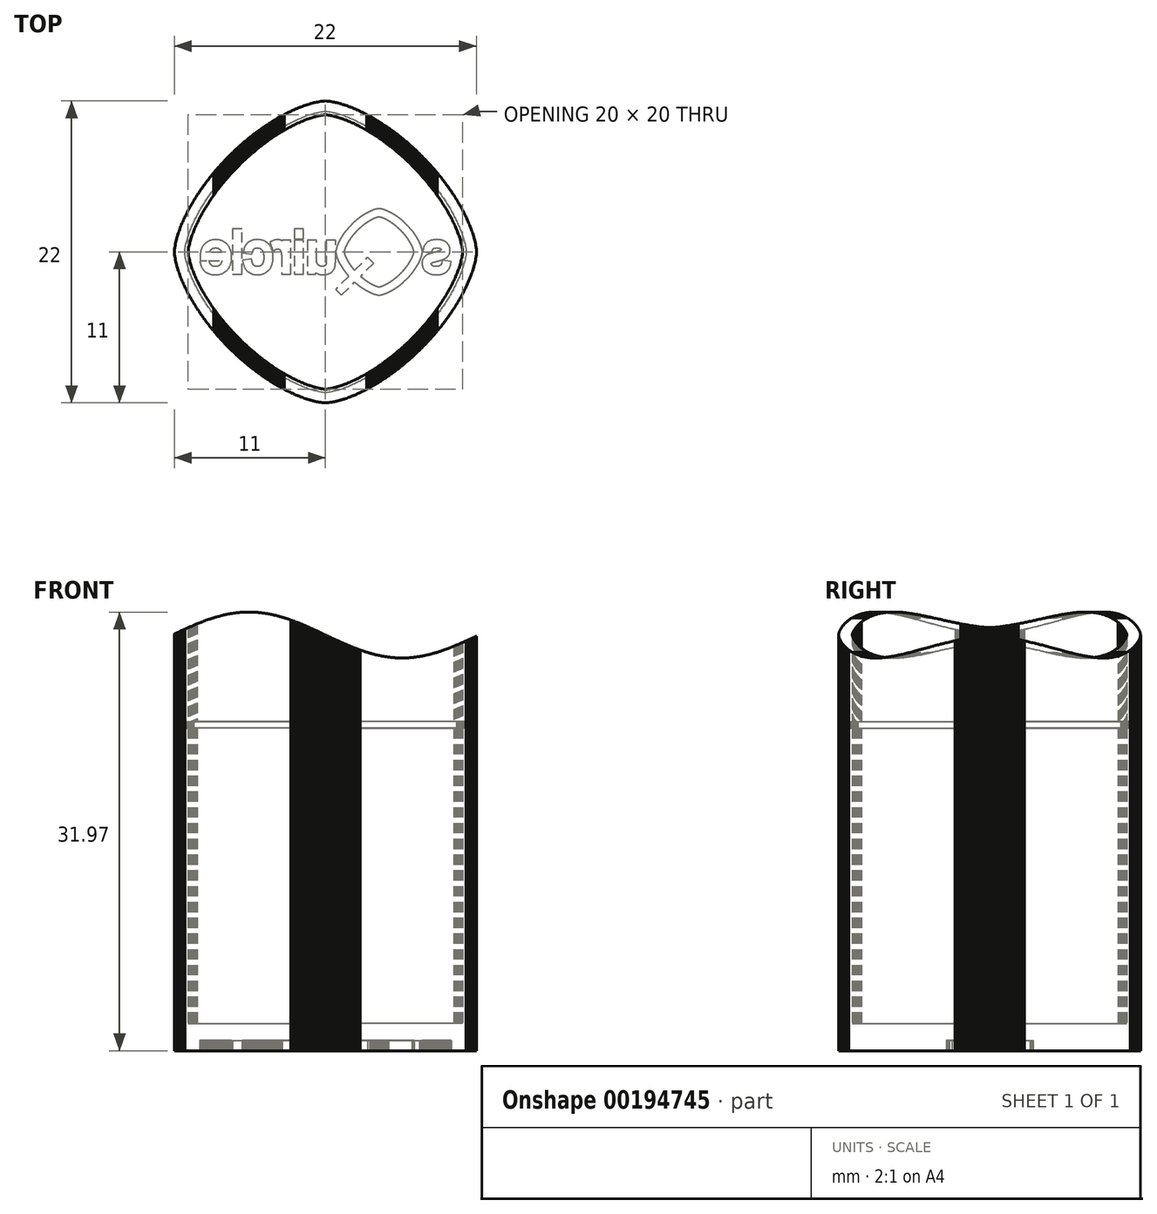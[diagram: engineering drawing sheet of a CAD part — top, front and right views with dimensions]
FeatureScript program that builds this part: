
annotation { "Feature Type Name" : "Feature", "Feature Type Description" : "" }
export const myFeature = defineFeature(function(context is Context, id is Id, definition is map)
    precondition{}
    {
        {
            var Q0;
            Q0=qCreatedBy(makeId("Top.planeOp"),FACE);
            var sketch = newSketch(context, id + "F0", { "sketchPlane" : qUnion([Q0])});
            skLineSegment(sketch, "E0", {"start": v(0, 10) * mm, "end": v(0.1, 10) * mm});
            skLineSegment(sketch, "E1", {"start": v(0.1, 10) * mm, "end": v(0.2, 9.98) * mm});
            skLineSegment(sketch, "E2", {"start": v(0.2, 9.98) * mm, "end": v(0.3, 9.97) * mm});
            skLineSegment(sketch, "E3", {"start": v(0.3, 9.97) * mm, "end": v(0.4, 9.95) * mm});
            skLineSegment(sketch, "E4", {"start": v(0.4, 9.95) * mm, "end": v(0.5, 9.93) * mm});
            skLineSegment(sketch, "E5", {"start": v(0.5, 9.93) * mm, "end": v(0.6, 9.9) * mm});
            skLineSegment(sketch, "E6", {"start": v(0.6, 9.9) * mm, "end": v(0.7, 9.88) * mm});
            skLineSegment(sketch, "E7", {"start": v(0.7, 9.88) * mm, "end": v(0.8, 9.85) * mm});
            skLineSegment(sketch, "E8", {"start": v(0.8, 9.85) * mm, "end": v(0.9, 9.82) * mm});
            skLineSegment(sketch, "E9", {"start": v(0.9, 9.82) * mm, "end": v(1, 9.79) * mm});
            skLineSegment(sketch, "E10", {"start": v(1, 9.79) * mm, "end": v(1.1, 9.76) * mm});
            skLineSegment(sketch, "E11", {"start": v(1.1, 9.76) * mm, "end": v(1.2, 9.72) * mm});
            skLineSegment(sketch, "E12", {"start": v(1.2, 9.72) * mm, "end": v(1.3, 9.69) * mm});
            skLineSegment(sketch, "E13", {"start": v(1.3, 9.69) * mm, "end": v(1.4, 9.65) * mm});
            skLineSegment(sketch, "E14", {"start": v(1.4, 9.65) * mm, "end": v(1.5, 9.6) * mm});
            skLineSegment(sketch, "E15", {"start": v(1.5, 9.6) * mm, "end": v(1.6, 9.57) * mm});
            skLineSegment(sketch, "E16", {"start": v(1.6, 9.57) * mm, "end": v(1.7, 9.53) * mm});
            skLineSegment(sketch, "E17", {"start": v(1.7, 9.53) * mm, "end": v(1.8, 9.48) * mm});
            skLineSegment(sketch, "E18", {"start": v(1.8, 9.48) * mm, "end": v(1.9, 9.44) * mm});
            skLineSegment(sketch, "E19", {"start": v(1.9, 9.44) * mm, "end": v(2, 9.4) * mm});
            skLineSegment(sketch, "E20", {"start": v(2, 9.4) * mm, "end": v(2.1, 9.35) * mm});
            skLineSegment(sketch, "E21", {"start": v(2.1, 9.35) * mm, "end": v(2.2, 9.3) * mm});
            skLineSegment(sketch, "E22", {"start": v(2.2, 9.3) * mm, "end": v(2.3, 9.25) * mm});
            skLineSegment(sketch, "E23", {"start": v(2.3, 9.25) * mm, "end": v(2.4, 9.2) * mm});
            skLineSegment(sketch, "E24", {"start": v(2.4, 9.2) * mm, "end": v(2.5, 9.15) * mm});
            skLineSegment(sketch, "E25", {"start": v(2.5, 9.15) * mm, "end": v(2.6, 9.1) * mm});
            skLineSegment(sketch, "E26", {"start": v(2.6, 9.1) * mm, "end": v(2.7, 9.04) * mm});
            skLineSegment(sketch, "E27", {"start": v(2.7, 9.04) * mm, "end": v(2.8, 8.99) * mm});
            skLineSegment(sketch, "E28", {"start": v(2.8, 8.99) * mm, "end": v(2.9, 8.93) * mm});
            skLineSegment(sketch, "E29", {"start": v(2.9, 8.93) * mm, "end": v(3, 8.87) * mm});
            skLineSegment(sketch, "E30", {"start": v(3, 8.87) * mm, "end": v(3.1, 8.81) * mm});
            skLineSegment(sketch, "E31", {"start": v(3.1, 8.81) * mm, "end": v(3.2, 8.75) * mm});
            skLineSegment(sketch, "E32", {"start": v(3.2, 8.75) * mm, "end": v(3.3, 8.7) * mm});
            skLineSegment(sketch, "E33", {"start": v(3.3, 8.7) * mm, "end": v(3.4, 8.63) * mm});
            skLineSegment(sketch, "E34", {"start": v(3.4, 8.63) * mm, "end": v(3.5, 8.57) * mm});
            skLineSegment(sketch, "E35", {"start": v(3.5, 8.57) * mm, "end": v(3.6, 8.5) * mm});
            skLineSegment(sketch, "E36", {"start": v(3.6, 8.5) * mm, "end": v(3.7, 8.44) * mm});
            skLineSegment(sketch, "E37", {"start": v(3.7, 8.44) * mm, "end": v(3.8, 8.37) * mm});
            skLineSegment(sketch, "E38", {"start": v(3.8, 8.37) * mm, "end": v(3.9, 8.3) * mm});
            skLineSegment(sketch, "E39", {"start": v(3.9, 8.3) * mm, "end": v(4, 8.23) * mm});
            skLineSegment(sketch, "E40", {"start": v(4, 8.23) * mm, "end": v(4.1, 8.16) * mm});
            skLineSegment(sketch, "E41", {"start": v(4.1, 8.16) * mm, "end": v(4.2, 8.1) * mm});
            skLineSegment(sketch, "E42", {"start": v(4.2, 8.1) * mm, "end": v(4.3, 8.02) * mm});
            skLineSegment(sketch, "E43", {"start": v(4.3, 8.02) * mm, "end": v(4.4, 7.94) * mm});
            skLineSegment(sketch, "E44", {"start": v(4.4, 7.94) * mm, "end": v(4.5, 7.87) * mm});
            skLineSegment(sketch, "E45", {"start": v(4.5, 7.87) * mm, "end": v(4.6, 7.8) * mm});
            skLineSegment(sketch, "E46", {"start": v(4.6, 7.8) * mm, "end": v(4.7, 7.72) * mm});
            skLineSegment(sketch, "E47", {"start": v(4.7, 7.72) * mm, "end": v(4.8, 7.64) * mm});
            skLineSegment(sketch, "E48", {"start": v(4.8, 7.64) * mm, "end": v(4.9, 7.56) * mm});
            skLineSegment(sketch, "E49", {"start": v(4.9, 7.56) * mm, "end": v(5, 7.48) * mm});
            skLineSegment(sketch, "E50", {"start": v(5, 7.48) * mm, "end": v(5.1, 7.4) * mm});
            skLineSegment(sketch, "E51", {"start": v(5.1, 7.4) * mm, "end": v(5.2, 7.31) * mm});
            skLineSegment(sketch, "E52", {"start": v(5.2, 7.31) * mm, "end": v(5.3, 7.23) * mm});
            skLineSegment(sketch, "E53", {"start": v(5.3, 7.23) * mm, "end": v(5.4, 7.14) * mm});
            skLineSegment(sketch, "E54", {"start": v(5.4, 7.14) * mm, "end": v(5.5, 7.05) * mm});
            skLineSegment(sketch, "E55", {"start": v(5.5, 7.05) * mm, "end": v(5.6, 6.96) * mm});
            skLineSegment(sketch, "E56", {"start": v(5.6, 6.96) * mm, "end": v(5.7, 6.87) * mm});
            skLineSegment(sketch, "E57", {"start": v(5.7, 6.87) * mm, "end": v(5.8, 6.78) * mm});
            skLineSegment(sketch, "E58", {"start": v(5.8, 6.78) * mm, "end": v(5.9, 6.69) * mm});
            skLineSegment(sketch, "E59", {"start": v(5.9, 6.69) * mm, "end": v(6, 6.6) * mm});
            skLineSegment(sketch, "E60", {"start": v(6, 6.6) * mm, "end": v(6.1, 6.5) * mm});
            skLineSegment(sketch, "E61", {"start": v(6.1, 6.5) * mm, "end": v(6.2, 6.4) * mm});
            skLineSegment(sketch, "E62", {"start": v(6.2, 6.4) * mm, "end": v(6.3, 6.3) * mm});
            skLineSegment(sketch, "E63", {"start": v(6.3, 6.3) * mm, "end": v(6.4, 6.2) * mm});
            skLineSegment(sketch, "E64", {"start": v(6.4, 6.2) * mm, "end": v(6.5, 6.1) * mm});
            skLineSegment(sketch, "E65", {"start": v(6.5, 6.1) * mm, "end": v(6.6, 6) * mm});
            skLineSegment(sketch, "E66", {"start": v(6.6, 6) * mm, "end": v(6.69, 5.9) * mm});
            skLineSegment(sketch, "E67", {"start": v(6.69, 5.9) * mm, "end": v(6.78, 5.8) * mm});
            skLineSegment(sketch, "E68", {"start": v(6.78, 5.8) * mm, "end": v(6.87, 5.7) * mm});
            skLineSegment(sketch, "E69", {"start": v(6.87, 5.7) * mm, "end": v(6.96, 5.6) * mm});
            skLineSegment(sketch, "E70", {"start": v(6.96, 5.6) * mm, "end": v(7.05, 5.5) * mm});
            skLineSegment(sketch, "E71", {"start": v(7.05, 5.5) * mm, "end": v(7.14, 5.4) * mm});
            skLineSegment(sketch, "E72", {"start": v(7.14, 5.4) * mm, "end": v(7.23, 5.3) * mm});
            skLineSegment(sketch, "E73", {"start": v(7.23, 5.3) * mm, "end": v(7.31, 5.2) * mm});
            skLineSegment(sketch, "E74", {"start": v(7.31, 5.2) * mm, "end": v(7.4, 5.1) * mm});
            skLineSegment(sketch, "E75", {"start": v(7.4, 5.1) * mm, "end": v(7.48, 5) * mm});
            skLineSegment(sketch, "E76", {"start": v(7.48, 5) * mm, "end": v(7.56, 4.9) * mm});
            skLineSegment(sketch, "E77", {"start": v(7.56, 4.9) * mm, "end": v(7.64, 4.8) * mm});
            skLineSegment(sketch, "E78", {"start": v(7.64, 4.8) * mm, "end": v(7.72, 4.7) * mm});
            skLineSegment(sketch, "E79", {"start": v(7.72, 4.7) * mm, "end": v(7.8, 4.6) * mm});
            skLineSegment(sketch, "E80", {"start": v(7.8, 4.6) * mm, "end": v(7.87, 4.5) * mm});
            skLineSegment(sketch, "E81", {"start": v(7.87, 4.5) * mm, "end": v(7.94, 4.4) * mm});
            skLineSegment(sketch, "E82", {"start": v(7.94, 4.4) * mm, "end": v(8.02, 4.3) * mm});
            skLineSegment(sketch, "E83", {"start": v(8.02, 4.3) * mm, "end": v(8.1, 4.2) * mm});
            skLineSegment(sketch, "E84", {"start": v(8.1, 4.2) * mm, "end": v(8.16, 4.1) * mm});
            skLineSegment(sketch, "E85", {"start": v(8.16, 4.1) * mm, "end": v(8.23, 4) * mm});
            skLineSegment(sketch, "E86", {"start": v(8.23, 4) * mm, "end": v(8.3, 3.9) * mm});
            skLineSegment(sketch, "E87", {"start": v(8.3, 3.9) * mm, "end": v(8.37, 3.8) * mm});
            skLineSegment(sketch, "E88", {"start": v(8.37, 3.8) * mm, "end": v(8.44, 3.7) * mm});
            skLineSegment(sketch, "E89", {"start": v(8.44, 3.7) * mm, "end": v(8.5, 3.6) * mm});
            skLineSegment(sketch, "E90", {"start": v(8.5, 3.6) * mm, "end": v(8.57, 3.5) * mm});
            skLineSegment(sketch, "E91", {"start": v(8.57, 3.5) * mm, "end": v(8.63, 3.4) * mm});
            skLineSegment(sketch, "E92", {"start": v(8.63, 3.4) * mm, "end": v(8.7, 3.3) * mm});
            skLineSegment(sketch, "E93", {"start": v(8.7, 3.3) * mm, "end": v(8.75, 3.2) * mm});
            skLineSegment(sketch, "E94", {"start": v(8.75, 3.2) * mm, "end": v(8.81, 3.1) * mm});
            skLineSegment(sketch, "E95", {"start": v(8.81, 3.1) * mm, "end": v(8.87, 3) * mm});
            skLineSegment(sketch, "E96", {"start": v(8.87, 3) * mm, "end": v(8.93, 2.9) * mm});
            skLineSegment(sketch, "E97", {"start": v(8.93, 2.9) * mm, "end": v(8.99, 2.8) * mm});
            skLineSegment(sketch, "E98", {"start": v(8.99, 2.8) * mm, "end": v(9.04, 2.7) * mm});
            skLineSegment(sketch, "E99", {"start": v(9.04, 2.7) * mm, "end": v(9.1, 2.6) * mm});
            skLineSegment(sketch, "E100", {"start": v(9.1, 2.6) * mm, "end": v(9.15, 2.5) * mm});
            skLineSegment(sketch, "E101", {"start": v(9.15, 2.5) * mm, "end": v(9.2, 2.4) * mm});
            skLineSegment(sketch, "E102", {"start": v(9.2, 2.4) * mm, "end": v(9.25, 2.3) * mm});
            skLineSegment(sketch, "E103", {"start": v(9.25, 2.3) * mm, "end": v(9.3, 2.2) * mm});
            skLineSegment(sketch, "E104", {"start": v(9.3, 2.2) * mm, "end": v(9.35, 2.1) * mm});
            skLineSegment(sketch, "E105", {"start": v(9.35, 2.1) * mm, "end": v(9.4, 2) * mm});
            skLineSegment(sketch, "E106", {"start": v(9.4, 2) * mm, "end": v(9.44, 1.9) * mm});
            skLineSegment(sketch, "E107", {"start": v(9.44, 1.9) * mm, "end": v(9.48, 1.8) * mm});
            skLineSegment(sketch, "E108", {"start": v(9.48, 1.8) * mm, "end": v(9.53, 1.7) * mm});
            skLineSegment(sketch, "E109", {"start": v(9.53, 1.7) * mm, "end": v(9.57, 1.6) * mm});
            skLineSegment(sketch, "E110", {"start": v(9.57, 1.6) * mm, "end": v(9.6, 1.5) * mm});
            skLineSegment(sketch, "E111", {"start": v(9.6, 1.5) * mm, "end": v(9.65, 1.4) * mm});
            skLineSegment(sketch, "E112", {"start": v(9.65, 1.4) * mm, "end": v(9.69, 1.3) * mm});
            skLineSegment(sketch, "E113", {"start": v(9.69, 1.3) * mm, "end": v(9.72, 1.2) * mm});
            skLineSegment(sketch, "E114", {"start": v(9.72, 1.2) * mm, "end": v(9.76, 1.1) * mm});
            skLineSegment(sketch, "E115", {"start": v(9.76, 1.1) * mm, "end": v(9.79, 1) * mm});
            skLineSegment(sketch, "E116", {"start": v(9.79, 1) * mm, "end": v(9.82, 0.9) * mm});
            skLineSegment(sketch, "E117", {"start": v(9.82, 0.9) * mm, "end": v(9.85, 0.8) * mm});
            skLineSegment(sketch, "E118", {"start": v(9.85, 0.8) * mm, "end": v(9.88, 0.7) * mm});
            skLineSegment(sketch, "E119", {"start": v(9.88, 0.7) * mm, "end": v(9.9, 0.6) * mm});
            skLineSegment(sketch, "E120", {"start": v(9.9, 0.6) * mm, "end": v(9.93, 0.5) * mm});
            skLineSegment(sketch, "E121", {"start": v(9.93, 0.5) * mm, "end": v(9.95, 0.4) * mm});
            skLineSegment(sketch, "E122", {"start": v(9.95, 0.4) * mm, "end": v(9.97, 0.3) * mm});
            skLineSegment(sketch, "E123", {"start": v(9.97, 0.3) * mm, "end": v(9.98, 0.2) * mm});
            skLineSegment(sketch, "E124", {"start": v(9.98, 0.2) * mm, "end": v(10, 0.1) * mm});
            skLineSegment(sketch, "E125", {"start": v(10, 0.1) * mm, "end": v(10, 0) * mm});
            skLineSegment(sketch, "E126", {"start": v(10, 0) * mm, "end": v(10, -0.1) * mm});
            skLineSegment(sketch, "E127", {"start": v(10, -0.1) * mm, "end": v(9.98, -0.2) * mm});
            skLineSegment(sketch, "E128", {"start": v(9.98, -0.2) * mm, "end": v(9.97, -0.3) * mm});
            skLineSegment(sketch, "E129", {"start": v(9.97, -0.3) * mm, "end": v(9.95, -0.4) * mm});
            skLineSegment(sketch, "E130", {"start": v(9.95, -0.4) * mm, "end": v(9.93, -0.5) * mm});
            skLineSegment(sketch, "E131", {"start": v(9.93, -0.5) * mm, "end": v(9.9, -0.6) * mm});
            skLineSegment(sketch, "E132", {"start": v(9.9, -0.6) * mm, "end": v(9.88, -0.7) * mm});
            skLineSegment(sketch, "E133", {"start": v(9.88, -0.7) * mm, "end": v(9.85, -0.8) * mm});
            skLineSegment(sketch, "E134", {"start": v(9.85, -0.8) * mm, "end": v(9.82, -0.9) * mm});
            skLineSegment(sketch, "E135", {"start": v(9.82, -0.9) * mm, "end": v(9.79, -1) * mm});
            skLineSegment(sketch, "E136", {"start": v(9.79, -1) * mm, "end": v(9.76, -1.1) * mm});
            skLineSegment(sketch, "E137", {"start": v(9.76, -1.1) * mm, "end": v(9.72, -1.2) * mm});
            skLineSegment(sketch, "E138", {"start": v(9.72, -1.2) * mm, "end": v(9.69, -1.3) * mm});
            skLineSegment(sketch, "E139", {"start": v(9.69, -1.3) * mm, "end": v(9.65, -1.4) * mm});
            skLineSegment(sketch, "E140", {"start": v(9.65, -1.4) * mm, "end": v(9.6, -1.5) * mm});
            skLineSegment(sketch, "E141", {"start": v(9.6, -1.5) * mm, "end": v(9.57, -1.6) * mm});
            skLineSegment(sketch, "E142", {"start": v(9.57, -1.6) * mm, "end": v(9.53, -1.7) * mm});
            skLineSegment(sketch, "E143", {"start": v(9.53, -1.7) * mm, "end": v(9.48, -1.8) * mm});
            skLineSegment(sketch, "E144", {"start": v(9.48, -1.8) * mm, "end": v(9.44, -1.9) * mm});
            skLineSegment(sketch, "E145", {"start": v(9.44, -1.9) * mm, "end": v(9.4, -2) * mm});
            skLineSegment(sketch, "E146", {"start": v(9.4, -2) * mm, "end": v(9.35, -2.1) * mm});
            skLineSegment(sketch, "E147", {"start": v(9.35, -2.1) * mm, "end": v(9.3, -2.2) * mm});
            skLineSegment(sketch, "E148", {"start": v(9.3, -2.2) * mm, "end": v(9.25, -2.3) * mm});
            skLineSegment(sketch, "E149", {"start": v(9.25, -2.3) * mm, "end": v(9.2, -2.4) * mm});
            skLineSegment(sketch, "E150", {"start": v(9.2, -2.4) * mm, "end": v(9.15, -2.5) * mm});
            skLineSegment(sketch, "E151", {"start": v(9.15, -2.5) * mm, "end": v(9.1, -2.6) * mm});
            skLineSegment(sketch, "E152", {"start": v(9.1, -2.6) * mm, "end": v(9.04, -2.7) * mm});
            skLineSegment(sketch, "E153", {"start": v(9.04, -2.7) * mm, "end": v(8.99, -2.8) * mm});
            skLineSegment(sketch, "E154", {"start": v(8.99, -2.8) * mm, "end": v(8.93, -2.9) * mm});
            skLineSegment(sketch, "E155", {"start": v(8.93, -2.9) * mm, "end": v(8.87, -3) * mm});
            skLineSegment(sketch, "E156", {"start": v(8.87, -3) * mm, "end": v(8.81, -3.1) * mm});
            skLineSegment(sketch, "E157", {"start": v(8.81, -3.1) * mm, "end": v(8.75, -3.2) * mm});
            skLineSegment(sketch, "E158", {"start": v(8.75, -3.2) * mm, "end": v(8.7, -3.3) * mm});
            skLineSegment(sketch, "E159", {"start": v(8.7, -3.3) * mm, "end": v(8.63, -3.4) * mm});
            skLineSegment(sketch, "E160", {"start": v(8.63, -3.4) * mm, "end": v(8.57, -3.5) * mm});
            skLineSegment(sketch, "E161", {"start": v(8.57, -3.5) * mm, "end": v(8.5, -3.6) * mm});
            skLineSegment(sketch, "E162", {"start": v(8.5, -3.6) * mm, "end": v(8.44, -3.7) * mm});
            skLineSegment(sketch, "E163", {"start": v(8.44, -3.7) * mm, "end": v(8.37, -3.8) * mm});
            skLineSegment(sketch, "E164", {"start": v(8.37, -3.8) * mm, "end": v(8.3, -3.9) * mm});
            skLineSegment(sketch, "E165", {"start": v(8.3, -3.9) * mm, "end": v(8.23, -4) * mm});
            skLineSegment(sketch, "E166", {"start": v(8.23, -4) * mm, "end": v(8.16, -4.1) * mm});
            skLineSegment(sketch, "E167", {"start": v(8.16, -4.1) * mm, "end": v(8.1, -4.2) * mm});
            skLineSegment(sketch, "E168", {"start": v(8.1, -4.2) * mm, "end": v(8.02, -4.3) * mm});
            skLineSegment(sketch, "E169", {"start": v(8.02, -4.3) * mm, "end": v(7.94, -4.4) * mm});
            skLineSegment(sketch, "E170", {"start": v(7.94, -4.4) * mm, "end": v(7.87, -4.5) * mm});
            skLineSegment(sketch, "E171", {"start": v(7.87, -4.5) * mm, "end": v(7.8, -4.6) * mm});
            skLineSegment(sketch, "E172", {"start": v(7.8, -4.6) * mm, "end": v(7.72, -4.7) * mm});
            skLineSegment(sketch, "E173", {"start": v(7.72, -4.7) * mm, "end": v(7.64, -4.8) * mm});
            skLineSegment(sketch, "E174", {"start": v(7.64, -4.8) * mm, "end": v(7.56, -4.9) * mm});
            skLineSegment(sketch, "E175", {"start": v(7.56, -4.9) * mm, "end": v(7.48, -5) * mm});
            skLineSegment(sketch, "E176", {"start": v(7.48, -5) * mm, "end": v(7.4, -5.1) * mm});
            skLineSegment(sketch, "E177", {"start": v(7.4, -5.1) * mm, "end": v(7.31, -5.2) * mm});
            skLineSegment(sketch, "E178", {"start": v(7.31, -5.2) * mm, "end": v(7.23, -5.3) * mm});
            skLineSegment(sketch, "E179", {"start": v(7.23, -5.3) * mm, "end": v(7.14, -5.4) * mm});
            skLineSegment(sketch, "E180", {"start": v(7.14, -5.4) * mm, "end": v(7.05, -5.5) * mm});
            skLineSegment(sketch, "E181", {"start": v(7.05, -5.5) * mm, "end": v(6.96, -5.6) * mm});
            skLineSegment(sketch, "E182", {"start": v(6.96, -5.6) * mm, "end": v(6.87, -5.7) * mm});
            skLineSegment(sketch, "E183", {"start": v(6.87, -5.7) * mm, "end": v(6.78, -5.8) * mm});
            skLineSegment(sketch, "E184", {"start": v(6.78, -5.8) * mm, "end": v(6.69, -5.9) * mm});
            skLineSegment(sketch, "E185", {"start": v(6.69, -5.9) * mm, "end": v(6.6, -6) * mm});
            skLineSegment(sketch, "E186", {"start": v(6.6, -6) * mm, "end": v(6.5, -6.1) * mm});
            skLineSegment(sketch, "E187", {"start": v(6.5, -6.1) * mm, "end": v(6.4, -6.2) * mm});
            skLineSegment(sketch, "E188", {"start": v(6.4, -6.2) * mm, "end": v(6.3, -6.3) * mm});
            skLineSegment(sketch, "E189", {"start": v(6.3, -6.3) * mm, "end": v(6.2, -6.4) * mm});
            skLineSegment(sketch, "E190", {"start": v(6.2, -6.4) * mm, "end": v(6.1, -6.5) * mm});
            skLineSegment(sketch, "E191", {"start": v(6.1, -6.5) * mm, "end": v(6, -6.6) * mm});
            skLineSegment(sketch, "E192", {"start": v(6, -6.6) * mm, "end": v(5.9, -6.69) * mm});
            skLineSegment(sketch, "E193", {"start": v(5.9, -6.69) * mm, "end": v(5.8, -6.78) * mm});
            skLineSegment(sketch, "E194", {"start": v(5.8, -6.78) * mm, "end": v(5.7, -6.87) * mm});
            skLineSegment(sketch, "E195", {"start": v(5.7, -6.87) * mm, "end": v(5.6, -6.96) * mm});
            skLineSegment(sketch, "E196", {"start": v(5.6, -6.96) * mm, "end": v(5.5, -7.05) * mm});
            skLineSegment(sketch, "E197", {"start": v(5.5, -7.05) * mm, "end": v(5.4, -7.14) * mm});
            skLineSegment(sketch, "E198", {"start": v(5.4, -7.14) * mm, "end": v(5.3, -7.23) * mm});
            skLineSegment(sketch, "E199", {"start": v(5.3, -7.23) * mm, "end": v(5.2, -7.31) * mm});
            skLineSegment(sketch, "E200", {"start": v(5.2, -7.31) * mm, "end": v(5.1, -7.4) * mm});
            skLineSegment(sketch, "E201", {"start": v(5.1, -7.4) * mm, "end": v(5, -7.48) * mm});
            skLineSegment(sketch, "E202", {"start": v(5, -7.48) * mm, "end": v(4.9, -7.56) * mm});
            skLineSegment(sketch, "E203", {"start": v(4.9, -7.56) * mm, "end": v(4.8, -7.64) * mm});
            skLineSegment(sketch, "E204", {"start": v(4.8, -7.64) * mm, "end": v(4.7, -7.72) * mm});
            skLineSegment(sketch, "E205", {"start": v(4.7, -7.72) * mm, "end": v(4.6, -7.8) * mm});
            skLineSegment(sketch, "E206", {"start": v(4.6, -7.8) * mm, "end": v(4.5, -7.87) * mm});
            skLineSegment(sketch, "E207", {"start": v(4.5, -7.87) * mm, "end": v(4.4, -7.94) * mm});
            skLineSegment(sketch, "E208", {"start": v(4.4, -7.94) * mm, "end": v(4.3, -8.02) * mm});
            skLineSegment(sketch, "E209", {"start": v(4.3, -8.02) * mm, "end": v(4.2, -8.1) * mm});
            skLineSegment(sketch, "E210", {"start": v(4.2, -8.1) * mm, "end": v(4.1, -8.16) * mm});
            skLineSegment(sketch, "E211", {"start": v(4.1, -8.16) * mm, "end": v(4, -8.23) * mm});
            skLineSegment(sketch, "E212", {"start": v(4, -8.23) * mm, "end": v(3.9, -8.3) * mm});
            skLineSegment(sketch, "E213", {"start": v(3.9, -8.3) * mm, "end": v(3.8, -8.37) * mm});
            skLineSegment(sketch, "E214", {"start": v(3.8, -8.37) * mm, "end": v(3.7, -8.44) * mm});
            skLineSegment(sketch, "E215", {"start": v(3.7, -8.44) * mm, "end": v(3.6, -8.5) * mm});
            skLineSegment(sketch, "E216", {"start": v(3.6, -8.5) * mm, "end": v(3.5, -8.57) * mm});
            skLineSegment(sketch, "E217", {"start": v(3.5, -8.57) * mm, "end": v(3.4, -8.63) * mm});
            skLineSegment(sketch, "E218", {"start": v(3.4, -8.63) * mm, "end": v(3.3, -8.7) * mm});
            skLineSegment(sketch, "E219", {"start": v(3.3, -8.7) * mm, "end": v(3.2, -8.75) * mm});
            skLineSegment(sketch, "E220", {"start": v(3.2, -8.75) * mm, "end": v(3.1, -8.81) * mm});
            skLineSegment(sketch, "E221", {"start": v(3.1, -8.81) * mm, "end": v(3, -8.87) * mm});
            skLineSegment(sketch, "E222", {"start": v(3, -8.87) * mm, "end": v(2.9, -8.93) * mm});
            skLineSegment(sketch, "E223", {"start": v(2.9, -8.93) * mm, "end": v(2.8, -8.99) * mm});
            skLineSegment(sketch, "E224", {"start": v(2.8, -8.99) * mm, "end": v(2.7, -9.04) * mm});
            skLineSegment(sketch, "E225", {"start": v(2.7, -9.04) * mm, "end": v(2.6, -9.1) * mm});
            skLineSegment(sketch, "E226", {"start": v(2.6, -9.1) * mm, "end": v(2.5, -9.15) * mm});
            skLineSegment(sketch, "E227", {"start": v(2.5, -9.15) * mm, "end": v(2.4, -9.2) * mm});
            skLineSegment(sketch, "E228", {"start": v(2.4, -9.2) * mm, "end": v(2.3, -9.25) * mm});
            skLineSegment(sketch, "E229", {"start": v(2.3, -9.25) * mm, "end": v(2.2, -9.3) * mm});
            skLineSegment(sketch, "E230", {"start": v(2.2, -9.3) * mm, "end": v(2.1, -9.35) * mm});
            skLineSegment(sketch, "E231", {"start": v(2.1, -9.35) * mm, "end": v(2, -9.4) * mm});
            skLineSegment(sketch, "E232", {"start": v(2, -9.4) * mm, "end": v(1.9, -9.44) * mm});
            skLineSegment(sketch, "E233", {"start": v(1.9, -9.44) * mm, "end": v(1.8, -9.48) * mm});
            skLineSegment(sketch, "E234", {"start": v(1.8, -9.48) * mm, "end": v(1.7, -9.53) * mm});
            skLineSegment(sketch, "E235", {"start": v(1.7, -9.53) * mm, "end": v(1.6, -9.57) * mm});
            skLineSegment(sketch, "E236", {"start": v(1.6, -9.57) * mm, "end": v(1.5, -9.6) * mm});
            skLineSegment(sketch, "E237", {"start": v(1.5, -9.6) * mm, "end": v(1.4, -9.65) * mm});
            skLineSegment(sketch, "E238", {"start": v(1.4, -9.65) * mm, "end": v(1.3, -9.69) * mm});
            skLineSegment(sketch, "E239", {"start": v(1.3, -9.69) * mm, "end": v(1.2, -9.72) * mm});
            skLineSegment(sketch, "E240", {"start": v(1.2, -9.72) * mm, "end": v(1.1, -9.76) * mm});
            skLineSegment(sketch, "E241", {"start": v(1.1, -9.76) * mm, "end": v(1, -9.79) * mm});
            skLineSegment(sketch, "E242", {"start": v(1, -9.79) * mm, "end": v(0.9, -9.82) * mm});
            skLineSegment(sketch, "E243", {"start": v(0.9, -9.82) * mm, "end": v(0.8, -9.85) * mm});
            skLineSegment(sketch, "E244", {"start": v(0.8, -9.85) * mm, "end": v(0.7, -9.88) * mm});
            skLineSegment(sketch, "E245", {"start": v(0.7, -9.88) * mm, "end": v(0.6, -9.9) * mm});
            skLineSegment(sketch, "E246", {"start": v(0.6, -9.9) * mm, "end": v(0.5, -9.93) * mm});
            skLineSegment(sketch, "E247", {"start": v(0.5, -9.93) * mm, "end": v(0.4, -9.95) * mm});
            skLineSegment(sketch, "E248", {"start": v(0.4, -9.95) * mm, "end": v(0.3, -9.97) * mm});
            skLineSegment(sketch, "E249", {"start": v(0.3, -9.97) * mm, "end": v(0.2, -9.98) * mm});
            skLineSegment(sketch, "E250", {"start": v(0.2, -9.98) * mm, "end": v(0.1, -10) * mm});
            skLineSegment(sketch, "E251", {"start": v(0.1, -10) * mm, "end": v(0, -10) * mm});
            skLineSegment(sketch, "E252", {"start": v(0, -10) * mm, "end": v(-0.1, -10) * mm});
            skLineSegment(sketch, "E253", {"start": v(-0.1, -10) * mm, "end": v(-0.2, -9.98) * mm});
            skLineSegment(sketch, "E254", {"start": v(-0.2, -9.98) * mm, "end": v(-0.3, -9.97) * mm});
            skLineSegment(sketch, "E255", {"start": v(-0.3, -9.97) * mm, "end": v(-0.4, -9.95) * mm});
            skLineSegment(sketch, "E256", {"start": v(-0.4, -9.95) * mm, "end": v(-0.5, -9.93) * mm});
            skLineSegment(sketch, "E257", {"start": v(-0.5, -9.93) * mm, "end": v(-0.6, -9.9) * mm});
            skLineSegment(sketch, "E258", {"start": v(-0.6, -9.9) * mm, "end": v(-0.7, -9.88) * mm});
            skLineSegment(sketch, "E259", {"start": v(-0.7, -9.88) * mm, "end": v(-0.8, -9.85) * mm});
            skLineSegment(sketch, "E260", {"start": v(-0.8, -9.85) * mm, "end": v(-0.9, -9.82) * mm});
            skLineSegment(sketch, "E261", {"start": v(-0.9, -9.82) * mm, "end": v(-1, -9.79) * mm});
            skLineSegment(sketch, "E262", {"start": v(-1, -9.79) * mm, "end": v(-1.1, -9.76) * mm});
            skLineSegment(sketch, "E263", {"start": v(-1.1, -9.76) * mm, "end": v(-1.2, -9.72) * mm});
            skLineSegment(sketch, "E264", {"start": v(-1.2, -9.72) * mm, "end": v(-1.3, -9.69) * mm});
            skLineSegment(sketch, "E265", {"start": v(-1.3, -9.69) * mm, "end": v(-1.4, -9.65) * mm});
            skLineSegment(sketch, "E266", {"start": v(-1.4, -9.65) * mm, "end": v(-1.5, -9.6) * mm});
            skLineSegment(sketch, "E267", {"start": v(-1.5, -9.6) * mm, "end": v(-1.6, -9.57) * mm});
            skLineSegment(sketch, "E268", {"start": v(-1.6, -9.57) * mm, "end": v(-1.7, -9.53) * mm});
            skLineSegment(sketch, "E269", {"start": v(-1.7, -9.53) * mm, "end": v(-1.8, -9.48) * mm});
            skLineSegment(sketch, "E270", {"start": v(-1.8, -9.48) * mm, "end": v(-1.9, -9.44) * mm});
            skLineSegment(sketch, "E271", {"start": v(-1.9, -9.44) * mm, "end": v(-2, -9.4) * mm});
            skLineSegment(sketch, "E272", {"start": v(-2, -9.4) * mm, "end": v(-2.1, -9.35) * mm});
            skLineSegment(sketch, "E273", {"start": v(-2.1, -9.35) * mm, "end": v(-2.2, -9.3) * mm});
            skLineSegment(sketch, "E274", {"start": v(-2.2, -9.3) * mm, "end": v(-2.3, -9.25) * mm});
            skLineSegment(sketch, "E275", {"start": v(-2.3, -9.25) * mm, "end": v(-2.4, -9.2) * mm});
            skLineSegment(sketch, "E276", {"start": v(-2.4, -9.2) * mm, "end": v(-2.5, -9.15) * mm});
            skLineSegment(sketch, "E277", {"start": v(-2.5, -9.15) * mm, "end": v(-2.6, -9.1) * mm});
            skLineSegment(sketch, "E278", {"start": v(-2.6, -9.1) * mm, "end": v(-2.7, -9.04) * mm});
            skLineSegment(sketch, "E279", {"start": v(-2.7, -9.04) * mm, "end": v(-2.8, -8.99) * mm});
            skLineSegment(sketch, "E280", {"start": v(-2.8, -8.99) * mm, "end": v(-2.9, -8.93) * mm});
            skLineSegment(sketch, "E281", {"start": v(-2.9, -8.93) * mm, "end": v(-3, -8.87) * mm});
            skLineSegment(sketch, "E282", {"start": v(-3, -8.87) * mm, "end": v(-3.1, -8.81) * mm});
            skLineSegment(sketch, "E283", {"start": v(-3.1, -8.81) * mm, "end": v(-3.2, -8.75) * mm});
            skLineSegment(sketch, "E284", {"start": v(-3.2, -8.75) * mm, "end": v(-3.3, -8.7) * mm});
            skLineSegment(sketch, "E285", {"start": v(-3.3, -8.7) * mm, "end": v(-3.4, -8.63) * mm});
            skLineSegment(sketch, "E286", {"start": v(-3.4, -8.63) * mm, "end": v(-3.5, -8.57) * mm});
            skLineSegment(sketch, "E287", {"start": v(-3.5, -8.57) * mm, "end": v(-3.6, -8.5) * mm});
            skLineSegment(sketch, "E288", {"start": v(-3.6, -8.5) * mm, "end": v(-3.7, -8.44) * mm});
            skLineSegment(sketch, "E289", {"start": v(-3.7, -8.44) * mm, "end": v(-3.8, -8.37) * mm});
            skLineSegment(sketch, "E290", {"start": v(-3.8, -8.37) * mm, "end": v(-3.9, -8.3) * mm});
            skLineSegment(sketch, "E291", {"start": v(-3.9, -8.3) * mm, "end": v(-4, -8.23) * mm});
            skLineSegment(sketch, "E292", {"start": v(-4, -8.23) * mm, "end": v(-4.1, -8.16) * mm});
            skLineSegment(sketch, "E293", {"start": v(-4.1, -8.16) * mm, "end": v(-4.2, -8.1) * mm});
            skLineSegment(sketch, "E294", {"start": v(-4.2, -8.1) * mm, "end": v(-4.3, -8.02) * mm});
            skLineSegment(sketch, "E295", {"start": v(-4.3, -8.02) * mm, "end": v(-4.4, -7.94) * mm});
            skLineSegment(sketch, "E296", {"start": v(-4.4, -7.94) * mm, "end": v(-4.5, -7.87) * mm});
            skLineSegment(sketch, "E297", {"start": v(-4.5, -7.87) * mm, "end": v(-4.6, -7.8) * mm});
            skLineSegment(sketch, "E298", {"start": v(-4.6, -7.8) * mm, "end": v(-4.7, -7.72) * mm});
            skLineSegment(sketch, "E299", {"start": v(-4.7, -7.72) * mm, "end": v(-4.8, -7.64) * mm});
            skLineSegment(sketch, "E300", {"start": v(-4.8, -7.64) * mm, "end": v(-4.9, -7.56) * mm});
            skLineSegment(sketch, "E301", {"start": v(-4.9, -7.56) * mm, "end": v(-5, -7.48) * mm});
            skLineSegment(sketch, "E302", {"start": v(-5, -7.48) * mm, "end": v(-5.1, -7.4) * mm});
            skLineSegment(sketch, "E303", {"start": v(-5.1, -7.4) * mm, "end": v(-5.2, -7.31) * mm});
            skLineSegment(sketch, "E304", {"start": v(-5.2, -7.31) * mm, "end": v(-5.3, -7.23) * mm});
            skLineSegment(sketch, "E305", {"start": v(-5.3, -7.23) * mm, "end": v(-5.4, -7.14) * mm});
            skLineSegment(sketch, "E306", {"start": v(-5.4, -7.14) * mm, "end": v(-5.5, -7.05) * mm});
            skLineSegment(sketch, "E307", {"start": v(-5.5, -7.05) * mm, "end": v(-5.6, -6.96) * mm});
            skLineSegment(sketch, "E308", {"start": v(-5.6, -6.96) * mm, "end": v(-5.7, -6.87) * mm});
            skLineSegment(sketch, "E309", {"start": v(-5.7, -6.87) * mm, "end": v(-5.8, -6.78) * mm});
            skLineSegment(sketch, "E310", {"start": v(-5.8, -6.78) * mm, "end": v(-5.9, -6.69) * mm});
            skLineSegment(sketch, "E311", {"start": v(-5.9, -6.69) * mm, "end": v(-6, -6.6) * mm});
            skLineSegment(sketch, "E312", {"start": v(-6, -6.6) * mm, "end": v(-6.1, -6.5) * mm});
            skLineSegment(sketch, "E313", {"start": v(-6.1, -6.5) * mm, "end": v(-6.2, -6.4) * mm});
            skLineSegment(sketch, "E314", {"start": v(-6.2, -6.4) * mm, "end": v(-6.3, -6.3) * mm});
            skLineSegment(sketch, "E315", {"start": v(-6.3, -6.3) * mm, "end": v(-6.4, -6.2) * mm});
            skLineSegment(sketch, "E316", {"start": v(-6.4, -6.2) * mm, "end": v(-6.5, -6.1) * mm});
            skLineSegment(sketch, "E317", {"start": v(-6.5, -6.1) * mm, "end": v(-6.6, -6) * mm});
            skLineSegment(sketch, "E318", {"start": v(-6.6, -6) * mm, "end": v(-6.69, -5.9) * mm});
            skLineSegment(sketch, "E319", {"start": v(-6.69, -5.9) * mm, "end": v(-6.78, -5.8) * mm});
            skLineSegment(sketch, "E320", {"start": v(-6.78, -5.8) * mm, "end": v(-6.87, -5.7) * mm});
            skLineSegment(sketch, "E321", {"start": v(-6.87, -5.7) * mm, "end": v(-6.96, -5.6) * mm});
            skLineSegment(sketch, "E322", {"start": v(-6.96, -5.6) * mm, "end": v(-7.05, -5.5) * mm});
            skLineSegment(sketch, "E323", {"start": v(-7.05, -5.5) * mm, "end": v(-7.14, -5.4) * mm});
            skLineSegment(sketch, "E324", {"start": v(-7.14, -5.4) * mm, "end": v(-7.23, -5.3) * mm});
            skLineSegment(sketch, "E325", {"start": v(-7.23, -5.3) * mm, "end": v(-7.31, -5.2) * mm});
            skLineSegment(sketch, "E326", {"start": v(-7.31, -5.2) * mm, "end": v(-7.4, -5.1) * mm});
            skLineSegment(sketch, "E327", {"start": v(-7.4, -5.1) * mm, "end": v(-7.48, -5) * mm});
            skLineSegment(sketch, "E328", {"start": v(-7.48, -5) * mm, "end": v(-7.56, -4.9) * mm});
            skLineSegment(sketch, "E329", {"start": v(-7.56, -4.9) * mm, "end": v(-7.64, -4.8) * mm});
            skLineSegment(sketch, "E330", {"start": v(-7.64, -4.8) * mm, "end": v(-7.72, -4.7) * mm});
            skLineSegment(sketch, "E331", {"start": v(-7.72, -4.7) * mm, "end": v(-7.8, -4.6) * mm});
            skLineSegment(sketch, "E332", {"start": v(-7.8, -4.6) * mm, "end": v(-7.87, -4.5) * mm});
            skLineSegment(sketch, "E333", {"start": v(-7.87, -4.5) * mm, "end": v(-7.94, -4.4) * mm});
            skLineSegment(sketch, "E334", {"start": v(-7.94, -4.4) * mm, "end": v(-8.02, -4.3) * mm});
            skLineSegment(sketch, "E335", {"start": v(-8.02, -4.3) * mm, "end": v(-8.1, -4.2) * mm});
            skLineSegment(sketch, "E336", {"start": v(-8.1, -4.2) * mm, "end": v(-8.16, -4.1) * mm});
            skLineSegment(sketch, "E337", {"start": v(-8.16, -4.1) * mm, "end": v(-8.23, -4) * mm});
            skLineSegment(sketch, "E338", {"start": v(-8.23, -4) * mm, "end": v(-8.3, -3.9) * mm});
            skLineSegment(sketch, "E339", {"start": v(-8.3, -3.9) * mm, "end": v(-8.37, -3.8) * mm});
            skLineSegment(sketch, "E340", {"start": v(-8.37, -3.8) * mm, "end": v(-8.44, -3.7) * mm});
            skLineSegment(sketch, "E341", {"start": v(-8.44, -3.7) * mm, "end": v(-8.5, -3.6) * mm});
            skLineSegment(sketch, "E342", {"start": v(-8.5, -3.6) * mm, "end": v(-8.57, -3.5) * mm});
            skLineSegment(sketch, "E343", {"start": v(-8.57, -3.5) * mm, "end": v(-8.63, -3.4) * mm});
            skLineSegment(sketch, "E344", {"start": v(-8.63, -3.4) * mm, "end": v(-8.7, -3.3) * mm});
            skLineSegment(sketch, "E345", {"start": v(-8.7, -3.3) * mm, "end": v(-8.75, -3.2) * mm});
            skLineSegment(sketch, "E346", {"start": v(-8.75, -3.2) * mm, "end": v(-8.81, -3.1) * mm});
            skLineSegment(sketch, "E347", {"start": v(-8.81, -3.1) * mm, "end": v(-8.87, -3) * mm});
            skLineSegment(sketch, "E348", {"start": v(-8.87, -3) * mm, "end": v(-8.93, -2.9) * mm});
            skLineSegment(sketch, "E349", {"start": v(-8.93, -2.9) * mm, "end": v(-8.99, -2.8) * mm});
            skLineSegment(sketch, "E350", {"start": v(-8.99, -2.8) * mm, "end": v(-9.04, -2.7) * mm});
            skLineSegment(sketch, "E351", {"start": v(-9.04, -2.7) * mm, "end": v(-9.1, -2.6) * mm});
            skLineSegment(sketch, "E352", {"start": v(-9.1, -2.6) * mm, "end": v(-9.15, -2.5) * mm});
            skLineSegment(sketch, "E353", {"start": v(-9.15, -2.5) * mm, "end": v(-9.2, -2.4) * mm});
            skLineSegment(sketch, "E354", {"start": v(-9.2, -2.4) * mm, "end": v(-9.25, -2.3) * mm});
            skLineSegment(sketch, "E355", {"start": v(-9.25, -2.3) * mm, "end": v(-9.3, -2.2) * mm});
            skLineSegment(sketch, "E356", {"start": v(-9.3, -2.2) * mm, "end": v(-9.35, -2.1) * mm});
            skLineSegment(sketch, "E357", {"start": v(-9.35, -2.1) * mm, "end": v(-9.4, -2) * mm});
            skLineSegment(sketch, "E358", {"start": v(-9.4, -2) * mm, "end": v(-9.44, -1.9) * mm});
            skLineSegment(sketch, "E359", {"start": v(-9.44, -1.9) * mm, "end": v(-9.48, -1.8) * mm});
            skLineSegment(sketch, "E360", {"start": v(-9.48, -1.8) * mm, "end": v(-9.53, -1.7) * mm});
            skLineSegment(sketch, "E361", {"start": v(-9.53, -1.7) * mm, "end": v(-9.57, -1.6) * mm});
            skLineSegment(sketch, "E362", {"start": v(-9.57, -1.6) * mm, "end": v(-9.6, -1.5) * mm});
            skLineSegment(sketch, "E363", {"start": v(-9.6, -1.5) * mm, "end": v(-9.65, -1.4) * mm});
            skLineSegment(sketch, "E364", {"start": v(-9.65, -1.4) * mm, "end": v(-9.69, -1.3) * mm});
            skLineSegment(sketch, "E365", {"start": v(-9.69, -1.3) * mm, "end": v(-9.72, -1.2) * mm});
            skLineSegment(sketch, "E366", {"start": v(-9.72, -1.2) * mm, "end": v(-9.76, -1.1) * mm});
            skLineSegment(sketch, "E367", {"start": v(-9.76, -1.1) * mm, "end": v(-9.79, -1) * mm});
            skLineSegment(sketch, "E368", {"start": v(-9.79, -1) * mm, "end": v(-9.82, -0.9) * mm});
            skLineSegment(sketch, "E369", {"start": v(-9.82, -0.9) * mm, "end": v(-9.85, -0.8) * mm});
            skLineSegment(sketch, "E370", {"start": v(-9.85, -0.8) * mm, "end": v(-9.88, -0.7) * mm});
            skLineSegment(sketch, "E371", {"start": v(-9.88, -0.7) * mm, "end": v(-9.9, -0.6) * mm});
            skLineSegment(sketch, "E372", {"start": v(-9.9, -0.6) * mm, "end": v(-9.93, -0.5) * mm});
            skLineSegment(sketch, "E373", {"start": v(-9.93, -0.5) * mm, "end": v(-9.95, -0.4) * mm});
            skLineSegment(sketch, "E374", {"start": v(-9.95, -0.4) * mm, "end": v(-9.97, -0.3) * mm});
            skLineSegment(sketch, "E375", {"start": v(-9.97, -0.3) * mm, "end": v(-9.98, -0.2) * mm});
            skLineSegment(sketch, "E376", {"start": v(-9.98, -0.2) * mm, "end": v(-10, -0.1) * mm});
            skLineSegment(sketch, "E377", {"start": v(-10, -0.1) * mm, "end": v(-10, 0) * mm});
            skLineSegment(sketch, "E378", {"start": v(-10, 0) * mm, "end": v(-10, 0.1) * mm});
            skLineSegment(sketch, "E379", {"start": v(-10, 0.1) * mm, "end": v(-9.98, 0.2) * mm});
            skLineSegment(sketch, "E380", {"start": v(-9.98, 0.2) * mm, "end": v(-9.97, 0.3) * mm});
            skLineSegment(sketch, "E381", {"start": v(-9.97, 0.3) * mm, "end": v(-9.95, 0.4) * mm});
            skLineSegment(sketch, "E382", {"start": v(-9.95, 0.4) * mm, "end": v(-9.93, 0.5) * mm});
            skLineSegment(sketch, "E383", {"start": v(-9.93, 0.5) * mm, "end": v(-9.9, 0.6) * mm});
            skLineSegment(sketch, "E384", {"start": v(-9.9, 0.6) * mm, "end": v(-9.88, 0.7) * mm});
            skLineSegment(sketch, "E385", {"start": v(-9.88, 0.7) * mm, "end": v(-9.85, 0.8) * mm});
            skLineSegment(sketch, "E386", {"start": v(-9.85, 0.8) * mm, "end": v(-9.82, 0.9) * mm});
            skLineSegment(sketch, "E387", {"start": v(-9.82, 0.9) * mm, "end": v(-9.79, 1) * mm});
            skLineSegment(sketch, "E388", {"start": v(-9.79, 1) * mm, "end": v(-9.76, 1.1) * mm});
            skLineSegment(sketch, "E389", {"start": v(-9.76, 1.1) * mm, "end": v(-9.72, 1.2) * mm});
            skLineSegment(sketch, "E390", {"start": v(-9.72, 1.2) * mm, "end": v(-9.69, 1.3) * mm});
            skLineSegment(sketch, "E391", {"start": v(-9.69, 1.3) * mm, "end": v(-9.65, 1.4) * mm});
            skLineSegment(sketch, "E392", {"start": v(-9.65, 1.4) * mm, "end": v(-9.6, 1.5) * mm});
            skLineSegment(sketch, "E393", {"start": v(-9.6, 1.5) * mm, "end": v(-9.57, 1.6) * mm});
            skLineSegment(sketch, "E394", {"start": v(-9.57, 1.6) * mm, "end": v(-9.53, 1.7) * mm});
            skLineSegment(sketch, "E395", {"start": v(-9.53, 1.7) * mm, "end": v(-9.48, 1.8) * mm});
            skLineSegment(sketch, "E396", {"start": v(-9.48, 1.8) * mm, "end": v(-9.44, 1.9) * mm});
            skLineSegment(sketch, "E397", {"start": v(-9.44, 1.9) * mm, "end": v(-9.4, 2) * mm});
            skLineSegment(sketch, "E398", {"start": v(-9.4, 2) * mm, "end": v(-9.35, 2.1) * mm});
            skLineSegment(sketch, "E399", {"start": v(-9.35, 2.1) * mm, "end": v(-9.3, 2.2) * mm});
            skLineSegment(sketch, "E400", {"start": v(-9.3, 2.2) * mm, "end": v(-9.25, 2.3) * mm});
            skLineSegment(sketch, "E401", {"start": v(-9.25, 2.3) * mm, "end": v(-9.2, 2.4) * mm});
            skLineSegment(sketch, "E402", {"start": v(-9.2, 2.4) * mm, "end": v(-9.15, 2.5) * mm});
            skLineSegment(sketch, "E403", {"start": v(-9.15, 2.5) * mm, "end": v(-9.1, 2.6) * mm});
            skLineSegment(sketch, "E404", {"start": v(-9.1, 2.6) * mm, "end": v(-9.04, 2.7) * mm});
            skLineSegment(sketch, "E405", {"start": v(-9.04, 2.7) * mm, "end": v(-8.99, 2.8) * mm});
            skLineSegment(sketch, "E406", {"start": v(-8.99, 2.8) * mm, "end": v(-8.93, 2.9) * mm});
            skLineSegment(sketch, "E407", {"start": v(-8.93, 2.9) * mm, "end": v(-8.87, 3) * mm});
            skLineSegment(sketch, "E408", {"start": v(-8.87, 3) * mm, "end": v(-8.81, 3.1) * mm});
            skLineSegment(sketch, "E409", {"start": v(-8.81, 3.1) * mm, "end": v(-8.75, 3.2) * mm});
            skLineSegment(sketch, "E410", {"start": v(-8.75, 3.2) * mm, "end": v(-8.7, 3.3) * mm});
            skLineSegment(sketch, "E411", {"start": v(-8.7, 3.3) * mm, "end": v(-8.63, 3.4) * mm});
            skLineSegment(sketch, "E412", {"start": v(-8.63, 3.4) * mm, "end": v(-8.57, 3.5) * mm});
            skLineSegment(sketch, "E413", {"start": v(-8.57, 3.5) * mm, "end": v(-8.5, 3.6) * mm});
            skLineSegment(sketch, "E414", {"start": v(-8.5, 3.6) * mm, "end": v(-8.44, 3.7) * mm});
            skLineSegment(sketch, "E415", {"start": v(-8.44, 3.7) * mm, "end": v(-8.37, 3.8) * mm});
            skLineSegment(sketch, "E416", {"start": v(-8.37, 3.8) * mm, "end": v(-8.3, 3.9) * mm});
            skLineSegment(sketch, "E417", {"start": v(-8.3, 3.9) * mm, "end": v(-8.23, 4) * mm});
            skLineSegment(sketch, "E418", {"start": v(-8.23, 4) * mm, "end": v(-8.16, 4.1) * mm});
            skLineSegment(sketch, "E419", {"start": v(-8.16, 4.1) * mm, "end": v(-8.1, 4.2) * mm});
            skLineSegment(sketch, "E420", {"start": v(-8.1, 4.2) * mm, "end": v(-8.02, 4.3) * mm});
            skLineSegment(sketch, "E421", {"start": v(-8.02, 4.3) * mm, "end": v(-7.94, 4.4) * mm});
            skLineSegment(sketch, "E422", {"start": v(-7.94, 4.4) * mm, "end": v(-7.87, 4.5) * mm});
            skLineSegment(sketch, "E423", {"start": v(-7.87, 4.5) * mm, "end": v(-7.8, 4.6) * mm});
            skLineSegment(sketch, "E424", {"start": v(-7.8, 4.6) * mm, "end": v(-7.72, 4.7) * mm});
            skLineSegment(sketch, "E425", {"start": v(-7.72, 4.7) * mm, "end": v(-7.64, 4.8) * mm});
            skLineSegment(sketch, "E426", {"start": v(-7.64, 4.8) * mm, "end": v(-7.56, 4.9) * mm});
            skLineSegment(sketch, "E427", {"start": v(-7.56, 4.9) * mm, "end": v(-7.48, 5) * mm});
            skLineSegment(sketch, "E428", {"start": v(-7.48, 5) * mm, "end": v(-7.4, 5.1) * mm});
            skLineSegment(sketch, "E429", {"start": v(-7.4, 5.1) * mm, "end": v(-7.31, 5.2) * mm});
            skLineSegment(sketch, "E430", {"start": v(-7.31, 5.2) * mm, "end": v(-7.23, 5.3) * mm});
            skLineSegment(sketch, "E431", {"start": v(-7.23, 5.3) * mm, "end": v(-7.14, 5.4) * mm});
            skLineSegment(sketch, "E432", {"start": v(-7.14, 5.4) * mm, "end": v(-7.05, 5.5) * mm});
            skLineSegment(sketch, "E433", {"start": v(-7.05, 5.5) * mm, "end": v(-6.96, 5.6) * mm});
            skLineSegment(sketch, "E434", {"start": v(-6.96, 5.6) * mm, "end": v(-6.87, 5.7) * mm});
            skLineSegment(sketch, "E435", {"start": v(-6.87, 5.7) * mm, "end": v(-6.78, 5.8) * mm});
            skLineSegment(sketch, "E436", {"start": v(-6.78, 5.8) * mm, "end": v(-6.69, 5.9) * mm});
            skLineSegment(sketch, "E437", {"start": v(-6.69, 5.9) * mm, "end": v(-6.6, 6) * mm});
            skLineSegment(sketch, "E438", {"start": v(-6.6, 6) * mm, "end": v(-6.5, 6.1) * mm});
            skLineSegment(sketch, "E439", {"start": v(-6.5, 6.1) * mm, "end": v(-6.4, 6.2) * mm});
            skLineSegment(sketch, "E440", {"start": v(-6.4, 6.2) * mm, "end": v(-6.3, 6.3) * mm});
            skLineSegment(sketch, "E441", {"start": v(-6.3, 6.3) * mm, "end": v(-6.2, 6.4) * mm});
            skLineSegment(sketch, "E442", {"start": v(-6.2, 6.4) * mm, "end": v(-6.1, 6.5) * mm});
            skLineSegment(sketch, "E443", {"start": v(-6.1, 6.5) * mm, "end": v(-6, 6.6) * mm});
            skLineSegment(sketch, "E444", {"start": v(-6, 6.6) * mm, "end": v(-5.9, 6.69) * mm});
            skLineSegment(sketch, "E445", {"start": v(-5.9, 6.69) * mm, "end": v(-5.8, 6.78) * mm});
            skLineSegment(sketch, "E446", {"start": v(-5.8, 6.78) * mm, "end": v(-5.7, 6.87) * mm});
            skLineSegment(sketch, "E447", {"start": v(-5.7, 6.87) * mm, "end": v(-5.6, 6.96) * mm});
            skLineSegment(sketch, "E448", {"start": v(-5.6, 6.96) * mm, "end": v(-5.5, 7.05) * mm});
            skLineSegment(sketch, "E449", {"start": v(-5.5, 7.05) * mm, "end": v(-5.4, 7.14) * mm});
            skLineSegment(sketch, "E450", {"start": v(-5.4, 7.14) * mm, "end": v(-5.3, 7.23) * mm});
            skLineSegment(sketch, "E451", {"start": v(-5.3, 7.23) * mm, "end": v(-5.2, 7.31) * mm});
            skLineSegment(sketch, "E452", {"start": v(-5.2, 7.31) * mm, "end": v(-5.1, 7.4) * mm});
            skLineSegment(sketch, "E453", {"start": v(-5.1, 7.4) * mm, "end": v(-5, 7.48) * mm});
            skLineSegment(sketch, "E454", {"start": v(-5, 7.48) * mm, "end": v(-4.9, 7.56) * mm});
            skLineSegment(sketch, "E455", {"start": v(-4.9, 7.56) * mm, "end": v(-4.8, 7.64) * mm});
            skLineSegment(sketch, "E456", {"start": v(-4.8, 7.64) * mm, "end": v(-4.7, 7.72) * mm});
            skLineSegment(sketch, "E457", {"start": v(-4.7, 7.72) * mm, "end": v(-4.6, 7.8) * mm});
            skLineSegment(sketch, "E458", {"start": v(-4.6, 7.8) * mm, "end": v(-4.5, 7.87) * mm});
            skLineSegment(sketch, "E459", {"start": v(-4.5, 7.87) * mm, "end": v(-4.4, 7.94) * mm});
            skLineSegment(sketch, "E460", {"start": v(-4.4, 7.94) * mm, "end": v(-4.3, 8.02) * mm});
            skLineSegment(sketch, "E461", {"start": v(-4.3, 8.02) * mm, "end": v(-4.2, 8.1) * mm});
            skLineSegment(sketch, "E462", {"start": v(-4.2, 8.1) * mm, "end": v(-4.1, 8.16) * mm});
            skLineSegment(sketch, "E463", {"start": v(-4.1, 8.16) * mm, "end": v(-4, 8.23) * mm});
            skLineSegment(sketch, "E464", {"start": v(-4, 8.23) * mm, "end": v(-3.9, 8.3) * mm});
            skLineSegment(sketch, "E465", {"start": v(-3.9, 8.3) * mm, "end": v(-3.8, 8.37) * mm});
            skLineSegment(sketch, "E466", {"start": v(-3.8, 8.37) * mm, "end": v(-3.7, 8.44) * mm});
            skLineSegment(sketch, "E467", {"start": v(-3.7, 8.44) * mm, "end": v(-3.6, 8.5) * mm});
            skLineSegment(sketch, "E468", {"start": v(-3.6, 8.5) * mm, "end": v(-3.5, 8.57) * mm});
            skLineSegment(sketch, "E469", {"start": v(-3.5, 8.57) * mm, "end": v(-3.4, 8.63) * mm});
            skLineSegment(sketch, "E470", {"start": v(-3.4, 8.63) * mm, "end": v(-3.3, 8.7) * mm});
            skLineSegment(sketch, "E471", {"start": v(-3.3, 8.7) * mm, "end": v(-3.2, 8.75) * mm});
            skLineSegment(sketch, "E472", {"start": v(-3.2, 8.75) * mm, "end": v(-3.1, 8.81) * mm});
            skLineSegment(sketch, "E473", {"start": v(-3.1, 8.81) * mm, "end": v(-3, 8.87) * mm});
            skLineSegment(sketch, "E474", {"start": v(-3, 8.87) * mm, "end": v(-2.9, 8.93) * mm});
            skLineSegment(sketch, "E475", {"start": v(-2.9, 8.93) * mm, "end": v(-2.8, 8.99) * mm});
            skLineSegment(sketch, "E476", {"start": v(-2.8, 8.99) * mm, "end": v(-2.7, 9.04) * mm});
            skLineSegment(sketch, "E477", {"start": v(-2.7, 9.04) * mm, "end": v(-2.6, 9.1) * mm});
            skLineSegment(sketch, "E478", {"start": v(-2.6, 9.1) * mm, "end": v(-2.5, 9.15) * mm});
            skLineSegment(sketch, "E479", {"start": v(-2.5, 9.15) * mm, "end": v(-2.4, 9.2) * mm});
            skLineSegment(sketch, "E480", {"start": v(-2.4, 9.2) * mm, "end": v(-2.3, 9.25) * mm});
            skLineSegment(sketch, "E481", {"start": v(-2.3, 9.25) * mm, "end": v(-2.2, 9.3) * mm});
            skLineSegment(sketch, "E482", {"start": v(-2.2, 9.3) * mm, "end": v(-2.1, 9.35) * mm});
            skLineSegment(sketch, "E483", {"start": v(-2.1, 9.35) * mm, "end": v(-2, 9.4) * mm});
            skLineSegment(sketch, "E484", {"start": v(-2, 9.4) * mm, "end": v(-1.9, 9.44) * mm});
            skLineSegment(sketch, "E485", {"start": v(-1.9, 9.44) * mm, "end": v(-1.8, 9.48) * mm});
            skLineSegment(sketch, "E486", {"start": v(-1.8, 9.48) * mm, "end": v(-1.7, 9.53) * mm});
            skLineSegment(sketch, "E487", {"start": v(-1.7, 9.53) * mm, "end": v(-1.6, 9.57) * mm});
            skLineSegment(sketch, "E488", {"start": v(-1.6, 9.57) * mm, "end": v(-1.5, 9.6) * mm});
            skLineSegment(sketch, "E489", {"start": v(-1.5, 9.6) * mm, "end": v(-1.4, 9.65) * mm});
            skLineSegment(sketch, "E490", {"start": v(-1.4, 9.65) * mm, "end": v(-1.3, 9.69) * mm});
            skLineSegment(sketch, "E491", {"start": v(-1.3, 9.69) * mm, "end": v(-1.2, 9.72) * mm});
            skLineSegment(sketch, "E492", {"start": v(-1.2, 9.72) * mm, "end": v(-1.1, 9.76) * mm});
            skLineSegment(sketch, "E493", {"start": v(-1.1, 9.76) * mm, "end": v(-1, 9.79) * mm});
            skLineSegment(sketch, "E494", {"start": v(-1, 9.79) * mm, "end": v(-0.9, 9.82) * mm});
            skLineSegment(sketch, "E495", {"start": v(-0.9, 9.82) * mm, "end": v(-0.8, 9.85) * mm});
            skLineSegment(sketch, "E496", {"start": v(-0.8, 9.85) * mm, "end": v(-0.7, 9.88) * mm});
            skLineSegment(sketch, "E497", {"start": v(-0.7, 9.88) * mm, "end": v(-0.6, 9.9) * mm});
            skLineSegment(sketch, "E498", {"start": v(-0.6, 9.9) * mm, "end": v(-0.5, 9.93) * mm});
            skLineSegment(sketch, "E499", {"start": v(-0.5, 9.93) * mm, "end": v(-0.4, 9.95) * mm});
            skLineSegment(sketch, "E500", {"start": v(-0.4, 9.95) * mm, "end": v(-0.3, 9.97) * mm});
            skLineSegment(sketch, "E501", {"start": v(-0.3, 9.97) * mm, "end": v(-0.2, 9.98) * mm});
            skLineSegment(sketch, "E502", {"start": v(-0.2, 9.98) * mm, "end": v(-0.1, 10) * mm});
            skLineSegment(sketch, "E503", {"start": v(-0.1, 10) * mm, "end": v(0, 10) * mm});
            skLineSegment(sketch, "E504.0", {"start": v(-7.42, 6.58) * mm, "end": v(-7.32, 6.7) * mm});
            skLineSegment(sketch, "E504.1", {"start": v(-7.51, 6.48) * mm, "end": v(-7.42, 6.58) * mm});
            skLineSegment(sketch, "E504.2", {"start": v(-7.61, 6.37) * mm, "end": v(-7.51, 6.48) * mm});
            skLineSegment(sketch, "E504.3", {"start": v(-7.7, 6.27) * mm, "end": v(-7.61, 6.37) * mm});
            skLineSegment(sketch, "E504.4", {"start": v(-7.8, 6.16) * mm, "end": v(-7.7, 6.27) * mm});
            skLineSegment(sketch, "E504.5", {"start": v(-7.9, 6.06) * mm, "end": v(-7.8, 6.16) * mm});
            skLineSegment(sketch, "E504.6", {"start": v(-7.98, 5.95) * mm, "end": v(-7.9, 6.06) * mm});
            skLineSegment(sketch, "E504.7", {"start": v(-8.07, 5.84) * mm, "end": v(-7.98, 5.95) * mm});
            skLineSegment(sketch, "E504.8", {"start": v(-8.16, 5.74) * mm, "end": v(-8.07, 5.84) * mm});
            skLineSegment(sketch, "E504.9", {"start": v(-8.25, 5.63) * mm, "end": v(-8.16, 5.74) * mm});
            skLineSegment(sketch, "E504.10", {"start": v(-8.34, 5.53) * mm, "end": v(-8.25, 5.63) * mm});
            skLineSegment(sketch, "E504.11", {"start": v(-8.42, 5.42) * mm, "end": v(-8.34, 5.53) * mm});
            skLineSegment(sketch, "E504.12", {"start": v(-8.5, 5.32) * mm, "end": v(-8.42, 5.42) * mm});
            skLineSegment(sketch, "E504.13", {"start": v(-8.59, 5.2) * mm, "end": v(-8.5, 5.32) * mm});
            skLineSegment(sketch, "E504.14", {"start": v(-8.67, 5.1) * mm, "end": v(-8.59, 5.2) * mm});
            skLineSegment(sketch, "E504.15", {"start": v(-8.75, 5) * mm, "end": v(-8.67, 5.1) * mm});
            skLineSegment(sketch, "E504.16", {"start": v(-8.83, 4.9) * mm, "end": v(-8.75, 5) * mm});
            skLineSegment(sketch, "E504.17", {"start": v(-8.9, 4.78) * mm, "end": v(-8.83, 4.9) * mm});
            skLineSegment(sketch, "E504.18", {"start": v(-8.98, 4.68) * mm, "end": v(-8.9, 4.78) * mm});
            skLineSegment(sketch, "E504.19", {"start": v(-9.05, 4.57) * mm, "end": v(-8.98, 4.68) * mm});
            skLineSegment(sketch, "E504.20", {"start": v(-9.13, 4.47) * mm, "end": v(-9.05, 4.57) * mm});
            skLineSegment(sketch, "E504.21", {"start": v(-9.2, 4.36) * mm, "end": v(-9.13, 4.47) * mm});
            skLineSegment(sketch, "E504.22", {"start": v(-9.27, 4.25) * mm, "end": v(-9.2, 4.36) * mm});
            skLineSegment(sketch, "E504.23", {"start": v(-9.34, 4.15) * mm, "end": v(-9.27, 4.25) * mm});
            skLineSegment(sketch, "E504.24", {"start": v(-9.4, 4.04) * mm, "end": v(-9.34, 4.15) * mm});
            skLineSegment(sketch, "E504.25", {"start": v(-9.48, 3.93) * mm, "end": v(-9.4, 4.04) * mm});
            skLineSegment(sketch, "E504.26", {"start": v(-9.54, 3.82) * mm, "end": v(-9.48, 3.93) * mm});
            skLineSegment(sketch, "E504.27", {"start": v(-9.6, 3.72) * mm, "end": v(-9.54, 3.82) * mm});
            skLineSegment(sketch, "E504.28", {"start": v(-9.67, 3.61) * mm, "end": v(-9.6, 3.72) * mm});
            skLineSegment(sketch, "E504.29", {"start": v(-9.74, 3.5) * mm, "end": v(-9.67, 3.61) * mm});
            skLineSegment(sketch, "E504.30", {"start": v(-9.8, 3.4) * mm, "end": v(-9.74, 3.5) * mm});
            skLineSegment(sketch, "E504.31", {"start": v(-9.86, 3.29) * mm, "end": v(-9.8, 3.4) * mm});
            skLineSegment(sketch, "E504.32", {"start": v(-9.92, 3.18) * mm, "end": v(-9.86, 3.29) * mm});
            skLineSegment(sketch, "E504.33", {"start": v(-9.98, 3.07) * mm, "end": v(-9.92, 3.18) * mm});
            skLineSegment(sketch, "E504.34", {"start": v(-10.03, 2.96) * mm, "end": v(-9.98, 3.07) * mm});
            skLineSegment(sketch, "E504.35", {"start": v(-10.1, 2.85) * mm, "end": v(-10.03, 2.96) * mm});
            skLineSegment(sketch, "E504.36", {"start": v(-10.15, 2.75) * mm, "end": v(-10.1, 2.85) * mm});
            skLineSegment(sketch, "E504.37", {"start": v(-10.2, 2.64) * mm, "end": v(-10.15, 2.75) * mm});
            skLineSegment(sketch, "E504.38", {"start": v(-10.25, 2.53) * mm, "end": v(-10.2, 2.64) * mm});
            skLineSegment(sketch, "E504.39", {"start": v(-10.3, 2.42) * mm, "end": v(-10.25, 2.53) * mm});
            skLineSegment(sketch, "E504.40", {"start": v(-10.35, 2.3) * mm, "end": v(-10.3, 2.42) * mm});
            skLineSegment(sketch, "E504.41", {"start": v(-10.4, 2.2) * mm, "end": v(-10.35, 2.3) * mm});
            skLineSegment(sketch, "E504.42", {"start": v(-10.45, 2.09) * mm, "end": v(-10.4, 2.2) * mm});
            skLineSegment(sketch, "E504.43", {"start": v(-10.5, 1.98) * mm, "end": v(-10.45, 2.09) * mm});
            skLineSegment(sketch, "E504.44", {"start": v(-10.54, 1.87) * mm, "end": v(-10.5, 1.98) * mm});
            skLineSegment(sketch, "E504.45", {"start": v(-10.58, 1.76) * mm, "end": v(-10.54, 1.87) * mm});
            skLineSegment(sketch, "E504.46", {"start": v(-10.62, 1.64) * mm, "end": v(-10.58, 1.76) * mm});
            skLineSegment(sketch, "E504.47", {"start": v(-10.66, 1.53) * mm, "end": v(-10.62, 1.64) * mm});
            skLineSegment(sketch, "E504.48", {"start": v(-10.7, 1.42) * mm, "end": v(-10.66, 1.53) * mm});
            skLineSegment(sketch, "E504.49", {"start": v(-10.74, 1.3) * mm, "end": v(-10.7, 1.42) * mm});
            skLineSegment(sketch, "E504.50", {"start": v(-10.78, 1.19) * mm, "end": v(-10.74, 1.3) * mm});
            skLineSegment(sketch, "E504.51", {"start": v(-10.81, 1.07) * mm, "end": v(-10.78, 1.19) * mm});
            skLineSegment(sketch, "E504.52", {"start": v(-10.84, 0.96) * mm, "end": v(-10.81, 1.07) * mm});
            skLineSegment(sketch, "E504.53", {"start": v(-10.87, 0.84) * mm, "end": v(-10.84, 0.96) * mm});
            skLineSegment(sketch, "E504.54", {"start": v(-10.9, 0.72) * mm, "end": v(-10.87, 0.84) * mm});
            skLineSegment(sketch, "E504.55", {"start": v(-10.93, 0.6) * mm, "end": v(-10.9, 0.72) * mm});
            skLineSegment(sketch, "E504.56", {"start": v(-10.95, 0.47) * mm, "end": v(-10.93, 0.6) * mm});
            skLineSegment(sketch, "E504.57", {"start": v(-10.97, 0.34) * mm, "end": v(-10.95, 0.47) * mm});
            skLineSegment(sketch, "E504.58", {"start": v(-10.99, 0.2) * mm, "end": v(-10.97, 0.34) * mm});
            skLineSegment(sketch, "E504.59", {"start": v(-11, 0) * mm, "end": v(-10.99, 0.2) * mm});
            skLineSegment(sketch, "E504.60", {"start": v(-10.99, -0.2) * mm, "end": v(-11, 0) * mm});
            skLineSegment(sketch, "E504.61", {"start": v(-10.97, -0.34) * mm, "end": v(-10.99, -0.2) * mm});
            skLineSegment(sketch, "E504.62", {"start": v(-10.95, -0.47) * mm, "end": v(-10.97, -0.34) * mm});
            skLineSegment(sketch, "E504.63", {"start": v(-10.93, -0.6) * mm, "end": v(-10.95, -0.47) * mm});
            skLineSegment(sketch, "E504.64", {"start": v(-10.9, -0.72) * mm, "end": v(-10.93, -0.6) * mm});
            skLineSegment(sketch, "E504.65", {"start": v(-10.87, -0.84) * mm, "end": v(-10.9, -0.72) * mm});
            skLineSegment(sketch, "E504.66", {"start": v(-10.84, -0.96) * mm, "end": v(-10.87, -0.84) * mm});
            skLineSegment(sketch, "E504.67", {"start": v(-10.81, -1.07) * mm, "end": v(-10.84, -0.96) * mm});
            skLineSegment(sketch, "E504.68", {"start": v(-10.78, -1.19) * mm, "end": v(-10.81, -1.07) * mm});
            skLineSegment(sketch, "E504.69", {"start": v(-10.74, -1.3) * mm, "end": v(-10.78, -1.19) * mm});
            skLineSegment(sketch, "E504.70", {"start": v(-10.7, -1.42) * mm, "end": v(-10.74, -1.3) * mm});
            skLineSegment(sketch, "E504.71", {"start": v(-10.66, -1.53) * mm, "end": v(-10.7, -1.42) * mm});
            skLineSegment(sketch, "E504.72", {"start": v(-10.62, -1.64) * mm, "end": v(-10.66, -1.53) * mm});
            skLineSegment(sketch, "E504.73", {"start": v(-10.58, -1.76) * mm, "end": v(-10.62, -1.64) * mm});
            skLineSegment(sketch, "E504.74", {"start": v(-10.54, -1.87) * mm, "end": v(-10.58, -1.76) * mm});
            skLineSegment(sketch, "E504.75", {"start": v(-10.5, -1.98) * mm, "end": v(-10.54, -1.87) * mm});
            skLineSegment(sketch, "E504.76", {"start": v(-10.45, -2.09) * mm, "end": v(-10.5, -1.98) * mm});
            skLineSegment(sketch, "E504.77", {"start": v(-10.4, -2.2) * mm, "end": v(-10.45, -2.09) * mm});
            skLineSegment(sketch, "E504.78", {"start": v(-10.35, -2.3) * mm, "end": v(-10.4, -2.2) * mm});
            skLineSegment(sketch, "E504.79", {"start": v(-10.3, -2.42) * mm, "end": v(-10.35, -2.3) * mm});
            skLineSegment(sketch, "E504.80", {"start": v(-10.25, -2.53) * mm, "end": v(-10.3, -2.42) * mm});
            skLineSegment(sketch, "E504.81", {"start": v(-10.2, -2.64) * mm, "end": v(-10.25, -2.53) * mm});
            skLineSegment(sketch, "E504.82", {"start": v(-10.15, -2.75) * mm, "end": v(-10.2, -2.64) * mm});
            skLineSegment(sketch, "E504.83", {"start": v(-10.1, -2.85) * mm, "end": v(-10.15, -2.75) * mm});
            skLineSegment(sketch, "E504.84", {"start": v(-10.03, -2.96) * mm, "end": v(-10.1, -2.85) * mm});
            skLineSegment(sketch, "E504.85", {"start": v(-9.98, -3.07) * mm, "end": v(-10.03, -2.96) * mm});
            skLineSegment(sketch, "E504.86", {"start": v(-9.92, -3.18) * mm, "end": v(-9.98, -3.07) * mm});
            skLineSegment(sketch, "E504.87", {"start": v(-9.86, -3.29) * mm, "end": v(-9.92, -3.18) * mm});
            skLineSegment(sketch, "E504.88", {"start": v(-9.8, -3.4) * mm, "end": v(-9.86, -3.29) * mm});
            skLineSegment(sketch, "E504.89", {"start": v(-9.74, -3.5) * mm, "end": v(-9.8, -3.4) * mm});
            skLineSegment(sketch, "E504.90", {"start": v(-9.67, -3.61) * mm, "end": v(-9.74, -3.5) * mm});
            skLineSegment(sketch, "E504.91", {"start": v(-9.6, -3.72) * mm, "end": v(-9.67, -3.61) * mm});
            skLineSegment(sketch, "E504.92", {"start": v(-9.54, -3.82) * mm, "end": v(-9.6, -3.72) * mm});
            skLineSegment(sketch, "E504.93", {"start": v(-9.48, -3.93) * mm, "end": v(-9.54, -3.82) * mm});
            skLineSegment(sketch, "E504.94", {"start": v(-9.4, -4.04) * mm, "end": v(-9.48, -3.93) * mm});
            skLineSegment(sketch, "E504.95", {"start": v(10.87, -0.84) * mm, "end": v(10.84, -0.96) * mm});
            skLineSegment(sketch, "E504.96", {"start": v(10.9, -0.72) * mm, "end": v(10.87, -0.84) * mm});
            skLineSegment(sketch, "E504.97", {"start": v(10.93, -0.6) * mm, "end": v(10.9, -0.72) * mm});
            skLineSegment(sketch, "E504.98", {"start": v(10.95, -0.47) * mm, "end": v(10.93, -0.6) * mm});
            skLineSegment(sketch, "E504.99", {"start": v(10.97, -0.34) * mm, "end": v(10.95, -0.47) * mm});
            skLineSegment(sketch, "E504.100", {"start": v(10.99, -0.2) * mm, "end": v(10.97, -0.34) * mm});
            skLineSegment(sketch, "E504.101", {"start": v(11, 0) * mm, "end": v(10.99, -0.2) * mm});
            skLineSegment(sketch, "E504.102", {"start": v(10.99, 0.2) * mm, "end": v(11, 0) * mm});
            skLineSegment(sketch, "E504.103", {"start": v(10.97, 0.34) * mm, "end": v(10.99, 0.2) * mm});
            skLineSegment(sketch, "E504.104", {"start": v(10.95, 0.47) * mm, "end": v(10.97, 0.34) * mm});
            skLineSegment(sketch, "E504.105", {"start": v(10.93, 0.6) * mm, "end": v(10.95, 0.47) * mm});
            skLineSegment(sketch, "E504.106", {"start": v(10.9, 0.72) * mm, "end": v(10.93, 0.6) * mm});
            skLineSegment(sketch, "E504.107", {"start": v(10.87, 0.84) * mm, "end": v(10.9, 0.72) * mm});
            skLineSegment(sketch, "E504.108", {"start": v(10.84, 0.96) * mm, "end": v(10.87, 0.84) * mm});
            skLineSegment(sketch, "E504.109", {"start": v(10.81, 1.07) * mm, "end": v(10.84, 0.96) * mm});
            skLineSegment(sketch, "E504.110", {"start": v(10.78, 1.19) * mm, "end": v(10.81, 1.07) * mm});
            skLineSegment(sketch, "E504.111", {"start": v(10.74, 1.3) * mm, "end": v(10.78, 1.19) * mm});
            skLineSegment(sketch, "E504.112", {"start": v(10.7, 1.42) * mm, "end": v(10.74, 1.3) * mm});
            skLineSegment(sketch, "E504.113", {"start": v(10.66, 1.53) * mm, "end": v(10.7, 1.42) * mm});
            skLineSegment(sketch, "E504.114", {"start": v(10.62, 1.64) * mm, "end": v(10.66, 1.53) * mm});
            skLineSegment(sketch, "E504.115", {"start": v(10.58, 1.76) * mm, "end": v(10.62, 1.64) * mm});
            skLineSegment(sketch, "E504.116", {"start": v(10.54, 1.87) * mm, "end": v(10.58, 1.76) * mm});
            skLineSegment(sketch, "E504.117", {"start": v(10.5, 1.98) * mm, "end": v(10.54, 1.87) * mm});
            skLineSegment(sketch, "E504.118", {"start": v(10.45, 2.09) * mm, "end": v(10.5, 1.98) * mm});
            skLineSegment(sketch, "E504.119", {"start": v(10.4, 2.2) * mm, "end": v(10.45, 2.09) * mm});
            skLineSegment(sketch, "E504.120", {"start": v(10.35, 2.3) * mm, "end": v(10.4, 2.2) * mm});
            skLineSegment(sketch, "E504.121", {"start": v(10.3, 2.42) * mm, "end": v(10.35, 2.3) * mm});
            skLineSegment(sketch, "E504.122", {"start": v(10.25, 2.53) * mm, "end": v(10.3, 2.42) * mm});
            skLineSegment(sketch, "E504.123", {"start": v(10.2, 2.64) * mm, "end": v(10.25, 2.53) * mm});
            skLineSegment(sketch, "E504.124", {"start": v(10.15, 2.75) * mm, "end": v(10.2, 2.64) * mm});
            skLineSegment(sketch, "E504.125", {"start": v(10.1, 2.85) * mm, "end": v(10.15, 2.75) * mm});
            skLineSegment(sketch, "E504.126", {"start": v(10.03, 2.96) * mm, "end": v(10.1, 2.85) * mm});
            skLineSegment(sketch, "E504.127", {"start": v(9.98, 3.07) * mm, "end": v(10.03, 2.96) * mm});
            skLineSegment(sketch, "E504.128", {"start": v(9.92, 3.18) * mm, "end": v(9.98, 3.07) * mm});
            skLineSegment(sketch, "E504.129", {"start": v(9.86, 3.29) * mm, "end": v(9.92, 3.18) * mm});
            skLineSegment(sketch, "E504.130", {"start": v(9.8, 3.4) * mm, "end": v(9.86, 3.29) * mm});
            skLineSegment(sketch, "E504.131", {"start": v(9.74, 3.5) * mm, "end": v(9.8, 3.4) * mm});
            skLineSegment(sketch, "E504.132", {"start": v(9.67, 3.61) * mm, "end": v(9.74, 3.5) * mm});
            skLineSegment(sketch, "E504.133", {"start": v(9.6, 3.72) * mm, "end": v(9.67, 3.61) * mm});
            skLineSegment(sketch, "E504.134", {"start": v(9.54, 3.82) * mm, "end": v(9.6, 3.72) * mm});
            skLineSegment(sketch, "E504.135", {"start": v(9.48, 3.93) * mm, "end": v(9.54, 3.82) * mm});
            skLineSegment(sketch, "E504.136", {"start": v(9.4, 4.04) * mm, "end": v(9.48, 3.93) * mm});
            skLineSegment(sketch, "E504.137", {"start": v(9.34, 4.15) * mm, "end": v(9.4, 4.04) * mm});
            skLineSegment(sketch, "E504.138", {"start": v(9.27, 4.25) * mm, "end": v(9.34, 4.15) * mm});
            skLineSegment(sketch, "E504.139", {"start": v(9.2, 4.36) * mm, "end": v(9.27, 4.25) * mm});
            skLineSegment(sketch, "E504.140", {"start": v(9.13, 4.47) * mm, "end": v(9.2, 4.36) * mm});
            skLineSegment(sketch, "E504.141", {"start": v(9.05, 4.57) * mm, "end": v(9.13, 4.47) * mm});
            skLineSegment(sketch, "E504.142", {"start": v(8.98, 4.68) * mm, "end": v(9.05, 4.57) * mm});
            skLineSegment(sketch, "E504.143", {"start": v(8.9, 4.78) * mm, "end": v(8.98, 4.68) * mm});
            skLineSegment(sketch, "E504.144", {"start": v(8.83, 4.9) * mm, "end": v(8.9, 4.78) * mm});
            skLineSegment(sketch, "E504.145", {"start": v(8.75, 5) * mm, "end": v(8.83, 4.9) * mm});
            skLineSegment(sketch, "E504.146", {"start": v(8.67, 5.1) * mm, "end": v(8.75, 5) * mm});
            skLineSegment(sketch, "E504.147", {"start": v(8.59, 5.2) * mm, "end": v(8.67, 5.1) * mm});
            skLineSegment(sketch, "E504.148", {"start": v(8.5, 5.32) * mm, "end": v(8.59, 5.2) * mm});
            skLineSegment(sketch, "E504.149", {"start": v(8.42, 5.42) * mm, "end": v(8.5, 5.32) * mm});
            skLineSegment(sketch, "E504.150", {"start": v(8.34, 5.53) * mm, "end": v(8.42, 5.42) * mm});
            skLineSegment(sketch, "E504.151", {"start": v(8.25, 5.63) * mm, "end": v(8.34, 5.53) * mm});
            skLineSegment(sketch, "E504.152", {"start": v(8.16, 5.74) * mm, "end": v(8.25, 5.63) * mm});
            skLineSegment(sketch, "E504.153", {"start": v(8.07, 5.84) * mm, "end": v(8.16, 5.74) * mm});
            skLineSegment(sketch, "E504.154", {"start": v(7.98, 5.95) * mm, "end": v(8.07, 5.84) * mm});
            skLineSegment(sketch, "E504.155", {"start": v(7.9, 6.06) * mm, "end": v(7.98, 5.95) * mm});
            skLineSegment(sketch, "E504.156", {"start": v(7.8, 6.16) * mm, "end": v(7.9, 6.06) * mm});
            skLineSegment(sketch, "E504.157", {"start": v(7.7, 6.27) * mm, "end": v(7.8, 6.16) * mm});
            skLineSegment(sketch, "E504.158", {"start": v(7.61, 6.37) * mm, "end": v(7.7, 6.27) * mm});
            skLineSegment(sketch, "E504.159", {"start": v(7.51, 6.48) * mm, "end": v(7.61, 6.37) * mm});
            skLineSegment(sketch, "E504.160", {"start": v(7.42, 6.58) * mm, "end": v(7.51, 6.48) * mm});
            skLineSegment(sketch, "E504.161", {"start": v(7.32, 6.7) * mm, "end": v(7.42, 6.58) * mm});
            skLineSegment(sketch, "E504.162", {"start": v(7.21, 6.8) * mm, "end": v(7.32, 6.7) * mm});
            skLineSegment(sketch, "E504.163", {"start": v(7.11, 6.9) * mm, "end": v(7.21, 6.8) * mm});
            skLineSegment(sketch, "E504.164", {"start": v(7, 7) * mm, "end": v(7.11, 6.9) * mm});
            skLineSegment(sketch, "E504.165", {"start": v(6.9, 7.11) * mm, "end": v(7, 7) * mm});
            skLineSegment(sketch, "E504.166", {"start": v(6.8, 7.21) * mm, "end": v(6.9, 7.11) * mm});
            skLineSegment(sketch, "E504.167", {"start": v(6.7, 7.32) * mm, "end": v(6.8, 7.21) * mm});
            skLineSegment(sketch, "E504.168", {"start": v(6.58, 7.42) * mm, "end": v(6.7, 7.32) * mm});
            skLineSegment(sketch, "E504.169", {"start": v(6.48, 7.51) * mm, "end": v(6.58, 7.42) * mm});
            skLineSegment(sketch, "E504.170", {"start": v(6.37, 7.61) * mm, "end": v(6.48, 7.51) * mm});
            skLineSegment(sketch, "E504.171", {"start": v(6.27, 7.7) * mm, "end": v(6.37, 7.61) * mm});
            skLineSegment(sketch, "E504.172", {"start": v(6.16, 7.8) * mm, "end": v(6.27, 7.7) * mm});
            skLineSegment(sketch, "E504.173", {"start": v(6.06, 7.9) * mm, "end": v(6.16, 7.8) * mm});
            skLineSegment(sketch, "E504.174", {"start": v(5.95, 7.98) * mm, "end": v(6.06, 7.9) * mm});
            skLineSegment(sketch, "E504.175", {"start": v(5.84, 8.07) * mm, "end": v(5.95, 7.98) * mm});
            skLineSegment(sketch, "E504.176", {"start": v(5.74, 8.16) * mm, "end": v(5.84, 8.07) * mm});
            skLineSegment(sketch, "E504.177", {"start": v(5.63, 8.25) * mm, "end": v(5.74, 8.16) * mm});
            skLineSegment(sketch, "E504.178", {"start": v(5.53, 8.34) * mm, "end": v(5.63, 8.25) * mm});
            skLineSegment(sketch, "E504.179", {"start": v(5.42, 8.42) * mm, "end": v(5.53, 8.34) * mm});
            skLineSegment(sketch, "E504.180", {"start": v(5.32, 8.5) * mm, "end": v(5.42, 8.42) * mm});
            skLineSegment(sketch, "E504.181", {"start": v(5.2, 8.59) * mm, "end": v(5.32, 8.5) * mm});
            skLineSegment(sketch, "E504.182", {"start": v(5.1, 8.67) * mm, "end": v(5.2, 8.59) * mm});
            skLineSegment(sketch, "E504.183", {"start": v(5, 8.75) * mm, "end": v(5.1, 8.67) * mm});
            skLineSegment(sketch, "E504.184", {"start": v(4.9, 8.83) * mm, "end": v(5, 8.75) * mm});
            skLineSegment(sketch, "E504.185", {"start": v(4.78, 8.9) * mm, "end": v(4.9, 8.83) * mm});
            skLineSegment(sketch, "E504.186", {"start": v(4.68, 8.98) * mm, "end": v(4.78, 8.9) * mm});
            skLineSegment(sketch, "E504.187", {"start": v(4.57, 9.05) * mm, "end": v(4.68, 8.98) * mm});
            skLineSegment(sketch, "E504.188", {"start": v(4.47, 9.13) * mm, "end": v(4.57, 9.05) * mm});
            skLineSegment(sketch, "E504.189", {"start": v(4.36, 9.2) * mm, "end": v(4.47, 9.13) * mm});
            skLineSegment(sketch, "E504.190", {"start": v(4.25, 9.27) * mm, "end": v(4.36, 9.2) * mm});
            skLineSegment(sketch, "E504.191", {"start": v(4.15, 9.34) * mm, "end": v(4.25, 9.27) * mm});
            skLineSegment(sketch, "E504.192", {"start": v(4.04, 9.4) * mm, "end": v(4.15, 9.34) * mm});
            skLineSegment(sketch, "E504.193", {"start": v(3.93, 9.48) * mm, "end": v(4.04, 9.4) * mm});
            skLineSegment(sketch, "E504.194", {"start": v(3.82, 9.54) * mm, "end": v(3.93, 9.48) * mm});
            skLineSegment(sketch, "E504.195", {"start": v(3.72, 9.6) * mm, "end": v(3.82, 9.54) * mm});
            skLineSegment(sketch, "E504.196", {"start": v(3.61, 9.67) * mm, "end": v(3.72, 9.6) * mm});
            skLineSegment(sketch, "E504.197", {"start": v(-2.42, 10.3) * mm, "end": v(-2.3, 10.35) * mm});
            skLineSegment(sketch, "E504.198", {"start": v(-2.53, 10.25) * mm, "end": v(-2.42, 10.3) * mm});
            skLineSegment(sketch, "E504.199", {"start": v(-2.64, 10.2) * mm, "end": v(-2.53, 10.25) * mm});
            skLineSegment(sketch, "E504.200", {"start": v(-2.75, 10.15) * mm, "end": v(-2.64, 10.2) * mm});
            skLineSegment(sketch, "E504.201", {"start": v(-2.85, 10.1) * mm, "end": v(-2.75, 10.15) * mm});
            skLineSegment(sketch, "E504.202", {"start": v(-2.96, 10.03) * mm, "end": v(-2.85, 10.1) * mm});
            skLineSegment(sketch, "E504.203", {"start": v(-3.07, 9.98) * mm, "end": v(-2.96, 10.03) * mm});
            skLineSegment(sketch, "E504.204", {"start": v(-3.18, 9.92) * mm, "end": v(-3.07, 9.98) * mm});
            skLineSegment(sketch, "E504.205", {"start": v(-3.29, 9.86) * mm, "end": v(-3.18, 9.92) * mm});
            skLineSegment(sketch, "E504.206", {"start": v(-3.4, 9.8) * mm, "end": v(-3.29, 9.86) * mm});
            skLineSegment(sketch, "E504.207", {"start": v(-3.5, 9.74) * mm, "end": v(-3.4, 9.8) * mm});
            skLineSegment(sketch, "E504.208", {"start": v(-3.61, 9.67) * mm, "end": v(-3.5, 9.74) * mm});
            skLineSegment(sketch, "E504.209", {"start": v(-3.72, 9.6) * mm, "end": v(-3.61, 9.67) * mm});
            skLineSegment(sketch, "E504.210", {"start": v(-3.82, 9.54) * mm, "end": v(-3.72, 9.6) * mm});
            skLineSegment(sketch, "E504.211", {"start": v(-3.93, 9.48) * mm, "end": v(-3.82, 9.54) * mm});
            skLineSegment(sketch, "E504.212", {"start": v(-4.04, 9.4) * mm, "end": v(-3.93, 9.48) * mm});
            skLineSegment(sketch, "E504.213", {"start": v(-4.15, 9.34) * mm, "end": v(-4.04, 9.4) * mm});
            skLineSegment(sketch, "E504.214", {"start": v(-4.25, 9.27) * mm, "end": v(-4.15, 9.34) * mm});
            skLineSegment(sketch, "E504.215", {"start": v(-4.36, 9.2) * mm, "end": v(-4.25, 9.27) * mm});
            skLineSegment(sketch, "E504.216", {"start": v(-4.47, 9.13) * mm, "end": v(-4.36, 9.2) * mm});
            skLineSegment(sketch, "E504.217", {"start": v(-4.57, 9.05) * mm, "end": v(-4.47, 9.13) * mm});
            skLineSegment(sketch, "E504.218", {"start": v(-4.68, 8.98) * mm, "end": v(-4.57, 9.05) * mm});
            skLineSegment(sketch, "E504.219", {"start": v(-4.78, 8.9) * mm, "end": v(-4.68, 8.98) * mm});
            skLineSegment(sketch, "E504.220", {"start": v(-4.9, 8.83) * mm, "end": v(-4.78, 8.9) * mm});
            skLineSegment(sketch, "E504.221", {"start": v(-6.27, 7.7) * mm, "end": v(-6.16, 7.8) * mm});
            skLineSegment(sketch, "E504.222", {"start": v(-6.37, 7.61) * mm, "end": v(-6.27, 7.7) * mm});
            skLineSegment(sketch, "E504.223", {"start": v(-6.48, 7.51) * mm, "end": v(-6.37, 7.61) * mm});
            skLineSegment(sketch, "E504.224", {"start": v(-6.58, 7.42) * mm, "end": v(-6.48, 7.51) * mm});
            skLineSegment(sketch, "E504.225", {"start": v(-6.7, 7.32) * mm, "end": v(-6.58, 7.42) * mm});
            skLineSegment(sketch, "E504.226", {"start": v(-6.8, 7.21) * mm, "end": v(-6.7, 7.32) * mm});
            skLineSegment(sketch, "E504.227", {"start": v(-7.21, 6.8) * mm, "end": v(-7.11, 6.9) * mm});
            skLineSegment(sketch, "E504.228", {"start": v(-7.11, 6.9) * mm, "end": v(-7, 7) * mm});
            skLineSegment(sketch, "E504.229", {"start": v(-7, 7) * mm, "end": v(-6.9, 7.11) * mm});
            skLineSegment(sketch, "E504.230", {"start": v(-6.9, 7.11) * mm, "end": v(-6.8, 7.21) * mm});
            skLineSegment(sketch, "E504.231", {"start": v(-6.16, 7.8) * mm, "end": v(-6.06, 7.9) * mm});
            skLineSegment(sketch, "E504.232", {"start": v(-6.06, 7.9) * mm, "end": v(-5.95, 7.98) * mm});
            skLineSegment(sketch, "E504.233", {"start": v(-5.95, 7.98) * mm, "end": v(-5.84, 8.07) * mm});
            skLineSegment(sketch, "E504.234", {"start": v(-5.84, 8.07) * mm, "end": v(-5.74, 8.16) * mm});
            skLineSegment(sketch, "E504.235", {"start": v(-5.74, 8.16) * mm, "end": v(-5.63, 8.25) * mm});
            skLineSegment(sketch, "E504.236", {"start": v(-5.63, 8.25) * mm, "end": v(-5.53, 8.34) * mm});
            skLineSegment(sketch, "E504.237", {"start": v(-5.53, 8.34) * mm, "end": v(-5.42, 8.42) * mm});
            skLineSegment(sketch, "E504.238", {"start": v(-5.42, 8.42) * mm, "end": v(-5.32, 8.5) * mm});
            skLineSegment(sketch, "E504.239", {"start": v(-5.32, 8.5) * mm, "end": v(-5.2, 8.59) * mm});
            skLineSegment(sketch, "E504.240", {"start": v(-5.2, 8.59) * mm, "end": v(-5.1, 8.67) * mm});
            skLineSegment(sketch, "E504.241", {"start": v(-5.1, 8.67) * mm, "end": v(-5, 8.75) * mm});
            skLineSegment(sketch, "E504.242", {"start": v(-5, 8.75) * mm, "end": v(-4.9, 8.83) * mm});
            skLineSegment(sketch, "E504.243", {"start": v(-2.3, 10.35) * mm, "end": v(-2.2, 10.4) * mm});
            skLineSegment(sketch, "E504.244", {"start": v(-2.2, 10.4) * mm, "end": v(-2.09, 10.45) * mm});
            skLineSegment(sketch, "E504.245", {"start": v(-2.09, 10.45) * mm, "end": v(-1.98, 10.5) * mm});
            skLineSegment(sketch, "E504.246", {"start": v(-1.98, 10.5) * mm, "end": v(-1.87, 10.54) * mm});
            skLineSegment(sketch, "E504.247", {"start": v(-1.87, 10.54) * mm, "end": v(-1.76, 10.58) * mm});
            skLineSegment(sketch, "E504.248", {"start": v(-1.76, 10.58) * mm, "end": v(-1.64, 10.62) * mm});
            skLineSegment(sketch, "E504.249", {"start": v(-1.64, 10.62) * mm, "end": v(-1.53, 10.66) * mm});
            skLineSegment(sketch, "E504.250", {"start": v(-1.53, 10.66) * mm, "end": v(-1.42, 10.7) * mm});
            skLineSegment(sketch, "E504.251", {"start": v(-1.42, 10.7) * mm, "end": v(-1.3, 10.74) * mm});
            skLineSegment(sketch, "E504.252", {"start": v(-1.3, 10.74) * mm, "end": v(-1.19, 10.78) * mm});
            skLineSegment(sketch, "E504.253", {"start": v(-1.19, 10.78) * mm, "end": v(-1.07, 10.81) * mm});
            skLineSegment(sketch, "E504.254", {"start": v(-1.07, 10.81) * mm, "end": v(-0.96, 10.84) * mm});
            skLineSegment(sketch, "E504.255", {"start": v(-0.96, 10.84) * mm, "end": v(-0.84, 10.87) * mm});
            skLineSegment(sketch, "E504.256", {"start": v(-0.84, 10.87) * mm, "end": v(-0.72, 10.9) * mm});
            skLineSegment(sketch, "E504.257", {"start": v(-0.72, 10.9) * mm, "end": v(-0.6, 10.93) * mm});
            skLineSegment(sketch, "E504.258", {"start": v(-0.6, 10.93) * mm, "end": v(-0.47, 10.95) * mm});
            skLineSegment(sketch, "E504.259", {"start": v(-0.47, 10.95) * mm, "end": v(-0.34, 10.97) * mm});
            skLineSegment(sketch, "E504.260", {"start": v(-0.34, 10.97) * mm, "end": v(-0.2, 10.99) * mm});
            skLineSegment(sketch, "E504.261", {"start": v(-0.2, 10.99) * mm, "end": v(0, 11) * mm});
            skLineSegment(sketch, "E504.262", {"start": v(0, 11) * mm, "end": v(0.2, 10.99) * mm});
            skLineSegment(sketch, "E504.263", {"start": v(0.2, 10.99) * mm, "end": v(0.34, 10.97) * mm});
            skLineSegment(sketch, "E504.264", {"start": v(0.34, 10.97) * mm, "end": v(0.47, 10.95) * mm});
            skLineSegment(sketch, "E504.265", {"start": v(0.47, 10.95) * mm, "end": v(0.6, 10.93) * mm});
            skLineSegment(sketch, "E504.266", {"start": v(0.6, 10.93) * mm, "end": v(0.72, 10.9) * mm});
            skLineSegment(sketch, "E504.267", {"start": v(0.72, 10.9) * mm, "end": v(0.84, 10.87) * mm});
            skLineSegment(sketch, "E504.268", {"start": v(0.84, 10.87) * mm, "end": v(0.96, 10.84) * mm});
            skLineSegment(sketch, "E504.269", {"start": v(0.96, 10.84) * mm, "end": v(1.07, 10.81) * mm});
            skLineSegment(sketch, "E504.270", {"start": v(1.07, 10.81) * mm, "end": v(1.19, 10.78) * mm});
            skLineSegment(sketch, "E504.271", {"start": v(1.19, 10.78) * mm, "end": v(1.3, 10.74) * mm});
            skLineSegment(sketch, "E504.272", {"start": v(1.3, 10.74) * mm, "end": v(1.42, 10.7) * mm});
            skLineSegment(sketch, "E504.273", {"start": v(1.42, 10.7) * mm, "end": v(1.53, 10.66) * mm});
            skLineSegment(sketch, "E504.274", {"start": v(1.53, 10.66) * mm, "end": v(1.64, 10.62) * mm});
            skLineSegment(sketch, "E504.275", {"start": v(1.64, 10.62) * mm, "end": v(1.76, 10.58) * mm});
            skLineSegment(sketch, "E504.276", {"start": v(1.76, 10.58) * mm, "end": v(1.87, 10.54) * mm});
            skLineSegment(sketch, "E504.277", {"start": v(1.87, 10.54) * mm, "end": v(1.98, 10.5) * mm});
            skLineSegment(sketch, "E504.278", {"start": v(1.98, 10.5) * mm, "end": v(2.09, 10.45) * mm});
            skLineSegment(sketch, "E504.279", {"start": v(2.09, 10.45) * mm, "end": v(2.2, 10.4) * mm});
            skLineSegment(sketch, "E504.280", {"start": v(2.2, 10.4) * mm, "end": v(2.3, 10.35) * mm});
            skLineSegment(sketch, "E504.281", {"start": v(2.3, 10.35) * mm, "end": v(2.42, 10.3) * mm});
            skLineSegment(sketch, "E504.282", {"start": v(2.42, 10.3) * mm, "end": v(2.53, 10.25) * mm});
            skLineSegment(sketch, "E504.283", {"start": v(2.53, 10.25) * mm, "end": v(2.64, 10.2) * mm});
            skLineSegment(sketch, "E504.284", {"start": v(2.64, 10.2) * mm, "end": v(2.75, 10.15) * mm});
            skLineSegment(sketch, "E504.285", {"start": v(2.75, 10.15) * mm, "end": v(2.85, 10.1) * mm});
            skLineSegment(sketch, "E504.286", {"start": v(2.85, 10.1) * mm, "end": v(2.96, 10.03) * mm});
            skLineSegment(sketch, "E504.287", {"start": v(2.96, 10.03) * mm, "end": v(3.07, 9.98) * mm});
            skLineSegment(sketch, "E504.288", {"start": v(3.07, 9.98) * mm, "end": v(3.18, 9.92) * mm});
            skLineSegment(sketch, "E504.289", {"start": v(3.18, 9.92) * mm, "end": v(3.29, 9.86) * mm});
            skLineSegment(sketch, "E504.290", {"start": v(3.29, 9.86) * mm, "end": v(3.4, 9.8) * mm});
            skLineSegment(sketch, "E504.291", {"start": v(3.4, 9.8) * mm, "end": v(3.5, 9.74) * mm});
            skLineSegment(sketch, "E504.292", {"start": v(3.5, 9.74) * mm, "end": v(3.61, 9.67) * mm});
            skLineSegment(sketch, "E504.293", {"start": v(10.84, -0.96) * mm, "end": v(10.81, -1.07) * mm});
            skLineSegment(sketch, "E504.294", {"start": v(10.81, -1.07) * mm, "end": v(10.78, -1.19) * mm});
            skLineSegment(sketch, "E504.295", {"start": v(10.78, -1.19) * mm, "end": v(10.74, -1.3) * mm});
            skLineSegment(sketch, "E504.296", {"start": v(10.74, -1.3) * mm, "end": v(10.7, -1.42) * mm});
            skLineSegment(sketch, "E504.297", {"start": v(10.7, -1.42) * mm, "end": v(10.66, -1.53) * mm});
            skLineSegment(sketch, "E504.298", {"start": v(10.66, -1.53) * mm, "end": v(10.62, -1.64) * mm});
            skLineSegment(sketch, "E504.299", {"start": v(10.62, -1.64) * mm, "end": v(10.58, -1.76) * mm});
            skLineSegment(sketch, "E504.300", {"start": v(10.58, -1.76) * mm, "end": v(10.54, -1.87) * mm});
            skLineSegment(sketch, "E504.301", {"start": v(10.54, -1.87) * mm, "end": v(10.5, -1.98) * mm});
            skLineSegment(sketch, "E504.302", {"start": v(10.5, -1.98) * mm, "end": v(10.45, -2.09) * mm});
            skLineSegment(sketch, "E504.303", {"start": v(10.45, -2.09) * mm, "end": v(10.4, -2.2) * mm});
            skLineSegment(sketch, "E504.304", {"start": v(10.4, -2.2) * mm, "end": v(10.35, -2.3) * mm});
            skLineSegment(sketch, "E504.305", {"start": v(10.35, -2.3) * mm, "end": v(10.3, -2.42) * mm});
            skLineSegment(sketch, "E504.306", {"start": v(10.3, -2.42) * mm, "end": v(10.25, -2.53) * mm});
            skLineSegment(sketch, "E504.307", {"start": v(10.25, -2.53) * mm, "end": v(10.2, -2.64) * mm});
            skLineSegment(sketch, "E504.308", {"start": v(10.2, -2.64) * mm, "end": v(10.15, -2.75) * mm});
            skLineSegment(sketch, "E504.309", {"start": v(10.15, -2.75) * mm, "end": v(10.1, -2.85) * mm});
            skLineSegment(sketch, "E504.310", {"start": v(10.1, -2.85) * mm, "end": v(10.03, -2.96) * mm});
            skLineSegment(sketch, "E504.311", {"start": v(10.03, -2.96) * mm, "end": v(9.98, -3.07) * mm});
            skLineSegment(sketch, "E504.312", {"start": v(9.98, -3.07) * mm, "end": v(9.92, -3.18) * mm});
            skLineSegment(sketch, "E504.313", {"start": v(9.92, -3.18) * mm, "end": v(9.86, -3.29) * mm});
            skLineSegment(sketch, "E504.314", {"start": v(9.86, -3.29) * mm, "end": v(9.8, -3.4) * mm});
            skLineSegment(sketch, "E504.315", {"start": v(9.8, -3.4) * mm, "end": v(9.74, -3.5) * mm});
            skLineSegment(sketch, "E504.316", {"start": v(9.74, -3.5) * mm, "end": v(9.67, -3.61) * mm});
            skLineSegment(sketch, "E504.317", {"start": v(9.67, -3.61) * mm, "end": v(9.6, -3.72) * mm});
            skLineSegment(sketch, "E504.318", {"start": v(9.6, -3.72) * mm, "end": v(9.54, -3.82) * mm});
            skLineSegment(sketch, "E504.319", {"start": v(9.54, -3.82) * mm, "end": v(9.48, -3.93) * mm});
            skLineSegment(sketch, "E504.320", {"start": v(9.48, -3.93) * mm, "end": v(9.4, -4.04) * mm});
            skLineSegment(sketch, "E504.321", {"start": v(9.4, -4.04) * mm, "end": v(9.34, -4.15) * mm});
            skLineSegment(sketch, "E504.322", {"start": v(9.34, -4.15) * mm, "end": v(9.27, -4.25) * mm});
            skLineSegment(sketch, "E504.323", {"start": v(9.27, -4.25) * mm, "end": v(9.2, -4.36) * mm});
            skLineSegment(sketch, "E504.324", {"start": v(9.2, -4.36) * mm, "end": v(9.13, -4.47) * mm});
            skLineSegment(sketch, "E504.325", {"start": v(9.13, -4.47) * mm, "end": v(9.05, -4.57) * mm});
            skLineSegment(sketch, "E504.326", {"start": v(9.05, -4.57) * mm, "end": v(8.98, -4.68) * mm});
            skLineSegment(sketch, "E504.327", {"start": v(8.98, -4.68) * mm, "end": v(8.9, -4.78) * mm});
            skLineSegment(sketch, "E504.328", {"start": v(8.9, -4.78) * mm, "end": v(8.83, -4.9) * mm});
            skLineSegment(sketch, "E504.329", {"start": v(8.83, -4.9) * mm, "end": v(8.75, -5) * mm});
            skLineSegment(sketch, "E504.330", {"start": v(8.75, -5) * mm, "end": v(8.67, -5.1) * mm});
            skLineSegment(sketch, "E504.331", {"start": v(8.67, -5.1) * mm, "end": v(8.59, -5.2) * mm});
            skLineSegment(sketch, "E504.332", {"start": v(8.59, -5.2) * mm, "end": v(8.5, -5.32) * mm});
            skLineSegment(sketch, "E504.333", {"start": v(8.5, -5.32) * mm, "end": v(8.42, -5.42) * mm});
            skLineSegment(sketch, "E504.334", {"start": v(8.42, -5.42) * mm, "end": v(8.34, -5.53) * mm});
            skLineSegment(sketch, "E504.335", {"start": v(8.34, -5.53) * mm, "end": v(8.25, -5.63) * mm});
            skLineSegment(sketch, "E504.336", {"start": v(8.25, -5.63) * mm, "end": v(8.16, -5.74) * mm});
            skLineSegment(sketch, "E504.337", {"start": v(8.16, -5.74) * mm, "end": v(8.07, -5.84) * mm});
            skLineSegment(sketch, "E504.338", {"start": v(8.07, -5.84) * mm, "end": v(7.98, -5.95) * mm});
            skLineSegment(sketch, "E504.339", {"start": v(7.98, -5.95) * mm, "end": v(7.9, -6.06) * mm});
            skLineSegment(sketch, "E504.340", {"start": v(7.9, -6.06) * mm, "end": v(7.8, -6.16) * mm});
            skLineSegment(sketch, "E504.341", {"start": v(7.8, -6.16) * mm, "end": v(7.7, -6.27) * mm});
            skLineSegment(sketch, "E504.342", {"start": v(7.7, -6.27) * mm, "end": v(7.61, -6.37) * mm});
            skLineSegment(sketch, "E504.343", {"start": v(7.61, -6.37) * mm, "end": v(7.51, -6.48) * mm});
            skLineSegment(sketch, "E504.344", {"start": v(7.51, -6.48) * mm, "end": v(7.42, -6.58) * mm});
            skLineSegment(sketch, "E504.345", {"start": v(7.42, -6.58) * mm, "end": v(7.32, -6.7) * mm});
            skLineSegment(sketch, "E504.346", {"start": v(7.32, -6.7) * mm, "end": v(7.21, -6.8) * mm});
            skLineSegment(sketch, "E504.347", {"start": v(7.21, -6.8) * mm, "end": v(7.11, -6.9) * mm});
            skLineSegment(sketch, "E504.348", {"start": v(7.11, -6.9) * mm, "end": v(7, -7) * mm});
            skLineSegment(sketch, "E504.349", {"start": v(7, -7) * mm, "end": v(6.9, -7.11) * mm});
            skLineSegment(sketch, "E504.350", {"start": v(6.9, -7.11) * mm, "end": v(6.8, -7.21) * mm});
            skLineSegment(sketch, "E504.351", {"start": v(6.8, -7.21) * mm, "end": v(6.7, -7.32) * mm});
            skLineSegment(sketch, "E504.352", {"start": v(6.7, -7.32) * mm, "end": v(6.58, -7.42) * mm});
            skLineSegment(sketch, "E504.353", {"start": v(6.58, -7.42) * mm, "end": v(6.48, -7.51) * mm});
            skLineSegment(sketch, "E504.354", {"start": v(6.48, -7.51) * mm, "end": v(6.37, -7.61) * mm});
            skLineSegment(sketch, "E504.355", {"start": v(6.37, -7.61) * mm, "end": v(6.27, -7.7) * mm});
            skLineSegment(sketch, "E504.356", {"start": v(6.27, -7.7) * mm, "end": v(6.16, -7.8) * mm});
            skLineSegment(sketch, "E504.357", {"start": v(6.16, -7.8) * mm, "end": v(6.06, -7.9) * mm});
            skLineSegment(sketch, "E504.358", {"start": v(6.06, -7.9) * mm, "end": v(5.95, -7.98) * mm});
            skLineSegment(sketch, "E504.359", {"start": v(5.95, -7.98) * mm, "end": v(5.84, -8.07) * mm});
            skLineSegment(sketch, "E504.360", {"start": v(5.84, -8.07) * mm, "end": v(5.74, -8.16) * mm});
            skLineSegment(sketch, "E504.361", {"start": v(5.74, -8.16) * mm, "end": v(5.63, -8.25) * mm});
            skLineSegment(sketch, "E504.362", {"start": v(5.63, -8.25) * mm, "end": v(5.53, -8.34) * mm});
            skLineSegment(sketch, "E504.363", {"start": v(5.53, -8.34) * mm, "end": v(5.42, -8.42) * mm});
            skLineSegment(sketch, "E504.364", {"start": v(5.42, -8.42) * mm, "end": v(5.32, -8.5) * mm});
            skLineSegment(sketch, "E504.365", {"start": v(5.32, -8.5) * mm, "end": v(5.2, -8.59) * mm});
            skLineSegment(sketch, "E504.366", {"start": v(5.2, -8.59) * mm, "end": v(5.1, -8.67) * mm});
            skLineSegment(sketch, "E504.367", {"start": v(5.1, -8.67) * mm, "end": v(5, -8.75) * mm});
            skLineSegment(sketch, "E504.368", {"start": v(5, -8.75) * mm, "end": v(4.9, -8.83) * mm});
            skLineSegment(sketch, "E504.369", {"start": v(4.9, -8.83) * mm, "end": v(4.78, -8.9) * mm});
            skLineSegment(sketch, "E504.370", {"start": v(4.78, -8.9) * mm, "end": v(4.68, -8.98) * mm});
            skLineSegment(sketch, "E504.371", {"start": v(4.68, -8.98) * mm, "end": v(4.57, -9.05) * mm});
            skLineSegment(sketch, "E504.372", {"start": v(4.57, -9.05) * mm, "end": v(4.47, -9.13) * mm});
            skLineSegment(sketch, "E504.373", {"start": v(4.47, -9.13) * mm, "end": v(4.36, -9.2) * mm});
            skLineSegment(sketch, "E504.374", {"start": v(4.36, -9.2) * mm, "end": v(4.25, -9.27) * mm});
            skLineSegment(sketch, "E504.375", {"start": v(4.25, -9.27) * mm, "end": v(4.15, -9.34) * mm});
            skLineSegment(sketch, "E504.376", {"start": v(4.15, -9.34) * mm, "end": v(4.04, -9.4) * mm});
            skLineSegment(sketch, "E504.377", {"start": v(4.04, -9.4) * mm, "end": v(3.93, -9.48) * mm});
            skLineSegment(sketch, "E504.378", {"start": v(3.93, -9.48) * mm, "end": v(3.82, -9.54) * mm});
            skLineSegment(sketch, "E504.379", {"start": v(3.82, -9.54) * mm, "end": v(3.72, -9.6) * mm});
            skLineSegment(sketch, "E504.380", {"start": v(3.72, -9.6) * mm, "end": v(3.61, -9.67) * mm});
            skLineSegment(sketch, "E504.381", {"start": v(3.61, -9.67) * mm, "end": v(3.5, -9.74) * mm});
            skLineSegment(sketch, "E504.382", {"start": v(3.5, -9.74) * mm, "end": v(3.4, -9.8) * mm});
            skLineSegment(sketch, "E504.383", {"start": v(3.4, -9.8) * mm, "end": v(3.29, -9.86) * mm});
            skLineSegment(sketch, "E504.384", {"start": v(3.29, -9.86) * mm, "end": v(3.18, -9.92) * mm});
            skLineSegment(sketch, "E504.385", {"start": v(3.18, -9.92) * mm, "end": v(3.07, -9.98) * mm});
            skLineSegment(sketch, "E504.386", {"start": v(3.07, -9.98) * mm, "end": v(2.96, -10.03) * mm});
            skLineSegment(sketch, "E504.387", {"start": v(2.96, -10.03) * mm, "end": v(2.85, -10.1) * mm});
            skLineSegment(sketch, "E504.388", {"start": v(2.85, -10.1) * mm, "end": v(2.75, -10.15) * mm});
            skLineSegment(sketch, "E504.389", {"start": v(2.75, -10.15) * mm, "end": v(2.64, -10.2) * mm});
            skLineSegment(sketch, "E504.390", {"start": v(2.64, -10.2) * mm, "end": v(2.53, -10.25) * mm});
            skLineSegment(sketch, "E504.391", {"start": v(2.53, -10.25) * mm, "end": v(2.42, -10.3) * mm});
            skLineSegment(sketch, "E504.392", {"start": v(-7.32, 6.7) * mm, "end": v(-7.21, 6.8) * mm});
            skLineSegment(sketch, "E504.393", {"start": v(2.42, -10.3) * mm, "end": v(2.3, -10.35) * mm});
            skLineSegment(sketch, "E504.394", {"start": v(2.3, -10.35) * mm, "end": v(2.2, -10.4) * mm});
            skLineSegment(sketch, "E504.395", {"start": v(2.2, -10.4) * mm, "end": v(2.09, -10.45) * mm});
            skLineSegment(sketch, "E504.396", {"start": v(2.09, -10.45) * mm, "end": v(1.98, -10.5) * mm});
            skLineSegment(sketch, "E504.397", {"start": v(1.98, -10.5) * mm, "end": v(1.87, -10.54) * mm});
            skLineSegment(sketch, "E504.398", {"start": v(1.87, -10.54) * mm, "end": v(1.76, -10.58) * mm});
            skLineSegment(sketch, "E504.399", {"start": v(1.76, -10.58) * mm, "end": v(1.64, -10.62) * mm});
            skLineSegment(sketch, "E504.400", {"start": v(1.64, -10.62) * mm, "end": v(1.53, -10.66) * mm});
            skLineSegment(sketch, "E504.401", {"start": v(1.53, -10.66) * mm, "end": v(1.42, -10.7) * mm});
            skLineSegment(sketch, "E504.402", {"start": v(1.42, -10.7) * mm, "end": v(1.3, -10.74) * mm});
            skLineSegment(sketch, "E504.403", {"start": v(1.3, -10.74) * mm, "end": v(1.19, -10.78) * mm});
            skLineSegment(sketch, "E504.404", {"start": v(1.19, -10.78) * mm, "end": v(1.07, -10.81) * mm});
            skLineSegment(sketch, "E504.405", {"start": v(1.07, -10.81) * mm, "end": v(0.96, -10.84) * mm});
            skLineSegment(sketch, "E504.406", {"start": v(0.96, -10.84) * mm, "end": v(0.84, -10.87) * mm});
            skLineSegment(sketch, "E504.407", {"start": v(0.84, -10.87) * mm, "end": v(0.72, -10.9) * mm});
            skLineSegment(sketch, "E504.408", {"start": v(0.72, -10.9) * mm, "end": v(0.6, -10.93) * mm});
            skLineSegment(sketch, "E504.409", {"start": v(0.6, -10.93) * mm, "end": v(0.47, -10.95) * mm});
            skLineSegment(sketch, "E504.410", {"start": v(0.47, -10.95) * mm, "end": v(0.34, -10.97) * mm});
            skLineSegment(sketch, "E504.411", {"start": v(0.34, -10.97) * mm, "end": v(0.2, -10.99) * mm});
            skLineSegment(sketch, "E504.412", {"start": v(0.2, -10.99) * mm, "end": v(0, -11) * mm});
            skLineSegment(sketch, "E504.413", {"start": v(0, -11) * mm, "end": v(-0.2, -10.99) * mm});
            skLineSegment(sketch, "E504.414", {"start": v(-0.2, -10.99) * mm, "end": v(-0.34, -10.97) * mm});
            skLineSegment(sketch, "E504.415", {"start": v(-0.34, -10.97) * mm, "end": v(-0.47, -10.95) * mm});
            skLineSegment(sketch, "E504.416", {"start": v(-0.47, -10.95) * mm, "end": v(-0.6, -10.93) * mm});
            skLineSegment(sketch, "E504.417", {"start": v(-0.6, -10.93) * mm, "end": v(-0.72, -10.9) * mm});
            skLineSegment(sketch, "E504.418", {"start": v(-0.72, -10.9) * mm, "end": v(-0.84, -10.87) * mm});
            skLineSegment(sketch, "E504.419", {"start": v(-0.84, -10.87) * mm, "end": v(-0.96, -10.84) * mm});
            skLineSegment(sketch, "E504.420", {"start": v(-0.96, -10.84) * mm, "end": v(-1.07, -10.81) * mm});
            skLineSegment(sketch, "E504.421", {"start": v(-1.07, -10.81) * mm, "end": v(-1.19, -10.78) * mm});
            skLineSegment(sketch, "E504.422", {"start": v(-1.19, -10.78) * mm, "end": v(-1.3, -10.74) * mm});
            skLineSegment(sketch, "E504.423", {"start": v(-1.3, -10.74) * mm, "end": v(-1.42, -10.7) * mm});
            skLineSegment(sketch, "E504.424", {"start": v(-1.42, -10.7) * mm, "end": v(-1.53, -10.66) * mm});
            skLineSegment(sketch, "E504.425", {"start": v(-1.53, -10.66) * mm, "end": v(-1.64, -10.62) * mm});
            skLineSegment(sketch, "E504.426", {"start": v(-1.64, -10.62) * mm, "end": v(-1.76, -10.58) * mm});
            skLineSegment(sketch, "E504.427", {"start": v(-1.76, -10.58) * mm, "end": v(-1.87, -10.54) * mm});
            skLineSegment(sketch, "E504.428", {"start": v(-1.87, -10.54) * mm, "end": v(-1.98, -10.5) * mm});
            skLineSegment(sketch, "E504.429", {"start": v(-1.98, -10.5) * mm, "end": v(-2.09, -10.45) * mm});
            skLineSegment(sketch, "E504.430", {"start": v(-2.09, -10.45) * mm, "end": v(-2.2, -10.4) * mm});
            skLineSegment(sketch, "E504.431", {"start": v(-2.2, -10.4) * mm, "end": v(-2.3, -10.35) * mm});
            skLineSegment(sketch, "E504.432", {"start": v(-2.3, -10.35) * mm, "end": v(-2.42, -10.3) * mm});
            skLineSegment(sketch, "E504.433", {"start": v(-2.42, -10.3) * mm, "end": v(-2.53, -10.25) * mm});
            skLineSegment(sketch, "E504.434", {"start": v(-2.53, -10.25) * mm, "end": v(-2.64, -10.2) * mm});
            skLineSegment(sketch, "E504.435", {"start": v(-2.64, -10.2) * mm, "end": v(-2.75, -10.15) * mm});
            skLineSegment(sketch, "E504.436", {"start": v(-2.75, -10.15) * mm, "end": v(-2.85, -10.1) * mm});
            skLineSegment(sketch, "E504.437", {"start": v(-2.85, -10.1) * mm, "end": v(-2.96, -10.03) * mm});
            skLineSegment(sketch, "E504.438", {"start": v(-2.96, -10.03) * mm, "end": v(-3.07, -9.98) * mm});
            skLineSegment(sketch, "E504.439", {"start": v(-3.07, -9.98) * mm, "end": v(-3.18, -9.92) * mm});
            skLineSegment(sketch, "E504.440", {"start": v(-3.18, -9.92) * mm, "end": v(-3.29, -9.86) * mm});
            skLineSegment(sketch, "E504.441", {"start": v(-3.29, -9.86) * mm, "end": v(-3.4, -9.8) * mm});
            skLineSegment(sketch, "E504.442", {"start": v(-3.4, -9.8) * mm, "end": v(-3.5, -9.74) * mm});
            skLineSegment(sketch, "E504.443", {"start": v(-3.5, -9.74) * mm, "end": v(-3.61, -9.67) * mm});
            skLineSegment(sketch, "E504.444", {"start": v(-3.61, -9.67) * mm, "end": v(-3.72, -9.6) * mm});
            skLineSegment(sketch, "E504.445", {"start": v(-3.72, -9.6) * mm, "end": v(-3.82, -9.54) * mm});
            skLineSegment(sketch, "E504.446", {"start": v(-3.82, -9.54) * mm, "end": v(-3.93, -9.48) * mm});
            skLineSegment(sketch, "E504.447", {"start": v(-3.93, -9.48) * mm, "end": v(-4.04, -9.4) * mm});
            skLineSegment(sketch, "E504.448", {"start": v(-4.04, -9.4) * mm, "end": v(-4.15, -9.34) * mm});
            skLineSegment(sketch, "E504.449", {"start": v(-4.15, -9.34) * mm, "end": v(-4.25, -9.27) * mm});
            skLineSegment(sketch, "E504.450", {"start": v(-4.25, -9.27) * mm, "end": v(-4.36, -9.2) * mm});
            skLineSegment(sketch, "E504.451", {"start": v(-4.36, -9.2) * mm, "end": v(-4.47, -9.13) * mm});
            skLineSegment(sketch, "E504.452", {"start": v(-4.47, -9.13) * mm, "end": v(-4.57, -9.05) * mm});
            skLineSegment(sketch, "E504.453", {"start": v(-4.57, -9.05) * mm, "end": v(-4.68, -8.98) * mm});
            skLineSegment(sketch, "E504.454", {"start": v(-4.68, -8.98) * mm, "end": v(-4.78, -8.9) * mm});
            skLineSegment(sketch, "E504.455", {"start": v(-4.78, -8.9) * mm, "end": v(-4.9, -8.83) * mm});
            skLineSegment(sketch, "E504.456", {"start": v(-4.9, -8.83) * mm, "end": v(-5, -8.75) * mm});
            skLineSegment(sketch, "E504.457", {"start": v(-5, -8.75) * mm, "end": v(-5.1, -8.67) * mm});
            skLineSegment(sketch, "E504.458", {"start": v(-5.1, -8.67) * mm, "end": v(-5.2, -8.59) * mm});
            skLineSegment(sketch, "E504.459", {"start": v(-5.2, -8.59) * mm, "end": v(-5.32, -8.5) * mm});
            skLineSegment(sketch, "E504.460", {"start": v(-5.32, -8.5) * mm, "end": v(-5.42, -8.42) * mm});
            skLineSegment(sketch, "E504.461", {"start": v(-5.42, -8.42) * mm, "end": v(-5.53, -8.34) * mm});
            skLineSegment(sketch, "E504.462", {"start": v(-5.53, -8.34) * mm, "end": v(-5.63, -8.25) * mm});
            skLineSegment(sketch, "E504.463", {"start": v(-5.63, -8.25) * mm, "end": v(-5.74, -8.16) * mm});
            skLineSegment(sketch, "E504.464", {"start": v(-5.74, -8.16) * mm, "end": v(-5.84, -8.07) * mm});
            skLineSegment(sketch, "E504.465", {"start": v(-5.84, -8.07) * mm, "end": v(-5.95, -7.98) * mm});
            skLineSegment(sketch, "E504.466", {"start": v(-5.95, -7.98) * mm, "end": v(-6.06, -7.9) * mm});
            skLineSegment(sketch, "E504.467", {"start": v(-6.06, -7.9) * mm, "end": v(-6.16, -7.8) * mm});
            skLineSegment(sketch, "E504.468", {"start": v(-6.16, -7.8) * mm, "end": v(-6.27, -7.7) * mm});
            skLineSegment(sketch, "E504.469", {"start": v(-6.27, -7.7) * mm, "end": v(-6.37, -7.61) * mm});
            skLineSegment(sketch, "E504.470", {"start": v(-6.37, -7.61) * mm, "end": v(-6.48, -7.51) * mm});
            skLineSegment(sketch, "E504.471", {"start": v(-6.48, -7.51) * mm, "end": v(-6.58, -7.42) * mm});
            skLineSegment(sketch, "E504.472", {"start": v(-6.58, -7.42) * mm, "end": v(-6.7, -7.32) * mm});
            skLineSegment(sketch, "E504.473", {"start": v(-6.7, -7.32) * mm, "end": v(-6.8, -7.21) * mm});
            skLineSegment(sketch, "E504.474", {"start": v(-6.8, -7.21) * mm, "end": v(-6.9, -7.11) * mm});
            skLineSegment(sketch, "E504.475", {"start": v(-6.9, -7.11) * mm, "end": v(-7, -7) * mm});
            skLineSegment(sketch, "E504.476", {"start": v(-7, -7) * mm, "end": v(-7.11, -6.9) * mm});
            skLineSegment(sketch, "E504.477", {"start": v(-7.11, -6.9) * mm, "end": v(-7.21, -6.8) * mm});
            skLineSegment(sketch, "E504.478", {"start": v(-7.21, -6.8) * mm, "end": v(-7.32, -6.7) * mm});
            skLineSegment(sketch, "E504.479", {"start": v(-7.32, -6.7) * mm, "end": v(-7.42, -6.58) * mm});
            skLineSegment(sketch, "E504.480", {"start": v(-7.42, -6.58) * mm, "end": v(-7.51, -6.48) * mm});
            skLineSegment(sketch, "E504.481", {"start": v(-7.51, -6.48) * mm, "end": v(-7.61, -6.37) * mm});
            skLineSegment(sketch, "E504.482", {"start": v(-7.61, -6.37) * mm, "end": v(-7.7, -6.27) * mm});
            skLineSegment(sketch, "E504.483", {"start": v(-7.7, -6.27) * mm, "end": v(-7.8, -6.16) * mm});
            skLineSegment(sketch, "E504.484", {"start": v(-7.8, -6.16) * mm, "end": v(-7.9, -6.06) * mm});
            skLineSegment(sketch, "E504.485", {"start": v(-7.9, -6.06) * mm, "end": v(-7.98, -5.95) * mm});
            skLineSegment(sketch, "E504.486", {"start": v(-7.98, -5.95) * mm, "end": v(-8.07, -5.84) * mm});
            skLineSegment(sketch, "E504.487", {"start": v(-8.07, -5.84) * mm, "end": v(-8.16, -5.74) * mm});
            skLineSegment(sketch, "E504.488", {"start": v(-8.16, -5.74) * mm, "end": v(-8.25, -5.63) * mm});
            skLineSegment(sketch, "E504.489", {"start": v(-8.25, -5.63) * mm, "end": v(-8.34, -5.53) * mm});
            skLineSegment(sketch, "E504.490", {"start": v(-8.34, -5.53) * mm, "end": v(-8.42, -5.42) * mm});
            skLineSegment(sketch, "E504.491", {"start": v(-8.42, -5.42) * mm, "end": v(-8.5, -5.32) * mm});
            skLineSegment(sketch, "E504.492", {"start": v(-8.5, -5.32) * mm, "end": v(-8.59, -5.2) * mm});
            skLineSegment(sketch, "E504.493", {"start": v(-8.59, -5.2) * mm, "end": v(-8.67, -5.1) * mm});
            skLineSegment(sketch, "E504.494", {"start": v(-8.67, -5.1) * mm, "end": v(-8.75, -5) * mm});
            skLineSegment(sketch, "E504.495", {"start": v(-8.75, -5) * mm, "end": v(-8.83, -4.9) * mm});
            skLineSegment(sketch, "E504.496", {"start": v(-8.83, -4.9) * mm, "end": v(-8.9, -4.78) * mm});
            skLineSegment(sketch, "E504.497", {"start": v(-8.9, -4.78) * mm, "end": v(-8.98, -4.68) * mm});
            skLineSegment(sketch, "E504.498", {"start": v(-8.98, -4.68) * mm, "end": v(-9.05, -4.57) * mm});
            skLineSegment(sketch, "E504.499", {"start": v(-9.05, -4.57) * mm, "end": v(-9.13, -4.47) * mm});
            skLineSegment(sketch, "E504.500", {"start": v(-9.13, -4.47) * mm, "end": v(-9.2, -4.36) * mm});
            skLineSegment(sketch, "E504.501", {"start": v(-9.2, -4.36) * mm, "end": v(-9.27, -4.25) * mm});
            skLineSegment(sketch, "E504.502", {"start": v(-9.27, -4.25) * mm, "end": v(-9.34, -4.15) * mm});
            skLineSegment(sketch, "E504.503", {"start": v(-9.34, -4.15) * mm, "end": v(-9.4, -4.04) * mm});
            skSolve(sketch);
        }
        {
            var Q0;
            Q0=makeQuery(id+"F0.imprint","IMPRINT",FACE,{"disambiguationData":[TD([[makeQuery(id+"F0.imprint","IMPRINT",EDGE,{"derivedFrom":sQuery(id+"F0.wireOp",EDGE,"E0")}),-1.0]])]});
            extrude(context, id + "F1", {"entities" : qUnion([Q0]), "depth" : 2 * mm});
        }
        {
            var Q0;
            Q0=makeQuery(id+"F0.imprint","IMPRINT",FACE,{"disambiguationData":[TD([[makeQuery(id+"F0.imprint","IMPRINT",EDGE,{"derivedFrom":sQuery(id+"F0.wireOp",EDGE,"E0")}),1.0]])]});
            extrude(context, id + "F2", {"entities" : qUnion([Q0]), "operationType" : NewBodyOperationType.ADD, "depth" : 40 * mm});
        }
        {
            var Q0;
            Q0=qCreatedBy(makeId("Front.planeOp"),FACE);
            var sketch = newSketch(context, id + "F3", { "sketchPlane" : qUnion([Q0])});
            skLineSegment(sketch, "E505", {"start": v(11, 0) * mm, "end": v(11, 10) * mm});
            skLineSegment(sketch, "E506", {"start": v(11, 10) * mm, "end": v(-11, 10) * mm});
            skLineSegment(sketch, "E507", {"start": v(-11, 0) * mm, "end": v(-11, 10) * mm});
            skLineSegment(sketch, "E508", {"start": v(-11, 0.02) * mm, "end": v(-10.94, 0.05) * mm});
            skLineSegment(sketch, "E509", {"start": v(-10.94, 0.05) * mm, "end": v(-10.83, 0.1) * mm});
            skLineSegment(sketch, "E510", {"start": v(-10.83, 0.1) * mm, "end": v(-10.72, 0.16) * mm});
            skLineSegment(sketch, "E511", {"start": v(-10.72, 0.16) * mm, "end": v(-10.6, 0.2) * mm});
            skLineSegment(sketch, "E512", {"start": v(-10.6, 0.2) * mm, "end": v(-10.5, 0.26) * mm});
            skLineSegment(sketch, "E513", {"start": v(-10.5, 0.26) * mm, "end": v(-10.39, 0.31) * mm});
            skLineSegment(sketch, "E514", {"start": v(-10.39, 0.31) * mm, "end": v(-10.28, 0.36) * mm});
            skLineSegment(sketch, "E515", {"start": v(-10.28, 0.36) * mm, "end": v(-10.17, 0.41) * mm});
            skLineSegment(sketch, "E516", {"start": v(-10.17, 0.41) * mm, "end": v(-10.06, 0.46) * mm});
            skLineSegment(sketch, "E517", {"start": v(-10.06, 0.46) * mm, "end": v(-9.95, 0.51) * mm});
            skLineSegment(sketch, "E518", {"start": v(-9.95, 0.51) * mm, "end": v(-9.83, 0.56) * mm});
            skLineSegment(sketch, "E519", {"start": v(-9.83, 0.56) * mm, "end": v(-9.72, 0.61) * mm});
            skLineSegment(sketch, "E520", {"start": v(-9.72, 0.61) * mm, "end": v(-9.61, 0.66) * mm});
            skLineSegment(sketch, "E521", {"start": v(-9.61, 0.66) * mm, "end": v(-9.5, 0.7) * mm});
            skLineSegment(sketch, "E522", {"start": v(-9.5, 0.7) * mm, "end": v(-9.4, 0.75) * mm});
            skLineSegment(sketch, "E523", {"start": v(-9.4, 0.75) * mm, "end": v(-9.28, 0.8) * mm});
            skLineSegment(sketch, "E524", {"start": v(-9.28, 0.8) * mm, "end": v(-9.17, 0.84) * mm});
            skLineSegment(sketch, "E525", {"start": v(-9.17, 0.84) * mm, "end": v(-9.06, 0.89) * mm});
            skLineSegment(sketch, "E526", {"start": v(-9.06, 0.89) * mm, "end": v(-8.95, 0.93) * mm});
            skLineSegment(sketch, "E527", {"start": v(-8.95, 0.93) * mm, "end": v(-8.84, 0.97) * mm});
            skLineSegment(sketch, "E528", {"start": v(-8.84, 0.97) * mm, "end": v(-8.73, 1.02) * mm});
            skLineSegment(sketch, "E529", {"start": v(-8.73, 1.02) * mm, "end": v(-8.62, 1.06) * mm});
            skLineSegment(sketch, "E530", {"start": v(-8.62, 1.06) * mm, "end": v(-8.5, 1.1) * mm});
            skLineSegment(sketch, "E531", {"start": v(-8.5, 1.1) * mm, "end": v(-8.4, 1.13) * mm});
            skLineSegment(sketch, "E532", {"start": v(-8.4, 1.13) * mm, "end": v(-8.29, 1.17) * mm});
            skLineSegment(sketch, "E533", {"start": v(-8.29, 1.17) * mm, "end": v(-8.18, 1.2) * mm});
            skLineSegment(sketch, "E534", {"start": v(-8.18, 1.2) * mm, "end": v(-8.07, 1.24) * mm});
            skLineSegment(sketch, "E535", {"start": v(-8.07, 1.24) * mm, "end": v(-7.96, 1.28) * mm});
            skLineSegment(sketch, "E536", {"start": v(-7.96, 1.28) * mm, "end": v(-7.85, 1.3) * mm});
            skLineSegment(sketch, "E537", {"start": v(-7.85, 1.3) * mm, "end": v(-7.74, 1.34) * mm});
            skLineSegment(sketch, "E538", {"start": v(-7.74, 1.34) * mm, "end": v(-7.62, 1.37) * mm});
            skLineSegment(sketch, "E539", {"start": v(-7.62, 1.37) * mm, "end": v(-7.51, 1.4) * mm});
            skLineSegment(sketch, "E540", {"start": v(-7.51, 1.4) * mm, "end": v(-7.4, 1.43) * mm});
            skLineSegment(sketch, "E541", {"start": v(-7.4, 1.43) * mm, "end": v(-7.3, 1.45) * mm});
            skLineSegment(sketch, "E542", {"start": v(-7.3, 1.45) * mm, "end": v(-7.18, 1.48) * mm});
            skLineSegment(sketch, "E543", {"start": v(-7.18, 1.48) * mm, "end": v(-7.07, 1.5) * mm});
            skLineSegment(sketch, "E544", {"start": v(-7.07, 1.5) * mm, "end": v(-6.96, 1.52) * mm});
            skLineSegment(sketch, "E545", {"start": v(-6.96, 1.52) * mm, "end": v(-6.85, 1.54) * mm});
            skLineSegment(sketch, "E546", {"start": v(-6.85, 1.54) * mm, "end": v(-6.74, 1.56) * mm});
            skLineSegment(sketch, "E547", {"start": v(-6.74, 1.56) * mm, "end": v(-6.63, 1.58) * mm});
            skLineSegment(sketch, "E548", {"start": v(-6.63, 1.58) * mm, "end": v(-6.52, 1.6) * mm});
            skLineSegment(sketch, "E549", {"start": v(-6.52, 1.6) * mm, "end": v(-6.4, 1.6) * mm});
            skLineSegment(sketch, "E550", {"start": v(-6.4, 1.6) * mm, "end": v(-6.3, 1.62) * mm});
            skLineSegment(sketch, "E551", {"start": v(-6.3, 1.62) * mm, "end": v(-6.19, 1.63) * mm});
            skLineSegment(sketch, "E552", {"start": v(-6.19, 1.63) * mm, "end": v(-6.08, 1.64) * mm});
            skLineSegment(sketch, "E553", {"start": v(-6.08, 1.64) * mm, "end": v(-5.97, 1.64) * mm});
            skLineSegment(sketch, "E554", {"start": v(-5.97, 1.64) * mm, "end": v(-5.86, 1.65) * mm});
            skLineSegment(sketch, "E555", {"start": v(-5.86, 1.65) * mm, "end": v(-5.75, 1.65) * mm});
            skLineSegment(sketch, "E556", {"start": v(-5.75, 1.65) * mm, "end": v(-5.64, 1.66) * mm});
            skLineSegment(sketch, "E557", {"start": v(-5.64, 1.66) * mm, "end": v(-5.53, 1.66) * mm});
            skLineSegment(sketch, "E558", {"start": v(-5.53, 1.66) * mm, "end": v(-5.41, 1.66) * mm});
            skLineSegment(sketch, "E559", {"start": v(-5.41, 1.66) * mm, "end": v(-5.3, 1.65) * mm});
            skLineSegment(sketch, "E560", {"start": v(-5.3, 1.65) * mm, "end": v(-5.2, 1.65) * mm});
            skLineSegment(sketch, "E561", {"start": v(-5.2, 1.65) * mm, "end": v(-5.08, 1.64) * mm});
            skLineSegment(sketch, "E562", {"start": v(-5.08, 1.64) * mm, "end": v(-4.97, 1.64) * mm});
            skLineSegment(sketch, "E563", {"start": v(-4.97, 1.64) * mm, "end": v(-4.86, 1.63) * mm});
            skLineSegment(sketch, "E564", {"start": v(-4.86, 1.63) * mm, "end": v(-4.75, 1.62) * mm});
            skLineSegment(sketch, "E565", {"start": v(-4.75, 1.62) * mm, "end": v(-4.64, 1.6) * mm});
            skLineSegment(sketch, "E566", {"start": v(-4.64, 1.6) * mm, "end": v(-4.53, 1.6) * mm});
            skLineSegment(sketch, "E567", {"start": v(-4.53, 1.6) * mm, "end": v(-4.42, 1.58) * mm});
            skLineSegment(sketch, "E568", {"start": v(-4.42, 1.58) * mm, "end": v(-4.3, 1.56) * mm});
            skLineSegment(sketch, "E569", {"start": v(-4.3, 1.56) * mm, "end": v(-4.2, 1.54) * mm});
            skLineSegment(sketch, "E570", {"start": v(-4.2, 1.54) * mm, "end": v(-4.09, 1.52) * mm});
            skLineSegment(sketch, "E571", {"start": v(-4.09, 1.52) * mm, "end": v(-3.98, 1.5) * mm});
            skLineSegment(sketch, "E572", {"start": v(-3.98, 1.5) * mm, "end": v(-3.87, 1.48) * mm});
            skLineSegment(sketch, "E573", {"start": v(-3.87, 1.48) * mm, "end": v(-3.76, 1.45) * mm});
            skLineSegment(sketch, "E574", {"start": v(-3.76, 1.45) * mm, "end": v(-3.65, 1.43) * mm});
            skLineSegment(sketch, "E575", {"start": v(-3.65, 1.43) * mm, "end": v(-3.54, 1.4) * mm});
            skLineSegment(sketch, "E576", {"start": v(-3.54, 1.4) * mm, "end": v(-3.43, 1.37) * mm});
            skLineSegment(sketch, "E577", {"start": v(-3.43, 1.37) * mm, "end": v(-3.31, 1.34) * mm});
            skLineSegment(sketch, "E578", {"start": v(-3.31, 1.34) * mm, "end": v(-3.2, 1.3) * mm});
            skLineSegment(sketch, "E579", {"start": v(-3.2, 1.3) * mm, "end": v(-3.1, 1.28) * mm});
            skLineSegment(sketch, "E580", {"start": v(-3.1, 1.28) * mm, "end": v(-2.98, 1.24) * mm});
            skLineSegment(sketch, "E581", {"start": v(-2.98, 1.24) * mm, "end": v(-2.87, 1.2) * mm});
            skLineSegment(sketch, "E582", {"start": v(-2.87, 1.2) * mm, "end": v(-2.76, 1.17) * mm});
            skLineSegment(sketch, "E583", {"start": v(-2.76, 1.17) * mm, "end": v(-2.65, 1.13) * mm});
            skLineSegment(sketch, "E584", {"start": v(-2.65, 1.13) * mm, "end": v(-2.54, 1.1) * mm});
            skLineSegment(sketch, "E585", {"start": v(-2.54, 1.1) * mm, "end": v(-2.43, 1.06) * mm});
            skLineSegment(sketch, "E586", {"start": v(-2.43, 1.06) * mm, "end": v(-2.32, 1.02) * mm});
            skLineSegment(sketch, "E587", {"start": v(-2.32, 1.02) * mm, "end": v(-2.2, 0.97) * mm});
            skLineSegment(sketch, "E588", {"start": v(-2.2, 0.97) * mm, "end": v(-2.1, 0.93) * mm});
            skLineSegment(sketch, "E589", {"start": v(-2.1, 0.93) * mm, "end": v(-1.99, 0.89) * mm});
            skLineSegment(sketch, "E590", {"start": v(-1.99, 0.89) * mm, "end": v(-1.88, 0.84) * mm});
            skLineSegment(sketch, "E591", {"start": v(-1.88, 0.84) * mm, "end": v(-1.77, 0.8) * mm});
            skLineSegment(sketch, "E592", {"start": v(-1.77, 0.8) * mm, "end": v(-1.66, 0.75) * mm});
            skLineSegment(sketch, "E593", {"start": v(-1.66, 0.75) * mm, "end": v(-1.55, 0.7) * mm});
            skLineSegment(sketch, "E594", {"start": v(-1.55, 0.7) * mm, "end": v(-1.44, 0.66) * mm});
            skLineSegment(sketch, "E595", {"start": v(-1.44, 0.66) * mm, "end": v(-1.33, 0.61) * mm});
            skLineSegment(sketch, "E596", {"start": v(-1.33, 0.61) * mm, "end": v(-1.22, 0.56) * mm});
            skLineSegment(sketch, "E597", {"start": v(-1.22, 0.56) * mm, "end": v(-1.1, 0.51) * mm});
            skLineSegment(sketch, "E598", {"start": v(-1.1, 0.51) * mm, "end": v(-1, 0.46) * mm});
            skLineSegment(sketch, "E599", {"start": v(-1, 0.46) * mm, "end": v(-0.88, 0.41) * mm});
            skLineSegment(sketch, "E600", {"start": v(-0.88, 0.41) * mm, "end": v(-0.77, 0.36) * mm});
            skLineSegment(sketch, "E601", {"start": v(-0.77, 0.36) * mm, "end": v(-0.66, 0.31) * mm});
            skLineSegment(sketch, "E602", {"start": v(-0.66, 0.31) * mm, "end": v(-0.55, 0.26) * mm});
            skLineSegment(sketch, "E603", {"start": v(-0.55, 0.26) * mm, "end": v(-0.44, 0.2) * mm});
            skLineSegment(sketch, "E604", {"start": v(-0.44, 0.2) * mm, "end": v(-0.33, 0.16) * mm});
            skLineSegment(sketch, "E605", {"start": v(-0.33, 0.16) * mm, "end": v(-0.22, 0.1) * mm});
            skLineSegment(sketch, "E606", {"start": v(-0.22, 0.1) * mm, "end": v(-0.11, 0.05) * mm});
            skLineSegment(sketch, "E607", {"start": v(-0.11, 0.05) * mm, "end": v(0, 0) * mm});
            skLineSegment(sketch, "E608", {"start": v(0, 0) * mm, "end": v(0.11, -0.05) * mm});
            skLineSegment(sketch, "E609", {"start": v(0.11, -0.05) * mm, "end": v(0.22, -0.1) * mm});
            skLineSegment(sketch, "E610", {"start": v(0.22, -0.1) * mm, "end": v(0.33, -0.16) * mm});
            skLineSegment(sketch, "E611", {"start": v(0.33, -0.16) * mm, "end": v(0.44, -0.2) * mm});
            skLineSegment(sketch, "E612", {"start": v(0.44, -0.2) * mm, "end": v(0.55, -0.26) * mm});
            skLineSegment(sketch, "E613", {"start": v(0.55, -0.26) * mm, "end": v(0.66, -0.31) * mm});
            skLineSegment(sketch, "E614", {"start": v(0.66, -0.31) * mm, "end": v(0.77, -0.36) * mm});
            skLineSegment(sketch, "E615", {"start": v(0.77, -0.36) * mm, "end": v(0.88, -0.41) * mm});
            skLineSegment(sketch, "E616", {"start": v(0.88, -0.41) * mm, "end": v(1, -0.46) * mm});
            skLineSegment(sketch, "E617", {"start": v(1, -0.46) * mm, "end": v(1.1, -0.51) * mm});
            skLineSegment(sketch, "E618", {"start": v(1.1, -0.51) * mm, "end": v(1.22, -0.56) * mm});
            skLineSegment(sketch, "E619", {"start": v(1.22, -0.56) * mm, "end": v(1.33, -0.61) * mm});
            skLineSegment(sketch, "E620", {"start": v(1.33, -0.61) * mm, "end": v(1.44, -0.66) * mm});
            skLineSegment(sketch, "E621", {"start": v(1.44, -0.66) * mm, "end": v(1.55, -0.7) * mm});
            skLineSegment(sketch, "E622", {"start": v(1.55, -0.7) * mm, "end": v(1.66, -0.75) * mm});
            skLineSegment(sketch, "E623", {"start": v(1.66, -0.75) * mm, "end": v(1.77, -0.8) * mm});
            skLineSegment(sketch, "E624", {"start": v(1.77, -0.8) * mm, "end": v(1.88, -0.84) * mm});
            skLineSegment(sketch, "E625", {"start": v(1.88, -0.84) * mm, "end": v(1.99, -0.89) * mm});
            skLineSegment(sketch, "E626", {"start": v(1.99, -0.89) * mm, "end": v(2.1, -0.93) * mm});
            skLineSegment(sketch, "E627", {"start": v(2.1, -0.93) * mm, "end": v(2.2, -0.97) * mm});
            skLineSegment(sketch, "E628", {"start": v(2.2, -0.97) * mm, "end": v(2.32, -1.02) * mm});
            skLineSegment(sketch, "E629", {"start": v(2.32, -1.02) * mm, "end": v(2.43, -1.06) * mm});
            skLineSegment(sketch, "E630", {"start": v(2.43, -1.06) * mm, "end": v(2.54, -1.1) * mm});
            skLineSegment(sketch, "E631", {"start": v(2.54, -1.1) * mm, "end": v(2.65, -1.13) * mm});
            skLineSegment(sketch, "E632", {"start": v(2.65, -1.13) * mm, "end": v(2.76, -1.17) * mm});
            skLineSegment(sketch, "E633", {"start": v(2.76, -1.17) * mm, "end": v(2.87, -1.2) * mm});
            skLineSegment(sketch, "E634", {"start": v(2.87, -1.2) * mm, "end": v(2.98, -1.24) * mm});
            skLineSegment(sketch, "E635", {"start": v(2.98, -1.24) * mm, "end": v(3.1, -1.28) * mm});
            skLineSegment(sketch, "E636", {"start": v(3.1, -1.28) * mm, "end": v(3.2, -1.3) * mm});
            skLineSegment(sketch, "E637", {"start": v(3.2, -1.3) * mm, "end": v(3.31, -1.34) * mm});
            skLineSegment(sketch, "E638", {"start": v(3.31, -1.34) * mm, "end": v(3.43, -1.37) * mm});
            skLineSegment(sketch, "E639", {"start": v(3.43, -1.37) * mm, "end": v(3.54, -1.4) * mm});
            skLineSegment(sketch, "E640", {"start": v(3.54, -1.4) * mm, "end": v(3.65, -1.43) * mm});
            skLineSegment(sketch, "E641", {"start": v(3.65, -1.43) * mm, "end": v(3.76, -1.45) * mm});
            skLineSegment(sketch, "E642", {"start": v(3.76, -1.45) * mm, "end": v(3.87, -1.48) * mm});
            skLineSegment(sketch, "E643", {"start": v(3.87, -1.48) * mm, "end": v(3.98, -1.5) * mm});
            skLineSegment(sketch, "E644", {"start": v(3.98, -1.5) * mm, "end": v(4.09, -1.52) * mm});
            skLineSegment(sketch, "E645", {"start": v(4.09, -1.52) * mm, "end": v(4.2, -1.54) * mm});
            skLineSegment(sketch, "E646", {"start": v(4.2, -1.54) * mm, "end": v(4.3, -1.56) * mm});
            skLineSegment(sketch, "E647", {"start": v(4.3, -1.56) * mm, "end": v(4.42, -1.58) * mm});
            skLineSegment(sketch, "E648", {"start": v(4.42, -1.58) * mm, "end": v(4.53, -1.6) * mm});
            skLineSegment(sketch, "E649", {"start": v(4.53, -1.6) * mm, "end": v(4.64, -1.6) * mm});
            skLineSegment(sketch, "E650", {"start": v(4.64, -1.6) * mm, "end": v(4.75, -1.62) * mm});
            skLineSegment(sketch, "E651", {"start": v(4.75, -1.62) * mm, "end": v(4.86, -1.63) * mm});
            skLineSegment(sketch, "E652", {"start": v(4.86, -1.63) * mm, "end": v(4.97, -1.64) * mm});
            skLineSegment(sketch, "E653", {"start": v(4.97, -1.64) * mm, "end": v(5.08, -1.64) * mm});
            skLineSegment(sketch, "E654", {"start": v(5.08, -1.64) * mm, "end": v(5.2, -1.65) * mm});
            skLineSegment(sketch, "E655", {"start": v(5.2, -1.65) * mm, "end": v(5.3, -1.65) * mm});
            skLineSegment(sketch, "E656", {"start": v(5.3, -1.65) * mm, "end": v(5.41, -1.66) * mm});
            skLineSegment(sketch, "E657", {"start": v(5.41, -1.66) * mm, "end": v(5.53, -1.66) * mm});
            skLineSegment(sketch, "E658", {"start": v(5.53, -1.66) * mm, "end": v(5.64, -1.66) * mm});
            skLineSegment(sketch, "E659", {"start": v(5.64, -1.66) * mm, "end": v(5.75, -1.65) * mm});
            skLineSegment(sketch, "E660", {"start": v(5.75, -1.65) * mm, "end": v(5.86, -1.65) * mm});
            skLineSegment(sketch, "E661", {"start": v(5.86, -1.65) * mm, "end": v(5.97, -1.64) * mm});
            skLineSegment(sketch, "E662", {"start": v(5.97, -1.64) * mm, "end": v(6.08, -1.64) * mm});
            skLineSegment(sketch, "E663", {"start": v(6.08, -1.64) * mm, "end": v(6.19, -1.63) * mm});
            skLineSegment(sketch, "E664", {"start": v(6.19, -1.63) * mm, "end": v(6.3, -1.62) * mm});
            skLineSegment(sketch, "E665", {"start": v(6.3, -1.62) * mm, "end": v(6.4, -1.6) * mm});
            skLineSegment(sketch, "E666", {"start": v(6.4, -1.6) * mm, "end": v(6.52, -1.6) * mm});
            skLineSegment(sketch, "E667", {"start": v(6.52, -1.6) * mm, "end": v(6.63, -1.58) * mm});
            skLineSegment(sketch, "E668", {"start": v(6.63, -1.58) * mm, "end": v(6.74, -1.56) * mm});
            skLineSegment(sketch, "E669", {"start": v(6.74, -1.56) * mm, "end": v(6.85, -1.54) * mm});
            skLineSegment(sketch, "E670", {"start": v(6.85, -1.54) * mm, "end": v(6.96, -1.52) * mm});
            skLineSegment(sketch, "E671", {"start": v(6.96, -1.52) * mm, "end": v(7.07, -1.5) * mm});
            skLineSegment(sketch, "E672", {"start": v(7.07, -1.5) * mm, "end": v(7.18, -1.48) * mm});
            skLineSegment(sketch, "E673", {"start": v(7.18, -1.48) * mm, "end": v(7.3, -1.45) * mm});
            skLineSegment(sketch, "E674", {"start": v(7.3, -1.45) * mm, "end": v(7.4, -1.43) * mm});
            skLineSegment(sketch, "E675", {"start": v(7.4, -1.43) * mm, "end": v(7.51, -1.4) * mm});
            skLineSegment(sketch, "E676", {"start": v(7.51, -1.4) * mm, "end": v(7.62, -1.37) * mm});
            skLineSegment(sketch, "E677", {"start": v(7.62, -1.37) * mm, "end": v(7.74, -1.34) * mm});
            skLineSegment(sketch, "E678", {"start": v(7.74, -1.34) * mm, "end": v(7.85, -1.3) * mm});
            skLineSegment(sketch, "E679", {"start": v(7.85, -1.3) * mm, "end": v(7.96, -1.28) * mm});
            skLineSegment(sketch, "E680", {"start": v(7.96, -1.28) * mm, "end": v(8.07, -1.24) * mm});
            skLineSegment(sketch, "E681", {"start": v(8.07, -1.24) * mm, "end": v(8.18, -1.2) * mm});
            skLineSegment(sketch, "E682", {"start": v(8.18, -1.2) * mm, "end": v(8.29, -1.17) * mm});
            skLineSegment(sketch, "E683", {"start": v(8.29, -1.17) * mm, "end": v(8.4, -1.13) * mm});
            skLineSegment(sketch, "E684", {"start": v(8.4, -1.13) * mm, "end": v(8.5, -1.1) * mm});
            skLineSegment(sketch, "E685", {"start": v(8.5, -1.1) * mm, "end": v(8.62, -1.06) * mm});
            skLineSegment(sketch, "E686", {"start": v(8.62, -1.06) * mm, "end": v(8.73, -1.02) * mm});
            skLineSegment(sketch, "E687", {"start": v(8.73, -1.02) * mm, "end": v(8.84, -0.97) * mm});
            skLineSegment(sketch, "E688", {"start": v(8.84, -0.97) * mm, "end": v(8.95, -0.93) * mm});
            skLineSegment(sketch, "E689", {"start": v(8.95, -0.93) * mm, "end": v(9.06, -0.89) * mm});
            skLineSegment(sketch, "E690", {"start": v(9.06, -0.89) * mm, "end": v(9.17, -0.84) * mm});
            skLineSegment(sketch, "E691", {"start": v(9.17, -0.84) * mm, "end": v(9.28, -0.8) * mm});
            skLineSegment(sketch, "E692", {"start": v(9.28, -0.8) * mm, "end": v(9.4, -0.75) * mm});
            skLineSegment(sketch, "E693", {"start": v(9.4, -0.75) * mm, "end": v(9.5, -0.7) * mm});
            skLineSegment(sketch, "E694", {"start": v(9.5, -0.7) * mm, "end": v(9.61, -0.66) * mm});
            skLineSegment(sketch, "E695", {"start": v(9.61, -0.66) * mm, "end": v(9.72, -0.61) * mm});
            skLineSegment(sketch, "E696", {"start": v(9.72, -0.61) * mm, "end": v(9.83, -0.56) * mm});
            skLineSegment(sketch, "E697", {"start": v(9.83, -0.56) * mm, "end": v(9.95, -0.51) * mm});
            skLineSegment(sketch, "E698", {"start": v(9.95, -0.51) * mm, "end": v(10.06, -0.46) * mm});
            skLineSegment(sketch, "E699", {"start": v(10.06, -0.46) * mm, "end": v(10.17, -0.41) * mm});
            skLineSegment(sketch, "E700", {"start": v(10.17, -0.41) * mm, "end": v(10.28, -0.36) * mm});
            skLineSegment(sketch, "E701", {"start": v(10.28, -0.36) * mm, "end": v(10.39, -0.31) * mm});
            skLineSegment(sketch, "E702", {"start": v(10.39, -0.31) * mm, "end": v(10.5, -0.26) * mm});
            skLineSegment(sketch, "E703", {"start": v(10.5, -0.26) * mm, "end": v(10.6, -0.2) * mm});
            skLineSegment(sketch, "E704", {"start": v(10.6, -0.2) * mm, "end": v(10.72, -0.16) * mm});
            skLineSegment(sketch, "E705", {"start": v(10.72, -0.16) * mm, "end": v(10.83, -0.1) * mm});
            skLineSegment(sketch, "E706", {"start": v(10.83, -0.1) * mm, "end": v(10.94, -0.05) * mm});
            skLineSegment(sketch, "E707", {"start": v(10.94, -0.05) * mm, "end": v(11.05, 0) * mm});
            skLineSegment(sketch, "E708", {"start": v(11, 0) * mm, "end": v(11, -0.02) * mm});
            skSolve(sketch);
        }
        {
            var Q0;
            Q0=makeQuery(id+"F3.imprint","IMPRINT",FACE,{"disambiguationData":[TD([[makeQuery(id+"F3.imprint","IMPRINT",EDGE,{"derivedFrom":sQuery(id+"F3.wireOp",EDGE,"E505")}),1.0]])]});
            extrude(context, id + "F4", {"entities" : qUnion([Q0]), "endBound" : BoundingType.SYMMETRIC, "depth" : 22 * mm});
        }
        {
            var Q0;
            Q0=makeQuery(id+"F4.opExtrude","SWEPT_BODY",BODY,{"disambiguationData":[OSD([sQuery(id+"F3.wireOp",EDGE,"ec41ae91-4df3-4674-b230-51135a62c841"),sQuery(id+"F3.wireOp",EDGE,"4915715a-3651-4802-93b2-976e28617991"),sQuery(id+"F3.wireOp",EDGE,"f15b2dd7-0a66-4c35-9b3a-76401d213128"),sQuery(id+"F3.wireOp",EDGE,"573a967d-7325-43e2-a310-91cf087eee18"),sQuery(id+"F3.wireOp",EDGE,"9829493d-dd2b-4d5e-a350-835d0b1967f8"),sQuery(id+"F3.wireOp",EDGE,"88a4fc78-4b8c-41cb-8199-d79f3d1a214f"),sQuery(id+"F3.wireOp",EDGE,"29e99f44-44dd-4ffa-b92d-bba17bea5d43"),sQuery(id+"F3.wireOp",EDGE,"08ec9610-4828-42c1-afa1-523aa55121be"),sQuery(id+"F3.wireOp",EDGE,"310ca9a3-fa69-468b-bae4-7742a02260ce"),sQuery(id+"F3.wireOp",EDGE,"1d81bcbc-7ed6-437a-9b34-64fc4b10475f"),sQuery(id+"F3.wireOp",EDGE,"7f1e7079-6e3e-4c6c-b9ef-b52a12ea813f"),sQuery(id+"F3.wireOp",EDGE,"e228bb15-0659-4b2b-91ba-388ef41ebd05"),sQuery(id+"F3.wireOp",EDGE,"2d2180e8-ce33-4739-9b09-17b5a1027c62"),sQuery(id+"F3.wireOp",EDGE,"8b5c6718-2d56-4e57-8b99-38efbef745b3"),sQuery(id+"F3.wireOp",EDGE,"da9e38a8-24f9-4dcf-82ff-eaedfc7ddac3"),sQuery(id+"F3.wireOp",EDGE,"3ed522c3-f551-4994-8af4-595096df8cab"),sQuery(id+"F3.wireOp",EDGE,"e3721c90-3ca1-4829-a1f0-4940f097088d"),sQuery(id+"F3.wireOp",EDGE,"e5858ef7-01e1-460b-9e1d-db8dee7450b7"),sQuery(id+"F3.wireOp",EDGE,"0b6d586f-89af-404d-9c45-8ac8a14e0f9f"),sQuery(id+"F3.wireOp",EDGE,"fdba9b58-a7c2-45ac-83c7-755c0024fe7c"),sQuery(id+"F3.wireOp",EDGE,"ef9297e6-c259-49a8-9986-bae6039550b3"),sQuery(id+"F3.wireOp",EDGE,"585c6f1e-c7aa-4b45-99f9-8ab2b20ae877"),sQuery(id+"F3.wireOp",EDGE,"6ead3385-f5af-4ced-bf6c-b98b03284e5d"),sQuery(id+"F3.wireOp",EDGE,"6cfa191d-58e2-4e74-a0ee-c94a68ea9b2d"),sQuery(id+"F3.wireOp",EDGE,"5f7c7bd5-4c1a-4aa2-a292-2ab4f57ae713"),sQuery(id+"F3.wireOp",EDGE,"4b36cdfc-4ed1-4727-9cce-d396c96bae2d"),sQuery(id+"F3.wireOp",EDGE,"ec7c89eb-33f3-4467-bb85-bf3e0787b498"),sQuery(id+"F3.wireOp",EDGE,"ca737aa9-3395-43b0-976a-56014d1f073b"),sQuery(id+"F3.wireOp",EDGE,"8b121f98-3189-41c8-99d6-237662d45c4a"),sQuery(id+"F3.wireOp",EDGE,"e15d9de9-761b-4ebb-85e4-fb4da82fe0c1"),sQuery(id+"F3.wireOp",EDGE,"7ad34d33-c3e0-4451-9494-264813b44421"),sQuery(id+"F3.wireOp",EDGE,"67097021-bec9-466b-973d-5e6d45f4df4b"),sQuery(id+"F3.wireOp",EDGE,"00a890b4-48cc-4d89-b077-d2e06b7e5dbd"),sQuery(id+"F3.wireOp",EDGE,"d7c93b06-eb0f-47ea-baf6-846be92fd260"),sQuery(id+"F3.wireOp",EDGE,"a2e0747d-17c9-4fc1-8cc4-fdaf8f8abfb8"),sQuery(id+"F3.wireOp",EDGE,"3372003e-2229-4558-92bf-d17431c63efe"),sQuery(id+"F3.wireOp",EDGE,"a3b7acfd-c5e1-4a2a-8837-4aa7ee2b56f2"),sQuery(id+"F3.wireOp",EDGE,"3a959202-a4c0-400d-9680-62f35a8281c4"),sQuery(id+"F3.wireOp",EDGE,"a8ddc96f-2760-4d3c-8c77-f7573f30c19d"),sQuery(id+"F3.wireOp",EDGE,"a7586bee-e7f3-42ba-b3eb-820e0c658ff0"),sQuery(id+"F3.wireOp",EDGE,"b1cc2dc8-0320-49c9-bff7-099614d47ec2"),sQuery(id+"F3.wireOp",EDGE,"8457c3d1-b865-450b-adf8-14351497ea25"),sQuery(id+"F3.wireOp",EDGE,"98e9128e-370b-4b50-baf2-f15997247181"),sQuery(id+"F3.wireOp",EDGE,"8a87dfde-57a5-43ec-bda8-da6793a18b73"),sQuery(id+"F3.wireOp",EDGE,"afad9ccd-78bf-4ea0-9416-078eea4e9aa8"),sQuery(id+"F3.wireOp",EDGE,"466440c7-c3a5-4f11-b76c-acbc010caadf"),sQuery(id+"F3.wireOp",EDGE,"802f05ca-83e2-4aad-b0e9-72984b1bff10"),sQuery(id+"F3.wireOp",EDGE,"380c98ad-3319-44b2-9d8b-94ab420c3658"),sQuery(id+"F3.wireOp",EDGE,"a3769aee-8604-4823-b0d7-44a8c97383a4"),sQuery(id+"F3.wireOp",EDGE,"1f52d996-aca9-497a-b7e2-600370ae6949"),sQuery(id+"F3.wireOp",EDGE,"67b67c53-8780-4a85-a3f5-8daf53ab2c04"),sQuery(id+"F3.wireOp",EDGE,"f16f5723-851b-4393-9b75-be1a9d8f5853"),sQuery(id+"F3.wireOp",EDGE,"bb383e53-8237-49ad-9faf-dc4e0ce0de8c"),sQuery(id+"F3.wireOp",EDGE,"7ec6589b-37b5-4f7e-8b9c-d80ded9de812"),sQuery(id+"F3.wireOp",EDGE,"08880140-c83c-486f-b26b-0da67e4ff0c8"),sQuery(id+"F3.wireOp",EDGE,"999823e5-c0bd-483c-88d5-3655cf2a24eb"),sQuery(id+"F3.wireOp",EDGE,"07b7ce3e-532a-4886-a937-3375ccde0f0e"),sQuery(id+"F3.wireOp",EDGE,"9dc5ff66-08db-4f58-bb2d-51863b145979"),sQuery(id+"F3.wireOp",EDGE,"eceeb68e-c3d4-4b94-b62d-56caa49e50b4"),sQuery(id+"F3.wireOp",EDGE,"f41b9d86-6198-4803-9e05-c2d42cc78262"),sQuery(id+"F3.wireOp",EDGE,"0ff7a2ec-16ac-4922-a147-e8dcbe953c89"),sQuery(id+"F3.wireOp",EDGE,"a5f3f9c6-b258-48e6-ac81-471d37944c80"),sQuery(id+"F3.wireOp",EDGE,"5d3368fa-4b93-4609-8d85-d76e8ccb9f70"),sQuery(id+"F3.wireOp",EDGE,"93e705d2-6a1b-4fd1-98fa-f7101df4e23e"),sQuery(id+"F3.wireOp",EDGE,"8560622e-69b7-4d5e-9719-021d16e605a7"),sQuery(id+"F3.wireOp",EDGE,"1269a461-9fb2-497b-9541-76a3c22068ad"),sQuery(id+"F3.wireOp",EDGE,"738108aa-f0e9-4788-8b29-18c751f9aff9"),sQuery(id+"F3.wireOp",EDGE,"c65de39b-1758-467b-980b-9cd9929a3d64"),sQuery(id+"F3.wireOp",EDGE,"756d41d9-dbab-496a-ae15-4fc1659277d1"),sQuery(id+"F3.wireOp",EDGE,"bac2d005-4ac7-492e-a373-e2c006eb4bfb"),sQuery(id+"F3.wireOp",EDGE,"85860d99-9013-4759-aa43-5487a99c41a6"),sQuery(id+"F3.wireOp",EDGE,"8b924ac3-f2a5-4087-bc70-23e4203bc6ae"),sQuery(id+"F3.wireOp",EDGE,"0916d5f8-d38e-4792-80fc-1789f880af75"),sQuery(id+"F3.wireOp",EDGE,"a8e22637-be16-4ef6-ae94-6b23f87871d8"),sQuery(id+"F3.wireOp",EDGE,"63b035c0-ac75-420b-bf11-3ed09439bdeb"),sQuery(id+"F3.wireOp",EDGE,"b31ee2f9-b45b-4c92-b652-2d6a6fa9c3c5"),sQuery(id+"F3.wireOp",EDGE,"97893759-3520-4bf3-a33f-99cd94809b8e"),sQuery(id+"F3.wireOp",EDGE,"5b4603d3-bafa-43cc-99d2-3470666ae78c"),sQuery(id+"F3.wireOp",EDGE,"5dc276c1-ad75-4351-9532-710b6f957b72"),sQuery(id+"F3.wireOp",EDGE,"36f0a240-2e3b-4426-aa0a-071803ecff03"),sQuery(id+"F3.wireOp",EDGE,"57a6f11b-a6b4-4852-9993-7efa1ac7adaf"),sQuery(id+"F3.wireOp",EDGE,"754e6465-131f-4ec7-94bb-14c8c9e997d9"),sQuery(id+"F3.wireOp",EDGE,"34610aa0-aea1-4ba5-b03d-e18f9e4dd988"),sQuery(id+"F3.wireOp",EDGE,"5ea570f2-0fa4-4e78-adeb-6f516147bd71"),sQuery(id+"F3.wireOp",EDGE,"a26f9c50-1319-4f95-9820-85724e840a82"),sQuery(id+"F3.wireOp",EDGE,"0f090b8e-50f8-4d2c-bafe-bdde45b5ada4"),sQuery(id+"F3.wireOp",EDGE,"7117585e-1228-4300-a3e4-db51f78ee14c"),sQuery(id+"F3.wireOp",EDGE,"f8689b3f-eda0-439f-be03-f97530164dd3"),sQuery(id+"F3.wireOp",EDGE,"203b92fc-7d6b-43b1-989f-c26bb414d1b2"),sQuery(id+"F3.wireOp",EDGE,"5679199e-b528-48c1-b11b-944558c980a8"),sQuery(id+"F3.wireOp",EDGE,"161a3187-e8c9-4983-85cb-49f6f7c5f339"),sQuery(id+"F3.wireOp",EDGE,"a6bb4c2e-d0b8-44ae-8978-b823822b2f62"),sQuery(id+"F3.wireOp",EDGE,"04610945-ebf1-46a7-939e-e9ad5c23b445"),sQuery(id+"F3.wireOp",EDGE,"39c5cceb-1e69-460b-a124-bfb35590148b"),sQuery(id+"F3.wireOp",EDGE,"0cac30ec-ac55-47a7-846b-215a65482ff4"),sQuery(id+"F3.wireOp",EDGE,"18e99eaa-199b-443f-9dbd-6b716a5c9e1a"),sQuery(id+"F3.wireOp",EDGE,"17e41e31-d35b-450a-824b-3514a620a768"),sQuery(id+"F3.wireOp",EDGE,"0524b4ea-f730-407d-9352-39bf46fc0a80"),sQuery(id+"F3.wireOp",EDGE,"0f5f3ec3-e111-4418-b32e-94214185c3f1"),sQuery(id+"F3.wireOp",EDGE,"f23df1d5-483b-4032-8ad5-835132419385"),sQuery(id+"F3.wireOp",EDGE,"45bb317c-8eae-478e-b6d9-0e3c22a77cd0"),sQuery(id+"F3.wireOp",EDGE,"bfa43031-806e-4edd-9d98-8f8031f24426"),sQuery(id+"F3.wireOp",EDGE,"f36d8605-259b-4c9b-a64e-53b25295e8f3"),sQuery(id+"F3.wireOp",EDGE,"aff81085-56e9-4dfb-b6c6-55d1b18e30ec"),sQuery(id+"F3.wireOp",EDGE,"64adf307-3694-4edf-9718-bdfb3c99b58e"),sQuery(id+"F3.wireOp",EDGE,"25b1a257-ab12-4c00-be89-3991f43899a6"),sQuery(id+"F3.wireOp",EDGE,"aea91b0e-bcb3-49ee-815e-f65bcd86e2fd"),sQuery(id+"F3.wireOp",EDGE,"dbcc5a10-4f3a-4c7a-88d6-be6ad4de9be3"),sQuery(id+"F3.wireOp",EDGE,"1300bb3d-7ac1-4f9a-91f7-a402756fa661"),sQuery(id+"F3.wireOp",EDGE,"977e18cc-96be-430d-abcb-59930a13b9f0"),sQuery(id+"F3.wireOp",EDGE,"6ba64014-859f-4af9-984d-7bedc4939d73"),sQuery(id+"F3.wireOp",EDGE,"a11d0871-7a20-44ed-b7c6-c8352198d685"),sQuery(id+"F3.wireOp",EDGE,"54e6f65c-df59-4b21-ab87-efc42813dc94"),sQuery(id+"F3.wireOp",EDGE,"f40db9cc-ce06-4c69-89d1-d6fb42ef8d4b"),sQuery(id+"F3.wireOp",EDGE,"290e4a50-9f37-415d-a77d-bcc76523f1d5"),sQuery(id+"F3.wireOp",EDGE,"9830cdb9-701e-436b-837d-810825575392"),sQuery(id+"F3.wireOp",EDGE,"c7a824f2-db51-401e-825b-f3d6b21fe486"),sQuery(id+"F3.wireOp",EDGE,"ad94afe7-f28e-4b73-8a1f-55e2296c2bca"),sQuery(id+"F3.wireOp",EDGE,"084e083d-f148-4afa-b33f-1a4e602a2cd3"),sQuery(id+"F3.wireOp",EDGE,"bd15d313-7969-47b0-a722-98a9e6f22b08"),sQuery(id+"F3.wireOp",EDGE,"cc41519e-33da-4bbe-b848-f50a6c4e3b84"),sQuery(id+"F3.wireOp",EDGE,"ef344dea-b100-4b94-8c68-aa645f94dcae"),sQuery(id+"F3.wireOp",EDGE,"5a8aaeff-4269-443b-ae8b-5febe453ce12"),sQuery(id+"F3.wireOp",EDGE,"bd50b30f-2b72-4484-bc14-e42f99e813fa"),sQuery(id+"F3.wireOp",EDGE,"df1e4ad1-31e9-48e5-81d7-2711f6055c90"),sQuery(id+"F3.wireOp",EDGE,"ae18261a-30a3-4fc6-b873-f9da53a0b074"),sQuery(id+"F3.wireOp",EDGE,"855ca772-78cf-44b3-8a8b-1af7bb703fff"),sQuery(id+"F3.wireOp",EDGE,"a3449970-7c4b-402d-9747-1e28fc93d780"),sQuery(id+"F3.wireOp",EDGE,"c398989f-697f-4569-b9cd-5a2f5c0afdfa"),sQuery(id+"F3.wireOp",EDGE,"be9c560b-05f3-44fc-9c24-5fb0ee9f46be"),sQuery(id+"F3.wireOp",EDGE,"6fb91335-0444-47dc-9a68-f012f8e9e497"),sQuery(id+"F3.wireOp",EDGE,"d4280811-013f-4bce-ad33-1f82742e0dd9"),sQuery(id+"F3.wireOp",EDGE,"0b1bd235-f05c-4c19-962e-4f72b657b4a9"),sQuery(id+"F3.wireOp",EDGE,"6ecc38b7-87ea-4faf-bea4-6a361bf0c5f1"),sQuery(id+"F3.wireOp",EDGE,"93b60800-9d39-4d9f-8d8b-3e53798cad8d"),sQuery(id+"F3.wireOp",EDGE,"bc0c8946-68bd-4333-991b-e604499cce4a"),sQuery(id+"F3.wireOp",EDGE,"03ec03ef-69c7-4f14-a4be-1943b1b26620"),sQuery(id+"F3.wireOp",EDGE,"70288df1-7fe0-44d6-81a0-38b7c6254652"),sQuery(id+"F3.wireOp",EDGE,"373aa3d3-7813-439a-aa6d-11bf33d8b24e"),sQuery(id+"F3.wireOp",EDGE,"45d8d8cd-c432-46a9-ba83-ca98e6a8b331"),sQuery(id+"F3.wireOp",EDGE,"30eeae1c-e414-4273-926e-a242566325a0"),sQuery(id+"F3.wireOp",EDGE,"2c9bb13c-11d4-40b6-bcc6-d08f2723e091"),sQuery(id+"F3.wireOp",EDGE,"a482991e-2cf6-48ab-8e8e-3e4f8b67d4b7"),sQuery(id+"F3.wireOp",EDGE,"06891698-4df7-4f94-84c6-72103b62673b"),sQuery(id+"F3.wireOp",EDGE,"ecab2fa4-6225-467e-82ee-4732fa611de3"),sQuery(id+"F3.wireOp",EDGE,"649bfd1a-9215-4127-87d3-ed0b3f5772d5"),sQuery(id+"F3.wireOp",EDGE,"bf54d2c0-65f1-4ff6-871b-ae601eb9e7cc"),sQuery(id+"F3.wireOp",EDGE,"29274e08-d376-4eb2-907f-b860139ca4db"),sQuery(id+"F3.wireOp",EDGE,"cd2404f3-3954-470e-aa5a-a76806b6835a"),sQuery(id+"F3.wireOp",EDGE,"dbd5f9e9-56cf-4ed4-a9fb-97d5f2897854"),sQuery(id+"F3.wireOp",EDGE,"a3f94ff5-44de-4570-8f07-2fa58cf7f771"),sQuery(id+"F3.wireOp",EDGE,"21d034b1-97d0-4cdd-a783-b5eef86ebc99"),sQuery(id+"F3.wireOp",EDGE,"a60bbc0a-156d-4d16-82fa-9e5e5c2e844d"),sQuery(id+"F3.wireOp",EDGE,"a528a1a4-90cb-4bac-a68a-6d2da3dfac97"),sQuery(id+"F3.wireOp",EDGE,"2897741f-4c31-4951-9326-161b0945bc72"),sQuery(id+"F3.wireOp",EDGE,"138138aa-b9e4-4038-8e12-b0c5a13fea39"),sQuery(id+"F3.wireOp",EDGE,"8187800a-b1e6-4d83-98c7-9c355a36d6c6"),sQuery(id+"F3.wireOp",EDGE,"9701c027-796e-4d6b-a002-6605f6ee80e3"),sQuery(id+"F3.wireOp",EDGE,"77e98c07-d0dc-4f04-9c1b-99f3355fd8a7"),sQuery(id+"F3.wireOp",EDGE,"4d81288f-f128-4ca3-b627-6a5b28d496de"),sQuery(id+"F3.wireOp",EDGE,"d1bad90c-4b8f-41a3-ac4a-47f6b9aadffb"),sQuery(id+"F3.wireOp",EDGE,"ed70a943-00e2-466a-98de-2b8f6be6381d"),sQuery(id+"F3.wireOp",EDGE,"ca15953e-95cc-4037-b944-8707390692ef"),sQuery(id+"F3.wireOp",EDGE,"d795c5ca-c7fa-4fa3-aceb-2aaa567452cf"),sQuery(id+"F3.wireOp",EDGE,"243c0ca0-aa5e-4f5e-bdca-16c8987a887f"),sQuery(id+"F3.wireOp",EDGE,"bc9fa2c3-366d-471d-97c7-70100b7d8498"),sQuery(id+"F3.wireOp",EDGE,"504d9464-3638-4fca-aca5-74d973fcd556"),sQuery(id+"F3.wireOp",EDGE,"904397ff-7935-4a86-961c-5e675a147941"),sQuery(id+"F3.wireOp",EDGE,"1c96a42e-db33-464e-939b-1401c8f3dc56"),sQuery(id+"F3.wireOp",EDGE,"c93a136a-b456-4118-8f96-0ff909422201"),sQuery(id+"F3.wireOp",EDGE,"18e409b6-aa76-48e1-b07a-2118d4afb836"),sQuery(id+"F3.wireOp",EDGE,"453d7378-4718-464e-bd01-99f678aa0ea9"),sQuery(id+"F3.wireOp",EDGE,"7a3a24a2-148e-4b54-a0ad-eba860c7fb7a"),sQuery(id+"F3.wireOp",EDGE,"8ef3a38d-664a-40d3-aa3a-b2176ce58029"),sQuery(id+"F3.wireOp",EDGE,"431eb4cf-7232-4f15-8871-3b81c8abfe77"),sQuery(id+"F3.wireOp",EDGE,"6c5b3992-7da6-44e2-8879-de97f4632d9e"),sQuery(id+"F3.wireOp",EDGE,"700eb462-5239-4aff-bb8e-38754561fb95"),sQuery(id+"F3.wireOp",EDGE,"76e36e64-b254-46aa-a38f-830b3794fe19"),sQuery(id+"F3.wireOp",EDGE,"7d77c6f3-f087-4291-933e-8eee58b8f264"),sQuery(id+"F3.wireOp",EDGE,"26ca988e-826e-47f0-98d2-556df3f9bf42"),sQuery(id+"F3.wireOp",EDGE,"4810f180-f491-4bec-8c84-57ef4a51e416"),sQuery(id+"F3.wireOp",EDGE,"a2f87652-967a-430d-baa5-b94727ffa003"),sQuery(id+"F3.wireOp",EDGE,"d08c92d7-9c6d-4fd1-b266-1e49aef11731"),sQuery(id+"F3.wireOp",EDGE,"60113931-40ab-4c1d-a52c-fd4caa2a44f1"),sQuery(id+"F3.wireOp",EDGE,"b1aa1ff4-0d0d-408d-8a15-147b6324842e"),sQuery(id+"F3.wireOp",EDGE,"38f109ba-2aae-4bc4-9a22-f038beb12030"),sQuery(id+"F3.wireOp",EDGE,"7441d3f1-614a-426d-b871-a4e1a13c6e7e"),sQuery(id+"F3.wireOp",EDGE,"847a2f50-4ef1-49b5-b090-5f8521ee8ca1"),sQuery(id+"F3.wireOp",EDGE,"98bd5360-29b1-4412-9294-02ef6551eecc"),sQuery(id+"F3.wireOp",EDGE,"cb6e78c9-5cdf-4276-b840-5cfec84caed4"),sQuery(id+"F3.wireOp",EDGE,"1736b3be-cda2-4842-aefb-283565cc4c62"),sQuery(id+"F3.wireOp",EDGE,"438710e5-800b-4df2-8fff-3432d8aae595"),sQuery(id+"F3.wireOp",EDGE,"f69e7794-4715-43f7-a271-aa5e98ef7e68"),sQuery(id+"F3.wireOp",EDGE,"02c9a714-cd92-4f6e-be60-84f6aca8f508"),sQuery(id+"F3.wireOp",EDGE,"e0730c34-1f26-4745-a30f-e9a291eaeb6f"),sQuery(id+"F3.wireOp",EDGE,"9554880d-9851-4e54-af44-454a4419ca75"),sQuery(id+"F3.wireOp",EDGE,"efb41e31-abb5-42fa-83db-f78bf43b7196"),sQuery(id+"F3.wireOp",EDGE,"1bdde1b5-8417-49bf-b267-4e22f08aa6f4"),sQuery(id+"F3.wireOp",EDGE,"72509248-fad9-462b-b756-80664d0faace"),sQuery(id+"F3.wireOp",EDGE,"76f0ff31-d45f-4a8a-86ee-2e308ecada5a"),sQuery(id+"F3.wireOp",EDGE,"E505"),sQuery(id+"F3.wireOp",EDGE,"E506"),sQuery(id+"F3.wireOp",EDGE,"E507")])]});
            transform(context, id + "F5", {"entities" : qUnion([Q0]), "transformType" : TransformType.TRANSLATION_3D, "dx" : 0 * mm, "dy" : 0 * mm, "dz" : 40 * mm, "makeCopy" : false});
        }
        {
            var Q0;
            Q0=makeQuery(id+"F4.opExtrude","SWEPT_BODY",BODY,{"disambiguationData":[OSD([sQuery(id+"F3.wireOp",EDGE,"ec41ae91-4df3-4674-b230-51135a62c841"),sQuery(id+"F3.wireOp",EDGE,"4915715a-3651-4802-93b2-976e28617991"),sQuery(id+"F3.wireOp",EDGE,"f15b2dd7-0a66-4c35-9b3a-76401d213128"),sQuery(id+"F3.wireOp",EDGE,"573a967d-7325-43e2-a310-91cf087eee18"),sQuery(id+"F3.wireOp",EDGE,"9829493d-dd2b-4d5e-a350-835d0b1967f8"),sQuery(id+"F3.wireOp",EDGE,"88a4fc78-4b8c-41cb-8199-d79f3d1a214f"),sQuery(id+"F3.wireOp",EDGE,"29e99f44-44dd-4ffa-b92d-bba17bea5d43"),sQuery(id+"F3.wireOp",EDGE,"08ec9610-4828-42c1-afa1-523aa55121be"),sQuery(id+"F3.wireOp",EDGE,"310ca9a3-fa69-468b-bae4-7742a02260ce"),sQuery(id+"F3.wireOp",EDGE,"1d81bcbc-7ed6-437a-9b34-64fc4b10475f"),sQuery(id+"F3.wireOp",EDGE,"7f1e7079-6e3e-4c6c-b9ef-b52a12ea813f"),sQuery(id+"F3.wireOp",EDGE,"e228bb15-0659-4b2b-91ba-388ef41ebd05"),sQuery(id+"F3.wireOp",EDGE,"2d2180e8-ce33-4739-9b09-17b5a1027c62"),sQuery(id+"F3.wireOp",EDGE,"8b5c6718-2d56-4e57-8b99-38efbef745b3"),sQuery(id+"F3.wireOp",EDGE,"da9e38a8-24f9-4dcf-82ff-eaedfc7ddac3"),sQuery(id+"F3.wireOp",EDGE,"3ed522c3-f551-4994-8af4-595096df8cab"),sQuery(id+"F3.wireOp",EDGE,"e3721c90-3ca1-4829-a1f0-4940f097088d"),sQuery(id+"F3.wireOp",EDGE,"e5858ef7-01e1-460b-9e1d-db8dee7450b7"),sQuery(id+"F3.wireOp",EDGE,"0b6d586f-89af-404d-9c45-8ac8a14e0f9f"),sQuery(id+"F3.wireOp",EDGE,"fdba9b58-a7c2-45ac-83c7-755c0024fe7c"),sQuery(id+"F3.wireOp",EDGE,"ef9297e6-c259-49a8-9986-bae6039550b3"),sQuery(id+"F3.wireOp",EDGE,"585c6f1e-c7aa-4b45-99f9-8ab2b20ae877"),sQuery(id+"F3.wireOp",EDGE,"6ead3385-f5af-4ced-bf6c-b98b03284e5d"),sQuery(id+"F3.wireOp",EDGE,"6cfa191d-58e2-4e74-a0ee-c94a68ea9b2d"),sQuery(id+"F3.wireOp",EDGE,"5f7c7bd5-4c1a-4aa2-a292-2ab4f57ae713"),sQuery(id+"F3.wireOp",EDGE,"4b36cdfc-4ed1-4727-9cce-d396c96bae2d"),sQuery(id+"F3.wireOp",EDGE,"ec7c89eb-33f3-4467-bb85-bf3e0787b498"),sQuery(id+"F3.wireOp",EDGE,"ca737aa9-3395-43b0-976a-56014d1f073b"),sQuery(id+"F3.wireOp",EDGE,"8b121f98-3189-41c8-99d6-237662d45c4a"),sQuery(id+"F3.wireOp",EDGE,"e15d9de9-761b-4ebb-85e4-fb4da82fe0c1"),sQuery(id+"F3.wireOp",EDGE,"7ad34d33-c3e0-4451-9494-264813b44421"),sQuery(id+"F3.wireOp",EDGE,"67097021-bec9-466b-973d-5e6d45f4df4b"),sQuery(id+"F3.wireOp",EDGE,"00a890b4-48cc-4d89-b077-d2e06b7e5dbd"),sQuery(id+"F3.wireOp",EDGE,"d7c93b06-eb0f-47ea-baf6-846be92fd260"),sQuery(id+"F3.wireOp",EDGE,"a2e0747d-17c9-4fc1-8cc4-fdaf8f8abfb8"),sQuery(id+"F3.wireOp",EDGE,"3372003e-2229-4558-92bf-d17431c63efe"),sQuery(id+"F3.wireOp",EDGE,"a3b7acfd-c5e1-4a2a-8837-4aa7ee2b56f2"),sQuery(id+"F3.wireOp",EDGE,"3a959202-a4c0-400d-9680-62f35a8281c4"),sQuery(id+"F3.wireOp",EDGE,"a8ddc96f-2760-4d3c-8c77-f7573f30c19d"),sQuery(id+"F3.wireOp",EDGE,"a7586bee-e7f3-42ba-b3eb-820e0c658ff0"),sQuery(id+"F3.wireOp",EDGE,"b1cc2dc8-0320-49c9-bff7-099614d47ec2"),sQuery(id+"F3.wireOp",EDGE,"8457c3d1-b865-450b-adf8-14351497ea25"),sQuery(id+"F3.wireOp",EDGE,"98e9128e-370b-4b50-baf2-f15997247181"),sQuery(id+"F3.wireOp",EDGE,"8a87dfde-57a5-43ec-bda8-da6793a18b73"),sQuery(id+"F3.wireOp",EDGE,"afad9ccd-78bf-4ea0-9416-078eea4e9aa8"),sQuery(id+"F3.wireOp",EDGE,"466440c7-c3a5-4f11-b76c-acbc010caadf"),sQuery(id+"F3.wireOp",EDGE,"802f05ca-83e2-4aad-b0e9-72984b1bff10"),sQuery(id+"F3.wireOp",EDGE,"380c98ad-3319-44b2-9d8b-94ab420c3658"),sQuery(id+"F3.wireOp",EDGE,"a3769aee-8604-4823-b0d7-44a8c97383a4"),sQuery(id+"F3.wireOp",EDGE,"1f52d996-aca9-497a-b7e2-600370ae6949"),sQuery(id+"F3.wireOp",EDGE,"67b67c53-8780-4a85-a3f5-8daf53ab2c04"),sQuery(id+"F3.wireOp",EDGE,"f16f5723-851b-4393-9b75-be1a9d8f5853"),sQuery(id+"F3.wireOp",EDGE,"bb383e53-8237-49ad-9faf-dc4e0ce0de8c"),sQuery(id+"F3.wireOp",EDGE,"7ec6589b-37b5-4f7e-8b9c-d80ded9de812"),sQuery(id+"F3.wireOp",EDGE,"08880140-c83c-486f-b26b-0da67e4ff0c8"),sQuery(id+"F3.wireOp",EDGE,"999823e5-c0bd-483c-88d5-3655cf2a24eb"),sQuery(id+"F3.wireOp",EDGE,"07b7ce3e-532a-4886-a937-3375ccde0f0e"),sQuery(id+"F3.wireOp",EDGE,"9dc5ff66-08db-4f58-bb2d-51863b145979"),sQuery(id+"F3.wireOp",EDGE,"eceeb68e-c3d4-4b94-b62d-56caa49e50b4"),sQuery(id+"F3.wireOp",EDGE,"f41b9d86-6198-4803-9e05-c2d42cc78262"),sQuery(id+"F3.wireOp",EDGE,"0ff7a2ec-16ac-4922-a147-e8dcbe953c89"),sQuery(id+"F3.wireOp",EDGE,"a5f3f9c6-b258-48e6-ac81-471d37944c80"),sQuery(id+"F3.wireOp",EDGE,"5d3368fa-4b93-4609-8d85-d76e8ccb9f70"),sQuery(id+"F3.wireOp",EDGE,"93e705d2-6a1b-4fd1-98fa-f7101df4e23e"),sQuery(id+"F3.wireOp",EDGE,"8560622e-69b7-4d5e-9719-021d16e605a7"),sQuery(id+"F3.wireOp",EDGE,"1269a461-9fb2-497b-9541-76a3c22068ad"),sQuery(id+"F3.wireOp",EDGE,"738108aa-f0e9-4788-8b29-18c751f9aff9"),sQuery(id+"F3.wireOp",EDGE,"c65de39b-1758-467b-980b-9cd9929a3d64"),sQuery(id+"F3.wireOp",EDGE,"756d41d9-dbab-496a-ae15-4fc1659277d1"),sQuery(id+"F3.wireOp",EDGE,"bac2d005-4ac7-492e-a373-e2c006eb4bfb"),sQuery(id+"F3.wireOp",EDGE,"85860d99-9013-4759-aa43-5487a99c41a6"),sQuery(id+"F3.wireOp",EDGE,"8b924ac3-f2a5-4087-bc70-23e4203bc6ae"),sQuery(id+"F3.wireOp",EDGE,"0916d5f8-d38e-4792-80fc-1789f880af75"),sQuery(id+"F3.wireOp",EDGE,"a8e22637-be16-4ef6-ae94-6b23f87871d8"),sQuery(id+"F3.wireOp",EDGE,"63b035c0-ac75-420b-bf11-3ed09439bdeb"),sQuery(id+"F3.wireOp",EDGE,"b31ee2f9-b45b-4c92-b652-2d6a6fa9c3c5"),sQuery(id+"F3.wireOp",EDGE,"97893759-3520-4bf3-a33f-99cd94809b8e"),sQuery(id+"F3.wireOp",EDGE,"5b4603d3-bafa-43cc-99d2-3470666ae78c"),sQuery(id+"F3.wireOp",EDGE,"5dc276c1-ad75-4351-9532-710b6f957b72"),sQuery(id+"F3.wireOp",EDGE,"36f0a240-2e3b-4426-aa0a-071803ecff03"),sQuery(id+"F3.wireOp",EDGE,"57a6f11b-a6b4-4852-9993-7efa1ac7adaf"),sQuery(id+"F3.wireOp",EDGE,"754e6465-131f-4ec7-94bb-14c8c9e997d9"),sQuery(id+"F3.wireOp",EDGE,"34610aa0-aea1-4ba5-b03d-e18f9e4dd988"),sQuery(id+"F3.wireOp",EDGE,"5ea570f2-0fa4-4e78-adeb-6f516147bd71"),sQuery(id+"F3.wireOp",EDGE,"a26f9c50-1319-4f95-9820-85724e840a82"),sQuery(id+"F3.wireOp",EDGE,"0f090b8e-50f8-4d2c-bafe-bdde45b5ada4"),sQuery(id+"F3.wireOp",EDGE,"7117585e-1228-4300-a3e4-db51f78ee14c"),sQuery(id+"F3.wireOp",EDGE,"f8689b3f-eda0-439f-be03-f97530164dd3"),sQuery(id+"F3.wireOp",EDGE,"203b92fc-7d6b-43b1-989f-c26bb414d1b2"),sQuery(id+"F3.wireOp",EDGE,"5679199e-b528-48c1-b11b-944558c980a8"),sQuery(id+"F3.wireOp",EDGE,"161a3187-e8c9-4983-85cb-49f6f7c5f339"),sQuery(id+"F3.wireOp",EDGE,"a6bb4c2e-d0b8-44ae-8978-b823822b2f62"),sQuery(id+"F3.wireOp",EDGE,"04610945-ebf1-46a7-939e-e9ad5c23b445"),sQuery(id+"F3.wireOp",EDGE,"39c5cceb-1e69-460b-a124-bfb35590148b"),sQuery(id+"F3.wireOp",EDGE,"0cac30ec-ac55-47a7-846b-215a65482ff4"),sQuery(id+"F3.wireOp",EDGE,"18e99eaa-199b-443f-9dbd-6b716a5c9e1a"),sQuery(id+"F3.wireOp",EDGE,"17e41e31-d35b-450a-824b-3514a620a768"),sQuery(id+"F3.wireOp",EDGE,"0524b4ea-f730-407d-9352-39bf46fc0a80"),sQuery(id+"F3.wireOp",EDGE,"0f5f3ec3-e111-4418-b32e-94214185c3f1"),sQuery(id+"F3.wireOp",EDGE,"f23df1d5-483b-4032-8ad5-835132419385"),sQuery(id+"F3.wireOp",EDGE,"45bb317c-8eae-478e-b6d9-0e3c22a77cd0"),sQuery(id+"F3.wireOp",EDGE,"bfa43031-806e-4edd-9d98-8f8031f24426"),sQuery(id+"F3.wireOp",EDGE,"f36d8605-259b-4c9b-a64e-53b25295e8f3"),sQuery(id+"F3.wireOp",EDGE,"aff81085-56e9-4dfb-b6c6-55d1b18e30ec"),sQuery(id+"F3.wireOp",EDGE,"64adf307-3694-4edf-9718-bdfb3c99b58e"),sQuery(id+"F3.wireOp",EDGE,"25b1a257-ab12-4c00-be89-3991f43899a6"),sQuery(id+"F3.wireOp",EDGE,"aea91b0e-bcb3-49ee-815e-f65bcd86e2fd"),sQuery(id+"F3.wireOp",EDGE,"dbcc5a10-4f3a-4c7a-88d6-be6ad4de9be3"),sQuery(id+"F3.wireOp",EDGE,"1300bb3d-7ac1-4f9a-91f7-a402756fa661"),sQuery(id+"F3.wireOp",EDGE,"977e18cc-96be-430d-abcb-59930a13b9f0"),sQuery(id+"F3.wireOp",EDGE,"6ba64014-859f-4af9-984d-7bedc4939d73"),sQuery(id+"F3.wireOp",EDGE,"a11d0871-7a20-44ed-b7c6-c8352198d685"),sQuery(id+"F3.wireOp",EDGE,"54e6f65c-df59-4b21-ab87-efc42813dc94"),sQuery(id+"F3.wireOp",EDGE,"f40db9cc-ce06-4c69-89d1-d6fb42ef8d4b"),sQuery(id+"F3.wireOp",EDGE,"290e4a50-9f37-415d-a77d-bcc76523f1d5"),sQuery(id+"F3.wireOp",EDGE,"9830cdb9-701e-436b-837d-810825575392"),sQuery(id+"F3.wireOp",EDGE,"c7a824f2-db51-401e-825b-f3d6b21fe486"),sQuery(id+"F3.wireOp",EDGE,"ad94afe7-f28e-4b73-8a1f-55e2296c2bca"),sQuery(id+"F3.wireOp",EDGE,"084e083d-f148-4afa-b33f-1a4e602a2cd3"),sQuery(id+"F3.wireOp",EDGE,"bd15d313-7969-47b0-a722-98a9e6f22b08"),sQuery(id+"F3.wireOp",EDGE,"cc41519e-33da-4bbe-b848-f50a6c4e3b84"),sQuery(id+"F3.wireOp",EDGE,"ef344dea-b100-4b94-8c68-aa645f94dcae"),sQuery(id+"F3.wireOp",EDGE,"5a8aaeff-4269-443b-ae8b-5febe453ce12"),sQuery(id+"F3.wireOp",EDGE,"bd50b30f-2b72-4484-bc14-e42f99e813fa"),sQuery(id+"F3.wireOp",EDGE,"df1e4ad1-31e9-48e5-81d7-2711f6055c90"),sQuery(id+"F3.wireOp",EDGE,"ae18261a-30a3-4fc6-b873-f9da53a0b074"),sQuery(id+"F3.wireOp",EDGE,"855ca772-78cf-44b3-8a8b-1af7bb703fff"),sQuery(id+"F3.wireOp",EDGE,"a3449970-7c4b-402d-9747-1e28fc93d780"),sQuery(id+"F3.wireOp",EDGE,"c398989f-697f-4569-b9cd-5a2f5c0afdfa"),sQuery(id+"F3.wireOp",EDGE,"be9c560b-05f3-44fc-9c24-5fb0ee9f46be"),sQuery(id+"F3.wireOp",EDGE,"6fb91335-0444-47dc-9a68-f012f8e9e497"),sQuery(id+"F3.wireOp",EDGE,"d4280811-013f-4bce-ad33-1f82742e0dd9"),sQuery(id+"F3.wireOp",EDGE,"0b1bd235-f05c-4c19-962e-4f72b657b4a9"),sQuery(id+"F3.wireOp",EDGE,"6ecc38b7-87ea-4faf-bea4-6a361bf0c5f1"),sQuery(id+"F3.wireOp",EDGE,"93b60800-9d39-4d9f-8d8b-3e53798cad8d"),sQuery(id+"F3.wireOp",EDGE,"bc0c8946-68bd-4333-991b-e604499cce4a"),sQuery(id+"F3.wireOp",EDGE,"03ec03ef-69c7-4f14-a4be-1943b1b26620"),sQuery(id+"F3.wireOp",EDGE,"70288df1-7fe0-44d6-81a0-38b7c6254652"),sQuery(id+"F3.wireOp",EDGE,"373aa3d3-7813-439a-aa6d-11bf33d8b24e"),sQuery(id+"F3.wireOp",EDGE,"45d8d8cd-c432-46a9-ba83-ca98e6a8b331"),sQuery(id+"F3.wireOp",EDGE,"30eeae1c-e414-4273-926e-a242566325a0"),sQuery(id+"F3.wireOp",EDGE,"2c9bb13c-11d4-40b6-bcc6-d08f2723e091"),sQuery(id+"F3.wireOp",EDGE,"a482991e-2cf6-48ab-8e8e-3e4f8b67d4b7"),sQuery(id+"F3.wireOp",EDGE,"06891698-4df7-4f94-84c6-72103b62673b"),sQuery(id+"F3.wireOp",EDGE,"ecab2fa4-6225-467e-82ee-4732fa611de3"),sQuery(id+"F3.wireOp",EDGE,"649bfd1a-9215-4127-87d3-ed0b3f5772d5"),sQuery(id+"F3.wireOp",EDGE,"bf54d2c0-65f1-4ff6-871b-ae601eb9e7cc"),sQuery(id+"F3.wireOp",EDGE,"29274e08-d376-4eb2-907f-b860139ca4db"),sQuery(id+"F3.wireOp",EDGE,"cd2404f3-3954-470e-aa5a-a76806b6835a"),sQuery(id+"F3.wireOp",EDGE,"dbd5f9e9-56cf-4ed4-a9fb-97d5f2897854"),sQuery(id+"F3.wireOp",EDGE,"a3f94ff5-44de-4570-8f07-2fa58cf7f771"),sQuery(id+"F3.wireOp",EDGE,"21d034b1-97d0-4cdd-a783-b5eef86ebc99"),sQuery(id+"F3.wireOp",EDGE,"a60bbc0a-156d-4d16-82fa-9e5e5c2e844d"),sQuery(id+"F3.wireOp",EDGE,"a528a1a4-90cb-4bac-a68a-6d2da3dfac97"),sQuery(id+"F3.wireOp",EDGE,"2897741f-4c31-4951-9326-161b0945bc72"),sQuery(id+"F3.wireOp",EDGE,"138138aa-b9e4-4038-8e12-b0c5a13fea39"),sQuery(id+"F3.wireOp",EDGE,"8187800a-b1e6-4d83-98c7-9c355a36d6c6"),sQuery(id+"F3.wireOp",EDGE,"9701c027-796e-4d6b-a002-6605f6ee80e3"),sQuery(id+"F3.wireOp",EDGE,"77e98c07-d0dc-4f04-9c1b-99f3355fd8a7"),sQuery(id+"F3.wireOp",EDGE,"4d81288f-f128-4ca3-b627-6a5b28d496de"),sQuery(id+"F3.wireOp",EDGE,"d1bad90c-4b8f-41a3-ac4a-47f6b9aadffb"),sQuery(id+"F3.wireOp",EDGE,"ed70a943-00e2-466a-98de-2b8f6be6381d"),sQuery(id+"F3.wireOp",EDGE,"ca15953e-95cc-4037-b944-8707390692ef"),sQuery(id+"F3.wireOp",EDGE,"d795c5ca-c7fa-4fa3-aceb-2aaa567452cf"),sQuery(id+"F3.wireOp",EDGE,"243c0ca0-aa5e-4f5e-bdca-16c8987a887f"),sQuery(id+"F3.wireOp",EDGE,"bc9fa2c3-366d-471d-97c7-70100b7d8498"),sQuery(id+"F3.wireOp",EDGE,"504d9464-3638-4fca-aca5-74d973fcd556"),sQuery(id+"F3.wireOp",EDGE,"904397ff-7935-4a86-961c-5e675a147941"),sQuery(id+"F3.wireOp",EDGE,"1c96a42e-db33-464e-939b-1401c8f3dc56"),sQuery(id+"F3.wireOp",EDGE,"c93a136a-b456-4118-8f96-0ff909422201"),sQuery(id+"F3.wireOp",EDGE,"18e409b6-aa76-48e1-b07a-2118d4afb836"),sQuery(id+"F3.wireOp",EDGE,"453d7378-4718-464e-bd01-99f678aa0ea9"),sQuery(id+"F3.wireOp",EDGE,"7a3a24a2-148e-4b54-a0ad-eba860c7fb7a"),sQuery(id+"F3.wireOp",EDGE,"8ef3a38d-664a-40d3-aa3a-b2176ce58029"),sQuery(id+"F3.wireOp",EDGE,"431eb4cf-7232-4f15-8871-3b81c8abfe77"),sQuery(id+"F3.wireOp",EDGE,"6c5b3992-7da6-44e2-8879-de97f4632d9e"),sQuery(id+"F3.wireOp",EDGE,"700eb462-5239-4aff-bb8e-38754561fb95"),sQuery(id+"F3.wireOp",EDGE,"76e36e64-b254-46aa-a38f-830b3794fe19"),sQuery(id+"F3.wireOp",EDGE,"7d77c6f3-f087-4291-933e-8eee58b8f264"),sQuery(id+"F3.wireOp",EDGE,"26ca988e-826e-47f0-98d2-556df3f9bf42"),sQuery(id+"F3.wireOp",EDGE,"4810f180-f491-4bec-8c84-57ef4a51e416"),sQuery(id+"F3.wireOp",EDGE,"a2f87652-967a-430d-baa5-b94727ffa003"),sQuery(id+"F3.wireOp",EDGE,"d08c92d7-9c6d-4fd1-b266-1e49aef11731"),sQuery(id+"F3.wireOp",EDGE,"60113931-40ab-4c1d-a52c-fd4caa2a44f1"),sQuery(id+"F3.wireOp",EDGE,"b1aa1ff4-0d0d-408d-8a15-147b6324842e"),sQuery(id+"F3.wireOp",EDGE,"38f109ba-2aae-4bc4-9a22-f038beb12030"),sQuery(id+"F3.wireOp",EDGE,"7441d3f1-614a-426d-b871-a4e1a13c6e7e"),sQuery(id+"F3.wireOp",EDGE,"847a2f50-4ef1-49b5-b090-5f8521ee8ca1"),sQuery(id+"F3.wireOp",EDGE,"98bd5360-29b1-4412-9294-02ef6551eecc"),sQuery(id+"F3.wireOp",EDGE,"cb6e78c9-5cdf-4276-b840-5cfec84caed4"),sQuery(id+"F3.wireOp",EDGE,"1736b3be-cda2-4842-aefb-283565cc4c62"),sQuery(id+"F3.wireOp",EDGE,"438710e5-800b-4df2-8fff-3432d8aae595"),sQuery(id+"F3.wireOp",EDGE,"f69e7794-4715-43f7-a271-aa5e98ef7e68"),sQuery(id+"F3.wireOp",EDGE,"02c9a714-cd92-4f6e-be60-84f6aca8f508"),sQuery(id+"F3.wireOp",EDGE,"e0730c34-1f26-4745-a30f-e9a291eaeb6f"),sQuery(id+"F3.wireOp",EDGE,"9554880d-9851-4e54-af44-454a4419ca75"),sQuery(id+"F3.wireOp",EDGE,"efb41e31-abb5-42fa-83db-f78bf43b7196"),sQuery(id+"F3.wireOp",EDGE,"1bdde1b5-8417-49bf-b267-4e22f08aa6f4"),sQuery(id+"F3.wireOp",EDGE,"72509248-fad9-462b-b756-80664d0faace"),sQuery(id+"F3.wireOp",EDGE,"76f0ff31-d45f-4a8a-86ee-2e308ecada5a"),sQuery(id+"F3.wireOp",EDGE,"E505"),sQuery(id+"F3.wireOp",EDGE,"E506"),sQuery(id+"F3.wireOp",EDGE,"E507")])]});
            transform(context, id + "F6", {"entities" : qUnion([Q0]), "transformType" : TransformType.TRANSLATION_3D, "dx" : 0 * mm, "dy" : 0 * mm, "dz" : -10 * mm, "makeCopy" : false});
        }
        {
            var Q0;
            Q0=makeQuery(id+"F4.opExtrude","SWEPT_BODY",BODY,{"disambiguationData":[OSD([sQuery(id+"F3.wireOp",EDGE,"ec41ae91-4df3-4674-b230-51135a62c841"),sQuery(id+"F3.wireOp",EDGE,"4915715a-3651-4802-93b2-976e28617991"),sQuery(id+"F3.wireOp",EDGE,"f15b2dd7-0a66-4c35-9b3a-76401d213128"),sQuery(id+"F3.wireOp",EDGE,"573a967d-7325-43e2-a310-91cf087eee18"),sQuery(id+"F3.wireOp",EDGE,"9829493d-dd2b-4d5e-a350-835d0b1967f8"),sQuery(id+"F3.wireOp",EDGE,"88a4fc78-4b8c-41cb-8199-d79f3d1a214f"),sQuery(id+"F3.wireOp",EDGE,"29e99f44-44dd-4ffa-b92d-bba17bea5d43"),sQuery(id+"F3.wireOp",EDGE,"08ec9610-4828-42c1-afa1-523aa55121be"),sQuery(id+"F3.wireOp",EDGE,"310ca9a3-fa69-468b-bae4-7742a02260ce"),sQuery(id+"F3.wireOp",EDGE,"1d81bcbc-7ed6-437a-9b34-64fc4b10475f"),sQuery(id+"F3.wireOp",EDGE,"7f1e7079-6e3e-4c6c-b9ef-b52a12ea813f"),sQuery(id+"F3.wireOp",EDGE,"e228bb15-0659-4b2b-91ba-388ef41ebd05"),sQuery(id+"F3.wireOp",EDGE,"2d2180e8-ce33-4739-9b09-17b5a1027c62"),sQuery(id+"F3.wireOp",EDGE,"8b5c6718-2d56-4e57-8b99-38efbef745b3"),sQuery(id+"F3.wireOp",EDGE,"da9e38a8-24f9-4dcf-82ff-eaedfc7ddac3"),sQuery(id+"F3.wireOp",EDGE,"3ed522c3-f551-4994-8af4-595096df8cab"),sQuery(id+"F3.wireOp",EDGE,"e3721c90-3ca1-4829-a1f0-4940f097088d"),sQuery(id+"F3.wireOp",EDGE,"e5858ef7-01e1-460b-9e1d-db8dee7450b7"),sQuery(id+"F3.wireOp",EDGE,"0b6d586f-89af-404d-9c45-8ac8a14e0f9f"),sQuery(id+"F3.wireOp",EDGE,"fdba9b58-a7c2-45ac-83c7-755c0024fe7c"),sQuery(id+"F3.wireOp",EDGE,"ef9297e6-c259-49a8-9986-bae6039550b3"),sQuery(id+"F3.wireOp",EDGE,"585c6f1e-c7aa-4b45-99f9-8ab2b20ae877"),sQuery(id+"F3.wireOp",EDGE,"6ead3385-f5af-4ced-bf6c-b98b03284e5d"),sQuery(id+"F3.wireOp",EDGE,"6cfa191d-58e2-4e74-a0ee-c94a68ea9b2d"),sQuery(id+"F3.wireOp",EDGE,"5f7c7bd5-4c1a-4aa2-a292-2ab4f57ae713"),sQuery(id+"F3.wireOp",EDGE,"4b36cdfc-4ed1-4727-9cce-d396c96bae2d"),sQuery(id+"F3.wireOp",EDGE,"ec7c89eb-33f3-4467-bb85-bf3e0787b498"),sQuery(id+"F3.wireOp",EDGE,"ca737aa9-3395-43b0-976a-56014d1f073b"),sQuery(id+"F3.wireOp",EDGE,"8b121f98-3189-41c8-99d6-237662d45c4a"),sQuery(id+"F3.wireOp",EDGE,"e15d9de9-761b-4ebb-85e4-fb4da82fe0c1"),sQuery(id+"F3.wireOp",EDGE,"7ad34d33-c3e0-4451-9494-264813b44421"),sQuery(id+"F3.wireOp",EDGE,"67097021-bec9-466b-973d-5e6d45f4df4b"),sQuery(id+"F3.wireOp",EDGE,"00a890b4-48cc-4d89-b077-d2e06b7e5dbd"),sQuery(id+"F3.wireOp",EDGE,"d7c93b06-eb0f-47ea-baf6-846be92fd260"),sQuery(id+"F3.wireOp",EDGE,"a2e0747d-17c9-4fc1-8cc4-fdaf8f8abfb8"),sQuery(id+"F3.wireOp",EDGE,"3372003e-2229-4558-92bf-d17431c63efe"),sQuery(id+"F3.wireOp",EDGE,"a3b7acfd-c5e1-4a2a-8837-4aa7ee2b56f2"),sQuery(id+"F3.wireOp",EDGE,"3a959202-a4c0-400d-9680-62f35a8281c4"),sQuery(id+"F3.wireOp",EDGE,"a8ddc96f-2760-4d3c-8c77-f7573f30c19d"),sQuery(id+"F3.wireOp",EDGE,"a7586bee-e7f3-42ba-b3eb-820e0c658ff0"),sQuery(id+"F3.wireOp",EDGE,"b1cc2dc8-0320-49c9-bff7-099614d47ec2"),sQuery(id+"F3.wireOp",EDGE,"8457c3d1-b865-450b-adf8-14351497ea25"),sQuery(id+"F3.wireOp",EDGE,"98e9128e-370b-4b50-baf2-f15997247181"),sQuery(id+"F3.wireOp",EDGE,"8a87dfde-57a5-43ec-bda8-da6793a18b73"),sQuery(id+"F3.wireOp",EDGE,"afad9ccd-78bf-4ea0-9416-078eea4e9aa8"),sQuery(id+"F3.wireOp",EDGE,"466440c7-c3a5-4f11-b76c-acbc010caadf"),sQuery(id+"F3.wireOp",EDGE,"802f05ca-83e2-4aad-b0e9-72984b1bff10"),sQuery(id+"F3.wireOp",EDGE,"380c98ad-3319-44b2-9d8b-94ab420c3658"),sQuery(id+"F3.wireOp",EDGE,"a3769aee-8604-4823-b0d7-44a8c97383a4"),sQuery(id+"F3.wireOp",EDGE,"1f52d996-aca9-497a-b7e2-600370ae6949"),sQuery(id+"F3.wireOp",EDGE,"67b67c53-8780-4a85-a3f5-8daf53ab2c04"),sQuery(id+"F3.wireOp",EDGE,"f16f5723-851b-4393-9b75-be1a9d8f5853"),sQuery(id+"F3.wireOp",EDGE,"bb383e53-8237-49ad-9faf-dc4e0ce0de8c"),sQuery(id+"F3.wireOp",EDGE,"7ec6589b-37b5-4f7e-8b9c-d80ded9de812"),sQuery(id+"F3.wireOp",EDGE,"08880140-c83c-486f-b26b-0da67e4ff0c8"),sQuery(id+"F3.wireOp",EDGE,"999823e5-c0bd-483c-88d5-3655cf2a24eb"),sQuery(id+"F3.wireOp",EDGE,"07b7ce3e-532a-4886-a937-3375ccde0f0e"),sQuery(id+"F3.wireOp",EDGE,"9dc5ff66-08db-4f58-bb2d-51863b145979"),sQuery(id+"F3.wireOp",EDGE,"eceeb68e-c3d4-4b94-b62d-56caa49e50b4"),sQuery(id+"F3.wireOp",EDGE,"f41b9d86-6198-4803-9e05-c2d42cc78262"),sQuery(id+"F3.wireOp",EDGE,"0ff7a2ec-16ac-4922-a147-e8dcbe953c89"),sQuery(id+"F3.wireOp",EDGE,"a5f3f9c6-b258-48e6-ac81-471d37944c80"),sQuery(id+"F3.wireOp",EDGE,"5d3368fa-4b93-4609-8d85-d76e8ccb9f70"),sQuery(id+"F3.wireOp",EDGE,"93e705d2-6a1b-4fd1-98fa-f7101df4e23e"),sQuery(id+"F3.wireOp",EDGE,"8560622e-69b7-4d5e-9719-021d16e605a7"),sQuery(id+"F3.wireOp",EDGE,"1269a461-9fb2-497b-9541-76a3c22068ad"),sQuery(id+"F3.wireOp",EDGE,"738108aa-f0e9-4788-8b29-18c751f9aff9"),sQuery(id+"F3.wireOp",EDGE,"c65de39b-1758-467b-980b-9cd9929a3d64"),sQuery(id+"F3.wireOp",EDGE,"756d41d9-dbab-496a-ae15-4fc1659277d1"),sQuery(id+"F3.wireOp",EDGE,"bac2d005-4ac7-492e-a373-e2c006eb4bfb"),sQuery(id+"F3.wireOp",EDGE,"85860d99-9013-4759-aa43-5487a99c41a6"),sQuery(id+"F3.wireOp",EDGE,"8b924ac3-f2a5-4087-bc70-23e4203bc6ae"),sQuery(id+"F3.wireOp",EDGE,"0916d5f8-d38e-4792-80fc-1789f880af75"),sQuery(id+"F3.wireOp",EDGE,"a8e22637-be16-4ef6-ae94-6b23f87871d8"),sQuery(id+"F3.wireOp",EDGE,"63b035c0-ac75-420b-bf11-3ed09439bdeb"),sQuery(id+"F3.wireOp",EDGE,"b31ee2f9-b45b-4c92-b652-2d6a6fa9c3c5"),sQuery(id+"F3.wireOp",EDGE,"97893759-3520-4bf3-a33f-99cd94809b8e"),sQuery(id+"F3.wireOp",EDGE,"5b4603d3-bafa-43cc-99d2-3470666ae78c"),sQuery(id+"F3.wireOp",EDGE,"5dc276c1-ad75-4351-9532-710b6f957b72"),sQuery(id+"F3.wireOp",EDGE,"36f0a240-2e3b-4426-aa0a-071803ecff03"),sQuery(id+"F3.wireOp",EDGE,"57a6f11b-a6b4-4852-9993-7efa1ac7adaf"),sQuery(id+"F3.wireOp",EDGE,"754e6465-131f-4ec7-94bb-14c8c9e997d9"),sQuery(id+"F3.wireOp",EDGE,"34610aa0-aea1-4ba5-b03d-e18f9e4dd988"),sQuery(id+"F3.wireOp",EDGE,"5ea570f2-0fa4-4e78-adeb-6f516147bd71"),sQuery(id+"F3.wireOp",EDGE,"a26f9c50-1319-4f95-9820-85724e840a82"),sQuery(id+"F3.wireOp",EDGE,"0f090b8e-50f8-4d2c-bafe-bdde45b5ada4"),sQuery(id+"F3.wireOp",EDGE,"7117585e-1228-4300-a3e4-db51f78ee14c"),sQuery(id+"F3.wireOp",EDGE,"f8689b3f-eda0-439f-be03-f97530164dd3"),sQuery(id+"F3.wireOp",EDGE,"203b92fc-7d6b-43b1-989f-c26bb414d1b2"),sQuery(id+"F3.wireOp",EDGE,"5679199e-b528-48c1-b11b-944558c980a8"),sQuery(id+"F3.wireOp",EDGE,"161a3187-e8c9-4983-85cb-49f6f7c5f339"),sQuery(id+"F3.wireOp",EDGE,"a6bb4c2e-d0b8-44ae-8978-b823822b2f62"),sQuery(id+"F3.wireOp",EDGE,"04610945-ebf1-46a7-939e-e9ad5c23b445"),sQuery(id+"F3.wireOp",EDGE,"39c5cceb-1e69-460b-a124-bfb35590148b"),sQuery(id+"F3.wireOp",EDGE,"0cac30ec-ac55-47a7-846b-215a65482ff4"),sQuery(id+"F3.wireOp",EDGE,"18e99eaa-199b-443f-9dbd-6b716a5c9e1a"),sQuery(id+"F3.wireOp",EDGE,"17e41e31-d35b-450a-824b-3514a620a768"),sQuery(id+"F3.wireOp",EDGE,"0524b4ea-f730-407d-9352-39bf46fc0a80"),sQuery(id+"F3.wireOp",EDGE,"0f5f3ec3-e111-4418-b32e-94214185c3f1"),sQuery(id+"F3.wireOp",EDGE,"f23df1d5-483b-4032-8ad5-835132419385"),sQuery(id+"F3.wireOp",EDGE,"45bb317c-8eae-478e-b6d9-0e3c22a77cd0"),sQuery(id+"F3.wireOp",EDGE,"bfa43031-806e-4edd-9d98-8f8031f24426"),sQuery(id+"F3.wireOp",EDGE,"f36d8605-259b-4c9b-a64e-53b25295e8f3"),sQuery(id+"F3.wireOp",EDGE,"aff81085-56e9-4dfb-b6c6-55d1b18e30ec"),sQuery(id+"F3.wireOp",EDGE,"64adf307-3694-4edf-9718-bdfb3c99b58e"),sQuery(id+"F3.wireOp",EDGE,"25b1a257-ab12-4c00-be89-3991f43899a6"),sQuery(id+"F3.wireOp",EDGE,"aea91b0e-bcb3-49ee-815e-f65bcd86e2fd"),sQuery(id+"F3.wireOp",EDGE,"dbcc5a10-4f3a-4c7a-88d6-be6ad4de9be3"),sQuery(id+"F3.wireOp",EDGE,"1300bb3d-7ac1-4f9a-91f7-a402756fa661"),sQuery(id+"F3.wireOp",EDGE,"977e18cc-96be-430d-abcb-59930a13b9f0"),sQuery(id+"F3.wireOp",EDGE,"6ba64014-859f-4af9-984d-7bedc4939d73"),sQuery(id+"F3.wireOp",EDGE,"a11d0871-7a20-44ed-b7c6-c8352198d685"),sQuery(id+"F3.wireOp",EDGE,"54e6f65c-df59-4b21-ab87-efc42813dc94"),sQuery(id+"F3.wireOp",EDGE,"f40db9cc-ce06-4c69-89d1-d6fb42ef8d4b"),sQuery(id+"F3.wireOp",EDGE,"290e4a50-9f37-415d-a77d-bcc76523f1d5"),sQuery(id+"F3.wireOp",EDGE,"9830cdb9-701e-436b-837d-810825575392"),sQuery(id+"F3.wireOp",EDGE,"c7a824f2-db51-401e-825b-f3d6b21fe486"),sQuery(id+"F3.wireOp",EDGE,"ad94afe7-f28e-4b73-8a1f-55e2296c2bca"),sQuery(id+"F3.wireOp",EDGE,"084e083d-f148-4afa-b33f-1a4e602a2cd3"),sQuery(id+"F3.wireOp",EDGE,"bd15d313-7969-47b0-a722-98a9e6f22b08"),sQuery(id+"F3.wireOp",EDGE,"cc41519e-33da-4bbe-b848-f50a6c4e3b84"),sQuery(id+"F3.wireOp",EDGE,"ef344dea-b100-4b94-8c68-aa645f94dcae"),sQuery(id+"F3.wireOp",EDGE,"5a8aaeff-4269-443b-ae8b-5febe453ce12"),sQuery(id+"F3.wireOp",EDGE,"bd50b30f-2b72-4484-bc14-e42f99e813fa"),sQuery(id+"F3.wireOp",EDGE,"df1e4ad1-31e9-48e5-81d7-2711f6055c90"),sQuery(id+"F3.wireOp",EDGE,"ae18261a-30a3-4fc6-b873-f9da53a0b074"),sQuery(id+"F3.wireOp",EDGE,"855ca772-78cf-44b3-8a8b-1af7bb703fff"),sQuery(id+"F3.wireOp",EDGE,"a3449970-7c4b-402d-9747-1e28fc93d780"),sQuery(id+"F3.wireOp",EDGE,"c398989f-697f-4569-b9cd-5a2f5c0afdfa"),sQuery(id+"F3.wireOp",EDGE,"be9c560b-05f3-44fc-9c24-5fb0ee9f46be"),sQuery(id+"F3.wireOp",EDGE,"6fb91335-0444-47dc-9a68-f012f8e9e497"),sQuery(id+"F3.wireOp",EDGE,"d4280811-013f-4bce-ad33-1f82742e0dd9"),sQuery(id+"F3.wireOp",EDGE,"0b1bd235-f05c-4c19-962e-4f72b657b4a9"),sQuery(id+"F3.wireOp",EDGE,"6ecc38b7-87ea-4faf-bea4-6a361bf0c5f1"),sQuery(id+"F3.wireOp",EDGE,"93b60800-9d39-4d9f-8d8b-3e53798cad8d"),sQuery(id+"F3.wireOp",EDGE,"bc0c8946-68bd-4333-991b-e604499cce4a"),sQuery(id+"F3.wireOp",EDGE,"03ec03ef-69c7-4f14-a4be-1943b1b26620"),sQuery(id+"F3.wireOp",EDGE,"70288df1-7fe0-44d6-81a0-38b7c6254652"),sQuery(id+"F3.wireOp",EDGE,"373aa3d3-7813-439a-aa6d-11bf33d8b24e"),sQuery(id+"F3.wireOp",EDGE,"45d8d8cd-c432-46a9-ba83-ca98e6a8b331"),sQuery(id+"F3.wireOp",EDGE,"30eeae1c-e414-4273-926e-a242566325a0"),sQuery(id+"F3.wireOp",EDGE,"2c9bb13c-11d4-40b6-bcc6-d08f2723e091"),sQuery(id+"F3.wireOp",EDGE,"a482991e-2cf6-48ab-8e8e-3e4f8b67d4b7"),sQuery(id+"F3.wireOp",EDGE,"06891698-4df7-4f94-84c6-72103b62673b"),sQuery(id+"F3.wireOp",EDGE,"ecab2fa4-6225-467e-82ee-4732fa611de3"),sQuery(id+"F3.wireOp",EDGE,"649bfd1a-9215-4127-87d3-ed0b3f5772d5"),sQuery(id+"F3.wireOp",EDGE,"bf54d2c0-65f1-4ff6-871b-ae601eb9e7cc"),sQuery(id+"F3.wireOp",EDGE,"29274e08-d376-4eb2-907f-b860139ca4db"),sQuery(id+"F3.wireOp",EDGE,"cd2404f3-3954-470e-aa5a-a76806b6835a"),sQuery(id+"F3.wireOp",EDGE,"dbd5f9e9-56cf-4ed4-a9fb-97d5f2897854"),sQuery(id+"F3.wireOp",EDGE,"a3f94ff5-44de-4570-8f07-2fa58cf7f771"),sQuery(id+"F3.wireOp",EDGE,"21d034b1-97d0-4cdd-a783-b5eef86ebc99"),sQuery(id+"F3.wireOp",EDGE,"a60bbc0a-156d-4d16-82fa-9e5e5c2e844d"),sQuery(id+"F3.wireOp",EDGE,"a528a1a4-90cb-4bac-a68a-6d2da3dfac97"),sQuery(id+"F3.wireOp",EDGE,"2897741f-4c31-4951-9326-161b0945bc72"),sQuery(id+"F3.wireOp",EDGE,"138138aa-b9e4-4038-8e12-b0c5a13fea39"),sQuery(id+"F3.wireOp",EDGE,"8187800a-b1e6-4d83-98c7-9c355a36d6c6"),sQuery(id+"F3.wireOp",EDGE,"9701c027-796e-4d6b-a002-6605f6ee80e3"),sQuery(id+"F3.wireOp",EDGE,"77e98c07-d0dc-4f04-9c1b-99f3355fd8a7"),sQuery(id+"F3.wireOp",EDGE,"4d81288f-f128-4ca3-b627-6a5b28d496de"),sQuery(id+"F3.wireOp",EDGE,"d1bad90c-4b8f-41a3-ac4a-47f6b9aadffb"),sQuery(id+"F3.wireOp",EDGE,"ed70a943-00e2-466a-98de-2b8f6be6381d"),sQuery(id+"F3.wireOp",EDGE,"ca15953e-95cc-4037-b944-8707390692ef"),sQuery(id+"F3.wireOp",EDGE,"d795c5ca-c7fa-4fa3-aceb-2aaa567452cf"),sQuery(id+"F3.wireOp",EDGE,"243c0ca0-aa5e-4f5e-bdca-16c8987a887f"),sQuery(id+"F3.wireOp",EDGE,"bc9fa2c3-366d-471d-97c7-70100b7d8498"),sQuery(id+"F3.wireOp",EDGE,"504d9464-3638-4fca-aca5-74d973fcd556"),sQuery(id+"F3.wireOp",EDGE,"904397ff-7935-4a86-961c-5e675a147941"),sQuery(id+"F3.wireOp",EDGE,"1c96a42e-db33-464e-939b-1401c8f3dc56"),sQuery(id+"F3.wireOp",EDGE,"c93a136a-b456-4118-8f96-0ff909422201"),sQuery(id+"F3.wireOp",EDGE,"18e409b6-aa76-48e1-b07a-2118d4afb836"),sQuery(id+"F3.wireOp",EDGE,"453d7378-4718-464e-bd01-99f678aa0ea9"),sQuery(id+"F3.wireOp",EDGE,"7a3a24a2-148e-4b54-a0ad-eba860c7fb7a"),sQuery(id+"F3.wireOp",EDGE,"8ef3a38d-664a-40d3-aa3a-b2176ce58029"),sQuery(id+"F3.wireOp",EDGE,"431eb4cf-7232-4f15-8871-3b81c8abfe77"),sQuery(id+"F3.wireOp",EDGE,"6c5b3992-7da6-44e2-8879-de97f4632d9e"),sQuery(id+"F3.wireOp",EDGE,"700eb462-5239-4aff-bb8e-38754561fb95"),sQuery(id+"F3.wireOp",EDGE,"76e36e64-b254-46aa-a38f-830b3794fe19"),sQuery(id+"F3.wireOp",EDGE,"7d77c6f3-f087-4291-933e-8eee58b8f264"),sQuery(id+"F3.wireOp",EDGE,"26ca988e-826e-47f0-98d2-556df3f9bf42"),sQuery(id+"F3.wireOp",EDGE,"4810f180-f491-4bec-8c84-57ef4a51e416"),sQuery(id+"F3.wireOp",EDGE,"a2f87652-967a-430d-baa5-b94727ffa003"),sQuery(id+"F3.wireOp",EDGE,"d08c92d7-9c6d-4fd1-b266-1e49aef11731"),sQuery(id+"F3.wireOp",EDGE,"60113931-40ab-4c1d-a52c-fd4caa2a44f1"),sQuery(id+"F3.wireOp",EDGE,"b1aa1ff4-0d0d-408d-8a15-147b6324842e"),sQuery(id+"F3.wireOp",EDGE,"38f109ba-2aae-4bc4-9a22-f038beb12030"),sQuery(id+"F3.wireOp",EDGE,"7441d3f1-614a-426d-b871-a4e1a13c6e7e"),sQuery(id+"F3.wireOp",EDGE,"847a2f50-4ef1-49b5-b090-5f8521ee8ca1"),sQuery(id+"F3.wireOp",EDGE,"98bd5360-29b1-4412-9294-02ef6551eecc"),sQuery(id+"F3.wireOp",EDGE,"cb6e78c9-5cdf-4276-b840-5cfec84caed4"),sQuery(id+"F3.wireOp",EDGE,"1736b3be-cda2-4842-aefb-283565cc4c62"),sQuery(id+"F3.wireOp",EDGE,"438710e5-800b-4df2-8fff-3432d8aae595"),sQuery(id+"F3.wireOp",EDGE,"f69e7794-4715-43f7-a271-aa5e98ef7e68"),sQuery(id+"F3.wireOp",EDGE,"02c9a714-cd92-4f6e-be60-84f6aca8f508"),sQuery(id+"F3.wireOp",EDGE,"e0730c34-1f26-4745-a30f-e9a291eaeb6f"),sQuery(id+"F3.wireOp",EDGE,"9554880d-9851-4e54-af44-454a4419ca75"),sQuery(id+"F3.wireOp",EDGE,"efb41e31-abb5-42fa-83db-f78bf43b7196"),sQuery(id+"F3.wireOp",EDGE,"1bdde1b5-8417-49bf-b267-4e22f08aa6f4"),sQuery(id+"F3.wireOp",EDGE,"72509248-fad9-462b-b756-80664d0faace"),sQuery(id+"F3.wireOp",EDGE,"76f0ff31-d45f-4a8a-86ee-2e308ecada5a"),sQuery(id+"F3.wireOp",EDGE,"E505"),sQuery(id+"F3.wireOp",EDGE,"E506"),sQuery(id+"F3.wireOp",EDGE,"E507")])]});
            var Q1;
            Q1=qCreatedBy(makeId("Origin.pointOp"),VERTEX);
            transform(context, id + "F7", {"entities" : qUnion([Q0]), "transformType" : TransformType.SCALE_UNIFORMLY, "scale" : 1.01, "scalePoint" : qUnion([Q1]), "makeCopy" : false});
        }
        {
            var Q0;
            Q0=makeQuery(id+"F4.opExtrude","SWEPT_BODY",BODY,{"disambiguationData":[OSD([sQuery(id+"F3.wireOp",EDGE,"ec41ae91-4df3-4674-b230-51135a62c841"),sQuery(id+"F3.wireOp",EDGE,"4915715a-3651-4802-93b2-976e28617991"),sQuery(id+"F3.wireOp",EDGE,"f15b2dd7-0a66-4c35-9b3a-76401d213128"),sQuery(id+"F3.wireOp",EDGE,"573a967d-7325-43e2-a310-91cf087eee18"),sQuery(id+"F3.wireOp",EDGE,"9829493d-dd2b-4d5e-a350-835d0b1967f8"),sQuery(id+"F3.wireOp",EDGE,"88a4fc78-4b8c-41cb-8199-d79f3d1a214f"),sQuery(id+"F3.wireOp",EDGE,"29e99f44-44dd-4ffa-b92d-bba17bea5d43"),sQuery(id+"F3.wireOp",EDGE,"08ec9610-4828-42c1-afa1-523aa55121be"),sQuery(id+"F3.wireOp",EDGE,"310ca9a3-fa69-468b-bae4-7742a02260ce"),sQuery(id+"F3.wireOp",EDGE,"1d81bcbc-7ed6-437a-9b34-64fc4b10475f"),sQuery(id+"F3.wireOp",EDGE,"7f1e7079-6e3e-4c6c-b9ef-b52a12ea813f"),sQuery(id+"F3.wireOp",EDGE,"e228bb15-0659-4b2b-91ba-388ef41ebd05"),sQuery(id+"F3.wireOp",EDGE,"2d2180e8-ce33-4739-9b09-17b5a1027c62"),sQuery(id+"F3.wireOp",EDGE,"8b5c6718-2d56-4e57-8b99-38efbef745b3"),sQuery(id+"F3.wireOp",EDGE,"da9e38a8-24f9-4dcf-82ff-eaedfc7ddac3"),sQuery(id+"F3.wireOp",EDGE,"3ed522c3-f551-4994-8af4-595096df8cab"),sQuery(id+"F3.wireOp",EDGE,"e3721c90-3ca1-4829-a1f0-4940f097088d"),sQuery(id+"F3.wireOp",EDGE,"e5858ef7-01e1-460b-9e1d-db8dee7450b7"),sQuery(id+"F3.wireOp",EDGE,"0b6d586f-89af-404d-9c45-8ac8a14e0f9f"),sQuery(id+"F3.wireOp",EDGE,"fdba9b58-a7c2-45ac-83c7-755c0024fe7c"),sQuery(id+"F3.wireOp",EDGE,"ef9297e6-c259-49a8-9986-bae6039550b3"),sQuery(id+"F3.wireOp",EDGE,"585c6f1e-c7aa-4b45-99f9-8ab2b20ae877"),sQuery(id+"F3.wireOp",EDGE,"6ead3385-f5af-4ced-bf6c-b98b03284e5d"),sQuery(id+"F3.wireOp",EDGE,"6cfa191d-58e2-4e74-a0ee-c94a68ea9b2d"),sQuery(id+"F3.wireOp",EDGE,"5f7c7bd5-4c1a-4aa2-a292-2ab4f57ae713"),sQuery(id+"F3.wireOp",EDGE,"4b36cdfc-4ed1-4727-9cce-d396c96bae2d"),sQuery(id+"F3.wireOp",EDGE,"ec7c89eb-33f3-4467-bb85-bf3e0787b498"),sQuery(id+"F3.wireOp",EDGE,"ca737aa9-3395-43b0-976a-56014d1f073b"),sQuery(id+"F3.wireOp",EDGE,"8b121f98-3189-41c8-99d6-237662d45c4a"),sQuery(id+"F3.wireOp",EDGE,"e15d9de9-761b-4ebb-85e4-fb4da82fe0c1"),sQuery(id+"F3.wireOp",EDGE,"7ad34d33-c3e0-4451-9494-264813b44421"),sQuery(id+"F3.wireOp",EDGE,"67097021-bec9-466b-973d-5e6d45f4df4b"),sQuery(id+"F3.wireOp",EDGE,"00a890b4-48cc-4d89-b077-d2e06b7e5dbd"),sQuery(id+"F3.wireOp",EDGE,"d7c93b06-eb0f-47ea-baf6-846be92fd260"),sQuery(id+"F3.wireOp",EDGE,"a2e0747d-17c9-4fc1-8cc4-fdaf8f8abfb8"),sQuery(id+"F3.wireOp",EDGE,"3372003e-2229-4558-92bf-d17431c63efe"),sQuery(id+"F3.wireOp",EDGE,"a3b7acfd-c5e1-4a2a-8837-4aa7ee2b56f2"),sQuery(id+"F3.wireOp",EDGE,"3a959202-a4c0-400d-9680-62f35a8281c4"),sQuery(id+"F3.wireOp",EDGE,"a8ddc96f-2760-4d3c-8c77-f7573f30c19d"),sQuery(id+"F3.wireOp",EDGE,"a7586bee-e7f3-42ba-b3eb-820e0c658ff0"),sQuery(id+"F3.wireOp",EDGE,"b1cc2dc8-0320-49c9-bff7-099614d47ec2"),sQuery(id+"F3.wireOp",EDGE,"8457c3d1-b865-450b-adf8-14351497ea25"),sQuery(id+"F3.wireOp",EDGE,"98e9128e-370b-4b50-baf2-f15997247181"),sQuery(id+"F3.wireOp",EDGE,"8a87dfde-57a5-43ec-bda8-da6793a18b73"),sQuery(id+"F3.wireOp",EDGE,"afad9ccd-78bf-4ea0-9416-078eea4e9aa8"),sQuery(id+"F3.wireOp",EDGE,"466440c7-c3a5-4f11-b76c-acbc010caadf"),sQuery(id+"F3.wireOp",EDGE,"802f05ca-83e2-4aad-b0e9-72984b1bff10"),sQuery(id+"F3.wireOp",EDGE,"380c98ad-3319-44b2-9d8b-94ab420c3658"),sQuery(id+"F3.wireOp",EDGE,"a3769aee-8604-4823-b0d7-44a8c97383a4"),sQuery(id+"F3.wireOp",EDGE,"1f52d996-aca9-497a-b7e2-600370ae6949"),sQuery(id+"F3.wireOp",EDGE,"67b67c53-8780-4a85-a3f5-8daf53ab2c04"),sQuery(id+"F3.wireOp",EDGE,"f16f5723-851b-4393-9b75-be1a9d8f5853"),sQuery(id+"F3.wireOp",EDGE,"bb383e53-8237-49ad-9faf-dc4e0ce0de8c"),sQuery(id+"F3.wireOp",EDGE,"7ec6589b-37b5-4f7e-8b9c-d80ded9de812"),sQuery(id+"F3.wireOp",EDGE,"08880140-c83c-486f-b26b-0da67e4ff0c8"),sQuery(id+"F3.wireOp",EDGE,"999823e5-c0bd-483c-88d5-3655cf2a24eb"),sQuery(id+"F3.wireOp",EDGE,"07b7ce3e-532a-4886-a937-3375ccde0f0e"),sQuery(id+"F3.wireOp",EDGE,"9dc5ff66-08db-4f58-bb2d-51863b145979"),sQuery(id+"F3.wireOp",EDGE,"eceeb68e-c3d4-4b94-b62d-56caa49e50b4"),sQuery(id+"F3.wireOp",EDGE,"f41b9d86-6198-4803-9e05-c2d42cc78262"),sQuery(id+"F3.wireOp",EDGE,"0ff7a2ec-16ac-4922-a147-e8dcbe953c89"),sQuery(id+"F3.wireOp",EDGE,"a5f3f9c6-b258-48e6-ac81-471d37944c80"),sQuery(id+"F3.wireOp",EDGE,"5d3368fa-4b93-4609-8d85-d76e8ccb9f70"),sQuery(id+"F3.wireOp",EDGE,"93e705d2-6a1b-4fd1-98fa-f7101df4e23e"),sQuery(id+"F3.wireOp",EDGE,"8560622e-69b7-4d5e-9719-021d16e605a7"),sQuery(id+"F3.wireOp",EDGE,"1269a461-9fb2-497b-9541-76a3c22068ad"),sQuery(id+"F3.wireOp",EDGE,"738108aa-f0e9-4788-8b29-18c751f9aff9"),sQuery(id+"F3.wireOp",EDGE,"c65de39b-1758-467b-980b-9cd9929a3d64"),sQuery(id+"F3.wireOp",EDGE,"756d41d9-dbab-496a-ae15-4fc1659277d1"),sQuery(id+"F3.wireOp",EDGE,"bac2d005-4ac7-492e-a373-e2c006eb4bfb"),sQuery(id+"F3.wireOp",EDGE,"85860d99-9013-4759-aa43-5487a99c41a6"),sQuery(id+"F3.wireOp",EDGE,"8b924ac3-f2a5-4087-bc70-23e4203bc6ae"),sQuery(id+"F3.wireOp",EDGE,"0916d5f8-d38e-4792-80fc-1789f880af75"),sQuery(id+"F3.wireOp",EDGE,"a8e22637-be16-4ef6-ae94-6b23f87871d8"),sQuery(id+"F3.wireOp",EDGE,"63b035c0-ac75-420b-bf11-3ed09439bdeb"),sQuery(id+"F3.wireOp",EDGE,"b31ee2f9-b45b-4c92-b652-2d6a6fa9c3c5"),sQuery(id+"F3.wireOp",EDGE,"97893759-3520-4bf3-a33f-99cd94809b8e"),sQuery(id+"F3.wireOp",EDGE,"5b4603d3-bafa-43cc-99d2-3470666ae78c"),sQuery(id+"F3.wireOp",EDGE,"5dc276c1-ad75-4351-9532-710b6f957b72"),sQuery(id+"F3.wireOp",EDGE,"36f0a240-2e3b-4426-aa0a-071803ecff03"),sQuery(id+"F3.wireOp",EDGE,"57a6f11b-a6b4-4852-9993-7efa1ac7adaf"),sQuery(id+"F3.wireOp",EDGE,"754e6465-131f-4ec7-94bb-14c8c9e997d9"),sQuery(id+"F3.wireOp",EDGE,"34610aa0-aea1-4ba5-b03d-e18f9e4dd988"),sQuery(id+"F3.wireOp",EDGE,"5ea570f2-0fa4-4e78-adeb-6f516147bd71"),sQuery(id+"F3.wireOp",EDGE,"a26f9c50-1319-4f95-9820-85724e840a82"),sQuery(id+"F3.wireOp",EDGE,"0f090b8e-50f8-4d2c-bafe-bdde45b5ada4"),sQuery(id+"F3.wireOp",EDGE,"7117585e-1228-4300-a3e4-db51f78ee14c"),sQuery(id+"F3.wireOp",EDGE,"f8689b3f-eda0-439f-be03-f97530164dd3"),sQuery(id+"F3.wireOp",EDGE,"203b92fc-7d6b-43b1-989f-c26bb414d1b2"),sQuery(id+"F3.wireOp",EDGE,"5679199e-b528-48c1-b11b-944558c980a8"),sQuery(id+"F3.wireOp",EDGE,"161a3187-e8c9-4983-85cb-49f6f7c5f339"),sQuery(id+"F3.wireOp",EDGE,"a6bb4c2e-d0b8-44ae-8978-b823822b2f62"),sQuery(id+"F3.wireOp",EDGE,"04610945-ebf1-46a7-939e-e9ad5c23b445"),sQuery(id+"F3.wireOp",EDGE,"39c5cceb-1e69-460b-a124-bfb35590148b"),sQuery(id+"F3.wireOp",EDGE,"0cac30ec-ac55-47a7-846b-215a65482ff4"),sQuery(id+"F3.wireOp",EDGE,"18e99eaa-199b-443f-9dbd-6b716a5c9e1a"),sQuery(id+"F3.wireOp",EDGE,"17e41e31-d35b-450a-824b-3514a620a768"),sQuery(id+"F3.wireOp",EDGE,"0524b4ea-f730-407d-9352-39bf46fc0a80"),sQuery(id+"F3.wireOp",EDGE,"0f5f3ec3-e111-4418-b32e-94214185c3f1"),sQuery(id+"F3.wireOp",EDGE,"f23df1d5-483b-4032-8ad5-835132419385"),sQuery(id+"F3.wireOp",EDGE,"45bb317c-8eae-478e-b6d9-0e3c22a77cd0"),sQuery(id+"F3.wireOp",EDGE,"bfa43031-806e-4edd-9d98-8f8031f24426"),sQuery(id+"F3.wireOp",EDGE,"f36d8605-259b-4c9b-a64e-53b25295e8f3"),sQuery(id+"F3.wireOp",EDGE,"aff81085-56e9-4dfb-b6c6-55d1b18e30ec"),sQuery(id+"F3.wireOp",EDGE,"64adf307-3694-4edf-9718-bdfb3c99b58e"),sQuery(id+"F3.wireOp",EDGE,"25b1a257-ab12-4c00-be89-3991f43899a6"),sQuery(id+"F3.wireOp",EDGE,"aea91b0e-bcb3-49ee-815e-f65bcd86e2fd"),sQuery(id+"F3.wireOp",EDGE,"dbcc5a10-4f3a-4c7a-88d6-be6ad4de9be3"),sQuery(id+"F3.wireOp",EDGE,"1300bb3d-7ac1-4f9a-91f7-a402756fa661"),sQuery(id+"F3.wireOp",EDGE,"977e18cc-96be-430d-abcb-59930a13b9f0"),sQuery(id+"F3.wireOp",EDGE,"6ba64014-859f-4af9-984d-7bedc4939d73"),sQuery(id+"F3.wireOp",EDGE,"a11d0871-7a20-44ed-b7c6-c8352198d685"),sQuery(id+"F3.wireOp",EDGE,"54e6f65c-df59-4b21-ab87-efc42813dc94"),sQuery(id+"F3.wireOp",EDGE,"f40db9cc-ce06-4c69-89d1-d6fb42ef8d4b"),sQuery(id+"F3.wireOp",EDGE,"290e4a50-9f37-415d-a77d-bcc76523f1d5"),sQuery(id+"F3.wireOp",EDGE,"9830cdb9-701e-436b-837d-810825575392"),sQuery(id+"F3.wireOp",EDGE,"c7a824f2-db51-401e-825b-f3d6b21fe486"),sQuery(id+"F3.wireOp",EDGE,"ad94afe7-f28e-4b73-8a1f-55e2296c2bca"),sQuery(id+"F3.wireOp",EDGE,"084e083d-f148-4afa-b33f-1a4e602a2cd3"),sQuery(id+"F3.wireOp",EDGE,"bd15d313-7969-47b0-a722-98a9e6f22b08"),sQuery(id+"F3.wireOp",EDGE,"cc41519e-33da-4bbe-b848-f50a6c4e3b84"),sQuery(id+"F3.wireOp",EDGE,"ef344dea-b100-4b94-8c68-aa645f94dcae"),sQuery(id+"F3.wireOp",EDGE,"5a8aaeff-4269-443b-ae8b-5febe453ce12"),sQuery(id+"F3.wireOp",EDGE,"bd50b30f-2b72-4484-bc14-e42f99e813fa"),sQuery(id+"F3.wireOp",EDGE,"df1e4ad1-31e9-48e5-81d7-2711f6055c90"),sQuery(id+"F3.wireOp",EDGE,"ae18261a-30a3-4fc6-b873-f9da53a0b074"),sQuery(id+"F3.wireOp",EDGE,"855ca772-78cf-44b3-8a8b-1af7bb703fff"),sQuery(id+"F3.wireOp",EDGE,"a3449970-7c4b-402d-9747-1e28fc93d780"),sQuery(id+"F3.wireOp",EDGE,"c398989f-697f-4569-b9cd-5a2f5c0afdfa"),sQuery(id+"F3.wireOp",EDGE,"be9c560b-05f3-44fc-9c24-5fb0ee9f46be"),sQuery(id+"F3.wireOp",EDGE,"6fb91335-0444-47dc-9a68-f012f8e9e497"),sQuery(id+"F3.wireOp",EDGE,"d4280811-013f-4bce-ad33-1f82742e0dd9"),sQuery(id+"F3.wireOp",EDGE,"0b1bd235-f05c-4c19-962e-4f72b657b4a9"),sQuery(id+"F3.wireOp",EDGE,"6ecc38b7-87ea-4faf-bea4-6a361bf0c5f1"),sQuery(id+"F3.wireOp",EDGE,"93b60800-9d39-4d9f-8d8b-3e53798cad8d"),sQuery(id+"F3.wireOp",EDGE,"bc0c8946-68bd-4333-991b-e604499cce4a"),sQuery(id+"F3.wireOp",EDGE,"03ec03ef-69c7-4f14-a4be-1943b1b26620"),sQuery(id+"F3.wireOp",EDGE,"70288df1-7fe0-44d6-81a0-38b7c6254652"),sQuery(id+"F3.wireOp",EDGE,"373aa3d3-7813-439a-aa6d-11bf33d8b24e"),sQuery(id+"F3.wireOp",EDGE,"45d8d8cd-c432-46a9-ba83-ca98e6a8b331"),sQuery(id+"F3.wireOp",EDGE,"30eeae1c-e414-4273-926e-a242566325a0"),sQuery(id+"F3.wireOp",EDGE,"2c9bb13c-11d4-40b6-bcc6-d08f2723e091"),sQuery(id+"F3.wireOp",EDGE,"a482991e-2cf6-48ab-8e8e-3e4f8b67d4b7"),sQuery(id+"F3.wireOp",EDGE,"06891698-4df7-4f94-84c6-72103b62673b"),sQuery(id+"F3.wireOp",EDGE,"ecab2fa4-6225-467e-82ee-4732fa611de3"),sQuery(id+"F3.wireOp",EDGE,"649bfd1a-9215-4127-87d3-ed0b3f5772d5"),sQuery(id+"F3.wireOp",EDGE,"bf54d2c0-65f1-4ff6-871b-ae601eb9e7cc"),sQuery(id+"F3.wireOp",EDGE,"29274e08-d376-4eb2-907f-b860139ca4db"),sQuery(id+"F3.wireOp",EDGE,"cd2404f3-3954-470e-aa5a-a76806b6835a"),sQuery(id+"F3.wireOp",EDGE,"dbd5f9e9-56cf-4ed4-a9fb-97d5f2897854"),sQuery(id+"F3.wireOp",EDGE,"a3f94ff5-44de-4570-8f07-2fa58cf7f771"),sQuery(id+"F3.wireOp",EDGE,"21d034b1-97d0-4cdd-a783-b5eef86ebc99"),sQuery(id+"F3.wireOp",EDGE,"a60bbc0a-156d-4d16-82fa-9e5e5c2e844d"),sQuery(id+"F3.wireOp",EDGE,"a528a1a4-90cb-4bac-a68a-6d2da3dfac97"),sQuery(id+"F3.wireOp",EDGE,"2897741f-4c31-4951-9326-161b0945bc72"),sQuery(id+"F3.wireOp",EDGE,"138138aa-b9e4-4038-8e12-b0c5a13fea39"),sQuery(id+"F3.wireOp",EDGE,"8187800a-b1e6-4d83-98c7-9c355a36d6c6"),sQuery(id+"F3.wireOp",EDGE,"9701c027-796e-4d6b-a002-6605f6ee80e3"),sQuery(id+"F3.wireOp",EDGE,"77e98c07-d0dc-4f04-9c1b-99f3355fd8a7"),sQuery(id+"F3.wireOp",EDGE,"4d81288f-f128-4ca3-b627-6a5b28d496de"),sQuery(id+"F3.wireOp",EDGE,"d1bad90c-4b8f-41a3-ac4a-47f6b9aadffb"),sQuery(id+"F3.wireOp",EDGE,"ed70a943-00e2-466a-98de-2b8f6be6381d"),sQuery(id+"F3.wireOp",EDGE,"ca15953e-95cc-4037-b944-8707390692ef"),sQuery(id+"F3.wireOp",EDGE,"d795c5ca-c7fa-4fa3-aceb-2aaa567452cf"),sQuery(id+"F3.wireOp",EDGE,"243c0ca0-aa5e-4f5e-bdca-16c8987a887f"),sQuery(id+"F3.wireOp",EDGE,"bc9fa2c3-366d-471d-97c7-70100b7d8498"),sQuery(id+"F3.wireOp",EDGE,"504d9464-3638-4fca-aca5-74d973fcd556"),sQuery(id+"F3.wireOp",EDGE,"904397ff-7935-4a86-961c-5e675a147941"),sQuery(id+"F3.wireOp",EDGE,"1c96a42e-db33-464e-939b-1401c8f3dc56"),sQuery(id+"F3.wireOp",EDGE,"c93a136a-b456-4118-8f96-0ff909422201"),sQuery(id+"F3.wireOp",EDGE,"18e409b6-aa76-48e1-b07a-2118d4afb836"),sQuery(id+"F3.wireOp",EDGE,"453d7378-4718-464e-bd01-99f678aa0ea9"),sQuery(id+"F3.wireOp",EDGE,"7a3a24a2-148e-4b54-a0ad-eba860c7fb7a"),sQuery(id+"F3.wireOp",EDGE,"8ef3a38d-664a-40d3-aa3a-b2176ce58029"),sQuery(id+"F3.wireOp",EDGE,"431eb4cf-7232-4f15-8871-3b81c8abfe77"),sQuery(id+"F3.wireOp",EDGE,"6c5b3992-7da6-44e2-8879-de97f4632d9e"),sQuery(id+"F3.wireOp",EDGE,"700eb462-5239-4aff-bb8e-38754561fb95"),sQuery(id+"F3.wireOp",EDGE,"76e36e64-b254-46aa-a38f-830b3794fe19"),sQuery(id+"F3.wireOp",EDGE,"7d77c6f3-f087-4291-933e-8eee58b8f264"),sQuery(id+"F3.wireOp",EDGE,"26ca988e-826e-47f0-98d2-556df3f9bf42"),sQuery(id+"F3.wireOp",EDGE,"4810f180-f491-4bec-8c84-57ef4a51e416"),sQuery(id+"F3.wireOp",EDGE,"a2f87652-967a-430d-baa5-b94727ffa003"),sQuery(id+"F3.wireOp",EDGE,"d08c92d7-9c6d-4fd1-b266-1e49aef11731"),sQuery(id+"F3.wireOp",EDGE,"60113931-40ab-4c1d-a52c-fd4caa2a44f1"),sQuery(id+"F3.wireOp",EDGE,"b1aa1ff4-0d0d-408d-8a15-147b6324842e"),sQuery(id+"F3.wireOp",EDGE,"38f109ba-2aae-4bc4-9a22-f038beb12030"),sQuery(id+"F3.wireOp",EDGE,"7441d3f1-614a-426d-b871-a4e1a13c6e7e"),sQuery(id+"F3.wireOp",EDGE,"847a2f50-4ef1-49b5-b090-5f8521ee8ca1"),sQuery(id+"F3.wireOp",EDGE,"98bd5360-29b1-4412-9294-02ef6551eecc"),sQuery(id+"F3.wireOp",EDGE,"cb6e78c9-5cdf-4276-b840-5cfec84caed4"),sQuery(id+"F3.wireOp",EDGE,"1736b3be-cda2-4842-aefb-283565cc4c62"),sQuery(id+"F3.wireOp",EDGE,"438710e5-800b-4df2-8fff-3432d8aae595"),sQuery(id+"F3.wireOp",EDGE,"f69e7794-4715-43f7-a271-aa5e98ef7e68"),sQuery(id+"F3.wireOp",EDGE,"02c9a714-cd92-4f6e-be60-84f6aca8f508"),sQuery(id+"F3.wireOp",EDGE,"e0730c34-1f26-4745-a30f-e9a291eaeb6f"),sQuery(id+"F3.wireOp",EDGE,"9554880d-9851-4e54-af44-454a4419ca75"),sQuery(id+"F3.wireOp",EDGE,"efb41e31-abb5-42fa-83db-f78bf43b7196"),sQuery(id+"F3.wireOp",EDGE,"1bdde1b5-8417-49bf-b267-4e22f08aa6f4"),sQuery(id+"F3.wireOp",EDGE,"72509248-fad9-462b-b756-80664d0faace"),sQuery(id+"F3.wireOp",EDGE,"76f0ff31-d45f-4a8a-86ee-2e308ecada5a"),sQuery(id+"F3.wireOp",EDGE,"E505"),sQuery(id+"F3.wireOp",EDGE,"E506"),sQuery(id+"F3.wireOp",EDGE,"E507")])]});
            var Q1;
            Q1=makeQuery(id+"F1.opExtrude","SWEPT_BODY",BODY,{"disambiguationData":[OSD([sQuery(id+"F0.wireOp",EDGE,"E0"),sQuery(id+"F0.wireOp",EDGE,"E1"),sQuery(id+"F0.wireOp",EDGE,"E2"),sQuery(id+"F0.wireOp",EDGE,"E3"),sQuery(id+"F0.wireOp",EDGE,"E4"),sQuery(id+"F0.wireOp",EDGE,"E5"),sQuery(id+"F0.wireOp",EDGE,"E6"),sQuery(id+"F0.wireOp",EDGE,"E7"),sQuery(id+"F0.wireOp",EDGE,"E8"),sQuery(id+"F0.wireOp",EDGE,"E9"),sQuery(id+"F0.wireOp",EDGE,"E10"),sQuery(id+"F0.wireOp",EDGE,"E11"),sQuery(id+"F0.wireOp",EDGE,"E12"),sQuery(id+"F0.wireOp",EDGE,"E13"),sQuery(id+"F0.wireOp",EDGE,"E14"),sQuery(id+"F0.wireOp",EDGE,"E15"),sQuery(id+"F0.wireOp",EDGE,"E16"),sQuery(id+"F0.wireOp",EDGE,"E17"),sQuery(id+"F0.wireOp",EDGE,"E18"),sQuery(id+"F0.wireOp",EDGE,"E19"),sQuery(id+"F0.wireOp",EDGE,"E20"),sQuery(id+"F0.wireOp",EDGE,"E21"),sQuery(id+"F0.wireOp",EDGE,"E22"),sQuery(id+"F0.wireOp",EDGE,"E23"),sQuery(id+"F0.wireOp",EDGE,"E24"),sQuery(id+"F0.wireOp",EDGE,"E25"),sQuery(id+"F0.wireOp",EDGE,"E26"),sQuery(id+"F0.wireOp",EDGE,"E27"),sQuery(id+"F0.wireOp",EDGE,"E28"),sQuery(id+"F0.wireOp",EDGE,"E29"),sQuery(id+"F0.wireOp",EDGE,"E30"),sQuery(id+"F0.wireOp",EDGE,"E31"),sQuery(id+"F0.wireOp",EDGE,"E32"),sQuery(id+"F0.wireOp",EDGE,"E33"),sQuery(id+"F0.wireOp",EDGE,"E34"),sQuery(id+"F0.wireOp",EDGE,"E35"),sQuery(id+"F0.wireOp",EDGE,"E36"),sQuery(id+"F0.wireOp",EDGE,"E37"),sQuery(id+"F0.wireOp",EDGE,"E38"),sQuery(id+"F0.wireOp",EDGE,"E39"),sQuery(id+"F0.wireOp",EDGE,"E40"),sQuery(id+"F0.wireOp",EDGE,"E41"),sQuery(id+"F0.wireOp",EDGE,"E42"),sQuery(id+"F0.wireOp",EDGE,"E43"),sQuery(id+"F0.wireOp",EDGE,"E44"),sQuery(id+"F0.wireOp",EDGE,"E45"),sQuery(id+"F0.wireOp",EDGE,"E46"),sQuery(id+"F0.wireOp",EDGE,"E47"),sQuery(id+"F0.wireOp",EDGE,"E48"),sQuery(id+"F0.wireOp",EDGE,"E49"),sQuery(id+"F0.wireOp",EDGE,"E50"),sQuery(id+"F0.wireOp",EDGE,"E51"),sQuery(id+"F0.wireOp",EDGE,"E52"),sQuery(id+"F0.wireOp",EDGE,"E53"),sQuery(id+"F0.wireOp",EDGE,"E54"),sQuery(id+"F0.wireOp",EDGE,"E55"),sQuery(id+"F0.wireOp",EDGE,"E56"),sQuery(id+"F0.wireOp",EDGE,"E57"),sQuery(id+"F0.wireOp",EDGE,"E58"),sQuery(id+"F0.wireOp",EDGE,"E59"),sQuery(id+"F0.wireOp",EDGE,"E60"),sQuery(id+"F0.wireOp",EDGE,"E61"),sQuery(id+"F0.wireOp",EDGE,"E62"),sQuery(id+"F0.wireOp",EDGE,"E63"),sQuery(id+"F0.wireOp",EDGE,"E64"),sQuery(id+"F0.wireOp",EDGE,"E65"),sQuery(id+"F0.wireOp",EDGE,"E66"),sQuery(id+"F0.wireOp",EDGE,"E67"),sQuery(id+"F0.wireOp",EDGE,"E68"),sQuery(id+"F0.wireOp",EDGE,"E69"),sQuery(id+"F0.wireOp",EDGE,"E70"),sQuery(id+"F0.wireOp",EDGE,"E71"),sQuery(id+"F0.wireOp",EDGE,"E72"),sQuery(id+"F0.wireOp",EDGE,"E73"),sQuery(id+"F0.wireOp",EDGE,"E74"),sQuery(id+"F0.wireOp",EDGE,"E75"),sQuery(id+"F0.wireOp",EDGE,"E76"),sQuery(id+"F0.wireOp",EDGE,"E77"),sQuery(id+"F0.wireOp",EDGE,"E78"),sQuery(id+"F0.wireOp",EDGE,"E79"),sQuery(id+"F0.wireOp",EDGE,"E80"),sQuery(id+"F0.wireOp",EDGE,"E81"),sQuery(id+"F0.wireOp",EDGE,"E82"),sQuery(id+"F0.wireOp",EDGE,"E83"),sQuery(id+"F0.wireOp",EDGE,"E84"),sQuery(id+"F0.wireOp",EDGE,"E85"),sQuery(id+"F0.wireOp",EDGE,"E86"),sQuery(id+"F0.wireOp",EDGE,"E87"),sQuery(id+"F0.wireOp",EDGE,"E88"),sQuery(id+"F0.wireOp",EDGE,"E89"),sQuery(id+"F0.wireOp",EDGE,"E90"),sQuery(id+"F0.wireOp",EDGE,"E91"),sQuery(id+"F0.wireOp",EDGE,"E92"),sQuery(id+"F0.wireOp",EDGE,"E93"),sQuery(id+"F0.wireOp",EDGE,"E94"),sQuery(id+"F0.wireOp",EDGE,"E95"),sQuery(id+"F0.wireOp",EDGE,"E96"),sQuery(id+"F0.wireOp",EDGE,"E97"),sQuery(id+"F0.wireOp",EDGE,"E98"),sQuery(id+"F0.wireOp",EDGE,"E99"),sQuery(id+"F0.wireOp",EDGE,"E100"),sQuery(id+"F0.wireOp",EDGE,"E101"),sQuery(id+"F0.wireOp",EDGE,"E102"),sQuery(id+"F0.wireOp",EDGE,"E103"),sQuery(id+"F0.wireOp",EDGE,"E104"),sQuery(id+"F0.wireOp",EDGE,"E105"),sQuery(id+"F0.wireOp",EDGE,"E106"),sQuery(id+"F0.wireOp",EDGE,"E107"),sQuery(id+"F0.wireOp",EDGE,"E108"),sQuery(id+"F0.wireOp",EDGE,"E109"),sQuery(id+"F0.wireOp",EDGE,"E110"),sQuery(id+"F0.wireOp",EDGE,"E111"),sQuery(id+"F0.wireOp",EDGE,"E112"),sQuery(id+"F0.wireOp",EDGE,"E113"),sQuery(id+"F0.wireOp",EDGE,"E114"),sQuery(id+"F0.wireOp",EDGE,"E115"),sQuery(id+"F0.wireOp",EDGE,"E116"),sQuery(id+"F0.wireOp",EDGE,"E117"),sQuery(id+"F0.wireOp",EDGE,"E118"),sQuery(id+"F0.wireOp",EDGE,"E119"),sQuery(id+"F0.wireOp",EDGE,"E120"),sQuery(id+"F0.wireOp",EDGE,"E121"),sQuery(id+"F0.wireOp",EDGE,"E122"),sQuery(id+"F0.wireOp",EDGE,"E123"),sQuery(id+"F0.wireOp",EDGE,"E124"),sQuery(id+"F0.wireOp",EDGE,"E125"),sQuery(id+"F0.wireOp",EDGE,"E126"),sQuery(id+"F0.wireOp",EDGE,"E127"),sQuery(id+"F0.wireOp",EDGE,"E128"),sQuery(id+"F0.wireOp",EDGE,"E129"),sQuery(id+"F0.wireOp",EDGE,"E130"),sQuery(id+"F0.wireOp",EDGE,"E131"),sQuery(id+"F0.wireOp",EDGE,"E132"),sQuery(id+"F0.wireOp",EDGE,"E133"),sQuery(id+"F0.wireOp",EDGE,"E134"),sQuery(id+"F0.wireOp",EDGE,"E135"),sQuery(id+"F0.wireOp",EDGE,"E136"),sQuery(id+"F0.wireOp",EDGE,"E137"),sQuery(id+"F0.wireOp",EDGE,"E138"),sQuery(id+"F0.wireOp",EDGE,"E139"),sQuery(id+"F0.wireOp",EDGE,"E140"),sQuery(id+"F0.wireOp",EDGE,"E141"),sQuery(id+"F0.wireOp",EDGE,"E142"),sQuery(id+"F0.wireOp",EDGE,"E143"),sQuery(id+"F0.wireOp",EDGE,"E144"),sQuery(id+"F0.wireOp",EDGE,"E145"),sQuery(id+"F0.wireOp",EDGE,"E146"),sQuery(id+"F0.wireOp",EDGE,"E147"),sQuery(id+"F0.wireOp",EDGE,"E148"),sQuery(id+"F0.wireOp",EDGE,"E149"),sQuery(id+"F0.wireOp",EDGE,"E150"),sQuery(id+"F0.wireOp",EDGE,"E151"),sQuery(id+"F0.wireOp",EDGE,"E152"),sQuery(id+"F0.wireOp",EDGE,"E153"),sQuery(id+"F0.wireOp",EDGE,"E154"),sQuery(id+"F0.wireOp",EDGE,"E155"),sQuery(id+"F0.wireOp",EDGE,"E156"),sQuery(id+"F0.wireOp",EDGE,"E157"),sQuery(id+"F0.wireOp",EDGE,"E158"),sQuery(id+"F0.wireOp",EDGE,"E159"),sQuery(id+"F0.wireOp",EDGE,"E160"),sQuery(id+"F0.wireOp",EDGE,"E161"),sQuery(id+"F0.wireOp",EDGE,"E162"),sQuery(id+"F0.wireOp",EDGE,"E163"),sQuery(id+"F0.wireOp",EDGE,"E164"),sQuery(id+"F0.wireOp",EDGE,"E165"),sQuery(id+"F0.wireOp",EDGE,"E166"),sQuery(id+"F0.wireOp",EDGE,"E167"),sQuery(id+"F0.wireOp",EDGE,"E168"),sQuery(id+"F0.wireOp",EDGE,"E169"),sQuery(id+"F0.wireOp",EDGE,"E170"),sQuery(id+"F0.wireOp",EDGE,"E171"),sQuery(id+"F0.wireOp",EDGE,"E172"),sQuery(id+"F0.wireOp",EDGE,"E173"),sQuery(id+"F0.wireOp",EDGE,"E174"),sQuery(id+"F0.wireOp",EDGE,"E175"),sQuery(id+"F0.wireOp",EDGE,"E176"),sQuery(id+"F0.wireOp",EDGE,"E177"),sQuery(id+"F0.wireOp",EDGE,"E178"),sQuery(id+"F0.wireOp",EDGE,"E179"),sQuery(id+"F0.wireOp",EDGE,"E180"),sQuery(id+"F0.wireOp",EDGE,"E181"),sQuery(id+"F0.wireOp",EDGE,"E182"),sQuery(id+"F0.wireOp",EDGE,"E183"),sQuery(id+"F0.wireOp",EDGE,"E184"),sQuery(id+"F0.wireOp",EDGE,"E185"),sQuery(id+"F0.wireOp",EDGE,"E186"),sQuery(id+"F0.wireOp",EDGE,"E187"),sQuery(id+"F0.wireOp",EDGE,"E188"),sQuery(id+"F0.wireOp",EDGE,"E189"),sQuery(id+"F0.wireOp",EDGE,"E190"),sQuery(id+"F0.wireOp",EDGE,"E191"),sQuery(id+"F0.wireOp",EDGE,"E192"),sQuery(id+"F0.wireOp",EDGE,"E193"),sQuery(id+"F0.wireOp",EDGE,"E194"),sQuery(id+"F0.wireOp",EDGE,"E195"),sQuery(id+"F0.wireOp",EDGE,"E196"),sQuery(id+"F0.wireOp",EDGE,"E197"),sQuery(id+"F0.wireOp",EDGE,"E198"),sQuery(id+"F0.wireOp",EDGE,"E199"),sQuery(id+"F0.wireOp",EDGE,"E200"),sQuery(id+"F0.wireOp",EDGE,"E201"),sQuery(id+"F0.wireOp",EDGE,"E202"),sQuery(id+"F0.wireOp",EDGE,"E203"),sQuery(id+"F0.wireOp",EDGE,"E204"),sQuery(id+"F0.wireOp",EDGE,"E205"),sQuery(id+"F0.wireOp",EDGE,"E206"),sQuery(id+"F0.wireOp",EDGE,"E207"),sQuery(id+"F0.wireOp",EDGE,"E208"),sQuery(id+"F0.wireOp",EDGE,"E209"),sQuery(id+"F0.wireOp",EDGE,"E210"),sQuery(id+"F0.wireOp",EDGE,"E211"),sQuery(id+"F0.wireOp",EDGE,"E212"),sQuery(id+"F0.wireOp",EDGE,"E213"),sQuery(id+"F0.wireOp",EDGE,"E214"),sQuery(id+"F0.wireOp",EDGE,"E215"),sQuery(id+"F0.wireOp",EDGE,"E216"),sQuery(id+"F0.wireOp",EDGE,"E217"),sQuery(id+"F0.wireOp",EDGE,"E218"),sQuery(id+"F0.wireOp",EDGE,"E219"),sQuery(id+"F0.wireOp",EDGE,"E220"),sQuery(id+"F0.wireOp",EDGE,"E221"),sQuery(id+"F0.wireOp",EDGE,"E222"),sQuery(id+"F0.wireOp",EDGE,"E223"),sQuery(id+"F0.wireOp",EDGE,"E224"),sQuery(id+"F0.wireOp",EDGE,"E225"),sQuery(id+"F0.wireOp",EDGE,"E226"),sQuery(id+"F0.wireOp",EDGE,"E227"),sQuery(id+"F0.wireOp",EDGE,"E228"),sQuery(id+"F0.wireOp",EDGE,"E229"),sQuery(id+"F0.wireOp",EDGE,"E230"),sQuery(id+"F0.wireOp",EDGE,"E231"),sQuery(id+"F0.wireOp",EDGE,"E232"),sQuery(id+"F0.wireOp",EDGE,"E233"),sQuery(id+"F0.wireOp",EDGE,"E234"),sQuery(id+"F0.wireOp",EDGE,"E235"),sQuery(id+"F0.wireOp",EDGE,"E236"),sQuery(id+"F0.wireOp",EDGE,"E237"),sQuery(id+"F0.wireOp",EDGE,"E238"),sQuery(id+"F0.wireOp",EDGE,"E239"),sQuery(id+"F0.wireOp",EDGE,"E240"),sQuery(id+"F0.wireOp",EDGE,"E241"),sQuery(id+"F0.wireOp",EDGE,"E242"),sQuery(id+"F0.wireOp",EDGE,"E243"),sQuery(id+"F0.wireOp",EDGE,"E244"),sQuery(id+"F0.wireOp",EDGE,"E245"),sQuery(id+"F0.wireOp",EDGE,"E246"),sQuery(id+"F0.wireOp",EDGE,"E247"),sQuery(id+"F0.wireOp",EDGE,"E248"),sQuery(id+"F0.wireOp",EDGE,"E249"),sQuery(id+"F0.wireOp",EDGE,"E250"),sQuery(id+"F0.wireOp",EDGE,"E251"),sQuery(id+"F0.wireOp",EDGE,"E252"),sQuery(id+"F0.wireOp",EDGE,"E253"),sQuery(id+"F0.wireOp",EDGE,"E254"),sQuery(id+"F0.wireOp",EDGE,"E255"),sQuery(id+"F0.wireOp",EDGE,"E256"),sQuery(id+"F0.wireOp",EDGE,"E257"),sQuery(id+"F0.wireOp",EDGE,"E258"),sQuery(id+"F0.wireOp",EDGE,"E259"),sQuery(id+"F0.wireOp",EDGE,"E260"),sQuery(id+"F0.wireOp",EDGE,"E261"),sQuery(id+"F0.wireOp",EDGE,"E262"),sQuery(id+"F0.wireOp",EDGE,"E263"),sQuery(id+"F0.wireOp",EDGE,"E264"),sQuery(id+"F0.wireOp",EDGE,"E265"),sQuery(id+"F0.wireOp",EDGE,"E266"),sQuery(id+"F0.wireOp",EDGE,"E267"),sQuery(id+"F0.wireOp",EDGE,"E268"),sQuery(id+"F0.wireOp",EDGE,"E269"),sQuery(id+"F0.wireOp",EDGE,"E270"),sQuery(id+"F0.wireOp",EDGE,"E271"),sQuery(id+"F0.wireOp",EDGE,"E272"),sQuery(id+"F0.wireOp",EDGE,"E273"),sQuery(id+"F0.wireOp",EDGE,"E274"),sQuery(id+"F0.wireOp",EDGE,"E275"),sQuery(id+"F0.wireOp",EDGE,"E276"),sQuery(id+"F0.wireOp",EDGE,"E277"),sQuery(id+"F0.wireOp",EDGE,"E278"),sQuery(id+"F0.wireOp",EDGE,"E279"),sQuery(id+"F0.wireOp",EDGE,"E280"),sQuery(id+"F0.wireOp",EDGE,"E281"),sQuery(id+"F0.wireOp",EDGE,"E282"),sQuery(id+"F0.wireOp",EDGE,"E283"),sQuery(id+"F0.wireOp",EDGE,"E284"),sQuery(id+"F0.wireOp",EDGE,"E285"),sQuery(id+"F0.wireOp",EDGE,"E286"),sQuery(id+"F0.wireOp",EDGE,"E287"),sQuery(id+"F0.wireOp",EDGE,"E288"),sQuery(id+"F0.wireOp",EDGE,"E289"),sQuery(id+"F0.wireOp",EDGE,"E290"),sQuery(id+"F0.wireOp",EDGE,"E291"),sQuery(id+"F0.wireOp",EDGE,"E292"),sQuery(id+"F0.wireOp",EDGE,"E293"),sQuery(id+"F0.wireOp",EDGE,"E294"),sQuery(id+"F0.wireOp",EDGE,"E295"),sQuery(id+"F0.wireOp",EDGE,"E296"),sQuery(id+"F0.wireOp",EDGE,"E297"),sQuery(id+"F0.wireOp",EDGE,"E298"),sQuery(id+"F0.wireOp",EDGE,"E299"),sQuery(id+"F0.wireOp",EDGE,"E300"),sQuery(id+"F0.wireOp",EDGE,"E301"),sQuery(id+"F0.wireOp",EDGE,"E302"),sQuery(id+"F0.wireOp",EDGE,"E303"),sQuery(id+"F0.wireOp",EDGE,"E304"),sQuery(id+"F0.wireOp",EDGE,"E305"),sQuery(id+"F0.wireOp",EDGE,"E306"),sQuery(id+"F0.wireOp",EDGE,"E307"),sQuery(id+"F0.wireOp",EDGE,"E308"),sQuery(id+"F0.wireOp",EDGE,"E309"),sQuery(id+"F0.wireOp",EDGE,"E310"),sQuery(id+"F0.wireOp",EDGE,"E311"),sQuery(id+"F0.wireOp",EDGE,"E312"),sQuery(id+"F0.wireOp",EDGE,"E313"),sQuery(id+"F0.wireOp",EDGE,"E314"),sQuery(id+"F0.wireOp",EDGE,"E315"),sQuery(id+"F0.wireOp",EDGE,"E316"),sQuery(id+"F0.wireOp",EDGE,"E317"),sQuery(id+"F0.wireOp",EDGE,"E318"),sQuery(id+"F0.wireOp",EDGE,"E319"),sQuery(id+"F0.wireOp",EDGE,"E320"),sQuery(id+"F0.wireOp",EDGE,"E321"),sQuery(id+"F0.wireOp",EDGE,"E322"),sQuery(id+"F0.wireOp",EDGE,"E323"),sQuery(id+"F0.wireOp",EDGE,"E324"),sQuery(id+"F0.wireOp",EDGE,"E325"),sQuery(id+"F0.wireOp",EDGE,"E326"),sQuery(id+"F0.wireOp",EDGE,"E327"),sQuery(id+"F0.wireOp",EDGE,"E328"),sQuery(id+"F0.wireOp",EDGE,"E329"),sQuery(id+"F0.wireOp",EDGE,"E330"),sQuery(id+"F0.wireOp",EDGE,"E331"),sQuery(id+"F0.wireOp",EDGE,"E332"),sQuery(id+"F0.wireOp",EDGE,"E333"),sQuery(id+"F0.wireOp",EDGE,"E334"),sQuery(id+"F0.wireOp",EDGE,"E335"),sQuery(id+"F0.wireOp",EDGE,"E336"),sQuery(id+"F0.wireOp",EDGE,"E337"),sQuery(id+"F0.wireOp",EDGE,"E338"),sQuery(id+"F0.wireOp",EDGE,"E339"),sQuery(id+"F0.wireOp",EDGE,"E340"),sQuery(id+"F0.wireOp",EDGE,"E341"),sQuery(id+"F0.wireOp",EDGE,"E342"),sQuery(id+"F0.wireOp",EDGE,"E343"),sQuery(id+"F0.wireOp",EDGE,"E344"),sQuery(id+"F0.wireOp",EDGE,"E345"),sQuery(id+"F0.wireOp",EDGE,"E346"),sQuery(id+"F0.wireOp",EDGE,"E347"),sQuery(id+"F0.wireOp",EDGE,"E348"),sQuery(id+"F0.wireOp",EDGE,"E349"),sQuery(id+"F0.wireOp",EDGE,"E350"),sQuery(id+"F0.wireOp",EDGE,"E351"),sQuery(id+"F0.wireOp",EDGE,"E352"),sQuery(id+"F0.wireOp",EDGE,"E353"),sQuery(id+"F0.wireOp",EDGE,"E354"),sQuery(id+"F0.wireOp",EDGE,"E355"),sQuery(id+"F0.wireOp",EDGE,"E356"),sQuery(id+"F0.wireOp",EDGE,"E357"),sQuery(id+"F0.wireOp",EDGE,"E358"),sQuery(id+"F0.wireOp",EDGE,"E359"),sQuery(id+"F0.wireOp",EDGE,"E360"),sQuery(id+"F0.wireOp",EDGE,"E361"),sQuery(id+"F0.wireOp",EDGE,"E362"),sQuery(id+"F0.wireOp",EDGE,"E363"),sQuery(id+"F0.wireOp",EDGE,"E364"),sQuery(id+"F0.wireOp",EDGE,"E365"),sQuery(id+"F0.wireOp",EDGE,"E366"),sQuery(id+"F0.wireOp",EDGE,"E367"),sQuery(id+"F0.wireOp",EDGE,"E368"),sQuery(id+"F0.wireOp",EDGE,"E369"),sQuery(id+"F0.wireOp",EDGE,"E370"),sQuery(id+"F0.wireOp",EDGE,"E371"),sQuery(id+"F0.wireOp",EDGE,"E372"),sQuery(id+"F0.wireOp",EDGE,"E373"),sQuery(id+"F0.wireOp",EDGE,"E374"),sQuery(id+"F0.wireOp",EDGE,"E375"),sQuery(id+"F0.wireOp",EDGE,"E376"),sQuery(id+"F0.wireOp",EDGE,"E377"),sQuery(id+"F0.wireOp",EDGE,"E378"),sQuery(id+"F0.wireOp",EDGE,"E379"),sQuery(id+"F0.wireOp",EDGE,"E380"),sQuery(id+"F0.wireOp",EDGE,"E381"),sQuery(id+"F0.wireOp",EDGE,"E382"),sQuery(id+"F0.wireOp",EDGE,"E383"),sQuery(id+"F0.wireOp",EDGE,"E384"),sQuery(id+"F0.wireOp",EDGE,"E385"),sQuery(id+"F0.wireOp",EDGE,"E386"),sQuery(id+"F0.wireOp",EDGE,"E387"),sQuery(id+"F0.wireOp",EDGE,"E388"),sQuery(id+"F0.wireOp",EDGE,"E389"),sQuery(id+"F0.wireOp",EDGE,"E390"),sQuery(id+"F0.wireOp",EDGE,"E391"),sQuery(id+"F0.wireOp",EDGE,"E392"),sQuery(id+"F0.wireOp",EDGE,"E393"),sQuery(id+"F0.wireOp",EDGE,"E394"),sQuery(id+"F0.wireOp",EDGE,"E395"),sQuery(id+"F0.wireOp",EDGE,"E396"),sQuery(id+"F0.wireOp",EDGE,"E397"),sQuery(id+"F0.wireOp",EDGE,"E398"),sQuery(id+"F0.wireOp",EDGE,"E399"),sQuery(id+"F0.wireOp",EDGE,"E400"),sQuery(id+"F0.wireOp",EDGE,"E401"),sQuery(id+"F0.wireOp",EDGE,"E402"),sQuery(id+"F0.wireOp",EDGE,"E403"),sQuery(id+"F0.wireOp",EDGE,"E404"),sQuery(id+"F0.wireOp",EDGE,"E405"),sQuery(id+"F0.wireOp",EDGE,"E406"),sQuery(id+"F0.wireOp",EDGE,"E407"),sQuery(id+"F0.wireOp",EDGE,"E408"),sQuery(id+"F0.wireOp",EDGE,"E409"),sQuery(id+"F0.wireOp",EDGE,"E410"),sQuery(id+"F0.wireOp",EDGE,"E411"),sQuery(id+"F0.wireOp",EDGE,"E412"),sQuery(id+"F0.wireOp",EDGE,"E413"),sQuery(id+"F0.wireOp",EDGE,"E414"),sQuery(id+"F0.wireOp",EDGE,"E415"),sQuery(id+"F0.wireOp",EDGE,"E416"),sQuery(id+"F0.wireOp",EDGE,"E417"),sQuery(id+"F0.wireOp",EDGE,"E418"),sQuery(id+"F0.wireOp",EDGE,"E419"),sQuery(id+"F0.wireOp",EDGE,"E420"),sQuery(id+"F0.wireOp",EDGE,"E421"),sQuery(id+"F0.wireOp",EDGE,"E422"),sQuery(id+"F0.wireOp",EDGE,"E423"),sQuery(id+"F0.wireOp",EDGE,"E424"),sQuery(id+"F0.wireOp",EDGE,"E425"),sQuery(id+"F0.wireOp",EDGE,"E426"),sQuery(id+"F0.wireOp",EDGE,"E427"),sQuery(id+"F0.wireOp",EDGE,"E428"),sQuery(id+"F0.wireOp",EDGE,"E429"),sQuery(id+"F0.wireOp",EDGE,"E430"),sQuery(id+"F0.wireOp",EDGE,"E431"),sQuery(id+"F0.wireOp",EDGE,"E432"),sQuery(id+"F0.wireOp",EDGE,"E433"),sQuery(id+"F0.wireOp",EDGE,"E434"),sQuery(id+"F0.wireOp",EDGE,"E435"),sQuery(id+"F0.wireOp",EDGE,"E436"),sQuery(id+"F0.wireOp",EDGE,"E437"),sQuery(id+"F0.wireOp",EDGE,"E438"),sQuery(id+"F0.wireOp",EDGE,"E439"),sQuery(id+"F0.wireOp",EDGE,"E440"),sQuery(id+"F0.wireOp",EDGE,"E441"),sQuery(id+"F0.wireOp",EDGE,"E442"),sQuery(id+"F0.wireOp",EDGE,"E443"),sQuery(id+"F0.wireOp",EDGE,"E444"),sQuery(id+"F0.wireOp",EDGE,"E445"),sQuery(id+"F0.wireOp",EDGE,"E446"),sQuery(id+"F0.wireOp",EDGE,"E447"),sQuery(id+"F0.wireOp",EDGE,"E448"),sQuery(id+"F0.wireOp",EDGE,"E449"),sQuery(id+"F0.wireOp",EDGE,"E450"),sQuery(id+"F0.wireOp",EDGE,"E451"),sQuery(id+"F0.wireOp",EDGE,"E452"),sQuery(id+"F0.wireOp",EDGE,"E453"),sQuery(id+"F0.wireOp",EDGE,"E454"),sQuery(id+"F0.wireOp",EDGE,"E455"),sQuery(id+"F0.wireOp",EDGE,"E456"),sQuery(id+"F0.wireOp",EDGE,"E457"),sQuery(id+"F0.wireOp",EDGE,"E458"),sQuery(id+"F0.wireOp",EDGE,"E459"),sQuery(id+"F0.wireOp",EDGE,"E460"),sQuery(id+"F0.wireOp",EDGE,"E461"),sQuery(id+"F0.wireOp",EDGE,"E462"),sQuery(id+"F0.wireOp",EDGE,"E463"),sQuery(id+"F0.wireOp",EDGE,"E464"),sQuery(id+"F0.wireOp",EDGE,"E465"),sQuery(id+"F0.wireOp",EDGE,"E466"),sQuery(id+"F0.wireOp",EDGE,"E467"),sQuery(id+"F0.wireOp",EDGE,"E468"),sQuery(id+"F0.wireOp",EDGE,"E469"),sQuery(id+"F0.wireOp",EDGE,"E470"),sQuery(id+"F0.wireOp",EDGE,"E471"),sQuery(id+"F0.wireOp",EDGE,"E472"),sQuery(id+"F0.wireOp",EDGE,"E473"),sQuery(id+"F0.wireOp",EDGE,"E474"),sQuery(id+"F0.wireOp",EDGE,"E475"),sQuery(id+"F0.wireOp",EDGE,"E476"),sQuery(id+"F0.wireOp",EDGE,"E477"),sQuery(id+"F0.wireOp",EDGE,"E478"),sQuery(id+"F0.wireOp",EDGE,"E479"),sQuery(id+"F0.wireOp",EDGE,"E480"),sQuery(id+"F0.wireOp",EDGE,"E481"),sQuery(id+"F0.wireOp",EDGE,"E482"),sQuery(id+"F0.wireOp",EDGE,"E483"),sQuery(id+"F0.wireOp",EDGE,"E484"),sQuery(id+"F0.wireOp",EDGE,"E485"),sQuery(id+"F0.wireOp",EDGE,"E486"),sQuery(id+"F0.wireOp",EDGE,"E487"),sQuery(id+"F0.wireOp",EDGE,"E488"),sQuery(id+"F0.wireOp",EDGE,"E489"),sQuery(id+"F0.wireOp",EDGE,"E490"),sQuery(id+"F0.wireOp",EDGE,"E491"),sQuery(id+"F0.wireOp",EDGE,"E492"),sQuery(id+"F0.wireOp",EDGE,"E493"),sQuery(id+"F0.wireOp",EDGE,"E494"),sQuery(id+"F0.wireOp",EDGE,"E495"),sQuery(id+"F0.wireOp",EDGE,"E496"),sQuery(id+"F0.wireOp",EDGE,"E497"),sQuery(id+"F0.wireOp",EDGE,"E498"),sQuery(id+"F0.wireOp",EDGE,"E499"),sQuery(id+"F0.wireOp",EDGE,"E500"),sQuery(id+"F0.wireOp",EDGE,"E501"),sQuery(id+"F0.wireOp",EDGE,"E502"),sQuery(id+"F0.wireOp",EDGE,"E503")])]});
            booleanBodies(context, id + "F8", {"operationType" : BooleanOperationType.SUBTRACTION, "tools" : qUnion([Q0]), "targets" : qUnion([Q1])});
        }
        {
            var Q0;
            Q0=qCreatedBy(makeId("Top.planeOp"),FACE);
            var sketch = newSketch(context, id + "F9", { "sketchPlane" : qUnion([Q0])});
            skLineSegment(sketch, "E709", {"start": v(6.11, -0.46) * mm, "end": v(5.67, -0.4) * mm});
            skLineSegment(sketch, "E710", {"start": v(5.67, -0.4) * mm, "end": v(5.65, -0.52) * mm});
            skLineSegment(sketch, "E711", {"start": v(5.65, -0.52) * mm, "end": v(5.64, -0.55) * mm});
            skLineSegment(sketch, "E712", {"start": v(5.64, -0.55) * mm, "end": v(5.63, -0.57) * mm});
            skLineSegment(sketch, "E713", {"start": v(5.63, -0.57) * mm, "end": v(5.62, -0.6) * mm});
            skLineSegment(sketch, "E714", {"start": v(5.62, -0.6) * mm, "end": v(5.61, -0.61) * mm});
            skLineSegment(sketch, "E715", {"start": v(5.61, -0.61) * mm, "end": v(5.6, -0.63) * mm});
            skLineSegment(sketch, "E716", {"start": v(5.6, -0.63) * mm, "end": v(5.59, -0.64) * mm});
            skLineSegment(sketch, "E717", {"start": v(5.59, -0.64) * mm, "end": v(5.57, -0.66) * mm});
            skLineSegment(sketch, "E718", {"start": v(5.57, -0.66) * mm, "end": v(5.57, -0.66) * mm});
            skLineSegment(sketch, "E719", {"start": v(5.57, -0.66) * mm, "end": v(5.56, -0.67) * mm});
            skLineSegment(sketch, "E720", {"start": v(5.56, -0.67) * mm, "end": v(5.55, -0.67) * mm});
            skLineSegment(sketch, "E721", {"start": v(5.55, -0.67) * mm, "end": v(5.54, -0.68) * mm});
            skLineSegment(sketch, "E722", {"start": v(5.54, -0.68) * mm, "end": v(5.53, -0.68) * mm});
            skLineSegment(sketch, "E723", {"start": v(5.53, -0.68) * mm, "end": v(5.52, -0.69) * mm});
            skLineSegment(sketch, "E724", {"start": v(5.52, -0.69) * mm, "end": v(5.5, -0.7) * mm});
            skLineSegment(sketch, "E725", {"start": v(5.5, -0.7) * mm, "end": v(5.5, -0.7) * mm});
            skLineSegment(sketch, "E726", {"start": v(5.5, -0.7) * mm, "end": v(5.48, -0.7) * mm});
            skLineSegment(sketch, "E727", {"start": v(5.48, -0.7) * mm, "end": v(5.47, -0.7) * mm});
            skLineSegment(sketch, "E728", {"start": v(5.47, -0.7) * mm, "end": v(5.46, -0.7) * mm});
            skLineSegment(sketch, "E729", {"start": v(5.46, -0.7) * mm, "end": v(5.44, -0.7) * mm});
            skLineSegment(sketch, "E730", {"start": v(5.44, -0.7) * mm, "end": v(5.43, -0.7) * mm});
            skLineSegment(sketch, "E731", {"start": v(5.43, -0.7) * mm, "end": v(5.41, -0.7) * mm});
            skLineSegment(sketch, "E732", {"start": v(5.41, -0.7) * mm, "end": v(5.4, -0.71) * mm});
            skLineSegment(sketch, "E733", {"start": v(5.4, -0.71) * mm, "end": v(5.38, -0.71) * mm});
            skLineSegment(sketch, "E734", {"start": v(5.38, -0.71) * mm, "end": v(5.36, -0.71) * mm});
            skLineSegment(sketch, "E735", {"start": v(5.36, -0.71) * mm, "end": v(5.34, -0.7) * mm});
            skLineSegment(sketch, "E736", {"start": v(5.34, -0.7) * mm, "end": v(5.32, -0.7) * mm});
            skLineSegment(sketch, "E737", {"start": v(5.32, -0.7) * mm, "end": v(5.3, -0.7) * mm});
            skLineSegment(sketch, "E738", {"start": v(5.3, -0.7) * mm, "end": v(5.3, -0.7) * mm});
            skLineSegment(sketch, "E739", {"start": v(5.3, -0.7) * mm, "end": v(5.28, -0.7) * mm});
            skLineSegment(sketch, "E740", {"start": v(5.28, -0.7) * mm, "end": v(5.27, -0.7) * mm});
            skLineSegment(sketch, "E741", {"start": v(5.27, -0.7) * mm, "end": v(5.25, -0.7) * mm});
            skLineSegment(sketch, "E742", {"start": v(5.25, -0.7) * mm, "end": v(5.24, -0.7) * mm});
            skLineSegment(sketch, "E743", {"start": v(5.24, -0.7) * mm, "end": v(5.23, -0.7) * mm});
            skLineSegment(sketch, "E744", {"start": v(5.23, -0.7) * mm, "end": v(5.22, -0.69) * mm});
            skLineSegment(sketch, "E745", {"start": v(5.22, -0.69) * mm, "end": v(5.22, -0.68) * mm});
            skLineSegment(sketch, "E746", {"start": v(5.22, -0.68) * mm, "end": v(5.2, -0.68) * mm});
            skLineSegment(sketch, "E747", {"start": v(5.2, -0.68) * mm, "end": v(5.2, -0.67) * mm});
            skLineSegment(sketch, "E748", {"start": v(5.2, -0.67) * mm, "end": v(5.2, -0.67) * mm});
            skLineSegment(sketch, "E749", {"start": v(5.2, -0.67) * mm, "end": v(5.19, -0.67) * mm});
            skLineSegment(sketch, "E750", {"start": v(5.19, -0.67) * mm, "end": v(5.18, -0.65) * mm});
            skLineSegment(sketch, "E751", {"start": v(5.18, -0.65) * mm, "end": v(5.17, -0.64) * mm});
            skLineSegment(sketch, "E752", {"start": v(5.17, -0.64) * mm, "end": v(5.16, -0.63) * mm});
            skLineSegment(sketch, "E753", {"start": v(5.16, -0.63) * mm, "end": v(5.15, -0.62) * mm});
            skLineSegment(sketch, "E754", {"start": v(5.15, -0.62) * mm, "end": v(5.15, -0.61) * mm});
            skLineSegment(sketch, "E755", {"start": v(5.15, -0.61) * mm, "end": v(5.15, -0.6) * mm});
            skLineSegment(sketch, "E756", {"start": v(5.15, -0.6) * mm, "end": v(5.14, -0.6) * mm});
            skLineSegment(sketch, "E757", {"start": v(5.14, -0.6) * mm, "end": v(5.14, -0.58) * mm});
            skLineSegment(sketch, "E758", {"start": v(5.14, -0.58) * mm, "end": v(5.14, -0.57) * mm});
            skLineSegment(sketch, "E759", {"start": v(5.14, -0.57) * mm, "end": v(5.14, -0.56) * mm});
            skLineSegment(sketch, "E760", {"start": v(5.14, -0.56) * mm, "end": v(5.15, -0.56) * mm});
            skLineSegment(sketch, "E761", {"start": v(5.15, -0.56) * mm, "end": v(5.15, -0.55) * mm});
            skLineSegment(sketch, "E762", {"start": v(5.15, -0.55) * mm, "end": v(5.15, -0.55) * mm});
            skLineSegment(sketch, "E763", {"start": v(5.15, -0.55) * mm, "end": v(5.16, -0.54) * mm});
            skLineSegment(sketch, "E764", {"start": v(5.16, -0.54) * mm, "end": v(5.16, -0.54) * mm});
            skLineSegment(sketch, "E765", {"start": v(5.16, -0.54) * mm, "end": v(5.17, -0.53) * mm});
            skLineSegment(sketch, "E766", {"start": v(5.17, -0.53) * mm, "end": v(5.17, -0.53) * mm});
            skLineSegment(sketch, "E767", {"start": v(5.17, -0.53) * mm, "end": v(5.18, -0.53) * mm});
            skLineSegment(sketch, "E768", {"start": v(5.18, -0.53) * mm, "end": v(5.18, -0.53) * mm});
            skLineSegment(sketch, "E769", {"start": v(5.18, -0.53) * mm, "end": v(5.19, -0.52) * mm});
            skLineSegment(sketch, "E770", {"start": v(5.19, -0.52) * mm, "end": v(5.2, -0.52) * mm});
            skLineSegment(sketch, "E771", {"start": v(5.2, -0.52) * mm, "end": v(5.2, -0.52) * mm});
            skLineSegment(sketch, "E772", {"start": v(5.2, -0.52) * mm, "end": v(5.22, -0.51) * mm});
            skLineSegment(sketch, "E773", {"start": v(5.22, -0.51) * mm, "end": v(5.23, -0.5) * mm});
            skLineSegment(sketch, "E774", {"start": v(5.23, -0.5) * mm, "end": v(5.25, -0.5) * mm});
            skLineSegment(sketch, "E775", {"start": v(5.25, -0.5) * mm, "end": v(5.27, -0.5) * mm});
            skLineSegment(sketch, "E776", {"start": v(5.27, -0.5) * mm, "end": v(5.28, -0.5) * mm});
            skLineSegment(sketch, "E777", {"start": v(5.28, -0.5) * mm, "end": v(5.3, -0.49) * mm});
            skLineSegment(sketch, "E778", {"start": v(5.3, -0.49) * mm, "end": v(5.32, -0.48) * mm});
            skLineSegment(sketch, "E779", {"start": v(5.32, -0.48) * mm, "end": v(5.34, -0.48) * mm});
            skLineSegment(sketch, "E780", {"start": v(5.34, -0.48) * mm, "end": v(5.37, -0.47) * mm});
            skLineSegment(sketch, "E781", {"start": v(5.37, -0.47) * mm, "end": v(5.4, -0.46) * mm});
            skLineSegment(sketch, "E782", {"start": v(5.4, -0.46) * mm, "end": v(5.42, -0.45) * mm});
            skLineSegment(sketch, "E783", {"start": v(5.42, -0.45) * mm, "end": v(5.46, -0.45) * mm});
            skLineSegment(sketch, "E784", {"start": v(5.46, -0.45) * mm, "end": v(5.49, -0.44) * mm});
            skLineSegment(sketch, "E785", {"start": v(5.49, -0.44) * mm, "end": v(5.52, -0.43) * mm});
            skLineSegment(sketch, "E786", {"start": v(5.52, -0.43) * mm, "end": v(5.55, -0.42) * mm});
            skLineSegment(sketch, "E787", {"start": v(5.55, -0.42) * mm, "end": v(5.57, -0.41) * mm});
            skLineSegment(sketch, "E788", {"start": v(5.57, -0.41) * mm, "end": v(5.6, -0.4) * mm});
            skLineSegment(sketch, "E789", {"start": v(5.6, -0.4) * mm, "end": v(5.63, -0.4) * mm});
            skLineSegment(sketch, "E790", {"start": v(5.63, -0.4) * mm, "end": v(5.65, -0.4) * mm});
            skLineSegment(sketch, "E791", {"start": v(5.65, -0.4) * mm, "end": v(5.67, -0.38) * mm});
            skLineSegment(sketch, "E792", {"start": v(5.67, -0.38) * mm, "end": v(5.7, -0.38) * mm});
            skLineSegment(sketch, "E793", {"start": v(5.7, -0.38) * mm, "end": v(5.71, -0.37) * mm});
            skLineSegment(sketch, "E794", {"start": v(5.71, -0.37) * mm, "end": v(5.73, -0.36) * mm});
            skLineSegment(sketch, "E795", {"start": v(5.73, -0.36) * mm, "end": v(5.75, -0.35) * mm});
            skLineSegment(sketch, "E796", {"start": v(5.75, -0.35) * mm, "end": v(5.77, -0.35) * mm});
            skLineSegment(sketch, "E797", {"start": v(5.77, -0.35) * mm, "end": v(5.78, -0.34) * mm});
            skLineSegment(sketch, "E798", {"start": v(5.78, -0.34) * mm, "end": v(5.81, -0.32) * mm});
            skLineSegment(sketch, "E799", {"start": v(5.81, -0.32) * mm, "end": v(5.84, -0.3) * mm});
            skLineSegment(sketch, "E800", {"start": v(5.84, -0.3) * mm, "end": v(5.87, -0.29) * mm});
            skLineSegment(sketch, "E801", {"start": v(5.87, -0.29) * mm, "end": v(5.9, -0.26) * mm});
            skLineSegment(sketch, "E802", {"start": v(5.9, -0.26) * mm, "end": v(5.92, -0.24) * mm});
            skLineSegment(sketch, "E803", {"start": v(5.92, -0.24) * mm, "end": v(5.95, -0.22) * mm});
            skLineSegment(sketch, "E804", {"start": v(5.95, -0.22) * mm, "end": v(5.97, -0.2) * mm});
            skLineSegment(sketch, "E805", {"start": v(5.97, -0.2) * mm, "end": v(5.98, -0.16) * mm});
            skLineSegment(sketch, "E806", {"start": v(5.98, -0.16) * mm, "end": v(6, -0.13) * mm});
            skLineSegment(sketch, "E807", {"start": v(6, -0.13) * mm, "end": v(6.01, -0.1) * mm});
            skLineSegment(sketch, "E808", {"start": v(6.01, -0.1) * mm, "end": v(6.03, -0.08) * mm});
            skLineSegment(sketch, "E809", {"start": v(6.03, -0.08) * mm, "end": v(6.04, -0.04) * mm});
            skLineSegment(sketch, "E810", {"start": v(6.04, -0.04) * mm, "end": v(6.04, -0.01) * mm});
            skLineSegment(sketch, "E811", {"start": v(6.04, -0.01) * mm, "end": v(6.05, 0.02) * mm});
            skLineSegment(sketch, "E812", {"start": v(6.05, 0.02) * mm, "end": v(6.05, 0.05) * mm});
            skLineSegment(sketch, "E813", {"start": v(6.05, 0.05) * mm, "end": v(6.05, 0.08) * mm});
            skLineSegment(sketch, "E814", {"start": v(6.05, 0.08) * mm, "end": v(6.05, 0.11) * mm});
            skLineSegment(sketch, "E815", {"start": v(6.05, 0.11) * mm, "end": v(6.05, 0.14) * mm});
            skLineSegment(sketch, "E816", {"start": v(6.05, 0.14) * mm, "end": v(6.05, 0.17) * mm});
            skLineSegment(sketch, "E817", {"start": v(6.05, 0.17) * mm, "end": v(6.04, 0.2) * mm});
            skLineSegment(sketch, "E818", {"start": v(6.04, 0.2) * mm, "end": v(6.03, 0.23) * mm});
            skLineSegment(sketch, "E819", {"start": v(6.03, 0.23) * mm, "end": v(6.02, 0.26) * mm});
            skLineSegment(sketch, "E820", {"start": v(6.02, 0.26) * mm, "end": v(6, 0.28) * mm});
            skLineSegment(sketch, "E821", {"start": v(6, 0.28) * mm, "end": v(6, 0.31) * mm});
            skLineSegment(sketch, "E822", {"start": v(6, 0.31) * mm, "end": v(5.98, 0.34) * mm});
            skLineSegment(sketch, "E823", {"start": v(5.98, 0.34) * mm, "end": v(5.97, 0.36) * mm});
            skLineSegment(sketch, "E824", {"start": v(5.97, 0.36) * mm, "end": v(5.95, 0.38) * mm});
            skLineSegment(sketch, "E825", {"start": v(5.95, 0.38) * mm, "end": v(5.93, 0.4) * mm});
            skLineSegment(sketch, "E826", {"start": v(5.93, 0.4) * mm, "end": v(5.91, 0.43) * mm});
            skLineSegment(sketch, "E827", {"start": v(5.91, 0.43) * mm, "end": v(5.9, 0.45) * mm});
            skLineSegment(sketch, "E828", {"start": v(5.9, 0.45) * mm, "end": v(5.87, 0.46) * mm});
            skLineSegment(sketch, "E829", {"start": v(5.87, 0.46) * mm, "end": v(5.85, 0.48) * mm});
            skLineSegment(sketch, "E830", {"start": v(5.85, 0.48) * mm, "end": v(5.83, 0.5) * mm});
            skLineSegment(sketch, "E831", {"start": v(5.83, 0.5) * mm, "end": v(5.8, 0.5) * mm});
            skLineSegment(sketch, "E832", {"start": v(5.8, 0.5) * mm, "end": v(5.78, 0.52) * mm});
            skLineSegment(sketch, "E833", {"start": v(5.78, 0.52) * mm, "end": v(5.76, 0.53) * mm});
            skLineSegment(sketch, "E834", {"start": v(5.76, 0.53) * mm, "end": v(5.74, 0.54) * mm});
            skLineSegment(sketch, "E835", {"start": v(5.74, 0.54) * mm, "end": v(5.71, 0.55) * mm});
            skLineSegment(sketch, "E836", {"start": v(5.71, 0.55) * mm, "end": v(5.69, 0.56) * mm});
            skLineSegment(sketch, "E837", {"start": v(5.69, 0.56) * mm, "end": v(5.66, 0.57) * mm});
            skLineSegment(sketch, "E838", {"start": v(5.66, 0.57) * mm, "end": v(5.63, 0.58) * mm});
            skLineSegment(sketch, "E839", {"start": v(5.63, 0.58) * mm, "end": v(5.6, 0.58) * mm});
            skLineSegment(sketch, "E840", {"start": v(5.6, 0.58) * mm, "end": v(5.57, 0.59) * mm});
            skLineSegment(sketch, "E841", {"start": v(5.57, 0.59) * mm, "end": v(5.54, 0.6) * mm});
            skLineSegment(sketch, "E842", {"start": v(5.54, 0.6) * mm, "end": v(5.51, 0.6) * mm});
            skLineSegment(sketch, "E843", {"start": v(5.51, 0.6) * mm, "end": v(5.48, 0.6) * mm});
            skLineSegment(sketch, "E844", {"start": v(5.48, 0.6) * mm, "end": v(5.45, 0.6) * mm});
            skLineSegment(sketch, "E845", {"start": v(5.45, 0.6) * mm, "end": v(5.42, 0.6) * mm});
            skLineSegment(sketch, "E846", {"start": v(5.42, 0.6) * mm, "end": v(5.37, 0.6) * mm});
            skLineSegment(sketch, "E847", {"start": v(5.37, 0.6) * mm, "end": v(5.33, 0.6) * mm});
            skLineSegment(sketch, "E848", {"start": v(5.33, 0.6) * mm, "end": v(5.29, 0.6) * mm});
            skLineSegment(sketch, "E849", {"start": v(5.29, 0.6) * mm, "end": v(5.24, 0.59) * mm});
            skLineSegment(sketch, "E850", {"start": v(5.24, 0.59) * mm, "end": v(5.2, 0.58) * mm});
            skLineSegment(sketch, "E851", {"start": v(5.2, 0.58) * mm, "end": v(5.16, 0.57) * mm});
            skLineSegment(sketch, "E852", {"start": v(5.16, 0.57) * mm, "end": v(5.12, 0.56) * mm});
            skLineSegment(sketch, "E853", {"start": v(5.12, 0.56) * mm, "end": v(5.08, 0.55) * mm});
            skLineSegment(sketch, "E854", {"start": v(5.08, 0.55) * mm, "end": v(5.05, 0.53) * mm});
            skLineSegment(sketch, "E855", {"start": v(5.05, 0.53) * mm, "end": v(5.01, 0.51) * mm});
            skLineSegment(sketch, "E856", {"start": v(5.01, 0.51) * mm, "end": v(4.98, 0.5) * mm});
            skLineSegment(sketch, "E857", {"start": v(4.98, 0.5) * mm, "end": v(4.95, 0.48) * mm});
            skLineSegment(sketch, "E858", {"start": v(4.95, 0.48) * mm, "end": v(4.92, 0.45) * mm});
            skLineSegment(sketch, "E859", {"start": v(4.92, 0.45) * mm, "end": v(4.9, 0.43) * mm});
            skLineSegment(sketch, "E860", {"start": v(4.9, 0.43) * mm, "end": v(4.87, 0.4) * mm});
            skLineSegment(sketch, "E861", {"start": v(4.87, 0.4) * mm, "end": v(4.85, 0.38) * mm});
            skLineSegment(sketch, "E862", {"start": v(4.85, 0.38) * mm, "end": v(4.83, 0.35) * mm});
            skLineSegment(sketch, "E863", {"start": v(4.83, 0.35) * mm, "end": v(4.81, 0.32) * mm});
            skLineSegment(sketch, "E864", {"start": v(4.81, 0.32) * mm, "end": v(4.8, 0.29) * mm});
            skLineSegment(sketch, "E865", {"start": v(4.8, 0.29) * mm, "end": v(4.78, 0.26) * mm});
            skLineSegment(sketch, "E866", {"start": v(4.78, 0.26) * mm, "end": v(4.77, 0.22) * mm});
            skLineSegment(sketch, "E867", {"start": v(4.77, 0.22) * mm, "end": v(4.76, 0.19) * mm});
            skLineSegment(sketch, "E868", {"start": v(4.76, 0.19) * mm, "end": v(4.75, 0.15) * mm});
            skLineSegment(sketch, "E869", {"start": v(4.75, 0.15) * mm, "end": v(4.73, 0.01) * mm});
            skLineSegment(sketch, "E870", {"start": v(4.73, 0.01) * mm, "end": v(5.17, -0.05) * mm});
            skLineSegment(sketch, "E871", {"start": v(5.17, -0.05) * mm, "end": v(5.19, 0.07) * mm});
            skLineSegment(sketch, "E872", {"start": v(5.19, 0.07) * mm, "end": v(5.2, 0.08) * mm});
            skLineSegment(sketch, "E873", {"start": v(5.2, 0.08) * mm, "end": v(5.2, 0.1) * mm});
            skLineSegment(sketch, "E874", {"start": v(5.2, 0.1) * mm, "end": v(5.2, 0.11) * mm});
            skLineSegment(sketch, "E875", {"start": v(5.2, 0.11) * mm, "end": v(5.21, 0.13) * mm});
            skLineSegment(sketch, "E876", {"start": v(5.21, 0.13) * mm, "end": v(5.22, 0.14) * mm});
            skLineSegment(sketch, "E877", {"start": v(5.22, 0.14) * mm, "end": v(5.23, 0.15) * mm});
            skLineSegment(sketch, "E878", {"start": v(5.23, 0.15) * mm, "end": v(5.24, 0.16) * mm});
            skLineSegment(sketch, "E879", {"start": v(5.24, 0.16) * mm, "end": v(5.25, 0.17) * mm});
            skLineSegment(sketch, "E880", {"start": v(5.25, 0.17) * mm, "end": v(5.27, 0.17) * mm});
            skLineSegment(sketch, "E881", {"start": v(5.27, 0.17) * mm, "end": v(5.28, 0.18) * mm});
            skLineSegment(sketch, "E882", {"start": v(5.28, 0.18) * mm, "end": v(5.3, 0.19) * mm});
            skLineSegment(sketch, "E883", {"start": v(5.3, 0.19) * mm, "end": v(5.32, 0.2) * mm});
            skLineSegment(sketch, "E884", {"start": v(5.32, 0.2) * mm, "end": v(5.35, 0.2) * mm});
            skLineSegment(sketch, "E885", {"start": v(5.35, 0.2) * mm, "end": v(5.37, 0.2) * mm});
            skLineSegment(sketch, "E886", {"start": v(5.37, 0.2) * mm, "end": v(5.4, 0.2) * mm});
            skLineSegment(sketch, "E887", {"start": v(5.4, 0.2) * mm, "end": v(5.42, 0.2) * mm});
            skLineSegment(sketch, "E888", {"start": v(5.42, 0.2) * mm, "end": v(5.44, 0.2) * mm});
            skLineSegment(sketch, "E889", {"start": v(5.44, 0.2) * mm, "end": v(5.45, 0.2) * mm});
            skLineSegment(sketch, "E890", {"start": v(5.45, 0.2) * mm, "end": v(5.47, 0.2) * mm});
            skLineSegment(sketch, "E891", {"start": v(5.47, 0.2) * mm, "end": v(5.49, 0.2) * mm});
            skLineSegment(sketch, "E892", {"start": v(5.49, 0.2) * mm, "end": v(5.5, 0.2) * mm});
            skLineSegment(sketch, "E893", {"start": v(5.5, 0.2) * mm, "end": v(5.51, 0.2) * mm});
            skLineSegment(sketch, "E894", {"start": v(5.51, 0.2) * mm, "end": v(5.52, 0.19) * mm});
            skLineSegment(sketch, "E895", {"start": v(5.52, 0.19) * mm, "end": v(5.53, 0.19) * mm});
            skLineSegment(sketch, "E896", {"start": v(5.53, 0.19) * mm, "end": v(5.54, 0.18) * mm});
            skLineSegment(sketch, "E897", {"start": v(5.54, 0.18) * mm, "end": v(5.55, 0.18) * mm});
            skLineSegment(sketch, "E898", {"start": v(5.55, 0.18) * mm, "end": v(5.56, 0.18) * mm});
            skLineSegment(sketch, "E899", {"start": v(5.56, 0.18) * mm, "end": v(5.57, 0.17) * mm});
            skLineSegment(sketch, "E900", {"start": v(5.57, 0.17) * mm, "end": v(5.57, 0.17) * mm});
            skLineSegment(sketch, "E901", {"start": v(5.57, 0.17) * mm, "end": v(5.58, 0.17) * mm});
            skLineSegment(sketch, "E902", {"start": v(5.58, 0.17) * mm, "end": v(5.58, 0.16) * mm});
            skLineSegment(sketch, "E903", {"start": v(5.58, 0.16) * mm, "end": v(5.6, 0.16) * mm});
            skLineSegment(sketch, "E904", {"start": v(5.6, 0.16) * mm, "end": v(5.6, 0.15) * mm});
            skLineSegment(sketch, "E905", {"start": v(5.6, 0.15) * mm, "end": v(5.6, 0.14) * mm});
            skLineSegment(sketch, "E906", {"start": v(5.6, 0.14) * mm, "end": v(5.6, 0.13) * mm});
            skLineSegment(sketch, "E907", {"start": v(5.6, 0.13) * mm, "end": v(5.61, 0.13) * mm});
            skLineSegment(sketch, "E908", {"start": v(5.61, 0.13) * mm, "end": v(5.61, 0.12) * mm});
            skLineSegment(sketch, "E909", {"start": v(5.61, 0.12) * mm, "end": v(5.61, 0.12) * mm});
            skLineSegment(sketch, "E910", {"start": v(5.61, 0.12) * mm, "end": v(5.62, 0.11) * mm});
            skLineSegment(sketch, "E911", {"start": v(5.62, 0.11) * mm, "end": v(5.62, 0.1) * mm});
            skLineSegment(sketch, "E912", {"start": v(5.62, 0.1) * mm, "end": v(5.61, 0.1) * mm});
            skLineSegment(sketch, "E913", {"start": v(5.61, 0.1) * mm, "end": v(5.61, 0.1) * mm});
            skLineSegment(sketch, "E914", {"start": v(5.61, 0.1) * mm, "end": v(5.6, 0.1) * mm});
            skLineSegment(sketch, "E915", {"start": v(5.6, 0.1) * mm, "end": v(5.6, 0.09) * mm});
            skLineSegment(sketch, "E916", {"start": v(5.6, 0.09) * mm, "end": v(5.6, 0.08) * mm});
            skLineSegment(sketch, "E917", {"start": v(5.6, 0.08) * mm, "end": v(5.6, 0.08) * mm});
            skLineSegment(sketch, "E918", {"start": v(5.6, 0.08) * mm, "end": v(5.59, 0.07) * mm});
            skLineSegment(sketch, "E919", {"start": v(5.59, 0.07) * mm, "end": v(5.58, 0.07) * mm});
            skLineSegment(sketch, "E920", {"start": v(5.58, 0.07) * mm, "end": v(5.57, 0.06) * mm});
            skLineSegment(sketch, "E921", {"start": v(5.57, 0.06) * mm, "end": v(5.56, 0.06) * mm});
            skLineSegment(sketch, "E922", {"start": v(5.56, 0.06) * mm, "end": v(5.55, 0.05) * mm});
            skLineSegment(sketch, "E923", {"start": v(5.55, 0.05) * mm, "end": v(5.55, 0.05) * mm});
            skLineSegment(sketch, "E924", {"start": v(5.55, 0.05) * mm, "end": v(5.54, 0.05) * mm});
            skLineSegment(sketch, "E925", {"start": v(5.54, 0.05) * mm, "end": v(5.53, 0.05) * mm});
            skLineSegment(sketch, "E926", {"start": v(5.53, 0.05) * mm, "end": v(5.53, 0.05) * mm});
            skLineSegment(sketch, "E927", {"start": v(5.53, 0.05) * mm, "end": v(5.52, 0.04) * mm});
            skLineSegment(sketch, "E928", {"start": v(5.52, 0.04) * mm, "end": v(5.5, 0.04) * mm});
            skLineSegment(sketch, "E929", {"start": v(5.5, 0.04) * mm, "end": v(5.5, 0.03) * mm});
            skLineSegment(sketch, "E930", {"start": v(5.5, 0.03) * mm, "end": v(5.48, 0.03) * mm});
            skLineSegment(sketch, "E931", {"start": v(5.48, 0.03) * mm, "end": v(5.46, 0.03) * mm});
            skLineSegment(sketch, "E932", {"start": v(5.46, 0.03) * mm, "end": v(5.45, 0.02) * mm});
            skLineSegment(sketch, "E933", {"start": v(5.45, 0.02) * mm, "end": v(5.43, 0.02) * mm});
            skLineSegment(sketch, "E934", {"start": v(5.43, 0.02) * mm, "end": v(5.41, 0.01) * mm});
            skLineSegment(sketch, "E935", {"start": v(5.41, 0.01) * mm, "end": v(5.4, 0) * mm});
            skLineSegment(sketch, "E936", {"start": v(5.4, 0) * mm, "end": v(5.37, 0) * mm});
            skLineSegment(sketch, "E937", {"start": v(5.37, 0) * mm, "end": v(5.35, 0) * mm});
            skLineSegment(sketch, "E938", {"start": v(5.35, 0) * mm, "end": v(5.32, -0.01) * mm});
            skLineSegment(sketch, "E939", {"start": v(5.32, -0.01) * mm, "end": v(5.29, -0.02) * mm});
            skLineSegment(sketch, "E940", {"start": v(5.29, -0.02) * mm, "end": v(5.26, -0.03) * mm});
            skLineSegment(sketch, "E941", {"start": v(5.26, -0.03) * mm, "end": v(5.23, -0.04) * mm});
            skLineSegment(sketch, "E942", {"start": v(5.23, -0.04) * mm, "end": v(5.2, -0.05) * mm});
            skLineSegment(sketch, "E943", {"start": v(5.2, -0.05) * mm, "end": v(5.17, -0.05) * mm});
            skLineSegment(sketch, "E944", {"start": v(5.17, -0.05) * mm, "end": v(5.15, -0.06) * mm});
            skLineSegment(sketch, "E945", {"start": v(5.15, -0.06) * mm, "end": v(5.12, -0.07) * mm});
            skLineSegment(sketch, "E946", {"start": v(5.12, -0.07) * mm, "end": v(5.1, -0.08) * mm});
            skLineSegment(sketch, "E947", {"start": v(5.1, -0.08) * mm, "end": v(5.08, -0.08) * mm});
            skLineSegment(sketch, "E948", {"start": v(5.08, -0.08) * mm, "end": v(5.06, -0.1) * mm});
            skLineSegment(sketch, "E949", {"start": v(5.06, -0.1) * mm, "end": v(5.04, -0.1) * mm});
            skLineSegment(sketch, "E950", {"start": v(5.04, -0.1) * mm, "end": v(5.02, -0.1) * mm});
            skLineSegment(sketch, "E951", {"start": v(5.02, -0.1) * mm, "end": v(5, -0.11) * mm});
            skLineSegment(sketch, "E952", {"start": v(5, -0.11) * mm, "end": v(4.99, -0.12) * mm});
            skLineSegment(sketch, "E953", {"start": v(4.99, -0.12) * mm, "end": v(4.97, -0.12) * mm});
            skLineSegment(sketch, "E954", {"start": v(4.97, -0.12) * mm, "end": v(4.94, -0.14) * mm});
            skLineSegment(sketch, "E955", {"start": v(4.94, -0.14) * mm, "end": v(4.91, -0.15) * mm});
            skLineSegment(sketch, "E956", {"start": v(4.91, -0.15) * mm, "end": v(4.88, -0.17) * mm});
            skLineSegment(sketch, "E957", {"start": v(4.88, -0.17) * mm, "end": v(4.86, -0.2) * mm});
            skLineSegment(sketch, "E958", {"start": v(4.86, -0.2) * mm, "end": v(4.83, -0.21) * mm});
            skLineSegment(sketch, "E959", {"start": v(4.83, -0.21) * mm, "end": v(4.8, -0.24) * mm});
            skLineSegment(sketch, "E960", {"start": v(4.8, -0.24) * mm, "end": v(4.79, -0.26) * mm});
            skLineSegment(sketch, "E961", {"start": v(4.79, -0.26) * mm, "end": v(4.77, -0.29) * mm});
            skLineSegment(sketch, "E962", {"start": v(4.77, -0.29) * mm, "end": v(4.75, -0.32) * mm});
            skLineSegment(sketch, "E963", {"start": v(4.75, -0.32) * mm, "end": v(4.73, -0.35) * mm});
            skLineSegment(sketch, "E964", {"start": v(4.73, -0.35) * mm, "end": v(4.72, -0.38) * mm});
            skLineSegment(sketch, "E965", {"start": v(4.72, -0.38) * mm, "end": v(4.7, -0.41) * mm});
            skLineSegment(sketch, "E966", {"start": v(4.7, -0.41) * mm, "end": v(4.7, -0.45) * mm});
            skLineSegment(sketch, "E967", {"start": v(4.7, -0.45) * mm, "end": v(4.7, -0.48) * mm});
            skLineSegment(sketch, "E968", {"start": v(4.7, -0.48) * mm, "end": v(4.7, -0.52) * mm});
            skLineSegment(sketch, "E969", {"start": v(4.7, -0.52) * mm, "end": v(4.7, -0.55) * mm});
            skLineSegment(sketch, "E970", {"start": v(4.7, -0.55) * mm, "end": v(4.7, -0.6) * mm});
            skLineSegment(sketch, "E971", {"start": v(4.7, -0.6) * mm, "end": v(4.7, -0.63) * mm});
            skLineSegment(sketch, "E972", {"start": v(4.7, -0.63) * mm, "end": v(4.7, -0.67) * mm});
            skLineSegment(sketch, "E973", {"start": v(4.7, -0.67) * mm, "end": v(4.71, -0.7) * mm});
            skLineSegment(sketch, "E974", {"start": v(4.71, -0.7) * mm, "end": v(4.73, -0.74) * mm});
            skLineSegment(sketch, "E975", {"start": v(4.73, -0.74) * mm, "end": v(4.74, -0.77) * mm});
            skLineSegment(sketch, "E976", {"start": v(4.74, -0.77) * mm, "end": v(4.76, -0.8) * mm});
            skLineSegment(sketch, "E977", {"start": v(4.76, -0.8) * mm, "end": v(4.78, -0.84) * mm});
            skLineSegment(sketch, "E978", {"start": v(4.78, -0.84) * mm, "end": v(4.8, -0.87) * mm});
            skLineSegment(sketch, "E979", {"start": v(4.8, -0.87) * mm, "end": v(4.83, -0.9) * mm});
            skLineSegment(sketch, "E980", {"start": v(4.83, -0.9) * mm, "end": v(4.86, -0.93) * mm});
            skLineSegment(sketch, "E981", {"start": v(4.86, -0.93) * mm, "end": v(4.89, -0.96) * mm});
            skLineSegment(sketch, "E982", {"start": v(4.89, -0.96) * mm, "end": v(4.92, -0.98) * mm});
            skLineSegment(sketch, "E983", {"start": v(4.92, -0.98) * mm, "end": v(4.95, -1) * mm});
            skLineSegment(sketch, "E984", {"start": v(4.95, -1) * mm, "end": v(5, -1.03) * mm});
            skLineSegment(sketch, "E985", {"start": v(5, -1.03) * mm, "end": v(5.03, -1.04) * mm});
            skLineSegment(sketch, "E986", {"start": v(5.03, -1.04) * mm, "end": v(5.07, -1.06) * mm});
            skLineSegment(sketch, "E987", {"start": v(5.07, -1.06) * mm, "end": v(5.1, -1.07) * mm});
            skLineSegment(sketch, "E988", {"start": v(5.1, -1.07) * mm, "end": v(5.15, -1.09) * mm});
            skLineSegment(sketch, "E989", {"start": v(5.15, -1.09) * mm, "end": v(5.2, -1.1) * mm});
            skLineSegment(sketch, "E990", {"start": v(5.2, -1.1) * mm, "end": v(5.24, -1.1) * mm});
            skLineSegment(sketch, "E991", {"start": v(5.24, -1.1) * mm, "end": v(5.28, -1.1) * mm});
            skLineSegment(sketch, "E992", {"start": v(5.28, -1.1) * mm, "end": v(5.33, -1.11) * mm});
            skLineSegment(sketch, "E993", {"start": v(5.33, -1.11) * mm, "end": v(5.37, -1.11) * mm});
            skLineSegment(sketch, "E994", {"start": v(5.37, -1.11) * mm, "end": v(5.41, -1.11) * mm});
            skLineSegment(sketch, "E995", {"start": v(5.41, -1.11) * mm, "end": v(5.45, -1.11) * mm});
            skLineSegment(sketch, "E996", {"start": v(5.45, -1.11) * mm, "end": v(5.48, -1.1) * mm});
            skLineSegment(sketch, "E997", {"start": v(5.48, -1.1) * mm, "end": v(5.52, -1.1) * mm});
            skLineSegment(sketch, "E998", {"start": v(5.52, -1.1) * mm, "end": v(5.55, -1.1) * mm});
            skLineSegment(sketch, "E999", {"start": v(5.55, -1.1) * mm, "end": v(5.59, -1.1) * mm});
            skLineSegment(sketch, "E1000", {"start": v(5.59, -1.1) * mm, "end": v(5.62, -1.09) * mm});
            skLineSegment(sketch, "E1001", {"start": v(5.62, -1.09) * mm, "end": v(5.65, -1.08) * mm});
            skLineSegment(sketch, "E1002", {"start": v(5.65, -1.08) * mm, "end": v(5.68, -1.07) * mm});
            skLineSegment(sketch, "E1003", {"start": v(5.68, -1.07) * mm, "end": v(5.7, -1.06) * mm});
            skLineSegment(sketch, "E1004", {"start": v(5.7, -1.06) * mm, "end": v(5.74, -1.05) * mm});
            skLineSegment(sketch, "E1005", {"start": v(5.74, -1.05) * mm, "end": v(5.77, -1.04) * mm});
            skLineSegment(sketch, "E1006", {"start": v(5.77, -1.04) * mm, "end": v(5.8, -1.02) * mm});
            skLineSegment(sketch, "E1007", {"start": v(5.8, -1.02) * mm, "end": v(5.82, -1) * mm});
            skLineSegment(sketch, "E1008", {"start": v(5.82, -1) * mm, "end": v(5.84, -1) * mm});
            skLineSegment(sketch, "E1009", {"start": v(5.84, -1) * mm, "end": v(5.87, -0.97) * mm});
            skLineSegment(sketch, "E1010", {"start": v(5.87, -0.97) * mm, "end": v(5.89, -0.96) * mm});
            skLineSegment(sketch, "E1011", {"start": v(5.89, -0.96) * mm, "end": v(5.91, -0.94) * mm});
            skLineSegment(sketch, "E1012", {"start": v(5.91, -0.94) * mm, "end": v(5.93, -0.92) * mm});
            skLineSegment(sketch, "E1013", {"start": v(5.93, -0.92) * mm, "end": v(5.95, -0.9) * mm});
            skLineSegment(sketch, "E1014", {"start": v(5.95, -0.9) * mm, "end": v(5.97, -0.87) * mm});
            skLineSegment(sketch, "E1015", {"start": v(5.97, -0.87) * mm, "end": v(5.98, -0.85) * mm});
            skLineSegment(sketch, "E1016", {"start": v(5.98, -0.85) * mm, "end": v(6, -0.82) * mm});
            skLineSegment(sketch, "E1017", {"start": v(6, -0.82) * mm, "end": v(6.01, -0.8) * mm});
            skLineSegment(sketch, "E1018", {"start": v(6.01, -0.8) * mm, "end": v(6.03, -0.77) * mm});
            skLineSegment(sketch, "E1019", {"start": v(6.03, -0.77) * mm, "end": v(6.04, -0.74) * mm});
            skLineSegment(sketch, "E1020", {"start": v(6.04, -0.74) * mm, "end": v(6.05, -0.72) * mm});
            skLineSegment(sketch, "E1021", {"start": v(6.05, -0.72) * mm, "end": v(6.06, -0.69) * mm});
            skLineSegment(sketch, "E1022", {"start": v(6.06, -0.69) * mm, "end": v(6.07, -0.66) * mm});
            skLineSegment(sketch, "E1023", {"start": v(6.07, -0.66) * mm, "end": v(6.08, -0.63) * mm});
            skLineSegment(sketch, "E1024", {"start": v(6.08, -0.63) * mm, "end": v(6.09, -0.6) * mm});
            skLineSegment(sketch, "E1025", {"start": v(6.09, -0.6) * mm, "end": v(6.11, -0.46) * mm});
            skLineSegment(sketch, "E1026", {"start": v(1.42, -1.46) * mm, "end": v(1.44, -1.48) * mm});
            skLineSegment(sketch, "E1027", {"start": v(1.44, -1.48) * mm, "end": v(1.46, -1.5) * mm});
            skLineSegment(sketch, "E1028", {"start": v(1.46, -1.5) * mm, "end": v(1.48, -1.52) * mm});
            skLineSegment(sketch, "E1029", {"start": v(1.48, -1.52) * mm, "end": v(1.5, -1.53) * mm});
            skLineSegment(sketch, "E1030", {"start": v(1.5, -1.53) * mm, "end": v(1.52, -1.55) * mm});
            skLineSegment(sketch, "E1031", {"start": v(1.52, -1.55) * mm, "end": v(1.54, -1.57) * mm});
            skLineSegment(sketch, "E1032", {"start": v(1.54, -1.57) * mm, "end": v(1.56, -1.59) * mm});
            skLineSegment(sketch, "E1033", {"start": v(1.56, -1.59) * mm, "end": v(1.58, -1.6) * mm});
            skLineSegment(sketch, "E1034", {"start": v(1.58, -1.6) * mm, "end": v(1.6, -1.62) * mm});
            skLineSegment(sketch, "E1035", {"start": v(1.6, -1.62) * mm, "end": v(1.62, -1.63) * mm});
            skLineSegment(sketch, "E1036", {"start": v(1.62, -1.63) * mm, "end": v(1.64, -1.65) * mm});
            skLineSegment(sketch, "E1037", {"start": v(1.64, -1.65) * mm, "end": v(1.66, -1.67) * mm});
            skLineSegment(sketch, "E1038", {"start": v(1.66, -1.67) * mm, "end": v(1.69, -1.68) * mm});
            skLineSegment(sketch, "E1039", {"start": v(1.69, -1.68) * mm, "end": v(1.7, -1.7) * mm});
            skLineSegment(sketch, "E1040", {"start": v(1.7, -1.7) * mm, "end": v(1.73, -1.71) * mm});
            skLineSegment(sketch, "E1041", {"start": v(1.73, -1.71) * mm, "end": v(1.75, -1.73) * mm});
            skLineSegment(sketch, "E1042", {"start": v(1.75, -1.73) * mm, "end": v(1.77, -1.74) * mm});
            skLineSegment(sketch, "E1043", {"start": v(1.77, -1.74) * mm, "end": v(1.79, -1.75) * mm});
            skLineSegment(sketch, "E1044", {"start": v(1.79, -1.75) * mm, "end": v(1.8, -1.77) * mm});
            skLineSegment(sketch, "E1045", {"start": v(1.8, -1.77) * mm, "end": v(1.83, -1.78) * mm});
            skLineSegment(sketch, "E1046", {"start": v(1.83, -1.78) * mm, "end": v(1.85, -1.8) * mm});
            skLineSegment(sketch, "E1047", {"start": v(1.85, -1.8) * mm, "end": v(1.87, -1.8) * mm});
            skLineSegment(sketch, "E1048", {"start": v(1.87, -1.8) * mm, "end": v(1.9, -1.82) * mm});
            skLineSegment(sketch, "E1049", {"start": v(1.9, -1.82) * mm, "end": v(1.91, -1.83) * mm});
            skLineSegment(sketch, "E1050", {"start": v(1.91, -1.83) * mm, "end": v(1.93, -1.85) * mm});
            skLineSegment(sketch, "E1051", {"start": v(1.93, -1.85) * mm, "end": v(1.95, -1.86) * mm});
            skLineSegment(sketch, "E1052", {"start": v(1.95, -1.86) * mm, "end": v(1.97, -1.87) * mm});
            skLineSegment(sketch, "E1053", {"start": v(1.97, -1.87) * mm, "end": v(2, -1.88) * mm});
            skLineSegment(sketch, "E1054", {"start": v(2, -1.88) * mm, "end": v(2.02, -1.9) * mm});
            skLineSegment(sketch, "E1055", {"start": v(2.02, -1.9) * mm, "end": v(2.04, -1.9) * mm});
            skLineSegment(sketch, "E1056", {"start": v(2.04, -1.9) * mm, "end": v(2.06, -1.91) * mm});
            skLineSegment(sketch, "E1057", {"start": v(2.06, -1.91) * mm, "end": v(2.08, -1.93) * mm});
            skLineSegment(sketch, "E1058", {"start": v(2.08, -1.93) * mm, "end": v(2.1, -1.94) * mm});
            skLineSegment(sketch, "E1059", {"start": v(2.1, -1.94) * mm, "end": v(2.12, -1.95) * mm});
            skLineSegment(sketch, "E1060", {"start": v(2.12, -1.95) * mm, "end": v(2.14, -1.96) * mm});
            skLineSegment(sketch, "E1061", {"start": v(2.14, -1.96) * mm, "end": v(2.16, -1.97) * mm});
            skLineSegment(sketch, "E1062", {"start": v(2.16, -1.97) * mm, "end": v(2.18, -1.98) * mm});
            skLineSegment(sketch, "E1063", {"start": v(2.18, -1.98) * mm, "end": v(2.2, -1.98) * mm});
            skLineSegment(sketch, "E1064", {"start": v(2.2, -1.98) * mm, "end": v(2.23, -2) * mm});
            skLineSegment(sketch, "E1065", {"start": v(2.23, -2) * mm, "end": v(2.25, -2) * mm});
            skLineSegment(sketch, "E1066", {"start": v(2.25, -2) * mm, "end": v(2.27, -2.01) * mm});
            skLineSegment(sketch, "E1067", {"start": v(2.27, -2.01) * mm, "end": v(2.29, -2.02) * mm});
            skLineSegment(sketch, "E1068", {"start": v(2.29, -2.02) * mm, "end": v(2.3, -2.03) * mm});
            skLineSegment(sketch, "E1069", {"start": v(2.3, -2.03) * mm, "end": v(2.33, -2.03) * mm});
            skLineSegment(sketch, "E1070", {"start": v(2.33, -2.03) * mm, "end": v(2.35, -2.04) * mm});
            skLineSegment(sketch, "E1071", {"start": v(2.35, -2.04) * mm, "end": v(2.37, -2.05) * mm});
            skLineSegment(sketch, "E1072", {"start": v(2.37, -2.05) * mm, "end": v(2.4, -2.06) * mm});
            skLineSegment(sketch, "E1073", {"start": v(2.4, -2.06) * mm, "end": v(2.42, -2.06) * mm});
            skLineSegment(sketch, "E1074", {"start": v(2.42, -2.06) * mm, "end": v(2.44, -2.07) * mm});
            skLineSegment(sketch, "E1075", {"start": v(2.44, -2.07) * mm, "end": v(2.46, -2.07) * mm});
            skLineSegment(sketch, "E1076", {"start": v(2.46, -2.07) * mm, "end": v(2.48, -2.08) * mm});
            skLineSegment(sketch, "E1077", {"start": v(2.48, -2.08) * mm, "end": v(2.5, -2.08) * mm});
            skLineSegment(sketch, "E1078", {"start": v(2.5, -2.08) * mm, "end": v(2.53, -2.09) * mm});
            skLineSegment(sketch, "E1079", {"start": v(2.53, -2.09) * mm, "end": v(2.55, -2.1) * mm});
            skLineSegment(sketch, "E1080", {"start": v(2.55, -2.1) * mm, "end": v(2.57, -2.1) * mm});
            skLineSegment(sketch, "E1081", {"start": v(2.57, -2.1) * mm, "end": v(2.6, -2.1) * mm});
            skLineSegment(sketch, "E1082", {"start": v(2.6, -2.1) * mm, "end": v(2.63, -2.1) * mm});
            skLineSegment(sketch, "E1083", {"start": v(2.63, -2.1) * mm, "end": v(2.66, -2.1) * mm});
            skLineSegment(sketch, "E1084", {"start": v(2.66, -2.1) * mm, "end": v(2.68, -2.09) * mm});
            skLineSegment(sketch, "E1085", {"start": v(2.68, -2.09) * mm, "end": v(2.7, -2.08) * mm});
            skLineSegment(sketch, "E1086", {"start": v(2.7, -2.08) * mm, "end": v(2.73, -2.08) * mm});
            skLineSegment(sketch, "E1087", {"start": v(2.73, -2.08) * mm, "end": v(2.75, -2.07) * mm});
            skLineSegment(sketch, "E1088", {"start": v(2.75, -2.07) * mm, "end": v(2.77, -2.07) * mm});
            skLineSegment(sketch, "E1089", {"start": v(2.77, -2.07) * mm, "end": v(2.8, -2.06) * mm});
            skLineSegment(sketch, "E1090", {"start": v(2.8, -2.06) * mm, "end": v(2.81, -2.06) * mm});
            skLineSegment(sketch, "E1091", {"start": v(2.81, -2.06) * mm, "end": v(2.83, -2.05) * mm});
            skLineSegment(sketch, "E1092", {"start": v(2.83, -2.05) * mm, "end": v(2.86, -2.04) * mm});
            skLineSegment(sketch, "E1093", {"start": v(2.86, -2.04) * mm, "end": v(2.88, -2.03) * mm});
            skLineSegment(sketch, "E1094", {"start": v(2.88, -2.03) * mm, "end": v(2.9, -2.03) * mm});
            skLineSegment(sketch, "E1095", {"start": v(2.9, -2.03) * mm, "end": v(2.92, -2.02) * mm});
            skLineSegment(sketch, "E1096", {"start": v(2.92, -2.02) * mm, "end": v(2.94, -2.01) * mm});
            skLineSegment(sketch, "E1097", {"start": v(2.94, -2.01) * mm, "end": v(2.96, -2) * mm});
            skLineSegment(sketch, "E1098", {"start": v(2.96, -2) * mm, "end": v(2.98, -2) * mm});
            skLineSegment(sketch, "E1099", {"start": v(2.98, -2) * mm, "end": v(3, -1.98) * mm});
            skLineSegment(sketch, "E1100", {"start": v(3, -1.98) * mm, "end": v(3.03, -1.98) * mm});
            skLineSegment(sketch, "E1101", {"start": v(3.03, -1.98) * mm, "end": v(3.05, -1.97) * mm});
            skLineSegment(sketch, "E1102", {"start": v(3.05, -1.97) * mm, "end": v(3.07, -1.96) * mm});
            skLineSegment(sketch, "E1103", {"start": v(3.07, -1.96) * mm, "end": v(3.09, -1.95) * mm});
            skLineSegment(sketch, "E1104", {"start": v(3.09, -1.95) * mm, "end": v(3.1, -1.94) * mm});
            skLineSegment(sketch, "E1105", {"start": v(3.1, -1.94) * mm, "end": v(3.13, -1.93) * mm});
            skLineSegment(sketch, "E1106", {"start": v(3.13, -1.93) * mm, "end": v(3.15, -1.91) * mm});
            skLineSegment(sketch, "E1107", {"start": v(3.15, -1.91) * mm, "end": v(3.17, -1.9) * mm});
            skLineSegment(sketch, "E1108", {"start": v(3.17, -1.9) * mm, "end": v(3.2, -1.9) * mm});
            skLineSegment(sketch, "E1109", {"start": v(3.2, -1.9) * mm, "end": v(3.21, -1.88) * mm});
            skLineSegment(sketch, "E1110", {"start": v(3.21, -1.88) * mm, "end": v(3.23, -1.87) * mm});
            skLineSegment(sketch, "E1111", {"start": v(3.23, -1.87) * mm, "end": v(3.25, -1.86) * mm});
            skLineSegment(sketch, "E1112", {"start": v(3.25, -1.86) * mm, "end": v(3.28, -1.85) * mm});
            skLineSegment(sketch, "E1113", {"start": v(3.28, -1.85) * mm, "end": v(3.3, -1.83) * mm});
            skLineSegment(sketch, "E1114", {"start": v(3.3, -1.83) * mm, "end": v(3.32, -1.82) * mm});
            skLineSegment(sketch, "E1115", {"start": v(3.32, -1.82) * mm, "end": v(3.34, -1.8) * mm});
            skLineSegment(sketch, "E1116", {"start": v(3.34, -1.8) * mm, "end": v(3.36, -1.8) * mm});
            skLineSegment(sketch, "E1117", {"start": v(3.36, -1.8) * mm, "end": v(3.38, -1.78) * mm});
            skLineSegment(sketch, "E1118", {"start": v(3.38, -1.78) * mm, "end": v(3.4, -1.77) * mm});
            skLineSegment(sketch, "E1119", {"start": v(3.4, -1.77) * mm, "end": v(3.42, -1.75) * mm});
            skLineSegment(sketch, "E1120", {"start": v(3.42, -1.75) * mm, "end": v(3.44, -1.74) * mm});
            skLineSegment(sketch, "E1121", {"start": v(3.44, -1.74) * mm, "end": v(3.46, -1.73) * mm});
            skLineSegment(sketch, "E1122", {"start": v(3.46, -1.73) * mm, "end": v(3.48, -1.71) * mm});
            skLineSegment(sketch, "E1123", {"start": v(3.48, -1.71) * mm, "end": v(3.5, -1.7) * mm});
            skLineSegment(sketch, "E1124", {"start": v(3.5, -1.7) * mm, "end": v(3.52, -1.68) * mm});
            skLineSegment(sketch, "E1125", {"start": v(3.52, -1.68) * mm, "end": v(3.54, -1.67) * mm});
            skLineSegment(sketch, "E1126", {"start": v(3.54, -1.67) * mm, "end": v(3.56, -1.65) * mm});
            skLineSegment(sketch, "E1127", {"start": v(3.56, -1.65) * mm, "end": v(3.59, -1.63) * mm});
            skLineSegment(sketch, "E1128", {"start": v(3.59, -1.63) * mm, "end": v(3.6, -1.62) * mm});
            skLineSegment(sketch, "E1129", {"start": v(3.6, -1.62) * mm, "end": v(3.63, -1.6) * mm});
            skLineSegment(sketch, "E1130", {"start": v(3.63, -1.6) * mm, "end": v(3.65, -1.59) * mm});
            skLineSegment(sketch, "E1131", {"start": v(3.65, -1.59) * mm, "end": v(3.67, -1.57) * mm});
            skLineSegment(sketch, "E1132", {"start": v(3.67, -1.57) * mm, "end": v(3.69, -1.55) * mm});
            skLineSegment(sketch, "E1133", {"start": v(3.69, -1.55) * mm, "end": v(3.7, -1.53) * mm});
            skLineSegment(sketch, "E1134", {"start": v(3.7, -1.53) * mm, "end": v(3.73, -1.52) * mm});
            skLineSegment(sketch, "E1135", {"start": v(3.73, -1.52) * mm, "end": v(3.75, -1.5) * mm});
            skLineSegment(sketch, "E1136", {"start": v(3.75, -1.5) * mm, "end": v(3.77, -1.48) * mm});
            skLineSegment(sketch, "E1137", {"start": v(3.77, -1.48) * mm, "end": v(3.8, -1.46) * mm});
            skLineSegment(sketch, "E1138", {"start": v(3.8, -1.46) * mm, "end": v(3.81, -1.44) * mm});
            skLineSegment(sketch, "E1139", {"start": v(3.81, -1.44) * mm, "end": v(3.83, -1.43) * mm});
            skLineSegment(sketch, "E1140", {"start": v(3.83, -1.43) * mm, "end": v(3.85, -1.4) * mm});
            skLineSegment(sketch, "E1141", {"start": v(3.85, -1.4) * mm, "end": v(3.87, -1.39) * mm});
            skLineSegment(sketch, "E1142", {"start": v(3.87, -1.39) * mm, "end": v(3.9, -1.37) * mm});
            skLineSegment(sketch, "E1143", {"start": v(3.9, -1.37) * mm, "end": v(3.91, -1.35) * mm});
            skLineSegment(sketch, "E1144", {"start": v(3.91, -1.35) * mm, "end": v(3.93, -1.33) * mm});
            skLineSegment(sketch, "E1145", {"start": v(3.93, -1.33) * mm, "end": v(3.96, -1.3) * mm});
            skLineSegment(sketch, "E1146", {"start": v(3.96, -1.3) * mm, "end": v(3.98, -1.29) * mm});
            skLineSegment(sketch, "E1147", {"start": v(3.98, -1.29) * mm, "end": v(4, -1.27) * mm});
            skLineSegment(sketch, "E1148", {"start": v(4, -1.27) * mm, "end": v(4.01, -1.24) * mm});
            skLineSegment(sketch, "E1149", {"start": v(4.01, -1.24) * mm, "end": v(4.03, -1.22) * mm});
            skLineSegment(sketch, "E1150", {"start": v(4.03, -1.22) * mm, "end": v(4.05, -1.2) * mm});
            skLineSegment(sketch, "E1151", {"start": v(4.05, -1.2) * mm, "end": v(4.07, -1.18) * mm});
            skLineSegment(sketch, "E1152", {"start": v(4.07, -1.18) * mm, "end": v(4.09, -1.16) * mm});
            skLineSegment(sketch, "E1153", {"start": v(4.09, -1.16) * mm, "end": v(4.1, -1.14) * mm});
            skLineSegment(sketch, "E1154", {"start": v(4.1, -1.14) * mm, "end": v(4.13, -1.12) * mm});
            skLineSegment(sketch, "E1155", {"start": v(4.13, -1.12) * mm, "end": v(4.14, -1.1) * mm});
            skLineSegment(sketch, "E1156", {"start": v(4.14, -1.1) * mm, "end": v(4.16, -1.08) * mm});
            skLineSegment(sketch, "E1157", {"start": v(4.16, -1.08) * mm, "end": v(4.18, -1.06) * mm});
            skLineSegment(sketch, "E1158", {"start": v(4.18, -1.06) * mm, "end": v(4.2, -1.04) * mm});
            skLineSegment(sketch, "E1159", {"start": v(4.2, -1.04) * mm, "end": v(4.21, -1.02) * mm});
            skLineSegment(sketch, "E1160", {"start": v(4.21, -1.02) * mm, "end": v(4.23, -1) * mm});
            skLineSegment(sketch, "E1161", {"start": v(4.23, -1) * mm, "end": v(4.24, -0.98) * mm});
            skLineSegment(sketch, "E1162", {"start": v(4.24, -0.98) * mm, "end": v(4.26, -0.96) * mm});
            skLineSegment(sketch, "E1163", {"start": v(4.26, -0.96) * mm, "end": v(4.27, -0.94) * mm});
            skLineSegment(sketch, "E1164", {"start": v(4.27, -0.94) * mm, "end": v(4.29, -0.92) * mm});
            skLineSegment(sketch, "E1165", {"start": v(4.29, -0.92) * mm, "end": v(4.3, -0.9) * mm});
            skLineSegment(sketch, "E1166", {"start": v(4.3, -0.9) * mm, "end": v(4.32, -0.87) * mm});
            skLineSegment(sketch, "E1167", {"start": v(4.32, -0.87) * mm, "end": v(4.33, -0.85) * mm});
            skLineSegment(sketch, "E1168", {"start": v(4.33, -0.85) * mm, "end": v(4.35, -0.83) * mm});
            skLineSegment(sketch, "E1169", {"start": v(4.35, -0.83) * mm, "end": v(4.36, -0.81) * mm});
            skLineSegment(sketch, "E1170", {"start": v(4.36, -0.81) * mm, "end": v(4.37, -0.8) * mm});
            skLineSegment(sketch, "E1171", {"start": v(4.37, -0.8) * mm, "end": v(4.39, -0.77) * mm});
            skLineSegment(sketch, "E1172", {"start": v(4.39, -0.77) * mm, "end": v(4.4, -0.75) * mm});
            skLineSegment(sketch, "E1173", {"start": v(4.4, -0.75) * mm, "end": v(4.41, -0.73) * mm});
            skLineSegment(sketch, "E1174", {"start": v(4.41, -0.73) * mm, "end": v(4.43, -0.7) * mm});
            skLineSegment(sketch, "E1175", {"start": v(4.43, -0.7) * mm, "end": v(4.44, -0.69) * mm});
            skLineSegment(sketch, "E1176", {"start": v(4.44, -0.69) * mm, "end": v(4.45, -0.67) * mm});
            skLineSegment(sketch, "E1177", {"start": v(4.45, -0.67) * mm, "end": v(4.47, -0.65) * mm});
            skLineSegment(sketch, "E1178", {"start": v(4.47, -0.65) * mm, "end": v(4.48, -0.63) * mm});
            skLineSegment(sketch, "E1179", {"start": v(4.48, -0.63) * mm, "end": v(4.49, -0.6) * mm});
            skLineSegment(sketch, "E1180", {"start": v(4.49, -0.6) * mm, "end": v(4.5, -0.58) * mm});
            skLineSegment(sketch, "E1181", {"start": v(4.5, -0.58) * mm, "end": v(4.51, -0.56) * mm});
            skLineSegment(sketch, "E1182", {"start": v(4.51, -0.56) * mm, "end": v(4.52, -0.54) * mm});
            skLineSegment(sketch, "E1183", {"start": v(4.52, -0.54) * mm, "end": v(4.53, -0.52) * mm});
            skLineSegment(sketch, "E1184", {"start": v(4.53, -0.52) * mm, "end": v(4.54, -0.5) * mm});
            skLineSegment(sketch, "E1185", {"start": v(4.54, -0.5) * mm, "end": v(4.55, -0.48) * mm});
            skLineSegment(sketch, "E1186", {"start": v(4.55, -0.48) * mm, "end": v(4.56, -0.46) * mm});
            skLineSegment(sketch, "E1187", {"start": v(4.56, -0.46) * mm, "end": v(4.57, -0.44) * mm});
            skLineSegment(sketch, "E1188", {"start": v(4.57, -0.44) * mm, "end": v(4.58, -0.42) * mm});
            skLineSegment(sketch, "E1189", {"start": v(4.58, -0.42) * mm, "end": v(4.6, -0.4) * mm});
            skLineSegment(sketch, "E1190", {"start": v(4.6, -0.4) * mm, "end": v(4.6, -0.38) * mm});
            skLineSegment(sketch, "E1191", {"start": v(4.6, -0.38) * mm, "end": v(4.61, -0.35) * mm});
            skLineSegment(sketch, "E1192", {"start": v(4.61, -0.35) * mm, "end": v(4.62, -0.33) * mm});
            skLineSegment(sketch, "E1193", {"start": v(4.62, -0.33) * mm, "end": v(4.63, -0.31) * mm});
            skLineSegment(sketch, "E1194", {"start": v(4.63, -0.31) * mm, "end": v(4.64, -0.3) * mm});
            skLineSegment(sketch, "E1195", {"start": v(4.64, -0.3) * mm, "end": v(4.64, -0.27) * mm});
            skLineSegment(sketch, "E1196", {"start": v(4.64, -0.27) * mm, "end": v(4.65, -0.25) * mm});
            skLineSegment(sketch, "E1197", {"start": v(4.65, -0.25) * mm, "end": v(4.66, -0.23) * mm});
            skLineSegment(sketch, "E1198", {"start": v(4.66, -0.23) * mm, "end": v(4.66, -0.2) * mm});
            skLineSegment(sketch, "E1199", {"start": v(4.66, -0.2) * mm, "end": v(4.67, -0.18) * mm});
            skLineSegment(sketch, "E1200", {"start": v(4.67, -0.18) * mm, "end": v(4.68, -0.16) * mm});
            skLineSegment(sketch, "E1201", {"start": v(4.68, -0.16) * mm, "end": v(4.68, -0.14) * mm});
            skLineSegment(sketch, "E1202", {"start": v(4.68, -0.14) * mm, "end": v(4.69, -0.12) * mm});
            skLineSegment(sketch, "E1203", {"start": v(4.69, -0.12) * mm, "end": v(4.7, -0.1) * mm});
            skLineSegment(sketch, "E1204", {"start": v(4.7, -0.1) * mm, "end": v(4.7, -0.07) * mm});
            skLineSegment(sketch, "E1205", {"start": v(4.7, -0.07) * mm, "end": v(4.7, -0.05) * mm});
            skLineSegment(sketch, "E1206", {"start": v(4.7, -0.05) * mm, "end": v(4.7, -0.03) * mm});
            skLineSegment(sketch, "E1207", {"start": v(4.7, -0.03) * mm, "end": v(4.7, 0) * mm});
            skLineSegment(sketch, "E1208", {"start": v(4.7, 0) * mm, "end": v(4.7, 0.03) * mm});
            skLineSegment(sketch, "E1209", {"start": v(4.7, 0.03) * mm, "end": v(4.7, 0.06) * mm});
            skLineSegment(sketch, "E1210", {"start": v(4.7, 0.06) * mm, "end": v(4.7, 0.08) * mm});
            skLineSegment(sketch, "E1211", {"start": v(4.7, 0.08) * mm, "end": v(4.7, 0.1) * mm});
            skLineSegment(sketch, "E1212", {"start": v(4.7, 0.1) * mm, "end": v(4.69, 0.13) * mm});
            skLineSegment(sketch, "E1213", {"start": v(4.69, 0.13) * mm, "end": v(4.68, 0.15) * mm});
            skLineSegment(sketch, "E1214", {"start": v(4.68, 0.15) * mm, "end": v(4.68, 0.17) * mm});
            skLineSegment(sketch, "E1215", {"start": v(4.68, 0.17) * mm, "end": v(4.67, 0.2) * mm});
            skLineSegment(sketch, "E1216", {"start": v(4.67, 0.2) * mm, "end": v(4.66, 0.21) * mm});
            skLineSegment(sketch, "E1217", {"start": v(4.66, 0.21) * mm, "end": v(4.66, 0.23) * mm});
            skLineSegment(sketch, "E1218", {"start": v(4.66, 0.23) * mm, "end": v(4.65, 0.26) * mm});
            skLineSegment(sketch, "E1219", {"start": v(4.65, 0.26) * mm, "end": v(4.64, 0.28) * mm});
            skLineSegment(sketch, "E1220", {"start": v(4.64, 0.28) * mm, "end": v(4.64, 0.3) * mm});
            skLineSegment(sketch, "E1221", {"start": v(4.64, 0.3) * mm, "end": v(4.63, 0.32) * mm});
            skLineSegment(sketch, "E1222", {"start": v(4.63, 0.32) * mm, "end": v(4.62, 0.34) * mm});
            skLineSegment(sketch, "E1223", {"start": v(4.62, 0.34) * mm, "end": v(4.61, 0.36) * mm});
            skLineSegment(sketch, "E1224", {"start": v(4.61, 0.36) * mm, "end": v(4.6, 0.38) * mm});
            skLineSegment(sketch, "E1225", {"start": v(4.6, 0.38) * mm, "end": v(4.6, 0.4) * mm});
            skLineSegment(sketch, "E1226", {"start": v(4.6, 0.4) * mm, "end": v(4.58, 0.42) * mm});
            skLineSegment(sketch, "E1227", {"start": v(4.58, 0.42) * mm, "end": v(4.57, 0.45) * mm});
            skLineSegment(sketch, "E1228", {"start": v(4.57, 0.45) * mm, "end": v(4.56, 0.47) * mm});
            skLineSegment(sketch, "E1229", {"start": v(4.56, 0.47) * mm, "end": v(4.55, 0.49) * mm});
            skLineSegment(sketch, "E1230", {"start": v(4.55, 0.49) * mm, "end": v(4.54, 0.5) * mm});
            skLineSegment(sketch, "E1231", {"start": v(4.54, 0.5) * mm, "end": v(4.53, 0.53) * mm});
            skLineSegment(sketch, "E1232", {"start": v(4.53, 0.53) * mm, "end": v(4.52, 0.55) * mm});
            skLineSegment(sketch, "E1233", {"start": v(4.52, 0.55) * mm, "end": v(4.51, 0.57) * mm});
            skLineSegment(sketch, "E1234", {"start": v(4.51, 0.57) * mm, "end": v(4.5, 0.6) * mm});
            skLineSegment(sketch, "E1235", {"start": v(4.5, 0.6) * mm, "end": v(4.49, 0.61) * mm});
            skLineSegment(sketch, "E1236", {"start": v(4.49, 0.61) * mm, "end": v(4.48, 0.63) * mm});
            skLineSegment(sketch, "E1237", {"start": v(4.48, 0.63) * mm, "end": v(4.47, 0.65) * mm});
            skLineSegment(sketch, "E1238", {"start": v(4.47, 0.65) * mm, "end": v(4.45, 0.67) * mm});
            skLineSegment(sketch, "E1239", {"start": v(4.45, 0.67) * mm, "end": v(4.44, 0.7) * mm});
            skLineSegment(sketch, "E1240", {"start": v(4.44, 0.7) * mm, "end": v(4.43, 0.72) * mm});
            skLineSegment(sketch, "E1241", {"start": v(4.43, 0.72) * mm, "end": v(4.41, 0.74) * mm});
            skLineSegment(sketch, "E1242", {"start": v(4.41, 0.74) * mm, "end": v(4.4, 0.76) * mm});
            skLineSegment(sketch, "E1243", {"start": v(4.4, 0.76) * mm, "end": v(4.39, 0.78) * mm});
            skLineSegment(sketch, "E1244", {"start": v(4.39, 0.78) * mm, "end": v(4.37, 0.8) * mm});
            skLineSegment(sketch, "E1245", {"start": v(4.37, 0.8) * mm, "end": v(4.36, 0.82) * mm});
            skLineSegment(sketch, "E1246", {"start": v(4.36, 0.82) * mm, "end": v(4.35, 0.84) * mm});
            skLineSegment(sketch, "E1247", {"start": v(4.35, 0.84) * mm, "end": v(4.33, 0.86) * mm});
            skLineSegment(sketch, "E1248", {"start": v(4.33, 0.86) * mm, "end": v(4.32, 0.88) * mm});
            skLineSegment(sketch, "E1249", {"start": v(4.32, 0.88) * mm, "end": v(4.3, 0.9) * mm});
            skLineSegment(sketch, "E1250", {"start": v(4.3, 0.9) * mm, "end": v(4.29, 0.92) * mm});
            skLineSegment(sketch, "E1251", {"start": v(4.29, 0.92) * mm, "end": v(4.27, 0.94) * mm});
            skLineSegment(sketch, "E1252", {"start": v(4.27, 0.94) * mm, "end": v(4.26, 0.96) * mm});
            skLineSegment(sketch, "E1253", {"start": v(4.26, 0.96) * mm, "end": v(4.24, 0.98) * mm});
            skLineSegment(sketch, "E1254", {"start": v(4.24, 0.98) * mm, "end": v(4.23, 1) * mm});
            skLineSegment(sketch, "E1255", {"start": v(4.23, 1) * mm, "end": v(4.21, 1.03) * mm});
            skLineSegment(sketch, "E1256", {"start": v(4.21, 1.03) * mm, "end": v(4.2, 1.05) * mm});
            skLineSegment(sketch, "E1257", {"start": v(4.2, 1.05) * mm, "end": v(4.18, 1.07) * mm});
            skLineSegment(sketch, "E1258", {"start": v(4.18, 1.07) * mm, "end": v(4.16, 1.09) * mm});
            skLineSegment(sketch, "E1259", {"start": v(4.16, 1.09) * mm, "end": v(4.14, 1.1) * mm});
            skLineSegment(sketch, "E1260", {"start": v(4.14, 1.1) * mm, "end": v(4.13, 1.13) * mm});
            skLineSegment(sketch, "E1261", {"start": v(4.13, 1.13) * mm, "end": v(4.1, 1.15) * mm});
            skLineSegment(sketch, "E1262", {"start": v(4.1, 1.15) * mm, "end": v(4.09, 1.17) * mm});
            skLineSegment(sketch, "E1263", {"start": v(4.09, 1.17) * mm, "end": v(4.07, 1.2) * mm});
            skLineSegment(sketch, "E1264", {"start": v(4.07, 1.2) * mm, "end": v(4.05, 1.21) * mm});
            skLineSegment(sketch, "E1265", {"start": v(4.05, 1.21) * mm, "end": v(4.03, 1.23) * mm});
            skLineSegment(sketch, "E1266", {"start": v(4.03, 1.23) * mm, "end": v(4.01, 1.25) * mm});
            skLineSegment(sketch, "E1267", {"start": v(4.01, 1.25) * mm, "end": v(4, 1.27) * mm});
            skLineSegment(sketch, "E1268", {"start": v(4, 1.27) * mm, "end": v(3.98, 1.3) * mm});
            skLineSegment(sketch, "E1269", {"start": v(3.98, 1.3) * mm, "end": v(3.96, 1.31) * mm});
            skLineSegment(sketch, "E1270", {"start": v(3.96, 1.31) * mm, "end": v(3.93, 1.33) * mm});
            skLineSegment(sketch, "E1271", {"start": v(3.93, 1.33) * mm, "end": v(3.91, 1.35) * mm});
            skLineSegment(sketch, "E1272", {"start": v(3.91, 1.35) * mm, "end": v(3.9, 1.37) * mm});
            skLineSegment(sketch, "E1273", {"start": v(3.9, 1.37) * mm, "end": v(3.87, 1.4) * mm});
            skLineSegment(sketch, "E1274", {"start": v(3.87, 1.4) * mm, "end": v(3.85, 1.41) * mm});
            skLineSegment(sketch, "E1275", {"start": v(3.85, 1.41) * mm, "end": v(3.83, 1.43) * mm});
            skLineSegment(sketch, "E1276", {"start": v(3.83, 1.43) * mm, "end": v(3.81, 1.45) * mm});
            skLineSegment(sketch, "E1277", {"start": v(3.81, 1.45) * mm, "end": v(3.8, 1.47) * mm});
            skLineSegment(sketch, "E1278", {"start": v(3.8, 1.47) * mm, "end": v(3.77, 1.49) * mm});
            skLineSegment(sketch, "E1279", {"start": v(3.77, 1.49) * mm, "end": v(3.75, 1.5) * mm});
            skLineSegment(sketch, "E1280", {"start": v(3.75, 1.5) * mm, "end": v(3.73, 1.52) * mm});
            skLineSegment(sketch, "E1281", {"start": v(3.73, 1.52) * mm, "end": v(3.7, 1.54) * mm});
            skLineSegment(sketch, "E1282", {"start": v(3.7, 1.54) * mm, "end": v(3.69, 1.56) * mm});
            skLineSegment(sketch, "E1283", {"start": v(3.69, 1.56) * mm, "end": v(3.67, 1.58) * mm});
            skLineSegment(sketch, "E1284", {"start": v(3.67, 1.58) * mm, "end": v(3.65, 1.6) * mm});
            skLineSegment(sketch, "E1285", {"start": v(3.65, 1.6) * mm, "end": v(3.63, 1.6) * mm});
            skLineSegment(sketch, "E1286", {"start": v(3.63, 1.6) * mm, "end": v(3.6, 1.63) * mm});
            skLineSegment(sketch, "E1287", {"start": v(3.6, 1.63) * mm, "end": v(3.59, 1.64) * mm});
            skLineSegment(sketch, "E1288", {"start": v(3.59, 1.64) * mm, "end": v(3.56, 1.66) * mm});
            skLineSegment(sketch, "E1289", {"start": v(3.56, 1.66) * mm, "end": v(3.54, 1.67) * mm});
            skLineSegment(sketch, "E1290", {"start": v(3.54, 1.67) * mm, "end": v(3.52, 1.69) * mm});
            skLineSegment(sketch, "E1291", {"start": v(3.52, 1.69) * mm, "end": v(3.5, 1.7) * mm});
            skLineSegment(sketch, "E1292", {"start": v(3.5, 1.7) * mm, "end": v(3.48, 1.72) * mm});
            skLineSegment(sketch, "E1293", {"start": v(3.48, 1.72) * mm, "end": v(3.46, 1.73) * mm});
            skLineSegment(sketch, "E1294", {"start": v(3.46, 1.73) * mm, "end": v(3.44, 1.75) * mm});
            skLineSegment(sketch, "E1295", {"start": v(3.44, 1.75) * mm, "end": v(3.42, 1.76) * mm});
            skLineSegment(sketch, "E1296", {"start": v(3.42, 1.76) * mm, "end": v(3.4, 1.77) * mm});
            skLineSegment(sketch, "E1297", {"start": v(3.4, 1.77) * mm, "end": v(3.38, 1.79) * mm});
            skLineSegment(sketch, "E1298", {"start": v(3.38, 1.79) * mm, "end": v(3.36, 1.8) * mm});
            skLineSegment(sketch, "E1299", {"start": v(3.36, 1.8) * mm, "end": v(3.34, 1.81) * mm});
            skLineSegment(sketch, "E1300", {"start": v(3.34, 1.81) * mm, "end": v(3.32, 1.83) * mm});
            skLineSegment(sketch, "E1301", {"start": v(3.32, 1.83) * mm, "end": v(3.3, 1.84) * mm});
            skLineSegment(sketch, "E1302", {"start": v(3.3, 1.84) * mm, "end": v(3.28, 1.85) * mm});
            skLineSegment(sketch, "E1303", {"start": v(3.28, 1.85) * mm, "end": v(3.25, 1.86) * mm});
            skLineSegment(sketch, "E1304", {"start": v(3.25, 1.86) * mm, "end": v(3.23, 1.88) * mm});
            skLineSegment(sketch, "E1305", {"start": v(3.23, 1.88) * mm, "end": v(3.21, 1.89) * mm});
            skLineSegment(sketch, "E1306", {"start": v(3.21, 1.89) * mm, "end": v(3.2, 1.9) * mm});
            skLineSegment(sketch, "E1307", {"start": v(3.2, 1.9) * mm, "end": v(3.17, 1.91) * mm});
            skLineSegment(sketch, "E1308", {"start": v(3.17, 1.91) * mm, "end": v(3.15, 1.92) * mm});
            skLineSegment(sketch, "E1309", {"start": v(3.15, 1.92) * mm, "end": v(3.13, 1.93) * mm});
            skLineSegment(sketch, "E1310", {"start": v(3.13, 1.93) * mm, "end": v(3.1, 1.94) * mm});
            skLineSegment(sketch, "E1311", {"start": v(3.1, 1.94) * mm, "end": v(3.09, 1.95) * mm});
            skLineSegment(sketch, "E1312", {"start": v(3.09, 1.95) * mm, "end": v(3.07, 1.96) * mm});
            skLineSegment(sketch, "E1313", {"start": v(3.07, 1.96) * mm, "end": v(3.05, 1.97) * mm});
            skLineSegment(sketch, "E1314", {"start": v(3.05, 1.97) * mm, "end": v(3.03, 1.98) * mm});
            skLineSegment(sketch, "E1315", {"start": v(3.03, 1.98) * mm, "end": v(3, 2) * mm});
            skLineSegment(sketch, "E1316", {"start": v(3, 2) * mm, "end": v(2.98, 2) * mm});
            skLineSegment(sketch, "E1317", {"start": v(2.98, 2) * mm, "end": v(2.96, 2) * mm});
            skLineSegment(sketch, "E1318", {"start": v(2.96, 2) * mm, "end": v(2.94, 2.02) * mm});
            skLineSegment(sketch, "E1319", {"start": v(2.94, 2.02) * mm, "end": v(2.92, 2.03) * mm});
            skLineSegment(sketch, "E1320", {"start": v(2.92, 2.03) * mm, "end": v(2.9, 2.03) * mm});
            skLineSegment(sketch, "E1321", {"start": v(2.9, 2.03) * mm, "end": v(2.88, 2.04) * mm});
            skLineSegment(sketch, "E1322", {"start": v(2.88, 2.04) * mm, "end": v(2.86, 2.05) * mm});
            skLineSegment(sketch, "E1323", {"start": v(2.86, 2.05) * mm, "end": v(2.83, 2.06) * mm});
            skLineSegment(sketch, "E1324", {"start": v(2.83, 2.06) * mm, "end": v(2.81, 2.06) * mm});
            skLineSegment(sketch, "E1325", {"start": v(2.81, 2.06) * mm, "end": v(2.8, 2.07) * mm});
            skLineSegment(sketch, "E1326", {"start": v(2.8, 2.07) * mm, "end": v(2.77, 2.08) * mm});
            skLineSegment(sketch, "E1327", {"start": v(2.77, 2.08) * mm, "end": v(2.75, 2.08) * mm});
            skLineSegment(sketch, "E1328", {"start": v(2.75, 2.08) * mm, "end": v(2.73, 2.09) * mm});
            skLineSegment(sketch, "E1329", {"start": v(2.73, 2.09) * mm, "end": v(2.7, 2.1) * mm});
            skLineSegment(sketch, "E1330", {"start": v(2.7, 2.1) * mm, "end": v(2.68, 2.1) * mm});
            skLineSegment(sketch, "E1331", {"start": v(2.68, 2.1) * mm, "end": v(2.66, 2.1) * mm});
            skLineSegment(sketch, "E1332", {"start": v(2.66, 2.1) * mm, "end": v(2.63, 2.1) * mm});
            skLineSegment(sketch, "E1333", {"start": v(2.63, 2.1) * mm, "end": v(2.6, 2.1) * mm});
            skLineSegment(sketch, "E1334", {"start": v(2.6, 2.1) * mm, "end": v(2.57, 2.1) * mm});
            skLineSegment(sketch, "E1335", {"start": v(2.57, 2.1) * mm, "end": v(2.55, 2.1) * mm});
            skLineSegment(sketch, "E1336", {"start": v(2.55, 2.1) * mm, "end": v(2.53, 2.1) * mm});
            skLineSegment(sketch, "E1337", {"start": v(2.53, 2.1) * mm, "end": v(2.5, 2.1) * mm});
            skLineSegment(sketch, "E1338", {"start": v(2.5, 2.1) * mm, "end": v(2.48, 2.09) * mm});
            skLineSegment(sketch, "E1339", {"start": v(2.48, 2.09) * mm, "end": v(2.46, 2.08) * mm});
            skLineSegment(sketch, "E1340", {"start": v(2.46, 2.08) * mm, "end": v(2.44, 2.08) * mm});
            skLineSegment(sketch, "E1341", {"start": v(2.44, 2.08) * mm, "end": v(2.42, 2.07) * mm});
            skLineSegment(sketch, "E1342", {"start": v(2.42, 2.07) * mm, "end": v(2.4, 2.06) * mm});
            skLineSegment(sketch, "E1343", {"start": v(2.4, 2.06) * mm, "end": v(2.37, 2.06) * mm});
            skLineSegment(sketch, "E1344", {"start": v(2.37, 2.06) * mm, "end": v(2.35, 2.05) * mm});
            skLineSegment(sketch, "E1345", {"start": v(2.35, 2.05) * mm, "end": v(2.33, 2.04) * mm});
            skLineSegment(sketch, "E1346", {"start": v(2.33, 2.04) * mm, "end": v(2.3, 2.03) * mm});
            skLineSegment(sketch, "E1347", {"start": v(2.3, 2.03) * mm, "end": v(2.29, 2.03) * mm});
            skLineSegment(sketch, "E1348", {"start": v(2.29, 2.03) * mm, "end": v(2.27, 2.02) * mm});
            skLineSegment(sketch, "E1349", {"start": v(2.27, 2.02) * mm, "end": v(2.25, 2) * mm});
            skLineSegment(sketch, "E1350", {"start": v(2.25, 2) * mm, "end": v(2.23, 2) * mm});
            skLineSegment(sketch, "E1351", {"start": v(2.23, 2) * mm, "end": v(2.2, 2) * mm});
            skLineSegment(sketch, "E1352", {"start": v(2.2, 2) * mm, "end": v(2.18, 1.98) * mm});
            skLineSegment(sketch, "E1353", {"start": v(2.18, 1.98) * mm, "end": v(2.16, 1.97) * mm});
            skLineSegment(sketch, "E1354", {"start": v(2.16, 1.97) * mm, "end": v(2.14, 1.96) * mm});
            skLineSegment(sketch, "E1355", {"start": v(2.14, 1.96) * mm, "end": v(2.12, 1.95) * mm});
            skLineSegment(sketch, "E1356", {"start": v(2.12, 1.95) * mm, "end": v(2.1, 1.94) * mm});
            skLineSegment(sketch, "E1357", {"start": v(2.1, 1.94) * mm, "end": v(2.08, 1.93) * mm});
            skLineSegment(sketch, "E1358", {"start": v(2.08, 1.93) * mm, "end": v(2.06, 1.92) * mm});
            skLineSegment(sketch, "E1359", {"start": v(2.06, 1.92) * mm, "end": v(2.04, 1.91) * mm});
            skLineSegment(sketch, "E1360", {"start": v(2.04, 1.91) * mm, "end": v(2.02, 1.9) * mm});
            skLineSegment(sketch, "E1361", {"start": v(2.02, 1.9) * mm, "end": v(2, 1.89) * mm});
            skLineSegment(sketch, "E1362", {"start": v(2, 1.89) * mm, "end": v(1.97, 1.88) * mm});
            skLineSegment(sketch, "E1363", {"start": v(1.97, 1.88) * mm, "end": v(1.95, 1.86) * mm});
            skLineSegment(sketch, "E1364", {"start": v(1.95, 1.86) * mm, "end": v(1.93, 1.85) * mm});
            skLineSegment(sketch, "E1365", {"start": v(1.93, 1.85) * mm, "end": v(1.91, 1.84) * mm});
            skLineSegment(sketch, "E1366", {"start": v(1.91, 1.84) * mm, "end": v(1.9, 1.83) * mm});
            skLineSegment(sketch, "E1367", {"start": v(1.9, 1.83) * mm, "end": v(1.87, 1.81) * mm});
            skLineSegment(sketch, "E1368", {"start": v(1.87, 1.81) * mm, "end": v(1.85, 1.8) * mm});
            skLineSegment(sketch, "E1369", {"start": v(1.85, 1.8) * mm, "end": v(1.83, 1.79) * mm});
            skLineSegment(sketch, "E1370", {"start": v(1.83, 1.79) * mm, "end": v(1.8, 1.77) * mm});
            skLineSegment(sketch, "E1371", {"start": v(1.8, 1.77) * mm, "end": v(1.79, 1.76) * mm});
            skLineSegment(sketch, "E1372", {"start": v(1.79, 1.76) * mm, "end": v(1.77, 1.75) * mm});
            skLineSegment(sketch, "E1373", {"start": v(1.77, 1.75) * mm, "end": v(1.75, 1.73) * mm});
            skLineSegment(sketch, "E1374", {"start": v(1.75, 1.73) * mm, "end": v(1.73, 1.72) * mm});
            skLineSegment(sketch, "E1375", {"start": v(1.73, 1.72) * mm, "end": v(1.7, 1.7) * mm});
            skLineSegment(sketch, "E1376", {"start": v(1.7, 1.7) * mm, "end": v(1.69, 1.69) * mm});
            skLineSegment(sketch, "E1377", {"start": v(1.69, 1.69) * mm, "end": v(1.66, 1.67) * mm});
            skLineSegment(sketch, "E1378", {"start": v(1.66, 1.67) * mm, "end": v(1.64, 1.66) * mm});
            skLineSegment(sketch, "E1379", {"start": v(1.64, 1.66) * mm, "end": v(1.62, 1.64) * mm});
            skLineSegment(sketch, "E1380", {"start": v(1.62, 1.64) * mm, "end": v(1.6, 1.63) * mm});
            skLineSegment(sketch, "E1381", {"start": v(1.6, 1.63) * mm, "end": v(1.58, 1.6) * mm});
            skLineSegment(sketch, "E1382", {"start": v(1.58, 1.6) * mm, "end": v(1.56, 1.6) * mm});
            skLineSegment(sketch, "E1383", {"start": v(1.56, 1.6) * mm, "end": v(1.54, 1.58) * mm});
            skLineSegment(sketch, "E1384", {"start": v(1.54, 1.58) * mm, "end": v(1.52, 1.56) * mm});
            skLineSegment(sketch, "E1385", {"start": v(1.52, 1.56) * mm, "end": v(1.5, 1.54) * mm});
            skLineSegment(sketch, "E1386", {"start": v(1.5, 1.54) * mm, "end": v(1.48, 1.52) * mm});
            skLineSegment(sketch, "E1387", {"start": v(1.48, 1.52) * mm, "end": v(1.46, 1.5) * mm});
            skLineSegment(sketch, "E1388", {"start": v(1.46, 1.5) * mm, "end": v(1.44, 1.49) * mm});
            skLineSegment(sketch, "E1389", {"start": v(1.44, 1.49) * mm, "end": v(1.42, 1.47) * mm});
            skLineSegment(sketch, "E1390", {"start": v(1.42, 1.47) * mm, "end": v(1.4, 1.45) * mm});
            skLineSegment(sketch, "E1391", {"start": v(1.4, 1.45) * mm, "end": v(1.38, 1.43) * mm});
            skLineSegment(sketch, "E1392", {"start": v(1.38, 1.43) * mm, "end": v(1.36, 1.41) * mm});
            skLineSegment(sketch, "E1393", {"start": v(1.36, 1.41) * mm, "end": v(1.34, 1.4) * mm});
            skLineSegment(sketch, "E1394", {"start": v(1.34, 1.4) * mm, "end": v(1.31, 1.37) * mm});
            skLineSegment(sketch, "E1395", {"start": v(1.31, 1.37) * mm, "end": v(1.3, 1.35) * mm});
            skLineSegment(sketch, "E1396", {"start": v(1.3, 1.35) * mm, "end": v(1.27, 1.33) * mm});
            skLineSegment(sketch, "E1397", {"start": v(1.27, 1.33) * mm, "end": v(1.25, 1.31) * mm});
            skLineSegment(sketch, "E1398", {"start": v(1.25, 1.31) * mm, "end": v(1.23, 1.3) * mm});
            skLineSegment(sketch, "E1399", {"start": v(1.23, 1.3) * mm, "end": v(1.21, 1.27) * mm});
            skLineSegment(sketch, "E1400", {"start": v(1.21, 1.27) * mm, "end": v(1.2, 1.25) * mm});
            skLineSegment(sketch, "E1401", {"start": v(1.2, 1.25) * mm, "end": v(1.17, 1.23) * mm});
            skLineSegment(sketch, "E1402", {"start": v(1.17, 1.23) * mm, "end": v(1.16, 1.21) * mm});
            skLineSegment(sketch, "E1403", {"start": v(1.16, 1.21) * mm, "end": v(1.14, 1.2) * mm});
            skLineSegment(sketch, "E1404", {"start": v(1.14, 1.2) * mm, "end": v(1.12, 1.17) * mm});
            skLineSegment(sketch, "E1405", {"start": v(1.12, 1.17) * mm, "end": v(1.1, 1.15) * mm});
            skLineSegment(sketch, "E1406", {"start": v(1.1, 1.15) * mm, "end": v(1.08, 1.13) * mm});
            skLineSegment(sketch, "E1407", {"start": v(1.08, 1.13) * mm, "end": v(1.07, 1.1) * mm});
            skLineSegment(sketch, "E1408", {"start": v(1.07, 1.1) * mm, "end": v(1.05, 1.09) * mm});
            skLineSegment(sketch, "E1409", {"start": v(1.05, 1.09) * mm, "end": v(1.03, 1.07) * mm});
            skLineSegment(sketch, "E1410", {"start": v(1.03, 1.07) * mm, "end": v(1.01, 1.05) * mm});
            skLineSegment(sketch, "E1411", {"start": v(1.01, 1.05) * mm, "end": v(1, 1.03) * mm});
            skLineSegment(sketch, "E1412", {"start": v(1, 1.03) * mm, "end": v(0.98, 1) * mm});
            skLineSegment(sketch, "E1413", {"start": v(0.98, 1) * mm, "end": v(0.97, 0.98) * mm});
            skLineSegment(sketch, "E1414", {"start": v(0.97, 0.98) * mm, "end": v(0.95, 0.96) * mm});
            skLineSegment(sketch, "E1415", {"start": v(0.95, 0.96) * mm, "end": v(0.94, 0.94) * mm});
            skLineSegment(sketch, "E1416", {"start": v(0.94, 0.94) * mm, "end": v(0.92, 0.92) * mm});
            skLineSegment(sketch, "E1417", {"start": v(0.92, 0.92) * mm, "end": v(0.9, 0.9) * mm});
            skLineSegment(sketch, "E1418", {"start": v(0.9, 0.9) * mm, "end": v(0.9, 0.88) * mm});
            skLineSegment(sketch, "E1419", {"start": v(0.9, 0.88) * mm, "end": v(0.88, 0.86) * mm});
            skLineSegment(sketch, "E1420", {"start": v(0.88, 0.86) * mm, "end": v(0.86, 0.84) * mm});
            skLineSegment(sketch, "E1421", {"start": v(0.86, 0.84) * mm, "end": v(0.85, 0.82) * mm});
            skLineSegment(sketch, "E1422", {"start": v(0.85, 0.82) * mm, "end": v(0.83, 0.8) * mm});
            skLineSegment(sketch, "E1423", {"start": v(0.83, 0.8) * mm, "end": v(0.82, 0.78) * mm});
            skLineSegment(sketch, "E1424", {"start": v(0.82, 0.78) * mm, "end": v(0.8, 0.76) * mm});
            skLineSegment(sketch, "E1425", {"start": v(0.8, 0.76) * mm, "end": v(0.8, 0.74) * mm});
            skLineSegment(sketch, "E1426", {"start": v(0.8, 0.74) * mm, "end": v(0.78, 0.72) * mm});
            skLineSegment(sketch, "E1427", {"start": v(0.78, 0.72) * mm, "end": v(0.77, 0.7) * mm});
            skLineSegment(sketch, "E1428", {"start": v(0.77, 0.7) * mm, "end": v(0.76, 0.67) * mm});
            skLineSegment(sketch, "E1429", {"start": v(0.76, 0.67) * mm, "end": v(0.74, 0.65) * mm});
            skLineSegment(sketch, "E1430", {"start": v(0.74, 0.65) * mm, "end": v(0.73, 0.63) * mm});
            skLineSegment(sketch, "E1431", {"start": v(0.73, 0.63) * mm, "end": v(0.72, 0.61) * mm});
            skLineSegment(sketch, "E1432", {"start": v(0.72, 0.61) * mm, "end": v(0.7, 0.6) * mm});
            skLineSegment(sketch, "E1433", {"start": v(0.7, 0.6) * mm, "end": v(0.7, 0.57) * mm});
            skLineSegment(sketch, "E1434", {"start": v(0.7, 0.57) * mm, "end": v(0.69, 0.55) * mm});
            skLineSegment(sketch, "E1435", {"start": v(0.69, 0.55) * mm, "end": v(0.68, 0.53) * mm});
            skLineSegment(sketch, "E1436", {"start": v(0.68, 0.53) * mm, "end": v(0.66, 0.5) * mm});
            skLineSegment(sketch, "E1437", {"start": v(0.66, 0.5) * mm, "end": v(0.65, 0.49) * mm});
            skLineSegment(sketch, "E1438", {"start": v(0.65, 0.49) * mm, "end": v(0.64, 0.47) * mm});
            skLineSegment(sketch, "E1439", {"start": v(0.64, 0.47) * mm, "end": v(0.63, 0.45) * mm});
            skLineSegment(sketch, "E1440", {"start": v(0.63, 0.45) * mm, "end": v(0.62, 0.42) * mm});
            skLineSegment(sketch, "E1441", {"start": v(0.62, 0.42) * mm, "end": v(0.62, 0.4) * mm});
            skLineSegment(sketch, "E1442", {"start": v(0.62, 0.4) * mm, "end": v(0.6, 0.38) * mm});
            skLineSegment(sketch, "E1443", {"start": v(0.6, 0.38) * mm, "end": v(0.6, 0.36) * mm});
            skLineSegment(sketch, "E1444", {"start": v(0.6, 0.36) * mm, "end": v(0.59, 0.34) * mm});
            skLineSegment(sketch, "E1445", {"start": v(0.59, 0.34) * mm, "end": v(0.58, 0.32) * mm});
            skLineSegment(sketch, "E1446", {"start": v(0.58, 0.32) * mm, "end": v(0.57, 0.3) * mm});
            skLineSegment(sketch, "E1447", {"start": v(0.57, 0.3) * mm, "end": v(0.57, 0.28) * mm});
            skLineSegment(sketch, "E1448", {"start": v(0.57, 0.28) * mm, "end": v(0.56, 0.26) * mm});
            skLineSegment(sketch, "E1449", {"start": v(0.56, 0.26) * mm, "end": v(0.55, 0.23) * mm});
            skLineSegment(sketch, "E1450", {"start": v(0.55, 0.23) * mm, "end": v(0.54, 0.21) * mm});
            skLineSegment(sketch, "E1451", {"start": v(0.54, 0.21) * mm, "end": v(0.54, 0.2) * mm});
            skLineSegment(sketch, "E1452", {"start": v(0.54, 0.2) * mm, "end": v(0.53, 0.17) * mm});
            skLineSegment(sketch, "E1453", {"start": v(0.53, 0.17) * mm, "end": v(0.53, 0.15) * mm});
            skLineSegment(sketch, "E1454", {"start": v(0.53, 0.15) * mm, "end": v(0.52, 0.13) * mm});
            skLineSegment(sketch, "E1455", {"start": v(0.52, 0.13) * mm, "end": v(0.52, 0.1) * mm});
            skLineSegment(sketch, "E1456", {"start": v(0.52, 0.1) * mm, "end": v(0.51, 0.08) * mm});
            skLineSegment(sketch, "E1457", {"start": v(0.51, 0.08) * mm, "end": v(0.5, 0.06) * mm});
            skLineSegment(sketch, "E1458", {"start": v(0.5, 0.06) * mm, "end": v(0.5, 0.03) * mm});
            skLineSegment(sketch, "E1459", {"start": v(0.5, 0.03) * mm, "end": v(0.5, 0) * mm});
            skLineSegment(sketch, "E1460", {"start": v(0.5, 0) * mm, "end": v(0.5, -0.03) * mm});
            skLineSegment(sketch, "E1461", {"start": v(0.5, -0.03) * mm, "end": v(0.5, -0.05) * mm});
            skLineSegment(sketch, "E1462", {"start": v(0.5, -0.05) * mm, "end": v(0.51, -0.07) * mm});
            skLineSegment(sketch, "E1463", {"start": v(0.51, -0.07) * mm, "end": v(0.52, -0.1) * mm});
            skLineSegment(sketch, "E1464", {"start": v(0.52, -0.1) * mm, "end": v(0.52, -0.12) * mm});
            skLineSegment(sketch, "E1465", {"start": v(0.52, -0.12) * mm, "end": v(0.53, -0.14) * mm});
            skLineSegment(sketch, "E1466", {"start": v(0.53, -0.14) * mm, "end": v(0.53, -0.16) * mm});
            skLineSegment(sketch, "E1467", {"start": v(0.53, -0.16) * mm, "end": v(0.54, -0.18) * mm});
            skLineSegment(sketch, "E1468", {"start": v(0.54, -0.18) * mm, "end": v(0.54, -0.2) * mm});
            skLineSegment(sketch, "E1469", {"start": v(0.54, -0.2) * mm, "end": v(0.55, -0.23) * mm});
            skLineSegment(sketch, "E1470", {"start": v(0.55, -0.23) * mm, "end": v(0.56, -0.25) * mm});
            skLineSegment(sketch, "E1471", {"start": v(0.56, -0.25) * mm, "end": v(0.57, -0.27) * mm});
            skLineSegment(sketch, "E1472", {"start": v(0.57, -0.27) * mm, "end": v(0.57, -0.3) * mm});
            skLineSegment(sketch, "E1473", {"start": v(0.57, -0.3) * mm, "end": v(0.58, -0.31) * mm});
            skLineSegment(sketch, "E1474", {"start": v(0.58, -0.31) * mm, "end": v(0.59, -0.33) * mm});
            skLineSegment(sketch, "E1475", {"start": v(0.59, -0.33) * mm, "end": v(0.6, -0.35) * mm});
            skLineSegment(sketch, "E1476", {"start": v(0.6, -0.35) * mm, "end": v(0.6, -0.38) * mm});
            skLineSegment(sketch, "E1477", {"start": v(0.6, -0.38) * mm, "end": v(0.62, -0.4) * mm});
            skLineSegment(sketch, "E1478", {"start": v(0.62, -0.4) * mm, "end": v(0.62, -0.42) * mm});
            skLineSegment(sketch, "E1479", {"start": v(0.62, -0.42) * mm, "end": v(0.63, -0.44) * mm});
            skLineSegment(sketch, "E1480", {"start": v(0.63, -0.44) * mm, "end": v(0.64, -0.46) * mm});
            skLineSegment(sketch, "E1481", {"start": v(0.64, -0.46) * mm, "end": v(0.65, -0.48) * mm});
            skLineSegment(sketch, "E1482", {"start": v(0.65, -0.48) * mm, "end": v(0.66, -0.5) * mm});
            skLineSegment(sketch, "E1483", {"start": v(0.66, -0.5) * mm, "end": v(0.68, -0.52) * mm});
            skLineSegment(sketch, "E1484", {"start": v(0.68, -0.52) * mm, "end": v(0.69, -0.54) * mm});
            skLineSegment(sketch, "E1485", {"start": v(0.69, -0.54) * mm, "end": v(0.7, -0.56) * mm});
            skLineSegment(sketch, "E1486", {"start": v(0.7, -0.56) * mm, "end": v(0.7, -0.58) * mm});
            skLineSegment(sketch, "E1487", {"start": v(0.7, -0.58) * mm, "end": v(0.72, -0.6) * mm});
            skLineSegment(sketch, "E1488", {"start": v(0.72, -0.6) * mm, "end": v(0.73, -0.63) * mm});
            skLineSegment(sketch, "E1489", {"start": v(0.73, -0.63) * mm, "end": v(0.74, -0.65) * mm});
            skLineSegment(sketch, "E1490", {"start": v(0.74, -0.65) * mm, "end": v(0.76, -0.67) * mm});
            skLineSegment(sketch, "E1491", {"start": v(0.76, -0.67) * mm, "end": v(0.77, -0.69) * mm});
            skLineSegment(sketch, "E1492", {"start": v(0.77, -0.69) * mm, "end": v(0.78, -0.7) * mm});
            skLineSegment(sketch, "E1493", {"start": v(0.78, -0.7) * mm, "end": v(0.8, -0.73) * mm});
            skLineSegment(sketch, "E1494", {"start": v(0.8, -0.73) * mm, "end": v(0.8, -0.75) * mm});
            skLineSegment(sketch, "E1495", {"start": v(0.8, -0.75) * mm, "end": v(0.82, -0.77) * mm});
            skLineSegment(sketch, "E1496", {"start": v(0.82, -0.77) * mm, "end": v(0.83, -0.8) * mm});
            skLineSegment(sketch, "E1497", {"start": v(0.83, -0.8) * mm, "end": v(0.85, -0.81) * mm});
            skLineSegment(sketch, "E1498", {"start": v(0.85, -0.81) * mm, "end": v(0.86, -0.83) * mm});
            skLineSegment(sketch, "E1499", {"start": v(0.86, -0.83) * mm, "end": v(0.88, -0.85) * mm});
            skLineSegment(sketch, "E1500", {"start": v(0.88, -0.85) * mm, "end": v(0.9, -0.87) * mm});
            skLineSegment(sketch, "E1501", {"start": v(0.9, -0.87) * mm, "end": v(0.9, -0.9) * mm});
            skLineSegment(sketch, "E1502", {"start": v(0.9, -0.9) * mm, "end": v(0.92, -0.92) * mm});
            skLineSegment(sketch, "E1503", {"start": v(0.92, -0.92) * mm, "end": v(0.94, -0.94) * mm});
            skLineSegment(sketch, "E1504", {"start": v(0.94, -0.94) * mm, "end": v(0.95, -0.96) * mm});
            skLineSegment(sketch, "E1505", {"start": v(0.95, -0.96) * mm, "end": v(0.97, -0.98) * mm});
            skLineSegment(sketch, "E1506", {"start": v(0.97, -0.98) * mm, "end": v(0.98, -1) * mm});
            skLineSegment(sketch, "E1507", {"start": v(0.98, -1) * mm, "end": v(1, -1.02) * mm});
            skLineSegment(sketch, "E1508", {"start": v(1, -1.02) * mm, "end": v(1.01, -1.04) * mm});
            skLineSegment(sketch, "E1509", {"start": v(1.01, -1.04) * mm, "end": v(1.03, -1.06) * mm});
            skLineSegment(sketch, "E1510", {"start": v(1.03, -1.06) * mm, "end": v(1.05, -1.08) * mm});
            skLineSegment(sketch, "E1511", {"start": v(1.05, -1.08) * mm, "end": v(1.07, -1.1) * mm});
            skLineSegment(sketch, "E1512", {"start": v(1.07, -1.1) * mm, "end": v(1.08, -1.12) * mm});
            skLineSegment(sketch, "E1513", {"start": v(1.08, -1.12) * mm, "end": v(1.1, -1.14) * mm});
            skLineSegment(sketch, "E1514", {"start": v(1.1, -1.14) * mm, "end": v(1.12, -1.16) * mm});
            skLineSegment(sketch, "E1515", {"start": v(1.12, -1.16) * mm, "end": v(1.14, -1.18) * mm});
            skLineSegment(sketch, "E1516", {"start": v(1.14, -1.18) * mm, "end": v(0.5, -1.82) * mm});
            skLineSegment(sketch, "E1517", {"start": v(0.5, -1.82) * mm, "end": v(0.78, -2.1) * mm});
            skLineSegment(sketch, "E1518", {"start": v(0.78, -2.1) * mm, "end": v(1.42, -1.46) * mm});
            skLineSegment(sketch, "E1519", {"start": v(1.7, -1.18) * mm, "end": v(1.7, -1.18) * mm});
            skLineSegment(sketch, "E1520", {"start": v(1.7, -1.18) * mm, "end": v(1.72, -1.2) * mm});
            skLineSegment(sketch, "E1521", {"start": v(1.72, -1.2) * mm, "end": v(1.74, -1.21) * mm});
            skLineSegment(sketch, "E1522", {"start": v(1.74, -1.21) * mm, "end": v(1.76, -1.23) * mm});
            skLineSegment(sketch, "E1523", {"start": v(1.76, -1.23) * mm, "end": v(1.78, -1.24) * mm});
            skLineSegment(sketch, "E1524", {"start": v(1.78, -1.24) * mm, "end": v(1.8, -1.26) * mm});
            skLineSegment(sketch, "E1525", {"start": v(1.8, -1.26) * mm, "end": v(1.81, -1.27) * mm});
            skLineSegment(sketch, "E1526", {"start": v(1.81, -1.27) * mm, "end": v(1.83, -1.29) * mm});
            skLineSegment(sketch, "E1527", {"start": v(1.83, -1.29) * mm, "end": v(1.85, -1.3) * mm});
            skLineSegment(sketch, "E1528", {"start": v(1.85, -1.3) * mm, "end": v(1.87, -1.32) * mm});
            skLineSegment(sketch, "E1529", {"start": v(1.87, -1.32) * mm, "end": v(1.89, -1.33) * mm});
            skLineSegment(sketch, "E1530", {"start": v(1.89, -1.33) * mm, "end": v(1.9, -1.34) * mm});
            skLineSegment(sketch, "E1531", {"start": v(1.9, -1.34) * mm, "end": v(1.92, -1.36) * mm});
            skLineSegment(sketch, "E1532", {"start": v(1.92, -1.36) * mm, "end": v(1.94, -1.37) * mm});
            skLineSegment(sketch, "E1533", {"start": v(1.94, -1.37) * mm, "end": v(1.96, -1.38) * mm});
            skLineSegment(sketch, "E1534", {"start": v(1.96, -1.38) * mm, "end": v(1.98, -1.4) * mm});
            skLineSegment(sketch, "E1535", {"start": v(1.98, -1.4) * mm, "end": v(2, -1.4) * mm});
            skLineSegment(sketch, "E1536", {"start": v(2, -1.4) * mm, "end": v(2.01, -1.42) * mm});
            skLineSegment(sketch, "E1537", {"start": v(2.01, -1.42) * mm, "end": v(2.03, -1.43) * mm});
            skLineSegment(sketch, "E1538", {"start": v(2.03, -1.43) * mm, "end": v(2.05, -1.45) * mm});
            skLineSegment(sketch, "E1539", {"start": v(2.05, -1.45) * mm, "end": v(2.07, -1.46) * mm});
            skLineSegment(sketch, "E1540", {"start": v(2.07, -1.46) * mm, "end": v(2.08, -1.47) * mm});
            skLineSegment(sketch, "E1541", {"start": v(2.08, -1.47) * mm, "end": v(2.1, -1.48) * mm});
            skLineSegment(sketch, "E1542", {"start": v(2.1, -1.48) * mm, "end": v(2.12, -1.5) * mm});
            skLineSegment(sketch, "E1543", {"start": v(2.12, -1.5) * mm, "end": v(2.14, -1.5) * mm});
            skLineSegment(sketch, "E1544", {"start": v(2.14, -1.5) * mm, "end": v(2.15, -1.51) * mm});
            skLineSegment(sketch, "E1545", {"start": v(2.15, -1.51) * mm, "end": v(2.17, -1.52) * mm});
            skLineSegment(sketch, "E1546", {"start": v(2.17, -1.52) * mm, "end": v(2.2, -1.53) * mm});
            skLineSegment(sketch, "E1547", {"start": v(2.2, -1.53) * mm, "end": v(2.2, -1.54) * mm});
            skLineSegment(sketch, "E1548", {"start": v(2.2, -1.54) * mm, "end": v(2.23, -1.55) * mm});
            skLineSegment(sketch, "E1549", {"start": v(2.23, -1.55) * mm, "end": v(2.24, -1.56) * mm});
            skLineSegment(sketch, "E1550", {"start": v(2.24, -1.56) * mm, "end": v(2.26, -1.57) * mm});
            skLineSegment(sketch, "E1551", {"start": v(2.26, -1.57) * mm, "end": v(2.28, -1.58) * mm});
            skLineSegment(sketch, "E1552", {"start": v(2.28, -1.58) * mm, "end": v(2.3, -1.59) * mm});
            skLineSegment(sketch, "E1553", {"start": v(2.3, -1.59) * mm, "end": v(2.31, -1.6) * mm});
            skLineSegment(sketch, "E1554", {"start": v(2.31, -1.6) * mm, "end": v(2.33, -1.6) * mm});
            skLineSegment(sketch, "E1555", {"start": v(2.33, -1.6) * mm, "end": v(2.35, -1.61) * mm});
            skLineSegment(sketch, "E1556", {"start": v(2.35, -1.61) * mm, "end": v(2.36, -1.62) * mm});
            skLineSegment(sketch, "E1557", {"start": v(2.36, -1.62) * mm, "end": v(2.38, -1.63) * mm});
            skLineSegment(sketch, "E1558", {"start": v(2.38, -1.63) * mm, "end": v(2.4, -1.63) * mm});
            skLineSegment(sketch, "E1559", {"start": v(2.4, -1.63) * mm, "end": v(2.41, -1.64) * mm});
            skLineSegment(sketch, "E1560", {"start": v(2.41, -1.64) * mm, "end": v(2.43, -1.65) * mm});
            skLineSegment(sketch, "E1561", {"start": v(2.43, -1.65) * mm, "end": v(2.45, -1.65) * mm});
            skLineSegment(sketch, "E1562", {"start": v(2.45, -1.65) * mm, "end": v(2.46, -1.66) * mm});
            skLineSegment(sketch, "E1563", {"start": v(2.46, -1.66) * mm, "end": v(2.48, -1.66) * mm});
            skLineSegment(sketch, "E1564", {"start": v(2.48, -1.66) * mm, "end": v(2.5, -1.67) * mm});
            skLineSegment(sketch, "E1565", {"start": v(2.5, -1.67) * mm, "end": v(2.51, -1.67) * mm});
            skLineSegment(sketch, "E1566", {"start": v(2.51, -1.67) * mm, "end": v(2.53, -1.68) * mm});
            skLineSegment(sketch, "E1567", {"start": v(2.53, -1.68) * mm, "end": v(2.54, -1.68) * mm});
            skLineSegment(sketch, "E1568", {"start": v(2.54, -1.68) * mm, "end": v(2.56, -1.69) * mm});
            skLineSegment(sketch, "E1569", {"start": v(2.56, -1.69) * mm, "end": v(2.57, -1.69) * mm});
            skLineSegment(sketch, "E1570", {"start": v(2.57, -1.69) * mm, "end": v(2.58, -1.7) * mm});
            skLineSegment(sketch, "E1571", {"start": v(2.58, -1.7) * mm, "end": v(2.6, -1.7) * mm});
            skLineSegment(sketch, "E1572", {"start": v(2.6, -1.7) * mm, "end": v(2.6, -1.7) * mm});
            skLineSegment(sketch, "E1573", {"start": v(2.6, -1.7) * mm, "end": v(2.61, -1.7) * mm});
            skLineSegment(sketch, "E1574", {"start": v(2.61, -1.7) * mm, "end": v(2.63, -1.7) * mm});
            skLineSegment(sketch, "E1575", {"start": v(2.63, -1.7) * mm, "end": v(2.64, -1.69) * mm});
            skLineSegment(sketch, "E1576", {"start": v(2.64, -1.69) * mm, "end": v(2.65, -1.69) * mm});
            skLineSegment(sketch, "E1577", {"start": v(2.65, -1.69) * mm, "end": v(2.67, -1.68) * mm});
            skLineSegment(sketch, "E1578", {"start": v(2.67, -1.68) * mm, "end": v(2.68, -1.68) * mm});
            skLineSegment(sketch, "E1579", {"start": v(2.68, -1.68) * mm, "end": v(2.7, -1.67) * mm});
            skLineSegment(sketch, "E1580", {"start": v(2.7, -1.67) * mm, "end": v(2.71, -1.67) * mm});
            skLineSegment(sketch, "E1581", {"start": v(2.71, -1.67) * mm, "end": v(2.73, -1.66) * mm});
            skLineSegment(sketch, "E1582", {"start": v(2.73, -1.66) * mm, "end": v(2.74, -1.66) * mm});
            skLineSegment(sketch, "E1583", {"start": v(2.74, -1.66) * mm, "end": v(2.76, -1.65) * mm});
            skLineSegment(sketch, "E1584", {"start": v(2.76, -1.65) * mm, "end": v(2.78, -1.65) * mm});
            skLineSegment(sketch, "E1585", {"start": v(2.78, -1.65) * mm, "end": v(2.8, -1.64) * mm});
            skLineSegment(sketch, "E1586", {"start": v(2.8, -1.64) * mm, "end": v(2.81, -1.63) * mm});
            skLineSegment(sketch, "E1587", {"start": v(2.81, -1.63) * mm, "end": v(2.83, -1.63) * mm});
            skLineSegment(sketch, "E1588", {"start": v(2.83, -1.63) * mm, "end": v(2.84, -1.62) * mm});
            skLineSegment(sketch, "E1589", {"start": v(2.84, -1.62) * mm, "end": v(2.86, -1.61) * mm});
            skLineSegment(sketch, "E1590", {"start": v(2.86, -1.61) * mm, "end": v(2.88, -1.6) * mm});
            skLineSegment(sketch, "E1591", {"start": v(2.88, -1.6) * mm, "end": v(2.9, -1.6) * mm});
            skLineSegment(sketch, "E1592", {"start": v(2.9, -1.6) * mm, "end": v(2.91, -1.59) * mm});
            skLineSegment(sketch, "E1593", {"start": v(2.91, -1.59) * mm, "end": v(2.93, -1.58) * mm});
            skLineSegment(sketch, "E1594", {"start": v(2.93, -1.58) * mm, "end": v(2.95, -1.57) * mm});
            skLineSegment(sketch, "E1595", {"start": v(2.95, -1.57) * mm, "end": v(2.97, -1.56) * mm});
            skLineSegment(sketch, "E1596", {"start": v(2.97, -1.56) * mm, "end": v(2.98, -1.55) * mm});
            skLineSegment(sketch, "E1597", {"start": v(2.98, -1.55) * mm, "end": v(3, -1.54) * mm});
            skLineSegment(sketch, "E1598", {"start": v(3, -1.54) * mm, "end": v(3.02, -1.53) * mm});
            skLineSegment(sketch, "E1599", {"start": v(3.02, -1.53) * mm, "end": v(3.04, -1.52) * mm});
            skLineSegment(sketch, "E1600", {"start": v(3.04, -1.52) * mm, "end": v(3.05, -1.51) * mm});
            skLineSegment(sketch, "E1601", {"start": v(3.05, -1.51) * mm, "end": v(3.07, -1.5) * mm});
            skLineSegment(sketch, "E1602", {"start": v(3.07, -1.5) * mm, "end": v(3.09, -1.5) * mm});
            skLineSegment(sketch, "E1603", {"start": v(3.09, -1.5) * mm, "end": v(3.1, -1.48) * mm});
            skLineSegment(sketch, "E1604", {"start": v(3.1, -1.48) * mm, "end": v(3.12, -1.47) * mm});
            skLineSegment(sketch, "E1605", {"start": v(3.12, -1.47) * mm, "end": v(3.14, -1.46) * mm});
            skLineSegment(sketch, "E1606", {"start": v(3.14, -1.46) * mm, "end": v(3.16, -1.45) * mm});
            skLineSegment(sketch, "E1607", {"start": v(3.16, -1.45) * mm, "end": v(3.18, -1.43) * mm});
            skLineSegment(sketch, "E1608", {"start": v(3.18, -1.43) * mm, "end": v(3.2, -1.42) * mm});
            skLineSegment(sketch, "E1609", {"start": v(3.2, -1.42) * mm, "end": v(3.21, -1.4) * mm});
            skLineSegment(sketch, "E1610", {"start": v(3.21, -1.4) * mm, "end": v(3.23, -1.4) * mm});
            skLineSegment(sketch, "E1611", {"start": v(3.23, -1.4) * mm, "end": v(3.25, -1.38) * mm});
            skLineSegment(sketch, "E1612", {"start": v(3.25, -1.38) * mm, "end": v(3.27, -1.37) * mm});
            skLineSegment(sketch, "E1613", {"start": v(3.27, -1.37) * mm, "end": v(3.29, -1.36) * mm});
            skLineSegment(sketch, "E1614", {"start": v(3.29, -1.36) * mm, "end": v(3.3, -1.34) * mm});
            skLineSegment(sketch, "E1615", {"start": v(3.3, -1.34) * mm, "end": v(3.32, -1.33) * mm});
            skLineSegment(sketch, "E1616", {"start": v(3.32, -1.33) * mm, "end": v(3.34, -1.32) * mm});
            skLineSegment(sketch, "E1617", {"start": v(3.34, -1.32) * mm, "end": v(3.36, -1.3) * mm});
            skLineSegment(sketch, "E1618", {"start": v(3.36, -1.3) * mm, "end": v(3.38, -1.29) * mm});
            skLineSegment(sketch, "E1619", {"start": v(3.38, -1.29) * mm, "end": v(3.4, -1.27) * mm});
            skLineSegment(sketch, "E1620", {"start": v(3.4, -1.27) * mm, "end": v(3.41, -1.26) * mm});
            skLineSegment(sketch, "E1621", {"start": v(3.41, -1.26) * mm, "end": v(3.43, -1.24) * mm});
            skLineSegment(sketch, "E1622", {"start": v(3.43, -1.24) * mm, "end": v(3.45, -1.23) * mm});
            skLineSegment(sketch, "E1623", {"start": v(3.45, -1.23) * mm, "end": v(3.47, -1.21) * mm});
            skLineSegment(sketch, "E1624", {"start": v(3.47, -1.21) * mm, "end": v(3.49, -1.2) * mm});
            skLineSegment(sketch, "E1625", {"start": v(3.49, -1.2) * mm, "end": v(3.5, -1.18) * mm});
            skLineSegment(sketch, "E1626", {"start": v(3.5, -1.18) * mm, "end": v(3.52, -1.17) * mm});
            skLineSegment(sketch, "E1627", {"start": v(3.52, -1.17) * mm, "end": v(3.54, -1.15) * mm});
            skLineSegment(sketch, "E1628", {"start": v(3.54, -1.15) * mm, "end": v(3.56, -1.13) * mm});
            skLineSegment(sketch, "E1629", {"start": v(3.56, -1.13) * mm, "end": v(3.58, -1.12) * mm});
            skLineSegment(sketch, "E1630", {"start": v(3.58, -1.12) * mm, "end": v(3.6, -1.1) * mm});
            skLineSegment(sketch, "E1631", {"start": v(3.6, -1.1) * mm, "end": v(3.62, -1.08) * mm});
            skLineSegment(sketch, "E1632", {"start": v(3.62, -1.08) * mm, "end": v(3.63, -1.06) * mm});
            skLineSegment(sketch, "E1633", {"start": v(3.63, -1.06) * mm, "end": v(3.65, -1.04) * mm});
            skLineSegment(sketch, "E1634", {"start": v(3.65, -1.04) * mm, "end": v(3.67, -1.03) * mm});
            skLineSegment(sketch, "E1635", {"start": v(3.67, -1.03) * mm, "end": v(3.69, -1) * mm});
            skLineSegment(sketch, "E1636", {"start": v(3.69, -1) * mm, "end": v(3.7, -0.99) * mm});
            skLineSegment(sketch, "E1637", {"start": v(3.7, -0.99) * mm, "end": v(3.72, -0.97) * mm});
            skLineSegment(sketch, "E1638", {"start": v(3.72, -0.97) * mm, "end": v(3.74, -0.95) * mm});
            skLineSegment(sketch, "E1639", {"start": v(3.74, -0.95) * mm, "end": v(3.76, -0.93) * mm});
            skLineSegment(sketch, "E1640", {"start": v(3.76, -0.93) * mm, "end": v(3.77, -0.92) * mm});
            skLineSegment(sketch, "E1641", {"start": v(3.77, -0.92) * mm, "end": v(3.79, -0.9) * mm});
            skLineSegment(sketch, "E1642", {"start": v(3.79, -0.9) * mm, "end": v(3.8, -0.88) * mm});
            skLineSegment(sketch, "E1643", {"start": v(3.8, -0.88) * mm, "end": v(3.82, -0.86) * mm});
            skLineSegment(sketch, "E1644", {"start": v(3.82, -0.86) * mm, "end": v(3.84, -0.84) * mm});
            skLineSegment(sketch, "E1645", {"start": v(3.84, -0.84) * mm, "end": v(3.85, -0.82) * mm});
            skLineSegment(sketch, "E1646", {"start": v(3.85, -0.82) * mm, "end": v(3.87, -0.8) * mm});
            skLineSegment(sketch, "E1647", {"start": v(3.87, -0.8) * mm, "end": v(3.88, -0.79) * mm});
            skLineSegment(sketch, "E1648", {"start": v(3.88, -0.79) * mm, "end": v(3.9, -0.77) * mm});
            skLineSegment(sketch, "E1649", {"start": v(3.9, -0.77) * mm, "end": v(3.91, -0.75) * mm});
            skLineSegment(sketch, "E1650", {"start": v(3.91, -0.75) * mm, "end": v(3.92, -0.73) * mm});
            skLineSegment(sketch, "E1651", {"start": v(3.92, -0.73) * mm, "end": v(3.94, -0.72) * mm});
            skLineSegment(sketch, "E1652", {"start": v(3.94, -0.72) * mm, "end": v(3.95, -0.7) * mm});
            skLineSegment(sketch, "E1653", {"start": v(3.95, -0.7) * mm, "end": v(3.97, -0.68) * mm});
            skLineSegment(sketch, "E1654", {"start": v(3.97, -0.68) * mm, "end": v(3.98, -0.66) * mm});
            skLineSegment(sketch, "E1655", {"start": v(3.98, -0.66) * mm, "end": v(4, -0.64) * mm});
            skLineSegment(sketch, "E1656", {"start": v(4, -0.64) * mm, "end": v(4, -0.62) * mm});
            skLineSegment(sketch, "E1657", {"start": v(4, -0.62) * mm, "end": v(4.02, -0.6) * mm});
            skLineSegment(sketch, "E1658", {"start": v(4.02, -0.6) * mm, "end": v(4.03, -0.59) * mm});
            skLineSegment(sketch, "E1659", {"start": v(4.03, -0.59) * mm, "end": v(4.04, -0.57) * mm});
            skLineSegment(sketch, "E1660", {"start": v(4.04, -0.57) * mm, "end": v(4.05, -0.55) * mm});
            skLineSegment(sketch, "E1661", {"start": v(4.05, -0.55) * mm, "end": v(4.06, -0.53) * mm});
            skLineSegment(sketch, "E1662", {"start": v(4.06, -0.53) * mm, "end": v(4.08, -0.52) * mm});
            skLineSegment(sketch, "E1663", {"start": v(4.08, -0.52) * mm, "end": v(4.09, -0.5) * mm});
            skLineSegment(sketch, "E1664", {"start": v(4.09, -0.5) * mm, "end": v(4.1, -0.48) * mm});
            skLineSegment(sketch, "E1665", {"start": v(4.1, -0.48) * mm, "end": v(4.1, -0.46) * mm});
            skLineSegment(sketch, "E1666", {"start": v(4.1, -0.46) * mm, "end": v(4.12, -0.45) * mm});
            skLineSegment(sketch, "E1667", {"start": v(4.12, -0.45) * mm, "end": v(4.13, -0.43) * mm});
            skLineSegment(sketch, "E1668", {"start": v(4.13, -0.43) * mm, "end": v(4.14, -0.41) * mm});
            skLineSegment(sketch, "E1669", {"start": v(4.14, -0.41) * mm, "end": v(4.15, -0.4) * mm});
            skLineSegment(sketch, "E1670", {"start": v(4.15, -0.4) * mm, "end": v(4.16, -0.37) * mm});
            skLineSegment(sketch, "E1671", {"start": v(4.16, -0.37) * mm, "end": v(4.17, -0.36) * mm});
            skLineSegment(sketch, "E1672", {"start": v(4.17, -0.36) * mm, "end": v(4.18, -0.34) * mm});
            skLineSegment(sketch, "E1673", {"start": v(4.18, -0.34) * mm, "end": v(4.19, -0.32) * mm});
            skLineSegment(sketch, "E1674", {"start": v(4.19, -0.32) * mm, "end": v(4.2, -0.3) * mm});
            skLineSegment(sketch, "E1675", {"start": v(4.2, -0.3) * mm, "end": v(4.2, -0.29) * mm});
            skLineSegment(sketch, "E1676", {"start": v(4.2, -0.29) * mm, "end": v(4.21, -0.27) * mm});
            skLineSegment(sketch, "E1677", {"start": v(4.21, -0.27) * mm, "end": v(4.22, -0.25) * mm});
            skLineSegment(sketch, "E1678", {"start": v(4.22, -0.25) * mm, "end": v(4.23, -0.24) * mm});
            skLineSegment(sketch, "E1679", {"start": v(4.23, -0.24) * mm, "end": v(4.23, -0.22) * mm});
            skLineSegment(sketch, "E1680", {"start": v(4.23, -0.22) * mm, "end": v(4.24, -0.2) * mm});
            skLineSegment(sketch, "E1681", {"start": v(4.24, -0.2) * mm, "end": v(4.25, -0.19) * mm});
            skLineSegment(sketch, "E1682", {"start": v(4.25, -0.19) * mm, "end": v(4.25, -0.17) * mm});
            skLineSegment(sketch, "E1683", {"start": v(4.25, -0.17) * mm, "end": v(4.26, -0.15) * mm});
            skLineSegment(sketch, "E1684", {"start": v(4.26, -0.15) * mm, "end": v(4.27, -0.14) * mm});
            skLineSegment(sketch, "E1685", {"start": v(4.27, -0.14) * mm, "end": v(4.27, -0.12) * mm});
            skLineSegment(sketch, "E1686", {"start": v(4.27, -0.12) * mm, "end": v(4.28, -0.1) * mm});
            skLineSegment(sketch, "E1687", {"start": v(4.28, -0.1) * mm, "end": v(4.28, -0.09) * mm});
            skLineSegment(sketch, "E1688", {"start": v(4.28, -0.09) * mm, "end": v(4.29, -0.07) * mm});
            skLineSegment(sketch, "E1689", {"start": v(4.29, -0.07) * mm, "end": v(4.29, -0.06) * mm});
            skLineSegment(sketch, "E1690", {"start": v(4.29, -0.06) * mm, "end": v(4.3, -0.04) * mm});
            skLineSegment(sketch, "E1691", {"start": v(4.3, -0.04) * mm, "end": v(4.3, -0.03) * mm});
            skLineSegment(sketch, "E1692", {"start": v(4.3, -0.03) * mm, "end": v(4.3, -0.02) * mm});
            skLineSegment(sketch, "E1693", {"start": v(4.3, -0.02) * mm, "end": v(4.3, 0) * mm});
            skLineSegment(sketch, "E1694", {"start": v(4.3, 0) * mm, "end": v(4.3, 0) * mm});
            skLineSegment(sketch, "E1695", {"start": v(4.3, 0) * mm, "end": v(4.3, 0.01) * mm});
            skLineSegment(sketch, "E1696", {"start": v(4.3, 0.01) * mm, "end": v(4.3, 0.02) * mm});
            skLineSegment(sketch, "E1697", {"start": v(4.3, 0.02) * mm, "end": v(4.3, 0.04) * mm});
            skLineSegment(sketch, "E1698", {"start": v(4.3, 0.04) * mm, "end": v(4.3, 0.05) * mm});
            skLineSegment(sketch, "E1699", {"start": v(4.3, 0.05) * mm, "end": v(4.29, 0.07) * mm});
            skLineSegment(sketch, "E1700", {"start": v(4.29, 0.07) * mm, "end": v(4.29, 0.08) * mm});
            skLineSegment(sketch, "E1701", {"start": v(4.29, 0.08) * mm, "end": v(4.28, 0.1) * mm});
            skLineSegment(sketch, "E1702", {"start": v(4.28, 0.1) * mm, "end": v(4.28, 0.11) * mm});
            skLineSegment(sketch, "E1703", {"start": v(4.28, 0.11) * mm, "end": v(4.27, 0.13) * mm});
            skLineSegment(sketch, "E1704", {"start": v(4.27, 0.13) * mm, "end": v(4.27, 0.14) * mm});
            skLineSegment(sketch, "E1705", {"start": v(4.27, 0.14) * mm, "end": v(4.26, 0.16) * mm});
            skLineSegment(sketch, "E1706", {"start": v(4.26, 0.16) * mm, "end": v(4.25, 0.18) * mm});
            skLineSegment(sketch, "E1707", {"start": v(4.25, 0.18) * mm, "end": v(4.25, 0.2) * mm});
            skLineSegment(sketch, "E1708", {"start": v(4.25, 0.2) * mm, "end": v(4.24, 0.21) * mm});
            skLineSegment(sketch, "E1709", {"start": v(4.24, 0.21) * mm, "end": v(4.23, 0.23) * mm});
            skLineSegment(sketch, "E1710", {"start": v(4.23, 0.23) * mm, "end": v(4.23, 0.24) * mm});
            skLineSegment(sketch, "E1711", {"start": v(4.23, 0.24) * mm, "end": v(4.22, 0.26) * mm});
            skLineSegment(sketch, "E1712", {"start": v(4.22, 0.26) * mm, "end": v(4.21, 0.28) * mm});
            skLineSegment(sketch, "E1713", {"start": v(4.21, 0.28) * mm, "end": v(4.2, 0.3) * mm});
            skLineSegment(sketch, "E1714", {"start": v(4.2, 0.3) * mm, "end": v(4.2, 0.31) * mm});
            skLineSegment(sketch, "E1715", {"start": v(4.2, 0.31) * mm, "end": v(4.19, 0.33) * mm});
            skLineSegment(sketch, "E1716", {"start": v(4.19, 0.33) * mm, "end": v(4.18, 0.35) * mm});
            skLineSegment(sketch, "E1717", {"start": v(4.18, 0.35) * mm, "end": v(4.17, 0.36) * mm});
            skLineSegment(sketch, "E1718", {"start": v(4.17, 0.36) * mm, "end": v(4.16, 0.38) * mm});
            skLineSegment(sketch, "E1719", {"start": v(4.16, 0.38) * mm, "end": v(4.15, 0.4) * mm});
            skLineSegment(sketch, "E1720", {"start": v(4.15, 0.4) * mm, "end": v(4.14, 0.42) * mm});
            skLineSegment(sketch, "E1721", {"start": v(4.14, 0.42) * mm, "end": v(4.13, 0.44) * mm});
            skLineSegment(sketch, "E1722", {"start": v(4.13, 0.44) * mm, "end": v(4.12, 0.45) * mm});
            skLineSegment(sketch, "E1723", {"start": v(4.12, 0.45) * mm, "end": v(4.1, 0.47) * mm});
            skLineSegment(sketch, "E1724", {"start": v(4.1, 0.47) * mm, "end": v(4.1, 0.49) * mm});
            skLineSegment(sketch, "E1725", {"start": v(4.1, 0.49) * mm, "end": v(4.09, 0.5) * mm});
            skLineSegment(sketch, "E1726", {"start": v(4.09, 0.5) * mm, "end": v(4.08, 0.52) * mm});
            skLineSegment(sketch, "E1727", {"start": v(4.08, 0.52) * mm, "end": v(4.06, 0.54) * mm});
            skLineSegment(sketch, "E1728", {"start": v(4.06, 0.54) * mm, "end": v(4.05, 0.56) * mm});
            skLineSegment(sketch, "E1729", {"start": v(4.05, 0.56) * mm, "end": v(4.04, 0.58) * mm});
            skLineSegment(sketch, "E1730", {"start": v(4.04, 0.58) * mm, "end": v(4.03, 0.6) * mm});
            skLineSegment(sketch, "E1731", {"start": v(4.03, 0.6) * mm, "end": v(4.02, 0.61) * mm});
            skLineSegment(sketch, "E1732", {"start": v(4.02, 0.61) * mm, "end": v(4, 0.63) * mm});
            skLineSegment(sketch, "E1733", {"start": v(4, 0.63) * mm, "end": v(4, 0.65) * mm});
            skLineSegment(sketch, "E1734", {"start": v(4, 0.65) * mm, "end": v(3.98, 0.67) * mm});
            skLineSegment(sketch, "E1735", {"start": v(3.98, 0.67) * mm, "end": v(3.97, 0.69) * mm});
            skLineSegment(sketch, "E1736", {"start": v(3.97, 0.69) * mm, "end": v(3.95, 0.7) * mm});
            skLineSegment(sketch, "E1737", {"start": v(3.95, 0.7) * mm, "end": v(3.94, 0.72) * mm});
            skLineSegment(sketch, "E1738", {"start": v(3.94, 0.72) * mm, "end": v(3.92, 0.74) * mm});
            skLineSegment(sketch, "E1739", {"start": v(3.92, 0.74) * mm, "end": v(3.91, 0.76) * mm});
            skLineSegment(sketch, "E1740", {"start": v(3.91, 0.76) * mm, "end": v(3.9, 0.78) * mm});
            skLineSegment(sketch, "E1741", {"start": v(3.9, 0.78) * mm, "end": v(3.88, 0.8) * mm});
            skLineSegment(sketch, "E1742", {"start": v(3.88, 0.8) * mm, "end": v(3.87, 0.81) * mm});
            skLineSegment(sketch, "E1743", {"start": v(3.87, 0.81) * mm, "end": v(3.85, 0.83) * mm});
            skLineSegment(sketch, "E1744", {"start": v(3.85, 0.83) * mm, "end": v(3.84, 0.85) * mm});
            skLineSegment(sketch, "E1745", {"start": v(3.84, 0.85) * mm, "end": v(3.82, 0.87) * mm});
            skLineSegment(sketch, "E1746", {"start": v(3.82, 0.87) * mm, "end": v(3.8, 0.89) * mm});
            skLineSegment(sketch, "E1747", {"start": v(3.8, 0.89) * mm, "end": v(3.79, 0.9) * mm});
            skLineSegment(sketch, "E1748", {"start": v(3.79, 0.9) * mm, "end": v(3.77, 0.92) * mm});
            skLineSegment(sketch, "E1749", {"start": v(3.77, 0.92) * mm, "end": v(3.76, 0.94) * mm});
            skLineSegment(sketch, "E1750", {"start": v(3.76, 0.94) * mm, "end": v(3.74, 0.96) * mm});
            skLineSegment(sketch, "E1751", {"start": v(3.74, 0.96) * mm, "end": v(3.72, 0.98) * mm});
            skLineSegment(sketch, "E1752", {"start": v(3.72, 0.98) * mm, "end": v(3.7, 1) * mm});
            skLineSegment(sketch, "E1753", {"start": v(3.7, 1) * mm, "end": v(3.69, 1.01) * mm});
            skLineSegment(sketch, "E1754", {"start": v(3.69, 1.01) * mm, "end": v(3.67, 1.03) * mm});
            skLineSegment(sketch, "E1755", {"start": v(3.67, 1.03) * mm, "end": v(3.65, 1.05) * mm});
            skLineSegment(sketch, "E1756", {"start": v(3.65, 1.05) * mm, "end": v(3.63, 1.07) * mm});
            skLineSegment(sketch, "E1757", {"start": v(3.63, 1.07) * mm, "end": v(3.62, 1.09) * mm});
            skLineSegment(sketch, "E1758", {"start": v(3.62, 1.09) * mm, "end": v(3.6, 1.1) * mm});
            skLineSegment(sketch, "E1759", {"start": v(3.6, 1.1) * mm, "end": v(3.58, 1.12) * mm});
            skLineSegment(sketch, "E1760", {"start": v(3.58, 1.12) * mm, "end": v(3.56, 1.14) * mm});
            skLineSegment(sketch, "E1761", {"start": v(3.56, 1.14) * mm, "end": v(3.54, 1.16) * mm});
            skLineSegment(sketch, "E1762", {"start": v(3.54, 1.16) * mm, "end": v(3.52, 1.17) * mm});
            skLineSegment(sketch, "E1763", {"start": v(3.52, 1.17) * mm, "end": v(3.5, 1.19) * mm});
            skLineSegment(sketch, "E1764", {"start": v(3.5, 1.19) * mm, "end": v(3.49, 1.2) * mm});
            skLineSegment(sketch, "E1765", {"start": v(3.49, 1.2) * mm, "end": v(3.47, 1.22) * mm});
            skLineSegment(sketch, "E1766", {"start": v(3.47, 1.22) * mm, "end": v(3.45, 1.24) * mm});
            skLineSegment(sketch, "E1767", {"start": v(3.45, 1.24) * mm, "end": v(3.43, 1.25) * mm});
            skLineSegment(sketch, "E1768", {"start": v(3.43, 1.25) * mm, "end": v(3.41, 1.27) * mm});
            skLineSegment(sketch, "E1769", {"start": v(3.41, 1.27) * mm, "end": v(3.4, 1.28) * mm});
            skLineSegment(sketch, "E1770", {"start": v(3.4, 1.28) * mm, "end": v(3.38, 1.3) * mm});
            skLineSegment(sketch, "E1771", {"start": v(3.38, 1.3) * mm, "end": v(3.36, 1.31) * mm});
            skLineSegment(sketch, "E1772", {"start": v(3.36, 1.31) * mm, "end": v(3.34, 1.32) * mm});
            skLineSegment(sketch, "E1773", {"start": v(3.34, 1.32) * mm, "end": v(3.32, 1.34) * mm});
            skLineSegment(sketch, "E1774", {"start": v(3.32, 1.34) * mm, "end": v(3.3, 1.35) * mm});
            skLineSegment(sketch, "E1775", {"start": v(3.3, 1.35) * mm, "end": v(3.29, 1.37) * mm});
            skLineSegment(sketch, "E1776", {"start": v(3.29, 1.37) * mm, "end": v(3.27, 1.38) * mm});
            skLineSegment(sketch, "E1777", {"start": v(3.27, 1.38) * mm, "end": v(3.25, 1.4) * mm});
            skLineSegment(sketch, "E1778", {"start": v(3.25, 1.4) * mm, "end": v(3.23, 1.4) * mm});
            skLineSegment(sketch, "E1779", {"start": v(3.23, 1.4) * mm, "end": v(3.21, 1.42) * mm});
            skLineSegment(sketch, "E1780", {"start": v(3.21, 1.42) * mm, "end": v(3.2, 1.43) * mm});
            skLineSegment(sketch, "E1781", {"start": v(3.2, 1.43) * mm, "end": v(3.18, 1.44) * mm});
            skLineSegment(sketch, "E1782", {"start": v(3.18, 1.44) * mm, "end": v(3.16, 1.45) * mm});
            skLineSegment(sketch, "E1783", {"start": v(3.16, 1.45) * mm, "end": v(3.14, 1.46) * mm});
            skLineSegment(sketch, "E1784", {"start": v(3.14, 1.46) * mm, "end": v(3.12, 1.48) * mm});
            skLineSegment(sketch, "E1785", {"start": v(3.12, 1.48) * mm, "end": v(3.1, 1.49) * mm});
            skLineSegment(sketch, "E1786", {"start": v(3.1, 1.49) * mm, "end": v(3.09, 1.5) * mm});
            skLineSegment(sketch, "E1787", {"start": v(3.09, 1.5) * mm, "end": v(3.07, 1.5) * mm});
            skLineSegment(sketch, "E1788", {"start": v(3.07, 1.5) * mm, "end": v(3.05, 1.52) * mm});
            skLineSegment(sketch, "E1789", {"start": v(3.05, 1.52) * mm, "end": v(3.04, 1.53) * mm});
            skLineSegment(sketch, "E1790", {"start": v(3.04, 1.53) * mm, "end": v(3.02, 1.54) * mm});
            skLineSegment(sketch, "E1791", {"start": v(3.02, 1.54) * mm, "end": v(3, 1.55) * mm});
            skLineSegment(sketch, "E1792", {"start": v(3, 1.55) * mm, "end": v(2.98, 1.56) * mm});
            skLineSegment(sketch, "E1793", {"start": v(2.98, 1.56) * mm, "end": v(2.97, 1.57) * mm});
            skLineSegment(sketch, "E1794", {"start": v(2.97, 1.57) * mm, "end": v(2.95, 1.58) * mm});
            skLineSegment(sketch, "E1795", {"start": v(2.95, 1.58) * mm, "end": v(2.93, 1.59) * mm});
            skLineSegment(sketch, "E1796", {"start": v(2.93, 1.59) * mm, "end": v(2.91, 1.6) * mm});
            skLineSegment(sketch, "E1797", {"start": v(2.91, 1.6) * mm, "end": v(2.9, 1.6) * mm});
            skLineSegment(sketch, "E1798", {"start": v(2.9, 1.6) * mm, "end": v(2.88, 1.61) * mm});
            skLineSegment(sketch, "E1799", {"start": v(2.88, 1.61) * mm, "end": v(2.86, 1.62) * mm});
            skLineSegment(sketch, "E1800", {"start": v(2.86, 1.62) * mm, "end": v(2.84, 1.63) * mm});
            skLineSegment(sketch, "E1801", {"start": v(2.84, 1.63) * mm, "end": v(2.83, 1.63) * mm});
            skLineSegment(sketch, "E1802", {"start": v(2.83, 1.63) * mm, "end": v(2.81, 1.64) * mm});
            skLineSegment(sketch, "E1803", {"start": v(2.81, 1.64) * mm, "end": v(2.8, 1.65) * mm});
            skLineSegment(sketch, "E1804", {"start": v(2.8, 1.65) * mm, "end": v(2.78, 1.65) * mm});
            skLineSegment(sketch, "E1805", {"start": v(2.78, 1.65) * mm, "end": v(2.76, 1.66) * mm});
            skLineSegment(sketch, "E1806", {"start": v(2.76, 1.66) * mm, "end": v(2.74, 1.66) * mm});
            skLineSegment(sketch, "E1807", {"start": v(2.74, 1.66) * mm, "end": v(2.73, 1.67) * mm});
            skLineSegment(sketch, "E1808", {"start": v(2.73, 1.67) * mm, "end": v(2.71, 1.68) * mm});
            skLineSegment(sketch, "E1809", {"start": v(2.71, 1.68) * mm, "end": v(2.7, 1.68) * mm});
            skLineSegment(sketch, "E1810", {"start": v(2.7, 1.68) * mm, "end": v(2.68, 1.68) * mm});
            skLineSegment(sketch, "E1811", {"start": v(2.68, 1.68) * mm, "end": v(2.67, 1.69) * mm});
            skLineSegment(sketch, "E1812", {"start": v(2.67, 1.69) * mm, "end": v(2.65, 1.7) * mm});
            skLineSegment(sketch, "E1813", {"start": v(2.65, 1.7) * mm, "end": v(2.64, 1.7) * mm});
            skLineSegment(sketch, "E1814", {"start": v(2.64, 1.7) * mm, "end": v(2.63, 1.7) * mm});
            skLineSegment(sketch, "E1815", {"start": v(2.63, 1.7) * mm, "end": v(2.61, 1.7) * mm});
            skLineSegment(sketch, "E1816", {"start": v(2.61, 1.7) * mm, "end": v(2.6, 1.7) * mm});
            skLineSegment(sketch, "E1817", {"start": v(2.6, 1.7) * mm, "end": v(2.6, 1.7) * mm});
            skLineSegment(sketch, "E1818", {"start": v(2.6, 1.7) * mm, "end": v(2.58, 1.7) * mm});
            skLineSegment(sketch, "E1819", {"start": v(2.58, 1.7) * mm, "end": v(2.57, 1.7) * mm});
            skLineSegment(sketch, "E1820", {"start": v(2.57, 1.7) * mm, "end": v(2.56, 1.7) * mm});
            skLineSegment(sketch, "E1821", {"start": v(2.56, 1.7) * mm, "end": v(2.54, 1.69) * mm});
            skLineSegment(sketch, "E1822", {"start": v(2.54, 1.69) * mm, "end": v(2.53, 1.68) * mm});
            skLineSegment(sketch, "E1823", {"start": v(2.53, 1.68) * mm, "end": v(2.51, 1.68) * mm});
            skLineSegment(sketch, "E1824", {"start": v(2.51, 1.68) * mm, "end": v(2.5, 1.68) * mm});
            skLineSegment(sketch, "E1825", {"start": v(2.5, 1.68) * mm, "end": v(2.48, 1.67) * mm});
            skLineSegment(sketch, "E1826", {"start": v(2.48, 1.67) * mm, "end": v(2.46, 1.66) * mm});
            skLineSegment(sketch, "E1827", {"start": v(2.46, 1.66) * mm, "end": v(2.45, 1.66) * mm});
            skLineSegment(sketch, "E1828", {"start": v(2.45, 1.66) * mm, "end": v(2.43, 1.65) * mm});
            skLineSegment(sketch, "E1829", {"start": v(2.43, 1.65) * mm, "end": v(2.41, 1.65) * mm});
            skLineSegment(sketch, "E1830", {"start": v(2.41, 1.65) * mm, "end": v(2.4, 1.64) * mm});
            skLineSegment(sketch, "E1831", {"start": v(2.4, 1.64) * mm, "end": v(2.38, 1.63) * mm});
            skLineSegment(sketch, "E1832", {"start": v(2.38, 1.63) * mm, "end": v(2.36, 1.63) * mm});
            skLineSegment(sketch, "E1833", {"start": v(2.36, 1.63) * mm, "end": v(2.35, 1.62) * mm});
            skLineSegment(sketch, "E1834", {"start": v(2.35, 1.62) * mm, "end": v(2.33, 1.61) * mm});
            skLineSegment(sketch, "E1835", {"start": v(2.33, 1.61) * mm, "end": v(2.31, 1.6) * mm});
            skLineSegment(sketch, "E1836", {"start": v(2.31, 1.6) * mm, "end": v(2.3, 1.6) * mm});
            skLineSegment(sketch, "E1837", {"start": v(2.3, 1.6) * mm, "end": v(2.28, 1.59) * mm});
            skLineSegment(sketch, "E1838", {"start": v(2.28, 1.59) * mm, "end": v(2.26, 1.58) * mm});
            skLineSegment(sketch, "E1839", {"start": v(2.26, 1.58) * mm, "end": v(2.24, 1.57) * mm});
            skLineSegment(sketch, "E1840", {"start": v(2.24, 1.57) * mm, "end": v(2.23, 1.56) * mm});
            skLineSegment(sketch, "E1841", {"start": v(2.23, 1.56) * mm, "end": v(2.2, 1.55) * mm});
            skLineSegment(sketch, "E1842", {"start": v(2.2, 1.55) * mm, "end": v(2.2, 1.54) * mm});
            skLineSegment(sketch, "E1843", {"start": v(2.2, 1.54) * mm, "end": v(2.17, 1.53) * mm});
            skLineSegment(sketch, "E1844", {"start": v(2.17, 1.53) * mm, "end": v(2.15, 1.52) * mm});
            skLineSegment(sketch, "E1845", {"start": v(2.15, 1.52) * mm, "end": v(2.14, 1.5) * mm});
            skLineSegment(sketch, "E1846", {"start": v(2.14, 1.5) * mm, "end": v(2.12, 1.5) * mm});
            skLineSegment(sketch, "E1847", {"start": v(2.12, 1.5) * mm, "end": v(2.1, 1.49) * mm});
            skLineSegment(sketch, "E1848", {"start": v(2.1, 1.49) * mm, "end": v(2.08, 1.48) * mm});
            skLineSegment(sketch, "E1849", {"start": v(2.08, 1.48) * mm, "end": v(2.07, 1.46) * mm});
            skLineSegment(sketch, "E1850", {"start": v(2.07, 1.46) * mm, "end": v(2.05, 1.45) * mm});
            skLineSegment(sketch, "E1851", {"start": v(2.05, 1.45) * mm, "end": v(2.03, 1.44) * mm});
            skLineSegment(sketch, "E1852", {"start": v(2.03, 1.44) * mm, "end": v(2.01, 1.43) * mm});
            skLineSegment(sketch, "E1853", {"start": v(2.01, 1.43) * mm, "end": v(2, 1.42) * mm});
            skLineSegment(sketch, "E1854", {"start": v(2, 1.42) * mm, "end": v(1.98, 1.4) * mm});
            skLineSegment(sketch, "E1855", {"start": v(1.98, 1.4) * mm, "end": v(1.96, 1.4) * mm});
            skLineSegment(sketch, "E1856", {"start": v(1.96, 1.4) * mm, "end": v(1.94, 1.38) * mm});
            skLineSegment(sketch, "E1857", {"start": v(1.94, 1.38) * mm, "end": v(1.92, 1.37) * mm});
            skLineSegment(sketch, "E1858", {"start": v(1.92, 1.37) * mm, "end": v(1.9, 1.35) * mm});
            skLineSegment(sketch, "E1859", {"start": v(1.9, 1.35) * mm, "end": v(1.89, 1.34) * mm});
            skLineSegment(sketch, "E1860", {"start": v(1.89, 1.34) * mm, "end": v(1.87, 1.32) * mm});
            skLineSegment(sketch, "E1861", {"start": v(1.87, 1.32) * mm, "end": v(1.85, 1.31) * mm});
            skLineSegment(sketch, "E1862", {"start": v(1.85, 1.31) * mm, "end": v(1.83, 1.3) * mm});
            skLineSegment(sketch, "E1863", {"start": v(1.83, 1.3) * mm, "end": v(1.81, 1.28) * mm});
            skLineSegment(sketch, "E1864", {"start": v(1.81, 1.28) * mm, "end": v(1.8, 1.27) * mm});
            skLineSegment(sketch, "E1865", {"start": v(1.8, 1.27) * mm, "end": v(1.78, 1.25) * mm});
            skLineSegment(sketch, "E1866", {"start": v(1.78, 1.25) * mm, "end": v(1.76, 1.24) * mm});
            skLineSegment(sketch, "E1867", {"start": v(1.76, 1.24) * mm, "end": v(1.74, 1.22) * mm});
            skLineSegment(sketch, "E1868", {"start": v(1.74, 1.22) * mm, "end": v(1.72, 1.2) * mm});
            skLineSegment(sketch, "E1869", {"start": v(1.72, 1.2) * mm, "end": v(1.7, 1.19) * mm});
            skLineSegment(sketch, "E1870", {"start": v(1.7, 1.19) * mm, "end": v(1.68, 1.17) * mm});
            skLineSegment(sketch, "E1871", {"start": v(1.68, 1.17) * mm, "end": v(1.67, 1.16) * mm});
            skLineSegment(sketch, "E1872", {"start": v(1.67, 1.16) * mm, "end": v(1.65, 1.14) * mm});
            skLineSegment(sketch, "E1873", {"start": v(1.65, 1.14) * mm, "end": v(1.63, 1.12) * mm});
            skLineSegment(sketch, "E1874", {"start": v(1.63, 1.12) * mm, "end": v(1.61, 1.1) * mm});
            skLineSegment(sketch, "E1875", {"start": v(1.61, 1.1) * mm, "end": v(1.6, 1.09) * mm});
            skLineSegment(sketch, "E1876", {"start": v(1.6, 1.09) * mm, "end": v(1.57, 1.07) * mm});
            skLineSegment(sketch, "E1877", {"start": v(1.57, 1.07) * mm, "end": v(1.56, 1.05) * mm});
            skLineSegment(sketch, "E1878", {"start": v(1.56, 1.05) * mm, "end": v(1.54, 1.03) * mm});
            skLineSegment(sketch, "E1879", {"start": v(1.54, 1.03) * mm, "end": v(1.52, 1.01) * mm});
            skLineSegment(sketch, "E1880", {"start": v(1.52, 1.01) * mm, "end": v(1.5, 1) * mm});
            skLineSegment(sketch, "E1881", {"start": v(1.5, 1) * mm, "end": v(1.49, 0.98) * mm});
            skLineSegment(sketch, "E1882", {"start": v(1.49, 0.98) * mm, "end": v(1.47, 0.96) * mm});
            skLineSegment(sketch, "E1883", {"start": v(1.47, 0.96) * mm, "end": v(1.45, 0.94) * mm});
            skLineSegment(sketch, "E1884", {"start": v(1.45, 0.94) * mm, "end": v(1.44, 0.92) * mm});
            skLineSegment(sketch, "E1885", {"start": v(1.44, 0.92) * mm, "end": v(1.42, 0.9) * mm});
            skLineSegment(sketch, "E1886", {"start": v(1.42, 0.9) * mm, "end": v(1.4, 0.89) * mm});
            skLineSegment(sketch, "E1887", {"start": v(1.4, 0.89) * mm, "end": v(1.39, 0.87) * mm});
            skLineSegment(sketch, "E1888", {"start": v(1.39, 0.87) * mm, "end": v(1.37, 0.85) * mm});
            skLineSegment(sketch, "E1889", {"start": v(1.37, 0.85) * mm, "end": v(1.36, 0.83) * mm});
            skLineSegment(sketch, "E1890", {"start": v(1.36, 0.83) * mm, "end": v(1.34, 0.81) * mm});
            skLineSegment(sketch, "E1891", {"start": v(1.34, 0.81) * mm, "end": v(1.33, 0.8) * mm});
            skLineSegment(sketch, "E1892", {"start": v(1.33, 0.8) * mm, "end": v(1.31, 0.78) * mm});
            skLineSegment(sketch, "E1893", {"start": v(1.31, 0.78) * mm, "end": v(1.3, 0.76) * mm});
            skLineSegment(sketch, "E1894", {"start": v(1.3, 0.76) * mm, "end": v(1.28, 0.74) * mm});
            skLineSegment(sketch, "E1895", {"start": v(1.28, 0.74) * mm, "end": v(1.27, 0.72) * mm});
            skLineSegment(sketch, "E1896", {"start": v(1.27, 0.72) * mm, "end": v(1.26, 0.7) * mm});
            skLineSegment(sketch, "E1897", {"start": v(1.26, 0.7) * mm, "end": v(1.24, 0.69) * mm});
            skLineSegment(sketch, "E1898", {"start": v(1.24, 0.69) * mm, "end": v(1.23, 0.67) * mm});
            skLineSegment(sketch, "E1899", {"start": v(1.23, 0.67) * mm, "end": v(1.22, 0.65) * mm});
            skLineSegment(sketch, "E1900", {"start": v(1.22, 0.65) * mm, "end": v(1.2, 0.63) * mm});
            skLineSegment(sketch, "E1901", {"start": v(1.2, 0.63) * mm, "end": v(1.2, 0.61) * mm});
            skLineSegment(sketch, "E1902", {"start": v(1.2, 0.61) * mm, "end": v(1.18, 0.6) * mm});
            skLineSegment(sketch, "E1903", {"start": v(1.18, 0.6) * mm, "end": v(1.17, 0.58) * mm});
            skLineSegment(sketch, "E1904", {"start": v(1.17, 0.58) * mm, "end": v(1.16, 0.56) * mm});
            skLineSegment(sketch, "E1905", {"start": v(1.16, 0.56) * mm, "end": v(1.14, 0.54) * mm});
            skLineSegment(sketch, "E1906", {"start": v(1.14, 0.54) * mm, "end": v(1.13, 0.52) * mm});
            skLineSegment(sketch, "E1907", {"start": v(1.13, 0.52) * mm, "end": v(1.12, 0.5) * mm});
            skLineSegment(sketch, "E1908", {"start": v(1.12, 0.5) * mm, "end": v(1.11, 0.49) * mm});
            skLineSegment(sketch, "E1909", {"start": v(1.11, 0.49) * mm, "end": v(1.1, 0.47) * mm});
            skLineSegment(sketch, "E1910", {"start": v(1.1, 0.47) * mm, "end": v(1.09, 0.45) * mm});
            skLineSegment(sketch, "E1911", {"start": v(1.09, 0.45) * mm, "end": v(1.08, 0.44) * mm});
            skLineSegment(sketch, "E1912", {"start": v(1.08, 0.44) * mm, "end": v(1.07, 0.42) * mm});
            skLineSegment(sketch, "E1913", {"start": v(1.07, 0.42) * mm, "end": v(1.06, 0.4) * mm});
            skLineSegment(sketch, "E1914", {"start": v(1.06, 0.4) * mm, "end": v(1.05, 0.38) * mm});
            skLineSegment(sketch, "E1915", {"start": v(1.05, 0.38) * mm, "end": v(1.04, 0.36) * mm});
            skLineSegment(sketch, "E1916", {"start": v(1.04, 0.36) * mm, "end": v(1.03, 0.35) * mm});
            skLineSegment(sketch, "E1917", {"start": v(1.03, 0.35) * mm, "end": v(1.02, 0.33) * mm});
            skLineSegment(sketch, "E1918", {"start": v(1.02, 0.33) * mm, "end": v(1.01, 0.31) * mm});
            skLineSegment(sketch, "E1919", {"start": v(1.01, 0.31) * mm, "end": v(1, 0.3) * mm});
            skLineSegment(sketch, "E1920", {"start": v(1, 0.3) * mm, "end": v(1, 0.28) * mm});
            skLineSegment(sketch, "E1921", {"start": v(1, 0.28) * mm, "end": v(0.99, 0.26) * mm});
            skLineSegment(sketch, "E1922", {"start": v(0.99, 0.26) * mm, "end": v(0.98, 0.24) * mm});
            skLineSegment(sketch, "E1923", {"start": v(0.98, 0.24) * mm, "end": v(0.98, 0.23) * mm});
            skLineSegment(sketch, "E1924", {"start": v(0.98, 0.23) * mm, "end": v(0.97, 0.21) * mm});
            skLineSegment(sketch, "E1925", {"start": v(0.97, 0.21) * mm, "end": v(0.96, 0.2) * mm});
            skLineSegment(sketch, "E1926", {"start": v(0.96, 0.2) * mm, "end": v(0.96, 0.18) * mm});
            skLineSegment(sketch, "E1927", {"start": v(0.96, 0.18) * mm, "end": v(0.95, 0.16) * mm});
            skLineSegment(sketch, "E1928", {"start": v(0.95, 0.16) * mm, "end": v(0.94, 0.14) * mm});
            skLineSegment(sketch, "E1929", {"start": v(0.94, 0.14) * mm, "end": v(0.94, 0.13) * mm});
            skLineSegment(sketch, "E1930", {"start": v(0.94, 0.13) * mm, "end": v(0.93, 0.11) * mm});
            skLineSegment(sketch, "E1931", {"start": v(0.93, 0.11) * mm, "end": v(0.93, 0.1) * mm});
            skLineSegment(sketch, "E1932", {"start": v(0.93, 0.1) * mm, "end": v(0.92, 0.08) * mm});
            skLineSegment(sketch, "E1933", {"start": v(0.92, 0.08) * mm, "end": v(0.92, 0.07) * mm});
            skLineSegment(sketch, "E1934", {"start": v(0.92, 0.07) * mm, "end": v(0.92, 0.05) * mm});
            skLineSegment(sketch, "E1935", {"start": v(0.92, 0.05) * mm, "end": v(0.91, 0.04) * mm});
            skLineSegment(sketch, "E1936", {"start": v(0.91, 0.04) * mm, "end": v(0.9, 0.02) * mm});
            skLineSegment(sketch, "E1937", {"start": v(0.9, 0.02) * mm, "end": v(0.9, 0.01) * mm});
            skLineSegment(sketch, "E1938", {"start": v(0.9, 0.01) * mm, "end": v(0.9, 0) * mm});
            skLineSegment(sketch, "E1939", {"start": v(0.9, 0) * mm, "end": v(0.9, 0) * mm});
            skLineSegment(sketch, "E1940", {"start": v(0.9, 0) * mm, "end": v(0.9, -0.02) * mm});
            skLineSegment(sketch, "E1941", {"start": v(0.9, -0.02) * mm, "end": v(0.91, -0.03) * mm});
            skLineSegment(sketch, "E1942", {"start": v(0.91, -0.03) * mm, "end": v(0.92, -0.04) * mm});
            skLineSegment(sketch, "E1943", {"start": v(0.92, -0.04) * mm, "end": v(0.92, -0.06) * mm});
            skLineSegment(sketch, "E1944", {"start": v(0.92, -0.06) * mm, "end": v(0.92, -0.07) * mm});
            skLineSegment(sketch, "E1945", {"start": v(0.92, -0.07) * mm, "end": v(0.93, -0.09) * mm});
            skLineSegment(sketch, "E1946", {"start": v(0.93, -0.09) * mm, "end": v(0.93, -0.1) * mm});
            skLineSegment(sketch, "E1947", {"start": v(0.93, -0.1) * mm, "end": v(0.94, -0.12) * mm});
            skLineSegment(sketch, "E1948", {"start": v(0.94, -0.12) * mm, "end": v(0.94, -0.14) * mm});
            skLineSegment(sketch, "E1949", {"start": v(0.94, -0.14) * mm, "end": v(0.95, -0.15) * mm});
            skLineSegment(sketch, "E1950", {"start": v(0.95, -0.15) * mm, "end": v(0.96, -0.17) * mm});
            skLineSegment(sketch, "E1951", {"start": v(0.96, -0.17) * mm, "end": v(0.96, -0.19) * mm});
            skLineSegment(sketch, "E1952", {"start": v(0.96, -0.19) * mm, "end": v(0.97, -0.2) * mm});
            skLineSegment(sketch, "E1953", {"start": v(0.97, -0.2) * mm, "end": v(0.98, -0.22) * mm});
            skLineSegment(sketch, "E1954", {"start": v(0.98, -0.22) * mm, "end": v(0.98, -0.24) * mm});
            skLineSegment(sketch, "E1955", {"start": v(0.98, -0.24) * mm, "end": v(0.99, -0.25) * mm});
            skLineSegment(sketch, "E1956", {"start": v(0.99, -0.25) * mm, "end": v(1, -0.27) * mm});
            skLineSegment(sketch, "E1957", {"start": v(1, -0.27) * mm, "end": v(1, -0.29) * mm});
            skLineSegment(sketch, "E1958", {"start": v(1, -0.29) * mm, "end": v(1.01, -0.3) * mm});
            skLineSegment(sketch, "E1959", {"start": v(1.01, -0.3) * mm, "end": v(1.02, -0.32) * mm});
            skLineSegment(sketch, "E1960", {"start": v(1.02, -0.32) * mm, "end": v(1.03, -0.34) * mm});
            skLineSegment(sketch, "E1961", {"start": v(1.03, -0.34) * mm, "end": v(1.04, -0.36) * mm});
            skLineSegment(sketch, "E1962", {"start": v(1.04, -0.36) * mm, "end": v(1.05, -0.37) * mm});
            skLineSegment(sketch, "E1963", {"start": v(1.05, -0.37) * mm, "end": v(1.06, -0.4) * mm});
            skLineSegment(sketch, "E1964", {"start": v(1.06, -0.4) * mm, "end": v(1.07, -0.41) * mm});
            skLineSegment(sketch, "E1965", {"start": v(1.07, -0.41) * mm, "end": v(1.08, -0.43) * mm});
            skLineSegment(sketch, "E1966", {"start": v(1.08, -0.43) * mm, "end": v(1.09, -0.45) * mm});
            skLineSegment(sketch, "E1967", {"start": v(1.09, -0.45) * mm, "end": v(1.1, -0.46) * mm});
            skLineSegment(sketch, "E1968", {"start": v(1.1, -0.46) * mm, "end": v(1.11, -0.48) * mm});
            skLineSegment(sketch, "E1969", {"start": v(1.11, -0.48) * mm, "end": v(1.12, -0.5) * mm});
            skLineSegment(sketch, "E1970", {"start": v(1.12, -0.5) * mm, "end": v(1.13, -0.52) * mm});
            skLineSegment(sketch, "E1971", {"start": v(1.13, -0.52) * mm, "end": v(1.14, -0.53) * mm});
            skLineSegment(sketch, "E1972", {"start": v(1.14, -0.53) * mm, "end": v(1.16, -0.55) * mm});
            skLineSegment(sketch, "E1973", {"start": v(1.16, -0.55) * mm, "end": v(1.17, -0.57) * mm});
            skLineSegment(sketch, "E1974", {"start": v(1.17, -0.57) * mm, "end": v(1.18, -0.59) * mm});
            skLineSegment(sketch, "E1975", {"start": v(1.18, -0.59) * mm, "end": v(1.2, -0.6) * mm});
            skLineSegment(sketch, "E1976", {"start": v(1.2, -0.6) * mm, "end": v(1.2, -0.62) * mm});
            skLineSegment(sketch, "E1977", {"start": v(1.2, -0.62) * mm, "end": v(1.22, -0.64) * mm});
            skLineSegment(sketch, "E1978", {"start": v(1.22, -0.64) * mm, "end": v(1.23, -0.66) * mm});
            skLineSegment(sketch, "E1979", {"start": v(1.23, -0.66) * mm, "end": v(1.24, -0.68) * mm});
            skLineSegment(sketch, "E1980", {"start": v(1.24, -0.68) * mm, "end": v(1.26, -0.7) * mm});
            skLineSegment(sketch, "E1981", {"start": v(1.26, -0.7) * mm, "end": v(1.27, -0.72) * mm});
            skLineSegment(sketch, "E1982", {"start": v(1.27, -0.72) * mm, "end": v(1.28, -0.73) * mm});
            skLineSegment(sketch, "E1983", {"start": v(1.28, -0.73) * mm, "end": v(1.3, -0.75) * mm});
            skLineSegment(sketch, "E1984", {"start": v(1.3, -0.75) * mm, "end": v(1.31, -0.77) * mm});
            skLineSegment(sketch, "E1985", {"start": v(1.31, -0.77) * mm, "end": v(1.33, -0.79) * mm});
            skLineSegment(sketch, "E1986", {"start": v(1.33, -0.79) * mm, "end": v(1.34, -0.8) * mm});
            skLineSegment(sketch, "E1987", {"start": v(1.34, -0.8) * mm, "end": v(1.36, -0.82) * mm});
            skLineSegment(sketch, "E1988", {"start": v(1.36, -0.82) * mm, "end": v(1.37, -0.84) * mm});
            skLineSegment(sketch, "E1989", {"start": v(1.37, -0.84) * mm, "end": v(1.39, -0.86) * mm});
            skLineSegment(sketch, "E1990", {"start": v(1.39, -0.86) * mm, "end": v(1.4, -0.88) * mm});
            skLineSegment(sketch, "E1991", {"start": v(1.4, -0.88) * mm, "end": v(1.42, -0.9) * mm});
            skLineSegment(sketch, "E1992", {"start": v(1.42, -0.9) * mm, "end": v(1.42, -0.9) * mm});
            skLineSegment(sketch, "E1993", {"start": v(1.42, -0.9) * mm, "end": v(2.05, -0.27) * mm});
            skLineSegment(sketch, "E1994", {"start": v(2.05, -0.27) * mm, "end": v(2.34, -0.55) * mm});
            skLineSegment(sketch, "E1995", {"start": v(2.34, -0.55) * mm, "end": v(1.7, -1.18) * mm});
            skLineSegment(sketch, "E1996", {"start": v(-0.46, -1.08) * mm, "end": v(-0.46, -1) * mm});
            skLineSegment(sketch, "E1997", {"start": v(-0.46, -1) * mm, "end": v(-0.45, -1.02) * mm});
            skLineSegment(sketch, "E1998", {"start": v(-0.45, -1.02) * mm, "end": v(-0.41, -1.04) * mm});
            skLineSegment(sketch, "E1999", {"start": v(-0.41, -1.04) * mm, "end": v(-0.38, -1.06) * mm});
            skLineSegment(sketch, "E2000", {"start": v(-0.38, -1.06) * mm, "end": v(-0.34, -1.07) * mm});
            skLineSegment(sketch, "E2001", {"start": v(-0.34, -1.07) * mm, "end": v(-0.3, -1.08) * mm});
            skLineSegment(sketch, "E2002", {"start": v(-0.3, -1.08) * mm, "end": v(-0.27, -1.1) * mm});
            skLineSegment(sketch, "E2003", {"start": v(-0.27, -1.1) * mm, "end": v(-0.23, -1.1) * mm});
            skLineSegment(sketch, "E2004", {"start": v(-0.23, -1.1) * mm, "end": v(-0.19, -1.1) * mm});
            skLineSegment(sketch, "E2005", {"start": v(-0.19, -1.1) * mm, "end": v(-0.15, -1.11) * mm});
            skLineSegment(sketch, "E2006", {"start": v(-0.15, -1.11) * mm, "end": v(-0.1, -1.11) * mm});
            skLineSegment(sketch, "E2007", {"start": v(-0.1, -1.11) * mm, "end": v(-0.07, -1.11) * mm});
            skLineSegment(sketch, "E2008", {"start": v(-0.07, -1.11) * mm, "end": v(-0.03, -1.1) * mm});
            skLineSegment(sketch, "E2009", {"start": v(-0.03, -1.1) * mm, "end": v(0, -1.1) * mm});
            skLineSegment(sketch, "E2010", {"start": v(0, -1.1) * mm, "end": v(0.04, -1.1) * mm});
            skLineSegment(sketch, "E2011", {"start": v(0.04, -1.1) * mm, "end": v(0.07, -1.1) * mm});
            skLineSegment(sketch, "E2012", {"start": v(0.07, -1.1) * mm, "end": v(0.1, -1.08) * mm});
            skLineSegment(sketch, "E2013", {"start": v(0.1, -1.08) * mm, "end": v(0.14, -1.07) * mm});
            skLineSegment(sketch, "E2014", {"start": v(0.14, -1.07) * mm, "end": v(0.18, -1.06) * mm});
            skLineSegment(sketch, "E2015", {"start": v(0.18, -1.06) * mm, "end": v(0.2, -1.04) * mm});
            skLineSegment(sketch, "E2016", {"start": v(0.2, -1.04) * mm, "end": v(0.24, -1.02) * mm});
            skLineSegment(sketch, "E2017", {"start": v(0.24, -1.02) * mm, "end": v(0.26, -1) * mm});
            skLineSegment(sketch, "E2018", {"start": v(0.26, -1) * mm, "end": v(0.3, -0.99) * mm});
            skLineSegment(sketch, "E2019", {"start": v(0.3, -0.99) * mm, "end": v(0.32, -0.97) * mm});
            skLineSegment(sketch, "E2020", {"start": v(0.32, -0.97) * mm, "end": v(0.34, -0.95) * mm});
            skLineSegment(sketch, "E2021", {"start": v(0.34, -0.95) * mm, "end": v(0.36, -0.92) * mm});
            skLineSegment(sketch, "E2022", {"start": v(0.36, -0.92) * mm, "end": v(0.38, -0.9) * mm});
            skLineSegment(sketch, "E2023", {"start": v(0.38, -0.9) * mm, "end": v(0.4, -0.87) * mm});
            skLineSegment(sketch, "E2024", {"start": v(0.4, -0.87) * mm, "end": v(0.41, -0.85) * mm});
            skLineSegment(sketch, "E2025", {"start": v(0.41, -0.85) * mm, "end": v(0.43, -0.82) * mm});
            skLineSegment(sketch, "E2026", {"start": v(0.43, -0.82) * mm, "end": v(0.44, -0.8) * mm});
            skLineSegment(sketch, "E2027", {"start": v(0.44, -0.8) * mm, "end": v(0.45, -0.77) * mm});
            skLineSegment(sketch, "E2028", {"start": v(0.45, -0.77) * mm, "end": v(0.46, -0.74) * mm});
            skLineSegment(sketch, "E2029", {"start": v(0.46, -0.74) * mm, "end": v(0.47, -0.7) * mm});
            skLineSegment(sketch, "E2030", {"start": v(0.47, -0.7) * mm, "end": v(0.47, -0.68) * mm});
            skLineSegment(sketch, "E2031", {"start": v(0.47, -0.68) * mm, "end": v(0.48, -0.65) * mm});
            skLineSegment(sketch, "E2032", {"start": v(0.48, -0.65) * mm, "end": v(0.48, -0.63) * mm});
            skLineSegment(sketch, "E2033", {"start": v(0.48, -0.63) * mm, "end": v(0.48, -0.6) * mm});
            skLineSegment(sketch, "E2034", {"start": v(0.48, -0.6) * mm, "end": v(0.49, -0.57) * mm});
            skLineSegment(sketch, "E2035", {"start": v(0.49, -0.57) * mm, "end": v(0.49, -0.54) * mm});
            skLineSegment(sketch, "E2036", {"start": v(0.49, -0.54) * mm, "end": v(0.49, -0.5) * mm});
            skLineSegment(sketch, "E2037", {"start": v(0.49, -0.5) * mm, "end": v(0.5, -0.47) * mm});
            skLineSegment(sketch, "E2038", {"start": v(0.5, -0.47) * mm, "end": v(0.5, -0.43) * mm});
            skLineSegment(sketch, "E2039", {"start": v(0.5, -0.43) * mm, "end": v(0.5, 0.57) * mm});
            skLineSegment(sketch, "E2040", {"start": v(0.5, 0.57) * mm, "end": v(0.04, 0.57) * mm});
            skLineSegment(sketch, "E2041", {"start": v(0.04, 0.57) * mm, "end": v(0.04, -0.33) * mm});
            skLineSegment(sketch, "E2042", {"start": v(0.04, -0.33) * mm, "end": v(0.04, -0.36) * mm});
            skLineSegment(sketch, "E2043", {"start": v(0.04, -0.36) * mm, "end": v(0.04, -0.38) * mm});
            skLineSegment(sketch, "E2044", {"start": v(0.04, -0.38) * mm, "end": v(0.04, -0.4) * mm});
            skLineSegment(sketch, "E2045", {"start": v(0.04, -0.4) * mm, "end": v(0.04, -0.42) * mm});
            skLineSegment(sketch, "E2046", {"start": v(0.04, -0.42) * mm, "end": v(0.04, -0.44) * mm});
            skLineSegment(sketch, "E2047", {"start": v(0.04, -0.44) * mm, "end": v(0.04, -0.46) * mm});
            skLineSegment(sketch, "E2048", {"start": v(0.04, -0.46) * mm, "end": v(0.04, -0.47) * mm});
            skLineSegment(sketch, "E2049", {"start": v(0.04, -0.47) * mm, "end": v(0.04, -0.49) * mm});
            skLineSegment(sketch, "E2050", {"start": v(0.04, -0.49) * mm, "end": v(0.04, -0.5) * mm});
            skLineSegment(sketch, "E2051", {"start": v(0.04, -0.5) * mm, "end": v(0.04, -0.52) * mm});
            skLineSegment(sketch, "E2052", {"start": v(0.04, -0.52) * mm, "end": v(0.04, -0.53) * mm});
            skLineSegment(sketch, "E2053", {"start": v(0.04, -0.53) * mm, "end": v(0.04, -0.54) * mm});
            skLineSegment(sketch, "E2054", {"start": v(0.04, -0.54) * mm, "end": v(0.04, -0.55) * mm});
            skLineSegment(sketch, "E2055", {"start": v(0.04, -0.55) * mm, "end": v(0.03, -0.56) * mm});
            skLineSegment(sketch, "E2056", {"start": v(0.03, -0.56) * mm, "end": v(0.03, -0.57) * mm});
            skLineSegment(sketch, "E2057", {"start": v(0.03, -0.57) * mm, "end": v(0.03, -0.57) * mm});
            skLineSegment(sketch, "E2058", {"start": v(0.03, -0.57) * mm, "end": v(0.03, -0.59) * mm});
            skLineSegment(sketch, "E2059", {"start": v(0.03, -0.59) * mm, "end": v(0.02, -0.6) * mm});
            skLineSegment(sketch, "E2060", {"start": v(0.02, -0.6) * mm, "end": v(0.02, -0.61) * mm});
            skLineSegment(sketch, "E2061", {"start": v(0.02, -0.61) * mm, "end": v(0, -0.63) * mm});
            skLineSegment(sketch, "E2062", {"start": v(0, -0.63) * mm, "end": v(0, -0.64) * mm});
            skLineSegment(sketch, "E2063", {"start": v(0, -0.64) * mm, "end": v(0, -0.65) * mm});
            skLineSegment(sketch, "E2064", {"start": v(0, -0.65) * mm, "end": v(-0.02, -0.66) * mm});
            skLineSegment(sketch, "E2065", {"start": v(-0.02, -0.66) * mm, "end": v(-0.03, -0.67) * mm});
            skLineSegment(sketch, "E2066", {"start": v(-0.03, -0.67) * mm, "end": v(-0.04, -0.67) * mm});
            skLineSegment(sketch, "E2067", {"start": v(-0.04, -0.67) * mm, "end": v(-0.05, -0.68) * mm});
            skLineSegment(sketch, "E2068", {"start": v(-0.05, -0.68) * mm, "end": v(-0.07, -0.69) * mm});
            skLineSegment(sketch, "E2069", {"start": v(-0.07, -0.69) * mm, "end": v(-0.08, -0.7) * mm});
            skLineSegment(sketch, "E2070", {"start": v(-0.08, -0.7) * mm, "end": v(-0.1, -0.7) * mm});
            skLineSegment(sketch, "E2071", {"start": v(-0.1, -0.7) * mm, "end": v(-0.11, -0.7) * mm});
            skLineSegment(sketch, "E2072", {"start": v(-0.11, -0.7) * mm, "end": v(-0.13, -0.7) * mm});
            skLineSegment(sketch, "E2073", {"start": v(-0.13, -0.7) * mm, "end": v(-0.15, -0.7) * mm});
            skLineSegment(sketch, "E2074", {"start": v(-0.15, -0.7) * mm, "end": v(-0.17, -0.7) * mm});
            skLineSegment(sketch, "E2075", {"start": v(-0.17, -0.7) * mm, "end": v(-0.2, -0.7) * mm});
            skLineSegment(sketch, "E2076", {"start": v(-0.2, -0.7) * mm, "end": v(-0.21, -0.7) * mm});
            skLineSegment(sketch, "E2077", {"start": v(-0.21, -0.7) * mm, "end": v(-0.23, -0.7) * mm});
            skLineSegment(sketch, "E2078", {"start": v(-0.23, -0.7) * mm, "end": v(-0.25, -0.68) * mm});
            skLineSegment(sketch, "E2079", {"start": v(-0.25, -0.68) * mm, "end": v(-0.27, -0.68) * mm});
            skLineSegment(sketch, "E2080", {"start": v(-0.27, -0.68) * mm, "end": v(-0.3, -0.67) * mm});
            skLineSegment(sketch, "E2081", {"start": v(-0.3, -0.67) * mm, "end": v(-0.31, -0.66) * mm});
            skLineSegment(sketch, "E2082", {"start": v(-0.31, -0.66) * mm, "end": v(-0.33, -0.65) * mm});
            skLineSegment(sketch, "E2083", {"start": v(-0.33, -0.65) * mm, "end": v(-0.34, -0.64) * mm});
            skLineSegment(sketch, "E2084", {"start": v(-0.34, -0.64) * mm, "end": v(-0.36, -0.62) * mm});
            skLineSegment(sketch, "E2085", {"start": v(-0.36, -0.62) * mm, "end": v(-0.37, -0.61) * mm});
            skLineSegment(sketch, "E2086", {"start": v(-0.37, -0.61) * mm, "end": v(-0.38, -0.6) * mm});
            skLineSegment(sketch, "E2087", {"start": v(-0.38, -0.6) * mm, "end": v(-0.39, -0.58) * mm});
            skLineSegment(sketch, "E2088", {"start": v(-0.39, -0.58) * mm, "end": v(-0.4, -0.57) * mm});
            skLineSegment(sketch, "E2089", {"start": v(-0.4, -0.57) * mm, "end": v(-0.4, -0.55) * mm});
            skLineSegment(sketch, "E2090", {"start": v(-0.4, -0.55) * mm, "end": v(-0.41, -0.53) * mm});
            skLineSegment(sketch, "E2091", {"start": v(-0.41, -0.53) * mm, "end": v(-0.42, -0.51) * mm});
            skLineSegment(sketch, "E2092", {"start": v(-0.42, -0.51) * mm, "end": v(-0.42, -0.49) * mm});
            skLineSegment(sketch, "E2093", {"start": v(-0.42, -0.49) * mm, "end": v(-0.43, -0.46) * mm});
            skLineSegment(sketch, "E2094", {"start": v(-0.43, -0.46) * mm, "end": v(-0.43, -0.42) * mm});
            skLineSegment(sketch, "E2095", {"start": v(-0.43, -0.42) * mm, "end": v(-0.44, -0.39) * mm});
            skLineSegment(sketch, "E2096", {"start": v(-0.44, -0.39) * mm, "end": v(-0.44, -0.35) * mm});
            skLineSegment(sketch, "E2097", {"start": v(-0.44, -0.35) * mm, "end": v(-0.44, -0.3) * mm});
            skLineSegment(sketch, "E2098", {"start": v(-0.44, -0.3) * mm, "end": v(-0.44, 0.57) * mm});
            skLineSegment(sketch, "E2099", {"start": v(-0.44, 0.57) * mm, "end": v(-0.88, 0.57) * mm});
            skLineSegment(sketch, "E2100", {"start": v(-0.88, 0.57) * mm, "end": v(-0.88, -1.08) * mm});
            skLineSegment(sketch, "E2101", {"start": v(-0.88, -1.08) * mm, "end": v(-0.46, -1.08) * mm});
            skLineSegment(sketch, "E2102", {"start": v(-1.07, -1.08) * mm, "end": v(-1.07, 0.57) * mm});
            skLineSegment(sketch, "E2103", {"start": v(-1.07, 0.57) * mm, "end": v(-1.52, 0.57) * mm});
            skLineSegment(sketch, "E2104", {"start": v(-1.52, 0.57) * mm, "end": v(-1.52, -1.08) * mm});
            skLineSegment(sketch, "E2105", {"start": v(-1.52, -1.08) * mm, "end": v(-1.07, -1.08) * mm});
            skLineSegment(sketch, "E2106", {"start": v(-1.07, 0.64) * mm, "end": v(-1.07, 1.12) * mm});
            skLineSegment(sketch, "E2107", {"start": v(-1.07, 1.12) * mm, "end": v(-1.52, 1.12) * mm});
            skLineSegment(sketch, "E2108", {"start": v(-1.52, 1.12) * mm, "end": v(-1.52, 0.64) * mm});
            skLineSegment(sketch, "E2109", {"start": v(-1.52, 0.64) * mm, "end": v(-1.07, 0.64) * mm});
            skLineSegment(sketch, "E2110", {"start": v(-1.69, -1.08) * mm, "end": v(-1.69, 0.57) * mm});
            skLineSegment(sketch, "E2111", {"start": v(-1.69, 0.57) * mm, "end": v(-2.1, 0.57) * mm});
            skLineSegment(sketch, "E2112", {"start": v(-2.1, 0.57) * mm, "end": v(-2.1, 0.54) * mm});
            skLineSegment(sketch, "E2113", {"start": v(-2.1, 0.54) * mm, "end": v(-2.13, 0.55) * mm});
            skLineSegment(sketch, "E2114", {"start": v(-2.13, 0.55) * mm, "end": v(-2.16, 0.56) * mm});
            skLineSegment(sketch, "E2115", {"start": v(-2.16, 0.56) * mm, "end": v(-2.18, 0.58) * mm});
            skLineSegment(sketch, "E2116", {"start": v(-2.18, 0.58) * mm, "end": v(-2.2, 0.58) * mm});
            skLineSegment(sketch, "E2117", {"start": v(-2.2, 0.58) * mm, "end": v(-2.24, 0.6) * mm});
            skLineSegment(sketch, "E2118", {"start": v(-2.24, 0.6) * mm, "end": v(-2.26, 0.6) * mm});
            skLineSegment(sketch, "E2119", {"start": v(-2.26, 0.6) * mm, "end": v(-2.3, 0.6) * mm});
            skLineSegment(sketch, "E2120", {"start": v(-2.3, 0.6) * mm, "end": v(-2.32, 0.6) * mm});
            skLineSegment(sketch, "E2121", {"start": v(-2.32, 0.6) * mm, "end": v(-2.36, 0.6) * mm});
            skLineSegment(sketch, "E2122", {"start": v(-2.36, 0.6) * mm, "end": v(-2.4, 0.6) * mm});
            skLineSegment(sketch, "E2123", {"start": v(-2.4, 0.6) * mm, "end": v(-2.44, 0.59) * mm});
            skLineSegment(sketch, "E2124", {"start": v(-2.44, 0.59) * mm, "end": v(-2.48, 0.58) * mm});
            skLineSegment(sketch, "E2125", {"start": v(-2.48, 0.58) * mm, "end": v(-2.51, 0.56) * mm});
            skLineSegment(sketch, "E2126", {"start": v(-2.51, 0.56) * mm, "end": v(-2.55, 0.55) * mm});
            skLineSegment(sketch, "E2127", {"start": v(-2.55, 0.55) * mm, "end": v(-2.59, 0.53) * mm});
            skLineSegment(sketch, "E2128", {"start": v(-2.59, 0.53) * mm, "end": v(-2.7, 0.47) * mm});
            skLineSegment(sketch, "E2129", {"start": v(-2.7, 0.47) * mm, "end": v(-2.54, 0.05) * mm});
            skLineSegment(sketch, "E2130", {"start": v(-2.54, 0.05) * mm, "end": v(-2.42, 0.12) * mm});
            skLineSegment(sketch, "E2131", {"start": v(-2.42, 0.12) * mm, "end": v(-2.4, 0.13) * mm});
            skLineSegment(sketch, "E2132", {"start": v(-2.4, 0.13) * mm, "end": v(-2.39, 0.13) * mm});
            skLineSegment(sketch, "E2133", {"start": v(-2.39, 0.13) * mm, "end": v(-2.37, 0.14) * mm});
            skLineSegment(sketch, "E2134", {"start": v(-2.37, 0.14) * mm, "end": v(-2.36, 0.14) * mm});
            skLineSegment(sketch, "E2135", {"start": v(-2.36, 0.14) * mm, "end": v(-2.34, 0.15) * mm});
            skLineSegment(sketch, "E2136", {"start": v(-2.34, 0.15) * mm, "end": v(-2.32, 0.15) * mm});
            skLineSegment(sketch, "E2137", {"start": v(-2.32, 0.15) * mm, "end": v(-2.3, 0.15) * mm});
            skLineSegment(sketch, "E2138", {"start": v(-2.3, 0.15) * mm, "end": v(-2.3, 0.15) * mm});
            skLineSegment(sketch, "E2139", {"start": v(-2.3, 0.15) * mm, "end": v(-2.29, 0.15) * mm});
            skLineSegment(sketch, "E2140", {"start": v(-2.29, 0.15) * mm, "end": v(-2.28, 0.14) * mm});
            skLineSegment(sketch, "E2141", {"start": v(-2.28, 0.14) * mm, "end": v(-2.26, 0.14) * mm});
            skLineSegment(sketch, "E2142", {"start": v(-2.26, 0.14) * mm, "end": v(-2.25, 0.14) * mm});
            skLineSegment(sketch, "E2143", {"start": v(-2.25, 0.14) * mm, "end": v(-2.24, 0.13) * mm});
            skLineSegment(sketch, "E2144", {"start": v(-2.24, 0.13) * mm, "end": v(-2.23, 0.13) * mm});
            skLineSegment(sketch, "E2145", {"start": v(-2.23, 0.13) * mm, "end": v(-2.23, 0.12) * mm});
            skLineSegment(sketch, "E2146", {"start": v(-2.23, 0.12) * mm, "end": v(-2.22, 0.11) * mm});
            skLineSegment(sketch, "E2147", {"start": v(-2.22, 0.11) * mm, "end": v(-2.2, 0.1) * mm});
            skLineSegment(sketch, "E2148", {"start": v(-2.2, 0.1) * mm, "end": v(-2.2, 0.1) * mm});
            skLineSegment(sketch, "E2149", {"start": v(-2.2, 0.1) * mm, "end": v(-2.2, 0.09) * mm});
            skLineSegment(sketch, "E2150", {"start": v(-2.2, 0.09) * mm, "end": v(-2.19, 0.07) * mm});
            skLineSegment(sketch, "E2151", {"start": v(-2.19, 0.07) * mm, "end": v(-2.18, 0.06) * mm});
            skLineSegment(sketch, "E2152", {"start": v(-2.18, 0.06) * mm, "end": v(-2.17, 0.05) * mm});
            skLineSegment(sketch, "E2153", {"start": v(-2.17, 0.05) * mm, "end": v(-2.17, 0.03) * mm});
            skLineSegment(sketch, "E2154", {"start": v(-2.17, 0.03) * mm, "end": v(-2.16, 0) * mm});
            skLineSegment(sketch, "E2155", {"start": v(-2.16, 0) * mm, "end": v(-2.15, -0.02) * mm});
            skLineSegment(sketch, "E2156", {"start": v(-2.15, -0.02) * mm, "end": v(-2.15, -0.05) * mm});
            skLineSegment(sketch, "E2157", {"start": v(-2.15, -0.05) * mm, "end": v(-2.14, -0.09) * mm});
            skLineSegment(sketch, "E2158", {"start": v(-2.14, -0.09) * mm, "end": v(-2.14, -0.12) * mm});
            skLineSegment(sketch, "E2159", {"start": v(-2.14, -0.12) * mm, "end": v(-2.13, -0.15) * mm});
            skLineSegment(sketch, "E2160", {"start": v(-2.13, -0.15) * mm, "end": v(-2.13, -0.19) * mm});
            skLineSegment(sketch, "E2161", {"start": v(-2.13, -0.19) * mm, "end": v(-2.13, -0.22) * mm});
            skLineSegment(sketch, "E2162", {"start": v(-2.13, -0.22) * mm, "end": v(-2.13, -1.08) * mm});
            skLineSegment(sketch, "E2163", {"start": v(-2.13, -1.08) * mm, "end": v(-1.69, -1.08) * mm});
            skLineSegment(sketch, "E2164", {"start": v(-3.58, -0.34) * mm, "end": v(-4.02, -0.4) * mm});
            skLineSegment(sketch, "E2165", {"start": v(-4.02, -0.4) * mm, "end": v(-4, -0.53) * mm});
            skLineSegment(sketch, "E2166", {"start": v(-4, -0.53) * mm, "end": v(-4, -0.56) * mm});
            skLineSegment(sketch, "E2167", {"start": v(-4, -0.56) * mm, "end": v(-3.98, -0.6) * mm});
            skLineSegment(sketch, "E2168", {"start": v(-3.98, -0.6) * mm, "end": v(-3.97, -0.63) * mm});
            skLineSegment(sketch, "E2169", {"start": v(-3.97, -0.63) * mm, "end": v(-3.96, -0.66) * mm});
            skLineSegment(sketch, "E2170", {"start": v(-3.96, -0.66) * mm, "end": v(-3.95, -0.7) * mm});
            skLineSegment(sketch, "E2171", {"start": v(-3.95, -0.7) * mm, "end": v(-3.94, -0.72) * mm});
            skLineSegment(sketch, "E2172", {"start": v(-3.94, -0.72) * mm, "end": v(-3.93, -0.75) * mm});
            skLineSegment(sketch, "E2173", {"start": v(-3.93, -0.75) * mm, "end": v(-3.9, -0.78) * mm});
            skLineSegment(sketch, "E2174", {"start": v(-3.9, -0.78) * mm, "end": v(-3.9, -0.8) * mm});
            skLineSegment(sketch, "E2175", {"start": v(-3.9, -0.8) * mm, "end": v(-3.88, -0.83) * mm});
            skLineSegment(sketch, "E2176", {"start": v(-3.88, -0.83) * mm, "end": v(-3.86, -0.86) * mm});
            skLineSegment(sketch, "E2177", {"start": v(-3.86, -0.86) * mm, "end": v(-3.84, -0.88) * mm});
            skLineSegment(sketch, "E2178", {"start": v(-3.84, -0.88) * mm, "end": v(-3.82, -0.9) * mm});
            skLineSegment(sketch, "E2179", {"start": v(-3.82, -0.9) * mm, "end": v(-3.8, -0.93) * mm});
            skLineSegment(sketch, "E2180", {"start": v(-3.8, -0.93) * mm, "end": v(-3.77, -0.95) * mm});
            skLineSegment(sketch, "E2181", {"start": v(-3.77, -0.95) * mm, "end": v(-3.75, -0.97) * mm});
            skLineSegment(sketch, "E2182", {"start": v(-3.75, -0.97) * mm, "end": v(-3.72, -0.99) * mm});
            skLineSegment(sketch, "E2183", {"start": v(-3.72, -0.99) * mm, "end": v(-3.7, -1) * mm});
            skLineSegment(sketch, "E2184", {"start": v(-3.7, -1) * mm, "end": v(-3.67, -1.02) * mm});
            skLineSegment(sketch, "E2185", {"start": v(-3.67, -1.02) * mm, "end": v(-3.64, -1.03) * mm});
            skLineSegment(sketch, "E2186", {"start": v(-3.64, -1.03) * mm, "end": v(-3.61, -1.05) * mm});
            skLineSegment(sketch, "E2187", {"start": v(-3.61, -1.05) * mm, "end": v(-3.59, -1.06) * mm});
            skLineSegment(sketch, "E2188", {"start": v(-3.59, -1.06) * mm, "end": v(-3.56, -1.07) * mm});
            skLineSegment(sketch, "E2189", {"start": v(-3.56, -1.07) * mm, "end": v(-3.53, -1.08) * mm});
            skLineSegment(sketch, "E2190", {"start": v(-3.53, -1.08) * mm, "end": v(-3.5, -1.09) * mm});
            skLineSegment(sketch, "E2191", {"start": v(-3.5, -1.09) * mm, "end": v(-3.47, -1.1) * mm});
            skLineSegment(sketch, "E2192", {"start": v(-3.47, -1.1) * mm, "end": v(-3.43, -1.1) * mm});
            skLineSegment(sketch, "E2193", {"start": v(-3.43, -1.1) * mm, "end": v(-3.4, -1.1) * mm});
            skLineSegment(sketch, "E2194", {"start": v(-3.4, -1.1) * mm, "end": v(-3.37, -1.11) * mm});
            skLineSegment(sketch, "E2195", {"start": v(-3.37, -1.11) * mm, "end": v(-3.34, -1.11) * mm});
            skLineSegment(sketch, "E2196", {"start": v(-3.34, -1.11) * mm, "end": v(-3.3, -1.11) * mm});
            skLineSegment(sketch, "E2197", {"start": v(-3.3, -1.11) * mm, "end": v(-3.26, -1.11) * mm});
            skLineSegment(sketch, "E2198", {"start": v(-3.26, -1.11) * mm, "end": v(-3.22, -1.1) * mm});
            skLineSegment(sketch, "E2199", {"start": v(-3.22, -1.1) * mm, "end": v(-3.18, -1.1) * mm});
            skLineSegment(sketch, "E2200", {"start": v(-3.18, -1.1) * mm, "end": v(-3.14, -1.1) * mm});
            skLineSegment(sketch, "E2201", {"start": v(-3.14, -1.1) * mm, "end": v(-3.1, -1.1) * mm});
            skLineSegment(sketch, "E2202", {"start": v(-3.1, -1.1) * mm, "end": v(-3.07, -1.08) * mm});
            skLineSegment(sketch, "E2203", {"start": v(-3.07, -1.08) * mm, "end": v(-3.03, -1.07) * mm});
            skLineSegment(sketch, "E2204", {"start": v(-3.03, -1.07) * mm, "end": v(-3, -1.06) * mm});
            skLineSegment(sketch, "E2205", {"start": v(-3, -1.06) * mm, "end": v(-2.96, -1.04) * mm});
            skLineSegment(sketch, "E2206", {"start": v(-2.96, -1.04) * mm, "end": v(-2.93, -1.02) * mm});
            skLineSegment(sketch, "E2207", {"start": v(-2.93, -1.02) * mm, "end": v(-2.9, -1) * mm});
            skLineSegment(sketch, "E2208", {"start": v(-2.9, -1) * mm, "end": v(-2.87, -0.99) * mm});
            skLineSegment(sketch, "E2209", {"start": v(-2.87, -0.99) * mm, "end": v(-2.84, -0.96) * mm});
            skLineSegment(sketch, "E2210", {"start": v(-2.84, -0.96) * mm, "end": v(-2.8, -0.94) * mm});
            skLineSegment(sketch, "E2211", {"start": v(-2.8, -0.94) * mm, "end": v(-2.78, -0.91) * mm});
            skLineSegment(sketch, "E2212", {"start": v(-2.78, -0.91) * mm, "end": v(-2.75, -0.89) * mm});
            skLineSegment(sketch, "E2213", {"start": v(-2.75, -0.89) * mm, "end": v(-2.73, -0.86) * mm});
            skLineSegment(sketch, "E2214", {"start": v(-2.73, -0.86) * mm, "end": v(-2.7, -0.83) * mm});
            skLineSegment(sketch, "E2215", {"start": v(-2.7, -0.83) * mm, "end": v(-2.68, -0.8) * mm});
            skLineSegment(sketch, "E2216", {"start": v(-2.68, -0.8) * mm, "end": v(-2.66, -0.76) * mm});
            skLineSegment(sketch, "E2217", {"start": v(-2.66, -0.76) * mm, "end": v(-2.64, -0.73) * mm});
            skLineSegment(sketch, "E2218", {"start": v(-2.64, -0.73) * mm, "end": v(-2.62, -0.69) * mm});
            skLineSegment(sketch, "E2219", {"start": v(-2.62, -0.69) * mm, "end": v(-2.6, -0.65) * mm});
            skLineSegment(sketch, "E2220", {"start": v(-2.6, -0.65) * mm, "end": v(-2.6, -0.61) * mm});
            skLineSegment(sketch, "E2221", {"start": v(-2.6, -0.61) * mm, "end": v(-2.58, -0.57) * mm});
            skLineSegment(sketch, "E2222", {"start": v(-2.58, -0.57) * mm, "end": v(-2.57, -0.53) * mm});
            skLineSegment(sketch, "E2223", {"start": v(-2.57, -0.53) * mm, "end": v(-2.56, -0.49) * mm});
            skLineSegment(sketch, "E2224", {"start": v(-2.56, -0.49) * mm, "end": v(-2.56, -0.45) * mm});
            skLineSegment(sketch, "E2225", {"start": v(-2.56, -0.45) * mm, "end": v(-2.55, -0.4) * mm});
            skLineSegment(sketch, "E2226", {"start": v(-2.55, -0.4) * mm, "end": v(-2.55, -0.36) * mm});
            skLineSegment(sketch, "E2227", {"start": v(-2.55, -0.36) * mm, "end": v(-2.55, -0.3) * mm});
            skLineSegment(sketch, "E2228", {"start": v(-2.55, -0.3) * mm, "end": v(-2.54, -0.26) * mm});
            skLineSegment(sketch, "E2229", {"start": v(-2.54, -0.26) * mm, "end": v(-2.55, -0.2) * mm});
            skLineSegment(sketch, "E2230", {"start": v(-2.55, -0.2) * mm, "end": v(-2.55, -0.14) * mm});
            skLineSegment(sketch, "E2231", {"start": v(-2.55, -0.14) * mm, "end": v(-2.56, -0.08) * mm});
            skLineSegment(sketch, "E2232", {"start": v(-2.56, -0.08) * mm, "end": v(-2.57, -0.02) * mm});
            skLineSegment(sketch, "E2233", {"start": v(-2.57, -0.02) * mm, "end": v(-2.58, 0.03) * mm});
            skLineSegment(sketch, "E2234", {"start": v(-2.58, 0.03) * mm, "end": v(-2.6, 0.09) * mm});
            skLineSegment(sketch, "E2235", {"start": v(-2.6, 0.09) * mm, "end": v(-2.61, 0.14) * mm});
            skLineSegment(sketch, "E2236", {"start": v(-2.61, 0.14) * mm, "end": v(-2.63, 0.19) * mm});
            skLineSegment(sketch, "E2237", {"start": v(-2.63, 0.19) * mm, "end": v(-2.64, 0.21) * mm});
            skLineSegment(sketch, "E2238", {"start": v(-2.64, 0.21) * mm, "end": v(-2.66, 0.24) * mm});
            skLineSegment(sketch, "E2239", {"start": v(-2.66, 0.24) * mm, "end": v(-2.67, 0.26) * mm});
            skLineSegment(sketch, "E2240", {"start": v(-2.67, 0.26) * mm, "end": v(-2.68, 0.29) * mm});
            skLineSegment(sketch, "E2241", {"start": v(-2.68, 0.29) * mm, "end": v(-2.7, 0.3) * mm});
            skLineSegment(sketch, "E2242", {"start": v(-2.7, 0.3) * mm, "end": v(-2.71, 0.33) * mm});
            skLineSegment(sketch, "E2243", {"start": v(-2.71, 0.33) * mm, "end": v(-2.73, 0.35) * mm});
            skLineSegment(sketch, "E2244", {"start": v(-2.73, 0.35) * mm, "end": v(-2.75, 0.37) * mm});
            skLineSegment(sketch, "E2245", {"start": v(-2.75, 0.37) * mm, "end": v(-2.76, 0.39) * mm});
            skLineSegment(sketch, "E2246", {"start": v(-2.76, 0.39) * mm, "end": v(-2.78, 0.4) * mm});
            skLineSegment(sketch, "E2247", {"start": v(-2.78, 0.4) * mm, "end": v(-2.8, 0.43) * mm});
            skLineSegment(sketch, "E2248", {"start": v(-2.8, 0.43) * mm, "end": v(-2.82, 0.44) * mm});
            skLineSegment(sketch, "E2249", {"start": v(-2.82, 0.44) * mm, "end": v(-2.84, 0.46) * mm});
            skLineSegment(sketch, "E2250", {"start": v(-2.84, 0.46) * mm, "end": v(-2.87, 0.47) * mm});
            skLineSegment(sketch, "E2251", {"start": v(-2.87, 0.47) * mm, "end": v(-2.89, 0.49) * mm});
            skLineSegment(sketch, "E2252", {"start": v(-2.89, 0.49) * mm, "end": v(-2.91, 0.5) * mm});
            skLineSegment(sketch, "E2253", {"start": v(-2.91, 0.5) * mm, "end": v(-2.96, 0.52) * mm});
            skLineSegment(sketch, "E2254", {"start": v(-2.96, 0.52) * mm, "end": v(-3, 0.55) * mm});
            skLineSegment(sketch, "E2255", {"start": v(-3, 0.55) * mm, "end": v(-3.05, 0.56) * mm});
            skLineSegment(sketch, "E2256", {"start": v(-3.05, 0.56) * mm, "end": v(-3.1, 0.58) * mm});
            skLineSegment(sketch, "E2257", {"start": v(-3.1, 0.58) * mm, "end": v(-3.15, 0.59) * mm});
            skLineSegment(sketch, "E2258", {"start": v(-3.15, 0.59) * mm, "end": v(-3.2, 0.6) * mm});
            skLineSegment(sketch, "E2259", {"start": v(-3.2, 0.6) * mm, "end": v(-3.25, 0.6) * mm});
            skLineSegment(sketch, "E2260", {"start": v(-3.25, 0.6) * mm, "end": v(-3.3, 0.6) * mm});
            skLineSegment(sketch, "E2261", {"start": v(-3.3, 0.6) * mm, "end": v(-3.34, 0.6) * mm});
            skLineSegment(sketch, "E2262", {"start": v(-3.34, 0.6) * mm, "end": v(-3.37, 0.6) * mm});
            skLineSegment(sketch, "E2263", {"start": v(-3.37, 0.6) * mm, "end": v(-3.4, 0.6) * mm});
            skLineSegment(sketch, "E2264", {"start": v(-3.4, 0.6) * mm, "end": v(-3.43, 0.6) * mm});
            skLineSegment(sketch, "E2265", {"start": v(-3.43, 0.6) * mm, "end": v(-3.46, 0.59) * mm});
            skLineSegment(sketch, "E2266", {"start": v(-3.46, 0.59) * mm, "end": v(-3.5, 0.58) * mm});
            skLineSegment(sketch, "E2267", {"start": v(-3.5, 0.58) * mm, "end": v(-3.52, 0.58) * mm});
            skLineSegment(sketch, "E2268", {"start": v(-3.52, 0.58) * mm, "end": v(-3.55, 0.57) * mm});
            skLineSegment(sketch, "E2269", {"start": v(-3.55, 0.57) * mm, "end": v(-3.58, 0.56) * mm});
            skLineSegment(sketch, "E2270", {"start": v(-3.58, 0.56) * mm, "end": v(-3.6, 0.55) * mm});
            skLineSegment(sketch, "E2271", {"start": v(-3.6, 0.55) * mm, "end": v(-3.63, 0.54) * mm});
            skLineSegment(sketch, "E2272", {"start": v(-3.63, 0.54) * mm, "end": v(-3.66, 0.52) * mm});
            skLineSegment(sketch, "E2273", {"start": v(-3.66, 0.52) * mm, "end": v(-3.68, 0.5) * mm});
            skLineSegment(sketch, "E2274", {"start": v(-3.68, 0.5) * mm, "end": v(-3.7, 0.5) * mm});
            skLineSegment(sketch, "E2275", {"start": v(-3.7, 0.5) * mm, "end": v(-3.73, 0.48) * mm});
            skLineSegment(sketch, "E2276", {"start": v(-3.73, 0.48) * mm, "end": v(-3.75, 0.46) * mm});
            skLineSegment(sketch, "E2277", {"start": v(-3.75, 0.46) * mm, "end": v(-3.78, 0.44) * mm});
            skLineSegment(sketch, "E2278", {"start": v(-3.78, 0.44) * mm, "end": v(-3.8, 0.42) * mm});
            skLineSegment(sketch, "E2279", {"start": v(-3.8, 0.42) * mm, "end": v(-3.82, 0.4) * mm});
            skLineSegment(sketch, "E2280", {"start": v(-3.82, 0.4) * mm, "end": v(-3.84, 0.38) * mm});
            skLineSegment(sketch, "E2281", {"start": v(-3.84, 0.38) * mm, "end": v(-3.85, 0.36) * mm});
            skLineSegment(sketch, "E2282", {"start": v(-3.85, 0.36) * mm, "end": v(-3.87, 0.34) * mm});
            skLineSegment(sketch, "E2283", {"start": v(-3.87, 0.34) * mm, "end": v(-3.89, 0.31) * mm});
            skLineSegment(sketch, "E2284", {"start": v(-3.89, 0.31) * mm, "end": v(-3.9, 0.29) * mm});
            skLineSegment(sketch, "E2285", {"start": v(-3.9, 0.29) * mm, "end": v(-3.92, 0.26) * mm});
            skLineSegment(sketch, "E2286", {"start": v(-3.92, 0.26) * mm, "end": v(-3.93, 0.24) * mm});
            skLineSegment(sketch, "E2287", {"start": v(-3.93, 0.24) * mm, "end": v(-3.94, 0.2) * mm});
            skLineSegment(sketch, "E2288", {"start": v(-3.94, 0.2) * mm, "end": v(-3.95, 0.18) * mm});
            skLineSegment(sketch, "E2289", {"start": v(-3.95, 0.18) * mm, "end": v(-3.96, 0.15) * mm});
            skLineSegment(sketch, "E2290", {"start": v(-3.96, 0.15) * mm, "end": v(-3.97, 0.12) * mm});
            skLineSegment(sketch, "E2291", {"start": v(-3.97, 0.12) * mm, "end": v(-3.98, 0.1) * mm});
            skLineSegment(sketch, "E2292", {"start": v(-3.98, 0.1) * mm, "end": v(-4, -0.04) * mm});
            skLineSegment(sketch, "E2293", {"start": v(-4, -0.04) * mm, "end": v(-3.57, -0.1) * mm});
            skLineSegment(sketch, "E2294", {"start": v(-3.57, -0.1) * mm, "end": v(-3.54, 0.01) * mm});
            skLineSegment(sketch, "E2295", {"start": v(-3.54, 0.01) * mm, "end": v(-3.53, 0.04) * mm});
            skLineSegment(sketch, "E2296", {"start": v(-3.53, 0.04) * mm, "end": v(-3.52, 0.06) * mm});
            skLineSegment(sketch, "E2297", {"start": v(-3.52, 0.06) * mm, "end": v(-3.51, 0.09) * mm});
            skLineSegment(sketch, "E2298", {"start": v(-3.51, 0.09) * mm, "end": v(-3.5, 0.1) * mm});
            skLineSegment(sketch, "E2299", {"start": v(-3.5, 0.1) * mm, "end": v(-3.49, 0.12) * mm});
            skLineSegment(sketch, "E2300", {"start": v(-3.49, 0.12) * mm, "end": v(-3.47, 0.14) * mm});
            skLineSegment(sketch, "E2301", {"start": v(-3.47, 0.14) * mm, "end": v(-3.46, 0.15) * mm});
            skLineSegment(sketch, "E2302", {"start": v(-3.46, 0.15) * mm, "end": v(-3.44, 0.16) * mm});
            skLineSegment(sketch, "E2303", {"start": v(-3.44, 0.16) * mm, "end": v(-3.43, 0.17) * mm});
            skLineSegment(sketch, "E2304", {"start": v(-3.43, 0.17) * mm, "end": v(-3.41, 0.18) * mm});
            skLineSegment(sketch, "E2305", {"start": v(-3.41, 0.18) * mm, "end": v(-3.4, 0.19) * mm});
            skLineSegment(sketch, "E2306", {"start": v(-3.4, 0.19) * mm, "end": v(-3.38, 0.2) * mm});
            skLineSegment(sketch, "E2307", {"start": v(-3.38, 0.2) * mm, "end": v(-3.36, 0.2) * mm});
            skLineSegment(sketch, "E2308", {"start": v(-3.36, 0.2) * mm, "end": v(-3.34, 0.2) * mm});
            skLineSegment(sketch, "E2309", {"start": v(-3.34, 0.2) * mm, "end": v(-3.31, 0.2) * mm});
            skLineSegment(sketch, "E2310", {"start": v(-3.31, 0.2) * mm, "end": v(-3.3, 0.2) * mm});
            skLineSegment(sketch, "E2311", {"start": v(-3.3, 0.2) * mm, "end": v(-3.28, 0.2) * mm});
            skLineSegment(sketch, "E2312", {"start": v(-3.28, 0.2) * mm, "end": v(-3.26, 0.2) * mm});
            skLineSegment(sketch, "E2313", {"start": v(-3.26, 0.2) * mm, "end": v(-3.25, 0.2) * mm});
            skLineSegment(sketch, "E2314", {"start": v(-3.25, 0.2) * mm, "end": v(-3.23, 0.19) * mm});
            skLineSegment(sketch, "E2315", {"start": v(-3.23, 0.19) * mm, "end": v(-3.22, 0.19) * mm});
            skLineSegment(sketch, "E2316", {"start": v(-3.22, 0.19) * mm, "end": v(-3.2, 0.18) * mm});
            skLineSegment(sketch, "E2317", {"start": v(-3.2, 0.18) * mm, "end": v(-3.19, 0.17) * mm});
            skLineSegment(sketch, "E2318", {"start": v(-3.19, 0.17) * mm, "end": v(-3.17, 0.17) * mm});
            skLineSegment(sketch, "E2319", {"start": v(-3.17, 0.17) * mm, "end": v(-3.16, 0.16) * mm});
            skLineSegment(sketch, "E2320", {"start": v(-3.16, 0.16) * mm, "end": v(-3.15, 0.15) * mm});
            skLineSegment(sketch, "E2321", {"start": v(-3.15, 0.15) * mm, "end": v(-3.14, 0.14) * mm});
            skLineSegment(sketch, "E2322", {"start": v(-3.14, 0.14) * mm, "end": v(-3.12, 0.14) * mm});
            skLineSegment(sketch, "E2323", {"start": v(-3.12, 0.14) * mm, "end": v(-3.11, 0.12) * mm});
            skLineSegment(sketch, "E2324", {"start": v(-3.11, 0.12) * mm, "end": v(-3.1, 0.11) * mm});
            skLineSegment(sketch, "E2325", {"start": v(-3.1, 0.11) * mm, "end": v(-3.09, 0.1) * mm});
            skLineSegment(sketch, "E2326", {"start": v(-3.09, 0.1) * mm, "end": v(-3.08, 0.09) * mm});
            skLineSegment(sketch, "E2327", {"start": v(-3.08, 0.09) * mm, "end": v(-3.07, 0.08) * mm});
            skLineSegment(sketch, "E2328", {"start": v(-3.07, 0.08) * mm, "end": v(-3.06, 0.06) * mm});
            skLineSegment(sketch, "E2329", {"start": v(-3.06, 0.06) * mm, "end": v(-3.05, 0.05) * mm});
            skLineSegment(sketch, "E2330", {"start": v(-3.05, 0.05) * mm, "end": v(-3.04, 0.03) * mm});
            skLineSegment(sketch, "E2331", {"start": v(-3.04, 0.03) * mm, "end": v(-3.04, 0) * mm});
            skLineSegment(sketch, "E2332", {"start": v(-3.04, 0) * mm, "end": v(-3.03, -0.01) * mm});
            skLineSegment(sketch, "E2333", {"start": v(-3.03, -0.01) * mm, "end": v(-3.02, -0.03) * mm});
            skLineSegment(sketch, "E2334", {"start": v(-3.02, -0.03) * mm, "end": v(-3.02, -0.05) * mm});
            skLineSegment(sketch, "E2335", {"start": v(-3.02, -0.05) * mm, "end": v(-3.01, -0.08) * mm});
            skLineSegment(sketch, "E2336", {"start": v(-3.01, -0.08) * mm, "end": v(-3, -0.1) * mm});
            skLineSegment(sketch, "E2337", {"start": v(-3, -0.1) * mm, "end": v(-3, -0.13) * mm});
            skLineSegment(sketch, "E2338", {"start": v(-3, -0.13) * mm, "end": v(-3, -0.16) * mm});
            skLineSegment(sketch, "E2339", {"start": v(-3, -0.16) * mm, "end": v(-3, -0.2) * mm});
            skLineSegment(sketch, "E2340", {"start": v(-3, -0.2) * mm, "end": v(-3, -0.22) * mm});
            skLineSegment(sketch, "E2341", {"start": v(-3, -0.22) * mm, "end": v(-3, -0.25) * mm});
            skLineSegment(sketch, "E2342", {"start": v(-3, -0.25) * mm, "end": v(-3, -0.29) * mm});
            skLineSegment(sketch, "E2343", {"start": v(-3, -0.29) * mm, "end": v(-3, -0.32) * mm});
            skLineSegment(sketch, "E2344", {"start": v(-3, -0.32) * mm, "end": v(-3, -0.35) * mm});
            skLineSegment(sketch, "E2345", {"start": v(-3, -0.35) * mm, "end": v(-3, -0.38) * mm});
            skLineSegment(sketch, "E2346", {"start": v(-3, -0.38) * mm, "end": v(-3, -0.4) * mm});
            skLineSegment(sketch, "E2347", {"start": v(-3, -0.4) * mm, "end": v(-3.01, -0.43) * mm});
            skLineSegment(sketch, "E2348", {"start": v(-3.01, -0.43) * mm, "end": v(-3.02, -0.46) * mm});
            skLineSegment(sketch, "E2349", {"start": v(-3.02, -0.46) * mm, "end": v(-3.02, -0.48) * mm});
            skLineSegment(sketch, "E2350", {"start": v(-3.02, -0.48) * mm, "end": v(-3.03, -0.5) * mm});
            skLineSegment(sketch, "E2351", {"start": v(-3.03, -0.5) * mm, "end": v(-3.04, -0.52) * mm});
            skLineSegment(sketch, "E2352", {"start": v(-3.04, -0.52) * mm, "end": v(-3.04, -0.54) * mm});
            skLineSegment(sketch, "E2353", {"start": v(-3.04, -0.54) * mm, "end": v(-3.05, -0.56) * mm});
            skLineSegment(sketch, "E2354", {"start": v(-3.05, -0.56) * mm, "end": v(-3.06, -0.57) * mm});
            skLineSegment(sketch, "E2355", {"start": v(-3.06, -0.57) * mm, "end": v(-3.07, -0.59) * mm});
            skLineSegment(sketch, "E2356", {"start": v(-3.07, -0.59) * mm, "end": v(-3.08, -0.6) * mm});
            skLineSegment(sketch, "E2357", {"start": v(-3.08, -0.6) * mm, "end": v(-3.09, -0.61) * mm});
            skLineSegment(sketch, "E2358", {"start": v(-3.09, -0.61) * mm, "end": v(-3.1, -0.63) * mm});
            skLineSegment(sketch, "E2359", {"start": v(-3.1, -0.63) * mm, "end": v(-3.1, -0.64) * mm});
            skLineSegment(sketch, "E2360", {"start": v(-3.1, -0.64) * mm, "end": v(-3.12, -0.65) * mm});
            skLineSegment(sketch, "E2361", {"start": v(-3.12, -0.65) * mm, "end": v(-3.13, -0.66) * mm});
            skLineSegment(sketch, "E2362", {"start": v(-3.13, -0.66) * mm, "end": v(-3.14, -0.67) * mm});
            skLineSegment(sketch, "E2363", {"start": v(-3.14, -0.67) * mm, "end": v(-3.15, -0.67) * mm});
            skLineSegment(sketch, "E2364", {"start": v(-3.15, -0.67) * mm, "end": v(-3.17, -0.68) * mm});
            skLineSegment(sketch, "E2365", {"start": v(-3.17, -0.68) * mm, "end": v(-3.18, -0.69) * mm});
            skLineSegment(sketch, "E2366", {"start": v(-3.18, -0.69) * mm, "end": v(-3.2, -0.7) * mm});
            skLineSegment(sketch, "E2367", {"start": v(-3.2, -0.7) * mm, "end": v(-3.2, -0.7) * mm});
            skLineSegment(sketch, "E2368", {"start": v(-3.2, -0.7) * mm, "end": v(-3.22, -0.7) * mm});
            skLineSegment(sketch, "E2369", {"start": v(-3.22, -0.7) * mm, "end": v(-3.24, -0.7) * mm});
            skLineSegment(sketch, "E2370", {"start": v(-3.24, -0.7) * mm, "end": v(-3.25, -0.7) * mm});
            skLineSegment(sketch, "E2371", {"start": v(-3.25, -0.7) * mm, "end": v(-3.27, -0.7) * mm});
            skLineSegment(sketch, "E2372", {"start": v(-3.27, -0.7) * mm, "end": v(-3.28, -0.71) * mm});
            skLineSegment(sketch, "E2373", {"start": v(-3.28, -0.71) * mm, "end": v(-3.3, -0.71) * mm});
            skLineSegment(sketch, "E2374", {"start": v(-3.3, -0.71) * mm, "end": v(-3.33, -0.7) * mm});
            skLineSegment(sketch, "E2375", {"start": v(-3.33, -0.7) * mm, "end": v(-3.35, -0.7) * mm});
            skLineSegment(sketch, "E2376", {"start": v(-3.35, -0.7) * mm, "end": v(-3.38, -0.7) * mm});
            skLineSegment(sketch, "E2377", {"start": v(-3.38, -0.7) * mm, "end": v(-3.4, -0.7) * mm});
            skLineSegment(sketch, "E2378", {"start": v(-3.4, -0.7) * mm, "end": v(-3.42, -0.69) * mm});
            skLineSegment(sketch, "E2379", {"start": v(-3.42, -0.69) * mm, "end": v(-3.44, -0.68) * mm});
            skLineSegment(sketch, "E2380", {"start": v(-3.44, -0.68) * mm, "end": v(-3.46, -0.66) * mm});
            skLineSegment(sketch, "E2381", {"start": v(-3.46, -0.66) * mm, "end": v(-3.48, -0.65) * mm});
            skLineSegment(sketch, "E2382", {"start": v(-3.48, -0.65) * mm, "end": v(-3.48, -0.64) * mm});
            skLineSegment(sketch, "E2383", {"start": v(-3.48, -0.64) * mm, "end": v(-3.5, -0.63) * mm});
            skLineSegment(sketch, "E2384", {"start": v(-3.5, -0.63) * mm, "end": v(-3.5, -0.62) * mm});
            skLineSegment(sketch, "E2385", {"start": v(-3.5, -0.62) * mm, "end": v(-3.5, -0.61) * mm});
            skLineSegment(sketch, "E2386", {"start": v(-3.5, -0.61) * mm, "end": v(-3.51, -0.6) * mm});
            skLineSegment(sketch, "E2387", {"start": v(-3.51, -0.6) * mm, "end": v(-3.52, -0.6) * mm});
            skLineSegment(sketch, "E2388", {"start": v(-3.52, -0.6) * mm, "end": v(-3.52, -0.58) * mm});
            skLineSegment(sketch, "E2389", {"start": v(-3.52, -0.58) * mm, "end": v(-3.53, -0.57) * mm});
            skLineSegment(sketch, "E2390", {"start": v(-3.53, -0.57) * mm, "end": v(-3.54, -0.56) * mm});
            skLineSegment(sketch, "E2391", {"start": v(-3.54, -0.56) * mm, "end": v(-3.54, -0.54) * mm});
            skLineSegment(sketch, "E2392", {"start": v(-3.54, -0.54) * mm, "end": v(-3.55, -0.53) * mm});
            skLineSegment(sketch, "E2393", {"start": v(-3.55, -0.53) * mm, "end": v(-3.55, -0.5) * mm});
            skLineSegment(sketch, "E2394", {"start": v(-3.55, -0.5) * mm, "end": v(-3.56, -0.5) * mm});
            skLineSegment(sketch, "E2395", {"start": v(-3.56, -0.5) * mm, "end": v(-3.56, -0.47) * mm});
            skLineSegment(sketch, "E2396", {"start": v(-3.56, -0.47) * mm, "end": v(-3.56, -0.46) * mm});
            skLineSegment(sketch, "E2397", {"start": v(-3.56, -0.46) * mm, "end": v(-3.58, -0.34) * mm});
            skLineSegment(sketch, "E2398", {"start": v(-4.06, -1.08) * mm, "end": v(-4.06, 1.12) * mm});
            skLineSegment(sketch, "E2399", {"start": v(-4.06, 1.12) * mm, "end": v(-4.5, 1.12) * mm});
            skLineSegment(sketch, "E2400", {"start": v(-4.5, 1.12) * mm, "end": v(-4.5, -1.08) * mm});
            skLineSegment(sketch, "E2401", {"start": v(-4.5, -1.08) * mm, "end": v(-4.06, -1.08) * mm});
            skLineSegment(sketch, "E2402", {"start": v(-5.78, -0.42) * mm, "end": v(-6.11, -0.46) * mm});
            skLineSegment(sketch, "E2403", {"start": v(-6.11, -0.46) * mm, "end": v(-6.07, -0.6) * mm});
            skLineSegment(sketch, "E2404", {"start": v(-6.07, -0.6) * mm, "end": v(-6.06, -0.63) * mm});
            skLineSegment(sketch, "E2405", {"start": v(-6.06, -0.63) * mm, "end": v(-6.05, -0.66) * mm});
            skLineSegment(sketch, "E2406", {"start": v(-6.05, -0.66) * mm, "end": v(-6.04, -0.69) * mm});
            skLineSegment(sketch, "E2407", {"start": v(-6.04, -0.69) * mm, "end": v(-6.03, -0.72) * mm});
            skLineSegment(sketch, "E2408", {"start": v(-6.03, -0.72) * mm, "end": v(-6.01, -0.74) * mm});
            skLineSegment(sketch, "E2409", {"start": v(-6.01, -0.74) * mm, "end": v(-6, -0.77) * mm});
            skLineSegment(sketch, "E2410", {"start": v(-6, -0.77) * mm, "end": v(-5.98, -0.8) * mm});
            skLineSegment(sketch, "E2411", {"start": v(-5.98, -0.8) * mm, "end": v(-5.97, -0.82) * mm});
            skLineSegment(sketch, "E2412", {"start": v(-5.97, -0.82) * mm, "end": v(-5.95, -0.85) * mm});
            skLineSegment(sketch, "E2413", {"start": v(-5.95, -0.85) * mm, "end": v(-5.93, -0.87) * mm});
            skLineSegment(sketch, "E2414", {"start": v(-5.93, -0.87) * mm, "end": v(-5.9, -0.9) * mm});
            skLineSegment(sketch, "E2415", {"start": v(-5.9, -0.9) * mm, "end": v(-5.89, -0.91) * mm});
            skLineSegment(sketch, "E2416", {"start": v(-5.89, -0.91) * mm, "end": v(-5.87, -0.93) * mm});
            skLineSegment(sketch, "E2417", {"start": v(-5.87, -0.93) * mm, "end": v(-5.84, -0.95) * mm});
            skLineSegment(sketch, "E2418", {"start": v(-5.84, -0.95) * mm, "end": v(-5.82, -0.97) * mm});
            skLineSegment(sketch, "E2419", {"start": v(-5.82, -0.97) * mm, "end": v(-5.8, -0.99) * mm});
            skLineSegment(sketch, "E2420", {"start": v(-5.8, -0.99) * mm, "end": v(-5.77, -1) * mm});
            skLineSegment(sketch, "E2421", {"start": v(-5.77, -1) * mm, "end": v(-5.75, -1.02) * mm});
            skLineSegment(sketch, "E2422", {"start": v(-5.75, -1.02) * mm, "end": v(-5.72, -1.03) * mm});
            skLineSegment(sketch, "E2423", {"start": v(-5.72, -1.03) * mm, "end": v(-5.7, -1.05) * mm});
            skLineSegment(sketch, "E2424", {"start": v(-5.7, -1.05) * mm, "end": v(-5.66, -1.06) * mm});
            skLineSegment(sketch, "E2425", {"start": v(-5.66, -1.06) * mm, "end": v(-5.63, -1.07) * mm});
            skLineSegment(sketch, "E2426", {"start": v(-5.63, -1.07) * mm, "end": v(-5.6, -1.08) * mm});
            skLineSegment(sketch, "E2427", {"start": v(-5.6, -1.08) * mm, "end": v(-5.57, -1.09) * mm});
            skLineSegment(sketch, "E2428", {"start": v(-5.57, -1.09) * mm, "end": v(-5.54, -1.1) * mm});
            skLineSegment(sketch, "E2429", {"start": v(-5.54, -1.1) * mm, "end": v(-5.51, -1.1) * mm});
            skLineSegment(sketch, "E2430", {"start": v(-5.51, -1.1) * mm, "end": v(-5.48, -1.1) * mm});
            skLineSegment(sketch, "E2431", {"start": v(-5.48, -1.1) * mm, "end": v(-5.45, -1.1) * mm});
            skLineSegment(sketch, "E2432", {"start": v(-5.45, -1.1) * mm, "end": v(-5.41, -1.11) * mm});
            skLineSegment(sketch, "E2433", {"start": v(-5.41, -1.11) * mm, "end": v(-5.38, -1.11) * mm});
            skLineSegment(sketch, "E2434", {"start": v(-5.38, -1.11) * mm, "end": v(-5.35, -1.11) * mm});
            skLineSegment(sketch, "E2435", {"start": v(-5.35, -1.11) * mm, "end": v(-5.3, -1.11) * mm});
            skLineSegment(sketch, "E2436", {"start": v(-5.3, -1.11) * mm, "end": v(-5.26, -1.1) * mm});
            skLineSegment(sketch, "E2437", {"start": v(-5.26, -1.1) * mm, "end": v(-5.22, -1.1) * mm});
            skLineSegment(sketch, "E2438", {"start": v(-5.22, -1.1) * mm, "end": v(-5.18, -1.1) * mm});
            skLineSegment(sketch, "E2439", {"start": v(-5.18, -1.1) * mm, "end": v(-5.14, -1.1) * mm});
            skLineSegment(sketch, "E2440", {"start": v(-5.14, -1.1) * mm, "end": v(-5.1, -1.08) * mm});
            skLineSegment(sketch, "E2441", {"start": v(-5.1, -1.08) * mm, "end": v(-5.06, -1.07) * mm});
            skLineSegment(sketch, "E2442", {"start": v(-5.06, -1.07) * mm, "end": v(-5.02, -1.06) * mm});
            skLineSegment(sketch, "E2443", {"start": v(-5.02, -1.06) * mm, "end": v(-4.99, -1.04) * mm});
            skLineSegment(sketch, "E2444", {"start": v(-4.99, -1.04) * mm, "end": v(-4.95, -1.03) * mm});
            skLineSegment(sketch, "E2445", {"start": v(-4.95, -1.03) * mm, "end": v(-4.92, -1) * mm});
            skLineSegment(sketch, "E2446", {"start": v(-4.92, -1) * mm, "end": v(-4.89, -0.99) * mm});
            skLineSegment(sketch, "E2447", {"start": v(-4.89, -0.99) * mm, "end": v(-4.86, -0.96) * mm});
            skLineSegment(sketch, "E2448", {"start": v(-4.86, -0.96) * mm, "end": v(-4.83, -0.94) * mm});
            skLineSegment(sketch, "E2449", {"start": v(-4.83, -0.94) * mm, "end": v(-4.8, -0.91) * mm});
            skLineSegment(sketch, "E2450", {"start": v(-4.8, -0.91) * mm, "end": v(-4.77, -0.89) * mm});
            skLineSegment(sketch, "E2451", {"start": v(-4.77, -0.89) * mm, "end": v(-4.74, -0.86) * mm});
            skLineSegment(sketch, "E2452", {"start": v(-4.74, -0.86) * mm, "end": v(-4.72, -0.83) * mm});
            skLineSegment(sketch, "E2453", {"start": v(-4.72, -0.83) * mm, "end": v(-4.7, -0.8) * mm});
            skLineSegment(sketch, "E2454", {"start": v(-4.7, -0.8) * mm, "end": v(-4.67, -0.76) * mm});
            skLineSegment(sketch, "E2455", {"start": v(-4.67, -0.76) * mm, "end": v(-4.66, -0.73) * mm});
            skLineSegment(sketch, "E2456", {"start": v(-4.66, -0.73) * mm, "end": v(-4.64, -0.69) * mm});
            skLineSegment(sketch, "E2457", {"start": v(-4.64, -0.69) * mm, "end": v(-4.62, -0.65) * mm});
            skLineSegment(sketch, "E2458", {"start": v(-4.62, -0.65) * mm, "end": v(-4.6, -0.61) * mm});
            skLineSegment(sketch, "E2459", {"start": v(-4.6, -0.61) * mm, "end": v(-4.6, -0.57) * mm});
            skLineSegment(sketch, "E2460", {"start": v(-4.6, -0.57) * mm, "end": v(-4.58, -0.53) * mm});
            skLineSegment(sketch, "E2461", {"start": v(-4.58, -0.53) * mm, "end": v(-4.58, -0.5) * mm});
            skLineSegment(sketch, "E2462", {"start": v(-4.58, -0.5) * mm, "end": v(-4.57, -0.45) * mm});
            skLineSegment(sketch, "E2463", {"start": v(-4.57, -0.45) * mm, "end": v(-4.56, -0.4) * mm});
            skLineSegment(sketch, "E2464", {"start": v(-4.56, -0.4) * mm, "end": v(-4.56, -0.36) * mm});
            skLineSegment(sketch, "E2465", {"start": v(-4.56, -0.36) * mm, "end": v(-4.56, -0.31) * mm});
            skLineSegment(sketch, "E2466", {"start": v(-4.56, -0.31) * mm, "end": v(-4.56, -0.27) * mm});
            skLineSegment(sketch, "E2467", {"start": v(-4.56, -0.27) * mm, "end": v(-4.56, -0.22) * mm});
            skLineSegment(sketch, "E2468", {"start": v(-4.56, -0.22) * mm, "end": v(-4.56, -0.17) * mm});
            skLineSegment(sketch, "E2469", {"start": v(-4.56, -0.17) * mm, "end": v(-4.56, -0.13) * mm});
            skLineSegment(sketch, "E2470", {"start": v(-4.56, -0.13) * mm, "end": v(-4.57, -0.08) * mm});
            skLineSegment(sketch, "E2471", {"start": v(-4.57, -0.08) * mm, "end": v(-4.58, -0.04) * mm});
            skLineSegment(sketch, "E2472", {"start": v(-4.58, -0.04) * mm, "end": v(-4.58, 0) * mm});
            skLineSegment(sketch, "E2473", {"start": v(-4.58, 0) * mm, "end": v(-4.6, 0.05) * mm});
            skLineSegment(sketch, "E2474", {"start": v(-4.6, 0.05) * mm, "end": v(-4.6, 0.09) * mm});
            skLineSegment(sketch, "E2475", {"start": v(-4.6, 0.09) * mm, "end": v(-4.62, 0.13) * mm});
            skLineSegment(sketch, "E2476", {"start": v(-4.62, 0.13) * mm, "end": v(-4.64, 0.17) * mm});
            skLineSegment(sketch, "E2477", {"start": v(-4.64, 0.17) * mm, "end": v(-4.66, 0.2) * mm});
            skLineSegment(sketch, "E2478", {"start": v(-4.66, 0.2) * mm, "end": v(-4.68, 0.24) * mm});
            skLineSegment(sketch, "E2479", {"start": v(-4.68, 0.24) * mm, "end": v(-4.7, 0.27) * mm});
            skLineSegment(sketch, "E2480", {"start": v(-4.7, 0.27) * mm, "end": v(-4.72, 0.3) * mm});
            skLineSegment(sketch, "E2481", {"start": v(-4.72, 0.3) * mm, "end": v(-4.74, 0.34) * mm});
            skLineSegment(sketch, "E2482", {"start": v(-4.74, 0.34) * mm, "end": v(-4.77, 0.37) * mm});
            skLineSegment(sketch, "E2483", {"start": v(-4.77, 0.37) * mm, "end": v(-4.8, 0.4) * mm});
            skLineSegment(sketch, "E2484", {"start": v(-4.8, 0.4) * mm, "end": v(-4.83, 0.42) * mm});
            skLineSegment(sketch, "E2485", {"start": v(-4.83, 0.42) * mm, "end": v(-4.86, 0.45) * mm});
            skLineSegment(sketch, "E2486", {"start": v(-4.86, 0.45) * mm, "end": v(-4.89, 0.47) * mm});
            skLineSegment(sketch, "E2487", {"start": v(-4.89, 0.47) * mm, "end": v(-4.92, 0.5) * mm});
            skLineSegment(sketch, "E2488", {"start": v(-4.92, 0.5) * mm, "end": v(-4.95, 0.51) * mm});
            skLineSegment(sketch, "E2489", {"start": v(-4.95, 0.51) * mm, "end": v(-4.99, 0.53) * mm});
            skLineSegment(sketch, "E2490", {"start": v(-4.99, 0.53) * mm, "end": v(-5.02, 0.54) * mm});
            skLineSegment(sketch, "E2491", {"start": v(-5.02, 0.54) * mm, "end": v(-5.06, 0.56) * mm});
            skLineSegment(sketch, "E2492", {"start": v(-5.06, 0.56) * mm, "end": v(-5.1, 0.57) * mm});
            skLineSegment(sketch, "E2493", {"start": v(-5.1, 0.57) * mm, "end": v(-5.13, 0.58) * mm});
            skLineSegment(sketch, "E2494", {"start": v(-5.13, 0.58) * mm, "end": v(-5.17, 0.59) * mm});
            skLineSegment(sketch, "E2495", {"start": v(-5.17, 0.59) * mm, "end": v(-5.21, 0.6) * mm});
            skLineSegment(sketch, "E2496", {"start": v(-5.21, 0.6) * mm, "end": v(-5.25, 0.6) * mm});
            skLineSegment(sketch, "E2497", {"start": v(-5.25, 0.6) * mm, "end": v(-5.3, 0.6) * mm});
            skLineSegment(sketch, "E2498", {"start": v(-5.3, 0.6) * mm, "end": v(-5.33, 0.6) * mm});
            skLineSegment(sketch, "E2499", {"start": v(-5.33, 0.6) * mm, "end": v(-5.37, 0.6) * mm});
            skLineSegment(sketch, "E2500", {"start": v(-5.37, 0.6) * mm, "end": v(-5.41, 0.6) * mm});
            skLineSegment(sketch, "E2501", {"start": v(-5.41, 0.6) * mm, "end": v(-5.45, 0.6) * mm});
            skLineSegment(sketch, "E2502", {"start": v(-5.45, 0.6) * mm, "end": v(-5.49, 0.59) * mm});
            skLineSegment(sketch, "E2503", {"start": v(-5.49, 0.59) * mm, "end": v(-5.53, 0.58) * mm});
            skLineSegment(sketch, "E2504", {"start": v(-5.53, 0.58) * mm, "end": v(-5.56, 0.57) * mm});
            skLineSegment(sketch, "E2505", {"start": v(-5.56, 0.57) * mm, "end": v(-5.6, 0.56) * mm});
            skLineSegment(sketch, "E2506", {"start": v(-5.6, 0.56) * mm, "end": v(-5.63, 0.54) * mm});
            skLineSegment(sketch, "E2507", {"start": v(-5.63, 0.54) * mm, "end": v(-5.67, 0.53) * mm});
            skLineSegment(sketch, "E2508", {"start": v(-5.67, 0.53) * mm, "end": v(-5.7, 0.51) * mm});
            skLineSegment(sketch, "E2509", {"start": v(-5.7, 0.51) * mm, "end": v(-5.73, 0.5) * mm});
            skLineSegment(sketch, "E2510", {"start": v(-5.73, 0.5) * mm, "end": v(-5.77, 0.47) * mm});
            skLineSegment(sketch, "E2511", {"start": v(-5.77, 0.47) * mm, "end": v(-5.8, 0.45) * mm});
            skLineSegment(sketch, "E2512", {"start": v(-5.8, 0.45) * mm, "end": v(-5.83, 0.43) * mm});
            skLineSegment(sketch, "E2513", {"start": v(-5.83, 0.43) * mm, "end": v(-5.85, 0.4) * mm});
            skLineSegment(sketch, "E2514", {"start": v(-5.85, 0.4) * mm, "end": v(-5.88, 0.37) * mm});
            skLineSegment(sketch, "E2515", {"start": v(-5.88, 0.37) * mm, "end": v(-5.9, 0.34) * mm});
            skLineSegment(sketch, "E2516", {"start": v(-5.9, 0.34) * mm, "end": v(-5.93, 0.31) * mm});
            skLineSegment(sketch, "E2517", {"start": v(-5.93, 0.31) * mm, "end": v(-5.95, 0.28) * mm});
            skLineSegment(sketch, "E2518", {"start": v(-5.95, 0.28) * mm, "end": v(-5.97, 0.24) * mm});
            skLineSegment(sketch, "E2519", {"start": v(-5.97, 0.24) * mm, "end": v(-6, 0.2) * mm});
            skLineSegment(sketch, "E2520", {"start": v(-6, 0.2) * mm, "end": v(-6.01, 0.17) * mm});
            skLineSegment(sketch, "E2521", {"start": v(-6.01, 0.17) * mm, "end": v(-6.03, 0.14) * mm});
            skLineSegment(sketch, "E2522", {"start": v(-6.03, 0.14) * mm, "end": v(-6.04, 0.1) * mm});
            skLineSegment(sketch, "E2523", {"start": v(-6.04, 0.1) * mm, "end": v(-6.05, 0.06) * mm});
            skLineSegment(sketch, "E2524", {"start": v(-6.05, 0.06) * mm, "end": v(-6.06, 0.02) * mm});
            skLineSegment(sketch, "E2525", {"start": v(-6.06, 0.02) * mm, "end": v(-6.07, -0.03) * mm});
            skLineSegment(sketch, "E2526", {"start": v(-6.07, -0.03) * mm, "end": v(-6.08, -0.07) * mm});
            skLineSegment(sketch, "E2527", {"start": v(-6.08, -0.07) * mm, "end": v(-6.08, -0.11) * mm});
            skLineSegment(sketch, "E2528", {"start": v(-6.08, -0.11) * mm, "end": v(-6.09, -0.16) * mm});
            skLineSegment(sketch, "E2529", {"start": v(-6.09, -0.16) * mm, "end": v(-6.1, -0.2) * mm});
            skLineSegment(sketch, "E2530", {"start": v(-6.1, -0.2) * mm, "end": v(-6.1, -0.25) * mm});
            skLineSegment(sketch, "E2531", {"start": v(-6.1, -0.25) * mm, "end": v(-6.1, -0.27) * mm});
            skLineSegment(sketch, "E2532", {"start": v(-6.1, -0.27) * mm, "end": v(-6.1, -0.28) * mm});
            skLineSegment(sketch, "E2533", {"start": v(-6.1, -0.28) * mm, "end": v(-6.1, -0.3) * mm});
            skLineSegment(sketch, "E2534", {"start": v(-6.1, -0.3) * mm, "end": v(-6.09, -0.42) * mm});
            skLineSegment(sketch, "E2535", {"start": v(-6.09, -0.42) * mm, "end": v(-5.78, -0.42) * mm});
            skLineSegment(sketch, "E2536", {"start": v(-5.66, -0.42) * mm, "end": v(-5.02, -0.42) * mm});
            skLineSegment(sketch, "E2537", {"start": v(-5.02, -0.42) * mm, "end": v(-5.03, -0.43) * mm});
            skLineSegment(sketch, "E2538", {"start": v(-5.03, -0.43) * mm, "end": v(-5.03, -0.46) * mm});
            skLineSegment(sketch, "E2539", {"start": v(-5.03, -0.46) * mm, "end": v(-5.04, -0.48) * mm});
            skLineSegment(sketch, "E2540", {"start": v(-5.04, -0.48) * mm, "end": v(-5.04, -0.5) * mm});
            skLineSegment(sketch, "E2541", {"start": v(-5.04, -0.5) * mm, "end": v(-5.05, -0.51) * mm});
            skLineSegment(sketch, "E2542", {"start": v(-5.05, -0.51) * mm, "end": v(-5.06, -0.53) * mm});
            skLineSegment(sketch, "E2543", {"start": v(-5.06, -0.53) * mm, "end": v(-5.07, -0.55) * mm});
            skLineSegment(sketch, "E2544", {"start": v(-5.07, -0.55) * mm, "end": v(-5.08, -0.56) * mm});
            skLineSegment(sketch, "E2545", {"start": v(-5.08, -0.56) * mm, "end": v(-5.09, -0.58) * mm});
            skLineSegment(sketch, "E2546", {"start": v(-5.09, -0.58) * mm, "end": v(-5.1, -0.59) * mm});
            skLineSegment(sketch, "E2547", {"start": v(-5.1, -0.59) * mm, "end": v(-5.1, -0.6) * mm});
            skLineSegment(sketch, "E2548", {"start": v(-5.1, -0.6) * mm, "end": v(-5.12, -0.61) * mm});
            skLineSegment(sketch, "E2549", {"start": v(-5.12, -0.61) * mm, "end": v(-5.13, -0.63) * mm});
            skLineSegment(sketch, "E2550", {"start": v(-5.13, -0.63) * mm, "end": v(-5.14, -0.64) * mm});
            skLineSegment(sketch, "E2551", {"start": v(-5.14, -0.64) * mm, "end": v(-5.15, -0.65) * mm});
            skLineSegment(sketch, "E2552", {"start": v(-5.15, -0.65) * mm, "end": v(-5.17, -0.66) * mm});
            skLineSegment(sketch, "E2553", {"start": v(-5.17, -0.66) * mm, "end": v(-5.18, -0.67) * mm});
            skLineSegment(sketch, "E2554", {"start": v(-5.18, -0.67) * mm, "end": v(-5.2, -0.67) * mm});
            skLineSegment(sketch, "E2555", {"start": v(-5.2, -0.67) * mm, "end": v(-5.2, -0.68) * mm});
            skLineSegment(sketch, "E2556", {"start": v(-5.2, -0.68) * mm, "end": v(-5.22, -0.69) * mm});
            skLineSegment(sketch, "E2557", {"start": v(-5.22, -0.69) * mm, "end": v(-5.23, -0.7) * mm});
            skLineSegment(sketch, "E2558", {"start": v(-5.23, -0.7) * mm, "end": v(-5.25, -0.7) * mm});
            skLineSegment(sketch, "E2559", {"start": v(-5.25, -0.7) * mm, "end": v(-5.26, -0.7) * mm});
            skLineSegment(sketch, "E2560", {"start": v(-5.26, -0.7) * mm, "end": v(-5.28, -0.7) * mm});
            skLineSegment(sketch, "E2561", {"start": v(-5.28, -0.7) * mm, "end": v(-5.3, -0.7) * mm});
            skLineSegment(sketch, "E2562", {"start": v(-5.3, -0.7) * mm, "end": v(-5.31, -0.7) * mm});
            skLineSegment(sketch, "E2563", {"start": v(-5.31, -0.7) * mm, "end": v(-5.33, -0.71) * mm});
            skLineSegment(sketch, "E2564", {"start": v(-5.33, -0.71) * mm, "end": v(-5.35, -0.71) * mm});
            skLineSegment(sketch, "E2565", {"start": v(-5.35, -0.71) * mm, "end": v(-5.37, -0.7) * mm});
            skLineSegment(sketch, "E2566", {"start": v(-5.37, -0.7) * mm, "end": v(-5.4, -0.7) * mm});
            skLineSegment(sketch, "E2567", {"start": v(-5.4, -0.7) * mm, "end": v(-5.42, -0.7) * mm});
            skLineSegment(sketch, "E2568", {"start": v(-5.42, -0.7) * mm, "end": v(-5.44, -0.7) * mm});
            skLineSegment(sketch, "E2569", {"start": v(-5.44, -0.7) * mm, "end": v(-5.46, -0.7) * mm});
            skLineSegment(sketch, "E2570", {"start": v(-5.46, -0.7) * mm, "end": v(-5.48, -0.68) * mm});
            skLineSegment(sketch, "E2571", {"start": v(-5.48, -0.68) * mm, "end": v(-5.5, -0.67) * mm});
            skLineSegment(sketch, "E2572", {"start": v(-5.5, -0.67) * mm, "end": v(-5.52, -0.66) * mm});
            skLineSegment(sketch, "E2573", {"start": v(-5.52, -0.66) * mm, "end": v(-5.53, -0.65) * mm});
            skLineSegment(sketch, "E2574", {"start": v(-5.53, -0.65) * mm, "end": v(-5.55, -0.63) * mm});
            skLineSegment(sketch, "E2575", {"start": v(-5.55, -0.63) * mm, "end": v(-5.57, -0.61) * mm});
            skLineSegment(sketch, "E2576", {"start": v(-5.57, -0.61) * mm, "end": v(-5.58, -0.6) * mm});
            skLineSegment(sketch, "E2577", {"start": v(-5.58, -0.6) * mm, "end": v(-5.6, -0.57) * mm});
            skLineSegment(sketch, "E2578", {"start": v(-5.6, -0.57) * mm, "end": v(-5.6, -0.54) * mm});
            skLineSegment(sketch, "E2579", {"start": v(-5.6, -0.54) * mm, "end": v(-5.62, -0.51) * mm});
            skLineSegment(sketch, "E2580", {"start": v(-5.62, -0.51) * mm, "end": v(-5.66, -0.42) * mm});
            skLineSegment(sketch, "E2581", {"start": v(-5.04, -0.02) * mm, "end": v(-5.61, -0.02) * mm});
            skLineSegment(sketch, "E2582", {"start": v(-5.61, -0.02) * mm, "end": v(-5.61, 0) * mm});
            skLineSegment(sketch, "E2583", {"start": v(-5.61, 0) * mm, "end": v(-5.6, 0.01) * mm});
            skLineSegment(sketch, "E2584", {"start": v(-5.6, 0.01) * mm, "end": v(-5.6, 0.02) * mm});
            skLineSegment(sketch, "E2585", {"start": v(-5.6, 0.02) * mm, "end": v(-5.6, 0.04) * mm});
            skLineSegment(sketch, "E2586", {"start": v(-5.6, 0.04) * mm, "end": v(-5.6, 0.05) * mm});
            skLineSegment(sketch, "E2587", {"start": v(-5.6, 0.05) * mm, "end": v(-5.59, 0.06) * mm});
            skLineSegment(sketch, "E2588", {"start": v(-5.59, 0.06) * mm, "end": v(-5.58, 0.07) * mm});
            skLineSegment(sketch, "E2589", {"start": v(-5.58, 0.07) * mm, "end": v(-5.57, 0.08) * mm});
            skLineSegment(sketch, "E2590", {"start": v(-5.57, 0.08) * mm, "end": v(-5.57, 0.09) * mm});
            skLineSegment(sketch, "E2591", {"start": v(-5.57, 0.09) * mm, "end": v(-5.56, 0.1) * mm});
            skLineSegment(sketch, "E2592", {"start": v(-5.56, 0.1) * mm, "end": v(-5.55, 0.1) * mm});
            skLineSegment(sketch, "E2593", {"start": v(-5.55, 0.1) * mm, "end": v(-5.54, 0.12) * mm});
            skLineSegment(sketch, "E2594", {"start": v(-5.54, 0.12) * mm, "end": v(-5.53, 0.13) * mm});
            skLineSegment(sketch, "E2595", {"start": v(-5.53, 0.13) * mm, "end": v(-5.51, 0.14) * mm});
            skLineSegment(sketch, "E2596", {"start": v(-5.51, 0.14) * mm, "end": v(-5.5, 0.15) * mm});
            skLineSegment(sketch, "E2597", {"start": v(-5.5, 0.15) * mm, "end": v(-5.49, 0.16) * mm});
            skLineSegment(sketch, "E2598", {"start": v(-5.49, 0.16) * mm, "end": v(-5.48, 0.17) * mm});
            skLineSegment(sketch, "E2599", {"start": v(-5.48, 0.17) * mm, "end": v(-5.46, 0.17) * mm});
            skLineSegment(sketch, "E2600", {"start": v(-5.46, 0.17) * mm, "end": v(-5.45, 0.18) * mm});
            skLineSegment(sketch, "E2601", {"start": v(-5.45, 0.18) * mm, "end": v(-5.43, 0.18) * mm});
            skLineSegment(sketch, "E2602", {"start": v(-5.43, 0.18) * mm, "end": v(-5.42, 0.19) * mm});
            skLineSegment(sketch, "E2603", {"start": v(-5.42, 0.19) * mm, "end": v(-5.4, 0.2) * mm});
            skLineSegment(sketch, "E2604", {"start": v(-5.4, 0.2) * mm, "end": v(-5.39, 0.2) * mm});
            skLineSegment(sketch, "E2605", {"start": v(-5.39, 0.2) * mm, "end": v(-5.37, 0.2) * mm});
            skLineSegment(sketch, "E2606", {"start": v(-5.37, 0.2) * mm, "end": v(-5.35, 0.2) * mm});
            skLineSegment(sketch, "E2607", {"start": v(-5.35, 0.2) * mm, "end": v(-5.34, 0.2) * mm});
            skLineSegment(sketch, "E2608", {"start": v(-5.34, 0.2) * mm, "end": v(-5.32, 0.2) * mm});
            skLineSegment(sketch, "E2609", {"start": v(-5.32, 0.2) * mm, "end": v(-5.3, 0.2) * mm});
            skLineSegment(sketch, "E2610", {"start": v(-5.3, 0.2) * mm, "end": v(-5.29, 0.2) * mm});
            skLineSegment(sketch, "E2611", {"start": v(-5.29, 0.2) * mm, "end": v(-5.27, 0.2) * mm});
            skLineSegment(sketch, "E2612", {"start": v(-5.27, 0.2) * mm, "end": v(-5.26, 0.2) * mm});
            skLineSegment(sketch, "E2613", {"start": v(-5.26, 0.2) * mm, "end": v(-5.24, 0.19) * mm});
            skLineSegment(sketch, "E2614", {"start": v(-5.24, 0.19) * mm, "end": v(-5.23, 0.18) * mm});
            skLineSegment(sketch, "E2615", {"start": v(-5.23, 0.18) * mm, "end": v(-5.22, 0.18) * mm});
            skLineSegment(sketch, "E2616", {"start": v(-5.22, 0.18) * mm, "end": v(-5.2, 0.17) * mm});
            skLineSegment(sketch, "E2617", {"start": v(-5.2, 0.17) * mm, "end": v(-5.2, 0.17) * mm});
            skLineSegment(sketch, "E2618", {"start": v(-5.2, 0.17) * mm, "end": v(-5.18, 0.16) * mm});
            skLineSegment(sketch, "E2619", {"start": v(-5.18, 0.16) * mm, "end": v(-5.17, 0.15) * mm});
            skLineSegment(sketch, "E2620", {"start": v(-5.17, 0.15) * mm, "end": v(-5.16, 0.14) * mm});
            skLineSegment(sketch, "E2621", {"start": v(-5.16, 0.14) * mm, "end": v(-5.14, 0.14) * mm});
            skLineSegment(sketch, "E2622", {"start": v(-5.14, 0.14) * mm, "end": v(-5.13, 0.13) * mm});
            skLineSegment(sketch, "E2623", {"start": v(-5.13, 0.13) * mm, "end": v(-5.12, 0.12) * mm});
            skLineSegment(sketch, "E2624", {"start": v(-5.12, 0.12) * mm, "end": v(-5.11, 0.1) * mm});
            skLineSegment(sketch, "E2625", {"start": v(-5.11, 0.1) * mm, "end": v(-5.1, 0.1) * mm});
            skLineSegment(sketch, "E2626", {"start": v(-5.1, 0.1) * mm, "end": v(-5.1, 0.08) * mm});
            skLineSegment(sketch, "E2627", {"start": v(-5.1, 0.08) * mm, "end": v(-5.08, 0.07) * mm});
            skLineSegment(sketch, "E2628", {"start": v(-5.08, 0.07) * mm, "end": v(-5.07, 0.06) * mm});
            skLineSegment(sketch, "E2629", {"start": v(-5.07, 0.06) * mm, "end": v(-5.07, 0.04) * mm});
            skLineSegment(sketch, "E2630", {"start": v(-5.07, 0.04) * mm, "end": v(-5.06, 0.03) * mm});
            skLineSegment(sketch, "E2631", {"start": v(-5.06, 0.03) * mm, "end": v(-5.05, 0.02) * mm});
            skLineSegment(sketch, "E2632", {"start": v(-5.05, 0.02) * mm, "end": v(-5.05, 0) * mm});
            skLineSegment(sketch, "E2633", {"start": v(-5.05, 0) * mm, "end": v(-5.04, -0.02) * mm});
            skLineSegment(sketch, "E2634", {"start": v(-5.04, -0.02) * mm, "end": v(-5.04, -0.02) * mm});
            skSolve(sketch);
        }
        {
            var Q0;
            Q0=makeQuery(id+"F9.imprint","IMPRINT",FACE,{"disambiguationData":[TD([[makeQuery(id+"F9.imprint","IMPRINT",EDGE,{"derivedFrom":sQuery(id+"F9.wireOp",EDGE,"E709")}),1.0]])]});
            var Q1;
            Q1=makeQuery(id+"F9.imprint","IMPRINT",FACE,{"disambiguationData":[TD([[makeQuery(id+"F9.imprint","IMPRINT",EDGE,{"derivedFrom":sQuery(id+"F9.wireOp",EDGE,"E1026")}),1.0]])]});
            var Q2;
            Q2=makeQuery(id+"F9.imprint","IMPRINT",FACE,{"disambiguationData":[TD([[makeQuery(id+"F9.imprint","IMPRINT",EDGE,{"derivedFrom":sQuery(id+"F9.wireOp",EDGE,"E1996")}),1.0]])]});
            var Q3;
            Q3=makeQuery(id+"F9.imprint","IMPRINT",FACE,{"disambiguationData":[TD([[makeQuery(id+"F9.imprint","IMPRINT",EDGE,{"derivedFrom":sQuery(id+"F9.wireOp",EDGE,"E2102")}),1.0]])]});
            var Q4;
            Q4=makeQuery(id+"F9.imprint","IMPRINT",FACE,{"disambiguationData":[TD([[makeQuery(id+"F9.imprint","IMPRINT",EDGE,{"derivedFrom":sQuery(id+"F9.wireOp",EDGE,"E2106")}),1.0]])]});
            var Q5;
            Q5=makeQuery(id+"F9.imprint","IMPRINT",FACE,{"disambiguationData":[TD([[makeQuery(id+"F9.imprint","IMPRINT",EDGE,{"derivedFrom":sQuery(id+"F9.wireOp",EDGE,"E2110")}),1.0]])]});
            var Q6;
            Q6=makeQuery(id+"F9.imprint","IMPRINT",FACE,{"disambiguationData":[TD([[makeQuery(id+"F9.imprint","IMPRINT",EDGE,{"derivedFrom":sQuery(id+"F9.wireOp",EDGE,"E2164")}),1.0]])]});
            var Q7;
            Q7=makeQuery(id+"F9.imprint","IMPRINT",FACE,{"disambiguationData":[TD([[makeQuery(id+"F9.imprint","IMPRINT",EDGE,{"derivedFrom":sQuery(id+"F9.wireOp",EDGE,"E2398")}),1.0]])]});
            var Q8;
            Q8=makeQuery(id+"F9.imprint","IMPRINT",FACE,{"disambiguationData":[TD([[makeQuery(id+"F9.imprint","IMPRINT",EDGE,{"derivedFrom":sQuery(id+"F9.wireOp",EDGE,"E2402")}),1.0]])]});
            extrude(context, id + "F10", {"entities" : qUnion([Q0, Q1, Q2, Q3, Q4, Q5, Q6, Q7, Q8]), "depth" : .5 * mm});
        }
        {
            var Q0;
            Q0=makeQuery(id+"F10.opExtrude","SWEPT_BODY",BODY,{"disambiguationData":[OSD([sQuery(id+"F9.wireOp",EDGE,"E709"),sQuery(id+"F9.wireOp",EDGE,"E710"),sQuery(id+"F9.wireOp",EDGE,"E711"),sQuery(id+"F9.wireOp",EDGE,"E712"),sQuery(id+"F9.wireOp",EDGE,"E713"),sQuery(id+"F9.wireOp",EDGE,"E714"),sQuery(id+"F9.wireOp",EDGE,"E715"),sQuery(id+"F9.wireOp",EDGE,"E716"),sQuery(id+"F9.wireOp",EDGE,"E717"),sQuery(id+"F9.wireOp",EDGE,"E718"),sQuery(id+"F9.wireOp",EDGE,"E719"),sQuery(id+"F9.wireOp",EDGE,"E720"),sQuery(id+"F9.wireOp",EDGE,"E721"),sQuery(id+"F9.wireOp",EDGE,"E722"),sQuery(id+"F9.wireOp",EDGE,"E723"),sQuery(id+"F9.wireOp",EDGE,"E724"),sQuery(id+"F9.wireOp",EDGE,"E725"),sQuery(id+"F9.wireOp",EDGE,"E726"),sQuery(id+"F9.wireOp",EDGE,"E727"),sQuery(id+"F9.wireOp",EDGE,"E728"),sQuery(id+"F9.wireOp",EDGE,"E729"),sQuery(id+"F9.wireOp",EDGE,"E730"),sQuery(id+"F9.wireOp",EDGE,"E731"),sQuery(id+"F9.wireOp",EDGE,"E732"),sQuery(id+"F9.wireOp",EDGE,"E733"),sQuery(id+"F9.wireOp",EDGE,"E734"),sQuery(id+"F9.wireOp",EDGE,"E735"),sQuery(id+"F9.wireOp",EDGE,"E736"),sQuery(id+"F9.wireOp",EDGE,"E737"),sQuery(id+"F9.wireOp",EDGE,"E738"),sQuery(id+"F9.wireOp",EDGE,"E739"),sQuery(id+"F9.wireOp",EDGE,"E740"),sQuery(id+"F9.wireOp",EDGE,"E741"),sQuery(id+"F9.wireOp",EDGE,"E742"),sQuery(id+"F9.wireOp",EDGE,"E743"),sQuery(id+"F9.wireOp",EDGE,"E744"),sQuery(id+"F9.wireOp",EDGE,"E745"),sQuery(id+"F9.wireOp",EDGE,"E746"),sQuery(id+"F9.wireOp",EDGE,"E747"),sQuery(id+"F9.wireOp",EDGE,"E748"),sQuery(id+"F9.wireOp",EDGE,"E749"),sQuery(id+"F9.wireOp",EDGE,"E750"),sQuery(id+"F9.wireOp",EDGE,"E751"),sQuery(id+"F9.wireOp",EDGE,"E752"),sQuery(id+"F9.wireOp",EDGE,"E753"),sQuery(id+"F9.wireOp",EDGE,"E754"),sQuery(id+"F9.wireOp",EDGE,"E755"),sQuery(id+"F9.wireOp",EDGE,"E756"),sQuery(id+"F9.wireOp",EDGE,"E757"),sQuery(id+"F9.wireOp",EDGE,"E758"),sQuery(id+"F9.wireOp",EDGE,"E759"),sQuery(id+"F9.wireOp",EDGE,"E760"),sQuery(id+"F9.wireOp",EDGE,"E761"),sQuery(id+"F9.wireOp",EDGE,"E762"),sQuery(id+"F9.wireOp",EDGE,"E763"),sQuery(id+"F9.wireOp",EDGE,"E764"),sQuery(id+"F9.wireOp",EDGE,"E765"),sQuery(id+"F9.wireOp",EDGE,"E766"),sQuery(id+"F9.wireOp",EDGE,"E767"),sQuery(id+"F9.wireOp",EDGE,"E768"),sQuery(id+"F9.wireOp",EDGE,"E769"),sQuery(id+"F9.wireOp",EDGE,"E770"),sQuery(id+"F9.wireOp",EDGE,"E771"),sQuery(id+"F9.wireOp",EDGE,"E772"),sQuery(id+"F9.wireOp",EDGE,"E773"),sQuery(id+"F9.wireOp",EDGE,"E774"),sQuery(id+"F9.wireOp",EDGE,"E775"),sQuery(id+"F9.wireOp",EDGE,"E776"),sQuery(id+"F9.wireOp",EDGE,"E777"),sQuery(id+"F9.wireOp",EDGE,"E778"),sQuery(id+"F9.wireOp",EDGE,"E779"),sQuery(id+"F9.wireOp",EDGE,"E780"),sQuery(id+"F9.wireOp",EDGE,"E781"),sQuery(id+"F9.wireOp",EDGE,"E782"),sQuery(id+"F9.wireOp",EDGE,"E783"),sQuery(id+"F9.wireOp",EDGE,"E784"),sQuery(id+"F9.wireOp",EDGE,"E785"),sQuery(id+"F9.wireOp",EDGE,"E786"),sQuery(id+"F9.wireOp",EDGE,"E787"),sQuery(id+"F9.wireOp",EDGE,"E788"),sQuery(id+"F9.wireOp",EDGE,"E789"),sQuery(id+"F9.wireOp",EDGE,"E790"),sQuery(id+"F9.wireOp",EDGE,"E791"),sQuery(id+"F9.wireOp",EDGE,"E792"),sQuery(id+"F9.wireOp",EDGE,"E793"),sQuery(id+"F9.wireOp",EDGE,"E794"),sQuery(id+"F9.wireOp",EDGE,"E795"),sQuery(id+"F9.wireOp",EDGE,"E796"),sQuery(id+"F9.wireOp",EDGE,"E797"),sQuery(id+"F9.wireOp",EDGE,"E798"),sQuery(id+"F9.wireOp",EDGE,"E799"),sQuery(id+"F9.wireOp",EDGE,"E800"),sQuery(id+"F9.wireOp",EDGE,"E801"),sQuery(id+"F9.wireOp",EDGE,"E802"),sQuery(id+"F9.wireOp",EDGE,"E803"),sQuery(id+"F9.wireOp",EDGE,"E804"),sQuery(id+"F9.wireOp",EDGE,"E805"),sQuery(id+"F9.wireOp",EDGE,"E806"),sQuery(id+"F9.wireOp",EDGE,"E807"),sQuery(id+"F9.wireOp",EDGE,"E808"),sQuery(id+"F9.wireOp",EDGE,"E809"),sQuery(id+"F9.wireOp",EDGE,"E810"),sQuery(id+"F9.wireOp",EDGE,"E811"),sQuery(id+"F9.wireOp",EDGE,"E812"),sQuery(id+"F9.wireOp",EDGE,"E813"),sQuery(id+"F9.wireOp",EDGE,"E814"),sQuery(id+"F9.wireOp",EDGE,"E815"),sQuery(id+"F9.wireOp",EDGE,"E816"),sQuery(id+"F9.wireOp",EDGE,"E817"),sQuery(id+"F9.wireOp",EDGE,"E818"),sQuery(id+"F9.wireOp",EDGE,"E819"),sQuery(id+"F9.wireOp",EDGE,"E820"),sQuery(id+"F9.wireOp",EDGE,"E821"),sQuery(id+"F9.wireOp",EDGE,"E822"),sQuery(id+"F9.wireOp",EDGE,"E823"),sQuery(id+"F9.wireOp",EDGE,"E824"),sQuery(id+"F9.wireOp",EDGE,"E825"),sQuery(id+"F9.wireOp",EDGE,"E826"),sQuery(id+"F9.wireOp",EDGE,"E827"),sQuery(id+"F9.wireOp",EDGE,"E828"),sQuery(id+"F9.wireOp",EDGE,"E829"),sQuery(id+"F9.wireOp",EDGE,"E830"),sQuery(id+"F9.wireOp",EDGE,"E831"),sQuery(id+"F9.wireOp",EDGE,"E832"),sQuery(id+"F9.wireOp",EDGE,"E833"),sQuery(id+"F9.wireOp",EDGE,"E834"),sQuery(id+"F9.wireOp",EDGE,"E835"),sQuery(id+"F9.wireOp",EDGE,"E836"),sQuery(id+"F9.wireOp",EDGE,"E837"),sQuery(id+"F9.wireOp",EDGE,"E838"),sQuery(id+"F9.wireOp",EDGE,"E839"),sQuery(id+"F9.wireOp",EDGE,"E840"),sQuery(id+"F9.wireOp",EDGE,"E841"),sQuery(id+"F9.wireOp",EDGE,"E842"),sQuery(id+"F9.wireOp",EDGE,"E843"),sQuery(id+"F9.wireOp",EDGE,"E844"),sQuery(id+"F9.wireOp",EDGE,"E845"),sQuery(id+"F9.wireOp",EDGE,"E846"),sQuery(id+"F9.wireOp",EDGE,"E847"),sQuery(id+"F9.wireOp",EDGE,"E848"),sQuery(id+"F9.wireOp",EDGE,"E849"),sQuery(id+"F9.wireOp",EDGE,"E850"),sQuery(id+"F9.wireOp",EDGE,"E851"),sQuery(id+"F9.wireOp",EDGE,"E852"),sQuery(id+"F9.wireOp",EDGE,"E853"),sQuery(id+"F9.wireOp",EDGE,"E854"),sQuery(id+"F9.wireOp",EDGE,"E855"),sQuery(id+"F9.wireOp",EDGE,"E856"),sQuery(id+"F9.wireOp",EDGE,"E857"),sQuery(id+"F9.wireOp",EDGE,"E858"),sQuery(id+"F9.wireOp",EDGE,"E859"),sQuery(id+"F9.wireOp",EDGE,"E860"),sQuery(id+"F9.wireOp",EDGE,"E861"),sQuery(id+"F9.wireOp",EDGE,"E862"),sQuery(id+"F9.wireOp",EDGE,"E863"),sQuery(id+"F9.wireOp",EDGE,"E864"),sQuery(id+"F9.wireOp",EDGE,"E865"),sQuery(id+"F9.wireOp",EDGE,"E866"),sQuery(id+"F9.wireOp",EDGE,"E867"),sQuery(id+"F9.wireOp",EDGE,"E868"),sQuery(id+"F9.wireOp",EDGE,"E869"),sQuery(id+"F9.wireOp",EDGE,"E870"),sQuery(id+"F9.wireOp",EDGE,"E871"),sQuery(id+"F9.wireOp",EDGE,"E872"),sQuery(id+"F9.wireOp",EDGE,"E873"),sQuery(id+"F9.wireOp",EDGE,"E874"),sQuery(id+"F9.wireOp",EDGE,"E875"),sQuery(id+"F9.wireOp",EDGE,"E876"),sQuery(id+"F9.wireOp",EDGE,"E877"),sQuery(id+"F9.wireOp",EDGE,"E878"),sQuery(id+"F9.wireOp",EDGE,"E879"),sQuery(id+"F9.wireOp",EDGE,"E880"),sQuery(id+"F9.wireOp",EDGE,"E881"),sQuery(id+"F9.wireOp",EDGE,"E882"),sQuery(id+"F9.wireOp",EDGE,"E883"),sQuery(id+"F9.wireOp",EDGE,"E884"),sQuery(id+"F9.wireOp",EDGE,"E885"),sQuery(id+"F9.wireOp",EDGE,"E886"),sQuery(id+"F9.wireOp",EDGE,"E887"),sQuery(id+"F9.wireOp",EDGE,"E888"),sQuery(id+"F9.wireOp",EDGE,"E889"),sQuery(id+"F9.wireOp",EDGE,"E890"),sQuery(id+"F9.wireOp",EDGE,"E891"),sQuery(id+"F9.wireOp",EDGE,"E892"),sQuery(id+"F9.wireOp",EDGE,"E893"),sQuery(id+"F9.wireOp",EDGE,"E894"),sQuery(id+"F9.wireOp",EDGE,"E895"),sQuery(id+"F9.wireOp",EDGE,"E896"),sQuery(id+"F9.wireOp",EDGE,"E897"),sQuery(id+"F9.wireOp",EDGE,"E898"),sQuery(id+"F9.wireOp",EDGE,"E899"),sQuery(id+"F9.wireOp",EDGE,"E900"),sQuery(id+"F9.wireOp",EDGE,"E901"),sQuery(id+"F9.wireOp",EDGE,"E902"),sQuery(id+"F9.wireOp",EDGE,"E903"),sQuery(id+"F9.wireOp",EDGE,"E904"),sQuery(id+"F9.wireOp",EDGE,"E905"),sQuery(id+"F9.wireOp",EDGE,"E906"),sQuery(id+"F9.wireOp",EDGE,"E907"),sQuery(id+"F9.wireOp",EDGE,"E908"),sQuery(id+"F9.wireOp",EDGE,"E909"),sQuery(id+"F9.wireOp",EDGE,"E910"),sQuery(id+"F9.wireOp",EDGE,"E911"),sQuery(id+"F9.wireOp",EDGE,"E912"),sQuery(id+"F9.wireOp",EDGE,"E913"),sQuery(id+"F9.wireOp",EDGE,"E913"),sQuery(id+"F9.wireOp",EDGE,"E913"),sQuery(id+"F9.wireOp",EDGE,"E913"),sQuery(id+"F9.wireOp",EDGE,"E914"),sQuery(id+"F9.wireOp",EDGE,"E915"),sQuery(id+"F9.wireOp",EDGE,"E916"),sQuery(id+"F9.wireOp",EDGE,"E917"),sQuery(id+"F9.wireOp",EDGE,"E917"),sQuery(id+"F9.wireOp",EDGE,"E918"),sQuery(id+"F9.wireOp",EDGE,"E919"),sQuery(id+"F9.wireOp",EDGE,"E920"),sQuery(id+"F9.wireOp",EDGE,"E921"),sQuery(id+"F9.wireOp",EDGE,"E922"),sQuery(id+"F9.wireOp",EDGE,"E923"),sQuery(id+"F9.wireOp",EDGE,"E923"),sQuery(id+"F9.wireOp",EDGE,"E924"),sQuery(id+"F9.wireOp",EDGE,"E925"),sQuery(id+"F9.wireOp",EDGE,"E926"),sQuery(id+"F9.wireOp",EDGE,"E927"),sQuery(id+"F9.wireOp",EDGE,"E928"),sQuery(id+"F9.wireOp",EDGE,"E929"),sQuery(id+"F9.wireOp",EDGE,"E930"),sQuery(id+"F9.wireOp",EDGE,"E931"),sQuery(id+"F9.wireOp",EDGE,"E932"),sQuery(id+"F9.wireOp",EDGE,"E933"),sQuery(id+"F9.wireOp",EDGE,"E934"),sQuery(id+"F9.wireOp",EDGE,"E935"),sQuery(id+"F9.wireOp",EDGE,"E936"),sQuery(id+"F9.wireOp",EDGE,"E937"),sQuery(id+"F9.wireOp",EDGE,"E938"),sQuery(id+"F9.wireOp",EDGE,"E939"),sQuery(id+"F9.wireOp",EDGE,"E940"),sQuery(id+"F9.wireOp",EDGE,"E941"),sQuery(id+"F9.wireOp",EDGE,"E942"),sQuery(id+"F9.wireOp",EDGE,"E943"),sQuery(id+"F9.wireOp",EDGE,"E944"),sQuery(id+"F9.wireOp",EDGE,"E945"),sQuery(id+"F9.wireOp",EDGE,"E946"),sQuery(id+"F9.wireOp",EDGE,"E947"),sQuery(id+"F9.wireOp",EDGE,"E948"),sQuery(id+"F9.wireOp",EDGE,"E949"),sQuery(id+"F9.wireOp",EDGE,"E950"),sQuery(id+"F9.wireOp",EDGE,"E951"),sQuery(id+"F9.wireOp",EDGE,"E952"),sQuery(id+"F9.wireOp",EDGE,"E953"),sQuery(id+"F9.wireOp",EDGE,"E954"),sQuery(id+"F9.wireOp",EDGE,"E955"),sQuery(id+"F9.wireOp",EDGE,"E956"),sQuery(id+"F9.wireOp",EDGE,"E957"),sQuery(id+"F9.wireOp",EDGE,"E958"),sQuery(id+"F9.wireOp",EDGE,"E959"),sQuery(id+"F9.wireOp",EDGE,"E960"),sQuery(id+"F9.wireOp",EDGE,"E961"),sQuery(id+"F9.wireOp",EDGE,"E962"),sQuery(id+"F9.wireOp",EDGE,"E963"),sQuery(id+"F9.wireOp",EDGE,"E964"),sQuery(id+"F9.wireOp",EDGE,"E965"),sQuery(id+"F9.wireOp",EDGE,"E966"),sQuery(id+"F9.wireOp",EDGE,"E967"),sQuery(id+"F9.wireOp",EDGE,"E968"),sQuery(id+"F9.wireOp",EDGE,"E969"),sQuery(id+"F9.wireOp",EDGE,"E970"),sQuery(id+"F9.wireOp",EDGE,"E971"),sQuery(id+"F9.wireOp",EDGE,"E972"),sQuery(id+"F9.wireOp",EDGE,"E973"),sQuery(id+"F9.wireOp",EDGE,"E974"),sQuery(id+"F9.wireOp",EDGE,"E975"),sQuery(id+"F9.wireOp",EDGE,"E976"),sQuery(id+"F9.wireOp",EDGE,"E977"),sQuery(id+"F9.wireOp",EDGE,"E978"),sQuery(id+"F9.wireOp",EDGE,"E979"),sQuery(id+"F9.wireOp",EDGE,"E980"),sQuery(id+"F9.wireOp",EDGE,"E981"),sQuery(id+"F9.wireOp",EDGE,"E982"),sQuery(id+"F9.wireOp",EDGE,"E983"),sQuery(id+"F9.wireOp",EDGE,"E984"),sQuery(id+"F9.wireOp",EDGE,"E985"),sQuery(id+"F9.wireOp",EDGE,"E986"),sQuery(id+"F9.wireOp",EDGE,"E987"),sQuery(id+"F9.wireOp",EDGE,"E988"),sQuery(id+"F9.wireOp",EDGE,"E989"),sQuery(id+"F9.wireOp",EDGE,"E990"),sQuery(id+"F9.wireOp",EDGE,"E991"),sQuery(id+"F9.wireOp",EDGE,"E992"),sQuery(id+"F9.wireOp",EDGE,"E993"),sQuery(id+"F9.wireOp",EDGE,"E994"),sQuery(id+"F9.wireOp",EDGE,"E995"),sQuery(id+"F9.wireOp",EDGE,"E996"),sQuery(id+"F9.wireOp",EDGE,"E997"),sQuery(id+"F9.wireOp",EDGE,"E998"),sQuery(id+"F9.wireOp",EDGE,"E999"),sQuery(id+"F9.wireOp",EDGE,"E1000"),sQuery(id+"F9.wireOp",EDGE,"E1001"),sQuery(id+"F9.wireOp",EDGE,"E1002"),sQuery(id+"F9.wireOp",EDGE,"E1003"),sQuery(id+"F9.wireOp",EDGE,"E1004"),sQuery(id+"F9.wireOp",EDGE,"E1005"),sQuery(id+"F9.wireOp",EDGE,"E1006"),sQuery(id+"F9.wireOp",EDGE,"E1007"),sQuery(id+"F9.wireOp",EDGE,"E1008"),sQuery(id+"F9.wireOp",EDGE,"E1009"),sQuery(id+"F9.wireOp",EDGE,"E1010"),sQuery(id+"F9.wireOp",EDGE,"E1011"),sQuery(id+"F9.wireOp",EDGE,"E1012"),sQuery(id+"F9.wireOp",EDGE,"E1013"),sQuery(id+"F9.wireOp",EDGE,"E1014"),sQuery(id+"F9.wireOp",EDGE,"E1015"),sQuery(id+"F9.wireOp",EDGE,"E1016"),sQuery(id+"F9.wireOp",EDGE,"E1017"),sQuery(id+"F9.wireOp",EDGE,"E1018"),sQuery(id+"F9.wireOp",EDGE,"E1019"),sQuery(id+"F9.wireOp",EDGE,"E1020"),sQuery(id+"F9.wireOp",EDGE,"E1021"),sQuery(id+"F9.wireOp",EDGE,"E1022"),sQuery(id+"F9.wireOp",EDGE,"E1023"),sQuery(id+"F9.wireOp",EDGE,"E1024"),sQuery(id+"F9.wireOp",EDGE,"E1025")])]});
            var Q1;
            Q1=makeQuery(id+"F10.opExtrude","SWEPT_BODY",BODY,{"disambiguationData":[OSD([sQuery(id+"F9.wireOp",EDGE,"E1026"),sQuery(id+"F9.wireOp",EDGE,"E1027"),sQuery(id+"F9.wireOp",EDGE,"E1028"),sQuery(id+"F9.wireOp",EDGE,"E1029"),sQuery(id+"F9.wireOp",EDGE,"E1030"),sQuery(id+"F9.wireOp",EDGE,"E1031"),sQuery(id+"F9.wireOp",EDGE,"E1032"),sQuery(id+"F9.wireOp",EDGE,"E1033"),sQuery(id+"F9.wireOp",EDGE,"E1034"),sQuery(id+"F9.wireOp",EDGE,"E1035"),sQuery(id+"F9.wireOp",EDGE,"E1036"),sQuery(id+"F9.wireOp",EDGE,"E1037"),sQuery(id+"F9.wireOp",EDGE,"E1038"),sQuery(id+"F9.wireOp",EDGE,"E1039"),sQuery(id+"F9.wireOp",EDGE,"E1040"),sQuery(id+"F9.wireOp",EDGE,"E1041"),sQuery(id+"F9.wireOp",EDGE,"E1042"),sQuery(id+"F9.wireOp",EDGE,"E1043"),sQuery(id+"F9.wireOp",EDGE,"E1044"),sQuery(id+"F9.wireOp",EDGE,"E1045"),sQuery(id+"F9.wireOp",EDGE,"E1046"),sQuery(id+"F9.wireOp",EDGE,"E1047"),sQuery(id+"F9.wireOp",EDGE,"E1048"),sQuery(id+"F9.wireOp",EDGE,"E1049"),sQuery(id+"F9.wireOp",EDGE,"E1050"),sQuery(id+"F9.wireOp",EDGE,"E1051"),sQuery(id+"F9.wireOp",EDGE,"E1052"),sQuery(id+"F9.wireOp",EDGE,"E1053"),sQuery(id+"F9.wireOp",EDGE,"E1054"),sQuery(id+"F9.wireOp",EDGE,"E1055"),sQuery(id+"F9.wireOp",EDGE,"E1056"),sQuery(id+"F9.wireOp",EDGE,"E1057"),sQuery(id+"F9.wireOp",EDGE,"E1058"),sQuery(id+"F9.wireOp",EDGE,"E1059"),sQuery(id+"F9.wireOp",EDGE,"E1060"),sQuery(id+"F9.wireOp",EDGE,"E1061"),sQuery(id+"F9.wireOp",EDGE,"E1062"),sQuery(id+"F9.wireOp",EDGE,"E1063"),sQuery(id+"F9.wireOp",EDGE,"E1064"),sQuery(id+"F9.wireOp",EDGE,"E1065"),sQuery(id+"F9.wireOp",EDGE,"E1066"),sQuery(id+"F9.wireOp",EDGE,"E1067"),sQuery(id+"F9.wireOp",EDGE,"E1068"),sQuery(id+"F9.wireOp",EDGE,"E1069"),sQuery(id+"F9.wireOp",EDGE,"E1070"),sQuery(id+"F9.wireOp",EDGE,"E1071"),sQuery(id+"F9.wireOp",EDGE,"E1072"),sQuery(id+"F9.wireOp",EDGE,"E1073"),sQuery(id+"F9.wireOp",EDGE,"E1074"),sQuery(id+"F9.wireOp",EDGE,"E1075"),sQuery(id+"F9.wireOp",EDGE,"E1076"),sQuery(id+"F9.wireOp",EDGE,"E1077"),sQuery(id+"F9.wireOp",EDGE,"E1078"),sQuery(id+"F9.wireOp",EDGE,"E1079"),sQuery(id+"F9.wireOp",EDGE,"E1080"),sQuery(id+"F9.wireOp",EDGE,"E1081"),sQuery(id+"F9.wireOp",EDGE,"E1082"),sQuery(id+"F9.wireOp",EDGE,"E1083"),sQuery(id+"F9.wireOp",EDGE,"E1084"),sQuery(id+"F9.wireOp",EDGE,"E1085"),sQuery(id+"F9.wireOp",EDGE,"E1086"),sQuery(id+"F9.wireOp",EDGE,"E1087"),sQuery(id+"F9.wireOp",EDGE,"E1088"),sQuery(id+"F9.wireOp",EDGE,"E1089"),sQuery(id+"F9.wireOp",EDGE,"E1090"),sQuery(id+"F9.wireOp",EDGE,"E1091"),sQuery(id+"F9.wireOp",EDGE,"E1092"),sQuery(id+"F9.wireOp",EDGE,"E1093"),sQuery(id+"F9.wireOp",EDGE,"E1094"),sQuery(id+"F9.wireOp",EDGE,"E1095"),sQuery(id+"F9.wireOp",EDGE,"E1096"),sQuery(id+"F9.wireOp",EDGE,"E1097"),sQuery(id+"F9.wireOp",EDGE,"E1098"),sQuery(id+"F9.wireOp",EDGE,"E1099"),sQuery(id+"F9.wireOp",EDGE,"E1100"),sQuery(id+"F9.wireOp",EDGE,"E1101"),sQuery(id+"F9.wireOp",EDGE,"E1102"),sQuery(id+"F9.wireOp",EDGE,"E1103"),sQuery(id+"F9.wireOp",EDGE,"E1104"),sQuery(id+"F9.wireOp",EDGE,"E1105"),sQuery(id+"F9.wireOp",EDGE,"E1106"),sQuery(id+"F9.wireOp",EDGE,"E1107"),sQuery(id+"F9.wireOp",EDGE,"E1108"),sQuery(id+"F9.wireOp",EDGE,"E1109"),sQuery(id+"F9.wireOp",EDGE,"E1110"),sQuery(id+"F9.wireOp",EDGE,"E1111"),sQuery(id+"F9.wireOp",EDGE,"E1112"),sQuery(id+"F9.wireOp",EDGE,"E1113"),sQuery(id+"F9.wireOp",EDGE,"E1114"),sQuery(id+"F9.wireOp",EDGE,"E1115"),sQuery(id+"F9.wireOp",EDGE,"E1116"),sQuery(id+"F9.wireOp",EDGE,"E1117"),sQuery(id+"F9.wireOp",EDGE,"E1118"),sQuery(id+"F9.wireOp",EDGE,"E1119"),sQuery(id+"F9.wireOp",EDGE,"E1120"),sQuery(id+"F9.wireOp",EDGE,"E1121"),sQuery(id+"F9.wireOp",EDGE,"E1122"),sQuery(id+"F9.wireOp",EDGE,"E1123"),sQuery(id+"F9.wireOp",EDGE,"E1124"),sQuery(id+"F9.wireOp",EDGE,"E1125"),sQuery(id+"F9.wireOp",EDGE,"E1126"),sQuery(id+"F9.wireOp",EDGE,"E1127"),sQuery(id+"F9.wireOp",EDGE,"E1128"),sQuery(id+"F9.wireOp",EDGE,"E1129"),sQuery(id+"F9.wireOp",EDGE,"E1130"),sQuery(id+"F9.wireOp",EDGE,"E1131"),sQuery(id+"F9.wireOp",EDGE,"E1132"),sQuery(id+"F9.wireOp",EDGE,"E1133"),sQuery(id+"F9.wireOp",EDGE,"E1134"),sQuery(id+"F9.wireOp",EDGE,"E1135"),sQuery(id+"F9.wireOp",EDGE,"E1136"),sQuery(id+"F9.wireOp",EDGE,"E1137"),sQuery(id+"F9.wireOp",EDGE,"E1138"),sQuery(id+"F9.wireOp",EDGE,"E1139"),sQuery(id+"F9.wireOp",EDGE,"E1140"),sQuery(id+"F9.wireOp",EDGE,"E1141"),sQuery(id+"F9.wireOp",EDGE,"E1142"),sQuery(id+"F9.wireOp",EDGE,"E1143"),sQuery(id+"F9.wireOp",EDGE,"E1144"),sQuery(id+"F9.wireOp",EDGE,"E1145"),sQuery(id+"F9.wireOp",EDGE,"E1146"),sQuery(id+"F9.wireOp",EDGE,"E1147"),sQuery(id+"F9.wireOp",EDGE,"E1148"),sQuery(id+"F9.wireOp",EDGE,"E1149"),sQuery(id+"F9.wireOp",EDGE,"E1150"),sQuery(id+"F9.wireOp",EDGE,"E1151"),sQuery(id+"F9.wireOp",EDGE,"E1152"),sQuery(id+"F9.wireOp",EDGE,"E1153"),sQuery(id+"F9.wireOp",EDGE,"E1154"),sQuery(id+"F9.wireOp",EDGE,"E1155"),sQuery(id+"F9.wireOp",EDGE,"E1156"),sQuery(id+"F9.wireOp",EDGE,"E1157"),sQuery(id+"F9.wireOp",EDGE,"E1158"),sQuery(id+"F9.wireOp",EDGE,"E1159"),sQuery(id+"F9.wireOp",EDGE,"E1160"),sQuery(id+"F9.wireOp",EDGE,"E1161"),sQuery(id+"F9.wireOp",EDGE,"E1162"),sQuery(id+"F9.wireOp",EDGE,"E1163"),sQuery(id+"F9.wireOp",EDGE,"E1164"),sQuery(id+"F9.wireOp",EDGE,"E1165"),sQuery(id+"F9.wireOp",EDGE,"E1166"),sQuery(id+"F9.wireOp",EDGE,"E1167"),sQuery(id+"F9.wireOp",EDGE,"E1168"),sQuery(id+"F9.wireOp",EDGE,"E1169"),sQuery(id+"F9.wireOp",EDGE,"E1170"),sQuery(id+"F9.wireOp",EDGE,"E1171"),sQuery(id+"F9.wireOp",EDGE,"E1172"),sQuery(id+"F9.wireOp",EDGE,"E1173"),sQuery(id+"F9.wireOp",EDGE,"E1174"),sQuery(id+"F9.wireOp",EDGE,"E1175"),sQuery(id+"F9.wireOp",EDGE,"E1176"),sQuery(id+"F9.wireOp",EDGE,"E1177"),sQuery(id+"F9.wireOp",EDGE,"E1178"),sQuery(id+"F9.wireOp",EDGE,"E1179"),sQuery(id+"F9.wireOp",EDGE,"E1180"),sQuery(id+"F9.wireOp",EDGE,"E1181"),sQuery(id+"F9.wireOp",EDGE,"E1182"),sQuery(id+"F9.wireOp",EDGE,"E1183"),sQuery(id+"F9.wireOp",EDGE,"E1184"),sQuery(id+"F9.wireOp",EDGE,"E1185"),sQuery(id+"F9.wireOp",EDGE,"E1186"),sQuery(id+"F9.wireOp",EDGE,"E1187"),sQuery(id+"F9.wireOp",EDGE,"E1188"),sQuery(id+"F9.wireOp",EDGE,"E1189"),sQuery(id+"F9.wireOp",EDGE,"E1190"),sQuery(id+"F9.wireOp",EDGE,"E1191"),sQuery(id+"F9.wireOp",EDGE,"E1192"),sQuery(id+"F9.wireOp",EDGE,"E1193"),sQuery(id+"F9.wireOp",EDGE,"E1194"),sQuery(id+"F9.wireOp",EDGE,"E1195"),sQuery(id+"F9.wireOp",EDGE,"E1196"),sQuery(id+"F9.wireOp",EDGE,"E1197"),sQuery(id+"F9.wireOp",EDGE,"E1198"),sQuery(id+"F9.wireOp",EDGE,"E1199"),sQuery(id+"F9.wireOp",EDGE,"E1200"),sQuery(id+"F9.wireOp",EDGE,"E1201"),sQuery(id+"F9.wireOp",EDGE,"E1202"),sQuery(id+"F9.wireOp",EDGE,"E1203"),sQuery(id+"F9.wireOp",EDGE,"E1204"),sQuery(id+"F9.wireOp",EDGE,"E1205"),sQuery(id+"F9.wireOp",EDGE,"E1206"),sQuery(id+"F9.wireOp",EDGE,"E1207"),sQuery(id+"F9.wireOp",EDGE,"E1208"),sQuery(id+"F9.wireOp",EDGE,"E1209"),sQuery(id+"F9.wireOp",EDGE,"E1210"),sQuery(id+"F9.wireOp",EDGE,"E1211"),sQuery(id+"F9.wireOp",EDGE,"E1212"),sQuery(id+"F9.wireOp",EDGE,"E1213"),sQuery(id+"F9.wireOp",EDGE,"E1214"),sQuery(id+"F9.wireOp",EDGE,"E1215"),sQuery(id+"F9.wireOp",EDGE,"E1216"),sQuery(id+"F9.wireOp",EDGE,"E1217"),sQuery(id+"F9.wireOp",EDGE,"E1218"),sQuery(id+"F9.wireOp",EDGE,"E1219"),sQuery(id+"F9.wireOp",EDGE,"E1220"),sQuery(id+"F9.wireOp",EDGE,"E1221"),sQuery(id+"F9.wireOp",EDGE,"E1222"),sQuery(id+"F9.wireOp",EDGE,"E1223"),sQuery(id+"F9.wireOp",EDGE,"E1224"),sQuery(id+"F9.wireOp",EDGE,"E1225"),sQuery(id+"F9.wireOp",EDGE,"E1226"),sQuery(id+"F9.wireOp",EDGE,"E1227"),sQuery(id+"F9.wireOp",EDGE,"E1228"),sQuery(id+"F9.wireOp",EDGE,"E1229"),sQuery(id+"F9.wireOp",EDGE,"E1230"),sQuery(id+"F9.wireOp",EDGE,"E1231"),sQuery(id+"F9.wireOp",EDGE,"E1232"),sQuery(id+"F9.wireOp",EDGE,"E1233"),sQuery(id+"F9.wireOp",EDGE,"E1234"),sQuery(id+"F9.wireOp",EDGE,"E1235"),sQuery(id+"F9.wireOp",EDGE,"E1236"),sQuery(id+"F9.wireOp",EDGE,"E1237"),sQuery(id+"F9.wireOp",EDGE,"E1238"),sQuery(id+"F9.wireOp",EDGE,"E1239"),sQuery(id+"F9.wireOp",EDGE,"E1240"),sQuery(id+"F9.wireOp",EDGE,"E1241"),sQuery(id+"F9.wireOp",EDGE,"E1242"),sQuery(id+"F9.wireOp",EDGE,"E1243"),sQuery(id+"F9.wireOp",EDGE,"E1244"),sQuery(id+"F9.wireOp",EDGE,"E1245"),sQuery(id+"F9.wireOp",EDGE,"E1246"),sQuery(id+"F9.wireOp",EDGE,"E1247"),sQuery(id+"F9.wireOp",EDGE,"E1248"),sQuery(id+"F9.wireOp",EDGE,"E1249"),sQuery(id+"F9.wireOp",EDGE,"E1250"),sQuery(id+"F9.wireOp",EDGE,"E1251"),sQuery(id+"F9.wireOp",EDGE,"E1252"),sQuery(id+"F9.wireOp",EDGE,"E1253"),sQuery(id+"F9.wireOp",EDGE,"E1254"),sQuery(id+"F9.wireOp",EDGE,"E1255"),sQuery(id+"F9.wireOp",EDGE,"E1256"),sQuery(id+"F9.wireOp",EDGE,"E1257"),sQuery(id+"F9.wireOp",EDGE,"E1258"),sQuery(id+"F9.wireOp",EDGE,"E1259"),sQuery(id+"F9.wireOp",EDGE,"E1260"),sQuery(id+"F9.wireOp",EDGE,"E1261"),sQuery(id+"F9.wireOp",EDGE,"E1262"),sQuery(id+"F9.wireOp",EDGE,"E1263"),sQuery(id+"F9.wireOp",EDGE,"E1264"),sQuery(id+"F9.wireOp",EDGE,"E1265"),sQuery(id+"F9.wireOp",EDGE,"E1266"),sQuery(id+"F9.wireOp",EDGE,"E1267"),sQuery(id+"F9.wireOp",EDGE,"E1268"),sQuery(id+"F9.wireOp",EDGE,"E1269"),sQuery(id+"F9.wireOp",EDGE,"E1270"),sQuery(id+"F9.wireOp",EDGE,"E1271"),sQuery(id+"F9.wireOp",EDGE,"E1272"),sQuery(id+"F9.wireOp",EDGE,"E1273"),sQuery(id+"F9.wireOp",EDGE,"E1274"),sQuery(id+"F9.wireOp",EDGE,"E1275"),sQuery(id+"F9.wireOp",EDGE,"E1276"),sQuery(id+"F9.wireOp",EDGE,"E1277"),sQuery(id+"F9.wireOp",EDGE,"E1278"),sQuery(id+"F9.wireOp",EDGE,"E1279"),sQuery(id+"F9.wireOp",EDGE,"E1280"),sQuery(id+"F9.wireOp",EDGE,"E1281"),sQuery(id+"F9.wireOp",EDGE,"E1282"),sQuery(id+"F9.wireOp",EDGE,"E1283"),sQuery(id+"F9.wireOp",EDGE,"E1284"),sQuery(id+"F9.wireOp",EDGE,"E1285"),sQuery(id+"F9.wireOp",EDGE,"E1286"),sQuery(id+"F9.wireOp",EDGE,"E1287"),sQuery(id+"F9.wireOp",EDGE,"E1288"),sQuery(id+"F9.wireOp",EDGE,"E1289"),sQuery(id+"F9.wireOp",EDGE,"E1290"),sQuery(id+"F9.wireOp",EDGE,"E1291"),sQuery(id+"F9.wireOp",EDGE,"E1292"),sQuery(id+"F9.wireOp",EDGE,"E1293"),sQuery(id+"F9.wireOp",EDGE,"E1294"),sQuery(id+"F9.wireOp",EDGE,"E1295"),sQuery(id+"F9.wireOp",EDGE,"E1296"),sQuery(id+"F9.wireOp",EDGE,"E1297"),sQuery(id+"F9.wireOp",EDGE,"E1298"),sQuery(id+"F9.wireOp",EDGE,"E1299"),sQuery(id+"F9.wireOp",EDGE,"E1300"),sQuery(id+"F9.wireOp",EDGE,"E1301"),sQuery(id+"F9.wireOp",EDGE,"E1302"),sQuery(id+"F9.wireOp",EDGE,"E1303"),sQuery(id+"F9.wireOp",EDGE,"E1304"),sQuery(id+"F9.wireOp",EDGE,"E1305"),sQuery(id+"F9.wireOp",EDGE,"E1306"),sQuery(id+"F9.wireOp",EDGE,"E1307"),sQuery(id+"F9.wireOp",EDGE,"E1308"),sQuery(id+"F9.wireOp",EDGE,"E1309"),sQuery(id+"F9.wireOp",EDGE,"E1310"),sQuery(id+"F9.wireOp",EDGE,"E1311"),sQuery(id+"F9.wireOp",EDGE,"E1312"),sQuery(id+"F9.wireOp",EDGE,"E1313"),sQuery(id+"F9.wireOp",EDGE,"E1314"),sQuery(id+"F9.wireOp",EDGE,"E1315"),sQuery(id+"F9.wireOp",EDGE,"E1316"),sQuery(id+"F9.wireOp",EDGE,"E1317"),sQuery(id+"F9.wireOp",EDGE,"E1318"),sQuery(id+"F9.wireOp",EDGE,"E1319"),sQuery(id+"F9.wireOp",EDGE,"E1320"),sQuery(id+"F9.wireOp",EDGE,"E1321"),sQuery(id+"F9.wireOp",EDGE,"E1322"),sQuery(id+"F9.wireOp",EDGE,"E1323"),sQuery(id+"F9.wireOp",EDGE,"E1324"),sQuery(id+"F9.wireOp",EDGE,"E1325"),sQuery(id+"F9.wireOp",EDGE,"E1326"),sQuery(id+"F9.wireOp",EDGE,"E1327"),sQuery(id+"F9.wireOp",EDGE,"E1328"),sQuery(id+"F9.wireOp",EDGE,"E1329"),sQuery(id+"F9.wireOp",EDGE,"E1330"),sQuery(id+"F9.wireOp",EDGE,"E1331"),sQuery(id+"F9.wireOp",EDGE,"E1332"),sQuery(id+"F9.wireOp",EDGE,"E1333"),sQuery(id+"F9.wireOp",EDGE,"E1334"),sQuery(id+"F9.wireOp",EDGE,"E1335"),sQuery(id+"F9.wireOp",EDGE,"E1336"),sQuery(id+"F9.wireOp",EDGE,"E1337"),sQuery(id+"F9.wireOp",EDGE,"E1338"),sQuery(id+"F9.wireOp",EDGE,"E1339"),sQuery(id+"F9.wireOp",EDGE,"E1340"),sQuery(id+"F9.wireOp",EDGE,"E1341"),sQuery(id+"F9.wireOp",EDGE,"E1342"),sQuery(id+"F9.wireOp",EDGE,"E1343"),sQuery(id+"F9.wireOp",EDGE,"E1344"),sQuery(id+"F9.wireOp",EDGE,"E1345"),sQuery(id+"F9.wireOp",EDGE,"E1346"),sQuery(id+"F9.wireOp",EDGE,"E1347"),sQuery(id+"F9.wireOp",EDGE,"E1348"),sQuery(id+"F9.wireOp",EDGE,"E1349"),sQuery(id+"F9.wireOp",EDGE,"E1350"),sQuery(id+"F9.wireOp",EDGE,"E1351"),sQuery(id+"F9.wireOp",EDGE,"E1352"),sQuery(id+"F9.wireOp",EDGE,"E1353"),sQuery(id+"F9.wireOp",EDGE,"E1354"),sQuery(id+"F9.wireOp",EDGE,"E1355"),sQuery(id+"F9.wireOp",EDGE,"E1356"),sQuery(id+"F9.wireOp",EDGE,"E1357"),sQuery(id+"F9.wireOp",EDGE,"E1358"),sQuery(id+"F9.wireOp",EDGE,"E1359"),sQuery(id+"F9.wireOp",EDGE,"E1360"),sQuery(id+"F9.wireOp",EDGE,"E1361"),sQuery(id+"F9.wireOp",EDGE,"E1362"),sQuery(id+"F9.wireOp",EDGE,"E1363"),sQuery(id+"F9.wireOp",EDGE,"E1364"),sQuery(id+"F9.wireOp",EDGE,"E1365"),sQuery(id+"F9.wireOp",EDGE,"E1366"),sQuery(id+"F9.wireOp",EDGE,"E1367"),sQuery(id+"F9.wireOp",EDGE,"E1368"),sQuery(id+"F9.wireOp",EDGE,"E1369"),sQuery(id+"F9.wireOp",EDGE,"E1370"),sQuery(id+"F9.wireOp",EDGE,"E1371"),sQuery(id+"F9.wireOp",EDGE,"E1372"),sQuery(id+"F9.wireOp",EDGE,"E1373"),sQuery(id+"F9.wireOp",EDGE,"E1374"),sQuery(id+"F9.wireOp",EDGE,"E1375"),sQuery(id+"F9.wireOp",EDGE,"E1376"),sQuery(id+"F9.wireOp",EDGE,"E1377"),sQuery(id+"F9.wireOp",EDGE,"E1378"),sQuery(id+"F9.wireOp",EDGE,"E1379"),sQuery(id+"F9.wireOp",EDGE,"E1380"),sQuery(id+"F9.wireOp",EDGE,"E1381"),sQuery(id+"F9.wireOp",EDGE,"E1382"),sQuery(id+"F9.wireOp",EDGE,"E1383"),sQuery(id+"F9.wireOp",EDGE,"E1384"),sQuery(id+"F9.wireOp",EDGE,"E1385"),sQuery(id+"F9.wireOp",EDGE,"E1386"),sQuery(id+"F9.wireOp",EDGE,"E1387"),sQuery(id+"F9.wireOp",EDGE,"E1388"),sQuery(id+"F9.wireOp",EDGE,"E1389"),sQuery(id+"F9.wireOp",EDGE,"E1390"),sQuery(id+"F9.wireOp",EDGE,"E1391"),sQuery(id+"F9.wireOp",EDGE,"E1392"),sQuery(id+"F9.wireOp",EDGE,"E1393"),sQuery(id+"F9.wireOp",EDGE,"E1394"),sQuery(id+"F9.wireOp",EDGE,"E1395"),sQuery(id+"F9.wireOp",EDGE,"E1396"),sQuery(id+"F9.wireOp",EDGE,"E1397"),sQuery(id+"F9.wireOp",EDGE,"E1398"),sQuery(id+"F9.wireOp",EDGE,"E1399"),sQuery(id+"F9.wireOp",EDGE,"E1400"),sQuery(id+"F9.wireOp",EDGE,"E1401"),sQuery(id+"F9.wireOp",EDGE,"E1402"),sQuery(id+"F9.wireOp",EDGE,"E1403"),sQuery(id+"F9.wireOp",EDGE,"E1404"),sQuery(id+"F9.wireOp",EDGE,"E1405"),sQuery(id+"F9.wireOp",EDGE,"E1406"),sQuery(id+"F9.wireOp",EDGE,"E1407"),sQuery(id+"F9.wireOp",EDGE,"E1408"),sQuery(id+"F9.wireOp",EDGE,"E1409"),sQuery(id+"F9.wireOp",EDGE,"E1410"),sQuery(id+"F9.wireOp",EDGE,"E1411"),sQuery(id+"F9.wireOp",EDGE,"E1412"),sQuery(id+"F9.wireOp",EDGE,"E1413"),sQuery(id+"F9.wireOp",EDGE,"E1414"),sQuery(id+"F9.wireOp",EDGE,"E1415"),sQuery(id+"F9.wireOp",EDGE,"E1416"),sQuery(id+"F9.wireOp",EDGE,"E1417"),sQuery(id+"F9.wireOp",EDGE,"E1418"),sQuery(id+"F9.wireOp",EDGE,"E1419"),sQuery(id+"F9.wireOp",EDGE,"E1420"),sQuery(id+"F9.wireOp",EDGE,"E1421"),sQuery(id+"F9.wireOp",EDGE,"E1422"),sQuery(id+"F9.wireOp",EDGE,"E1423"),sQuery(id+"F9.wireOp",EDGE,"E1424"),sQuery(id+"F9.wireOp",EDGE,"E1425"),sQuery(id+"F9.wireOp",EDGE,"E1426"),sQuery(id+"F9.wireOp",EDGE,"E1427"),sQuery(id+"F9.wireOp",EDGE,"E1428"),sQuery(id+"F9.wireOp",EDGE,"E1429"),sQuery(id+"F9.wireOp",EDGE,"E1430"),sQuery(id+"F9.wireOp",EDGE,"E1431"),sQuery(id+"F9.wireOp",EDGE,"E1432"),sQuery(id+"F9.wireOp",EDGE,"E1433"),sQuery(id+"F9.wireOp",EDGE,"E1434"),sQuery(id+"F9.wireOp",EDGE,"E1435"),sQuery(id+"F9.wireOp",EDGE,"E1436"),sQuery(id+"F9.wireOp",EDGE,"E1437"),sQuery(id+"F9.wireOp",EDGE,"E1438"),sQuery(id+"F9.wireOp",EDGE,"E1439"),sQuery(id+"F9.wireOp",EDGE,"E1440"),sQuery(id+"F9.wireOp",EDGE,"E1441"),sQuery(id+"F9.wireOp",EDGE,"E1442"),sQuery(id+"F9.wireOp",EDGE,"E1443"),sQuery(id+"F9.wireOp",EDGE,"E1444"),sQuery(id+"F9.wireOp",EDGE,"E1445"),sQuery(id+"F9.wireOp",EDGE,"E1446"),sQuery(id+"F9.wireOp",EDGE,"E1447"),sQuery(id+"F9.wireOp",EDGE,"E1448"),sQuery(id+"F9.wireOp",EDGE,"E1449"),sQuery(id+"F9.wireOp",EDGE,"E1450"),sQuery(id+"F9.wireOp",EDGE,"E1451"),sQuery(id+"F9.wireOp",EDGE,"E1452"),sQuery(id+"F9.wireOp",EDGE,"E1453"),sQuery(id+"F9.wireOp",EDGE,"E1454"),sQuery(id+"F9.wireOp",EDGE,"E1455"),sQuery(id+"F9.wireOp",EDGE,"E1456"),sQuery(id+"F9.wireOp",EDGE,"E1457"),sQuery(id+"F9.wireOp",EDGE,"E1458"),sQuery(id+"F9.wireOp",EDGE,"E1459"),sQuery(id+"F9.wireOp",EDGE,"E1460"),sQuery(id+"F9.wireOp",EDGE,"E1461"),sQuery(id+"F9.wireOp",EDGE,"E1462"),sQuery(id+"F9.wireOp",EDGE,"E1463"),sQuery(id+"F9.wireOp",EDGE,"E1464"),sQuery(id+"F9.wireOp",EDGE,"E1465"),sQuery(id+"F9.wireOp",EDGE,"E1466"),sQuery(id+"F9.wireOp",EDGE,"E1467"),sQuery(id+"F9.wireOp",EDGE,"E1468"),sQuery(id+"F9.wireOp",EDGE,"E1469"),sQuery(id+"F9.wireOp",EDGE,"E1470"),sQuery(id+"F9.wireOp",EDGE,"E1471"),sQuery(id+"F9.wireOp",EDGE,"E1472"),sQuery(id+"F9.wireOp",EDGE,"E1473"),sQuery(id+"F9.wireOp",EDGE,"E1474"),sQuery(id+"F9.wireOp",EDGE,"E1475"),sQuery(id+"F9.wireOp",EDGE,"E1476"),sQuery(id+"F9.wireOp",EDGE,"E1477"),sQuery(id+"F9.wireOp",EDGE,"E1478"),sQuery(id+"F9.wireOp",EDGE,"E1479"),sQuery(id+"F9.wireOp",EDGE,"E1480"),sQuery(id+"F9.wireOp",EDGE,"E1481"),sQuery(id+"F9.wireOp",EDGE,"E1482"),sQuery(id+"F9.wireOp",EDGE,"E1483"),sQuery(id+"F9.wireOp",EDGE,"E1484"),sQuery(id+"F9.wireOp",EDGE,"E1485"),sQuery(id+"F9.wireOp",EDGE,"E1486"),sQuery(id+"F9.wireOp",EDGE,"E1487"),sQuery(id+"F9.wireOp",EDGE,"E1488"),sQuery(id+"F9.wireOp",EDGE,"E1489"),sQuery(id+"F9.wireOp",EDGE,"E1490"),sQuery(id+"F9.wireOp",EDGE,"E1491"),sQuery(id+"F9.wireOp",EDGE,"E1492"),sQuery(id+"F9.wireOp",EDGE,"E1493"),sQuery(id+"F9.wireOp",EDGE,"E1494"),sQuery(id+"F9.wireOp",EDGE,"E1495"),sQuery(id+"F9.wireOp",EDGE,"E1496"),sQuery(id+"F9.wireOp",EDGE,"E1497"),sQuery(id+"F9.wireOp",EDGE,"E1498"),sQuery(id+"F9.wireOp",EDGE,"E1499"),sQuery(id+"F9.wireOp",EDGE,"E1500"),sQuery(id+"F9.wireOp",EDGE,"E1501"),sQuery(id+"F9.wireOp",EDGE,"E1502"),sQuery(id+"F9.wireOp",EDGE,"E1503"),sQuery(id+"F9.wireOp",EDGE,"E1504"),sQuery(id+"F9.wireOp",EDGE,"E1505"),sQuery(id+"F9.wireOp",EDGE,"E1506"),sQuery(id+"F9.wireOp",EDGE,"E1507"),sQuery(id+"F9.wireOp",EDGE,"E1508"),sQuery(id+"F9.wireOp",EDGE,"E1509"),sQuery(id+"F9.wireOp",EDGE,"E1510"),sQuery(id+"F9.wireOp",EDGE,"E1511"),sQuery(id+"F9.wireOp",EDGE,"E1512"),sQuery(id+"F9.wireOp",EDGE,"E1513"),sQuery(id+"F9.wireOp",EDGE,"E1514"),sQuery(id+"F9.wireOp",EDGE,"E1515"),sQuery(id+"F9.wireOp",EDGE,"E1516"),sQuery(id+"F9.wireOp",EDGE,"E1517"),sQuery(id+"F9.wireOp",EDGE,"E1518"),sQuery(id+"F9.wireOp",EDGE,"E1519"),sQuery(id+"F9.wireOp",EDGE,"E1520"),sQuery(id+"F9.wireOp",EDGE,"E1521"),sQuery(id+"F9.wireOp",EDGE,"E1522"),sQuery(id+"F9.wireOp",EDGE,"E1523"),sQuery(id+"F9.wireOp",EDGE,"E1524"),sQuery(id+"F9.wireOp",EDGE,"E1525"),sQuery(id+"F9.wireOp",EDGE,"E1526"),sQuery(id+"F9.wireOp",EDGE,"E1527"),sQuery(id+"F9.wireOp",EDGE,"E1528"),sQuery(id+"F9.wireOp",EDGE,"E1529"),sQuery(id+"F9.wireOp",EDGE,"E1530"),sQuery(id+"F9.wireOp",EDGE,"E1531"),sQuery(id+"F9.wireOp",EDGE,"E1532"),sQuery(id+"F9.wireOp",EDGE,"E1533"),sQuery(id+"F9.wireOp",EDGE,"E1534"),sQuery(id+"F9.wireOp",EDGE,"E1535"),sQuery(id+"F9.wireOp",EDGE,"E1536"),sQuery(id+"F9.wireOp",EDGE,"E1537"),sQuery(id+"F9.wireOp",EDGE,"E1538"),sQuery(id+"F9.wireOp",EDGE,"E1539"),sQuery(id+"F9.wireOp",EDGE,"E1540"),sQuery(id+"F9.wireOp",EDGE,"E1541"),sQuery(id+"F9.wireOp",EDGE,"E1542"),sQuery(id+"F9.wireOp",EDGE,"E1543"),sQuery(id+"F9.wireOp",EDGE,"E1544"),sQuery(id+"F9.wireOp",EDGE,"E1545"),sQuery(id+"F9.wireOp",EDGE,"E1546"),sQuery(id+"F9.wireOp",EDGE,"E1547"),sQuery(id+"F9.wireOp",EDGE,"E1548"),sQuery(id+"F9.wireOp",EDGE,"E1549"),sQuery(id+"F9.wireOp",EDGE,"E1550"),sQuery(id+"F9.wireOp",EDGE,"E1551"),sQuery(id+"F9.wireOp",EDGE,"E1552"),sQuery(id+"F9.wireOp",EDGE,"E1553"),sQuery(id+"F9.wireOp",EDGE,"E1554"),sQuery(id+"F9.wireOp",EDGE,"E1555"),sQuery(id+"F9.wireOp",EDGE,"E1556"),sQuery(id+"F9.wireOp",EDGE,"E1557"),sQuery(id+"F9.wireOp",EDGE,"E1558"),sQuery(id+"F9.wireOp",EDGE,"E1559"),sQuery(id+"F9.wireOp",EDGE,"E1560"),sQuery(id+"F9.wireOp",EDGE,"E1561"),sQuery(id+"F9.wireOp",EDGE,"E1562"),sQuery(id+"F9.wireOp",EDGE,"E1563"),sQuery(id+"F9.wireOp",EDGE,"E1564"),sQuery(id+"F9.wireOp",EDGE,"E1565"),sQuery(id+"F9.wireOp",EDGE,"E1566"),sQuery(id+"F9.wireOp",EDGE,"E1567"),sQuery(id+"F9.wireOp",EDGE,"E1568"),sQuery(id+"F9.wireOp",EDGE,"E1569"),sQuery(id+"F9.wireOp",EDGE,"E1570"),sQuery(id+"F9.wireOp",EDGE,"E1571"),sQuery(id+"F9.wireOp",EDGE,"E1572"),sQuery(id+"F9.wireOp",EDGE,"E1573"),sQuery(id+"F9.wireOp",EDGE,"E1574"),sQuery(id+"F9.wireOp",EDGE,"E1575"),sQuery(id+"F9.wireOp",EDGE,"E1576"),sQuery(id+"F9.wireOp",EDGE,"E1577"),sQuery(id+"F9.wireOp",EDGE,"E1578"),sQuery(id+"F9.wireOp",EDGE,"E1579"),sQuery(id+"F9.wireOp",EDGE,"E1580"),sQuery(id+"F9.wireOp",EDGE,"E1581"),sQuery(id+"F9.wireOp",EDGE,"E1582"),sQuery(id+"F9.wireOp",EDGE,"E1583"),sQuery(id+"F9.wireOp",EDGE,"E1584"),sQuery(id+"F9.wireOp",EDGE,"E1585"),sQuery(id+"F9.wireOp",EDGE,"E1586"),sQuery(id+"F9.wireOp",EDGE,"E1587"),sQuery(id+"F9.wireOp",EDGE,"E1588"),sQuery(id+"F9.wireOp",EDGE,"E1589"),sQuery(id+"F9.wireOp",EDGE,"E1590"),sQuery(id+"F9.wireOp",EDGE,"E1591"),sQuery(id+"F9.wireOp",EDGE,"E1592"),sQuery(id+"F9.wireOp",EDGE,"E1593"),sQuery(id+"F9.wireOp",EDGE,"E1594"),sQuery(id+"F9.wireOp",EDGE,"E1595"),sQuery(id+"F9.wireOp",EDGE,"E1596"),sQuery(id+"F9.wireOp",EDGE,"E1597"),sQuery(id+"F9.wireOp",EDGE,"E1598"),sQuery(id+"F9.wireOp",EDGE,"E1599"),sQuery(id+"F9.wireOp",EDGE,"E1600"),sQuery(id+"F9.wireOp",EDGE,"E1601"),sQuery(id+"F9.wireOp",EDGE,"E1602"),sQuery(id+"F9.wireOp",EDGE,"E1603"),sQuery(id+"F9.wireOp",EDGE,"E1604"),sQuery(id+"F9.wireOp",EDGE,"E1605"),sQuery(id+"F9.wireOp",EDGE,"E1606"),sQuery(id+"F9.wireOp",EDGE,"E1607"),sQuery(id+"F9.wireOp",EDGE,"E1608"),sQuery(id+"F9.wireOp",EDGE,"E1609"),sQuery(id+"F9.wireOp",EDGE,"E1610"),sQuery(id+"F9.wireOp",EDGE,"E1611"),sQuery(id+"F9.wireOp",EDGE,"E1612"),sQuery(id+"F9.wireOp",EDGE,"E1613"),sQuery(id+"F9.wireOp",EDGE,"E1614"),sQuery(id+"F9.wireOp",EDGE,"E1615"),sQuery(id+"F9.wireOp",EDGE,"E1616"),sQuery(id+"F9.wireOp",EDGE,"E1617"),sQuery(id+"F9.wireOp",EDGE,"E1618"),sQuery(id+"F9.wireOp",EDGE,"E1619"),sQuery(id+"F9.wireOp",EDGE,"E1620"),sQuery(id+"F9.wireOp",EDGE,"E1621"),sQuery(id+"F9.wireOp",EDGE,"E1622"),sQuery(id+"F9.wireOp",EDGE,"E1623"),sQuery(id+"F9.wireOp",EDGE,"E1624"),sQuery(id+"F9.wireOp",EDGE,"E1625"),sQuery(id+"F9.wireOp",EDGE,"E1626"),sQuery(id+"F9.wireOp",EDGE,"E1627"),sQuery(id+"F9.wireOp",EDGE,"E1628"),sQuery(id+"F9.wireOp",EDGE,"E1629"),sQuery(id+"F9.wireOp",EDGE,"E1630"),sQuery(id+"F9.wireOp",EDGE,"E1631"),sQuery(id+"F9.wireOp",EDGE,"E1632"),sQuery(id+"F9.wireOp",EDGE,"E1633"),sQuery(id+"F9.wireOp",EDGE,"E1634"),sQuery(id+"F9.wireOp",EDGE,"E1635"),sQuery(id+"F9.wireOp",EDGE,"E1636"),sQuery(id+"F9.wireOp",EDGE,"E1637"),sQuery(id+"F9.wireOp",EDGE,"E1638"),sQuery(id+"F9.wireOp",EDGE,"E1639"),sQuery(id+"F9.wireOp",EDGE,"E1640"),sQuery(id+"F9.wireOp",EDGE,"E1641"),sQuery(id+"F9.wireOp",EDGE,"E1642"),sQuery(id+"F9.wireOp",EDGE,"E1643"),sQuery(id+"F9.wireOp",EDGE,"E1644"),sQuery(id+"F9.wireOp",EDGE,"E1645"),sQuery(id+"F9.wireOp",EDGE,"E1646"),sQuery(id+"F9.wireOp",EDGE,"E1647"),sQuery(id+"F9.wireOp",EDGE,"E1648"),sQuery(id+"F9.wireOp",EDGE,"E1649"),sQuery(id+"F9.wireOp",EDGE,"E1650"),sQuery(id+"F9.wireOp",EDGE,"E1651"),sQuery(id+"F9.wireOp",EDGE,"E1652"),sQuery(id+"F9.wireOp",EDGE,"E1653"),sQuery(id+"F9.wireOp",EDGE,"E1654"),sQuery(id+"F9.wireOp",EDGE,"E1655"),sQuery(id+"F9.wireOp",EDGE,"E1656"),sQuery(id+"F9.wireOp",EDGE,"E1657"),sQuery(id+"F9.wireOp",EDGE,"E1658"),sQuery(id+"F9.wireOp",EDGE,"E1659"),sQuery(id+"F9.wireOp",EDGE,"E1660"),sQuery(id+"F9.wireOp",EDGE,"E1661"),sQuery(id+"F9.wireOp",EDGE,"E1662"),sQuery(id+"F9.wireOp",EDGE,"E1663"),sQuery(id+"F9.wireOp",EDGE,"E1664"),sQuery(id+"F9.wireOp",EDGE,"E1665"),sQuery(id+"F9.wireOp",EDGE,"E1666"),sQuery(id+"F9.wireOp",EDGE,"E1667"),sQuery(id+"F9.wireOp",EDGE,"E1668"),sQuery(id+"F9.wireOp",EDGE,"E1669"),sQuery(id+"F9.wireOp",EDGE,"E1670"),sQuery(id+"F9.wireOp",EDGE,"E1671"),sQuery(id+"F9.wireOp",EDGE,"E1672"),sQuery(id+"F9.wireOp",EDGE,"E1673"),sQuery(id+"F9.wireOp",EDGE,"E1674"),sQuery(id+"F9.wireOp",EDGE,"E1675"),sQuery(id+"F9.wireOp",EDGE,"E1676"),sQuery(id+"F9.wireOp",EDGE,"E1677"),sQuery(id+"F9.wireOp",EDGE,"E1678"),sQuery(id+"F9.wireOp",EDGE,"E1679"),sQuery(id+"F9.wireOp",EDGE,"E1680"),sQuery(id+"F9.wireOp",EDGE,"E1681"),sQuery(id+"F9.wireOp",EDGE,"E1682"),sQuery(id+"F9.wireOp",EDGE,"E1683"),sQuery(id+"F9.wireOp",EDGE,"E1684"),sQuery(id+"F9.wireOp",EDGE,"E1685"),sQuery(id+"F9.wireOp",EDGE,"E1686"),sQuery(id+"F9.wireOp",EDGE,"E1687"),sQuery(id+"F9.wireOp",EDGE,"E1688"),sQuery(id+"F9.wireOp",EDGE,"E1689"),sQuery(id+"F9.wireOp",EDGE,"E1690"),sQuery(id+"F9.wireOp",EDGE,"E1691"),sQuery(id+"F9.wireOp",EDGE,"E1692"),sQuery(id+"F9.wireOp",EDGE,"E1693"),sQuery(id+"F9.wireOp",EDGE,"E1694"),sQuery(id+"F9.wireOp",EDGE,"E1695"),sQuery(id+"F9.wireOp",EDGE,"E1696"),sQuery(id+"F9.wireOp",EDGE,"E1697"),sQuery(id+"F9.wireOp",EDGE,"E1698"),sQuery(id+"F9.wireOp",EDGE,"E1699"),sQuery(id+"F9.wireOp",EDGE,"E1700"),sQuery(id+"F9.wireOp",EDGE,"E1701"),sQuery(id+"F9.wireOp",EDGE,"E1702"),sQuery(id+"F9.wireOp",EDGE,"E1703"),sQuery(id+"F9.wireOp",EDGE,"E1704"),sQuery(id+"F9.wireOp",EDGE,"E1705"),sQuery(id+"F9.wireOp",EDGE,"E1706"),sQuery(id+"F9.wireOp",EDGE,"E1707"),sQuery(id+"F9.wireOp",EDGE,"E1708"),sQuery(id+"F9.wireOp",EDGE,"E1709"),sQuery(id+"F9.wireOp",EDGE,"E1710"),sQuery(id+"F9.wireOp",EDGE,"E1711"),sQuery(id+"F9.wireOp",EDGE,"E1712"),sQuery(id+"F9.wireOp",EDGE,"E1713"),sQuery(id+"F9.wireOp",EDGE,"E1714"),sQuery(id+"F9.wireOp",EDGE,"E1715"),sQuery(id+"F9.wireOp",EDGE,"E1716"),sQuery(id+"F9.wireOp",EDGE,"E1717"),sQuery(id+"F9.wireOp",EDGE,"E1718"),sQuery(id+"F9.wireOp",EDGE,"E1719"),sQuery(id+"F9.wireOp",EDGE,"E1720"),sQuery(id+"F9.wireOp",EDGE,"E1721"),sQuery(id+"F9.wireOp",EDGE,"E1722"),sQuery(id+"F9.wireOp",EDGE,"E1723"),sQuery(id+"F9.wireOp",EDGE,"E1724"),sQuery(id+"F9.wireOp",EDGE,"E1725"),sQuery(id+"F9.wireOp",EDGE,"E1726"),sQuery(id+"F9.wireOp",EDGE,"E1727"),sQuery(id+"F9.wireOp",EDGE,"E1728"),sQuery(id+"F9.wireOp",EDGE,"E1729"),sQuery(id+"F9.wireOp",EDGE,"E1730"),sQuery(id+"F9.wireOp",EDGE,"E1731"),sQuery(id+"F9.wireOp",EDGE,"E1732"),sQuery(id+"F9.wireOp",EDGE,"E1733"),sQuery(id+"F9.wireOp",EDGE,"E1734"),sQuery(id+"F9.wireOp",EDGE,"E1735"),sQuery(id+"F9.wireOp",EDGE,"E1736"),sQuery(id+"F9.wireOp",EDGE,"E1737"),sQuery(id+"F9.wireOp",EDGE,"E1738"),sQuery(id+"F9.wireOp",EDGE,"E1739"),sQuery(id+"F9.wireOp",EDGE,"E1740"),sQuery(id+"F9.wireOp",EDGE,"E1741"),sQuery(id+"F9.wireOp",EDGE,"E1742"),sQuery(id+"F9.wireOp",EDGE,"E1743"),sQuery(id+"F9.wireOp",EDGE,"E1744"),sQuery(id+"F9.wireOp",EDGE,"E1745"),sQuery(id+"F9.wireOp",EDGE,"E1746"),sQuery(id+"F9.wireOp",EDGE,"E1747"),sQuery(id+"F9.wireOp",EDGE,"E1748"),sQuery(id+"F9.wireOp",EDGE,"E1749"),sQuery(id+"F9.wireOp",EDGE,"E1750"),sQuery(id+"F9.wireOp",EDGE,"E1751"),sQuery(id+"F9.wireOp",EDGE,"E1752"),sQuery(id+"F9.wireOp",EDGE,"E1753"),sQuery(id+"F9.wireOp",EDGE,"E1754"),sQuery(id+"F9.wireOp",EDGE,"E1755"),sQuery(id+"F9.wireOp",EDGE,"E1756"),sQuery(id+"F9.wireOp",EDGE,"E1757"),sQuery(id+"F9.wireOp",EDGE,"E1758"),sQuery(id+"F9.wireOp",EDGE,"E1759"),sQuery(id+"F9.wireOp",EDGE,"E1760"),sQuery(id+"F9.wireOp",EDGE,"E1761"),sQuery(id+"F9.wireOp",EDGE,"E1762"),sQuery(id+"F9.wireOp",EDGE,"E1763"),sQuery(id+"F9.wireOp",EDGE,"E1764"),sQuery(id+"F9.wireOp",EDGE,"E1765"),sQuery(id+"F9.wireOp",EDGE,"E1766"),sQuery(id+"F9.wireOp",EDGE,"E1767"),sQuery(id+"F9.wireOp",EDGE,"E1768"),sQuery(id+"F9.wireOp",EDGE,"E1769"),sQuery(id+"F9.wireOp",EDGE,"E1770"),sQuery(id+"F9.wireOp",EDGE,"E1771"),sQuery(id+"F9.wireOp",EDGE,"E1772"),sQuery(id+"F9.wireOp",EDGE,"E1773"),sQuery(id+"F9.wireOp",EDGE,"E1774"),sQuery(id+"F9.wireOp",EDGE,"E1775"),sQuery(id+"F9.wireOp",EDGE,"E1776"),sQuery(id+"F9.wireOp",EDGE,"E1777"),sQuery(id+"F9.wireOp",EDGE,"E1778"),sQuery(id+"F9.wireOp",EDGE,"E1779"),sQuery(id+"F9.wireOp",EDGE,"E1780"),sQuery(id+"F9.wireOp",EDGE,"E1781"),sQuery(id+"F9.wireOp",EDGE,"E1782"),sQuery(id+"F9.wireOp",EDGE,"E1783"),sQuery(id+"F9.wireOp",EDGE,"E1784"),sQuery(id+"F9.wireOp",EDGE,"E1785"),sQuery(id+"F9.wireOp",EDGE,"E1786"),sQuery(id+"F9.wireOp",EDGE,"E1787"),sQuery(id+"F9.wireOp",EDGE,"E1788"),sQuery(id+"F9.wireOp",EDGE,"E1789"),sQuery(id+"F9.wireOp",EDGE,"E1790"),sQuery(id+"F9.wireOp",EDGE,"E1791"),sQuery(id+"F9.wireOp",EDGE,"E1792"),sQuery(id+"F9.wireOp",EDGE,"E1793"),sQuery(id+"F9.wireOp",EDGE,"E1794"),sQuery(id+"F9.wireOp",EDGE,"E1795"),sQuery(id+"F9.wireOp",EDGE,"E1796"),sQuery(id+"F9.wireOp",EDGE,"E1797"),sQuery(id+"F9.wireOp",EDGE,"E1798"),sQuery(id+"F9.wireOp",EDGE,"E1799"),sQuery(id+"F9.wireOp",EDGE,"E1800"),sQuery(id+"F9.wireOp",EDGE,"E1801"),sQuery(id+"F9.wireOp",EDGE,"E1802"),sQuery(id+"F9.wireOp",EDGE,"E1803"),sQuery(id+"F9.wireOp",EDGE,"E1804"),sQuery(id+"F9.wireOp",EDGE,"E1805"),sQuery(id+"F9.wireOp",EDGE,"E1806"),sQuery(id+"F9.wireOp",EDGE,"E1807"),sQuery(id+"F9.wireOp",EDGE,"E1808"),sQuery(id+"F9.wireOp",EDGE,"E1809"),sQuery(id+"F9.wireOp",EDGE,"E1810"),sQuery(id+"F9.wireOp",EDGE,"E1811"),sQuery(id+"F9.wireOp",EDGE,"E1812"),sQuery(id+"F9.wireOp",EDGE,"E1813"),sQuery(id+"F9.wireOp",EDGE,"E1814"),sQuery(id+"F9.wireOp",EDGE,"E1815"),sQuery(id+"F9.wireOp",EDGE,"E1816"),sQuery(id+"F9.wireOp",EDGE,"E1817"),sQuery(id+"F9.wireOp",EDGE,"E1818"),sQuery(id+"F9.wireOp",EDGE,"E1819"),sQuery(id+"F9.wireOp",EDGE,"E1820"),sQuery(id+"F9.wireOp",EDGE,"E1821"),sQuery(id+"F9.wireOp",EDGE,"E1822"),sQuery(id+"F9.wireOp",EDGE,"E1823"),sQuery(id+"F9.wireOp",EDGE,"E1824"),sQuery(id+"F9.wireOp",EDGE,"E1825"),sQuery(id+"F9.wireOp",EDGE,"E1826"),sQuery(id+"F9.wireOp",EDGE,"E1827"),sQuery(id+"F9.wireOp",EDGE,"E1828"),sQuery(id+"F9.wireOp",EDGE,"E1829"),sQuery(id+"F9.wireOp",EDGE,"E1830"),sQuery(id+"F9.wireOp",EDGE,"E1831"),sQuery(id+"F9.wireOp",EDGE,"E1832"),sQuery(id+"F9.wireOp",EDGE,"E1833"),sQuery(id+"F9.wireOp",EDGE,"E1834"),sQuery(id+"F9.wireOp",EDGE,"E1835"),sQuery(id+"F9.wireOp",EDGE,"E1836"),sQuery(id+"F9.wireOp",EDGE,"E1837"),sQuery(id+"F9.wireOp",EDGE,"E1838"),sQuery(id+"F9.wireOp",EDGE,"E1839"),sQuery(id+"F9.wireOp",EDGE,"E1840"),sQuery(id+"F9.wireOp",EDGE,"E1841"),sQuery(id+"F9.wireOp",EDGE,"E1842"),sQuery(id+"F9.wireOp",EDGE,"E1843"),sQuery(id+"F9.wireOp",EDGE,"E1844"),sQuery(id+"F9.wireOp",EDGE,"E1845"),sQuery(id+"F9.wireOp",EDGE,"E1846"),sQuery(id+"F9.wireOp",EDGE,"E1847"),sQuery(id+"F9.wireOp",EDGE,"E1848"),sQuery(id+"F9.wireOp",EDGE,"E1849"),sQuery(id+"F9.wireOp",EDGE,"E1850"),sQuery(id+"F9.wireOp",EDGE,"E1851"),sQuery(id+"F9.wireOp",EDGE,"E1852"),sQuery(id+"F9.wireOp",EDGE,"E1853"),sQuery(id+"F9.wireOp",EDGE,"E1854"),sQuery(id+"F9.wireOp",EDGE,"E1855"),sQuery(id+"F9.wireOp",EDGE,"E1856"),sQuery(id+"F9.wireOp",EDGE,"E1857"),sQuery(id+"F9.wireOp",EDGE,"E1858"),sQuery(id+"F9.wireOp",EDGE,"E1859"),sQuery(id+"F9.wireOp",EDGE,"E1860"),sQuery(id+"F9.wireOp",EDGE,"E1861"),sQuery(id+"F9.wireOp",EDGE,"E1862"),sQuery(id+"F9.wireOp",EDGE,"E1863"),sQuery(id+"F9.wireOp",EDGE,"E1864"),sQuery(id+"F9.wireOp",EDGE,"E1865"),sQuery(id+"F9.wireOp",EDGE,"E1866"),sQuery(id+"F9.wireOp",EDGE,"E1867"),sQuery(id+"F9.wireOp",EDGE,"E1868"),sQuery(id+"F9.wireOp",EDGE,"E1869"),sQuery(id+"F9.wireOp",EDGE,"E1870"),sQuery(id+"F9.wireOp",EDGE,"E1871"),sQuery(id+"F9.wireOp",EDGE,"E1872"),sQuery(id+"F9.wireOp",EDGE,"E1873"),sQuery(id+"F9.wireOp",EDGE,"E1874"),sQuery(id+"F9.wireOp",EDGE,"E1875"),sQuery(id+"F9.wireOp",EDGE,"E1876"),sQuery(id+"F9.wireOp",EDGE,"E1877"),sQuery(id+"F9.wireOp",EDGE,"E1878"),sQuery(id+"F9.wireOp",EDGE,"E1879"),sQuery(id+"F9.wireOp",EDGE,"E1880"),sQuery(id+"F9.wireOp",EDGE,"E1881"),sQuery(id+"F9.wireOp",EDGE,"E1882"),sQuery(id+"F9.wireOp",EDGE,"E1883"),sQuery(id+"F9.wireOp",EDGE,"E1884"),sQuery(id+"F9.wireOp",EDGE,"E1885"),sQuery(id+"F9.wireOp",EDGE,"E1886"),sQuery(id+"F9.wireOp",EDGE,"E1887"),sQuery(id+"F9.wireOp",EDGE,"E1888"),sQuery(id+"F9.wireOp",EDGE,"E1889"),sQuery(id+"F9.wireOp",EDGE,"E1890"),sQuery(id+"F9.wireOp",EDGE,"E1891"),sQuery(id+"F9.wireOp",EDGE,"E1892"),sQuery(id+"F9.wireOp",EDGE,"E1893"),sQuery(id+"F9.wireOp",EDGE,"E1894"),sQuery(id+"F9.wireOp",EDGE,"E1895"),sQuery(id+"F9.wireOp",EDGE,"E1896"),sQuery(id+"F9.wireOp",EDGE,"E1897"),sQuery(id+"F9.wireOp",EDGE,"E1898"),sQuery(id+"F9.wireOp",EDGE,"E1899"),sQuery(id+"F9.wireOp",EDGE,"E1900"),sQuery(id+"F9.wireOp",EDGE,"E1901"),sQuery(id+"F9.wireOp",EDGE,"E1902"),sQuery(id+"F9.wireOp",EDGE,"E1903"),sQuery(id+"F9.wireOp",EDGE,"E1904"),sQuery(id+"F9.wireOp",EDGE,"E1905"),sQuery(id+"F9.wireOp",EDGE,"E1906"),sQuery(id+"F9.wireOp",EDGE,"E1907"),sQuery(id+"F9.wireOp",EDGE,"E1908"),sQuery(id+"F9.wireOp",EDGE,"E1909"),sQuery(id+"F9.wireOp",EDGE,"E1910"),sQuery(id+"F9.wireOp",EDGE,"E1911"),sQuery(id+"F9.wireOp",EDGE,"E1912"),sQuery(id+"F9.wireOp",EDGE,"E1913"),sQuery(id+"F9.wireOp",EDGE,"E1914"),sQuery(id+"F9.wireOp",EDGE,"E1915"),sQuery(id+"F9.wireOp",EDGE,"E1916"),sQuery(id+"F9.wireOp",EDGE,"E1917"),sQuery(id+"F9.wireOp",EDGE,"E1918"),sQuery(id+"F9.wireOp",EDGE,"E1919"),sQuery(id+"F9.wireOp",EDGE,"E1920"),sQuery(id+"F9.wireOp",EDGE,"E1921"),sQuery(id+"F9.wireOp",EDGE,"E1922"),sQuery(id+"F9.wireOp",EDGE,"E1923"),sQuery(id+"F9.wireOp",EDGE,"E1924"),sQuery(id+"F9.wireOp",EDGE,"E1925"),sQuery(id+"F9.wireOp",EDGE,"E1926"),sQuery(id+"F9.wireOp",EDGE,"E1927"),sQuery(id+"F9.wireOp",EDGE,"E1928"),sQuery(id+"F9.wireOp",EDGE,"E1929"),sQuery(id+"F9.wireOp",EDGE,"E1930"),sQuery(id+"F9.wireOp",EDGE,"E1931"),sQuery(id+"F9.wireOp",EDGE,"E1932"),sQuery(id+"F9.wireOp",EDGE,"E1933"),sQuery(id+"F9.wireOp",EDGE,"E1934"),sQuery(id+"F9.wireOp",EDGE,"E1935"),sQuery(id+"F9.wireOp",EDGE,"E1936"),sQuery(id+"F9.wireOp",EDGE,"E1937"),sQuery(id+"F9.wireOp",EDGE,"E1938"),sQuery(id+"F9.wireOp",EDGE,"E1939"),sQuery(id+"F9.wireOp",EDGE,"E1940"),sQuery(id+"F9.wireOp",EDGE,"E1941"),sQuery(id+"F9.wireOp",EDGE,"E1942"),sQuery(id+"F9.wireOp",EDGE,"E1943"),sQuery(id+"F9.wireOp",EDGE,"E1944"),sQuery(id+"F9.wireOp",EDGE,"E1945"),sQuery(id+"F9.wireOp",EDGE,"E1946"),sQuery(id+"F9.wireOp",EDGE,"E1947"),sQuery(id+"F9.wireOp",EDGE,"E1948"),sQuery(id+"F9.wireOp",EDGE,"E1949"),sQuery(id+"F9.wireOp",EDGE,"E1950"),sQuery(id+"F9.wireOp",EDGE,"E1951"),sQuery(id+"F9.wireOp",EDGE,"E1952"),sQuery(id+"F9.wireOp",EDGE,"E1953"),sQuery(id+"F9.wireOp",EDGE,"E1954"),sQuery(id+"F9.wireOp",EDGE,"E1955"),sQuery(id+"F9.wireOp",EDGE,"E1956"),sQuery(id+"F9.wireOp",EDGE,"E1957"),sQuery(id+"F9.wireOp",EDGE,"E1958"),sQuery(id+"F9.wireOp",EDGE,"E1959"),sQuery(id+"F9.wireOp",EDGE,"E1960"),sQuery(id+"F9.wireOp",EDGE,"E1961"),sQuery(id+"F9.wireOp",EDGE,"E1962"),sQuery(id+"F9.wireOp",EDGE,"E1963"),sQuery(id+"F9.wireOp",EDGE,"E1964"),sQuery(id+"F9.wireOp",EDGE,"E1965"),sQuery(id+"F9.wireOp",EDGE,"E1966"),sQuery(id+"F9.wireOp",EDGE,"E1967"),sQuery(id+"F9.wireOp",EDGE,"E1968"),sQuery(id+"F9.wireOp",EDGE,"E1969"),sQuery(id+"F9.wireOp",EDGE,"E1970"),sQuery(id+"F9.wireOp",EDGE,"E1971"),sQuery(id+"F9.wireOp",EDGE,"E1972"),sQuery(id+"F9.wireOp",EDGE,"E1973"),sQuery(id+"F9.wireOp",EDGE,"E1974"),sQuery(id+"F9.wireOp",EDGE,"E1975"),sQuery(id+"F9.wireOp",EDGE,"E1976"),sQuery(id+"F9.wireOp",EDGE,"E1977"),sQuery(id+"F9.wireOp",EDGE,"E1978"),sQuery(id+"F9.wireOp",EDGE,"E1979"),sQuery(id+"F9.wireOp",EDGE,"E1980"),sQuery(id+"F9.wireOp",EDGE,"E1981"),sQuery(id+"F9.wireOp",EDGE,"E1982"),sQuery(id+"F9.wireOp",EDGE,"E1983"),sQuery(id+"F9.wireOp",EDGE,"E1984"),sQuery(id+"F9.wireOp",EDGE,"E1985"),sQuery(id+"F9.wireOp",EDGE,"E1986"),sQuery(id+"F9.wireOp",EDGE,"E1987"),sQuery(id+"F9.wireOp",EDGE,"E1988"),sQuery(id+"F9.wireOp",EDGE,"E1989"),sQuery(id+"F9.wireOp",EDGE,"E1990"),sQuery(id+"F9.wireOp",EDGE,"E1991"),sQuery(id+"F9.wireOp",EDGE,"E1992"),sQuery(id+"F9.wireOp",EDGE,"E1993"),sQuery(id+"F9.wireOp",EDGE,"E1994"),sQuery(id+"F9.wireOp",EDGE,"E1995")])]});
            var Q2;
            Q2=makeQuery(id+"F10.opExtrude","SWEPT_BODY",BODY,{"disambiguationData":[OSD([sQuery(id+"F9.wireOp",EDGE,"E1996"),sQuery(id+"F9.wireOp",EDGE,"E1997"),sQuery(id+"F9.wireOp",EDGE,"E1998"),sQuery(id+"F9.wireOp",EDGE,"E1999"),sQuery(id+"F9.wireOp",EDGE,"E2000"),sQuery(id+"F9.wireOp",EDGE,"E2001"),sQuery(id+"F9.wireOp",EDGE,"E2002"),sQuery(id+"F9.wireOp",EDGE,"E2003"),sQuery(id+"F9.wireOp",EDGE,"E2004"),sQuery(id+"F9.wireOp",EDGE,"E2005"),sQuery(id+"F9.wireOp",EDGE,"E2006"),sQuery(id+"F9.wireOp",EDGE,"E2007"),sQuery(id+"F9.wireOp",EDGE,"E2008"),sQuery(id+"F9.wireOp",EDGE,"E2009"),sQuery(id+"F9.wireOp",EDGE,"E2010"),sQuery(id+"F9.wireOp",EDGE,"E2011"),sQuery(id+"F9.wireOp",EDGE,"E2012"),sQuery(id+"F9.wireOp",EDGE,"E2013"),sQuery(id+"F9.wireOp",EDGE,"E2014"),sQuery(id+"F9.wireOp",EDGE,"E2015"),sQuery(id+"F9.wireOp",EDGE,"E2016"),sQuery(id+"F9.wireOp",EDGE,"E2017"),sQuery(id+"F9.wireOp",EDGE,"E2018"),sQuery(id+"F9.wireOp",EDGE,"E2019"),sQuery(id+"F9.wireOp",EDGE,"E2020"),sQuery(id+"F9.wireOp",EDGE,"E2021"),sQuery(id+"F9.wireOp",EDGE,"E2022"),sQuery(id+"F9.wireOp",EDGE,"E2023"),sQuery(id+"F9.wireOp",EDGE,"E2024"),sQuery(id+"F9.wireOp",EDGE,"E2025"),sQuery(id+"F9.wireOp",EDGE,"E2026"),sQuery(id+"F9.wireOp",EDGE,"E2027"),sQuery(id+"F9.wireOp",EDGE,"E2028"),sQuery(id+"F9.wireOp",EDGE,"E2029"),sQuery(id+"F9.wireOp",EDGE,"E2030"),sQuery(id+"F9.wireOp",EDGE,"E2031"),sQuery(id+"F9.wireOp",EDGE,"E2032"),sQuery(id+"F9.wireOp",EDGE,"E2033"),sQuery(id+"F9.wireOp",EDGE,"E2034"),sQuery(id+"F9.wireOp",EDGE,"E2035"),sQuery(id+"F9.wireOp",EDGE,"E2036"),sQuery(id+"F9.wireOp",EDGE,"E2037"),sQuery(id+"F9.wireOp",EDGE,"E2038"),sQuery(id+"F9.wireOp",EDGE,"E2039"),sQuery(id+"F9.wireOp",EDGE,"E2040"),sQuery(id+"F9.wireOp",EDGE,"E2041"),sQuery(id+"F9.wireOp",EDGE,"E2042"),sQuery(id+"F9.wireOp",EDGE,"E2043"),sQuery(id+"F9.wireOp",EDGE,"E2044"),sQuery(id+"F9.wireOp",EDGE,"E2045"),sQuery(id+"F9.wireOp",EDGE,"E2046"),sQuery(id+"F9.wireOp",EDGE,"E2047"),sQuery(id+"F9.wireOp",EDGE,"E2048"),sQuery(id+"F9.wireOp",EDGE,"E2049"),sQuery(id+"F9.wireOp",EDGE,"E2050"),sQuery(id+"F9.wireOp",EDGE,"E2051"),sQuery(id+"F9.wireOp",EDGE,"E2052"),sQuery(id+"F9.wireOp",EDGE,"E2053"),sQuery(id+"F9.wireOp",EDGE,"E2054"),sQuery(id+"F9.wireOp",EDGE,"E2055"),sQuery(id+"F9.wireOp",EDGE,"E2056"),sQuery(id+"F9.wireOp",EDGE,"E2057"),sQuery(id+"F9.wireOp",EDGE,"E2058"),sQuery(id+"F9.wireOp",EDGE,"E2059"),sQuery(id+"F9.wireOp",EDGE,"E2060"),sQuery(id+"F9.wireOp",EDGE,"E2061"),sQuery(id+"F9.wireOp",EDGE,"E2062"),sQuery(id+"F9.wireOp",EDGE,"E2063"),sQuery(id+"F9.wireOp",EDGE,"E2064"),sQuery(id+"F9.wireOp",EDGE,"E2065"),sQuery(id+"F9.wireOp",EDGE,"E2066"),sQuery(id+"F9.wireOp",EDGE,"E2067"),sQuery(id+"F9.wireOp",EDGE,"E2068"),sQuery(id+"F9.wireOp",EDGE,"E2069"),sQuery(id+"F9.wireOp",EDGE,"E2070"),sQuery(id+"F9.wireOp",EDGE,"E2071"),sQuery(id+"F9.wireOp",EDGE,"E2072"),sQuery(id+"F9.wireOp",EDGE,"E2073"),sQuery(id+"F9.wireOp",EDGE,"E2074"),sQuery(id+"F9.wireOp",EDGE,"E2075"),sQuery(id+"F9.wireOp",EDGE,"E2076"),sQuery(id+"F9.wireOp",EDGE,"E2077"),sQuery(id+"F9.wireOp",EDGE,"E2078"),sQuery(id+"F9.wireOp",EDGE,"E2079"),sQuery(id+"F9.wireOp",EDGE,"E2080"),sQuery(id+"F9.wireOp",EDGE,"E2081"),sQuery(id+"F9.wireOp",EDGE,"E2082"),sQuery(id+"F9.wireOp",EDGE,"E2083"),sQuery(id+"F9.wireOp",EDGE,"E2084"),sQuery(id+"F9.wireOp",EDGE,"E2085"),sQuery(id+"F9.wireOp",EDGE,"E2086"),sQuery(id+"F9.wireOp",EDGE,"E2087"),sQuery(id+"F9.wireOp",EDGE,"E2088"),sQuery(id+"F9.wireOp",EDGE,"E2089"),sQuery(id+"F9.wireOp",EDGE,"E2090"),sQuery(id+"F9.wireOp",EDGE,"E2091"),sQuery(id+"F9.wireOp",EDGE,"E2092"),sQuery(id+"F9.wireOp",EDGE,"E2093"),sQuery(id+"F9.wireOp",EDGE,"E2094"),sQuery(id+"F9.wireOp",EDGE,"E2095"),sQuery(id+"F9.wireOp",EDGE,"E2096"),sQuery(id+"F9.wireOp",EDGE,"E2097"),sQuery(id+"F9.wireOp",EDGE,"E2098"),sQuery(id+"F9.wireOp",EDGE,"E2099"),sQuery(id+"F9.wireOp",EDGE,"E2100"),sQuery(id+"F9.wireOp",EDGE,"E2101")])]});
            var Q3;
            Q3=makeQuery(id+"F10.opExtrude","SWEPT_BODY",BODY,{"disambiguationData":[OSD([sQuery(id+"F9.wireOp",EDGE,"E2102"),sQuery(id+"F9.wireOp",EDGE,"E2103"),sQuery(id+"F9.wireOp",EDGE,"E2104"),sQuery(id+"F9.wireOp",EDGE,"E2105")])]});
            var Q4;
            Q4=makeQuery(id+"F10.opExtrude","SWEPT_BODY",BODY,{"disambiguationData":[OSD([sQuery(id+"F9.wireOp",EDGE,"E2106"),sQuery(id+"F9.wireOp",EDGE,"E2107"),sQuery(id+"F9.wireOp",EDGE,"E2108"),sQuery(id+"F9.wireOp",EDGE,"E2109")])]});
            var Q5;
            Q5=makeQuery(id+"F10.opExtrude","SWEPT_BODY",BODY,{"disambiguationData":[OSD([sQuery(id+"F9.wireOp",EDGE,"E2110"),sQuery(id+"F9.wireOp",EDGE,"E2111"),sQuery(id+"F9.wireOp",EDGE,"E2112"),sQuery(id+"F9.wireOp",EDGE,"E2113"),sQuery(id+"F9.wireOp",EDGE,"E2114"),sQuery(id+"F9.wireOp",EDGE,"E2115"),sQuery(id+"F9.wireOp",EDGE,"E2116"),sQuery(id+"F9.wireOp",EDGE,"E2117"),sQuery(id+"F9.wireOp",EDGE,"E2118"),sQuery(id+"F9.wireOp",EDGE,"E2119"),sQuery(id+"F9.wireOp",EDGE,"E2120"),sQuery(id+"F9.wireOp",EDGE,"E2121"),sQuery(id+"F9.wireOp",EDGE,"E2122"),sQuery(id+"F9.wireOp",EDGE,"E2123"),sQuery(id+"F9.wireOp",EDGE,"E2124"),sQuery(id+"F9.wireOp",EDGE,"E2125"),sQuery(id+"F9.wireOp",EDGE,"E2126"),sQuery(id+"F9.wireOp",EDGE,"E2127"),sQuery(id+"F9.wireOp",EDGE,"E2128"),sQuery(id+"F9.wireOp",EDGE,"E2129"),sQuery(id+"F9.wireOp",EDGE,"E2130"),sQuery(id+"F9.wireOp",EDGE,"E2131"),sQuery(id+"F9.wireOp",EDGE,"E2132"),sQuery(id+"F9.wireOp",EDGE,"E2133"),sQuery(id+"F9.wireOp",EDGE,"E2134"),sQuery(id+"F9.wireOp",EDGE,"E2135"),sQuery(id+"F9.wireOp",EDGE,"E2136"),sQuery(id+"F9.wireOp",EDGE,"E2137"),sQuery(id+"F9.wireOp",EDGE,"E2138"),sQuery(id+"F9.wireOp",EDGE,"E2139"),sQuery(id+"F9.wireOp",EDGE,"E2140"),sQuery(id+"F9.wireOp",EDGE,"E2141"),sQuery(id+"F9.wireOp",EDGE,"E2142"),sQuery(id+"F9.wireOp",EDGE,"E2143"),sQuery(id+"F9.wireOp",EDGE,"E2144"),sQuery(id+"F9.wireOp",EDGE,"E2145"),sQuery(id+"F9.wireOp",EDGE,"E2146"),sQuery(id+"F9.wireOp",EDGE,"E2147"),sQuery(id+"F9.wireOp",EDGE,"E2148"),sQuery(id+"F9.wireOp",EDGE,"E2149"),sQuery(id+"F9.wireOp",EDGE,"E2150"),sQuery(id+"F9.wireOp",EDGE,"E2151"),sQuery(id+"F9.wireOp",EDGE,"E2152"),sQuery(id+"F9.wireOp",EDGE,"E2153"),sQuery(id+"F9.wireOp",EDGE,"E2154"),sQuery(id+"F9.wireOp",EDGE,"E2155"),sQuery(id+"F9.wireOp",EDGE,"E2156"),sQuery(id+"F9.wireOp",EDGE,"E2157"),sQuery(id+"F9.wireOp",EDGE,"E2158"),sQuery(id+"F9.wireOp",EDGE,"E2159"),sQuery(id+"F9.wireOp",EDGE,"E2160"),sQuery(id+"F9.wireOp",EDGE,"E2161"),sQuery(id+"F9.wireOp",EDGE,"E2162"),sQuery(id+"F9.wireOp",EDGE,"E2163")])]});
            var Q6;
            Q6=makeQuery(id+"F10.opExtrude","SWEPT_BODY",BODY,{"disambiguationData":[OSD([sQuery(id+"F9.wireOp",EDGE,"E2164"),sQuery(id+"F9.wireOp",EDGE,"E2165"),sQuery(id+"F9.wireOp",EDGE,"E2166"),sQuery(id+"F9.wireOp",EDGE,"E2167"),sQuery(id+"F9.wireOp",EDGE,"E2168"),sQuery(id+"F9.wireOp",EDGE,"E2169"),sQuery(id+"F9.wireOp",EDGE,"E2170"),sQuery(id+"F9.wireOp",EDGE,"E2171"),sQuery(id+"F9.wireOp",EDGE,"E2172"),sQuery(id+"F9.wireOp",EDGE,"E2173"),sQuery(id+"F9.wireOp",EDGE,"E2174"),sQuery(id+"F9.wireOp",EDGE,"E2175"),sQuery(id+"F9.wireOp",EDGE,"E2176"),sQuery(id+"F9.wireOp",EDGE,"E2177"),sQuery(id+"F9.wireOp",EDGE,"E2178"),sQuery(id+"F9.wireOp",EDGE,"E2179"),sQuery(id+"F9.wireOp",EDGE,"E2180"),sQuery(id+"F9.wireOp",EDGE,"E2181"),sQuery(id+"F9.wireOp",EDGE,"E2182"),sQuery(id+"F9.wireOp",EDGE,"E2183"),sQuery(id+"F9.wireOp",EDGE,"E2184"),sQuery(id+"F9.wireOp",EDGE,"E2185"),sQuery(id+"F9.wireOp",EDGE,"E2186"),sQuery(id+"F9.wireOp",EDGE,"E2187"),sQuery(id+"F9.wireOp",EDGE,"E2188"),sQuery(id+"F9.wireOp",EDGE,"E2189"),sQuery(id+"F9.wireOp",EDGE,"E2190"),sQuery(id+"F9.wireOp",EDGE,"E2191"),sQuery(id+"F9.wireOp",EDGE,"E2192"),sQuery(id+"F9.wireOp",EDGE,"E2193"),sQuery(id+"F9.wireOp",EDGE,"E2194"),sQuery(id+"F9.wireOp",EDGE,"E2195"),sQuery(id+"F9.wireOp",EDGE,"E2196"),sQuery(id+"F9.wireOp",EDGE,"E2197"),sQuery(id+"F9.wireOp",EDGE,"E2198"),sQuery(id+"F9.wireOp",EDGE,"E2199"),sQuery(id+"F9.wireOp",EDGE,"E2200"),sQuery(id+"F9.wireOp",EDGE,"E2201"),sQuery(id+"F9.wireOp",EDGE,"E2202"),sQuery(id+"F9.wireOp",EDGE,"E2203"),sQuery(id+"F9.wireOp",EDGE,"E2204"),sQuery(id+"F9.wireOp",EDGE,"E2205"),sQuery(id+"F9.wireOp",EDGE,"E2206"),sQuery(id+"F9.wireOp",EDGE,"E2207"),sQuery(id+"F9.wireOp",EDGE,"E2208"),sQuery(id+"F9.wireOp",EDGE,"E2209"),sQuery(id+"F9.wireOp",EDGE,"E2210"),sQuery(id+"F9.wireOp",EDGE,"E2211"),sQuery(id+"F9.wireOp",EDGE,"E2212"),sQuery(id+"F9.wireOp",EDGE,"E2213"),sQuery(id+"F9.wireOp",EDGE,"E2214"),sQuery(id+"F9.wireOp",EDGE,"E2215"),sQuery(id+"F9.wireOp",EDGE,"E2216"),sQuery(id+"F9.wireOp",EDGE,"E2217"),sQuery(id+"F9.wireOp",EDGE,"E2218"),sQuery(id+"F9.wireOp",EDGE,"E2219"),sQuery(id+"F9.wireOp",EDGE,"E2220"),sQuery(id+"F9.wireOp",EDGE,"E2221"),sQuery(id+"F9.wireOp",EDGE,"E2222"),sQuery(id+"F9.wireOp",EDGE,"E2223"),sQuery(id+"F9.wireOp",EDGE,"E2224"),sQuery(id+"F9.wireOp",EDGE,"E2225"),sQuery(id+"F9.wireOp",EDGE,"E2226"),sQuery(id+"F9.wireOp",EDGE,"E2227"),sQuery(id+"F9.wireOp",EDGE,"E2228"),sQuery(id+"F9.wireOp",EDGE,"E2229"),sQuery(id+"F9.wireOp",EDGE,"E2230"),sQuery(id+"F9.wireOp",EDGE,"E2231"),sQuery(id+"F9.wireOp",EDGE,"E2232"),sQuery(id+"F9.wireOp",EDGE,"E2233"),sQuery(id+"F9.wireOp",EDGE,"E2234"),sQuery(id+"F9.wireOp",EDGE,"E2235"),sQuery(id+"F9.wireOp",EDGE,"E2236"),sQuery(id+"F9.wireOp",EDGE,"E2237"),sQuery(id+"F9.wireOp",EDGE,"E2238"),sQuery(id+"F9.wireOp",EDGE,"E2239"),sQuery(id+"F9.wireOp",EDGE,"E2240"),sQuery(id+"F9.wireOp",EDGE,"E2241"),sQuery(id+"F9.wireOp",EDGE,"E2242"),sQuery(id+"F9.wireOp",EDGE,"E2243"),sQuery(id+"F9.wireOp",EDGE,"E2244"),sQuery(id+"F9.wireOp",EDGE,"E2245"),sQuery(id+"F9.wireOp",EDGE,"E2246"),sQuery(id+"F9.wireOp",EDGE,"E2247"),sQuery(id+"F9.wireOp",EDGE,"E2248"),sQuery(id+"F9.wireOp",EDGE,"E2249"),sQuery(id+"F9.wireOp",EDGE,"E2250"),sQuery(id+"F9.wireOp",EDGE,"E2251"),sQuery(id+"F9.wireOp",EDGE,"E2252"),sQuery(id+"F9.wireOp",EDGE,"E2253"),sQuery(id+"F9.wireOp",EDGE,"E2254"),sQuery(id+"F9.wireOp",EDGE,"E2255"),sQuery(id+"F9.wireOp",EDGE,"E2256"),sQuery(id+"F9.wireOp",EDGE,"E2257"),sQuery(id+"F9.wireOp",EDGE,"E2258"),sQuery(id+"F9.wireOp",EDGE,"E2259"),sQuery(id+"F9.wireOp",EDGE,"E2260"),sQuery(id+"F9.wireOp",EDGE,"E2261"),sQuery(id+"F9.wireOp",EDGE,"E2262"),sQuery(id+"F9.wireOp",EDGE,"E2263"),sQuery(id+"F9.wireOp",EDGE,"E2264"),sQuery(id+"F9.wireOp",EDGE,"E2265"),sQuery(id+"F9.wireOp",EDGE,"E2266"),sQuery(id+"F9.wireOp",EDGE,"E2267"),sQuery(id+"F9.wireOp",EDGE,"E2268"),sQuery(id+"F9.wireOp",EDGE,"E2269"),sQuery(id+"F9.wireOp",EDGE,"E2270"),sQuery(id+"F9.wireOp",EDGE,"E2271"),sQuery(id+"F9.wireOp",EDGE,"E2272"),sQuery(id+"F9.wireOp",EDGE,"E2273"),sQuery(id+"F9.wireOp",EDGE,"E2274"),sQuery(id+"F9.wireOp",EDGE,"E2275"),sQuery(id+"F9.wireOp",EDGE,"E2276"),sQuery(id+"F9.wireOp",EDGE,"E2277"),sQuery(id+"F9.wireOp",EDGE,"E2278"),sQuery(id+"F9.wireOp",EDGE,"E2279"),sQuery(id+"F9.wireOp",EDGE,"E2280"),sQuery(id+"F9.wireOp",EDGE,"E2281"),sQuery(id+"F9.wireOp",EDGE,"E2282"),sQuery(id+"F9.wireOp",EDGE,"E2283"),sQuery(id+"F9.wireOp",EDGE,"E2284"),sQuery(id+"F9.wireOp",EDGE,"E2285"),sQuery(id+"F9.wireOp",EDGE,"E2286"),sQuery(id+"F9.wireOp",EDGE,"E2287"),sQuery(id+"F9.wireOp",EDGE,"E2288"),sQuery(id+"F9.wireOp",EDGE,"E2289"),sQuery(id+"F9.wireOp",EDGE,"E2290"),sQuery(id+"F9.wireOp",EDGE,"E2291"),sQuery(id+"F9.wireOp",EDGE,"E2292"),sQuery(id+"F9.wireOp",EDGE,"E2293"),sQuery(id+"F9.wireOp",EDGE,"E2294"),sQuery(id+"F9.wireOp",EDGE,"E2295"),sQuery(id+"F9.wireOp",EDGE,"E2296"),sQuery(id+"F9.wireOp",EDGE,"E2297"),sQuery(id+"F9.wireOp",EDGE,"E2298"),sQuery(id+"F9.wireOp",EDGE,"E2299"),sQuery(id+"F9.wireOp",EDGE,"E2300"),sQuery(id+"F9.wireOp",EDGE,"E2301"),sQuery(id+"F9.wireOp",EDGE,"E2302"),sQuery(id+"F9.wireOp",EDGE,"E2303"),sQuery(id+"F9.wireOp",EDGE,"E2304"),sQuery(id+"F9.wireOp",EDGE,"E2305"),sQuery(id+"F9.wireOp",EDGE,"E2306"),sQuery(id+"F9.wireOp",EDGE,"E2307"),sQuery(id+"F9.wireOp",EDGE,"E2308"),sQuery(id+"F9.wireOp",EDGE,"E2309"),sQuery(id+"F9.wireOp",EDGE,"E2310"),sQuery(id+"F9.wireOp",EDGE,"E2311"),sQuery(id+"F9.wireOp",EDGE,"E2312"),sQuery(id+"F9.wireOp",EDGE,"E2313"),sQuery(id+"F9.wireOp",EDGE,"E2314"),sQuery(id+"F9.wireOp",EDGE,"E2315"),sQuery(id+"F9.wireOp",EDGE,"E2316"),sQuery(id+"F9.wireOp",EDGE,"E2317"),sQuery(id+"F9.wireOp",EDGE,"E2318"),sQuery(id+"F9.wireOp",EDGE,"E2319"),sQuery(id+"F9.wireOp",EDGE,"E2320"),sQuery(id+"F9.wireOp",EDGE,"E2321"),sQuery(id+"F9.wireOp",EDGE,"E2322"),sQuery(id+"F9.wireOp",EDGE,"E2323"),sQuery(id+"F9.wireOp",EDGE,"E2324"),sQuery(id+"F9.wireOp",EDGE,"E2325"),sQuery(id+"F9.wireOp",EDGE,"E2326"),sQuery(id+"F9.wireOp",EDGE,"E2327"),sQuery(id+"F9.wireOp",EDGE,"E2328"),sQuery(id+"F9.wireOp",EDGE,"E2329"),sQuery(id+"F9.wireOp",EDGE,"E2330"),sQuery(id+"F9.wireOp",EDGE,"E2331"),sQuery(id+"F9.wireOp",EDGE,"E2332"),sQuery(id+"F9.wireOp",EDGE,"E2333"),sQuery(id+"F9.wireOp",EDGE,"E2334"),sQuery(id+"F9.wireOp",EDGE,"E2335"),sQuery(id+"F9.wireOp",EDGE,"E2336"),sQuery(id+"F9.wireOp",EDGE,"E2337"),sQuery(id+"F9.wireOp",EDGE,"E2338"),sQuery(id+"F9.wireOp",EDGE,"E2339"),sQuery(id+"F9.wireOp",EDGE,"E2340"),sQuery(id+"F9.wireOp",EDGE,"E2341"),sQuery(id+"F9.wireOp",EDGE,"E2342"),sQuery(id+"F9.wireOp",EDGE,"E2343"),sQuery(id+"F9.wireOp",EDGE,"E2344"),sQuery(id+"F9.wireOp",EDGE,"E2345"),sQuery(id+"F9.wireOp",EDGE,"E2346"),sQuery(id+"F9.wireOp",EDGE,"E2347"),sQuery(id+"F9.wireOp",EDGE,"E2348"),sQuery(id+"F9.wireOp",EDGE,"E2349"),sQuery(id+"F9.wireOp",EDGE,"E2350"),sQuery(id+"F9.wireOp",EDGE,"E2351"),sQuery(id+"F9.wireOp",EDGE,"E2352"),sQuery(id+"F9.wireOp",EDGE,"E2353"),sQuery(id+"F9.wireOp",EDGE,"E2354"),sQuery(id+"F9.wireOp",EDGE,"E2355"),sQuery(id+"F9.wireOp",EDGE,"E2356"),sQuery(id+"F9.wireOp",EDGE,"E2357"),sQuery(id+"F9.wireOp",EDGE,"E2358"),sQuery(id+"F9.wireOp",EDGE,"E2359"),sQuery(id+"F9.wireOp",EDGE,"E2360"),sQuery(id+"F9.wireOp",EDGE,"E2361"),sQuery(id+"F9.wireOp",EDGE,"E2362"),sQuery(id+"F9.wireOp",EDGE,"E2363"),sQuery(id+"F9.wireOp",EDGE,"E2364"),sQuery(id+"F9.wireOp",EDGE,"E2365"),sQuery(id+"F9.wireOp",EDGE,"E2366"),sQuery(id+"F9.wireOp",EDGE,"E2367"),sQuery(id+"F9.wireOp",EDGE,"E2368"),sQuery(id+"F9.wireOp",EDGE,"E2369"),sQuery(id+"F9.wireOp",EDGE,"E2370"),sQuery(id+"F9.wireOp",EDGE,"E2371"),sQuery(id+"F9.wireOp",EDGE,"E2372"),sQuery(id+"F9.wireOp",EDGE,"E2373"),sQuery(id+"F9.wireOp",EDGE,"E2374"),sQuery(id+"F9.wireOp",EDGE,"E2375"),sQuery(id+"F9.wireOp",EDGE,"E2376"),sQuery(id+"F9.wireOp",EDGE,"E2377"),sQuery(id+"F9.wireOp",EDGE,"E2378"),sQuery(id+"F9.wireOp",EDGE,"E2379"),sQuery(id+"F9.wireOp",EDGE,"E2380"),sQuery(id+"F9.wireOp",EDGE,"E2381"),sQuery(id+"F9.wireOp",EDGE,"E2382"),sQuery(id+"F9.wireOp",EDGE,"E2383"),sQuery(id+"F9.wireOp",EDGE,"E2384"),sQuery(id+"F9.wireOp",EDGE,"E2385"),sQuery(id+"F9.wireOp",EDGE,"E2386"),sQuery(id+"F9.wireOp",EDGE,"E2387"),sQuery(id+"F9.wireOp",EDGE,"E2388"),sQuery(id+"F9.wireOp",EDGE,"E2389"),sQuery(id+"F9.wireOp",EDGE,"E2390"),sQuery(id+"F9.wireOp",EDGE,"E2391"),sQuery(id+"F9.wireOp",EDGE,"E2392"),sQuery(id+"F9.wireOp",EDGE,"E2393"),sQuery(id+"F9.wireOp",EDGE,"E2394"),sQuery(id+"F9.wireOp",EDGE,"E2395"),sQuery(id+"F9.wireOp",EDGE,"E2396"),sQuery(id+"F9.wireOp",EDGE,"E2397")])]});
            var Q7;
            Q7=makeQuery(id+"F10.opExtrude","SWEPT_BODY",BODY,{"disambiguationData":[OSD([sQuery(id+"F9.wireOp",EDGE,"E2398"),sQuery(id+"F9.wireOp",EDGE,"E2399"),sQuery(id+"F9.wireOp",EDGE,"E2400"),sQuery(id+"F9.wireOp",EDGE,"E2401")])]});
            var Q8;
            Q8=makeQuery(id+"F10.opExtrude","SWEPT_BODY",BODY,{"disambiguationData":[OSD([sQuery(id+"F9.wireOp",EDGE,"E2402"),sQuery(id+"F9.wireOp",EDGE,"E2403"),sQuery(id+"F9.wireOp",EDGE,"E2404"),sQuery(id+"F9.wireOp",EDGE,"E2405"),sQuery(id+"F9.wireOp",EDGE,"E2406"),sQuery(id+"F9.wireOp",EDGE,"E2407"),sQuery(id+"F9.wireOp",EDGE,"E2408"),sQuery(id+"F9.wireOp",EDGE,"E2409"),sQuery(id+"F9.wireOp",EDGE,"E2410"),sQuery(id+"F9.wireOp",EDGE,"E2411"),sQuery(id+"F9.wireOp",EDGE,"E2412"),sQuery(id+"F9.wireOp",EDGE,"E2413"),sQuery(id+"F9.wireOp",EDGE,"E2414"),sQuery(id+"F9.wireOp",EDGE,"E2415"),sQuery(id+"F9.wireOp",EDGE,"E2416"),sQuery(id+"F9.wireOp",EDGE,"E2417"),sQuery(id+"F9.wireOp",EDGE,"E2418"),sQuery(id+"F9.wireOp",EDGE,"E2419"),sQuery(id+"F9.wireOp",EDGE,"E2420"),sQuery(id+"F9.wireOp",EDGE,"E2421"),sQuery(id+"F9.wireOp",EDGE,"E2422"),sQuery(id+"F9.wireOp",EDGE,"E2423"),sQuery(id+"F9.wireOp",EDGE,"E2424"),sQuery(id+"F9.wireOp",EDGE,"E2425"),sQuery(id+"F9.wireOp",EDGE,"E2426"),sQuery(id+"F9.wireOp",EDGE,"E2427"),sQuery(id+"F9.wireOp",EDGE,"E2428"),sQuery(id+"F9.wireOp",EDGE,"E2429"),sQuery(id+"F9.wireOp",EDGE,"E2430"),sQuery(id+"F9.wireOp",EDGE,"E2431"),sQuery(id+"F9.wireOp",EDGE,"E2432"),sQuery(id+"F9.wireOp",EDGE,"E2433"),sQuery(id+"F9.wireOp",EDGE,"E2434"),sQuery(id+"F9.wireOp",EDGE,"E2435"),sQuery(id+"F9.wireOp",EDGE,"E2436"),sQuery(id+"F9.wireOp",EDGE,"E2437"),sQuery(id+"F9.wireOp",EDGE,"E2438"),sQuery(id+"F9.wireOp",EDGE,"E2439"),sQuery(id+"F9.wireOp",EDGE,"E2440"),sQuery(id+"F9.wireOp",EDGE,"E2441"),sQuery(id+"F9.wireOp",EDGE,"E2442"),sQuery(id+"F9.wireOp",EDGE,"E2443"),sQuery(id+"F9.wireOp",EDGE,"E2444"),sQuery(id+"F9.wireOp",EDGE,"E2445"),sQuery(id+"F9.wireOp",EDGE,"E2446"),sQuery(id+"F9.wireOp",EDGE,"E2447"),sQuery(id+"F9.wireOp",EDGE,"E2448"),sQuery(id+"F9.wireOp",EDGE,"E2449"),sQuery(id+"F9.wireOp",EDGE,"E2450"),sQuery(id+"F9.wireOp",EDGE,"E2451"),sQuery(id+"F9.wireOp",EDGE,"E2452"),sQuery(id+"F9.wireOp",EDGE,"E2453"),sQuery(id+"F9.wireOp",EDGE,"E2454"),sQuery(id+"F9.wireOp",EDGE,"E2455"),sQuery(id+"F9.wireOp",EDGE,"E2456"),sQuery(id+"F9.wireOp",EDGE,"E2457"),sQuery(id+"F9.wireOp",EDGE,"E2458"),sQuery(id+"F9.wireOp",EDGE,"E2459"),sQuery(id+"F9.wireOp",EDGE,"E2460"),sQuery(id+"F9.wireOp",EDGE,"E2461"),sQuery(id+"F9.wireOp",EDGE,"E2462"),sQuery(id+"F9.wireOp",EDGE,"E2463"),sQuery(id+"F9.wireOp",EDGE,"E2464"),sQuery(id+"F9.wireOp",EDGE,"E2465"),sQuery(id+"F9.wireOp",EDGE,"E2466"),sQuery(id+"F9.wireOp",EDGE,"E2467"),sQuery(id+"F9.wireOp",EDGE,"E2468"),sQuery(id+"F9.wireOp",EDGE,"E2469"),sQuery(id+"F9.wireOp",EDGE,"E2470"),sQuery(id+"F9.wireOp",EDGE,"E2471"),sQuery(id+"F9.wireOp",EDGE,"E2472"),sQuery(id+"F9.wireOp",EDGE,"E2473"),sQuery(id+"F9.wireOp",EDGE,"E2474"),sQuery(id+"F9.wireOp",EDGE,"E2475"),sQuery(id+"F9.wireOp",EDGE,"E2476"),sQuery(id+"F9.wireOp",EDGE,"E2477"),sQuery(id+"F9.wireOp",EDGE,"E2478"),sQuery(id+"F9.wireOp",EDGE,"E2479"),sQuery(id+"F9.wireOp",EDGE,"E2480"),sQuery(id+"F9.wireOp",EDGE,"E2481"),sQuery(id+"F9.wireOp",EDGE,"E2482"),sQuery(id+"F9.wireOp",EDGE,"E2483"),sQuery(id+"F9.wireOp",EDGE,"E2484"),sQuery(id+"F9.wireOp",EDGE,"E2485"),sQuery(id+"F9.wireOp",EDGE,"E2486"),sQuery(id+"F9.wireOp",EDGE,"E2487"),sQuery(id+"F9.wireOp",EDGE,"E2488"),sQuery(id+"F9.wireOp",EDGE,"E2489"),sQuery(id+"F9.wireOp",EDGE,"E2490"),sQuery(id+"F9.wireOp",EDGE,"E2491"),sQuery(id+"F9.wireOp",EDGE,"E2492"),sQuery(id+"F9.wireOp",EDGE,"E2493"),sQuery(id+"F9.wireOp",EDGE,"E2494"),sQuery(id+"F9.wireOp",EDGE,"E2495"),sQuery(id+"F9.wireOp",EDGE,"E2496"),sQuery(id+"F9.wireOp",EDGE,"E2497"),sQuery(id+"F9.wireOp",EDGE,"E2498"),sQuery(id+"F9.wireOp",EDGE,"E2499"),sQuery(id+"F9.wireOp",EDGE,"E2500"),sQuery(id+"F9.wireOp",EDGE,"E2501"),sQuery(id+"F9.wireOp",EDGE,"E2502"),sQuery(id+"F9.wireOp",EDGE,"E2503"),sQuery(id+"F9.wireOp",EDGE,"E2504"),sQuery(id+"F9.wireOp",EDGE,"E2505"),sQuery(id+"F9.wireOp",EDGE,"E2506"),sQuery(id+"F9.wireOp",EDGE,"E2507"),sQuery(id+"F9.wireOp",EDGE,"E2508"),sQuery(id+"F9.wireOp",EDGE,"E2509"),sQuery(id+"F9.wireOp",EDGE,"E2510"),sQuery(id+"F9.wireOp",EDGE,"E2511"),sQuery(id+"F9.wireOp",EDGE,"E2512"),sQuery(id+"F9.wireOp",EDGE,"E2513"),sQuery(id+"F9.wireOp",EDGE,"E2514"),sQuery(id+"F9.wireOp",EDGE,"E2515"),sQuery(id+"F9.wireOp",EDGE,"E2516"),sQuery(id+"F9.wireOp",EDGE,"E2517"),sQuery(id+"F9.wireOp",EDGE,"E2518"),sQuery(id+"F9.wireOp",EDGE,"E2519"),sQuery(id+"F9.wireOp",EDGE,"E2520"),sQuery(id+"F9.wireOp",EDGE,"E2521"),sQuery(id+"F9.wireOp",EDGE,"E2522"),sQuery(id+"F9.wireOp",EDGE,"E2523"),sQuery(id+"F9.wireOp",EDGE,"E2524"),sQuery(id+"F9.wireOp",EDGE,"E2525"),sQuery(id+"F9.wireOp",EDGE,"E2526"),sQuery(id+"F9.wireOp",EDGE,"E2527"),sQuery(id+"F9.wireOp",EDGE,"E2528"),sQuery(id+"F9.wireOp",EDGE,"E2529"),sQuery(id+"F9.wireOp",EDGE,"E2530"),sQuery(id+"F9.wireOp",EDGE,"E2531"),sQuery(id+"F9.wireOp",EDGE,"E2532"),sQuery(id+"F9.wireOp",EDGE,"E2533"),sQuery(id+"F9.wireOp",EDGE,"E2534"),sQuery(id+"F9.wireOp",EDGE,"E2535"),sQuery(id+"F9.wireOp",EDGE,"E2536"),sQuery(id+"F9.wireOp",EDGE,"E2537"),sQuery(id+"F9.wireOp",EDGE,"E2538"),sQuery(id+"F9.wireOp",EDGE,"E2539"),sQuery(id+"F9.wireOp",EDGE,"E2540"),sQuery(id+"F9.wireOp",EDGE,"E2541"),sQuery(id+"F9.wireOp",EDGE,"E2542"),sQuery(id+"F9.wireOp",EDGE,"E2543"),sQuery(id+"F9.wireOp",EDGE,"E2544"),sQuery(id+"F9.wireOp",EDGE,"E2545"),sQuery(id+"F9.wireOp",EDGE,"E2546"),sQuery(id+"F9.wireOp",EDGE,"E2547"),sQuery(id+"F9.wireOp",EDGE,"E2548"),sQuery(id+"F9.wireOp",EDGE,"E2549"),sQuery(id+"F9.wireOp",EDGE,"E2550"),sQuery(id+"F9.wireOp",EDGE,"E2551"),sQuery(id+"F9.wireOp",EDGE,"E2552"),sQuery(id+"F9.wireOp",EDGE,"E2553"),sQuery(id+"F9.wireOp",EDGE,"E2554"),sQuery(id+"F9.wireOp",EDGE,"E2555"),sQuery(id+"F9.wireOp",EDGE,"E2556"),sQuery(id+"F9.wireOp",EDGE,"E2557"),sQuery(id+"F9.wireOp",EDGE,"E2558"),sQuery(id+"F9.wireOp",EDGE,"E2559"),sQuery(id+"F9.wireOp",EDGE,"E2560"),sQuery(id+"F9.wireOp",EDGE,"E2561"),sQuery(id+"F9.wireOp",EDGE,"E2562"),sQuery(id+"F9.wireOp",EDGE,"E2563"),sQuery(id+"F9.wireOp",EDGE,"E2564"),sQuery(id+"F9.wireOp",EDGE,"E2565"),sQuery(id+"F9.wireOp",EDGE,"E2566"),sQuery(id+"F9.wireOp",EDGE,"E2567"),sQuery(id+"F9.wireOp",EDGE,"E2568"),sQuery(id+"F9.wireOp",EDGE,"E2569"),sQuery(id+"F9.wireOp",EDGE,"E2570"),sQuery(id+"F9.wireOp",EDGE,"E2571"),sQuery(id+"F9.wireOp",EDGE,"E2572"),sQuery(id+"F9.wireOp",EDGE,"E2573"),sQuery(id+"F9.wireOp",EDGE,"E2574"),sQuery(id+"F9.wireOp",EDGE,"E2575"),sQuery(id+"F9.wireOp",EDGE,"E2576"),sQuery(id+"F9.wireOp",EDGE,"E2577"),sQuery(id+"F9.wireOp",EDGE,"E2578"),sQuery(id+"F9.wireOp",EDGE,"E2579"),sQuery(id+"F9.wireOp",EDGE,"E2580"),sQuery(id+"F9.wireOp",EDGE,"E2581"),sQuery(id+"F9.wireOp",EDGE,"E2582"),sQuery(id+"F9.wireOp",EDGE,"E2583"),sQuery(id+"F9.wireOp",EDGE,"E2584"),sQuery(id+"F9.wireOp",EDGE,"E2585"),sQuery(id+"F9.wireOp",EDGE,"E2586"),sQuery(id+"F9.wireOp",EDGE,"E2587"),sQuery(id+"F9.wireOp",EDGE,"E2588"),sQuery(id+"F9.wireOp",EDGE,"E2589"),sQuery(id+"F9.wireOp",EDGE,"E2590"),sQuery(id+"F9.wireOp",EDGE,"E2591"),sQuery(id+"F9.wireOp",EDGE,"E2592"),sQuery(id+"F9.wireOp",EDGE,"E2593"),sQuery(id+"F9.wireOp",EDGE,"E2594"),sQuery(id+"F9.wireOp",EDGE,"E2595"),sQuery(id+"F9.wireOp",EDGE,"E2596"),sQuery(id+"F9.wireOp",EDGE,"E2597"),sQuery(id+"F9.wireOp",EDGE,"E2598"),sQuery(id+"F9.wireOp",EDGE,"E2599"),sQuery(id+"F9.wireOp",EDGE,"E2600"),sQuery(id+"F9.wireOp",EDGE,"E2601"),sQuery(id+"F9.wireOp",EDGE,"E2602"),sQuery(id+"F9.wireOp",EDGE,"E2603"),sQuery(id+"F9.wireOp",EDGE,"E2604"),sQuery(id+"F9.wireOp",EDGE,"E2605"),sQuery(id+"F9.wireOp",EDGE,"E2606"),sQuery(id+"F9.wireOp",EDGE,"E2607"),sQuery(id+"F9.wireOp",EDGE,"E2608"),sQuery(id+"F9.wireOp",EDGE,"E2609"),sQuery(id+"F9.wireOp",EDGE,"E2610"),sQuery(id+"F9.wireOp",EDGE,"E2611"),sQuery(id+"F9.wireOp",EDGE,"E2612"),sQuery(id+"F9.wireOp",EDGE,"E2613"),sQuery(id+"F9.wireOp",EDGE,"E2614"),sQuery(id+"F9.wireOp",EDGE,"E2615"),sQuery(id+"F9.wireOp",EDGE,"E2616"),sQuery(id+"F9.wireOp",EDGE,"E2617"),sQuery(id+"F9.wireOp",EDGE,"E2618"),sQuery(id+"F9.wireOp",EDGE,"E2619"),sQuery(id+"F9.wireOp",EDGE,"E2620"),sQuery(id+"F9.wireOp",EDGE,"E2621"),sQuery(id+"F9.wireOp",EDGE,"E2622"),sQuery(id+"F9.wireOp",EDGE,"E2623"),sQuery(id+"F9.wireOp",EDGE,"E2624"),sQuery(id+"F9.wireOp",EDGE,"E2625"),sQuery(id+"F9.wireOp",EDGE,"E2626"),sQuery(id+"F9.wireOp",EDGE,"E2627"),sQuery(id+"F9.wireOp",EDGE,"E2628"),sQuery(id+"F9.wireOp",EDGE,"E2629"),sQuery(id+"F9.wireOp",EDGE,"E2630"),sQuery(id+"F9.wireOp",EDGE,"E2631"),sQuery(id+"F9.wireOp",EDGE,"E2632"),sQuery(id+"F9.wireOp",EDGE,"E2633"),sQuery(id+"F9.wireOp",EDGE,"E2634")])]});
            var Q9;
            Q9=qCreatedBy(makeId("Origin.pointOp"),VERTEX);
            transform(context, id + "F11", {"entities" : qUnion([Q0, Q1, Q2, Q3, Q4, Q5, Q6, Q7, Q8]), "transformType" : TransformType.SCALE_UNIFORMLY, "scale" : 1.5, "scalePoint" : qUnion([Q9]), "makeCopy" : false});
        }
        {
            var Q0;
            Q0=makeQuery(id+"F10.opExtrude","SWEPT_BODY",BODY,{"disambiguationData":[OSD([sQuery(id+"F9.wireOp",EDGE,"E709"),sQuery(id+"F9.wireOp",EDGE,"E710"),sQuery(id+"F9.wireOp",EDGE,"E711"),sQuery(id+"F9.wireOp",EDGE,"E712"),sQuery(id+"F9.wireOp",EDGE,"E713"),sQuery(id+"F9.wireOp",EDGE,"E714"),sQuery(id+"F9.wireOp",EDGE,"E715"),sQuery(id+"F9.wireOp",EDGE,"E716"),sQuery(id+"F9.wireOp",EDGE,"E717"),sQuery(id+"F9.wireOp",EDGE,"E718"),sQuery(id+"F9.wireOp",EDGE,"E719"),sQuery(id+"F9.wireOp",EDGE,"E720"),sQuery(id+"F9.wireOp",EDGE,"E721"),sQuery(id+"F9.wireOp",EDGE,"E722"),sQuery(id+"F9.wireOp",EDGE,"E723"),sQuery(id+"F9.wireOp",EDGE,"E724"),sQuery(id+"F9.wireOp",EDGE,"E725"),sQuery(id+"F9.wireOp",EDGE,"E726"),sQuery(id+"F9.wireOp",EDGE,"E727"),sQuery(id+"F9.wireOp",EDGE,"E728"),sQuery(id+"F9.wireOp",EDGE,"E729"),sQuery(id+"F9.wireOp",EDGE,"E730"),sQuery(id+"F9.wireOp",EDGE,"E731"),sQuery(id+"F9.wireOp",EDGE,"E732"),sQuery(id+"F9.wireOp",EDGE,"E733"),sQuery(id+"F9.wireOp",EDGE,"E734"),sQuery(id+"F9.wireOp",EDGE,"E735"),sQuery(id+"F9.wireOp",EDGE,"E736"),sQuery(id+"F9.wireOp",EDGE,"E737"),sQuery(id+"F9.wireOp",EDGE,"E738"),sQuery(id+"F9.wireOp",EDGE,"E739"),sQuery(id+"F9.wireOp",EDGE,"E740"),sQuery(id+"F9.wireOp",EDGE,"E741"),sQuery(id+"F9.wireOp",EDGE,"E742"),sQuery(id+"F9.wireOp",EDGE,"E743"),sQuery(id+"F9.wireOp",EDGE,"E744"),sQuery(id+"F9.wireOp",EDGE,"E745"),sQuery(id+"F9.wireOp",EDGE,"E746"),sQuery(id+"F9.wireOp",EDGE,"E747"),sQuery(id+"F9.wireOp",EDGE,"E748"),sQuery(id+"F9.wireOp",EDGE,"E749"),sQuery(id+"F9.wireOp",EDGE,"E750"),sQuery(id+"F9.wireOp",EDGE,"E751"),sQuery(id+"F9.wireOp",EDGE,"E752"),sQuery(id+"F9.wireOp",EDGE,"E753"),sQuery(id+"F9.wireOp",EDGE,"E754"),sQuery(id+"F9.wireOp",EDGE,"E755"),sQuery(id+"F9.wireOp",EDGE,"E756"),sQuery(id+"F9.wireOp",EDGE,"E757"),sQuery(id+"F9.wireOp",EDGE,"E758"),sQuery(id+"F9.wireOp",EDGE,"E759"),sQuery(id+"F9.wireOp",EDGE,"E760"),sQuery(id+"F9.wireOp",EDGE,"E761"),sQuery(id+"F9.wireOp",EDGE,"E762"),sQuery(id+"F9.wireOp",EDGE,"E763"),sQuery(id+"F9.wireOp",EDGE,"E764"),sQuery(id+"F9.wireOp",EDGE,"E765"),sQuery(id+"F9.wireOp",EDGE,"E766"),sQuery(id+"F9.wireOp",EDGE,"E767"),sQuery(id+"F9.wireOp",EDGE,"E768"),sQuery(id+"F9.wireOp",EDGE,"E769"),sQuery(id+"F9.wireOp",EDGE,"E770"),sQuery(id+"F9.wireOp",EDGE,"E771"),sQuery(id+"F9.wireOp",EDGE,"E772"),sQuery(id+"F9.wireOp",EDGE,"E773"),sQuery(id+"F9.wireOp",EDGE,"E774"),sQuery(id+"F9.wireOp",EDGE,"E775"),sQuery(id+"F9.wireOp",EDGE,"E776"),sQuery(id+"F9.wireOp",EDGE,"E777"),sQuery(id+"F9.wireOp",EDGE,"E778"),sQuery(id+"F9.wireOp",EDGE,"E779"),sQuery(id+"F9.wireOp",EDGE,"E780"),sQuery(id+"F9.wireOp",EDGE,"E781"),sQuery(id+"F9.wireOp",EDGE,"E782"),sQuery(id+"F9.wireOp",EDGE,"E783"),sQuery(id+"F9.wireOp",EDGE,"E784"),sQuery(id+"F9.wireOp",EDGE,"E785"),sQuery(id+"F9.wireOp",EDGE,"E786"),sQuery(id+"F9.wireOp",EDGE,"E787"),sQuery(id+"F9.wireOp",EDGE,"E788"),sQuery(id+"F9.wireOp",EDGE,"E789"),sQuery(id+"F9.wireOp",EDGE,"E790"),sQuery(id+"F9.wireOp",EDGE,"E791"),sQuery(id+"F9.wireOp",EDGE,"E792"),sQuery(id+"F9.wireOp",EDGE,"E793"),sQuery(id+"F9.wireOp",EDGE,"E794"),sQuery(id+"F9.wireOp",EDGE,"E795"),sQuery(id+"F9.wireOp",EDGE,"E796"),sQuery(id+"F9.wireOp",EDGE,"E797"),sQuery(id+"F9.wireOp",EDGE,"E798"),sQuery(id+"F9.wireOp",EDGE,"E799"),sQuery(id+"F9.wireOp",EDGE,"E800"),sQuery(id+"F9.wireOp",EDGE,"E801"),sQuery(id+"F9.wireOp",EDGE,"E802"),sQuery(id+"F9.wireOp",EDGE,"E803"),sQuery(id+"F9.wireOp",EDGE,"E804"),sQuery(id+"F9.wireOp",EDGE,"E805"),sQuery(id+"F9.wireOp",EDGE,"E806"),sQuery(id+"F9.wireOp",EDGE,"E807"),sQuery(id+"F9.wireOp",EDGE,"E808"),sQuery(id+"F9.wireOp",EDGE,"E809"),sQuery(id+"F9.wireOp",EDGE,"E810"),sQuery(id+"F9.wireOp",EDGE,"E811"),sQuery(id+"F9.wireOp",EDGE,"E812"),sQuery(id+"F9.wireOp",EDGE,"E813"),sQuery(id+"F9.wireOp",EDGE,"E814"),sQuery(id+"F9.wireOp",EDGE,"E815"),sQuery(id+"F9.wireOp",EDGE,"E816"),sQuery(id+"F9.wireOp",EDGE,"E817"),sQuery(id+"F9.wireOp",EDGE,"E818"),sQuery(id+"F9.wireOp",EDGE,"E819"),sQuery(id+"F9.wireOp",EDGE,"E820"),sQuery(id+"F9.wireOp",EDGE,"E821"),sQuery(id+"F9.wireOp",EDGE,"E822"),sQuery(id+"F9.wireOp",EDGE,"E823"),sQuery(id+"F9.wireOp",EDGE,"E824"),sQuery(id+"F9.wireOp",EDGE,"E825"),sQuery(id+"F9.wireOp",EDGE,"E826"),sQuery(id+"F9.wireOp",EDGE,"E827"),sQuery(id+"F9.wireOp",EDGE,"E828"),sQuery(id+"F9.wireOp",EDGE,"E829"),sQuery(id+"F9.wireOp",EDGE,"E830"),sQuery(id+"F9.wireOp",EDGE,"E831"),sQuery(id+"F9.wireOp",EDGE,"E832"),sQuery(id+"F9.wireOp",EDGE,"E833"),sQuery(id+"F9.wireOp",EDGE,"E834"),sQuery(id+"F9.wireOp",EDGE,"E835"),sQuery(id+"F9.wireOp",EDGE,"E836"),sQuery(id+"F9.wireOp",EDGE,"E837"),sQuery(id+"F9.wireOp",EDGE,"E838"),sQuery(id+"F9.wireOp",EDGE,"E839"),sQuery(id+"F9.wireOp",EDGE,"E840"),sQuery(id+"F9.wireOp",EDGE,"E841"),sQuery(id+"F9.wireOp",EDGE,"E842"),sQuery(id+"F9.wireOp",EDGE,"E843"),sQuery(id+"F9.wireOp",EDGE,"E844"),sQuery(id+"F9.wireOp",EDGE,"E845"),sQuery(id+"F9.wireOp",EDGE,"E846"),sQuery(id+"F9.wireOp",EDGE,"E847"),sQuery(id+"F9.wireOp",EDGE,"E848"),sQuery(id+"F9.wireOp",EDGE,"E849"),sQuery(id+"F9.wireOp",EDGE,"E850"),sQuery(id+"F9.wireOp",EDGE,"E851"),sQuery(id+"F9.wireOp",EDGE,"E852"),sQuery(id+"F9.wireOp",EDGE,"E853"),sQuery(id+"F9.wireOp",EDGE,"E854"),sQuery(id+"F9.wireOp",EDGE,"E855"),sQuery(id+"F9.wireOp",EDGE,"E856"),sQuery(id+"F9.wireOp",EDGE,"E857"),sQuery(id+"F9.wireOp",EDGE,"E858"),sQuery(id+"F9.wireOp",EDGE,"E859"),sQuery(id+"F9.wireOp",EDGE,"E860"),sQuery(id+"F9.wireOp",EDGE,"E861"),sQuery(id+"F9.wireOp",EDGE,"E862"),sQuery(id+"F9.wireOp",EDGE,"E863"),sQuery(id+"F9.wireOp",EDGE,"E864"),sQuery(id+"F9.wireOp",EDGE,"E865"),sQuery(id+"F9.wireOp",EDGE,"E866"),sQuery(id+"F9.wireOp",EDGE,"E867"),sQuery(id+"F9.wireOp",EDGE,"E868"),sQuery(id+"F9.wireOp",EDGE,"E869"),sQuery(id+"F9.wireOp",EDGE,"E870"),sQuery(id+"F9.wireOp",EDGE,"E871"),sQuery(id+"F9.wireOp",EDGE,"E872"),sQuery(id+"F9.wireOp",EDGE,"E873"),sQuery(id+"F9.wireOp",EDGE,"E874"),sQuery(id+"F9.wireOp",EDGE,"E875"),sQuery(id+"F9.wireOp",EDGE,"E876"),sQuery(id+"F9.wireOp",EDGE,"E877"),sQuery(id+"F9.wireOp",EDGE,"E878"),sQuery(id+"F9.wireOp",EDGE,"E879"),sQuery(id+"F9.wireOp",EDGE,"E880"),sQuery(id+"F9.wireOp",EDGE,"E881"),sQuery(id+"F9.wireOp",EDGE,"E882"),sQuery(id+"F9.wireOp",EDGE,"E883"),sQuery(id+"F9.wireOp",EDGE,"E884"),sQuery(id+"F9.wireOp",EDGE,"E885"),sQuery(id+"F9.wireOp",EDGE,"E886"),sQuery(id+"F9.wireOp",EDGE,"E887"),sQuery(id+"F9.wireOp",EDGE,"E888"),sQuery(id+"F9.wireOp",EDGE,"E889"),sQuery(id+"F9.wireOp",EDGE,"E890"),sQuery(id+"F9.wireOp",EDGE,"E891"),sQuery(id+"F9.wireOp",EDGE,"E892"),sQuery(id+"F9.wireOp",EDGE,"E893"),sQuery(id+"F9.wireOp",EDGE,"E894"),sQuery(id+"F9.wireOp",EDGE,"E895"),sQuery(id+"F9.wireOp",EDGE,"E896"),sQuery(id+"F9.wireOp",EDGE,"E897"),sQuery(id+"F9.wireOp",EDGE,"E898"),sQuery(id+"F9.wireOp",EDGE,"E899"),sQuery(id+"F9.wireOp",EDGE,"E900"),sQuery(id+"F9.wireOp",EDGE,"E901"),sQuery(id+"F9.wireOp",EDGE,"E902"),sQuery(id+"F9.wireOp",EDGE,"E903"),sQuery(id+"F9.wireOp",EDGE,"E904"),sQuery(id+"F9.wireOp",EDGE,"E905"),sQuery(id+"F9.wireOp",EDGE,"E906"),sQuery(id+"F9.wireOp",EDGE,"E907"),sQuery(id+"F9.wireOp",EDGE,"E908"),sQuery(id+"F9.wireOp",EDGE,"E909"),sQuery(id+"F9.wireOp",EDGE,"E910"),sQuery(id+"F9.wireOp",EDGE,"E911"),sQuery(id+"F9.wireOp",EDGE,"E912"),sQuery(id+"F9.wireOp",EDGE,"E913"),sQuery(id+"F9.wireOp",EDGE,"E913"),sQuery(id+"F9.wireOp",EDGE,"E913"),sQuery(id+"F9.wireOp",EDGE,"E913"),sQuery(id+"F9.wireOp",EDGE,"E914"),sQuery(id+"F9.wireOp",EDGE,"E915"),sQuery(id+"F9.wireOp",EDGE,"E916"),sQuery(id+"F9.wireOp",EDGE,"E917"),sQuery(id+"F9.wireOp",EDGE,"E917"),sQuery(id+"F9.wireOp",EDGE,"E918"),sQuery(id+"F9.wireOp",EDGE,"E919"),sQuery(id+"F9.wireOp",EDGE,"E920"),sQuery(id+"F9.wireOp",EDGE,"E921"),sQuery(id+"F9.wireOp",EDGE,"E922"),sQuery(id+"F9.wireOp",EDGE,"E923"),sQuery(id+"F9.wireOp",EDGE,"E923"),sQuery(id+"F9.wireOp",EDGE,"E924"),sQuery(id+"F9.wireOp",EDGE,"E925"),sQuery(id+"F9.wireOp",EDGE,"E926"),sQuery(id+"F9.wireOp",EDGE,"E927"),sQuery(id+"F9.wireOp",EDGE,"E928"),sQuery(id+"F9.wireOp",EDGE,"E929"),sQuery(id+"F9.wireOp",EDGE,"E930"),sQuery(id+"F9.wireOp",EDGE,"E931"),sQuery(id+"F9.wireOp",EDGE,"E932"),sQuery(id+"F9.wireOp",EDGE,"E933"),sQuery(id+"F9.wireOp",EDGE,"E934"),sQuery(id+"F9.wireOp",EDGE,"E935"),sQuery(id+"F9.wireOp",EDGE,"E936"),sQuery(id+"F9.wireOp",EDGE,"E937"),sQuery(id+"F9.wireOp",EDGE,"E938"),sQuery(id+"F9.wireOp",EDGE,"E939"),sQuery(id+"F9.wireOp",EDGE,"E940"),sQuery(id+"F9.wireOp",EDGE,"E941"),sQuery(id+"F9.wireOp",EDGE,"E942"),sQuery(id+"F9.wireOp",EDGE,"E943"),sQuery(id+"F9.wireOp",EDGE,"E944"),sQuery(id+"F9.wireOp",EDGE,"E945"),sQuery(id+"F9.wireOp",EDGE,"E946"),sQuery(id+"F9.wireOp",EDGE,"E947"),sQuery(id+"F9.wireOp",EDGE,"E948"),sQuery(id+"F9.wireOp",EDGE,"E949"),sQuery(id+"F9.wireOp",EDGE,"E950"),sQuery(id+"F9.wireOp",EDGE,"E951"),sQuery(id+"F9.wireOp",EDGE,"E952"),sQuery(id+"F9.wireOp",EDGE,"E953"),sQuery(id+"F9.wireOp",EDGE,"E954"),sQuery(id+"F9.wireOp",EDGE,"E955"),sQuery(id+"F9.wireOp",EDGE,"E956"),sQuery(id+"F9.wireOp",EDGE,"E957"),sQuery(id+"F9.wireOp",EDGE,"E958"),sQuery(id+"F9.wireOp",EDGE,"E959"),sQuery(id+"F9.wireOp",EDGE,"E960"),sQuery(id+"F9.wireOp",EDGE,"E961"),sQuery(id+"F9.wireOp",EDGE,"E962"),sQuery(id+"F9.wireOp",EDGE,"E963"),sQuery(id+"F9.wireOp",EDGE,"E964"),sQuery(id+"F9.wireOp",EDGE,"E965"),sQuery(id+"F9.wireOp",EDGE,"E966"),sQuery(id+"F9.wireOp",EDGE,"E967"),sQuery(id+"F9.wireOp",EDGE,"E968"),sQuery(id+"F9.wireOp",EDGE,"E969"),sQuery(id+"F9.wireOp",EDGE,"E970"),sQuery(id+"F9.wireOp",EDGE,"E971"),sQuery(id+"F9.wireOp",EDGE,"E972"),sQuery(id+"F9.wireOp",EDGE,"E973"),sQuery(id+"F9.wireOp",EDGE,"E974"),sQuery(id+"F9.wireOp",EDGE,"E975"),sQuery(id+"F9.wireOp",EDGE,"E976"),sQuery(id+"F9.wireOp",EDGE,"E977"),sQuery(id+"F9.wireOp",EDGE,"E978"),sQuery(id+"F9.wireOp",EDGE,"E979"),sQuery(id+"F9.wireOp",EDGE,"E980"),sQuery(id+"F9.wireOp",EDGE,"E981"),sQuery(id+"F9.wireOp",EDGE,"E982"),sQuery(id+"F9.wireOp",EDGE,"E983"),sQuery(id+"F9.wireOp",EDGE,"E984"),sQuery(id+"F9.wireOp",EDGE,"E985"),sQuery(id+"F9.wireOp",EDGE,"E986"),sQuery(id+"F9.wireOp",EDGE,"E987"),sQuery(id+"F9.wireOp",EDGE,"E988"),sQuery(id+"F9.wireOp",EDGE,"E989"),sQuery(id+"F9.wireOp",EDGE,"E990"),sQuery(id+"F9.wireOp",EDGE,"E991"),sQuery(id+"F9.wireOp",EDGE,"E992"),sQuery(id+"F9.wireOp",EDGE,"E993"),sQuery(id+"F9.wireOp",EDGE,"E994"),sQuery(id+"F9.wireOp",EDGE,"E995"),sQuery(id+"F9.wireOp",EDGE,"E996"),sQuery(id+"F9.wireOp",EDGE,"E997"),sQuery(id+"F9.wireOp",EDGE,"E998"),sQuery(id+"F9.wireOp",EDGE,"E999"),sQuery(id+"F9.wireOp",EDGE,"E1000"),sQuery(id+"F9.wireOp",EDGE,"E1001"),sQuery(id+"F9.wireOp",EDGE,"E1002"),sQuery(id+"F9.wireOp",EDGE,"E1003"),sQuery(id+"F9.wireOp",EDGE,"E1004"),sQuery(id+"F9.wireOp",EDGE,"E1005"),sQuery(id+"F9.wireOp",EDGE,"E1006"),sQuery(id+"F9.wireOp",EDGE,"E1007"),sQuery(id+"F9.wireOp",EDGE,"E1008"),sQuery(id+"F9.wireOp",EDGE,"E1009"),sQuery(id+"F9.wireOp",EDGE,"E1010"),sQuery(id+"F9.wireOp",EDGE,"E1011"),sQuery(id+"F9.wireOp",EDGE,"E1012"),sQuery(id+"F9.wireOp",EDGE,"E1013"),sQuery(id+"F9.wireOp",EDGE,"E1014"),sQuery(id+"F9.wireOp",EDGE,"E1015"),sQuery(id+"F9.wireOp",EDGE,"E1016"),sQuery(id+"F9.wireOp",EDGE,"E1017"),sQuery(id+"F9.wireOp",EDGE,"E1018"),sQuery(id+"F9.wireOp",EDGE,"E1019"),sQuery(id+"F9.wireOp",EDGE,"E1020"),sQuery(id+"F9.wireOp",EDGE,"E1021"),sQuery(id+"F9.wireOp",EDGE,"E1022"),sQuery(id+"F9.wireOp",EDGE,"E1023"),sQuery(id+"F9.wireOp",EDGE,"E1024"),sQuery(id+"F9.wireOp",EDGE,"E1025")])]});
            var Q1;
            Q1=makeQuery(id+"F10.opExtrude","SWEPT_BODY",BODY,{"disambiguationData":[OSD([sQuery(id+"F9.wireOp",EDGE,"E1026"),sQuery(id+"F9.wireOp",EDGE,"E1027"),sQuery(id+"F9.wireOp",EDGE,"E1028"),sQuery(id+"F9.wireOp",EDGE,"E1029"),sQuery(id+"F9.wireOp",EDGE,"E1030"),sQuery(id+"F9.wireOp",EDGE,"E1031"),sQuery(id+"F9.wireOp",EDGE,"E1032"),sQuery(id+"F9.wireOp",EDGE,"E1033"),sQuery(id+"F9.wireOp",EDGE,"E1034"),sQuery(id+"F9.wireOp",EDGE,"E1035"),sQuery(id+"F9.wireOp",EDGE,"E1036"),sQuery(id+"F9.wireOp",EDGE,"E1037"),sQuery(id+"F9.wireOp",EDGE,"E1038"),sQuery(id+"F9.wireOp",EDGE,"E1039"),sQuery(id+"F9.wireOp",EDGE,"E1040"),sQuery(id+"F9.wireOp",EDGE,"E1041"),sQuery(id+"F9.wireOp",EDGE,"E1042"),sQuery(id+"F9.wireOp",EDGE,"E1043"),sQuery(id+"F9.wireOp",EDGE,"E1044"),sQuery(id+"F9.wireOp",EDGE,"E1045"),sQuery(id+"F9.wireOp",EDGE,"E1046"),sQuery(id+"F9.wireOp",EDGE,"E1047"),sQuery(id+"F9.wireOp",EDGE,"E1048"),sQuery(id+"F9.wireOp",EDGE,"E1049"),sQuery(id+"F9.wireOp",EDGE,"E1050"),sQuery(id+"F9.wireOp",EDGE,"E1051"),sQuery(id+"F9.wireOp",EDGE,"E1052"),sQuery(id+"F9.wireOp",EDGE,"E1053"),sQuery(id+"F9.wireOp",EDGE,"E1054"),sQuery(id+"F9.wireOp",EDGE,"E1055"),sQuery(id+"F9.wireOp",EDGE,"E1056"),sQuery(id+"F9.wireOp",EDGE,"E1057"),sQuery(id+"F9.wireOp",EDGE,"E1058"),sQuery(id+"F9.wireOp",EDGE,"E1059"),sQuery(id+"F9.wireOp",EDGE,"E1060"),sQuery(id+"F9.wireOp",EDGE,"E1061"),sQuery(id+"F9.wireOp",EDGE,"E1062"),sQuery(id+"F9.wireOp",EDGE,"E1063"),sQuery(id+"F9.wireOp",EDGE,"E1064"),sQuery(id+"F9.wireOp",EDGE,"E1065"),sQuery(id+"F9.wireOp",EDGE,"E1066"),sQuery(id+"F9.wireOp",EDGE,"E1067"),sQuery(id+"F9.wireOp",EDGE,"E1068"),sQuery(id+"F9.wireOp",EDGE,"E1069"),sQuery(id+"F9.wireOp",EDGE,"E1070"),sQuery(id+"F9.wireOp",EDGE,"E1071"),sQuery(id+"F9.wireOp",EDGE,"E1072"),sQuery(id+"F9.wireOp",EDGE,"E1073"),sQuery(id+"F9.wireOp",EDGE,"E1074"),sQuery(id+"F9.wireOp",EDGE,"E1075"),sQuery(id+"F9.wireOp",EDGE,"E1076"),sQuery(id+"F9.wireOp",EDGE,"E1077"),sQuery(id+"F9.wireOp",EDGE,"E1078"),sQuery(id+"F9.wireOp",EDGE,"E1079"),sQuery(id+"F9.wireOp",EDGE,"E1080"),sQuery(id+"F9.wireOp",EDGE,"E1081"),sQuery(id+"F9.wireOp",EDGE,"E1082"),sQuery(id+"F9.wireOp",EDGE,"E1083"),sQuery(id+"F9.wireOp",EDGE,"E1084"),sQuery(id+"F9.wireOp",EDGE,"E1085"),sQuery(id+"F9.wireOp",EDGE,"E1086"),sQuery(id+"F9.wireOp",EDGE,"E1087"),sQuery(id+"F9.wireOp",EDGE,"E1088"),sQuery(id+"F9.wireOp",EDGE,"E1089"),sQuery(id+"F9.wireOp",EDGE,"E1090"),sQuery(id+"F9.wireOp",EDGE,"E1091"),sQuery(id+"F9.wireOp",EDGE,"E1092"),sQuery(id+"F9.wireOp",EDGE,"E1093"),sQuery(id+"F9.wireOp",EDGE,"E1094"),sQuery(id+"F9.wireOp",EDGE,"E1095"),sQuery(id+"F9.wireOp",EDGE,"E1096"),sQuery(id+"F9.wireOp",EDGE,"E1097"),sQuery(id+"F9.wireOp",EDGE,"E1098"),sQuery(id+"F9.wireOp",EDGE,"E1099"),sQuery(id+"F9.wireOp",EDGE,"E1100"),sQuery(id+"F9.wireOp",EDGE,"E1101"),sQuery(id+"F9.wireOp",EDGE,"E1102"),sQuery(id+"F9.wireOp",EDGE,"E1103"),sQuery(id+"F9.wireOp",EDGE,"E1104"),sQuery(id+"F9.wireOp",EDGE,"E1105"),sQuery(id+"F9.wireOp",EDGE,"E1106"),sQuery(id+"F9.wireOp",EDGE,"E1107"),sQuery(id+"F9.wireOp",EDGE,"E1108"),sQuery(id+"F9.wireOp",EDGE,"E1109"),sQuery(id+"F9.wireOp",EDGE,"E1110"),sQuery(id+"F9.wireOp",EDGE,"E1111"),sQuery(id+"F9.wireOp",EDGE,"E1112"),sQuery(id+"F9.wireOp",EDGE,"E1113"),sQuery(id+"F9.wireOp",EDGE,"E1114"),sQuery(id+"F9.wireOp",EDGE,"E1115"),sQuery(id+"F9.wireOp",EDGE,"E1116"),sQuery(id+"F9.wireOp",EDGE,"E1117"),sQuery(id+"F9.wireOp",EDGE,"E1118"),sQuery(id+"F9.wireOp",EDGE,"E1119"),sQuery(id+"F9.wireOp",EDGE,"E1120"),sQuery(id+"F9.wireOp",EDGE,"E1121"),sQuery(id+"F9.wireOp",EDGE,"E1122"),sQuery(id+"F9.wireOp",EDGE,"E1123"),sQuery(id+"F9.wireOp",EDGE,"E1124"),sQuery(id+"F9.wireOp",EDGE,"E1125"),sQuery(id+"F9.wireOp",EDGE,"E1126"),sQuery(id+"F9.wireOp",EDGE,"E1127"),sQuery(id+"F9.wireOp",EDGE,"E1128"),sQuery(id+"F9.wireOp",EDGE,"E1129"),sQuery(id+"F9.wireOp",EDGE,"E1130"),sQuery(id+"F9.wireOp",EDGE,"E1131"),sQuery(id+"F9.wireOp",EDGE,"E1132"),sQuery(id+"F9.wireOp",EDGE,"E1133"),sQuery(id+"F9.wireOp",EDGE,"E1134"),sQuery(id+"F9.wireOp",EDGE,"E1135"),sQuery(id+"F9.wireOp",EDGE,"E1136"),sQuery(id+"F9.wireOp",EDGE,"E1137"),sQuery(id+"F9.wireOp",EDGE,"E1138"),sQuery(id+"F9.wireOp",EDGE,"E1139"),sQuery(id+"F9.wireOp",EDGE,"E1140"),sQuery(id+"F9.wireOp",EDGE,"E1141"),sQuery(id+"F9.wireOp",EDGE,"E1142"),sQuery(id+"F9.wireOp",EDGE,"E1143"),sQuery(id+"F9.wireOp",EDGE,"E1144"),sQuery(id+"F9.wireOp",EDGE,"E1145"),sQuery(id+"F9.wireOp",EDGE,"E1146"),sQuery(id+"F9.wireOp",EDGE,"E1147"),sQuery(id+"F9.wireOp",EDGE,"E1148"),sQuery(id+"F9.wireOp",EDGE,"E1149"),sQuery(id+"F9.wireOp",EDGE,"E1150"),sQuery(id+"F9.wireOp",EDGE,"E1151"),sQuery(id+"F9.wireOp",EDGE,"E1152"),sQuery(id+"F9.wireOp",EDGE,"E1153"),sQuery(id+"F9.wireOp",EDGE,"E1154"),sQuery(id+"F9.wireOp",EDGE,"E1155"),sQuery(id+"F9.wireOp",EDGE,"E1156"),sQuery(id+"F9.wireOp",EDGE,"E1157"),sQuery(id+"F9.wireOp",EDGE,"E1158"),sQuery(id+"F9.wireOp",EDGE,"E1159"),sQuery(id+"F9.wireOp",EDGE,"E1160"),sQuery(id+"F9.wireOp",EDGE,"E1161"),sQuery(id+"F9.wireOp",EDGE,"E1162"),sQuery(id+"F9.wireOp",EDGE,"E1163"),sQuery(id+"F9.wireOp",EDGE,"E1164"),sQuery(id+"F9.wireOp",EDGE,"E1165"),sQuery(id+"F9.wireOp",EDGE,"E1166"),sQuery(id+"F9.wireOp",EDGE,"E1167"),sQuery(id+"F9.wireOp",EDGE,"E1168"),sQuery(id+"F9.wireOp",EDGE,"E1169"),sQuery(id+"F9.wireOp",EDGE,"E1170"),sQuery(id+"F9.wireOp",EDGE,"E1171"),sQuery(id+"F9.wireOp",EDGE,"E1172"),sQuery(id+"F9.wireOp",EDGE,"E1173"),sQuery(id+"F9.wireOp",EDGE,"E1174"),sQuery(id+"F9.wireOp",EDGE,"E1175"),sQuery(id+"F9.wireOp",EDGE,"E1176"),sQuery(id+"F9.wireOp",EDGE,"E1177"),sQuery(id+"F9.wireOp",EDGE,"E1178"),sQuery(id+"F9.wireOp",EDGE,"E1179"),sQuery(id+"F9.wireOp",EDGE,"E1180"),sQuery(id+"F9.wireOp",EDGE,"E1181"),sQuery(id+"F9.wireOp",EDGE,"E1182"),sQuery(id+"F9.wireOp",EDGE,"E1183"),sQuery(id+"F9.wireOp",EDGE,"E1184"),sQuery(id+"F9.wireOp",EDGE,"E1185"),sQuery(id+"F9.wireOp",EDGE,"E1186"),sQuery(id+"F9.wireOp",EDGE,"E1187"),sQuery(id+"F9.wireOp",EDGE,"E1188"),sQuery(id+"F9.wireOp",EDGE,"E1189"),sQuery(id+"F9.wireOp",EDGE,"E1190"),sQuery(id+"F9.wireOp",EDGE,"E1191"),sQuery(id+"F9.wireOp",EDGE,"E1192"),sQuery(id+"F9.wireOp",EDGE,"E1193"),sQuery(id+"F9.wireOp",EDGE,"E1194"),sQuery(id+"F9.wireOp",EDGE,"E1195"),sQuery(id+"F9.wireOp",EDGE,"E1196"),sQuery(id+"F9.wireOp",EDGE,"E1197"),sQuery(id+"F9.wireOp",EDGE,"E1198"),sQuery(id+"F9.wireOp",EDGE,"E1199"),sQuery(id+"F9.wireOp",EDGE,"E1200"),sQuery(id+"F9.wireOp",EDGE,"E1201"),sQuery(id+"F9.wireOp",EDGE,"E1202"),sQuery(id+"F9.wireOp",EDGE,"E1203"),sQuery(id+"F9.wireOp",EDGE,"E1204"),sQuery(id+"F9.wireOp",EDGE,"E1205"),sQuery(id+"F9.wireOp",EDGE,"E1206"),sQuery(id+"F9.wireOp",EDGE,"E1207"),sQuery(id+"F9.wireOp",EDGE,"E1208"),sQuery(id+"F9.wireOp",EDGE,"E1209"),sQuery(id+"F9.wireOp",EDGE,"E1210"),sQuery(id+"F9.wireOp",EDGE,"E1211"),sQuery(id+"F9.wireOp",EDGE,"E1212"),sQuery(id+"F9.wireOp",EDGE,"E1213"),sQuery(id+"F9.wireOp",EDGE,"E1214"),sQuery(id+"F9.wireOp",EDGE,"E1215"),sQuery(id+"F9.wireOp",EDGE,"E1216"),sQuery(id+"F9.wireOp",EDGE,"E1217"),sQuery(id+"F9.wireOp",EDGE,"E1218"),sQuery(id+"F9.wireOp",EDGE,"E1219"),sQuery(id+"F9.wireOp",EDGE,"E1220"),sQuery(id+"F9.wireOp",EDGE,"E1221"),sQuery(id+"F9.wireOp",EDGE,"E1222"),sQuery(id+"F9.wireOp",EDGE,"E1223"),sQuery(id+"F9.wireOp",EDGE,"E1224"),sQuery(id+"F9.wireOp",EDGE,"E1225"),sQuery(id+"F9.wireOp",EDGE,"E1226"),sQuery(id+"F9.wireOp",EDGE,"E1227"),sQuery(id+"F9.wireOp",EDGE,"E1228"),sQuery(id+"F9.wireOp",EDGE,"E1229"),sQuery(id+"F9.wireOp",EDGE,"E1230"),sQuery(id+"F9.wireOp",EDGE,"E1231"),sQuery(id+"F9.wireOp",EDGE,"E1232"),sQuery(id+"F9.wireOp",EDGE,"E1233"),sQuery(id+"F9.wireOp",EDGE,"E1234"),sQuery(id+"F9.wireOp",EDGE,"E1235"),sQuery(id+"F9.wireOp",EDGE,"E1236"),sQuery(id+"F9.wireOp",EDGE,"E1237"),sQuery(id+"F9.wireOp",EDGE,"E1238"),sQuery(id+"F9.wireOp",EDGE,"E1239"),sQuery(id+"F9.wireOp",EDGE,"E1240"),sQuery(id+"F9.wireOp",EDGE,"E1241"),sQuery(id+"F9.wireOp",EDGE,"E1242"),sQuery(id+"F9.wireOp",EDGE,"E1243"),sQuery(id+"F9.wireOp",EDGE,"E1244"),sQuery(id+"F9.wireOp",EDGE,"E1245"),sQuery(id+"F9.wireOp",EDGE,"E1246"),sQuery(id+"F9.wireOp",EDGE,"E1247"),sQuery(id+"F9.wireOp",EDGE,"E1248"),sQuery(id+"F9.wireOp",EDGE,"E1249"),sQuery(id+"F9.wireOp",EDGE,"E1250"),sQuery(id+"F9.wireOp",EDGE,"E1251"),sQuery(id+"F9.wireOp",EDGE,"E1252"),sQuery(id+"F9.wireOp",EDGE,"E1253"),sQuery(id+"F9.wireOp",EDGE,"E1254"),sQuery(id+"F9.wireOp",EDGE,"E1255"),sQuery(id+"F9.wireOp",EDGE,"E1256"),sQuery(id+"F9.wireOp",EDGE,"E1257"),sQuery(id+"F9.wireOp",EDGE,"E1258"),sQuery(id+"F9.wireOp",EDGE,"E1259"),sQuery(id+"F9.wireOp",EDGE,"E1260"),sQuery(id+"F9.wireOp",EDGE,"E1261"),sQuery(id+"F9.wireOp",EDGE,"E1262"),sQuery(id+"F9.wireOp",EDGE,"E1263"),sQuery(id+"F9.wireOp",EDGE,"E1264"),sQuery(id+"F9.wireOp",EDGE,"E1265"),sQuery(id+"F9.wireOp",EDGE,"E1266"),sQuery(id+"F9.wireOp",EDGE,"E1267"),sQuery(id+"F9.wireOp",EDGE,"E1268"),sQuery(id+"F9.wireOp",EDGE,"E1269"),sQuery(id+"F9.wireOp",EDGE,"E1270"),sQuery(id+"F9.wireOp",EDGE,"E1271"),sQuery(id+"F9.wireOp",EDGE,"E1272"),sQuery(id+"F9.wireOp",EDGE,"E1273"),sQuery(id+"F9.wireOp",EDGE,"E1274"),sQuery(id+"F9.wireOp",EDGE,"E1275"),sQuery(id+"F9.wireOp",EDGE,"E1276"),sQuery(id+"F9.wireOp",EDGE,"E1277"),sQuery(id+"F9.wireOp",EDGE,"E1278"),sQuery(id+"F9.wireOp",EDGE,"E1279"),sQuery(id+"F9.wireOp",EDGE,"E1280"),sQuery(id+"F9.wireOp",EDGE,"E1281"),sQuery(id+"F9.wireOp",EDGE,"E1282"),sQuery(id+"F9.wireOp",EDGE,"E1283"),sQuery(id+"F9.wireOp",EDGE,"E1284"),sQuery(id+"F9.wireOp",EDGE,"E1285"),sQuery(id+"F9.wireOp",EDGE,"E1286"),sQuery(id+"F9.wireOp",EDGE,"E1287"),sQuery(id+"F9.wireOp",EDGE,"E1288"),sQuery(id+"F9.wireOp",EDGE,"E1289"),sQuery(id+"F9.wireOp",EDGE,"E1290"),sQuery(id+"F9.wireOp",EDGE,"E1291"),sQuery(id+"F9.wireOp",EDGE,"E1292"),sQuery(id+"F9.wireOp",EDGE,"E1293"),sQuery(id+"F9.wireOp",EDGE,"E1294"),sQuery(id+"F9.wireOp",EDGE,"E1295"),sQuery(id+"F9.wireOp",EDGE,"E1296"),sQuery(id+"F9.wireOp",EDGE,"E1297"),sQuery(id+"F9.wireOp",EDGE,"E1298"),sQuery(id+"F9.wireOp",EDGE,"E1299"),sQuery(id+"F9.wireOp",EDGE,"E1300"),sQuery(id+"F9.wireOp",EDGE,"E1301"),sQuery(id+"F9.wireOp",EDGE,"E1302"),sQuery(id+"F9.wireOp",EDGE,"E1303"),sQuery(id+"F9.wireOp",EDGE,"E1304"),sQuery(id+"F9.wireOp",EDGE,"E1305"),sQuery(id+"F9.wireOp",EDGE,"E1306"),sQuery(id+"F9.wireOp",EDGE,"E1307"),sQuery(id+"F9.wireOp",EDGE,"E1308"),sQuery(id+"F9.wireOp",EDGE,"E1309"),sQuery(id+"F9.wireOp",EDGE,"E1310"),sQuery(id+"F9.wireOp",EDGE,"E1311"),sQuery(id+"F9.wireOp",EDGE,"E1312"),sQuery(id+"F9.wireOp",EDGE,"E1313"),sQuery(id+"F9.wireOp",EDGE,"E1314"),sQuery(id+"F9.wireOp",EDGE,"E1315"),sQuery(id+"F9.wireOp",EDGE,"E1316"),sQuery(id+"F9.wireOp",EDGE,"E1317"),sQuery(id+"F9.wireOp",EDGE,"E1318"),sQuery(id+"F9.wireOp",EDGE,"E1319"),sQuery(id+"F9.wireOp",EDGE,"E1320"),sQuery(id+"F9.wireOp",EDGE,"E1321"),sQuery(id+"F9.wireOp",EDGE,"E1322"),sQuery(id+"F9.wireOp",EDGE,"E1323"),sQuery(id+"F9.wireOp",EDGE,"E1324"),sQuery(id+"F9.wireOp",EDGE,"E1325"),sQuery(id+"F9.wireOp",EDGE,"E1326"),sQuery(id+"F9.wireOp",EDGE,"E1327"),sQuery(id+"F9.wireOp",EDGE,"E1328"),sQuery(id+"F9.wireOp",EDGE,"E1329"),sQuery(id+"F9.wireOp",EDGE,"E1330"),sQuery(id+"F9.wireOp",EDGE,"E1331"),sQuery(id+"F9.wireOp",EDGE,"E1332"),sQuery(id+"F9.wireOp",EDGE,"E1333"),sQuery(id+"F9.wireOp",EDGE,"E1334"),sQuery(id+"F9.wireOp",EDGE,"E1335"),sQuery(id+"F9.wireOp",EDGE,"E1336"),sQuery(id+"F9.wireOp",EDGE,"E1337"),sQuery(id+"F9.wireOp",EDGE,"E1338"),sQuery(id+"F9.wireOp",EDGE,"E1339"),sQuery(id+"F9.wireOp",EDGE,"E1340"),sQuery(id+"F9.wireOp",EDGE,"E1341"),sQuery(id+"F9.wireOp",EDGE,"E1342"),sQuery(id+"F9.wireOp",EDGE,"E1343"),sQuery(id+"F9.wireOp",EDGE,"E1344"),sQuery(id+"F9.wireOp",EDGE,"E1345"),sQuery(id+"F9.wireOp",EDGE,"E1346"),sQuery(id+"F9.wireOp",EDGE,"E1347"),sQuery(id+"F9.wireOp",EDGE,"E1348"),sQuery(id+"F9.wireOp",EDGE,"E1349"),sQuery(id+"F9.wireOp",EDGE,"E1350"),sQuery(id+"F9.wireOp",EDGE,"E1351"),sQuery(id+"F9.wireOp",EDGE,"E1352"),sQuery(id+"F9.wireOp",EDGE,"E1353"),sQuery(id+"F9.wireOp",EDGE,"E1354"),sQuery(id+"F9.wireOp",EDGE,"E1355"),sQuery(id+"F9.wireOp",EDGE,"E1356"),sQuery(id+"F9.wireOp",EDGE,"E1357"),sQuery(id+"F9.wireOp",EDGE,"E1358"),sQuery(id+"F9.wireOp",EDGE,"E1359"),sQuery(id+"F9.wireOp",EDGE,"E1360"),sQuery(id+"F9.wireOp",EDGE,"E1361"),sQuery(id+"F9.wireOp",EDGE,"E1362"),sQuery(id+"F9.wireOp",EDGE,"E1363"),sQuery(id+"F9.wireOp",EDGE,"E1364"),sQuery(id+"F9.wireOp",EDGE,"E1365"),sQuery(id+"F9.wireOp",EDGE,"E1366"),sQuery(id+"F9.wireOp",EDGE,"E1367"),sQuery(id+"F9.wireOp",EDGE,"E1368"),sQuery(id+"F9.wireOp",EDGE,"E1369"),sQuery(id+"F9.wireOp",EDGE,"E1370"),sQuery(id+"F9.wireOp",EDGE,"E1371"),sQuery(id+"F9.wireOp",EDGE,"E1372"),sQuery(id+"F9.wireOp",EDGE,"E1373"),sQuery(id+"F9.wireOp",EDGE,"E1374"),sQuery(id+"F9.wireOp",EDGE,"E1375"),sQuery(id+"F9.wireOp",EDGE,"E1376"),sQuery(id+"F9.wireOp",EDGE,"E1377"),sQuery(id+"F9.wireOp",EDGE,"E1378"),sQuery(id+"F9.wireOp",EDGE,"E1379"),sQuery(id+"F9.wireOp",EDGE,"E1380"),sQuery(id+"F9.wireOp",EDGE,"E1381"),sQuery(id+"F9.wireOp",EDGE,"E1382"),sQuery(id+"F9.wireOp",EDGE,"E1383"),sQuery(id+"F9.wireOp",EDGE,"E1384"),sQuery(id+"F9.wireOp",EDGE,"E1385"),sQuery(id+"F9.wireOp",EDGE,"E1386"),sQuery(id+"F9.wireOp",EDGE,"E1387"),sQuery(id+"F9.wireOp",EDGE,"E1388"),sQuery(id+"F9.wireOp",EDGE,"E1389"),sQuery(id+"F9.wireOp",EDGE,"E1390"),sQuery(id+"F9.wireOp",EDGE,"E1391"),sQuery(id+"F9.wireOp",EDGE,"E1392"),sQuery(id+"F9.wireOp",EDGE,"E1393"),sQuery(id+"F9.wireOp",EDGE,"E1394"),sQuery(id+"F9.wireOp",EDGE,"E1395"),sQuery(id+"F9.wireOp",EDGE,"E1396"),sQuery(id+"F9.wireOp",EDGE,"E1397"),sQuery(id+"F9.wireOp",EDGE,"E1398"),sQuery(id+"F9.wireOp",EDGE,"E1399"),sQuery(id+"F9.wireOp",EDGE,"E1400"),sQuery(id+"F9.wireOp",EDGE,"E1401"),sQuery(id+"F9.wireOp",EDGE,"E1402"),sQuery(id+"F9.wireOp",EDGE,"E1403"),sQuery(id+"F9.wireOp",EDGE,"E1404"),sQuery(id+"F9.wireOp",EDGE,"E1405"),sQuery(id+"F9.wireOp",EDGE,"E1406"),sQuery(id+"F9.wireOp",EDGE,"E1407"),sQuery(id+"F9.wireOp",EDGE,"E1408"),sQuery(id+"F9.wireOp",EDGE,"E1409"),sQuery(id+"F9.wireOp",EDGE,"E1410"),sQuery(id+"F9.wireOp",EDGE,"E1411"),sQuery(id+"F9.wireOp",EDGE,"E1412"),sQuery(id+"F9.wireOp",EDGE,"E1413"),sQuery(id+"F9.wireOp",EDGE,"E1414"),sQuery(id+"F9.wireOp",EDGE,"E1415"),sQuery(id+"F9.wireOp",EDGE,"E1416"),sQuery(id+"F9.wireOp",EDGE,"E1417"),sQuery(id+"F9.wireOp",EDGE,"E1418"),sQuery(id+"F9.wireOp",EDGE,"E1419"),sQuery(id+"F9.wireOp",EDGE,"E1420"),sQuery(id+"F9.wireOp",EDGE,"E1421"),sQuery(id+"F9.wireOp",EDGE,"E1422"),sQuery(id+"F9.wireOp",EDGE,"E1423"),sQuery(id+"F9.wireOp",EDGE,"E1424"),sQuery(id+"F9.wireOp",EDGE,"E1425"),sQuery(id+"F9.wireOp",EDGE,"E1426"),sQuery(id+"F9.wireOp",EDGE,"E1427"),sQuery(id+"F9.wireOp",EDGE,"E1428"),sQuery(id+"F9.wireOp",EDGE,"E1429"),sQuery(id+"F9.wireOp",EDGE,"E1430"),sQuery(id+"F9.wireOp",EDGE,"E1431"),sQuery(id+"F9.wireOp",EDGE,"E1432"),sQuery(id+"F9.wireOp",EDGE,"E1433"),sQuery(id+"F9.wireOp",EDGE,"E1434"),sQuery(id+"F9.wireOp",EDGE,"E1435"),sQuery(id+"F9.wireOp",EDGE,"E1436"),sQuery(id+"F9.wireOp",EDGE,"E1437"),sQuery(id+"F9.wireOp",EDGE,"E1438"),sQuery(id+"F9.wireOp",EDGE,"E1439"),sQuery(id+"F9.wireOp",EDGE,"E1440"),sQuery(id+"F9.wireOp",EDGE,"E1441"),sQuery(id+"F9.wireOp",EDGE,"E1442"),sQuery(id+"F9.wireOp",EDGE,"E1443"),sQuery(id+"F9.wireOp",EDGE,"E1444"),sQuery(id+"F9.wireOp",EDGE,"E1445"),sQuery(id+"F9.wireOp",EDGE,"E1446"),sQuery(id+"F9.wireOp",EDGE,"E1447"),sQuery(id+"F9.wireOp",EDGE,"E1448"),sQuery(id+"F9.wireOp",EDGE,"E1449"),sQuery(id+"F9.wireOp",EDGE,"E1450"),sQuery(id+"F9.wireOp",EDGE,"E1451"),sQuery(id+"F9.wireOp",EDGE,"E1452"),sQuery(id+"F9.wireOp",EDGE,"E1453"),sQuery(id+"F9.wireOp",EDGE,"E1454"),sQuery(id+"F9.wireOp",EDGE,"E1455"),sQuery(id+"F9.wireOp",EDGE,"E1456"),sQuery(id+"F9.wireOp",EDGE,"E1457"),sQuery(id+"F9.wireOp",EDGE,"E1458"),sQuery(id+"F9.wireOp",EDGE,"E1459"),sQuery(id+"F9.wireOp",EDGE,"E1460"),sQuery(id+"F9.wireOp",EDGE,"E1461"),sQuery(id+"F9.wireOp",EDGE,"E1462"),sQuery(id+"F9.wireOp",EDGE,"E1463"),sQuery(id+"F9.wireOp",EDGE,"E1464"),sQuery(id+"F9.wireOp",EDGE,"E1465"),sQuery(id+"F9.wireOp",EDGE,"E1466"),sQuery(id+"F9.wireOp",EDGE,"E1467"),sQuery(id+"F9.wireOp",EDGE,"E1468"),sQuery(id+"F9.wireOp",EDGE,"E1469"),sQuery(id+"F9.wireOp",EDGE,"E1470"),sQuery(id+"F9.wireOp",EDGE,"E1471"),sQuery(id+"F9.wireOp",EDGE,"E1472"),sQuery(id+"F9.wireOp",EDGE,"E1473"),sQuery(id+"F9.wireOp",EDGE,"E1474"),sQuery(id+"F9.wireOp",EDGE,"E1475"),sQuery(id+"F9.wireOp",EDGE,"E1476"),sQuery(id+"F9.wireOp",EDGE,"E1477"),sQuery(id+"F9.wireOp",EDGE,"E1478"),sQuery(id+"F9.wireOp",EDGE,"E1479"),sQuery(id+"F9.wireOp",EDGE,"E1480"),sQuery(id+"F9.wireOp",EDGE,"E1481"),sQuery(id+"F9.wireOp",EDGE,"E1482"),sQuery(id+"F9.wireOp",EDGE,"E1483"),sQuery(id+"F9.wireOp",EDGE,"E1484"),sQuery(id+"F9.wireOp",EDGE,"E1485"),sQuery(id+"F9.wireOp",EDGE,"E1486"),sQuery(id+"F9.wireOp",EDGE,"E1487"),sQuery(id+"F9.wireOp",EDGE,"E1488"),sQuery(id+"F9.wireOp",EDGE,"E1489"),sQuery(id+"F9.wireOp",EDGE,"E1490"),sQuery(id+"F9.wireOp",EDGE,"E1491"),sQuery(id+"F9.wireOp",EDGE,"E1492"),sQuery(id+"F9.wireOp",EDGE,"E1493"),sQuery(id+"F9.wireOp",EDGE,"E1494"),sQuery(id+"F9.wireOp",EDGE,"E1495"),sQuery(id+"F9.wireOp",EDGE,"E1496"),sQuery(id+"F9.wireOp",EDGE,"E1497"),sQuery(id+"F9.wireOp",EDGE,"E1498"),sQuery(id+"F9.wireOp",EDGE,"E1499"),sQuery(id+"F9.wireOp",EDGE,"E1500"),sQuery(id+"F9.wireOp",EDGE,"E1501"),sQuery(id+"F9.wireOp",EDGE,"E1502"),sQuery(id+"F9.wireOp",EDGE,"E1503"),sQuery(id+"F9.wireOp",EDGE,"E1504"),sQuery(id+"F9.wireOp",EDGE,"E1505"),sQuery(id+"F9.wireOp",EDGE,"E1506"),sQuery(id+"F9.wireOp",EDGE,"E1507"),sQuery(id+"F9.wireOp",EDGE,"E1508"),sQuery(id+"F9.wireOp",EDGE,"E1509"),sQuery(id+"F9.wireOp",EDGE,"E1510"),sQuery(id+"F9.wireOp",EDGE,"E1511"),sQuery(id+"F9.wireOp",EDGE,"E1512"),sQuery(id+"F9.wireOp",EDGE,"E1513"),sQuery(id+"F9.wireOp",EDGE,"E1514"),sQuery(id+"F9.wireOp",EDGE,"E1515"),sQuery(id+"F9.wireOp",EDGE,"E1516"),sQuery(id+"F9.wireOp",EDGE,"E1517"),sQuery(id+"F9.wireOp",EDGE,"E1518"),sQuery(id+"F9.wireOp",EDGE,"E1519"),sQuery(id+"F9.wireOp",EDGE,"E1520"),sQuery(id+"F9.wireOp",EDGE,"E1521"),sQuery(id+"F9.wireOp",EDGE,"E1522"),sQuery(id+"F9.wireOp",EDGE,"E1523"),sQuery(id+"F9.wireOp",EDGE,"E1524"),sQuery(id+"F9.wireOp",EDGE,"E1525"),sQuery(id+"F9.wireOp",EDGE,"E1526"),sQuery(id+"F9.wireOp",EDGE,"E1527"),sQuery(id+"F9.wireOp",EDGE,"E1528"),sQuery(id+"F9.wireOp",EDGE,"E1529"),sQuery(id+"F9.wireOp",EDGE,"E1530"),sQuery(id+"F9.wireOp",EDGE,"E1531"),sQuery(id+"F9.wireOp",EDGE,"E1532"),sQuery(id+"F9.wireOp",EDGE,"E1533"),sQuery(id+"F9.wireOp",EDGE,"E1534"),sQuery(id+"F9.wireOp",EDGE,"E1535"),sQuery(id+"F9.wireOp",EDGE,"E1536"),sQuery(id+"F9.wireOp",EDGE,"E1537"),sQuery(id+"F9.wireOp",EDGE,"E1538"),sQuery(id+"F9.wireOp",EDGE,"E1539"),sQuery(id+"F9.wireOp",EDGE,"E1540"),sQuery(id+"F9.wireOp",EDGE,"E1541"),sQuery(id+"F9.wireOp",EDGE,"E1542"),sQuery(id+"F9.wireOp",EDGE,"E1543"),sQuery(id+"F9.wireOp",EDGE,"E1544"),sQuery(id+"F9.wireOp",EDGE,"E1545"),sQuery(id+"F9.wireOp",EDGE,"E1546"),sQuery(id+"F9.wireOp",EDGE,"E1547"),sQuery(id+"F9.wireOp",EDGE,"E1548"),sQuery(id+"F9.wireOp",EDGE,"E1549"),sQuery(id+"F9.wireOp",EDGE,"E1550"),sQuery(id+"F9.wireOp",EDGE,"E1551"),sQuery(id+"F9.wireOp",EDGE,"E1552"),sQuery(id+"F9.wireOp",EDGE,"E1553"),sQuery(id+"F9.wireOp",EDGE,"E1554"),sQuery(id+"F9.wireOp",EDGE,"E1555"),sQuery(id+"F9.wireOp",EDGE,"E1556"),sQuery(id+"F9.wireOp",EDGE,"E1557"),sQuery(id+"F9.wireOp",EDGE,"E1558"),sQuery(id+"F9.wireOp",EDGE,"E1559"),sQuery(id+"F9.wireOp",EDGE,"E1560"),sQuery(id+"F9.wireOp",EDGE,"E1561"),sQuery(id+"F9.wireOp",EDGE,"E1562"),sQuery(id+"F9.wireOp",EDGE,"E1563"),sQuery(id+"F9.wireOp",EDGE,"E1564"),sQuery(id+"F9.wireOp",EDGE,"E1565"),sQuery(id+"F9.wireOp",EDGE,"E1566"),sQuery(id+"F9.wireOp",EDGE,"E1567"),sQuery(id+"F9.wireOp",EDGE,"E1568"),sQuery(id+"F9.wireOp",EDGE,"E1569"),sQuery(id+"F9.wireOp",EDGE,"E1570"),sQuery(id+"F9.wireOp",EDGE,"E1571"),sQuery(id+"F9.wireOp",EDGE,"E1572"),sQuery(id+"F9.wireOp",EDGE,"E1573"),sQuery(id+"F9.wireOp",EDGE,"E1574"),sQuery(id+"F9.wireOp",EDGE,"E1575"),sQuery(id+"F9.wireOp",EDGE,"E1576"),sQuery(id+"F9.wireOp",EDGE,"E1577"),sQuery(id+"F9.wireOp",EDGE,"E1578"),sQuery(id+"F9.wireOp",EDGE,"E1579"),sQuery(id+"F9.wireOp",EDGE,"E1580"),sQuery(id+"F9.wireOp",EDGE,"E1581"),sQuery(id+"F9.wireOp",EDGE,"E1582"),sQuery(id+"F9.wireOp",EDGE,"E1583"),sQuery(id+"F9.wireOp",EDGE,"E1584"),sQuery(id+"F9.wireOp",EDGE,"E1585"),sQuery(id+"F9.wireOp",EDGE,"E1586"),sQuery(id+"F9.wireOp",EDGE,"E1587"),sQuery(id+"F9.wireOp",EDGE,"E1588"),sQuery(id+"F9.wireOp",EDGE,"E1589"),sQuery(id+"F9.wireOp",EDGE,"E1590"),sQuery(id+"F9.wireOp",EDGE,"E1591"),sQuery(id+"F9.wireOp",EDGE,"E1592"),sQuery(id+"F9.wireOp",EDGE,"E1593"),sQuery(id+"F9.wireOp",EDGE,"E1594"),sQuery(id+"F9.wireOp",EDGE,"E1595"),sQuery(id+"F9.wireOp",EDGE,"E1596"),sQuery(id+"F9.wireOp",EDGE,"E1597"),sQuery(id+"F9.wireOp",EDGE,"E1598"),sQuery(id+"F9.wireOp",EDGE,"E1599"),sQuery(id+"F9.wireOp",EDGE,"E1600"),sQuery(id+"F9.wireOp",EDGE,"E1601"),sQuery(id+"F9.wireOp",EDGE,"E1602"),sQuery(id+"F9.wireOp",EDGE,"E1603"),sQuery(id+"F9.wireOp",EDGE,"E1604"),sQuery(id+"F9.wireOp",EDGE,"E1605"),sQuery(id+"F9.wireOp",EDGE,"E1606"),sQuery(id+"F9.wireOp",EDGE,"E1607"),sQuery(id+"F9.wireOp",EDGE,"E1608"),sQuery(id+"F9.wireOp",EDGE,"E1609"),sQuery(id+"F9.wireOp",EDGE,"E1610"),sQuery(id+"F9.wireOp",EDGE,"E1611"),sQuery(id+"F9.wireOp",EDGE,"E1612"),sQuery(id+"F9.wireOp",EDGE,"E1613"),sQuery(id+"F9.wireOp",EDGE,"E1614"),sQuery(id+"F9.wireOp",EDGE,"E1615"),sQuery(id+"F9.wireOp",EDGE,"E1616"),sQuery(id+"F9.wireOp",EDGE,"E1617"),sQuery(id+"F9.wireOp",EDGE,"E1618"),sQuery(id+"F9.wireOp",EDGE,"E1619"),sQuery(id+"F9.wireOp",EDGE,"E1620"),sQuery(id+"F9.wireOp",EDGE,"E1621"),sQuery(id+"F9.wireOp",EDGE,"E1622"),sQuery(id+"F9.wireOp",EDGE,"E1623"),sQuery(id+"F9.wireOp",EDGE,"E1624"),sQuery(id+"F9.wireOp",EDGE,"E1625"),sQuery(id+"F9.wireOp",EDGE,"E1626"),sQuery(id+"F9.wireOp",EDGE,"E1627"),sQuery(id+"F9.wireOp",EDGE,"E1628"),sQuery(id+"F9.wireOp",EDGE,"E1629"),sQuery(id+"F9.wireOp",EDGE,"E1630"),sQuery(id+"F9.wireOp",EDGE,"E1631"),sQuery(id+"F9.wireOp",EDGE,"E1632"),sQuery(id+"F9.wireOp",EDGE,"E1633"),sQuery(id+"F9.wireOp",EDGE,"E1634"),sQuery(id+"F9.wireOp",EDGE,"E1635"),sQuery(id+"F9.wireOp",EDGE,"E1636"),sQuery(id+"F9.wireOp",EDGE,"E1637"),sQuery(id+"F9.wireOp",EDGE,"E1638"),sQuery(id+"F9.wireOp",EDGE,"E1639"),sQuery(id+"F9.wireOp",EDGE,"E1640"),sQuery(id+"F9.wireOp",EDGE,"E1641"),sQuery(id+"F9.wireOp",EDGE,"E1642"),sQuery(id+"F9.wireOp",EDGE,"E1643"),sQuery(id+"F9.wireOp",EDGE,"E1644"),sQuery(id+"F9.wireOp",EDGE,"E1645"),sQuery(id+"F9.wireOp",EDGE,"E1646"),sQuery(id+"F9.wireOp",EDGE,"E1647"),sQuery(id+"F9.wireOp",EDGE,"E1648"),sQuery(id+"F9.wireOp",EDGE,"E1649"),sQuery(id+"F9.wireOp",EDGE,"E1650"),sQuery(id+"F9.wireOp",EDGE,"E1651"),sQuery(id+"F9.wireOp",EDGE,"E1652"),sQuery(id+"F9.wireOp",EDGE,"E1653"),sQuery(id+"F9.wireOp",EDGE,"E1654"),sQuery(id+"F9.wireOp",EDGE,"E1655"),sQuery(id+"F9.wireOp",EDGE,"E1656"),sQuery(id+"F9.wireOp",EDGE,"E1657"),sQuery(id+"F9.wireOp",EDGE,"E1658"),sQuery(id+"F9.wireOp",EDGE,"E1659"),sQuery(id+"F9.wireOp",EDGE,"E1660"),sQuery(id+"F9.wireOp",EDGE,"E1661"),sQuery(id+"F9.wireOp",EDGE,"E1662"),sQuery(id+"F9.wireOp",EDGE,"E1663"),sQuery(id+"F9.wireOp",EDGE,"E1664"),sQuery(id+"F9.wireOp",EDGE,"E1665"),sQuery(id+"F9.wireOp",EDGE,"E1666"),sQuery(id+"F9.wireOp",EDGE,"E1667"),sQuery(id+"F9.wireOp",EDGE,"E1668"),sQuery(id+"F9.wireOp",EDGE,"E1669"),sQuery(id+"F9.wireOp",EDGE,"E1670"),sQuery(id+"F9.wireOp",EDGE,"E1671"),sQuery(id+"F9.wireOp",EDGE,"E1672"),sQuery(id+"F9.wireOp",EDGE,"E1673"),sQuery(id+"F9.wireOp",EDGE,"E1674"),sQuery(id+"F9.wireOp",EDGE,"E1675"),sQuery(id+"F9.wireOp",EDGE,"E1676"),sQuery(id+"F9.wireOp",EDGE,"E1677"),sQuery(id+"F9.wireOp",EDGE,"E1678"),sQuery(id+"F9.wireOp",EDGE,"E1679"),sQuery(id+"F9.wireOp",EDGE,"E1680"),sQuery(id+"F9.wireOp",EDGE,"E1681"),sQuery(id+"F9.wireOp",EDGE,"E1682"),sQuery(id+"F9.wireOp",EDGE,"E1683"),sQuery(id+"F9.wireOp",EDGE,"E1684"),sQuery(id+"F9.wireOp",EDGE,"E1685"),sQuery(id+"F9.wireOp",EDGE,"E1686"),sQuery(id+"F9.wireOp",EDGE,"E1687"),sQuery(id+"F9.wireOp",EDGE,"E1688"),sQuery(id+"F9.wireOp",EDGE,"E1689"),sQuery(id+"F9.wireOp",EDGE,"E1690"),sQuery(id+"F9.wireOp",EDGE,"E1691"),sQuery(id+"F9.wireOp",EDGE,"E1692"),sQuery(id+"F9.wireOp",EDGE,"E1693"),sQuery(id+"F9.wireOp",EDGE,"E1694"),sQuery(id+"F9.wireOp",EDGE,"E1695"),sQuery(id+"F9.wireOp",EDGE,"E1696"),sQuery(id+"F9.wireOp",EDGE,"E1697"),sQuery(id+"F9.wireOp",EDGE,"E1698"),sQuery(id+"F9.wireOp",EDGE,"E1699"),sQuery(id+"F9.wireOp",EDGE,"E1700"),sQuery(id+"F9.wireOp",EDGE,"E1701"),sQuery(id+"F9.wireOp",EDGE,"E1702"),sQuery(id+"F9.wireOp",EDGE,"E1703"),sQuery(id+"F9.wireOp",EDGE,"E1704"),sQuery(id+"F9.wireOp",EDGE,"E1705"),sQuery(id+"F9.wireOp",EDGE,"E1706"),sQuery(id+"F9.wireOp",EDGE,"E1707"),sQuery(id+"F9.wireOp",EDGE,"E1708"),sQuery(id+"F9.wireOp",EDGE,"E1709"),sQuery(id+"F9.wireOp",EDGE,"E1710"),sQuery(id+"F9.wireOp",EDGE,"E1711"),sQuery(id+"F9.wireOp",EDGE,"E1712"),sQuery(id+"F9.wireOp",EDGE,"E1713"),sQuery(id+"F9.wireOp",EDGE,"E1714"),sQuery(id+"F9.wireOp",EDGE,"E1715"),sQuery(id+"F9.wireOp",EDGE,"E1716"),sQuery(id+"F9.wireOp",EDGE,"E1717"),sQuery(id+"F9.wireOp",EDGE,"E1718"),sQuery(id+"F9.wireOp",EDGE,"E1719"),sQuery(id+"F9.wireOp",EDGE,"E1720"),sQuery(id+"F9.wireOp",EDGE,"E1721"),sQuery(id+"F9.wireOp",EDGE,"E1722"),sQuery(id+"F9.wireOp",EDGE,"E1723"),sQuery(id+"F9.wireOp",EDGE,"E1724"),sQuery(id+"F9.wireOp",EDGE,"E1725"),sQuery(id+"F9.wireOp",EDGE,"E1726"),sQuery(id+"F9.wireOp",EDGE,"E1727"),sQuery(id+"F9.wireOp",EDGE,"E1728"),sQuery(id+"F9.wireOp",EDGE,"E1729"),sQuery(id+"F9.wireOp",EDGE,"E1730"),sQuery(id+"F9.wireOp",EDGE,"E1731"),sQuery(id+"F9.wireOp",EDGE,"E1732"),sQuery(id+"F9.wireOp",EDGE,"E1733"),sQuery(id+"F9.wireOp",EDGE,"E1734"),sQuery(id+"F9.wireOp",EDGE,"E1735"),sQuery(id+"F9.wireOp",EDGE,"E1736"),sQuery(id+"F9.wireOp",EDGE,"E1737"),sQuery(id+"F9.wireOp",EDGE,"E1738"),sQuery(id+"F9.wireOp",EDGE,"E1739"),sQuery(id+"F9.wireOp",EDGE,"E1740"),sQuery(id+"F9.wireOp",EDGE,"E1741"),sQuery(id+"F9.wireOp",EDGE,"E1742"),sQuery(id+"F9.wireOp",EDGE,"E1743"),sQuery(id+"F9.wireOp",EDGE,"E1744"),sQuery(id+"F9.wireOp",EDGE,"E1745"),sQuery(id+"F9.wireOp",EDGE,"E1746"),sQuery(id+"F9.wireOp",EDGE,"E1747"),sQuery(id+"F9.wireOp",EDGE,"E1748"),sQuery(id+"F9.wireOp",EDGE,"E1749"),sQuery(id+"F9.wireOp",EDGE,"E1750"),sQuery(id+"F9.wireOp",EDGE,"E1751"),sQuery(id+"F9.wireOp",EDGE,"E1752"),sQuery(id+"F9.wireOp",EDGE,"E1753"),sQuery(id+"F9.wireOp",EDGE,"E1754"),sQuery(id+"F9.wireOp",EDGE,"E1755"),sQuery(id+"F9.wireOp",EDGE,"E1756"),sQuery(id+"F9.wireOp",EDGE,"E1757"),sQuery(id+"F9.wireOp",EDGE,"E1758"),sQuery(id+"F9.wireOp",EDGE,"E1759"),sQuery(id+"F9.wireOp",EDGE,"E1760"),sQuery(id+"F9.wireOp",EDGE,"E1761"),sQuery(id+"F9.wireOp",EDGE,"E1762"),sQuery(id+"F9.wireOp",EDGE,"E1763"),sQuery(id+"F9.wireOp",EDGE,"E1764"),sQuery(id+"F9.wireOp",EDGE,"E1765"),sQuery(id+"F9.wireOp",EDGE,"E1766"),sQuery(id+"F9.wireOp",EDGE,"E1767"),sQuery(id+"F9.wireOp",EDGE,"E1768"),sQuery(id+"F9.wireOp",EDGE,"E1769"),sQuery(id+"F9.wireOp",EDGE,"E1770"),sQuery(id+"F9.wireOp",EDGE,"E1771"),sQuery(id+"F9.wireOp",EDGE,"E1772"),sQuery(id+"F9.wireOp",EDGE,"E1773"),sQuery(id+"F9.wireOp",EDGE,"E1774"),sQuery(id+"F9.wireOp",EDGE,"E1775"),sQuery(id+"F9.wireOp",EDGE,"E1776"),sQuery(id+"F9.wireOp",EDGE,"E1777"),sQuery(id+"F9.wireOp",EDGE,"E1778"),sQuery(id+"F9.wireOp",EDGE,"E1779"),sQuery(id+"F9.wireOp",EDGE,"E1780"),sQuery(id+"F9.wireOp",EDGE,"E1781"),sQuery(id+"F9.wireOp",EDGE,"E1782"),sQuery(id+"F9.wireOp",EDGE,"E1783"),sQuery(id+"F9.wireOp",EDGE,"E1784"),sQuery(id+"F9.wireOp",EDGE,"E1785"),sQuery(id+"F9.wireOp",EDGE,"E1786"),sQuery(id+"F9.wireOp",EDGE,"E1787"),sQuery(id+"F9.wireOp",EDGE,"E1788"),sQuery(id+"F9.wireOp",EDGE,"E1789"),sQuery(id+"F9.wireOp",EDGE,"E1790"),sQuery(id+"F9.wireOp",EDGE,"E1791"),sQuery(id+"F9.wireOp",EDGE,"E1792"),sQuery(id+"F9.wireOp",EDGE,"E1793"),sQuery(id+"F9.wireOp",EDGE,"E1794"),sQuery(id+"F9.wireOp",EDGE,"E1795"),sQuery(id+"F9.wireOp",EDGE,"E1796"),sQuery(id+"F9.wireOp",EDGE,"E1797"),sQuery(id+"F9.wireOp",EDGE,"E1798"),sQuery(id+"F9.wireOp",EDGE,"E1799"),sQuery(id+"F9.wireOp",EDGE,"E1800"),sQuery(id+"F9.wireOp",EDGE,"E1801"),sQuery(id+"F9.wireOp",EDGE,"E1802"),sQuery(id+"F9.wireOp",EDGE,"E1803"),sQuery(id+"F9.wireOp",EDGE,"E1804"),sQuery(id+"F9.wireOp",EDGE,"E1805"),sQuery(id+"F9.wireOp",EDGE,"E1806"),sQuery(id+"F9.wireOp",EDGE,"E1807"),sQuery(id+"F9.wireOp",EDGE,"E1808"),sQuery(id+"F9.wireOp",EDGE,"E1809"),sQuery(id+"F9.wireOp",EDGE,"E1810"),sQuery(id+"F9.wireOp",EDGE,"E1811"),sQuery(id+"F9.wireOp",EDGE,"E1812"),sQuery(id+"F9.wireOp",EDGE,"E1813"),sQuery(id+"F9.wireOp",EDGE,"E1814"),sQuery(id+"F9.wireOp",EDGE,"E1815"),sQuery(id+"F9.wireOp",EDGE,"E1816"),sQuery(id+"F9.wireOp",EDGE,"E1817"),sQuery(id+"F9.wireOp",EDGE,"E1818"),sQuery(id+"F9.wireOp",EDGE,"E1819"),sQuery(id+"F9.wireOp",EDGE,"E1820"),sQuery(id+"F9.wireOp",EDGE,"E1821"),sQuery(id+"F9.wireOp",EDGE,"E1822"),sQuery(id+"F9.wireOp",EDGE,"E1823"),sQuery(id+"F9.wireOp",EDGE,"E1824"),sQuery(id+"F9.wireOp",EDGE,"E1825"),sQuery(id+"F9.wireOp",EDGE,"E1826"),sQuery(id+"F9.wireOp",EDGE,"E1827"),sQuery(id+"F9.wireOp",EDGE,"E1828"),sQuery(id+"F9.wireOp",EDGE,"E1829"),sQuery(id+"F9.wireOp",EDGE,"E1830"),sQuery(id+"F9.wireOp",EDGE,"E1831"),sQuery(id+"F9.wireOp",EDGE,"E1832"),sQuery(id+"F9.wireOp",EDGE,"E1833"),sQuery(id+"F9.wireOp",EDGE,"E1834"),sQuery(id+"F9.wireOp",EDGE,"E1835"),sQuery(id+"F9.wireOp",EDGE,"E1836"),sQuery(id+"F9.wireOp",EDGE,"E1837"),sQuery(id+"F9.wireOp",EDGE,"E1838"),sQuery(id+"F9.wireOp",EDGE,"E1839"),sQuery(id+"F9.wireOp",EDGE,"E1840"),sQuery(id+"F9.wireOp",EDGE,"E1841"),sQuery(id+"F9.wireOp",EDGE,"E1842"),sQuery(id+"F9.wireOp",EDGE,"E1843"),sQuery(id+"F9.wireOp",EDGE,"E1844"),sQuery(id+"F9.wireOp",EDGE,"E1845"),sQuery(id+"F9.wireOp",EDGE,"E1846"),sQuery(id+"F9.wireOp",EDGE,"E1847"),sQuery(id+"F9.wireOp",EDGE,"E1848"),sQuery(id+"F9.wireOp",EDGE,"E1849"),sQuery(id+"F9.wireOp",EDGE,"E1850"),sQuery(id+"F9.wireOp",EDGE,"E1851"),sQuery(id+"F9.wireOp",EDGE,"E1852"),sQuery(id+"F9.wireOp",EDGE,"E1853"),sQuery(id+"F9.wireOp",EDGE,"E1854"),sQuery(id+"F9.wireOp",EDGE,"E1855"),sQuery(id+"F9.wireOp",EDGE,"E1856"),sQuery(id+"F9.wireOp",EDGE,"E1857"),sQuery(id+"F9.wireOp",EDGE,"E1858"),sQuery(id+"F9.wireOp",EDGE,"E1859"),sQuery(id+"F9.wireOp",EDGE,"E1860"),sQuery(id+"F9.wireOp",EDGE,"E1861"),sQuery(id+"F9.wireOp",EDGE,"E1862"),sQuery(id+"F9.wireOp",EDGE,"E1863"),sQuery(id+"F9.wireOp",EDGE,"E1864"),sQuery(id+"F9.wireOp",EDGE,"E1865"),sQuery(id+"F9.wireOp",EDGE,"E1866"),sQuery(id+"F9.wireOp",EDGE,"E1867"),sQuery(id+"F9.wireOp",EDGE,"E1868"),sQuery(id+"F9.wireOp",EDGE,"E1869"),sQuery(id+"F9.wireOp",EDGE,"E1870"),sQuery(id+"F9.wireOp",EDGE,"E1871"),sQuery(id+"F9.wireOp",EDGE,"E1872"),sQuery(id+"F9.wireOp",EDGE,"E1873"),sQuery(id+"F9.wireOp",EDGE,"E1874"),sQuery(id+"F9.wireOp",EDGE,"E1875"),sQuery(id+"F9.wireOp",EDGE,"E1876"),sQuery(id+"F9.wireOp",EDGE,"E1877"),sQuery(id+"F9.wireOp",EDGE,"E1878"),sQuery(id+"F9.wireOp",EDGE,"E1879"),sQuery(id+"F9.wireOp",EDGE,"E1880"),sQuery(id+"F9.wireOp",EDGE,"E1881"),sQuery(id+"F9.wireOp",EDGE,"E1882"),sQuery(id+"F9.wireOp",EDGE,"E1883"),sQuery(id+"F9.wireOp",EDGE,"E1884"),sQuery(id+"F9.wireOp",EDGE,"E1885"),sQuery(id+"F9.wireOp",EDGE,"E1886"),sQuery(id+"F9.wireOp",EDGE,"E1887"),sQuery(id+"F9.wireOp",EDGE,"E1888"),sQuery(id+"F9.wireOp",EDGE,"E1889"),sQuery(id+"F9.wireOp",EDGE,"E1890"),sQuery(id+"F9.wireOp",EDGE,"E1891"),sQuery(id+"F9.wireOp",EDGE,"E1892"),sQuery(id+"F9.wireOp",EDGE,"E1893"),sQuery(id+"F9.wireOp",EDGE,"E1894"),sQuery(id+"F9.wireOp",EDGE,"E1895"),sQuery(id+"F9.wireOp",EDGE,"E1896"),sQuery(id+"F9.wireOp",EDGE,"E1897"),sQuery(id+"F9.wireOp",EDGE,"E1898"),sQuery(id+"F9.wireOp",EDGE,"E1899"),sQuery(id+"F9.wireOp",EDGE,"E1900"),sQuery(id+"F9.wireOp",EDGE,"E1901"),sQuery(id+"F9.wireOp",EDGE,"E1902"),sQuery(id+"F9.wireOp",EDGE,"E1903"),sQuery(id+"F9.wireOp",EDGE,"E1904"),sQuery(id+"F9.wireOp",EDGE,"E1905"),sQuery(id+"F9.wireOp",EDGE,"E1906"),sQuery(id+"F9.wireOp",EDGE,"E1907"),sQuery(id+"F9.wireOp",EDGE,"E1908"),sQuery(id+"F9.wireOp",EDGE,"E1909"),sQuery(id+"F9.wireOp",EDGE,"E1910"),sQuery(id+"F9.wireOp",EDGE,"E1911"),sQuery(id+"F9.wireOp",EDGE,"E1912"),sQuery(id+"F9.wireOp",EDGE,"E1913"),sQuery(id+"F9.wireOp",EDGE,"E1914"),sQuery(id+"F9.wireOp",EDGE,"E1915"),sQuery(id+"F9.wireOp",EDGE,"E1916"),sQuery(id+"F9.wireOp",EDGE,"E1917"),sQuery(id+"F9.wireOp",EDGE,"E1918"),sQuery(id+"F9.wireOp",EDGE,"E1919"),sQuery(id+"F9.wireOp",EDGE,"E1920"),sQuery(id+"F9.wireOp",EDGE,"E1921"),sQuery(id+"F9.wireOp",EDGE,"E1922"),sQuery(id+"F9.wireOp",EDGE,"E1923"),sQuery(id+"F9.wireOp",EDGE,"E1924"),sQuery(id+"F9.wireOp",EDGE,"E1925"),sQuery(id+"F9.wireOp",EDGE,"E1926"),sQuery(id+"F9.wireOp",EDGE,"E1927"),sQuery(id+"F9.wireOp",EDGE,"E1928"),sQuery(id+"F9.wireOp",EDGE,"E1929"),sQuery(id+"F9.wireOp",EDGE,"E1930"),sQuery(id+"F9.wireOp",EDGE,"E1931"),sQuery(id+"F9.wireOp",EDGE,"E1932"),sQuery(id+"F9.wireOp",EDGE,"E1933"),sQuery(id+"F9.wireOp",EDGE,"E1934"),sQuery(id+"F9.wireOp",EDGE,"E1935"),sQuery(id+"F9.wireOp",EDGE,"E1936"),sQuery(id+"F9.wireOp",EDGE,"E1937"),sQuery(id+"F9.wireOp",EDGE,"E1938"),sQuery(id+"F9.wireOp",EDGE,"E1939"),sQuery(id+"F9.wireOp",EDGE,"E1940"),sQuery(id+"F9.wireOp",EDGE,"E1941"),sQuery(id+"F9.wireOp",EDGE,"E1942"),sQuery(id+"F9.wireOp",EDGE,"E1943"),sQuery(id+"F9.wireOp",EDGE,"E1944"),sQuery(id+"F9.wireOp",EDGE,"E1945"),sQuery(id+"F9.wireOp",EDGE,"E1946"),sQuery(id+"F9.wireOp",EDGE,"E1947"),sQuery(id+"F9.wireOp",EDGE,"E1948"),sQuery(id+"F9.wireOp",EDGE,"E1949"),sQuery(id+"F9.wireOp",EDGE,"E1950"),sQuery(id+"F9.wireOp",EDGE,"E1951"),sQuery(id+"F9.wireOp",EDGE,"E1952"),sQuery(id+"F9.wireOp",EDGE,"E1953"),sQuery(id+"F9.wireOp",EDGE,"E1954"),sQuery(id+"F9.wireOp",EDGE,"E1955"),sQuery(id+"F9.wireOp",EDGE,"E1956"),sQuery(id+"F9.wireOp",EDGE,"E1957"),sQuery(id+"F9.wireOp",EDGE,"E1958"),sQuery(id+"F9.wireOp",EDGE,"E1959"),sQuery(id+"F9.wireOp",EDGE,"E1960"),sQuery(id+"F9.wireOp",EDGE,"E1961"),sQuery(id+"F9.wireOp",EDGE,"E1962"),sQuery(id+"F9.wireOp",EDGE,"E1963"),sQuery(id+"F9.wireOp",EDGE,"E1964"),sQuery(id+"F9.wireOp",EDGE,"E1965"),sQuery(id+"F9.wireOp",EDGE,"E1966"),sQuery(id+"F9.wireOp",EDGE,"E1967"),sQuery(id+"F9.wireOp",EDGE,"E1968"),sQuery(id+"F9.wireOp",EDGE,"E1969"),sQuery(id+"F9.wireOp",EDGE,"E1970"),sQuery(id+"F9.wireOp",EDGE,"E1971"),sQuery(id+"F9.wireOp",EDGE,"E1972"),sQuery(id+"F9.wireOp",EDGE,"E1973"),sQuery(id+"F9.wireOp",EDGE,"E1974"),sQuery(id+"F9.wireOp",EDGE,"E1975"),sQuery(id+"F9.wireOp",EDGE,"E1976"),sQuery(id+"F9.wireOp",EDGE,"E1977"),sQuery(id+"F9.wireOp",EDGE,"E1978"),sQuery(id+"F9.wireOp",EDGE,"E1979"),sQuery(id+"F9.wireOp",EDGE,"E1980"),sQuery(id+"F9.wireOp",EDGE,"E1981"),sQuery(id+"F9.wireOp",EDGE,"E1982"),sQuery(id+"F9.wireOp",EDGE,"E1983"),sQuery(id+"F9.wireOp",EDGE,"E1984"),sQuery(id+"F9.wireOp",EDGE,"E1985"),sQuery(id+"F9.wireOp",EDGE,"E1986"),sQuery(id+"F9.wireOp",EDGE,"E1987"),sQuery(id+"F9.wireOp",EDGE,"E1988"),sQuery(id+"F9.wireOp",EDGE,"E1989"),sQuery(id+"F9.wireOp",EDGE,"E1990"),sQuery(id+"F9.wireOp",EDGE,"E1991"),sQuery(id+"F9.wireOp",EDGE,"E1992"),sQuery(id+"F9.wireOp",EDGE,"E1993"),sQuery(id+"F9.wireOp",EDGE,"E1994"),sQuery(id+"F9.wireOp",EDGE,"E1995")])]});
            var Q2;
            Q2=makeQuery(id+"F10.opExtrude","SWEPT_BODY",BODY,{"disambiguationData":[OSD([sQuery(id+"F9.wireOp",EDGE,"E1996"),sQuery(id+"F9.wireOp",EDGE,"E1997"),sQuery(id+"F9.wireOp",EDGE,"E1998"),sQuery(id+"F9.wireOp",EDGE,"E1999"),sQuery(id+"F9.wireOp",EDGE,"E2000"),sQuery(id+"F9.wireOp",EDGE,"E2001"),sQuery(id+"F9.wireOp",EDGE,"E2002"),sQuery(id+"F9.wireOp",EDGE,"E2003"),sQuery(id+"F9.wireOp",EDGE,"E2004"),sQuery(id+"F9.wireOp",EDGE,"E2005"),sQuery(id+"F9.wireOp",EDGE,"E2006"),sQuery(id+"F9.wireOp",EDGE,"E2007"),sQuery(id+"F9.wireOp",EDGE,"E2008"),sQuery(id+"F9.wireOp",EDGE,"E2009"),sQuery(id+"F9.wireOp",EDGE,"E2010"),sQuery(id+"F9.wireOp",EDGE,"E2011"),sQuery(id+"F9.wireOp",EDGE,"E2012"),sQuery(id+"F9.wireOp",EDGE,"E2013"),sQuery(id+"F9.wireOp",EDGE,"E2014"),sQuery(id+"F9.wireOp",EDGE,"E2015"),sQuery(id+"F9.wireOp",EDGE,"E2016"),sQuery(id+"F9.wireOp",EDGE,"E2017"),sQuery(id+"F9.wireOp",EDGE,"E2018"),sQuery(id+"F9.wireOp",EDGE,"E2019"),sQuery(id+"F9.wireOp",EDGE,"E2020"),sQuery(id+"F9.wireOp",EDGE,"E2021"),sQuery(id+"F9.wireOp",EDGE,"E2022"),sQuery(id+"F9.wireOp",EDGE,"E2023"),sQuery(id+"F9.wireOp",EDGE,"E2024"),sQuery(id+"F9.wireOp",EDGE,"E2025"),sQuery(id+"F9.wireOp",EDGE,"E2026"),sQuery(id+"F9.wireOp",EDGE,"E2027"),sQuery(id+"F9.wireOp",EDGE,"E2028"),sQuery(id+"F9.wireOp",EDGE,"E2029"),sQuery(id+"F9.wireOp",EDGE,"E2030"),sQuery(id+"F9.wireOp",EDGE,"E2031"),sQuery(id+"F9.wireOp",EDGE,"E2032"),sQuery(id+"F9.wireOp",EDGE,"E2033"),sQuery(id+"F9.wireOp",EDGE,"E2034"),sQuery(id+"F9.wireOp",EDGE,"E2035"),sQuery(id+"F9.wireOp",EDGE,"E2036"),sQuery(id+"F9.wireOp",EDGE,"E2037"),sQuery(id+"F9.wireOp",EDGE,"E2038"),sQuery(id+"F9.wireOp",EDGE,"E2039"),sQuery(id+"F9.wireOp",EDGE,"E2040"),sQuery(id+"F9.wireOp",EDGE,"E2041"),sQuery(id+"F9.wireOp",EDGE,"E2042"),sQuery(id+"F9.wireOp",EDGE,"E2043"),sQuery(id+"F9.wireOp",EDGE,"E2044"),sQuery(id+"F9.wireOp",EDGE,"E2045"),sQuery(id+"F9.wireOp",EDGE,"E2046"),sQuery(id+"F9.wireOp",EDGE,"E2047"),sQuery(id+"F9.wireOp",EDGE,"E2048"),sQuery(id+"F9.wireOp",EDGE,"E2049"),sQuery(id+"F9.wireOp",EDGE,"E2050"),sQuery(id+"F9.wireOp",EDGE,"E2051"),sQuery(id+"F9.wireOp",EDGE,"E2052"),sQuery(id+"F9.wireOp",EDGE,"E2053"),sQuery(id+"F9.wireOp",EDGE,"E2054"),sQuery(id+"F9.wireOp",EDGE,"E2055"),sQuery(id+"F9.wireOp",EDGE,"E2056"),sQuery(id+"F9.wireOp",EDGE,"E2057"),sQuery(id+"F9.wireOp",EDGE,"E2058"),sQuery(id+"F9.wireOp",EDGE,"E2059"),sQuery(id+"F9.wireOp",EDGE,"E2060"),sQuery(id+"F9.wireOp",EDGE,"E2061"),sQuery(id+"F9.wireOp",EDGE,"E2062"),sQuery(id+"F9.wireOp",EDGE,"E2063"),sQuery(id+"F9.wireOp",EDGE,"E2064"),sQuery(id+"F9.wireOp",EDGE,"E2065"),sQuery(id+"F9.wireOp",EDGE,"E2066"),sQuery(id+"F9.wireOp",EDGE,"E2067"),sQuery(id+"F9.wireOp",EDGE,"E2068"),sQuery(id+"F9.wireOp",EDGE,"E2069"),sQuery(id+"F9.wireOp",EDGE,"E2070"),sQuery(id+"F9.wireOp",EDGE,"E2071"),sQuery(id+"F9.wireOp",EDGE,"E2072"),sQuery(id+"F9.wireOp",EDGE,"E2073"),sQuery(id+"F9.wireOp",EDGE,"E2074"),sQuery(id+"F9.wireOp",EDGE,"E2075"),sQuery(id+"F9.wireOp",EDGE,"E2076"),sQuery(id+"F9.wireOp",EDGE,"E2077"),sQuery(id+"F9.wireOp",EDGE,"E2078"),sQuery(id+"F9.wireOp",EDGE,"E2079"),sQuery(id+"F9.wireOp",EDGE,"E2080"),sQuery(id+"F9.wireOp",EDGE,"E2081"),sQuery(id+"F9.wireOp",EDGE,"E2082"),sQuery(id+"F9.wireOp",EDGE,"E2083"),sQuery(id+"F9.wireOp",EDGE,"E2084"),sQuery(id+"F9.wireOp",EDGE,"E2085"),sQuery(id+"F9.wireOp",EDGE,"E2086"),sQuery(id+"F9.wireOp",EDGE,"E2087"),sQuery(id+"F9.wireOp",EDGE,"E2088"),sQuery(id+"F9.wireOp",EDGE,"E2089"),sQuery(id+"F9.wireOp",EDGE,"E2090"),sQuery(id+"F9.wireOp",EDGE,"E2091"),sQuery(id+"F9.wireOp",EDGE,"E2092"),sQuery(id+"F9.wireOp",EDGE,"E2093"),sQuery(id+"F9.wireOp",EDGE,"E2094"),sQuery(id+"F9.wireOp",EDGE,"E2095"),sQuery(id+"F9.wireOp",EDGE,"E2096"),sQuery(id+"F9.wireOp",EDGE,"E2097"),sQuery(id+"F9.wireOp",EDGE,"E2098"),sQuery(id+"F9.wireOp",EDGE,"E2099"),sQuery(id+"F9.wireOp",EDGE,"E2100"),sQuery(id+"F9.wireOp",EDGE,"E2101")])]});
            var Q3;
            Q3=makeQuery(id+"F10.opExtrude","SWEPT_BODY",BODY,{"disambiguationData":[OSD([sQuery(id+"F9.wireOp",EDGE,"E2102"),sQuery(id+"F9.wireOp",EDGE,"E2103"),sQuery(id+"F9.wireOp",EDGE,"E2104"),sQuery(id+"F9.wireOp",EDGE,"E2105")])]});
            var Q4;
            Q4=makeQuery(id+"F10.opExtrude","SWEPT_BODY",BODY,{"disambiguationData":[OSD([sQuery(id+"F9.wireOp",EDGE,"E2106"),sQuery(id+"F9.wireOp",EDGE,"E2107"),sQuery(id+"F9.wireOp",EDGE,"E2108"),sQuery(id+"F9.wireOp",EDGE,"E2109")])]});
            var Q5;
            Q5=makeQuery(id+"F10.opExtrude","SWEPT_BODY",BODY,{"disambiguationData":[OSD([sQuery(id+"F9.wireOp",EDGE,"E2110"),sQuery(id+"F9.wireOp",EDGE,"E2111"),sQuery(id+"F9.wireOp",EDGE,"E2112"),sQuery(id+"F9.wireOp",EDGE,"E2113"),sQuery(id+"F9.wireOp",EDGE,"E2114"),sQuery(id+"F9.wireOp",EDGE,"E2115"),sQuery(id+"F9.wireOp",EDGE,"E2116"),sQuery(id+"F9.wireOp",EDGE,"E2117"),sQuery(id+"F9.wireOp",EDGE,"E2118"),sQuery(id+"F9.wireOp",EDGE,"E2119"),sQuery(id+"F9.wireOp",EDGE,"E2120"),sQuery(id+"F9.wireOp",EDGE,"E2121"),sQuery(id+"F9.wireOp",EDGE,"E2122"),sQuery(id+"F9.wireOp",EDGE,"E2123"),sQuery(id+"F9.wireOp",EDGE,"E2124"),sQuery(id+"F9.wireOp",EDGE,"E2125"),sQuery(id+"F9.wireOp",EDGE,"E2126"),sQuery(id+"F9.wireOp",EDGE,"E2127"),sQuery(id+"F9.wireOp",EDGE,"E2128"),sQuery(id+"F9.wireOp",EDGE,"E2129"),sQuery(id+"F9.wireOp",EDGE,"E2130"),sQuery(id+"F9.wireOp",EDGE,"E2131"),sQuery(id+"F9.wireOp",EDGE,"E2132"),sQuery(id+"F9.wireOp",EDGE,"E2133"),sQuery(id+"F9.wireOp",EDGE,"E2134"),sQuery(id+"F9.wireOp",EDGE,"E2135"),sQuery(id+"F9.wireOp",EDGE,"E2136"),sQuery(id+"F9.wireOp",EDGE,"E2137"),sQuery(id+"F9.wireOp",EDGE,"E2138"),sQuery(id+"F9.wireOp",EDGE,"E2139"),sQuery(id+"F9.wireOp",EDGE,"E2140"),sQuery(id+"F9.wireOp",EDGE,"E2141"),sQuery(id+"F9.wireOp",EDGE,"E2142"),sQuery(id+"F9.wireOp",EDGE,"E2143"),sQuery(id+"F9.wireOp",EDGE,"E2144"),sQuery(id+"F9.wireOp",EDGE,"E2145"),sQuery(id+"F9.wireOp",EDGE,"E2146"),sQuery(id+"F9.wireOp",EDGE,"E2147"),sQuery(id+"F9.wireOp",EDGE,"E2148"),sQuery(id+"F9.wireOp",EDGE,"E2149"),sQuery(id+"F9.wireOp",EDGE,"E2150"),sQuery(id+"F9.wireOp",EDGE,"E2151"),sQuery(id+"F9.wireOp",EDGE,"E2152"),sQuery(id+"F9.wireOp",EDGE,"E2153"),sQuery(id+"F9.wireOp",EDGE,"E2154"),sQuery(id+"F9.wireOp",EDGE,"E2155"),sQuery(id+"F9.wireOp",EDGE,"E2156"),sQuery(id+"F9.wireOp",EDGE,"E2157"),sQuery(id+"F9.wireOp",EDGE,"E2158"),sQuery(id+"F9.wireOp",EDGE,"E2159"),sQuery(id+"F9.wireOp",EDGE,"E2160"),sQuery(id+"F9.wireOp",EDGE,"E2161"),sQuery(id+"F9.wireOp",EDGE,"E2162"),sQuery(id+"F9.wireOp",EDGE,"E2163")])]});
            var Q6;
            Q6=makeQuery(id+"F10.opExtrude","SWEPT_BODY",BODY,{"disambiguationData":[OSD([sQuery(id+"F9.wireOp",EDGE,"E2164"),sQuery(id+"F9.wireOp",EDGE,"E2165"),sQuery(id+"F9.wireOp",EDGE,"E2166"),sQuery(id+"F9.wireOp",EDGE,"E2167"),sQuery(id+"F9.wireOp",EDGE,"E2168"),sQuery(id+"F9.wireOp",EDGE,"E2169"),sQuery(id+"F9.wireOp",EDGE,"E2170"),sQuery(id+"F9.wireOp",EDGE,"E2171"),sQuery(id+"F9.wireOp",EDGE,"E2172"),sQuery(id+"F9.wireOp",EDGE,"E2173"),sQuery(id+"F9.wireOp",EDGE,"E2174"),sQuery(id+"F9.wireOp",EDGE,"E2175"),sQuery(id+"F9.wireOp",EDGE,"E2176"),sQuery(id+"F9.wireOp",EDGE,"E2177"),sQuery(id+"F9.wireOp",EDGE,"E2178"),sQuery(id+"F9.wireOp",EDGE,"E2179"),sQuery(id+"F9.wireOp",EDGE,"E2180"),sQuery(id+"F9.wireOp",EDGE,"E2181"),sQuery(id+"F9.wireOp",EDGE,"E2182"),sQuery(id+"F9.wireOp",EDGE,"E2183"),sQuery(id+"F9.wireOp",EDGE,"E2184"),sQuery(id+"F9.wireOp",EDGE,"E2185"),sQuery(id+"F9.wireOp",EDGE,"E2186"),sQuery(id+"F9.wireOp",EDGE,"E2187"),sQuery(id+"F9.wireOp",EDGE,"E2188"),sQuery(id+"F9.wireOp",EDGE,"E2189"),sQuery(id+"F9.wireOp",EDGE,"E2190"),sQuery(id+"F9.wireOp",EDGE,"E2191"),sQuery(id+"F9.wireOp",EDGE,"E2192"),sQuery(id+"F9.wireOp",EDGE,"E2193"),sQuery(id+"F9.wireOp",EDGE,"E2194"),sQuery(id+"F9.wireOp",EDGE,"E2195"),sQuery(id+"F9.wireOp",EDGE,"E2196"),sQuery(id+"F9.wireOp",EDGE,"E2197"),sQuery(id+"F9.wireOp",EDGE,"E2198"),sQuery(id+"F9.wireOp",EDGE,"E2199"),sQuery(id+"F9.wireOp",EDGE,"E2200"),sQuery(id+"F9.wireOp",EDGE,"E2201"),sQuery(id+"F9.wireOp",EDGE,"E2202"),sQuery(id+"F9.wireOp",EDGE,"E2203"),sQuery(id+"F9.wireOp",EDGE,"E2204"),sQuery(id+"F9.wireOp",EDGE,"E2205"),sQuery(id+"F9.wireOp",EDGE,"E2206"),sQuery(id+"F9.wireOp",EDGE,"E2207"),sQuery(id+"F9.wireOp",EDGE,"E2208"),sQuery(id+"F9.wireOp",EDGE,"E2209"),sQuery(id+"F9.wireOp",EDGE,"E2210"),sQuery(id+"F9.wireOp",EDGE,"E2211"),sQuery(id+"F9.wireOp",EDGE,"E2212"),sQuery(id+"F9.wireOp",EDGE,"E2213"),sQuery(id+"F9.wireOp",EDGE,"E2214"),sQuery(id+"F9.wireOp",EDGE,"E2215"),sQuery(id+"F9.wireOp",EDGE,"E2216"),sQuery(id+"F9.wireOp",EDGE,"E2217"),sQuery(id+"F9.wireOp",EDGE,"E2218"),sQuery(id+"F9.wireOp",EDGE,"E2219"),sQuery(id+"F9.wireOp",EDGE,"E2220"),sQuery(id+"F9.wireOp",EDGE,"E2221"),sQuery(id+"F9.wireOp",EDGE,"E2222"),sQuery(id+"F9.wireOp",EDGE,"E2223"),sQuery(id+"F9.wireOp",EDGE,"E2224"),sQuery(id+"F9.wireOp",EDGE,"E2225"),sQuery(id+"F9.wireOp",EDGE,"E2226"),sQuery(id+"F9.wireOp",EDGE,"E2227"),sQuery(id+"F9.wireOp",EDGE,"E2228"),sQuery(id+"F9.wireOp",EDGE,"E2229"),sQuery(id+"F9.wireOp",EDGE,"E2230"),sQuery(id+"F9.wireOp",EDGE,"E2231"),sQuery(id+"F9.wireOp",EDGE,"E2232"),sQuery(id+"F9.wireOp",EDGE,"E2233"),sQuery(id+"F9.wireOp",EDGE,"E2234"),sQuery(id+"F9.wireOp",EDGE,"E2235"),sQuery(id+"F9.wireOp",EDGE,"E2236"),sQuery(id+"F9.wireOp",EDGE,"E2237"),sQuery(id+"F9.wireOp",EDGE,"E2238"),sQuery(id+"F9.wireOp",EDGE,"E2239"),sQuery(id+"F9.wireOp",EDGE,"E2240"),sQuery(id+"F9.wireOp",EDGE,"E2241"),sQuery(id+"F9.wireOp",EDGE,"E2242"),sQuery(id+"F9.wireOp",EDGE,"E2243"),sQuery(id+"F9.wireOp",EDGE,"E2244"),sQuery(id+"F9.wireOp",EDGE,"E2245"),sQuery(id+"F9.wireOp",EDGE,"E2246"),sQuery(id+"F9.wireOp",EDGE,"E2247"),sQuery(id+"F9.wireOp",EDGE,"E2248"),sQuery(id+"F9.wireOp",EDGE,"E2249"),sQuery(id+"F9.wireOp",EDGE,"E2250"),sQuery(id+"F9.wireOp",EDGE,"E2251"),sQuery(id+"F9.wireOp",EDGE,"E2252"),sQuery(id+"F9.wireOp",EDGE,"E2253"),sQuery(id+"F9.wireOp",EDGE,"E2254"),sQuery(id+"F9.wireOp",EDGE,"E2255"),sQuery(id+"F9.wireOp",EDGE,"E2256"),sQuery(id+"F9.wireOp",EDGE,"E2257"),sQuery(id+"F9.wireOp",EDGE,"E2258"),sQuery(id+"F9.wireOp",EDGE,"E2259"),sQuery(id+"F9.wireOp",EDGE,"E2260"),sQuery(id+"F9.wireOp",EDGE,"E2261"),sQuery(id+"F9.wireOp",EDGE,"E2262"),sQuery(id+"F9.wireOp",EDGE,"E2263"),sQuery(id+"F9.wireOp",EDGE,"E2264"),sQuery(id+"F9.wireOp",EDGE,"E2265"),sQuery(id+"F9.wireOp",EDGE,"E2266"),sQuery(id+"F9.wireOp",EDGE,"E2267"),sQuery(id+"F9.wireOp",EDGE,"E2268"),sQuery(id+"F9.wireOp",EDGE,"E2269"),sQuery(id+"F9.wireOp",EDGE,"E2270"),sQuery(id+"F9.wireOp",EDGE,"E2271"),sQuery(id+"F9.wireOp",EDGE,"E2272"),sQuery(id+"F9.wireOp",EDGE,"E2273"),sQuery(id+"F9.wireOp",EDGE,"E2274"),sQuery(id+"F9.wireOp",EDGE,"E2275"),sQuery(id+"F9.wireOp",EDGE,"E2276"),sQuery(id+"F9.wireOp",EDGE,"E2277"),sQuery(id+"F9.wireOp",EDGE,"E2278"),sQuery(id+"F9.wireOp",EDGE,"E2279"),sQuery(id+"F9.wireOp",EDGE,"E2280"),sQuery(id+"F9.wireOp",EDGE,"E2281"),sQuery(id+"F9.wireOp",EDGE,"E2282"),sQuery(id+"F9.wireOp",EDGE,"E2283"),sQuery(id+"F9.wireOp",EDGE,"E2284"),sQuery(id+"F9.wireOp",EDGE,"E2285"),sQuery(id+"F9.wireOp",EDGE,"E2286"),sQuery(id+"F9.wireOp",EDGE,"E2287"),sQuery(id+"F9.wireOp",EDGE,"E2288"),sQuery(id+"F9.wireOp",EDGE,"E2289"),sQuery(id+"F9.wireOp",EDGE,"E2290"),sQuery(id+"F9.wireOp",EDGE,"E2291"),sQuery(id+"F9.wireOp",EDGE,"E2292"),sQuery(id+"F9.wireOp",EDGE,"E2293"),sQuery(id+"F9.wireOp",EDGE,"E2294"),sQuery(id+"F9.wireOp",EDGE,"E2295"),sQuery(id+"F9.wireOp",EDGE,"E2296"),sQuery(id+"F9.wireOp",EDGE,"E2297"),sQuery(id+"F9.wireOp",EDGE,"E2298"),sQuery(id+"F9.wireOp",EDGE,"E2299"),sQuery(id+"F9.wireOp",EDGE,"E2300"),sQuery(id+"F9.wireOp",EDGE,"E2301"),sQuery(id+"F9.wireOp",EDGE,"E2302"),sQuery(id+"F9.wireOp",EDGE,"E2303"),sQuery(id+"F9.wireOp",EDGE,"E2304"),sQuery(id+"F9.wireOp",EDGE,"E2305"),sQuery(id+"F9.wireOp",EDGE,"E2306"),sQuery(id+"F9.wireOp",EDGE,"E2307"),sQuery(id+"F9.wireOp",EDGE,"E2308"),sQuery(id+"F9.wireOp",EDGE,"E2309"),sQuery(id+"F9.wireOp",EDGE,"E2310"),sQuery(id+"F9.wireOp",EDGE,"E2311"),sQuery(id+"F9.wireOp",EDGE,"E2312"),sQuery(id+"F9.wireOp",EDGE,"E2313"),sQuery(id+"F9.wireOp",EDGE,"E2314"),sQuery(id+"F9.wireOp",EDGE,"E2315"),sQuery(id+"F9.wireOp",EDGE,"E2316"),sQuery(id+"F9.wireOp",EDGE,"E2317"),sQuery(id+"F9.wireOp",EDGE,"E2318"),sQuery(id+"F9.wireOp",EDGE,"E2319"),sQuery(id+"F9.wireOp",EDGE,"E2320"),sQuery(id+"F9.wireOp",EDGE,"E2321"),sQuery(id+"F9.wireOp",EDGE,"E2322"),sQuery(id+"F9.wireOp",EDGE,"E2323"),sQuery(id+"F9.wireOp",EDGE,"E2324"),sQuery(id+"F9.wireOp",EDGE,"E2325"),sQuery(id+"F9.wireOp",EDGE,"E2326"),sQuery(id+"F9.wireOp",EDGE,"E2327"),sQuery(id+"F9.wireOp",EDGE,"E2328"),sQuery(id+"F9.wireOp",EDGE,"E2329"),sQuery(id+"F9.wireOp",EDGE,"E2330"),sQuery(id+"F9.wireOp",EDGE,"E2331"),sQuery(id+"F9.wireOp",EDGE,"E2332"),sQuery(id+"F9.wireOp",EDGE,"E2333"),sQuery(id+"F9.wireOp",EDGE,"E2334"),sQuery(id+"F9.wireOp",EDGE,"E2335"),sQuery(id+"F9.wireOp",EDGE,"E2336"),sQuery(id+"F9.wireOp",EDGE,"E2337"),sQuery(id+"F9.wireOp",EDGE,"E2338"),sQuery(id+"F9.wireOp",EDGE,"E2339"),sQuery(id+"F9.wireOp",EDGE,"E2340"),sQuery(id+"F9.wireOp",EDGE,"E2341"),sQuery(id+"F9.wireOp",EDGE,"E2342"),sQuery(id+"F9.wireOp",EDGE,"E2343"),sQuery(id+"F9.wireOp",EDGE,"E2344"),sQuery(id+"F9.wireOp",EDGE,"E2345"),sQuery(id+"F9.wireOp",EDGE,"E2346"),sQuery(id+"F9.wireOp",EDGE,"E2347"),sQuery(id+"F9.wireOp",EDGE,"E2348"),sQuery(id+"F9.wireOp",EDGE,"E2349"),sQuery(id+"F9.wireOp",EDGE,"E2350"),sQuery(id+"F9.wireOp",EDGE,"E2351"),sQuery(id+"F9.wireOp",EDGE,"E2352"),sQuery(id+"F9.wireOp",EDGE,"E2353"),sQuery(id+"F9.wireOp",EDGE,"E2354"),sQuery(id+"F9.wireOp",EDGE,"E2355"),sQuery(id+"F9.wireOp",EDGE,"E2356"),sQuery(id+"F9.wireOp",EDGE,"E2357"),sQuery(id+"F9.wireOp",EDGE,"E2358"),sQuery(id+"F9.wireOp",EDGE,"E2359"),sQuery(id+"F9.wireOp",EDGE,"E2360"),sQuery(id+"F9.wireOp",EDGE,"E2361"),sQuery(id+"F9.wireOp",EDGE,"E2362"),sQuery(id+"F9.wireOp",EDGE,"E2363"),sQuery(id+"F9.wireOp",EDGE,"E2364"),sQuery(id+"F9.wireOp",EDGE,"E2365"),sQuery(id+"F9.wireOp",EDGE,"E2366"),sQuery(id+"F9.wireOp",EDGE,"E2367"),sQuery(id+"F9.wireOp",EDGE,"E2368"),sQuery(id+"F9.wireOp",EDGE,"E2369"),sQuery(id+"F9.wireOp",EDGE,"E2370"),sQuery(id+"F9.wireOp",EDGE,"E2371"),sQuery(id+"F9.wireOp",EDGE,"E2372"),sQuery(id+"F9.wireOp",EDGE,"E2373"),sQuery(id+"F9.wireOp",EDGE,"E2374"),sQuery(id+"F9.wireOp",EDGE,"E2375"),sQuery(id+"F9.wireOp",EDGE,"E2376"),sQuery(id+"F9.wireOp",EDGE,"E2377"),sQuery(id+"F9.wireOp",EDGE,"E2378"),sQuery(id+"F9.wireOp",EDGE,"E2379"),sQuery(id+"F9.wireOp",EDGE,"E2380"),sQuery(id+"F9.wireOp",EDGE,"E2381"),sQuery(id+"F9.wireOp",EDGE,"E2382"),sQuery(id+"F9.wireOp",EDGE,"E2383"),sQuery(id+"F9.wireOp",EDGE,"E2384"),sQuery(id+"F9.wireOp",EDGE,"E2385"),sQuery(id+"F9.wireOp",EDGE,"E2386"),sQuery(id+"F9.wireOp",EDGE,"E2387"),sQuery(id+"F9.wireOp",EDGE,"E2388"),sQuery(id+"F9.wireOp",EDGE,"E2389"),sQuery(id+"F9.wireOp",EDGE,"E2390"),sQuery(id+"F9.wireOp",EDGE,"E2391"),sQuery(id+"F9.wireOp",EDGE,"E2392"),sQuery(id+"F9.wireOp",EDGE,"E2393"),sQuery(id+"F9.wireOp",EDGE,"E2394"),sQuery(id+"F9.wireOp",EDGE,"E2395"),sQuery(id+"F9.wireOp",EDGE,"E2396"),sQuery(id+"F9.wireOp",EDGE,"E2397")])]});
            var Q7;
            Q7=makeQuery(id+"F10.opExtrude","SWEPT_BODY",BODY,{"disambiguationData":[OSD([sQuery(id+"F9.wireOp",EDGE,"E2398"),sQuery(id+"F9.wireOp",EDGE,"E2399"),sQuery(id+"F9.wireOp",EDGE,"E2400"),sQuery(id+"F9.wireOp",EDGE,"E2401")])]});
            var Q8;
            Q8=makeQuery(id+"F10.opExtrude","SWEPT_BODY",BODY,{"disambiguationData":[OSD([sQuery(id+"F9.wireOp",EDGE,"E2402"),sQuery(id+"F9.wireOp",EDGE,"E2403"),sQuery(id+"F9.wireOp",EDGE,"E2404"),sQuery(id+"F9.wireOp",EDGE,"E2405"),sQuery(id+"F9.wireOp",EDGE,"E2406"),sQuery(id+"F9.wireOp",EDGE,"E2407"),sQuery(id+"F9.wireOp",EDGE,"E2408"),sQuery(id+"F9.wireOp",EDGE,"E2409"),sQuery(id+"F9.wireOp",EDGE,"E2410"),sQuery(id+"F9.wireOp",EDGE,"E2411"),sQuery(id+"F9.wireOp",EDGE,"E2412"),sQuery(id+"F9.wireOp",EDGE,"E2413"),sQuery(id+"F9.wireOp",EDGE,"E2414"),sQuery(id+"F9.wireOp",EDGE,"E2415"),sQuery(id+"F9.wireOp",EDGE,"E2416"),sQuery(id+"F9.wireOp",EDGE,"E2417"),sQuery(id+"F9.wireOp",EDGE,"E2418"),sQuery(id+"F9.wireOp",EDGE,"E2419"),sQuery(id+"F9.wireOp",EDGE,"E2420"),sQuery(id+"F9.wireOp",EDGE,"E2421"),sQuery(id+"F9.wireOp",EDGE,"E2422"),sQuery(id+"F9.wireOp",EDGE,"E2423"),sQuery(id+"F9.wireOp",EDGE,"E2424"),sQuery(id+"F9.wireOp",EDGE,"E2425"),sQuery(id+"F9.wireOp",EDGE,"E2426"),sQuery(id+"F9.wireOp",EDGE,"E2427"),sQuery(id+"F9.wireOp",EDGE,"E2428"),sQuery(id+"F9.wireOp",EDGE,"E2429"),sQuery(id+"F9.wireOp",EDGE,"E2430"),sQuery(id+"F9.wireOp",EDGE,"E2431"),sQuery(id+"F9.wireOp",EDGE,"E2432"),sQuery(id+"F9.wireOp",EDGE,"E2433"),sQuery(id+"F9.wireOp",EDGE,"E2434"),sQuery(id+"F9.wireOp",EDGE,"E2435"),sQuery(id+"F9.wireOp",EDGE,"E2436"),sQuery(id+"F9.wireOp",EDGE,"E2437"),sQuery(id+"F9.wireOp",EDGE,"E2438"),sQuery(id+"F9.wireOp",EDGE,"E2439"),sQuery(id+"F9.wireOp",EDGE,"E2440"),sQuery(id+"F9.wireOp",EDGE,"E2441"),sQuery(id+"F9.wireOp",EDGE,"E2442"),sQuery(id+"F9.wireOp",EDGE,"E2443"),sQuery(id+"F9.wireOp",EDGE,"E2444"),sQuery(id+"F9.wireOp",EDGE,"E2445"),sQuery(id+"F9.wireOp",EDGE,"E2446"),sQuery(id+"F9.wireOp",EDGE,"E2447"),sQuery(id+"F9.wireOp",EDGE,"E2448"),sQuery(id+"F9.wireOp",EDGE,"E2449"),sQuery(id+"F9.wireOp",EDGE,"E2450"),sQuery(id+"F9.wireOp",EDGE,"E2451"),sQuery(id+"F9.wireOp",EDGE,"E2452"),sQuery(id+"F9.wireOp",EDGE,"E2453"),sQuery(id+"F9.wireOp",EDGE,"E2454"),sQuery(id+"F9.wireOp",EDGE,"E2455"),sQuery(id+"F9.wireOp",EDGE,"E2456"),sQuery(id+"F9.wireOp",EDGE,"E2457"),sQuery(id+"F9.wireOp",EDGE,"E2458"),sQuery(id+"F9.wireOp",EDGE,"E2459"),sQuery(id+"F9.wireOp",EDGE,"E2460"),sQuery(id+"F9.wireOp",EDGE,"E2461"),sQuery(id+"F9.wireOp",EDGE,"E2462"),sQuery(id+"F9.wireOp",EDGE,"E2463"),sQuery(id+"F9.wireOp",EDGE,"E2464"),sQuery(id+"F9.wireOp",EDGE,"E2465"),sQuery(id+"F9.wireOp",EDGE,"E2466"),sQuery(id+"F9.wireOp",EDGE,"E2467"),sQuery(id+"F9.wireOp",EDGE,"E2468"),sQuery(id+"F9.wireOp",EDGE,"E2469"),sQuery(id+"F9.wireOp",EDGE,"E2470"),sQuery(id+"F9.wireOp",EDGE,"E2471"),sQuery(id+"F9.wireOp",EDGE,"E2472"),sQuery(id+"F9.wireOp",EDGE,"E2473"),sQuery(id+"F9.wireOp",EDGE,"E2474"),sQuery(id+"F9.wireOp",EDGE,"E2475"),sQuery(id+"F9.wireOp",EDGE,"E2476"),sQuery(id+"F9.wireOp",EDGE,"E2477"),sQuery(id+"F9.wireOp",EDGE,"E2478"),sQuery(id+"F9.wireOp",EDGE,"E2479"),sQuery(id+"F9.wireOp",EDGE,"E2480"),sQuery(id+"F9.wireOp",EDGE,"E2481"),sQuery(id+"F9.wireOp",EDGE,"E2482"),sQuery(id+"F9.wireOp",EDGE,"E2483"),sQuery(id+"F9.wireOp",EDGE,"E2484"),sQuery(id+"F9.wireOp",EDGE,"E2485"),sQuery(id+"F9.wireOp",EDGE,"E2486"),sQuery(id+"F9.wireOp",EDGE,"E2487"),sQuery(id+"F9.wireOp",EDGE,"E2488"),sQuery(id+"F9.wireOp",EDGE,"E2489"),sQuery(id+"F9.wireOp",EDGE,"E2490"),sQuery(id+"F9.wireOp",EDGE,"E2491"),sQuery(id+"F9.wireOp",EDGE,"E2492"),sQuery(id+"F9.wireOp",EDGE,"E2493"),sQuery(id+"F9.wireOp",EDGE,"E2494"),sQuery(id+"F9.wireOp",EDGE,"E2495"),sQuery(id+"F9.wireOp",EDGE,"E2496"),sQuery(id+"F9.wireOp",EDGE,"E2497"),sQuery(id+"F9.wireOp",EDGE,"E2498"),sQuery(id+"F9.wireOp",EDGE,"E2499"),sQuery(id+"F9.wireOp",EDGE,"E2500"),sQuery(id+"F9.wireOp",EDGE,"E2501"),sQuery(id+"F9.wireOp",EDGE,"E2502"),sQuery(id+"F9.wireOp",EDGE,"E2503"),sQuery(id+"F9.wireOp",EDGE,"E2504"),sQuery(id+"F9.wireOp",EDGE,"E2505"),sQuery(id+"F9.wireOp",EDGE,"E2506"),sQuery(id+"F9.wireOp",EDGE,"E2507"),sQuery(id+"F9.wireOp",EDGE,"E2508"),sQuery(id+"F9.wireOp",EDGE,"E2509"),sQuery(id+"F9.wireOp",EDGE,"E2510"),sQuery(id+"F9.wireOp",EDGE,"E2511"),sQuery(id+"F9.wireOp",EDGE,"E2512"),sQuery(id+"F9.wireOp",EDGE,"E2513"),sQuery(id+"F9.wireOp",EDGE,"E2514"),sQuery(id+"F9.wireOp",EDGE,"E2515"),sQuery(id+"F9.wireOp",EDGE,"E2516"),sQuery(id+"F9.wireOp",EDGE,"E2517"),sQuery(id+"F9.wireOp",EDGE,"E2518"),sQuery(id+"F9.wireOp",EDGE,"E2519"),sQuery(id+"F9.wireOp",EDGE,"E2520"),sQuery(id+"F9.wireOp",EDGE,"E2521"),sQuery(id+"F9.wireOp",EDGE,"E2522"),sQuery(id+"F9.wireOp",EDGE,"E2523"),sQuery(id+"F9.wireOp",EDGE,"E2524"),sQuery(id+"F9.wireOp",EDGE,"E2525"),sQuery(id+"F9.wireOp",EDGE,"E2526"),sQuery(id+"F9.wireOp",EDGE,"E2527"),sQuery(id+"F9.wireOp",EDGE,"E2528"),sQuery(id+"F9.wireOp",EDGE,"E2529"),sQuery(id+"F9.wireOp",EDGE,"E2530"),sQuery(id+"F9.wireOp",EDGE,"E2531"),sQuery(id+"F9.wireOp",EDGE,"E2532"),sQuery(id+"F9.wireOp",EDGE,"E2533"),sQuery(id+"F9.wireOp",EDGE,"E2534"),sQuery(id+"F9.wireOp",EDGE,"E2535"),sQuery(id+"F9.wireOp",EDGE,"E2536"),sQuery(id+"F9.wireOp",EDGE,"E2537"),sQuery(id+"F9.wireOp",EDGE,"E2538"),sQuery(id+"F9.wireOp",EDGE,"E2539"),sQuery(id+"F9.wireOp",EDGE,"E2540"),sQuery(id+"F9.wireOp",EDGE,"E2541"),sQuery(id+"F9.wireOp",EDGE,"E2542"),sQuery(id+"F9.wireOp",EDGE,"E2543"),sQuery(id+"F9.wireOp",EDGE,"E2544"),sQuery(id+"F9.wireOp",EDGE,"E2545"),sQuery(id+"F9.wireOp",EDGE,"E2546"),sQuery(id+"F9.wireOp",EDGE,"E2547"),sQuery(id+"F9.wireOp",EDGE,"E2548"),sQuery(id+"F9.wireOp",EDGE,"E2549"),sQuery(id+"F9.wireOp",EDGE,"E2550"),sQuery(id+"F9.wireOp",EDGE,"E2551"),sQuery(id+"F9.wireOp",EDGE,"E2552"),sQuery(id+"F9.wireOp",EDGE,"E2553"),sQuery(id+"F9.wireOp",EDGE,"E2554"),sQuery(id+"F9.wireOp",EDGE,"E2555"),sQuery(id+"F9.wireOp",EDGE,"E2556"),sQuery(id+"F9.wireOp",EDGE,"E2557"),sQuery(id+"F9.wireOp",EDGE,"E2558"),sQuery(id+"F9.wireOp",EDGE,"E2559"),sQuery(id+"F9.wireOp",EDGE,"E2560"),sQuery(id+"F9.wireOp",EDGE,"E2561"),sQuery(id+"F9.wireOp",EDGE,"E2562"),sQuery(id+"F9.wireOp",EDGE,"E2563"),sQuery(id+"F9.wireOp",EDGE,"E2564"),sQuery(id+"F9.wireOp",EDGE,"E2565"),sQuery(id+"F9.wireOp",EDGE,"E2566"),sQuery(id+"F9.wireOp",EDGE,"E2567"),sQuery(id+"F9.wireOp",EDGE,"E2568"),sQuery(id+"F9.wireOp",EDGE,"E2569"),sQuery(id+"F9.wireOp",EDGE,"E2570"),sQuery(id+"F9.wireOp",EDGE,"E2571"),sQuery(id+"F9.wireOp",EDGE,"E2572"),sQuery(id+"F9.wireOp",EDGE,"E2573"),sQuery(id+"F9.wireOp",EDGE,"E2574"),sQuery(id+"F9.wireOp",EDGE,"E2575"),sQuery(id+"F9.wireOp",EDGE,"E2576"),sQuery(id+"F9.wireOp",EDGE,"E2577"),sQuery(id+"F9.wireOp",EDGE,"E2578"),sQuery(id+"F9.wireOp",EDGE,"E2579"),sQuery(id+"F9.wireOp",EDGE,"E2580"),sQuery(id+"F9.wireOp",EDGE,"E2581"),sQuery(id+"F9.wireOp",EDGE,"E2582"),sQuery(id+"F9.wireOp",EDGE,"E2583"),sQuery(id+"F9.wireOp",EDGE,"E2584"),sQuery(id+"F9.wireOp",EDGE,"E2585"),sQuery(id+"F9.wireOp",EDGE,"E2586"),sQuery(id+"F9.wireOp",EDGE,"E2587"),sQuery(id+"F9.wireOp",EDGE,"E2588"),sQuery(id+"F9.wireOp",EDGE,"E2589"),sQuery(id+"F9.wireOp",EDGE,"E2590"),sQuery(id+"F9.wireOp",EDGE,"E2591"),sQuery(id+"F9.wireOp",EDGE,"E2592"),sQuery(id+"F9.wireOp",EDGE,"E2593"),sQuery(id+"F9.wireOp",EDGE,"E2594"),sQuery(id+"F9.wireOp",EDGE,"E2595"),sQuery(id+"F9.wireOp",EDGE,"E2596"),sQuery(id+"F9.wireOp",EDGE,"E2597"),sQuery(id+"F9.wireOp",EDGE,"E2598"),sQuery(id+"F9.wireOp",EDGE,"E2599"),sQuery(id+"F9.wireOp",EDGE,"E2600"),sQuery(id+"F9.wireOp",EDGE,"E2601"),sQuery(id+"F9.wireOp",EDGE,"E2602"),sQuery(id+"F9.wireOp",EDGE,"E2603"),sQuery(id+"F9.wireOp",EDGE,"E2604"),sQuery(id+"F9.wireOp",EDGE,"E2605"),sQuery(id+"F9.wireOp",EDGE,"E2606"),sQuery(id+"F9.wireOp",EDGE,"E2607"),sQuery(id+"F9.wireOp",EDGE,"E2608"),sQuery(id+"F9.wireOp",EDGE,"E2609"),sQuery(id+"F9.wireOp",EDGE,"E2610"),sQuery(id+"F9.wireOp",EDGE,"E2611"),sQuery(id+"F9.wireOp",EDGE,"E2612"),sQuery(id+"F9.wireOp",EDGE,"E2613"),sQuery(id+"F9.wireOp",EDGE,"E2614"),sQuery(id+"F9.wireOp",EDGE,"E2615"),sQuery(id+"F9.wireOp",EDGE,"E2616"),sQuery(id+"F9.wireOp",EDGE,"E2617"),sQuery(id+"F9.wireOp",EDGE,"E2618"),sQuery(id+"F9.wireOp",EDGE,"E2619"),sQuery(id+"F9.wireOp",EDGE,"E2620"),sQuery(id+"F9.wireOp",EDGE,"E2621"),sQuery(id+"F9.wireOp",EDGE,"E2622"),sQuery(id+"F9.wireOp",EDGE,"E2623"),sQuery(id+"F9.wireOp",EDGE,"E2624"),sQuery(id+"F9.wireOp",EDGE,"E2625"),sQuery(id+"F9.wireOp",EDGE,"E2626"),sQuery(id+"F9.wireOp",EDGE,"E2627"),sQuery(id+"F9.wireOp",EDGE,"E2628"),sQuery(id+"F9.wireOp",EDGE,"E2629"),sQuery(id+"F9.wireOp",EDGE,"E2630"),sQuery(id+"F9.wireOp",EDGE,"E2631"),sQuery(id+"F9.wireOp",EDGE,"E2632"),sQuery(id+"F9.wireOp",EDGE,"E2633"),sQuery(id+"F9.wireOp",EDGE,"E2634")])]});
            var Q9;
            Q9=makeQuery(id+"F1.opExtrude","SWEPT_BODY",BODY,{"disambiguationData":[OSD([sQuery(id+"F0.wireOp",EDGE,"E0"),sQuery(id+"F0.wireOp",EDGE,"E1"),sQuery(id+"F0.wireOp",EDGE,"E2"),sQuery(id+"F0.wireOp",EDGE,"E3"),sQuery(id+"F0.wireOp",EDGE,"E4"),sQuery(id+"F0.wireOp",EDGE,"E5"),sQuery(id+"F0.wireOp",EDGE,"E6"),sQuery(id+"F0.wireOp",EDGE,"E7"),sQuery(id+"F0.wireOp",EDGE,"E8"),sQuery(id+"F0.wireOp",EDGE,"E9"),sQuery(id+"F0.wireOp",EDGE,"E10"),sQuery(id+"F0.wireOp",EDGE,"E11"),sQuery(id+"F0.wireOp",EDGE,"E12"),sQuery(id+"F0.wireOp",EDGE,"E13"),sQuery(id+"F0.wireOp",EDGE,"E14"),sQuery(id+"F0.wireOp",EDGE,"E15"),sQuery(id+"F0.wireOp",EDGE,"E16"),sQuery(id+"F0.wireOp",EDGE,"E17"),sQuery(id+"F0.wireOp",EDGE,"E18"),sQuery(id+"F0.wireOp",EDGE,"E19"),sQuery(id+"F0.wireOp",EDGE,"E20"),sQuery(id+"F0.wireOp",EDGE,"E21"),sQuery(id+"F0.wireOp",EDGE,"E22"),sQuery(id+"F0.wireOp",EDGE,"E23"),sQuery(id+"F0.wireOp",EDGE,"E24"),sQuery(id+"F0.wireOp",EDGE,"E25"),sQuery(id+"F0.wireOp",EDGE,"E26"),sQuery(id+"F0.wireOp",EDGE,"E27"),sQuery(id+"F0.wireOp",EDGE,"E28"),sQuery(id+"F0.wireOp",EDGE,"E29"),sQuery(id+"F0.wireOp",EDGE,"E30"),sQuery(id+"F0.wireOp",EDGE,"E31"),sQuery(id+"F0.wireOp",EDGE,"E32"),sQuery(id+"F0.wireOp",EDGE,"E33"),sQuery(id+"F0.wireOp",EDGE,"E34"),sQuery(id+"F0.wireOp",EDGE,"E35"),sQuery(id+"F0.wireOp",EDGE,"E36"),sQuery(id+"F0.wireOp",EDGE,"E37"),sQuery(id+"F0.wireOp",EDGE,"E38"),sQuery(id+"F0.wireOp",EDGE,"E39"),sQuery(id+"F0.wireOp",EDGE,"E40"),sQuery(id+"F0.wireOp",EDGE,"E41"),sQuery(id+"F0.wireOp",EDGE,"E42"),sQuery(id+"F0.wireOp",EDGE,"E43"),sQuery(id+"F0.wireOp",EDGE,"E44"),sQuery(id+"F0.wireOp",EDGE,"E45"),sQuery(id+"F0.wireOp",EDGE,"E46"),sQuery(id+"F0.wireOp",EDGE,"E47"),sQuery(id+"F0.wireOp",EDGE,"E48"),sQuery(id+"F0.wireOp",EDGE,"E49"),sQuery(id+"F0.wireOp",EDGE,"E50"),sQuery(id+"F0.wireOp",EDGE,"E51"),sQuery(id+"F0.wireOp",EDGE,"E52"),sQuery(id+"F0.wireOp",EDGE,"E53"),sQuery(id+"F0.wireOp",EDGE,"E54"),sQuery(id+"F0.wireOp",EDGE,"E55"),sQuery(id+"F0.wireOp",EDGE,"E56"),sQuery(id+"F0.wireOp",EDGE,"E57"),sQuery(id+"F0.wireOp",EDGE,"E58"),sQuery(id+"F0.wireOp",EDGE,"E59"),sQuery(id+"F0.wireOp",EDGE,"E60"),sQuery(id+"F0.wireOp",EDGE,"E61"),sQuery(id+"F0.wireOp",EDGE,"E62"),sQuery(id+"F0.wireOp",EDGE,"E63"),sQuery(id+"F0.wireOp",EDGE,"E64"),sQuery(id+"F0.wireOp",EDGE,"E65"),sQuery(id+"F0.wireOp",EDGE,"E66"),sQuery(id+"F0.wireOp",EDGE,"E67"),sQuery(id+"F0.wireOp",EDGE,"E68"),sQuery(id+"F0.wireOp",EDGE,"E69"),sQuery(id+"F0.wireOp",EDGE,"E70"),sQuery(id+"F0.wireOp",EDGE,"E71"),sQuery(id+"F0.wireOp",EDGE,"E72"),sQuery(id+"F0.wireOp",EDGE,"E73"),sQuery(id+"F0.wireOp",EDGE,"E74"),sQuery(id+"F0.wireOp",EDGE,"E75"),sQuery(id+"F0.wireOp",EDGE,"E76"),sQuery(id+"F0.wireOp",EDGE,"E77"),sQuery(id+"F0.wireOp",EDGE,"E78"),sQuery(id+"F0.wireOp",EDGE,"E79"),sQuery(id+"F0.wireOp",EDGE,"E80"),sQuery(id+"F0.wireOp",EDGE,"E81"),sQuery(id+"F0.wireOp",EDGE,"E82"),sQuery(id+"F0.wireOp",EDGE,"E83"),sQuery(id+"F0.wireOp",EDGE,"E84"),sQuery(id+"F0.wireOp",EDGE,"E85"),sQuery(id+"F0.wireOp",EDGE,"E86"),sQuery(id+"F0.wireOp",EDGE,"E87"),sQuery(id+"F0.wireOp",EDGE,"E88"),sQuery(id+"F0.wireOp",EDGE,"E89"),sQuery(id+"F0.wireOp",EDGE,"E90"),sQuery(id+"F0.wireOp",EDGE,"E91"),sQuery(id+"F0.wireOp",EDGE,"E92"),sQuery(id+"F0.wireOp",EDGE,"E93"),sQuery(id+"F0.wireOp",EDGE,"E94"),sQuery(id+"F0.wireOp",EDGE,"E95"),sQuery(id+"F0.wireOp",EDGE,"E96"),sQuery(id+"F0.wireOp",EDGE,"E97"),sQuery(id+"F0.wireOp",EDGE,"E98"),sQuery(id+"F0.wireOp",EDGE,"E99"),sQuery(id+"F0.wireOp",EDGE,"E100"),sQuery(id+"F0.wireOp",EDGE,"E101"),sQuery(id+"F0.wireOp",EDGE,"E102"),sQuery(id+"F0.wireOp",EDGE,"E103"),sQuery(id+"F0.wireOp",EDGE,"E104"),sQuery(id+"F0.wireOp",EDGE,"E105"),sQuery(id+"F0.wireOp",EDGE,"E106"),sQuery(id+"F0.wireOp",EDGE,"E107"),sQuery(id+"F0.wireOp",EDGE,"E108"),sQuery(id+"F0.wireOp",EDGE,"E109"),sQuery(id+"F0.wireOp",EDGE,"E110"),sQuery(id+"F0.wireOp",EDGE,"E111"),sQuery(id+"F0.wireOp",EDGE,"E112"),sQuery(id+"F0.wireOp",EDGE,"E113"),sQuery(id+"F0.wireOp",EDGE,"E114"),sQuery(id+"F0.wireOp",EDGE,"E115"),sQuery(id+"F0.wireOp",EDGE,"E116"),sQuery(id+"F0.wireOp",EDGE,"E117"),sQuery(id+"F0.wireOp",EDGE,"E118"),sQuery(id+"F0.wireOp",EDGE,"E119"),sQuery(id+"F0.wireOp",EDGE,"E120"),sQuery(id+"F0.wireOp",EDGE,"E121"),sQuery(id+"F0.wireOp",EDGE,"E122"),sQuery(id+"F0.wireOp",EDGE,"E123"),sQuery(id+"F0.wireOp",EDGE,"E124"),sQuery(id+"F0.wireOp",EDGE,"E125"),sQuery(id+"F0.wireOp",EDGE,"E126"),sQuery(id+"F0.wireOp",EDGE,"E127"),sQuery(id+"F0.wireOp",EDGE,"E128"),sQuery(id+"F0.wireOp",EDGE,"E129"),sQuery(id+"F0.wireOp",EDGE,"E130"),sQuery(id+"F0.wireOp",EDGE,"E131"),sQuery(id+"F0.wireOp",EDGE,"E132"),sQuery(id+"F0.wireOp",EDGE,"E133"),sQuery(id+"F0.wireOp",EDGE,"E134"),sQuery(id+"F0.wireOp",EDGE,"E135"),sQuery(id+"F0.wireOp",EDGE,"E136"),sQuery(id+"F0.wireOp",EDGE,"E137"),sQuery(id+"F0.wireOp",EDGE,"E138"),sQuery(id+"F0.wireOp",EDGE,"E139"),sQuery(id+"F0.wireOp",EDGE,"E140"),sQuery(id+"F0.wireOp",EDGE,"E141"),sQuery(id+"F0.wireOp",EDGE,"E142"),sQuery(id+"F0.wireOp",EDGE,"E143"),sQuery(id+"F0.wireOp",EDGE,"E144"),sQuery(id+"F0.wireOp",EDGE,"E145"),sQuery(id+"F0.wireOp",EDGE,"E146"),sQuery(id+"F0.wireOp",EDGE,"E147"),sQuery(id+"F0.wireOp",EDGE,"E148"),sQuery(id+"F0.wireOp",EDGE,"E149"),sQuery(id+"F0.wireOp",EDGE,"E150"),sQuery(id+"F0.wireOp",EDGE,"E151"),sQuery(id+"F0.wireOp",EDGE,"E152"),sQuery(id+"F0.wireOp",EDGE,"E153"),sQuery(id+"F0.wireOp",EDGE,"E154"),sQuery(id+"F0.wireOp",EDGE,"E155"),sQuery(id+"F0.wireOp",EDGE,"E156"),sQuery(id+"F0.wireOp",EDGE,"E157"),sQuery(id+"F0.wireOp",EDGE,"E158"),sQuery(id+"F0.wireOp",EDGE,"E159"),sQuery(id+"F0.wireOp",EDGE,"E160"),sQuery(id+"F0.wireOp",EDGE,"E161"),sQuery(id+"F0.wireOp",EDGE,"E162"),sQuery(id+"F0.wireOp",EDGE,"E163"),sQuery(id+"F0.wireOp",EDGE,"E164"),sQuery(id+"F0.wireOp",EDGE,"E165"),sQuery(id+"F0.wireOp",EDGE,"E166"),sQuery(id+"F0.wireOp",EDGE,"E167"),sQuery(id+"F0.wireOp",EDGE,"E168"),sQuery(id+"F0.wireOp",EDGE,"E169"),sQuery(id+"F0.wireOp",EDGE,"E170"),sQuery(id+"F0.wireOp",EDGE,"E171"),sQuery(id+"F0.wireOp",EDGE,"E172"),sQuery(id+"F0.wireOp",EDGE,"E173"),sQuery(id+"F0.wireOp",EDGE,"E174"),sQuery(id+"F0.wireOp",EDGE,"E175"),sQuery(id+"F0.wireOp",EDGE,"E176"),sQuery(id+"F0.wireOp",EDGE,"E177"),sQuery(id+"F0.wireOp",EDGE,"E178"),sQuery(id+"F0.wireOp",EDGE,"E179"),sQuery(id+"F0.wireOp",EDGE,"E180"),sQuery(id+"F0.wireOp",EDGE,"E181"),sQuery(id+"F0.wireOp",EDGE,"E182"),sQuery(id+"F0.wireOp",EDGE,"E183"),sQuery(id+"F0.wireOp",EDGE,"E184"),sQuery(id+"F0.wireOp",EDGE,"E185"),sQuery(id+"F0.wireOp",EDGE,"E186"),sQuery(id+"F0.wireOp",EDGE,"E187"),sQuery(id+"F0.wireOp",EDGE,"E188"),sQuery(id+"F0.wireOp",EDGE,"E189"),sQuery(id+"F0.wireOp",EDGE,"E190"),sQuery(id+"F0.wireOp",EDGE,"E191"),sQuery(id+"F0.wireOp",EDGE,"E192"),sQuery(id+"F0.wireOp",EDGE,"E193"),sQuery(id+"F0.wireOp",EDGE,"E194"),sQuery(id+"F0.wireOp",EDGE,"E195"),sQuery(id+"F0.wireOp",EDGE,"E196"),sQuery(id+"F0.wireOp",EDGE,"E197"),sQuery(id+"F0.wireOp",EDGE,"E198"),sQuery(id+"F0.wireOp",EDGE,"E199"),sQuery(id+"F0.wireOp",EDGE,"E200"),sQuery(id+"F0.wireOp",EDGE,"E201"),sQuery(id+"F0.wireOp",EDGE,"E202"),sQuery(id+"F0.wireOp",EDGE,"E203"),sQuery(id+"F0.wireOp",EDGE,"E204"),sQuery(id+"F0.wireOp",EDGE,"E205"),sQuery(id+"F0.wireOp",EDGE,"E206"),sQuery(id+"F0.wireOp",EDGE,"E207"),sQuery(id+"F0.wireOp",EDGE,"E208"),sQuery(id+"F0.wireOp",EDGE,"E209"),sQuery(id+"F0.wireOp",EDGE,"E210"),sQuery(id+"F0.wireOp",EDGE,"E211"),sQuery(id+"F0.wireOp",EDGE,"E212"),sQuery(id+"F0.wireOp",EDGE,"E213"),sQuery(id+"F0.wireOp",EDGE,"E214"),sQuery(id+"F0.wireOp",EDGE,"E215"),sQuery(id+"F0.wireOp",EDGE,"E216"),sQuery(id+"F0.wireOp",EDGE,"E217"),sQuery(id+"F0.wireOp",EDGE,"E218"),sQuery(id+"F0.wireOp",EDGE,"E219"),sQuery(id+"F0.wireOp",EDGE,"E220"),sQuery(id+"F0.wireOp",EDGE,"E221"),sQuery(id+"F0.wireOp",EDGE,"E222"),sQuery(id+"F0.wireOp",EDGE,"E223"),sQuery(id+"F0.wireOp",EDGE,"E224"),sQuery(id+"F0.wireOp",EDGE,"E225"),sQuery(id+"F0.wireOp",EDGE,"E226"),sQuery(id+"F0.wireOp",EDGE,"E227"),sQuery(id+"F0.wireOp",EDGE,"E228"),sQuery(id+"F0.wireOp",EDGE,"E229"),sQuery(id+"F0.wireOp",EDGE,"E230"),sQuery(id+"F0.wireOp",EDGE,"E231"),sQuery(id+"F0.wireOp",EDGE,"E232"),sQuery(id+"F0.wireOp",EDGE,"E233"),sQuery(id+"F0.wireOp",EDGE,"E234"),sQuery(id+"F0.wireOp",EDGE,"E235"),sQuery(id+"F0.wireOp",EDGE,"E236"),sQuery(id+"F0.wireOp",EDGE,"E237"),sQuery(id+"F0.wireOp",EDGE,"E238"),sQuery(id+"F0.wireOp",EDGE,"E239"),sQuery(id+"F0.wireOp",EDGE,"E240"),sQuery(id+"F0.wireOp",EDGE,"E241"),sQuery(id+"F0.wireOp",EDGE,"E242"),sQuery(id+"F0.wireOp",EDGE,"E243"),sQuery(id+"F0.wireOp",EDGE,"E244"),sQuery(id+"F0.wireOp",EDGE,"E245"),sQuery(id+"F0.wireOp",EDGE,"E246"),sQuery(id+"F0.wireOp",EDGE,"E247"),sQuery(id+"F0.wireOp",EDGE,"E248"),sQuery(id+"F0.wireOp",EDGE,"E249"),sQuery(id+"F0.wireOp",EDGE,"E250"),sQuery(id+"F0.wireOp",EDGE,"E251"),sQuery(id+"F0.wireOp",EDGE,"E252"),sQuery(id+"F0.wireOp",EDGE,"E253"),sQuery(id+"F0.wireOp",EDGE,"E254"),sQuery(id+"F0.wireOp",EDGE,"E255"),sQuery(id+"F0.wireOp",EDGE,"E256"),sQuery(id+"F0.wireOp",EDGE,"E257"),sQuery(id+"F0.wireOp",EDGE,"E258"),sQuery(id+"F0.wireOp",EDGE,"E259"),sQuery(id+"F0.wireOp",EDGE,"E260"),sQuery(id+"F0.wireOp",EDGE,"E261"),sQuery(id+"F0.wireOp",EDGE,"E262"),sQuery(id+"F0.wireOp",EDGE,"E263"),sQuery(id+"F0.wireOp",EDGE,"E264"),sQuery(id+"F0.wireOp",EDGE,"E265"),sQuery(id+"F0.wireOp",EDGE,"E266"),sQuery(id+"F0.wireOp",EDGE,"E267"),sQuery(id+"F0.wireOp",EDGE,"E268"),sQuery(id+"F0.wireOp",EDGE,"E269"),sQuery(id+"F0.wireOp",EDGE,"E270"),sQuery(id+"F0.wireOp",EDGE,"E271"),sQuery(id+"F0.wireOp",EDGE,"E272"),sQuery(id+"F0.wireOp",EDGE,"E273"),sQuery(id+"F0.wireOp",EDGE,"E274"),sQuery(id+"F0.wireOp",EDGE,"E275"),sQuery(id+"F0.wireOp",EDGE,"E276"),sQuery(id+"F0.wireOp",EDGE,"E277"),sQuery(id+"F0.wireOp",EDGE,"E278"),sQuery(id+"F0.wireOp",EDGE,"E279"),sQuery(id+"F0.wireOp",EDGE,"E280"),sQuery(id+"F0.wireOp",EDGE,"E281"),sQuery(id+"F0.wireOp",EDGE,"E282"),sQuery(id+"F0.wireOp",EDGE,"E283"),sQuery(id+"F0.wireOp",EDGE,"E284"),sQuery(id+"F0.wireOp",EDGE,"E285"),sQuery(id+"F0.wireOp",EDGE,"E286"),sQuery(id+"F0.wireOp",EDGE,"E287"),sQuery(id+"F0.wireOp",EDGE,"E288"),sQuery(id+"F0.wireOp",EDGE,"E289"),sQuery(id+"F0.wireOp",EDGE,"E290"),sQuery(id+"F0.wireOp",EDGE,"E291"),sQuery(id+"F0.wireOp",EDGE,"E292"),sQuery(id+"F0.wireOp",EDGE,"E293"),sQuery(id+"F0.wireOp",EDGE,"E294"),sQuery(id+"F0.wireOp",EDGE,"E295"),sQuery(id+"F0.wireOp",EDGE,"E296"),sQuery(id+"F0.wireOp",EDGE,"E297"),sQuery(id+"F0.wireOp",EDGE,"E298"),sQuery(id+"F0.wireOp",EDGE,"E299"),sQuery(id+"F0.wireOp",EDGE,"E300"),sQuery(id+"F0.wireOp",EDGE,"E301"),sQuery(id+"F0.wireOp",EDGE,"E302"),sQuery(id+"F0.wireOp",EDGE,"E303"),sQuery(id+"F0.wireOp",EDGE,"E304"),sQuery(id+"F0.wireOp",EDGE,"E305"),sQuery(id+"F0.wireOp",EDGE,"E306"),sQuery(id+"F0.wireOp",EDGE,"E307"),sQuery(id+"F0.wireOp",EDGE,"E308"),sQuery(id+"F0.wireOp",EDGE,"E309"),sQuery(id+"F0.wireOp",EDGE,"E310"),sQuery(id+"F0.wireOp",EDGE,"E311"),sQuery(id+"F0.wireOp",EDGE,"E312"),sQuery(id+"F0.wireOp",EDGE,"E313"),sQuery(id+"F0.wireOp",EDGE,"E314"),sQuery(id+"F0.wireOp",EDGE,"E315"),sQuery(id+"F0.wireOp",EDGE,"E316"),sQuery(id+"F0.wireOp",EDGE,"E317"),sQuery(id+"F0.wireOp",EDGE,"E318"),sQuery(id+"F0.wireOp",EDGE,"E319"),sQuery(id+"F0.wireOp",EDGE,"E320"),sQuery(id+"F0.wireOp",EDGE,"E321"),sQuery(id+"F0.wireOp",EDGE,"E322"),sQuery(id+"F0.wireOp",EDGE,"E323"),sQuery(id+"F0.wireOp",EDGE,"E324"),sQuery(id+"F0.wireOp",EDGE,"E325"),sQuery(id+"F0.wireOp",EDGE,"E326"),sQuery(id+"F0.wireOp",EDGE,"E327"),sQuery(id+"F0.wireOp",EDGE,"E328"),sQuery(id+"F0.wireOp",EDGE,"E329"),sQuery(id+"F0.wireOp",EDGE,"E330"),sQuery(id+"F0.wireOp",EDGE,"E331"),sQuery(id+"F0.wireOp",EDGE,"E332"),sQuery(id+"F0.wireOp",EDGE,"E333"),sQuery(id+"F0.wireOp",EDGE,"E334"),sQuery(id+"F0.wireOp",EDGE,"E335"),sQuery(id+"F0.wireOp",EDGE,"E336"),sQuery(id+"F0.wireOp",EDGE,"E337"),sQuery(id+"F0.wireOp",EDGE,"E338"),sQuery(id+"F0.wireOp",EDGE,"E339"),sQuery(id+"F0.wireOp",EDGE,"E340"),sQuery(id+"F0.wireOp",EDGE,"E341"),sQuery(id+"F0.wireOp",EDGE,"E342"),sQuery(id+"F0.wireOp",EDGE,"E343"),sQuery(id+"F0.wireOp",EDGE,"E344"),sQuery(id+"F0.wireOp",EDGE,"E345"),sQuery(id+"F0.wireOp",EDGE,"E346"),sQuery(id+"F0.wireOp",EDGE,"E347"),sQuery(id+"F0.wireOp",EDGE,"E348"),sQuery(id+"F0.wireOp",EDGE,"E349"),sQuery(id+"F0.wireOp",EDGE,"E350"),sQuery(id+"F0.wireOp",EDGE,"E351"),sQuery(id+"F0.wireOp",EDGE,"E352"),sQuery(id+"F0.wireOp",EDGE,"E353"),sQuery(id+"F0.wireOp",EDGE,"E354"),sQuery(id+"F0.wireOp",EDGE,"E355"),sQuery(id+"F0.wireOp",EDGE,"E356"),sQuery(id+"F0.wireOp",EDGE,"E357"),sQuery(id+"F0.wireOp",EDGE,"E358"),sQuery(id+"F0.wireOp",EDGE,"E359"),sQuery(id+"F0.wireOp",EDGE,"E360"),sQuery(id+"F0.wireOp",EDGE,"E361"),sQuery(id+"F0.wireOp",EDGE,"E362"),sQuery(id+"F0.wireOp",EDGE,"E363"),sQuery(id+"F0.wireOp",EDGE,"E364"),sQuery(id+"F0.wireOp",EDGE,"E365"),sQuery(id+"F0.wireOp",EDGE,"E366"),sQuery(id+"F0.wireOp",EDGE,"E367"),sQuery(id+"F0.wireOp",EDGE,"E368"),sQuery(id+"F0.wireOp",EDGE,"E369"),sQuery(id+"F0.wireOp",EDGE,"E370"),sQuery(id+"F0.wireOp",EDGE,"E371"),sQuery(id+"F0.wireOp",EDGE,"E372"),sQuery(id+"F0.wireOp",EDGE,"E373"),sQuery(id+"F0.wireOp",EDGE,"E374"),sQuery(id+"F0.wireOp",EDGE,"E375"),sQuery(id+"F0.wireOp",EDGE,"E376"),sQuery(id+"F0.wireOp",EDGE,"E377"),sQuery(id+"F0.wireOp",EDGE,"E378"),sQuery(id+"F0.wireOp",EDGE,"E379"),sQuery(id+"F0.wireOp",EDGE,"E380"),sQuery(id+"F0.wireOp",EDGE,"E381"),sQuery(id+"F0.wireOp",EDGE,"E382"),sQuery(id+"F0.wireOp",EDGE,"E383"),sQuery(id+"F0.wireOp",EDGE,"E384"),sQuery(id+"F0.wireOp",EDGE,"E385"),sQuery(id+"F0.wireOp",EDGE,"E386"),sQuery(id+"F0.wireOp",EDGE,"E387"),sQuery(id+"F0.wireOp",EDGE,"E388"),sQuery(id+"F0.wireOp",EDGE,"E389"),sQuery(id+"F0.wireOp",EDGE,"E390"),sQuery(id+"F0.wireOp",EDGE,"E391"),sQuery(id+"F0.wireOp",EDGE,"E392"),sQuery(id+"F0.wireOp",EDGE,"E393"),sQuery(id+"F0.wireOp",EDGE,"E394"),sQuery(id+"F0.wireOp",EDGE,"E395"),sQuery(id+"F0.wireOp",EDGE,"E396"),sQuery(id+"F0.wireOp",EDGE,"E397"),sQuery(id+"F0.wireOp",EDGE,"E398"),sQuery(id+"F0.wireOp",EDGE,"E399"),sQuery(id+"F0.wireOp",EDGE,"E400"),sQuery(id+"F0.wireOp",EDGE,"E401"),sQuery(id+"F0.wireOp",EDGE,"E402"),sQuery(id+"F0.wireOp",EDGE,"E403"),sQuery(id+"F0.wireOp",EDGE,"E404"),sQuery(id+"F0.wireOp",EDGE,"E405"),sQuery(id+"F0.wireOp",EDGE,"E406"),sQuery(id+"F0.wireOp",EDGE,"E407"),sQuery(id+"F0.wireOp",EDGE,"E408"),sQuery(id+"F0.wireOp",EDGE,"E409"),sQuery(id+"F0.wireOp",EDGE,"E410"),sQuery(id+"F0.wireOp",EDGE,"E411"),sQuery(id+"F0.wireOp",EDGE,"E412"),sQuery(id+"F0.wireOp",EDGE,"E413"),sQuery(id+"F0.wireOp",EDGE,"E414"),sQuery(id+"F0.wireOp",EDGE,"E415"),sQuery(id+"F0.wireOp",EDGE,"E416"),sQuery(id+"F0.wireOp",EDGE,"E417"),sQuery(id+"F0.wireOp",EDGE,"E418"),sQuery(id+"F0.wireOp",EDGE,"E419"),sQuery(id+"F0.wireOp",EDGE,"E420"),sQuery(id+"F0.wireOp",EDGE,"E421"),sQuery(id+"F0.wireOp",EDGE,"E422"),sQuery(id+"F0.wireOp",EDGE,"E423"),sQuery(id+"F0.wireOp",EDGE,"E424"),sQuery(id+"F0.wireOp",EDGE,"E425"),sQuery(id+"F0.wireOp",EDGE,"E426"),sQuery(id+"F0.wireOp",EDGE,"E427"),sQuery(id+"F0.wireOp",EDGE,"E428"),sQuery(id+"F0.wireOp",EDGE,"E429"),sQuery(id+"F0.wireOp",EDGE,"E430"),sQuery(id+"F0.wireOp",EDGE,"E431"),sQuery(id+"F0.wireOp",EDGE,"E432"),sQuery(id+"F0.wireOp",EDGE,"E433"),sQuery(id+"F0.wireOp",EDGE,"E434"),sQuery(id+"F0.wireOp",EDGE,"E435"),sQuery(id+"F0.wireOp",EDGE,"E436"),sQuery(id+"F0.wireOp",EDGE,"E437"),sQuery(id+"F0.wireOp",EDGE,"E438"),sQuery(id+"F0.wireOp",EDGE,"E439"),sQuery(id+"F0.wireOp",EDGE,"E440"),sQuery(id+"F0.wireOp",EDGE,"E441"),sQuery(id+"F0.wireOp",EDGE,"E442"),sQuery(id+"F0.wireOp",EDGE,"E443"),sQuery(id+"F0.wireOp",EDGE,"E444"),sQuery(id+"F0.wireOp",EDGE,"E445"),sQuery(id+"F0.wireOp",EDGE,"E446"),sQuery(id+"F0.wireOp",EDGE,"E447"),sQuery(id+"F0.wireOp",EDGE,"E448"),sQuery(id+"F0.wireOp",EDGE,"E449"),sQuery(id+"F0.wireOp",EDGE,"E450"),sQuery(id+"F0.wireOp",EDGE,"E451"),sQuery(id+"F0.wireOp",EDGE,"E452"),sQuery(id+"F0.wireOp",EDGE,"E453"),sQuery(id+"F0.wireOp",EDGE,"E454"),sQuery(id+"F0.wireOp",EDGE,"E455"),sQuery(id+"F0.wireOp",EDGE,"E456"),sQuery(id+"F0.wireOp",EDGE,"E457"),sQuery(id+"F0.wireOp",EDGE,"E458"),sQuery(id+"F0.wireOp",EDGE,"E459"),sQuery(id+"F0.wireOp",EDGE,"E460"),sQuery(id+"F0.wireOp",EDGE,"E461"),sQuery(id+"F0.wireOp",EDGE,"E462"),sQuery(id+"F0.wireOp",EDGE,"E463"),sQuery(id+"F0.wireOp",EDGE,"E464"),sQuery(id+"F0.wireOp",EDGE,"E465"),sQuery(id+"F0.wireOp",EDGE,"E466"),sQuery(id+"F0.wireOp",EDGE,"E467"),sQuery(id+"F0.wireOp",EDGE,"E468"),sQuery(id+"F0.wireOp",EDGE,"E469"),sQuery(id+"F0.wireOp",EDGE,"E470"),sQuery(id+"F0.wireOp",EDGE,"E471"),sQuery(id+"F0.wireOp",EDGE,"E472"),sQuery(id+"F0.wireOp",EDGE,"E473"),sQuery(id+"F0.wireOp",EDGE,"E474"),sQuery(id+"F0.wireOp",EDGE,"E475"),sQuery(id+"F0.wireOp",EDGE,"E476"),sQuery(id+"F0.wireOp",EDGE,"E477"),sQuery(id+"F0.wireOp",EDGE,"E478"),sQuery(id+"F0.wireOp",EDGE,"E479"),sQuery(id+"F0.wireOp",EDGE,"E480"),sQuery(id+"F0.wireOp",EDGE,"E481"),sQuery(id+"F0.wireOp",EDGE,"E482"),sQuery(id+"F0.wireOp",EDGE,"E483"),sQuery(id+"F0.wireOp",EDGE,"E484"),sQuery(id+"F0.wireOp",EDGE,"E485"),sQuery(id+"F0.wireOp",EDGE,"E486"),sQuery(id+"F0.wireOp",EDGE,"E487"),sQuery(id+"F0.wireOp",EDGE,"E488"),sQuery(id+"F0.wireOp",EDGE,"E489"),sQuery(id+"F0.wireOp",EDGE,"E490"),sQuery(id+"F0.wireOp",EDGE,"E491"),sQuery(id+"F0.wireOp",EDGE,"E492"),sQuery(id+"F0.wireOp",EDGE,"E493"),sQuery(id+"F0.wireOp",EDGE,"E494"),sQuery(id+"F0.wireOp",EDGE,"E495"),sQuery(id+"F0.wireOp",EDGE,"E496"),sQuery(id+"F0.wireOp",EDGE,"E497"),sQuery(id+"F0.wireOp",EDGE,"E498"),sQuery(id+"F0.wireOp",EDGE,"E499"),sQuery(id+"F0.wireOp",EDGE,"E500"),sQuery(id+"F0.wireOp",EDGE,"E501"),sQuery(id+"F0.wireOp",EDGE,"E502"),sQuery(id+"F0.wireOp",EDGE,"E503")])]});
            booleanBodies(context, id + "F12", {"operationType" : BooleanOperationType.SUBTRACTION, "tools" : qUnion([Q0, Q1, Q2, Q3, Q4, Q5, Q6, Q7, Q8]), "targets" : qUnion([Q9])});
        }
        {
            var Q0;
            Q0=makeQuery(id+"F1.opExtrude","CAP_FACE",FACE,{"disambiguationData":[OSD([sQuery(id+"F0.wireOp",EDGE,"E0"),sQuery(id+"F0.wireOp",EDGE,"E1"),sQuery(id+"F0.wireOp",EDGE,"E2"),sQuery(id+"F0.wireOp",EDGE,"E3"),sQuery(id+"F0.wireOp",EDGE,"E4"),sQuery(id+"F0.wireOp",EDGE,"E5"),sQuery(id+"F0.wireOp",EDGE,"E6"),sQuery(id+"F0.wireOp",EDGE,"E7"),sQuery(id+"F0.wireOp",EDGE,"E8"),sQuery(id+"F0.wireOp",EDGE,"E9"),sQuery(id+"F0.wireOp",EDGE,"E10"),sQuery(id+"F0.wireOp",EDGE,"E11"),sQuery(id+"F0.wireOp",EDGE,"E12"),sQuery(id+"F0.wireOp",EDGE,"E13"),sQuery(id+"F0.wireOp",EDGE,"E14"),sQuery(id+"F0.wireOp",EDGE,"E15"),sQuery(id+"F0.wireOp",EDGE,"E16"),sQuery(id+"F0.wireOp",EDGE,"E17"),sQuery(id+"F0.wireOp",EDGE,"E18"),sQuery(id+"F0.wireOp",EDGE,"E19"),sQuery(id+"F0.wireOp",EDGE,"E20"),sQuery(id+"F0.wireOp",EDGE,"E21"),sQuery(id+"F0.wireOp",EDGE,"E22"),sQuery(id+"F0.wireOp",EDGE,"E23"),sQuery(id+"F0.wireOp",EDGE,"E24"),sQuery(id+"F0.wireOp",EDGE,"E25"),sQuery(id+"F0.wireOp",EDGE,"E26"),sQuery(id+"F0.wireOp",EDGE,"E27"),sQuery(id+"F0.wireOp",EDGE,"E28"),sQuery(id+"F0.wireOp",EDGE,"E29"),sQuery(id+"F0.wireOp",EDGE,"E30"),sQuery(id+"F0.wireOp",EDGE,"E31"),sQuery(id+"F0.wireOp",EDGE,"E32"),sQuery(id+"F0.wireOp",EDGE,"E33"),sQuery(id+"F0.wireOp",EDGE,"E34"),sQuery(id+"F0.wireOp",EDGE,"E35"),sQuery(id+"F0.wireOp",EDGE,"E36"),sQuery(id+"F0.wireOp",EDGE,"E37"),sQuery(id+"F0.wireOp",EDGE,"E38"),sQuery(id+"F0.wireOp",EDGE,"E39"),sQuery(id+"F0.wireOp",EDGE,"E40"),sQuery(id+"F0.wireOp",EDGE,"E41"),sQuery(id+"F0.wireOp",EDGE,"E42"),sQuery(id+"F0.wireOp",EDGE,"E43"),sQuery(id+"F0.wireOp",EDGE,"E44"),sQuery(id+"F0.wireOp",EDGE,"E45"),sQuery(id+"F0.wireOp",EDGE,"E46"),sQuery(id+"F0.wireOp",EDGE,"E47"),sQuery(id+"F0.wireOp",EDGE,"E48"),sQuery(id+"F0.wireOp",EDGE,"E49"),sQuery(id+"F0.wireOp",EDGE,"E50"),sQuery(id+"F0.wireOp",EDGE,"E51"),sQuery(id+"F0.wireOp",EDGE,"E52"),sQuery(id+"F0.wireOp",EDGE,"E53"),sQuery(id+"F0.wireOp",EDGE,"E54"),sQuery(id+"F0.wireOp",EDGE,"E55"),sQuery(id+"F0.wireOp",EDGE,"E56"),sQuery(id+"F0.wireOp",EDGE,"E57"),sQuery(id+"F0.wireOp",EDGE,"E58"),sQuery(id+"F0.wireOp",EDGE,"E59"),sQuery(id+"F0.wireOp",EDGE,"E60"),sQuery(id+"F0.wireOp",EDGE,"E61"),sQuery(id+"F0.wireOp",EDGE,"E62"),sQuery(id+"F0.wireOp",EDGE,"E63"),sQuery(id+"F0.wireOp",EDGE,"E64"),sQuery(id+"F0.wireOp",EDGE,"E65"),sQuery(id+"F0.wireOp",EDGE,"E66"),sQuery(id+"F0.wireOp",EDGE,"E67"),sQuery(id+"F0.wireOp",EDGE,"E68"),sQuery(id+"F0.wireOp",EDGE,"E69"),sQuery(id+"F0.wireOp",EDGE,"E70"),sQuery(id+"F0.wireOp",EDGE,"E71"),sQuery(id+"F0.wireOp",EDGE,"E72"),sQuery(id+"F0.wireOp",EDGE,"E73"),sQuery(id+"F0.wireOp",EDGE,"E74"),sQuery(id+"F0.wireOp",EDGE,"E75"),sQuery(id+"F0.wireOp",EDGE,"E76"),sQuery(id+"F0.wireOp",EDGE,"E77"),sQuery(id+"F0.wireOp",EDGE,"E78"),sQuery(id+"F0.wireOp",EDGE,"E79"),sQuery(id+"F0.wireOp",EDGE,"E80"),sQuery(id+"F0.wireOp",EDGE,"E81"),sQuery(id+"F0.wireOp",EDGE,"E82"),sQuery(id+"F0.wireOp",EDGE,"E83"),sQuery(id+"F0.wireOp",EDGE,"E84"),sQuery(id+"F0.wireOp",EDGE,"E85"),sQuery(id+"F0.wireOp",EDGE,"E86"),sQuery(id+"F0.wireOp",EDGE,"E87"),sQuery(id+"F0.wireOp",EDGE,"E88"),sQuery(id+"F0.wireOp",EDGE,"E89"),sQuery(id+"F0.wireOp",EDGE,"E90"),sQuery(id+"F0.wireOp",EDGE,"E91"),sQuery(id+"F0.wireOp",EDGE,"E92"),sQuery(id+"F0.wireOp",EDGE,"E93"),sQuery(id+"F0.wireOp",EDGE,"E94"),sQuery(id+"F0.wireOp",EDGE,"E95"),sQuery(id+"F0.wireOp",EDGE,"E96"),sQuery(id+"F0.wireOp",EDGE,"E97"),sQuery(id+"F0.wireOp",EDGE,"E98"),sQuery(id+"F0.wireOp",EDGE,"E99"),sQuery(id+"F0.wireOp",EDGE,"E100"),sQuery(id+"F0.wireOp",EDGE,"E101"),sQuery(id+"F0.wireOp",EDGE,"E102"),sQuery(id+"F0.wireOp",EDGE,"E103"),sQuery(id+"F0.wireOp",EDGE,"E104"),sQuery(id+"F0.wireOp",EDGE,"E105"),sQuery(id+"F0.wireOp",EDGE,"E106"),sQuery(id+"F0.wireOp",EDGE,"E107"),sQuery(id+"F0.wireOp",EDGE,"E108"),sQuery(id+"F0.wireOp",EDGE,"E109"),sQuery(id+"F0.wireOp",EDGE,"E110"),sQuery(id+"F0.wireOp",EDGE,"E111"),sQuery(id+"F0.wireOp",EDGE,"E112"),sQuery(id+"F0.wireOp",EDGE,"E113"),sQuery(id+"F0.wireOp",EDGE,"E114"),sQuery(id+"F0.wireOp",EDGE,"E115"),sQuery(id+"F0.wireOp",EDGE,"E116"),sQuery(id+"F0.wireOp",EDGE,"E117"),sQuery(id+"F0.wireOp",EDGE,"E118"),sQuery(id+"F0.wireOp",EDGE,"E119"),sQuery(id+"F0.wireOp",EDGE,"E120"),sQuery(id+"F0.wireOp",EDGE,"E121"),sQuery(id+"F0.wireOp",EDGE,"E122"),sQuery(id+"F0.wireOp",EDGE,"E123"),sQuery(id+"F0.wireOp",EDGE,"E124"),sQuery(id+"F0.wireOp",EDGE,"E125"),sQuery(id+"F0.wireOp",EDGE,"E126"),sQuery(id+"F0.wireOp",EDGE,"E127"),sQuery(id+"F0.wireOp",EDGE,"E128"),sQuery(id+"F0.wireOp",EDGE,"E129"),sQuery(id+"F0.wireOp",EDGE,"E130"),sQuery(id+"F0.wireOp",EDGE,"E131"),sQuery(id+"F0.wireOp",EDGE,"E132"),sQuery(id+"F0.wireOp",EDGE,"E133"),sQuery(id+"F0.wireOp",EDGE,"E134"),sQuery(id+"F0.wireOp",EDGE,"E135"),sQuery(id+"F0.wireOp",EDGE,"E136"),sQuery(id+"F0.wireOp",EDGE,"E137"),sQuery(id+"F0.wireOp",EDGE,"E138"),sQuery(id+"F0.wireOp",EDGE,"E139"),sQuery(id+"F0.wireOp",EDGE,"E140"),sQuery(id+"F0.wireOp",EDGE,"E141"),sQuery(id+"F0.wireOp",EDGE,"E142"),sQuery(id+"F0.wireOp",EDGE,"E143"),sQuery(id+"F0.wireOp",EDGE,"E144"),sQuery(id+"F0.wireOp",EDGE,"E145"),sQuery(id+"F0.wireOp",EDGE,"E146"),sQuery(id+"F0.wireOp",EDGE,"E147"),sQuery(id+"F0.wireOp",EDGE,"E148"),sQuery(id+"F0.wireOp",EDGE,"E149"),sQuery(id+"F0.wireOp",EDGE,"E150"),sQuery(id+"F0.wireOp",EDGE,"E151"),sQuery(id+"F0.wireOp",EDGE,"E152"),sQuery(id+"F0.wireOp",EDGE,"E153"),sQuery(id+"F0.wireOp",EDGE,"E154"),sQuery(id+"F0.wireOp",EDGE,"E155"),sQuery(id+"F0.wireOp",EDGE,"E156"),sQuery(id+"F0.wireOp",EDGE,"E157"),sQuery(id+"F0.wireOp",EDGE,"E158"),sQuery(id+"F0.wireOp",EDGE,"E159"),sQuery(id+"F0.wireOp",EDGE,"E160"),sQuery(id+"F0.wireOp",EDGE,"E161"),sQuery(id+"F0.wireOp",EDGE,"E162"),sQuery(id+"F0.wireOp",EDGE,"E163"),sQuery(id+"F0.wireOp",EDGE,"E164"),sQuery(id+"F0.wireOp",EDGE,"E165"),sQuery(id+"F0.wireOp",EDGE,"E166"),sQuery(id+"F0.wireOp",EDGE,"E167"),sQuery(id+"F0.wireOp",EDGE,"E168"),sQuery(id+"F0.wireOp",EDGE,"E169"),sQuery(id+"F0.wireOp",EDGE,"E170"),sQuery(id+"F0.wireOp",EDGE,"E171"),sQuery(id+"F0.wireOp",EDGE,"E172"),sQuery(id+"F0.wireOp",EDGE,"E173"),sQuery(id+"F0.wireOp",EDGE,"E174"),sQuery(id+"F0.wireOp",EDGE,"E175"),sQuery(id+"F0.wireOp",EDGE,"E176"),sQuery(id+"F0.wireOp",EDGE,"E177"),sQuery(id+"F0.wireOp",EDGE,"E178"),sQuery(id+"F0.wireOp",EDGE,"E179"),sQuery(id+"F0.wireOp",EDGE,"E180"),sQuery(id+"F0.wireOp",EDGE,"E181"),sQuery(id+"F0.wireOp",EDGE,"E182"),sQuery(id+"F0.wireOp",EDGE,"E183"),sQuery(id+"F0.wireOp",EDGE,"E184"),sQuery(id+"F0.wireOp",EDGE,"E185"),sQuery(id+"F0.wireOp",EDGE,"E186"),sQuery(id+"F0.wireOp",EDGE,"E187"),sQuery(id+"F0.wireOp",EDGE,"E188"),sQuery(id+"F0.wireOp",EDGE,"E189"),sQuery(id+"F0.wireOp",EDGE,"E190"),sQuery(id+"F0.wireOp",EDGE,"E191"),sQuery(id+"F0.wireOp",EDGE,"E192"),sQuery(id+"F0.wireOp",EDGE,"E193"),sQuery(id+"F0.wireOp",EDGE,"E194"),sQuery(id+"F0.wireOp",EDGE,"E195"),sQuery(id+"F0.wireOp",EDGE,"E196"),sQuery(id+"F0.wireOp",EDGE,"E197"),sQuery(id+"F0.wireOp",EDGE,"E198"),sQuery(id+"F0.wireOp",EDGE,"E199"),sQuery(id+"F0.wireOp",EDGE,"E200"),sQuery(id+"F0.wireOp",EDGE,"E201"),sQuery(id+"F0.wireOp",EDGE,"E202"),sQuery(id+"F0.wireOp",EDGE,"E203"),sQuery(id+"F0.wireOp",EDGE,"E204"),sQuery(id+"F0.wireOp",EDGE,"E205"),sQuery(id+"F0.wireOp",EDGE,"E206"),sQuery(id+"F0.wireOp",EDGE,"E207"),sQuery(id+"F0.wireOp",EDGE,"E208"),sQuery(id+"F0.wireOp",EDGE,"E209"),sQuery(id+"F0.wireOp",EDGE,"E210"),sQuery(id+"F0.wireOp",EDGE,"E211"),sQuery(id+"F0.wireOp",EDGE,"E212"),sQuery(id+"F0.wireOp",EDGE,"E213"),sQuery(id+"F0.wireOp",EDGE,"E214"),sQuery(id+"F0.wireOp",EDGE,"E215"),sQuery(id+"F0.wireOp",EDGE,"E216"),sQuery(id+"F0.wireOp",EDGE,"E217"),sQuery(id+"F0.wireOp",EDGE,"E218"),sQuery(id+"F0.wireOp",EDGE,"E219"),sQuery(id+"F0.wireOp",EDGE,"E220"),sQuery(id+"F0.wireOp",EDGE,"E221"),sQuery(id+"F0.wireOp",EDGE,"E222"),sQuery(id+"F0.wireOp",EDGE,"E223"),sQuery(id+"F0.wireOp",EDGE,"E224"),sQuery(id+"F0.wireOp",EDGE,"E225"),sQuery(id+"F0.wireOp",EDGE,"E226"),sQuery(id+"F0.wireOp",EDGE,"E227"),sQuery(id+"F0.wireOp",EDGE,"E228"),sQuery(id+"F0.wireOp",EDGE,"E229"),sQuery(id+"F0.wireOp",EDGE,"E230"),sQuery(id+"F0.wireOp",EDGE,"E231"),sQuery(id+"F0.wireOp",EDGE,"E232"),sQuery(id+"F0.wireOp",EDGE,"E233"),sQuery(id+"F0.wireOp",EDGE,"E234"),sQuery(id+"F0.wireOp",EDGE,"E235"),sQuery(id+"F0.wireOp",EDGE,"E236"),sQuery(id+"F0.wireOp",EDGE,"E237"),sQuery(id+"F0.wireOp",EDGE,"E238"),sQuery(id+"F0.wireOp",EDGE,"E239"),sQuery(id+"F0.wireOp",EDGE,"E240"),sQuery(id+"F0.wireOp",EDGE,"E241"),sQuery(id+"F0.wireOp",EDGE,"E242"),sQuery(id+"F0.wireOp",EDGE,"E243"),sQuery(id+"F0.wireOp",EDGE,"E244"),sQuery(id+"F0.wireOp",EDGE,"E245"),sQuery(id+"F0.wireOp",EDGE,"E246"),sQuery(id+"F0.wireOp",EDGE,"E247"),sQuery(id+"F0.wireOp",EDGE,"E248"),sQuery(id+"F0.wireOp",EDGE,"E249"),sQuery(id+"F0.wireOp",EDGE,"E250"),sQuery(id+"F0.wireOp",EDGE,"E251"),sQuery(id+"F0.wireOp",EDGE,"E252"),sQuery(id+"F0.wireOp",EDGE,"E253"),sQuery(id+"F0.wireOp",EDGE,"E254"),sQuery(id+"F0.wireOp",EDGE,"E255"),sQuery(id+"F0.wireOp",EDGE,"E256"),sQuery(id+"F0.wireOp",EDGE,"E257"),sQuery(id+"F0.wireOp",EDGE,"E258"),sQuery(id+"F0.wireOp",EDGE,"E259"),sQuery(id+"F0.wireOp",EDGE,"E260"),sQuery(id+"F0.wireOp",EDGE,"E261"),sQuery(id+"F0.wireOp",EDGE,"E262"),sQuery(id+"F0.wireOp",EDGE,"E263"),sQuery(id+"F0.wireOp",EDGE,"E264"),sQuery(id+"F0.wireOp",EDGE,"E265"),sQuery(id+"F0.wireOp",EDGE,"E266"),sQuery(id+"F0.wireOp",EDGE,"E267"),sQuery(id+"F0.wireOp",EDGE,"E268"),sQuery(id+"F0.wireOp",EDGE,"E269"),sQuery(id+"F0.wireOp",EDGE,"E270"),sQuery(id+"F0.wireOp",EDGE,"E271"),sQuery(id+"F0.wireOp",EDGE,"E272"),sQuery(id+"F0.wireOp",EDGE,"E273"),sQuery(id+"F0.wireOp",EDGE,"E274"),sQuery(id+"F0.wireOp",EDGE,"E275"),sQuery(id+"F0.wireOp",EDGE,"E276"),sQuery(id+"F0.wireOp",EDGE,"E277"),sQuery(id+"F0.wireOp",EDGE,"E278"),sQuery(id+"F0.wireOp",EDGE,"E279"),sQuery(id+"F0.wireOp",EDGE,"E280"),sQuery(id+"F0.wireOp",EDGE,"E281"),sQuery(id+"F0.wireOp",EDGE,"E282"),sQuery(id+"F0.wireOp",EDGE,"E283"),sQuery(id+"F0.wireOp",EDGE,"E284"),sQuery(id+"F0.wireOp",EDGE,"E285"),sQuery(id+"F0.wireOp",EDGE,"E286"),sQuery(id+"F0.wireOp",EDGE,"E287"),sQuery(id+"F0.wireOp",EDGE,"E288"),sQuery(id+"F0.wireOp",EDGE,"E289"),sQuery(id+"F0.wireOp",EDGE,"E290"),sQuery(id+"F0.wireOp",EDGE,"E291"),sQuery(id+"F0.wireOp",EDGE,"E292"),sQuery(id+"F0.wireOp",EDGE,"E293"),sQuery(id+"F0.wireOp",EDGE,"E294"),sQuery(id+"F0.wireOp",EDGE,"E295"),sQuery(id+"F0.wireOp",EDGE,"E296"),sQuery(id+"F0.wireOp",EDGE,"E297"),sQuery(id+"F0.wireOp",EDGE,"E298"),sQuery(id+"F0.wireOp",EDGE,"E299"),sQuery(id+"F0.wireOp",EDGE,"E300"),sQuery(id+"F0.wireOp",EDGE,"E301"),sQuery(id+"F0.wireOp",EDGE,"E302"),sQuery(id+"F0.wireOp",EDGE,"E303"),sQuery(id+"F0.wireOp",EDGE,"E304"),sQuery(id+"F0.wireOp",EDGE,"E305"),sQuery(id+"F0.wireOp",EDGE,"E306"),sQuery(id+"F0.wireOp",EDGE,"E307"),sQuery(id+"F0.wireOp",EDGE,"E308"),sQuery(id+"F0.wireOp",EDGE,"E309"),sQuery(id+"F0.wireOp",EDGE,"E310"),sQuery(id+"F0.wireOp",EDGE,"E311"),sQuery(id+"F0.wireOp",EDGE,"E312"),sQuery(id+"F0.wireOp",EDGE,"E313"),sQuery(id+"F0.wireOp",EDGE,"E314"),sQuery(id+"F0.wireOp",EDGE,"E315"),sQuery(id+"F0.wireOp",EDGE,"E316"),sQuery(id+"F0.wireOp",EDGE,"E317"),sQuery(id+"F0.wireOp",EDGE,"E318"),sQuery(id+"F0.wireOp",EDGE,"E319"),sQuery(id+"F0.wireOp",EDGE,"E320"),sQuery(id+"F0.wireOp",EDGE,"E321"),sQuery(id+"F0.wireOp",EDGE,"E322"),sQuery(id+"F0.wireOp",EDGE,"E323"),sQuery(id+"F0.wireOp",EDGE,"E324"),sQuery(id+"F0.wireOp",EDGE,"E325"),sQuery(id+"F0.wireOp",EDGE,"E326"),sQuery(id+"F0.wireOp",EDGE,"E327"),sQuery(id+"F0.wireOp",EDGE,"E328"),sQuery(id+"F0.wireOp",EDGE,"E329"),sQuery(id+"F0.wireOp",EDGE,"E330"),sQuery(id+"F0.wireOp",EDGE,"E331"),sQuery(id+"F0.wireOp",EDGE,"E332"),sQuery(id+"F0.wireOp",EDGE,"E333"),sQuery(id+"F0.wireOp",EDGE,"E334"),sQuery(id+"F0.wireOp",EDGE,"E335"),sQuery(id+"F0.wireOp",EDGE,"E336"),sQuery(id+"F0.wireOp",EDGE,"E337"),sQuery(id+"F0.wireOp",EDGE,"E338"),sQuery(id+"F0.wireOp",EDGE,"E339"),sQuery(id+"F0.wireOp",EDGE,"E340"),sQuery(id+"F0.wireOp",EDGE,"E341"),sQuery(id+"F0.wireOp",EDGE,"E342"),sQuery(id+"F0.wireOp",EDGE,"E343"),sQuery(id+"F0.wireOp",EDGE,"E344"),sQuery(id+"F0.wireOp",EDGE,"E345"),sQuery(id+"F0.wireOp",EDGE,"E346"),sQuery(id+"F0.wireOp",EDGE,"E347"),sQuery(id+"F0.wireOp",EDGE,"E348"),sQuery(id+"F0.wireOp",EDGE,"E349"),sQuery(id+"F0.wireOp",EDGE,"E350"),sQuery(id+"F0.wireOp",EDGE,"E351"),sQuery(id+"F0.wireOp",EDGE,"E352"),sQuery(id+"F0.wireOp",EDGE,"E353"),sQuery(id+"F0.wireOp",EDGE,"E354"),sQuery(id+"F0.wireOp",EDGE,"E355"),sQuery(id+"F0.wireOp",EDGE,"E356"),sQuery(id+"F0.wireOp",EDGE,"E357"),sQuery(id+"F0.wireOp",EDGE,"E358"),sQuery(id+"F0.wireOp",EDGE,"E359"),sQuery(id+"F0.wireOp",EDGE,"E360"),sQuery(id+"F0.wireOp",EDGE,"E361"),sQuery(id+"F0.wireOp",EDGE,"E362"),sQuery(id+"F0.wireOp",EDGE,"E363"),sQuery(id+"F0.wireOp",EDGE,"E364"),sQuery(id+"F0.wireOp",EDGE,"E365"),sQuery(id+"F0.wireOp",EDGE,"E366"),sQuery(id+"F0.wireOp",EDGE,"E367"),sQuery(id+"F0.wireOp",EDGE,"E368"),sQuery(id+"F0.wireOp",EDGE,"E369"),sQuery(id+"F0.wireOp",EDGE,"E370"),sQuery(id+"F0.wireOp",EDGE,"E371"),sQuery(id+"F0.wireOp",EDGE,"E372"),sQuery(id+"F0.wireOp",EDGE,"E373"),sQuery(id+"F0.wireOp",EDGE,"E374"),sQuery(id+"F0.wireOp",EDGE,"E375"),sQuery(id+"F0.wireOp",EDGE,"E376"),sQuery(id+"F0.wireOp",EDGE,"E377"),sQuery(id+"F0.wireOp",EDGE,"E378"),sQuery(id+"F0.wireOp",EDGE,"E379"),sQuery(id+"F0.wireOp",EDGE,"E380"),sQuery(id+"F0.wireOp",EDGE,"E381"),sQuery(id+"F0.wireOp",EDGE,"E382"),sQuery(id+"F0.wireOp",EDGE,"E383"),sQuery(id+"F0.wireOp",EDGE,"E384"),sQuery(id+"F0.wireOp",EDGE,"E385"),sQuery(id+"F0.wireOp",EDGE,"E386"),sQuery(id+"F0.wireOp",EDGE,"E387"),sQuery(id+"F0.wireOp",EDGE,"E388"),sQuery(id+"F0.wireOp",EDGE,"E389"),sQuery(id+"F0.wireOp",EDGE,"E390"),sQuery(id+"F0.wireOp",EDGE,"E391"),sQuery(id+"F0.wireOp",EDGE,"E392"),sQuery(id+"F0.wireOp",EDGE,"E393"),sQuery(id+"F0.wireOp",EDGE,"E394"),sQuery(id+"F0.wireOp",EDGE,"E395"),sQuery(id+"F0.wireOp",EDGE,"E396"),sQuery(id+"F0.wireOp",EDGE,"E397"),sQuery(id+"F0.wireOp",EDGE,"E398"),sQuery(id+"F0.wireOp",EDGE,"E399"),sQuery(id+"F0.wireOp",EDGE,"E400"),sQuery(id+"F0.wireOp",EDGE,"E401"),sQuery(id+"F0.wireOp",EDGE,"E402"),sQuery(id+"F0.wireOp",EDGE,"E403"),sQuery(id+"F0.wireOp",EDGE,"E404"),sQuery(id+"F0.wireOp",EDGE,"E405"),sQuery(id+"F0.wireOp",EDGE,"E406"),sQuery(id+"F0.wireOp",EDGE,"E407"),sQuery(id+"F0.wireOp",EDGE,"E408"),sQuery(id+"F0.wireOp",EDGE,"E409"),sQuery(id+"F0.wireOp",EDGE,"E410"),sQuery(id+"F0.wireOp",EDGE,"E411"),sQuery(id+"F0.wireOp",EDGE,"E412"),sQuery(id+"F0.wireOp",EDGE,"E413"),sQuery(id+"F0.wireOp",EDGE,"E414"),sQuery(id+"F0.wireOp",EDGE,"E415"),sQuery(id+"F0.wireOp",EDGE,"E416"),sQuery(id+"F0.wireOp",EDGE,"E417"),sQuery(id+"F0.wireOp",EDGE,"E418"),sQuery(id+"F0.wireOp",EDGE,"E419"),sQuery(id+"F0.wireOp",EDGE,"E420"),sQuery(id+"F0.wireOp",EDGE,"E421"),sQuery(id+"F0.wireOp",EDGE,"E422"),sQuery(id+"F0.wireOp",EDGE,"E423"),sQuery(id+"F0.wireOp",EDGE,"E424"),sQuery(id+"F0.wireOp",EDGE,"E425"),sQuery(id+"F0.wireOp",EDGE,"E426"),sQuery(id+"F0.wireOp",EDGE,"E427"),sQuery(id+"F0.wireOp",EDGE,"E428"),sQuery(id+"F0.wireOp",EDGE,"E429"),sQuery(id+"F0.wireOp",EDGE,"E430"),sQuery(id+"F0.wireOp",EDGE,"E431"),sQuery(id+"F0.wireOp",EDGE,"E432"),sQuery(id+"F0.wireOp",EDGE,"E433"),sQuery(id+"F0.wireOp",EDGE,"E434"),sQuery(id+"F0.wireOp",EDGE,"E435"),sQuery(id+"F0.wireOp",EDGE,"E436"),sQuery(id+"F0.wireOp",EDGE,"E437"),sQuery(id+"F0.wireOp",EDGE,"E438"),sQuery(id+"F0.wireOp",EDGE,"E439"),sQuery(id+"F0.wireOp",EDGE,"E440"),sQuery(id+"F0.wireOp",EDGE,"E441"),sQuery(id+"F0.wireOp",EDGE,"E442"),sQuery(id+"F0.wireOp",EDGE,"E443"),sQuery(id+"F0.wireOp",EDGE,"E444"),sQuery(id+"F0.wireOp",EDGE,"E445"),sQuery(id+"F0.wireOp",EDGE,"E446"),sQuery(id+"F0.wireOp",EDGE,"E447"),sQuery(id+"F0.wireOp",EDGE,"E448"),sQuery(id+"F0.wireOp",EDGE,"E449"),sQuery(id+"F0.wireOp",EDGE,"E450"),sQuery(id+"F0.wireOp",EDGE,"E451"),sQuery(id+"F0.wireOp",EDGE,"E452"),sQuery(id+"F0.wireOp",EDGE,"E453"),sQuery(id+"F0.wireOp",EDGE,"E454"),sQuery(id+"F0.wireOp",EDGE,"E455"),sQuery(id+"F0.wireOp",EDGE,"E456"),sQuery(id+"F0.wireOp",EDGE,"E457"),sQuery(id+"F0.wireOp",EDGE,"E458"),sQuery(id+"F0.wireOp",EDGE,"E459"),sQuery(id+"F0.wireOp",EDGE,"E460"),sQuery(id+"F0.wireOp",EDGE,"E461"),sQuery(id+"F0.wireOp",EDGE,"E462"),sQuery(id+"F0.wireOp",EDGE,"E463"),sQuery(id+"F0.wireOp",EDGE,"E464"),sQuery(id+"F0.wireOp",EDGE,"E465"),sQuery(id+"F0.wireOp",EDGE,"E466"),sQuery(id+"F0.wireOp",EDGE,"E467"),sQuery(id+"F0.wireOp",EDGE,"E468"),sQuery(id+"F0.wireOp",EDGE,"E469"),sQuery(id+"F0.wireOp",EDGE,"E470"),sQuery(id+"F0.wireOp",EDGE,"E471"),sQuery(id+"F0.wireOp",EDGE,"E472"),sQuery(id+"F0.wireOp",EDGE,"E473"),sQuery(id+"F0.wireOp",EDGE,"E474"),sQuery(id+"F0.wireOp",EDGE,"E475"),sQuery(id+"F0.wireOp",EDGE,"E476"),sQuery(id+"F0.wireOp",EDGE,"E477"),sQuery(id+"F0.wireOp",EDGE,"E478"),sQuery(id+"F0.wireOp",EDGE,"E479"),sQuery(id+"F0.wireOp",EDGE,"E480"),sQuery(id+"F0.wireOp",EDGE,"E481"),sQuery(id+"F0.wireOp",EDGE,"E482"),sQuery(id+"F0.wireOp",EDGE,"E483"),sQuery(id+"F0.wireOp",EDGE,"E484"),sQuery(id+"F0.wireOp",EDGE,"E485"),sQuery(id+"F0.wireOp",EDGE,"E486"),sQuery(id+"F0.wireOp",EDGE,"E487"),sQuery(id+"F0.wireOp",EDGE,"E488"),sQuery(id+"F0.wireOp",EDGE,"E489"),sQuery(id+"F0.wireOp",EDGE,"E490"),sQuery(id+"F0.wireOp",EDGE,"E491"),sQuery(id+"F0.wireOp",EDGE,"E492"),sQuery(id+"F0.wireOp",EDGE,"E493"),sQuery(id+"F0.wireOp",EDGE,"E494"),sQuery(id+"F0.wireOp",EDGE,"E495"),sQuery(id+"F0.wireOp",EDGE,"E496"),sQuery(id+"F0.wireOp",EDGE,"E497"),sQuery(id+"F0.wireOp",EDGE,"E498"),sQuery(id+"F0.wireOp",EDGE,"E499"),sQuery(id+"F0.wireOp",EDGE,"E500"),sQuery(id+"F0.wireOp",EDGE,"E501"),sQuery(id+"F0.wireOp",EDGE,"E502"),sQuery(id+"F0.wireOp",EDGE,"E503")])],"isStart":false});
            cPlane(context, id + "F13", {"entities" : qUnion([Q0]), "cplaneType" : CPlaneType.OFFSET, "offset" : 22 * mm, "width" : 150 * mm, "height" : 150 * mm});
        }
        {
            var Q0;
            Q0=qCreatedBy(id+"F13.planeOp",FACE);
            var sketch = newSketch(context, id + "F14", { "sketchPlane" : qUnion([Q0])});
            skLineSegment(sketch, "E2635.4", {"start": v(-8.63, 3.4) * mm, "end": v(-8.57, 3.5) * mm});
            skLineSegment(sketch, "E2635.10", {"start": v(-6, 6.6) * mm, "end": v(-5.9, 6.69) * mm});
            skLineSegment(sketch, "E2635.13", {"start": v(4.4, 7.94) * mm, "end": v(4.5, 7.87) * mm});
            skLineSegment(sketch, "E2635.29", {"start": v(9.95, -0.4) * mm, "end": v(9.93, -0.5) * mm});
            skLineSegment(sketch, "E2635.33", {"start": v(-6.3, -6.3) * mm, "end": v(-6.4, -6.2) * mm});
            skLineSegment(sketch, "E2635.40", {"start": v(6.78, 5.8) * mm, "end": v(6.87, 5.7) * mm});
            skLineSegment(sketch, "E2635.41", {"start": v(0.9, 9.82) * mm, "end": v(1, 9.79) * mm});
            skLineSegment(sketch, "E2635.42", {"start": v(-6.5, 6.1) * mm, "end": v(-6.4, 6.2) * mm});
            skLineSegment(sketch, "E2635.43", {"start": v(6.3, 6.3) * mm, "end": v(6.4, 6.2) * mm});
            skLineSegment(sketch, "E2635.55", {"start": v(-2.3, 9.25) * mm, "end": v(-2.2, 9.3) * mm});
            skLineSegment(sketch, "E2635.56", {"start": v(6.6, 6) * mm, "end": v(6.69, 5.9) * mm});
            skLineSegment(sketch, "E2635.62", {"start": v(-6.2, 6.4) * mm, "end": v(-6.1, 6.5) * mm});
            skLineSegment(sketch, "E2635.71", {"start": v(-2.1, 9.35) * mm, "end": v(-2, 9.4) * mm});
            skLineSegment(sketch, "E2635.72", {"start": v(4, 8.23) * mm, "end": v(4.1, 8.16) * mm});
            skLineSegment(sketch, "E2635.81", {"start": v(-6.69, 5.9) * mm, "end": v(-6.6, 6) * mm});
            skLineSegment(sketch, "E2635.82", {"start": v(-5.5, -7.05) * mm, "end": v(-5.6, -6.96) * mm});
            skLineSegment(sketch, "E2635.83", {"start": v(6.69, 5.9) * mm, "end": v(6.78, 5.8) * mm});
            skLineSegment(sketch, "E2635.92", {"start": v(-6.3, 6.3) * mm, "end": v(-6.2, 6.4) * mm});
            skLineSegment(sketch, "E2635.94", {"start": v(3.8, 8.37) * mm, "end": v(3.9, 8.3) * mm});
            skLineSegment(sketch, "E2635.101", {"start": v(4.2, 8.1) * mm, "end": v(4.3, 8.02) * mm});
            skLineSegment(sketch, "E2635.104", {"start": v(6.5, 6.1) * mm, "end": v(6.6, 6) * mm});
            skLineSegment(sketch, "E2635.121", {"start": v(-8.7, 3.3) * mm, "end": v(-8.63, 3.4) * mm});
            skLineSegment(sketch, "E2635.124", {"start": v(-6.1, 6.5) * mm, "end": v(-6, 6.6) * mm});
            skLineSegment(sketch, "E2635.130", {"start": v(-9.48, 1.8) * mm, "end": v(-9.44, 1.9) * mm});
            skLineSegment(sketch, "E2635.132", {"start": v(-8.75, 3.2) * mm, "end": v(-8.7, 3.3) * mm});
            skLineSegment(sketch, "E2635.152", {"start": v(6.4, 6.2) * mm, "end": v(6.5, 6.1) * mm});
            skLineSegment(sketch, "E2635.154", {"start": v(4.1, 8.16) * mm, "end": v(4.2, 8.1) * mm});
            skLineSegment(sketch, "E2635.158", {"start": v(-8.87, 3) * mm, "end": v(-8.81, 3.1) * mm});
            skLineSegment(sketch, "E2635.165", {"start": v(-9.88, -0.7) * mm, "end": v(-9.9, -0.6) * mm});
            skLineSegment(sketch, "E2635.175", {"start": v(-5.4, -7.14) * mm, "end": v(-5.5, -7.05) * mm});
            skLineSegment(sketch, "E2635.181", {"start": v(3.9, 8.3) * mm, "end": v(4, 8.23) * mm});
            skLineSegment(sketch, "E2635.189", {"start": v(4.3, 8.02) * mm, "end": v(4.4, 7.94) * mm});
            skLineSegment(sketch, "E2635.194", {"start": v(-2.2, 9.3) * mm, "end": v(-2.1, 9.35) * mm});
            skLineSegment(sketch, "E2635.196", {"start": v(0.8, 9.85) * mm, "end": v(0.9, 9.82) * mm});
            skLineSegment(sketch, "E2635.198", {"start": v(-7.14, 5.4) * mm, "end": v(-7.05, 5.5) * mm});
            skLineSegment(sketch, "E2635.200", {"start": v(-2.4, 9.2) * mm, "end": v(-2.3, 9.25) * mm});
            skLineSegment(sketch, "E2635.205", {"start": v(-6.78, 5.8) * mm, "end": v(-6.69, 5.9) * mm});
            skLineSegment(sketch, "E2635.208", {"start": v(-6.4, 6.2) * mm, "end": v(-6.3, 6.3) * mm});
            skLineSegment(sketch, "E2635.220", {"start": v(3.7, 8.44) * mm, "end": v(3.8, 8.37) * mm});
            skLineSegment(sketch, "E2635.222", {"start": v(-9.82, -0.9) * mm, "end": v(-9.85, -0.8) * mm});
            skLineSegment(sketch, "E2635.223", {"start": v(-6.6, 6) * mm, "end": v(-6.5, 6.1) * mm});
            skLineSegment(sketch, "E2635.228", {"start": v(-6.96, 5.6) * mm, "end": v(-6.87, 5.7) * mm});
            skLineSegment(sketch, "E2635.249", {"start": v(0.7, 9.88) * mm, "end": v(0.8, 9.85) * mm});
            skLineSegment(sketch, "E2635.250", {"start": v(9.97, -0.3) * mm, "end": v(9.95, -0.4) * mm});
            skLineSegment(sketch, "E2635.256", {"start": v(6.2, 6.4) * mm, "end": v(6.3, 6.3) * mm});
            skLineSegment(sketch, "E2635.258", {"start": v(-6.2, -6.4) * mm, "end": v(-6.3, -6.3) * mm});
            skLineSegment(sketch, "E2635.282", {"start": v(-1.6, -9.57) * mm, "end": v(-1.7, -9.53) * mm});
            skLineSegment(sketch, "E2635.283", {"start": v(8.87, -3) * mm, "end": v(8.81, -3.1) * mm});
            skLineSegment(sketch, "E2635.284", {"start": v(-4.8, -7.64) * mm, "end": v(-4.9, -7.56) * mm});
            skLineSegment(sketch, "E2635.285", {"start": v(-9.65, -1.4) * mm, "end": v(-9.69, -1.3) * mm});
            skLineSegment(sketch, "E2635.286", {"start": v(7.8, -4.6) * mm, "end": v(7.72, -4.7) * mm});
            skLineSegment(sketch, "E2635.287", {"start": v(-8.87, -3) * mm, "end": v(-8.93, -2.9) * mm});
            skLineSegment(sketch, "E2635.288", {"start": v(-9.98, 0.2) * mm, "end": v(-9.97, 0.3) * mm});
            skLineSegment(sketch, "E2635.289", {"start": v(1.6, -9.57) * mm, "end": v(1.5, -9.6) * mm});
            skLineSegment(sketch, "E2635.290", {"start": v(-9.53, 1.7) * mm, "end": v(-9.48, 1.8) * mm});
            skLineSegment(sketch, "E2635.291", {"start": v(6, 6.6) * mm, "end": v(6.1, 6.5) * mm});
            skLineSegment(sketch, "E2635.292", {"start": v(6.4, -6.2) * mm, "end": v(6.3, -6.3) * mm});
            skLineSegment(sketch, "E2635.293", {"start": v(8.63, 3.4) * mm, "end": v(8.7, 3.3) * mm});
            skLineSegment(sketch, "E2635.294", {"start": v(9.65, -1.4) * mm, "end": v(9.6, -1.5) * mm});
            skLineSegment(sketch, "E2635.295", {"start": v(7.48, 5) * mm, "end": v(7.56, 4.9) * mm});
            skLineSegment(sketch, "E2635.297", {"start": v(-7.56, 4.9) * mm, "end": v(-7.48, 5) * mm});
            skLineSegment(sketch, "E2635.298", {"start": v(9.98, 0.2) * mm, "end": v(10, 0.1) * mm});
            skLineSegment(sketch, "E2635.299", {"start": v(-6.4, -6.2) * mm, "end": v(-6.5, -6.1) * mm});
            skLineSegment(sketch, "E2635.300", {"start": v(9.48, 1.8) * mm, "end": v(9.53, 1.7) * mm});
            skLineSegment(sketch, "E2635.301", {"start": v(-3.2, -8.75) * mm, "end": v(-3.3, -8.7) * mm});
            skLineSegment(sketch, "E2635.302", {"start": v(-7.48, 5) * mm, "end": v(-7.4, 5.1) * mm});
            skLineSegment(sketch, "E2635.304", {"start": v(2.8, 8.99) * mm, "end": v(2.9, 8.93) * mm});
            skLineSegment(sketch, "E2635.305", {"start": v(-2.8, 8.99) * mm, "end": v(-2.7, 9.04) * mm});
            skLineSegment(sketch, "E2635.307", {"start": v(9.69, -1.3) * mm, "end": v(9.65, -1.4) * mm});
            skLineSegment(sketch, "E2635.309", {"start": v(-1.2, 9.72) * mm, "end": v(-1.1, 9.76) * mm});
            skLineSegment(sketch, "E2635.311", {"start": v(-1.5, -9.6) * mm, "end": v(-1.6, -9.57) * mm});
            skLineSegment(sketch, "E2635.312", {"start": v(6.5, -6.1) * mm, "end": v(6.4, -6.2) * mm});
            skLineSegment(sketch, "E2635.314", {"start": v(-7.64, -4.8) * mm, "end": v(-7.72, -4.7) * mm});
            skLineSegment(sketch, "E2635.315", {"start": v(1.7, -9.53) * mm, "end": v(1.6, -9.57) * mm});
            skLineSegment(sketch, "E2635.316", {"start": v(9.15, -2.5) * mm, "end": v(9.1, -2.6) * mm});
            skLineSegment(sketch, "E2635.319", {"start": v(2.1, -9.35) * mm, "end": v(2, -9.4) * mm});
            skLineSegment(sketch, "E2635.320", {"start": v(-3.1, -8.81) * mm, "end": v(-3.2, -8.75) * mm});
            skLineSegment(sketch, "E2635.321", {"start": v(5.4, -7.14) * mm, "end": v(5.3, -7.23) * mm});
            skLineSegment(sketch, "E2635.322", {"start": v(5.5, -7.05) * mm, "end": v(5.4, -7.14) * mm});
            skLineSegment(sketch, "E2635.324", {"start": v(-2.6, -9.1) * mm, "end": v(-2.7, -9.04) * mm});
            skLineSegment(sketch, "E2635.327", {"start": v(-9.4, -2) * mm, "end": v(-9.44, -1.9) * mm});
            skLineSegment(sketch, "E2635.328", {"start": v(-5.7, -6.87) * mm, "end": v(-5.8, -6.78) * mm});
            skLineSegment(sketch, "E2635.330", {"start": v(-8.99, 2.8) * mm, "end": v(-8.93, 2.9) * mm});
            skLineSegment(sketch, "E2635.332", {"start": v(9.2, -2.4) * mm, "end": v(9.15, -2.5) * mm});
            skLineSegment(sketch, "E2635.333", {"start": v(2.4, 9.2) * mm, "end": v(2.5, 9.15) * mm});
            skLineSegment(sketch, "E2635.335", {"start": v(-9.95, -0.4) * mm, "end": v(-9.97, -0.3) * mm});
            skLineSegment(sketch, "E2635.337", {"start": v(4.6, 7.8) * mm, "end": v(4.7, 7.72) * mm});
            skLineSegment(sketch, "E2635.339", {"start": v(9.88, -0.7) * mm, "end": v(9.85, -0.8) * mm});
            skLineSegment(sketch, "E2635.340", {"start": v(0.3, -9.97) * mm, "end": v(0.2, -9.98) * mm});
            skLineSegment(sketch, "E2635.342", {"start": v(0.4, -9.95) * mm, "end": v(0.3, -9.97) * mm});
            skLineSegment(sketch, "E2635.344", {"start": v(-2, -9.4) * mm, "end": v(-2.1, -9.35) * mm});
            skLineSegment(sketch, "E2635.348", {"start": v(6.78, -5.8) * mm, "end": v(6.69, -5.9) * mm});
            skLineSegment(sketch, "E2635.349", {"start": v(9.9, -0.6) * mm, "end": v(9.88, -0.7) * mm});
            skLineSegment(sketch, "E2635.351", {"start": v(-4.3, -8.02) * mm, "end": v(-4.4, -7.94) * mm});
            skLineSegment(sketch, "E2635.352", {"start": v(-0.1, 10) * mm, "end": v(0, 10) * mm});
            skLineSegment(sketch, "E2635.356", {"start": v(10, -0.1) * mm, "end": v(9.98, -0.2) * mm});
            skLineSegment(sketch, "E2635.357", {"start": v(5.8, 6.78) * mm, "end": v(5.9, 6.69) * mm});
            skLineSegment(sketch, "E2635.359", {"start": v(0.1, -10) * mm, "end": v(0, -10) * mm});
            skLineSegment(sketch, "E2635.362", {"start": v(-1.2, -9.72) * mm, "end": v(-1.3, -9.69) * mm});
            skLineSegment(sketch, "E2635.365", {"start": v(0.8, -9.85) * mm, "end": v(0.7, -9.88) * mm});
            skLineSegment(sketch, "E2635.368", {"start": v(9.72, -1.2) * mm, "end": v(9.69, -1.3) * mm});
            skLineSegment(sketch, "E2635.371", {"start": v(7.87, 4.5) * mm, "end": v(7.94, 4.4) * mm});
            skLineSegment(sketch, "E2635.374", {"start": v(5.1, 7.4) * mm, "end": v(5.2, 7.31) * mm});
            skLineSegment(sketch, "E2635.378", {"start": v(5.6, 6.96) * mm, "end": v(5.7, 6.87) * mm});
            skLineSegment(sketch, "E2635.380", {"start": v(5.7, 6.87) * mm, "end": v(5.8, 6.78) * mm});
            skLineSegment(sketch, "E2635.381", {"start": v(8.5, -3.6) * mm, "end": v(8.44, -3.7) * mm});
            skLineSegment(sketch, "E2635.382", {"start": v(8.63, -3.4) * mm, "end": v(8.57, -3.5) * mm});
            skLineSegment(sketch, "E2635.383", {"start": v(-9.85, -0.8) * mm, "end": v(-9.88, -0.7) * mm});
            skLineSegment(sketch, "E2635.384", {"start": v(7.14, -5.4) * mm, "end": v(7.05, -5.5) * mm});
            skLineSegment(sketch, "E2635.385", {"start": v(-7.94, 4.4) * mm, "end": v(-7.87, 4.5) * mm});
            skLineSegment(sketch, "E2635.386", {"start": v(-2.9, -8.93) * mm, "end": v(-3, -8.87) * mm});
            skLineSegment(sketch, "E2635.388", {"start": v(-7.87, 4.5) * mm, "end": v(-7.8, 4.6) * mm});
            skLineSegment(sketch, "E2635.390", {"start": v(-5.2, -7.31) * mm, "end": v(-5.3, -7.23) * mm});
            skLineSegment(sketch, "E2635.391", {"start": v(-1.9, -9.44) * mm, "end": v(-2, -9.4) * mm});
            skLineSegment(sketch, "E2635.393", {"start": v(-7.05, 5.5) * mm, "end": v(-6.96, 5.6) * mm});
            skLineSegment(sketch, "E2635.394", {"start": v(4.8, 7.64) * mm, "end": v(4.9, 7.56) * mm});
            skLineSegment(sketch, "E2635.395", {"start": v(8.93, -2.9) * mm, "end": v(8.87, -3) * mm});
            skLineSegment(sketch, "E2635.396", {"start": v(1, -9.79) * mm, "end": v(0.9, -9.82) * mm});
            skLineSegment(sketch, "E2635.398", {"start": v(-5.8, -6.78) * mm, "end": v(-5.9, -6.69) * mm});
            skLineSegment(sketch, "E2635.401", {"start": v(-2.8, -8.99) * mm, "end": v(-2.9, -8.93) * mm});
            skLineSegment(sketch, "E2635.404", {"start": v(1.9, -9.44) * mm, "end": v(1.8, -9.48) * mm});
            skLineSegment(sketch, "E2635.405", {"start": v(-7.64, 4.8) * mm, "end": v(-7.56, 4.9) * mm});
            skLineSegment(sketch, "E2635.406", {"start": v(2.1, 9.35) * mm, "end": v(2.2, 9.3) * mm});
            skLineSegment(sketch, "E2635.407", {"start": v(0.6, -9.9) * mm, "end": v(0.5, -9.93) * mm});
            skLineSegment(sketch, "E2635.408", {"start": v(-4.1, -8.16) * mm, "end": v(-4.2, -8.1) * mm});
            skLineSegment(sketch, "E2635.410", {"start": v(-8.93, 2.9) * mm, "end": v(-8.87, 3) * mm});
            skLineSegment(sketch, "E2635.413", {"start": v(7.56, -4.9) * mm, "end": v(7.48, -5) * mm});
            skLineSegment(sketch, "E2635.415", {"start": v(-6.1, -6.5) * mm, "end": v(-6.2, -6.4) * mm});
            skLineSegment(sketch, "E2635.416", {"start": v(7.8, 4.6) * mm, "end": v(7.87, 4.5) * mm});
            skLineSegment(sketch, "E2635.417", {"start": v(-2.4, -9.2) * mm, "end": v(-2.5, -9.15) * mm});
            skLineSegment(sketch, "E2635.421", {"start": v(9.53, -1.7) * mm, "end": v(9.48, -1.8) * mm});
            skLineSegment(sketch, "E2635.422", {"start": v(9.1, -2.6) * mm, "end": v(9.04, -2.7) * mm});
            skLineSegment(sketch, "E2635.425", {"start": v(-5, 7.48) * mm, "end": v(-4.9, 7.56) * mm});
            skLineSegment(sketch, "E2635.426", {"start": v(8.37, -3.8) * mm, "end": v(8.3, -3.9) * mm});
            skLineSegment(sketch, "E2635.427", {"start": v(6, -6.6) * mm, "end": v(5.9, -6.69) * mm});
            skLineSegment(sketch, "E2635.429", {"start": v(-2.2, -9.3) * mm, "end": v(-2.3, -9.25) * mm});
            skLineSegment(sketch, "E2635.430", {"start": v(-0.8, 9.85) * mm, "end": v(-0.7, 9.88) * mm});
            skLineSegment(sketch, "E2635.432", {"start": v(-2.5, 9.15) * mm, "end": v(-2.4, 9.2) * mm});
            skLineSegment(sketch, "E2635.433", {"start": v(-7.8, 4.6) * mm, "end": v(-7.72, 4.7) * mm});
            skLineSegment(sketch, "E2635.437", {"start": v(0.5, 9.93) * mm, "end": v(0.6, 9.9) * mm});
            skLineSegment(sketch, "E2635.440", {"start": v(0.6, 9.9) * mm, "end": v(0.7, 9.88) * mm});
            skLineSegment(sketch, "E2635.441", {"start": v(9.79, -1) * mm, "end": v(9.76, -1.1) * mm});
            skLineSegment(sketch, "E2635.443", {"start": v(4.9, 7.56) * mm, "end": v(5, 7.48) * mm});
            skLineSegment(sketch, "E2635.444", {"start": v(9.44, -1.9) * mm, "end": v(9.4, -2) * mm});
            skLineSegment(sketch, "E2635.445", {"start": v(6.96, -5.6) * mm, "end": v(6.87, -5.7) * mm});
            skLineSegment(sketch, "E2635.446", {"start": v(8.02, 4.3) * mm, "end": v(8.1, 4.2) * mm});
            skLineSegment(sketch, "E2635.447", {"start": v(8.99, 2.8) * mm, "end": v(9.04, 2.7) * mm});
            skLineSegment(sketch, "E2635.448", {"start": v(-8.81, 3.1) * mm, "end": v(-8.75, 3.2) * mm});
            skLineSegment(sketch, "E2635.449", {"start": v(-3.7, -8.44) * mm, "end": v(-3.8, -8.37) * mm});
            skLineSegment(sketch, "E2635.450", {"start": v(-7.23, -5.3) * mm, "end": v(-7.31, -5.2) * mm});
            skLineSegment(sketch, "E2635.451", {"start": v(-8.37, 3.8) * mm, "end": v(-8.3, 3.9) * mm});
            skLineSegment(sketch, "E2635.454", {"start": v(9.98, -0.2) * mm, "end": v(9.97, -0.3) * mm});
            skLineSegment(sketch, "E2635.456", {"start": v(-8.57, 3.5) * mm, "end": v(-8.5, 3.6) * mm});
            skLineSegment(sketch, "E2635.457", {"start": v(8.99, -2.8) * mm, "end": v(8.93, -2.9) * mm});
            skLineSegment(sketch, "E2635.459", {"start": v(3.3, 8.7) * mm, "end": v(3.4, 8.63) * mm});
            skLineSegment(sketch, "E2635.460", {"start": v(5, 7.48) * mm, "end": v(5.1, 7.4) * mm});
            skLineSegment(sketch, "E2635.462", {"start": v(-9.98, -0.2) * mm, "end": v(-10, -0.1) * mm});
            skLineSegment(sketch, "E2635.463", {"start": v(-6.87, 5.7) * mm, "end": v(-6.78, 5.8) * mm});
            skLineSegment(sketch, "E2635.464", {"start": v(-5.2, 7.31) * mm, "end": v(-5.1, 7.4) * mm});
            skLineSegment(sketch, "E2635.465", {"start": v(-9.79, -1) * mm, "end": v(-9.82, -0.9) * mm});
            skLineSegment(sketch, "E2635.466", {"start": v(-0.6, 9.9) * mm, "end": v(-0.5, 9.93) * mm});
            skLineSegment(sketch, "E2635.467", {"start": v(-4.6, -7.8) * mm, "end": v(-4.7, -7.72) * mm});
            skLineSegment(sketch, "E2635.468", {"start": v(-8.23, 4) * mm, "end": v(-8.16, 4.1) * mm});
            skLineSegment(sketch, "E2635.470", {"start": v(-0.3, 9.97) * mm, "end": v(-0.2, 9.98) * mm});
            skLineSegment(sketch, "E2635.473", {"start": v(8.87, 3) * mm, "end": v(8.93, 2.9) * mm});
            skLineSegment(sketch, "E2635.475", {"start": v(9.35, -2.1) * mm, "end": v(9.3, -2.2) * mm});
            skLineSegment(sketch, "E2635.477", {"start": v(5.3, 7.23) * mm, "end": v(5.4, 7.14) * mm});
            skLineSegment(sketch, "E2635.478", {"start": v(-9.1, 2.6) * mm, "end": v(-9.04, 2.7) * mm});
            skLineSegment(sketch, "E2635.480", {"start": v(-3.9, -8.3) * mm, "end": v(-4, -8.23) * mm});
            skLineSegment(sketch, "E2635.483", {"start": v(-4.4, -7.94) * mm, "end": v(-4.5, -7.87) * mm});
            skLineSegment(sketch, "E2635.484", {"start": v(-3.8, -8.37) * mm, "end": v(-3.9, -8.3) * mm});
            skLineSegment(sketch, "E2635.486", {"start": v(6.1, 6.5) * mm, "end": v(6.2, 6.4) * mm});
            skLineSegment(sketch, "E2635.487", {"start": v(1.3, -9.69) * mm, "end": v(1.2, -9.72) * mm});
            skLineSegment(sketch, "E2635.491", {"start": v(-0.4, 9.95) * mm, "end": v(-0.3, 9.97) * mm});
            skLineSegment(sketch, "E2635.493", {"start": v(0.4, 9.95) * mm, "end": v(0.5, 9.93) * mm});
            skLineSegment(sketch, "E2635.498", {"start": v(-9.76, -1.1) * mm, "end": v(-9.79, -1) * mm});
            skLineSegment(sketch, "E2635.499", {"start": v(-3.5, -8.57) * mm, "end": v(-3.6, -8.5) * mm});
            skLineSegment(sketch, "E2635.503", {"start": v(7.23, -5.3) * mm, "end": v(7.14, -5.4) * mm});
            skLineSegment(sketch, "E2635.504", {"start": v(-9.6, -1.5) * mm, "end": v(-9.65, -1.4) * mm});
            skLineSegment(sketch, "E2635.505", {"start": v(3.4, 8.63) * mm, "end": v(3.5, 8.57) * mm});
            skLineSegment(sketch, "E2635.506", {"start": v(0.9, -9.82) * mm, "end": v(0.8, -9.85) * mm});
            skLineSegment(sketch, "E2635.508", {"start": v(7.4, -5.1) * mm, "end": v(7.31, -5.2) * mm});
            skLineSegment(sketch, "E2635.509", {"start": v(6.69, -5.9) * mm, "end": v(6.6, -6) * mm});
            skLineSegment(sketch, "E2635.512", {"start": v(3.6, 8.5) * mm, "end": v(3.7, 8.44) * mm});
            skLineSegment(sketch, "E2635.513", {"start": v(-8.5, 3.6) * mm, "end": v(-8.44, 3.7) * mm});
            skLineSegment(sketch, "E2635.515", {"start": v(-7.4, -5.1) * mm, "end": v(-7.48, -5) * mm});
            skLineSegment(sketch, "E2635.516", {"start": v(2, 9.4) * mm, "end": v(2.1, 9.35) * mm});
            skLineSegment(sketch, "E2635.517", {"start": v(-8.1, 4.2) * mm, "end": v(-8.02, 4.3) * mm});
            skLineSegment(sketch, "E2635.518", {"start": v(2.6, 9.1) * mm, "end": v(2.7, 9.04) * mm});
            skLineSegment(sketch, "E2635.522", {"start": v(-5, -7.48) * mm, "end": v(-5.1, -7.4) * mm});
            skLineSegment(sketch, "E2635.523", {"start": v(-6, -6.6) * mm, "end": v(-6.1, -6.5) * mm});
            skLineSegment(sketch, "E2635.525", {"start": v(-9.3, 2.2) * mm, "end": v(-9.25, 2.3) * mm});
            skLineSegment(sketch, "E2635.527", {"start": v(-9.4, 2) * mm, "end": v(-9.35, 2.1) * mm});
            skLineSegment(sketch, "E2635.529", {"start": v(5.5, 7.05) * mm, "end": v(5.6, 6.96) * mm});
            skLineSegment(sketch, "E2635.530", {"start": v(4.9, -7.56) * mm, "end": v(4.8, -7.64) * mm});
            skLineSegment(sketch, "E2635.532", {"start": v(5.7, -6.87) * mm, "end": v(5.6, -6.96) * mm});
            skLineSegment(sketch, "E2635.534", {"start": v(5, -7.48) * mm, "end": v(4.9, -7.56) * mm});
            skLineSegment(sketch, "E2635.535", {"start": v(9.3, -2.2) * mm, "end": v(9.25, -2.3) * mm});
            skLineSegment(sketch, "E2635.536", {"start": v(-7.23, 5.3) * mm, "end": v(-7.14, 5.4) * mm});
            skLineSegment(sketch, "E2635.537", {"start": v(-10, 0.1) * mm, "end": v(-9.98, 0.2) * mm});
            skLineSegment(sketch, "E2635.540", {"start": v(-9.35, 2.1) * mm, "end": v(-9.3, 2.2) * mm});
            skLineSegment(sketch, "E2635.541", {"start": v(-7.48, -5) * mm, "end": v(-7.56, -4.9) * mm});
            skLineSegment(sketch, "E2635.542", {"start": v(0.2, 9.98) * mm, "end": v(0.3, 9.97) * mm});
            skLineSegment(sketch, "E2635.545", {"start": v(7.48, -5) * mm, "end": v(7.4, -5.1) * mm});
            skLineSegment(sketch, "E2635.547", {"start": v(5.2, -7.31) * mm, "end": v(5.1, -7.4) * mm});
            skLineSegment(sketch, "E2635.548", {"start": v(3.2, 8.75) * mm, "end": v(3.3, 8.7) * mm});
            skLineSegment(sketch, "E2635.549", {"start": v(5.9, -6.69) * mm, "end": v(5.8, -6.78) * mm});
            skLineSegment(sketch, "E2635.550", {"start": v(-5.3, -7.23) * mm, "end": v(-5.4, -7.14) * mm});
            skLineSegment(sketch, "E2635.551", {"start": v(-9.2, 2.4) * mm, "end": v(-9.15, 2.5) * mm});
            skLineSegment(sketch, "E2635.552", {"start": v(-9.48, -1.8) * mm, "end": v(-9.53, -1.7) * mm});
            skLineSegment(sketch, "E2635.553", {"start": v(-9.88, 0.7) * mm, "end": v(-9.85, 0.8) * mm});
            skLineSegment(sketch, "E2635.555", {"start": v(-2.9, 8.93) * mm, "end": v(-2.8, 8.99) * mm});
            skLineSegment(sketch, "E2635.560", {"start": v(-4.7, -7.72) * mm, "end": v(-4.8, -7.64) * mm});
            skLineSegment(sketch, "E2635.561", {"start": v(9.82, -0.9) * mm, "end": v(9.79, -1) * mm});
            skLineSegment(sketch, "E2635.562", {"start": v(-0.2, 9.98) * mm, "end": v(-0.1, 10) * mm});
            skLineSegment(sketch, "E2635.563", {"start": v(-9.04, 2.7) * mm, "end": v(-8.99, 2.8) * mm});
            skLineSegment(sketch, "E2635.564", {"start": v(5.4, 7.14) * mm, "end": v(5.5, 7.05) * mm});
            skLineSegment(sketch, "E2635.565", {"start": v(0.7, -9.88) * mm, "end": v(0.6, -9.9) * mm});
            skLineSegment(sketch, "E2635.566", {"start": v(-7.31, -5.2) * mm, "end": v(-7.4, -5.1) * mm});
            skLineSegment(sketch, "E2635.567", {"start": v(7.05, -5.5) * mm, "end": v(6.96, -5.6) * mm});
            skLineSegment(sketch, "E2635.568", {"start": v(4.7, 7.72) * mm, "end": v(4.8, 7.64) * mm});
            skLineSegment(sketch, "E2635.570", {"start": v(-7.56, -4.9) * mm, "end": v(-7.64, -4.8) * mm});
            skLineSegment(sketch, "E2635.572", {"start": v(0.1, 10) * mm, "end": v(0.2, 9.98) * mm});
            skLineSegment(sketch, "E2635.573", {"start": v(5.3, -7.23) * mm, "end": v(5.2, -7.31) * mm});
            skLineSegment(sketch, "E2635.574", {"start": v(-6.5, -6.1) * mm, "end": v(-6.6, -6) * mm});
            skLineSegment(sketch, "E2635.575", {"start": v(-2.5, -9.15) * mm, "end": v(-2.6, -9.1) * mm});
            skLineSegment(sketch, "E2635.576", {"start": v(-2.6, 9.1) * mm, "end": v(-2.5, 9.15) * mm});
            skLineSegment(sketch, "E2635.577", {"start": v(-8.3, 3.9) * mm, "end": v(-8.23, 4) * mm});
            skLineSegment(sketch, "E2635.578", {"start": v(7.64, 4.8) * mm, "end": v(7.72, 4.7) * mm});
            skLineSegment(sketch, "E2635.579", {"start": v(-0.9, 9.82) * mm, "end": v(-0.8, 9.85) * mm});
            skLineSegment(sketch, "E2635.580", {"start": v(-7.4, 5.1) * mm, "end": v(-7.31, 5.2) * mm});
            skLineSegment(sketch, "E2635.581", {"start": v(-7.31, 5.2) * mm, "end": v(-7.23, 5.3) * mm});
            skLineSegment(sketch, "E2635.582", {"start": v(5.8, -6.78) * mm, "end": v(5.7, -6.87) * mm});
            skLineSegment(sketch, "E2635.584", {"start": v(-7.72, 4.7) * mm, "end": v(-7.64, 4.8) * mm});
            skLineSegment(sketch, "E2635.585", {"start": v(-1, 9.79) * mm, "end": v(-0.9, 9.82) * mm});
            skLineSegment(sketch, "E2635.587", {"start": v(6.2, -6.4) * mm, "end": v(6.1, -6.5) * mm});
            skLineSegment(sketch, "E2635.588", {"start": v(-9.44, -1.9) * mm, "end": v(-9.48, -1.8) * mm});
            skLineSegment(sketch, "E2635.589", {"start": v(-9.44, 1.9) * mm, "end": v(-9.4, 2) * mm});
            skLineSegment(sketch, "E2635.590", {"start": v(2, -9.4) * mm, "end": v(1.9, -9.44) * mm});
            skLineSegment(sketch, "E2635.591", {"start": v(-3.3, -8.7) * mm, "end": v(-3.4, -8.63) * mm});
            skLineSegment(sketch, "E2635.592", {"start": v(8.57, -3.5) * mm, "end": v(8.5, -3.6) * mm});
            skLineSegment(sketch, "E2635.593", {"start": v(8.7, -3.3) * mm, "end": v(8.63, -3.4) * mm});
            skLineSegment(sketch, "E2635.595", {"start": v(-5.1, 7.4) * mm, "end": v(-5, 7.48) * mm});
            skLineSegment(sketch, "E2635.596", {"start": v(-10, 0) * mm, "end": v(-10, 0.1) * mm});
            skLineSegment(sketch, "E2635.597", {"start": v(7.72, 4.7) * mm, "end": v(7.8, 4.6) * mm});
            skLineSegment(sketch, "E2635.598", {"start": v(3.1, 8.81) * mm, "end": v(3.2, 8.75) * mm});
            skLineSegment(sketch, "E2635.599", {"start": v(-5.6, -6.96) * mm, "end": v(-5.7, -6.87) * mm});
            skLineSegment(sketch, "E2635.600", {"start": v(1.8, -9.48) * mm, "end": v(1.7, -9.53) * mm});
            skLineSegment(sketch, "E2635.602", {"start": v(-4.2, -8.1) * mm, "end": v(-4.3, -8.02) * mm});
            skLineSegment(sketch, "E2635.603", {"start": v(-9.9, 0.6) * mm, "end": v(-9.88, 0.7) * mm});
            skLineSegment(sketch, "E2635.604", {"start": v(-9.35, -2.1) * mm, "end": v(-9.4, -2) * mm});
            skLineSegment(sketch, "E2635.605", {"start": v(9.4, -2) * mm, "end": v(9.35, -2.1) * mm});
            skLineSegment(sketch, "E2635.606", {"start": v(-7.14, -5.4) * mm, "end": v(-7.23, -5.3) * mm});
            skLineSegment(sketch, "E2635.607", {"start": v(-3.6, -8.5) * mm, "end": v(-3.7, -8.44) * mm});
            skLineSegment(sketch, "E2635.608", {"start": v(-4, -8.23) * mm, "end": v(-4.1, -8.16) * mm});
            skLineSegment(sketch, "E2635.609", {"start": v(8.81, 3.1) * mm, "end": v(8.87, 3) * mm});
            skLineSegment(sketch, "E2635.610", {"start": v(1.4, -9.65) * mm, "end": v(1.3, -9.69) * mm});
            skLineSegment(sketch, "E2635.614", {"start": v(5.6, -6.96) * mm, "end": v(5.5, -7.05) * mm});
            skLineSegment(sketch, "E2635.615", {"start": v(-9.25, 2.3) * mm, "end": v(-9.2, 2.4) * mm});
            skLineSegment(sketch, "E2635.616", {"start": v(-5.1, -7.4) * mm, "end": v(-5.2, -7.31) * mm});
            skLineSegment(sketch, "E2635.617", {"start": v(-1.1, -9.76) * mm, "end": v(-1.2, -9.72) * mm});
            skLineSegment(sketch, "E2635.618", {"start": v(-2.7, -9.04) * mm, "end": v(-2.8, -8.99) * mm});
            skLineSegment(sketch, "E2635.620", {"start": v(7.31, -5.2) * mm, "end": v(7.23, -5.3) * mm});
            skLineSegment(sketch, "E2635.621", {"start": v(6.1, -6.5) * mm, "end": v(6, -6.6) * mm});
            skLineSegment(sketch, "E2635.623", {"start": v(-3.4, -8.63) * mm, "end": v(-3.5, -8.57) * mm});
            skLineSegment(sketch, "E2635.624", {"start": v(2.2, -9.3) * mm, "end": v(2.1, -9.35) * mm});
            skLineSegment(sketch, "E2635.626", {"start": v(1.7, 9.53) * mm, "end": v(1.8, 9.48) * mm});
            skLineSegment(sketch, "E2635.627", {"start": v(-3, -8.87) * mm, "end": v(-3.1, -8.81) * mm});
            skLineSegment(sketch, "E2635.628", {"start": v(9.25, -2.3) * mm, "end": v(9.2, -2.4) * mm});
            skLineSegment(sketch, "E2635.629", {"start": v(2.3, 9.25) * mm, "end": v(2.4, 9.2) * mm});
            skLineSegment(sketch, "E2635.631", {"start": v(6.6, -6) * mm, "end": v(6.5, -6.1) * mm});
            skLineSegment(sketch, "E2635.632", {"start": v(8.93, 2.9) * mm, "end": v(8.99, 2.8) * mm});
            skLineSegment(sketch, "E2635.635", {"start": v(9.57, -1.6) * mm, "end": v(9.53, -1.7) * mm});
            skLineSegment(sketch, "E2635.637", {"start": v(3, 8.87) * mm, "end": v(3.1, 8.81) * mm});
            skLineSegment(sketch, "E2635.638", {"start": v(-0.5, 9.93) * mm, "end": v(-0.4, 9.95) * mm});
            skLineSegment(sketch, "E2635.639", {"start": v(7.94, 4.4) * mm, "end": v(8.02, 4.3) * mm});
            skLineSegment(sketch, "E2635.640", {"start": v(2.7, 9.04) * mm, "end": v(2.8, 8.99) * mm});
            skLineSegment(sketch, "E2635.642", {"start": v(-9.57, -1.6) * mm, "end": v(-9.6, -1.5) * mm});
            skLineSegment(sketch, "E2635.643", {"start": v(0, 10) * mm, "end": v(0.1, 10) * mm});
            skLineSegment(sketch, "E2635.645", {"start": v(9.6, -1.5) * mm, "end": v(9.57, -1.6) * mm});
            skLineSegment(sketch, "E2635.646", {"start": v(-9.15, 2.5) * mm, "end": v(-9.1, 2.6) * mm});
            skLineSegment(sketch, "E2635.647", {"start": v(3.5, 8.57) * mm, "end": v(3.6, 8.5) * mm});
            skLineSegment(sketch, "E2635.648", {"start": v(-4.9, -7.56) * mm, "end": v(-5, -7.48) * mm});
            skLineSegment(sketch, "E2635.650", {"start": v(-9.93, -0.5) * mm, "end": v(-9.95, -0.4) * mm});
            skLineSegment(sketch, "E2635.651", {"start": v(1.6, 9.57) * mm, "end": v(1.7, 9.53) * mm});
            skLineSegment(sketch, "E2635.653", {"start": v(4.5, 7.87) * mm, "end": v(4.6, 7.8) * mm});
            skLineSegment(sketch, "E2635.654", {"start": v(-8.02, 4.3) * mm, "end": v(-7.94, 4.4) * mm});
            skLineSegment(sketch, "E2635.655", {"start": v(-1.7, -9.53) * mm, "end": v(-1.8, -9.48) * mm});
            skLineSegment(sketch, "E2635.657", {"start": v(-1.8, -9.48) * mm, "end": v(-1.9, -9.44) * mm});
            skLineSegment(sketch, "E2635.658", {"start": v(-5.3, 7.23) * mm, "end": v(-5.2, 7.31) * mm});
            skLineSegment(sketch, "E2635.661", {"start": v(-9.69, -1.3) * mm, "end": v(-9.72, -1.2) * mm});
            skLineSegment(sketch, "E2635.662", {"start": v(-8.81, -3.1) * mm, "end": v(-8.87, -3) * mm});
            skLineSegment(sketch, "E2635.664", {"start": v(-2.1, -9.35) * mm, "end": v(-2.2, -9.3) * mm});
            skLineSegment(sketch, "E2635.665", {"start": v(-1.4, -9.65) * mm, "end": v(-1.5, -9.6) * mm});
            skLineSegment(sketch, "E2635.668", {"start": v(6.87, -5.7) * mm, "end": v(6.78, -5.8) * mm});
            skLineSegment(sketch, "E2635.669", {"start": v(1.5, -9.6) * mm, "end": v(1.4, -9.65) * mm});
            skLineSegment(sketch, "E2635.670", {"start": v(9.48, -1.8) * mm, "end": v(9.44, -1.9) * mm});
            skLineSegment(sketch, "E2635.673", {"start": v(-4.5, -7.87) * mm, "end": v(-4.6, -7.8) * mm});
            skLineSegment(sketch, "E2635.674", {"start": v(-8.16, 4.1) * mm, "end": v(-8.1, 4.2) * mm});
            skLineSegment(sketch, "E2635.675", {"start": v(10, 0) * mm, "end": v(10, -0.1) * mm});
            skLineSegment(sketch, "E2635.676", {"start": v(1.9, 9.44) * mm, "end": v(2, 9.4) * mm});
            skLineSegment(sketch, "E2635.677", {"start": v(-2.3, -9.25) * mm, "end": v(-2.4, -9.2) * mm});
            skLineSegment(sketch, "E2635.678", {"start": v(7.64, -4.8) * mm, "end": v(7.56, -4.9) * mm});
            skLineSegment(sketch, "E2635.680", {"start": v(1.2, 9.72) * mm, "end": v(1.3, 9.69) * mm});
            skLineSegment(sketch, "E2635.681", {"start": v(9.93, -0.5) * mm, "end": v(9.9, -0.6) * mm});
            skLineSegment(sketch, "E2635.683", {"start": v(0.3, 9.97) * mm, "end": v(0.4, 9.95) * mm});
            skLineSegment(sketch, "E2635.686", {"start": v(-9.95, 0.4) * mm, "end": v(-9.93, 0.5) * mm});
            skLineSegment(sketch, "E2635.687", {"start": v(7.72, -4.7) * mm, "end": v(7.64, -4.8) * mm});
            skLineSegment(sketch, "E2635.688", {"start": v(9.04, -2.7) * mm, "end": v(8.99, -2.8) * mm});
            skLineSegment(sketch, "E2635.691", {"start": v(0.5, -9.93) * mm, "end": v(0.4, -9.95) * mm});
            skLineSegment(sketch, "E2635.692", {"start": v(9.44, 1.9) * mm, "end": v(9.48, 1.8) * mm});
            skLineSegment(sketch, "E2635.693", {"start": v(5.9, 6.69) * mm, "end": v(6, 6.6) * mm});
            skLineSegment(sketch, "E2635.695", {"start": v(5.2, 7.31) * mm, "end": v(5.3, 7.23) * mm});
            skLineSegment(sketch, "E2635.696", {"start": v(-5.9, -6.69) * mm, "end": v(-6, -6.6) * mm});
            skLineSegment(sketch, "E2635.698", {"start": v(-8.44, 3.7) * mm, "end": v(-8.37, 3.8) * mm});
            skLineSegment(sketch, "E2635.699", {"start": v(-9.97, -0.3) * mm, "end": v(-9.98, -0.2) * mm});
            skLineSegment(sketch, "E2635.701", {"start": v(-0.7, 9.88) * mm, "end": v(-0.6, 9.9) * mm});
            skLineSegment(sketch, "E2635.702", {"start": v(2.5, 9.15) * mm, "end": v(2.6, 9.1) * mm});
            skLineSegment(sketch, "E2635.703", {"start": v(8.44, -3.7) * mm, "end": v(8.37, -3.8) * mm});
            skLineSegment(sketch, "E2635.705", {"start": v(8.75, -3.2) * mm, "end": v(8.7, -3.3) * mm});
            skLineSegment(sketch, "E2635.706", {"start": v(9.76, -1.1) * mm, "end": v(9.72, -1.2) * mm});
            skLineSegment(sketch, "E2635.707", {"start": v(0.2, -9.98) * mm, "end": v(0.1, -10) * mm});
            skLineSegment(sketch, "E2635.708", {"start": v(-9.72, -1.2) * mm, "end": v(-9.76, -1.1) * mm});
            skLineSegment(sketch, "E2635.709", {"start": v(8.75, 3.2) * mm, "end": v(8.81, 3.1) * mm});
            skLineSegment(sketch, "E2635.710", {"start": v(5.1, -7.4) * mm, "end": v(5, -7.48) * mm});
            skLineSegment(sketch, "E2635.711", {"start": v(1.1, -9.76) * mm, "end": v(1, -9.79) * mm});
            skLineSegment(sketch, "E2635.714", {"start": v(0, -10) * mm, "end": v(-0.1, -10) * mm});
            skLineSegment(sketch, "E2635.716", {"start": v(-7.8, -4.6) * mm, "end": v(-7.87, -4.5) * mm});
            skLineSegment(sketch, "E2635.717", {"start": v(-4.5, 7.87) * mm, "end": v(-4.4, 7.94) * mm});
            skLineSegment(sketch, "E2635.720", {"start": v(7.87, -4.5) * mm, "end": v(7.8, -4.6) * mm});
            skLineSegment(sketch, "E2635.721", {"start": v(-9.57, 1.6) * mm, "end": v(-9.53, 1.7) * mm});
            skLineSegment(sketch, "E2635.722", {"start": v(-1.3, 9.69) * mm, "end": v(-1.2, 9.72) * mm});
            skLineSegment(sketch, "E2635.723", {"start": v(-8.75, -3.2) * mm, "end": v(-8.81, -3.1) * mm});
            skLineSegment(sketch, "E2635.724", {"start": v(9.97, 0.3) * mm, "end": v(9.98, 0.2) * mm});
            skLineSegment(sketch, "E2635.725", {"start": v(7.4, 5.1) * mm, "end": v(7.48, 5) * mm});
            skLineSegment(sketch, "E2635.728", {"start": v(9.85, 0.8) * mm, "end": v(9.88, 0.7) * mm});
            skLineSegment(sketch, "E2635.729", {"start": v(-5.9, 6.69) * mm, "end": v(-5.8, 6.78) * mm});
            skLineSegment(sketch, "E2635.730", {"start": v(-5.5, 7.05) * mm, "end": v(-5.4, 7.14) * mm});
            skLineSegment(sketch, "E2635.731", {"start": v(9.4, 2) * mm, "end": v(9.44, 1.9) * mm});
            skLineSegment(sketch, "E2635.733", {"start": v(-9.97, 0.3) * mm, "end": v(-9.95, 0.4) * mm});
            skLineSegment(sketch, "E2635.735", {"start": v(-5.7, 6.87) * mm, "end": v(-5.6, 6.96) * mm});
            skLineSegment(sketch, "E2635.736", {"start": v(9.85, -0.8) * mm, "end": v(9.82, -0.9) * mm});
            skLineSegment(sketch, "E2635.737", {"start": v(6.3, -6.3) * mm, "end": v(6.2, -6.4) * mm});
            skLineSegment(sketch, "E2635.738", {"start": v(7.94, -4.4) * mm, "end": v(7.87, -4.5) * mm});
            skLineSegment(sketch, "E2635.740", {"start": v(8.1, -4.2) * mm, "end": v(8.02, -4.3) * mm});
            skLineSegment(sketch, "E2635.741", {"start": v(-5.4, 7.14) * mm, "end": v(-5.3, 7.23) * mm});
            skLineSegment(sketch, "E2635.743", {"start": v(7.31, 5.2) * mm, "end": v(7.4, 5.1) * mm});
            skLineSegment(sketch, "E2635.744", {"start": v(9.72, 1.2) * mm, "end": v(9.76, 1.1) * mm});
            skLineSegment(sketch, "E2635.745", {"start": v(-9.2, -2.4) * mm, "end": v(-9.25, -2.3) * mm});
            skLineSegment(sketch, "E2635.746", {"start": v(1.2, -9.72) * mm, "end": v(1.1, -9.76) * mm});
            skLineSegment(sketch, "E2635.747", {"start": v(9.2, 2.4) * mm, "end": v(9.25, 2.3) * mm});
            skLineSegment(sketch, "E2635.748", {"start": v(-0.2, -9.98) * mm, "end": v(-0.3, -9.97) * mm});
            skLineSegment(sketch, "E2635.750", {"start": v(-8.7, -3.3) * mm, "end": v(-8.75, -3.2) * mm});
            skLineSegment(sketch, "E2635.751", {"start": v(-10, -0.1) * mm, "end": v(-10, 0) * mm});
            skLineSegment(sketch, "E2635.752", {"start": v(1.4, 9.65) * mm, "end": v(1.5, 9.6) * mm});
            skLineSegment(sketch, "E2635.753", {"start": v(-0.4, -9.95) * mm, "end": v(-0.5, -9.93) * mm});
            skLineSegment(sketch, "E2635.755", {"start": v(-0.8, -9.85) * mm, "end": v(-0.9, -9.82) * mm});
            skLineSegment(sketch, "E2635.756", {"start": v(2.9, 8.93) * mm, "end": v(3, 8.87) * mm});
            skLineSegment(sketch, "E2635.759", {"start": v(1.8, 9.48) * mm, "end": v(1.9, 9.44) * mm});
            skLineSegment(sketch, "E2635.760", {"start": v(2.2, 9.3) * mm, "end": v(2.3, 9.25) * mm});
            skLineSegment(sketch, "E2635.762", {"start": v(-8.44, -3.7) * mm, "end": v(-8.5, -3.6) * mm});
            skLineSegment(sketch, "E2635.763", {"start": v(9.65, 1.4) * mm, "end": v(9.69, 1.3) * mm});
            skLineSegment(sketch, "E2635.766", {"start": v(2.3, -9.25) * mm, "end": v(2.2, -9.3) * mm});
            skLineSegment(sketch, "E2635.767", {"start": v(1.5, 9.6) * mm, "end": v(1.6, 9.57) * mm});
            skLineSegment(sketch, "E2635.771", {"start": v(-1, -9.79) * mm, "end": v(-1.1, -9.76) * mm});
            skLineSegment(sketch, "E2635.772", {"start": v(-0.5, -9.93) * mm, "end": v(-0.6, -9.9) * mm});
            skLineSegment(sketch, "E2635.775", {"start": v(7.56, 4.9) * mm, "end": v(7.64, 4.8) * mm});
            skLineSegment(sketch, "E2635.777", {"start": v(-1.5, 9.6) * mm, "end": v(-1.4, 9.65) * mm});
            skLineSegment(sketch, "E2635.781", {"start": v(-1.3, -9.69) * mm, "end": v(-1.4, -9.65) * mm});
            skLineSegment(sketch, "E2635.782", {"start": v(-8.1, -4.2) * mm, "end": v(-8.16, -4.1) * mm});
            skLineSegment(sketch, "E2635.783", {"start": v(8.23, -4) * mm, "end": v(8.16, -4.1) * mm});
            skLineSegment(sketch, "E2635.784", {"start": v(-9.93, 0.5) * mm, "end": v(-9.9, 0.6) * mm});
            skLineSegment(sketch, "E2635.785", {"start": v(-6.96, -5.6) * mm, "end": v(-7.05, -5.5) * mm});
            skLineSegment(sketch, "E2635.786", {"start": v(8.3, -3.9) * mm, "end": v(8.23, -4) * mm});
            skLineSegment(sketch, "E2635.787", {"start": v(9.1, 2.6) * mm, "end": v(9.15, 2.5) * mm});
            skLineSegment(sketch, "E2635.788", {"start": v(9.88, 0.7) * mm, "end": v(9.9, 0.6) * mm});
            skLineSegment(sketch, "E2635.790", {"start": v(-2.7, 9.04) * mm, "end": v(-2.6, 9.1) * mm});
            skLineSegment(sketch, "E2635.791", {"start": v(-9.3, -2.2) * mm, "end": v(-9.35, -2.1) * mm});
            skLineSegment(sketch, "E2635.792", {"start": v(9.6, 1.5) * mm, "end": v(9.65, 1.4) * mm});
            skLineSegment(sketch, "E2635.793", {"start": v(9.57, 1.6) * mm, "end": v(9.6, 1.5) * mm});
            skLineSegment(sketch, "E2635.795", {"start": v(-1.7, 9.53) * mm, "end": v(-1.6, 9.57) * mm});
            skLineSegment(sketch, "E2635.796", {"start": v(-8.57, -3.5) * mm, "end": v(-8.63, -3.4) * mm});
            skLineSegment(sketch, "E2635.797", {"start": v(-9.6, 1.5) * mm, "end": v(-9.57, 1.6) * mm});
            skLineSegment(sketch, "E2635.798", {"start": v(-9.9, -0.6) * mm, "end": v(-9.93, -0.5) * mm});
            skLineSegment(sketch, "E2635.799", {"start": v(-1.9, 9.44) * mm, "end": v(-1.8, 9.48) * mm});
            skLineSegment(sketch, "E2635.800", {"start": v(9.3, 2.2) * mm, "end": v(9.35, 2.1) * mm});
            skLineSegment(sketch, "E2635.801", {"start": v(-7.05, -5.5) * mm, "end": v(-7.14, -5.4) * mm});
            skLineSegment(sketch, "E2635.802", {"start": v(10, 0.1) * mm, "end": v(10, 0) * mm});
            skLineSegment(sketch, "E2635.803", {"start": v(-9.65, 1.4) * mm, "end": v(-9.6, 1.5) * mm});
            skLineSegment(sketch, "E2635.806", {"start": v(8.7, 3.3) * mm, "end": v(8.75, 3.2) * mm});
            skLineSegment(sketch, "E2635.810", {"start": v(-8.3, -3.9) * mm, "end": v(-8.37, -3.8) * mm});
            skLineSegment(sketch, "E2635.811", {"start": v(9.15, 2.5) * mm, "end": v(9.2, 2.4) * mm});
            skLineSegment(sketch, "E2635.812", {"start": v(7.23, 5.3) * mm, "end": v(7.31, 5.2) * mm});
            skLineSegment(sketch, "E2635.814", {"start": v(6.87, 5.7) * mm, "end": v(6.96, 5.6) * mm});
            skLineSegment(sketch, "E2635.815", {"start": v(-8.16, -4.1) * mm, "end": v(-8.23, -4) * mm});
            skLineSegment(sketch, "E2635.816", {"start": v(-6.78, -5.8) * mm, "end": v(-6.87, -5.7) * mm});
            skLineSegment(sketch, "E2635.817", {"start": v(-6.6, -6) * mm, "end": v(-6.69, -5.9) * mm});
            skLineSegment(sketch, "E2635.821", {"start": v(-9.1, -2.6) * mm, "end": v(-9.15, -2.5) * mm});
            skLineSegment(sketch, "E2635.823", {"start": v(9.82, 0.9) * mm, "end": v(9.85, 0.8) * mm});
            skLineSegment(sketch, "E2635.824", {"start": v(-9.72, 1.2) * mm, "end": v(-9.69, 1.3) * mm});
            skLineSegment(sketch, "E2635.825", {"start": v(9.93, 0.5) * mm, "end": v(9.95, 0.4) * mm});
            skLineSegment(sketch, "E2635.827", {"start": v(-9.79, 1) * mm, "end": v(-9.76, 1.1) * mm});
            skLineSegment(sketch, "E2635.828", {"start": v(-4.9, 7.56) * mm, "end": v(-4.8, 7.64) * mm});
            skLineSegment(sketch, "E2635.829", {"start": v(-8.99, -2.8) * mm, "end": v(-9.04, -2.7) * mm});
            skLineSegment(sketch, "E2635.830", {"start": v(8.81, -3.1) * mm, "end": v(8.75, -3.2) * mm});
            skLineSegment(sketch, "E2635.831", {"start": v(-9.53, -1.7) * mm, "end": v(-9.57, -1.6) * mm});
            skLineSegment(sketch, "E2635.832", {"start": v(8.57, 3.5) * mm, "end": v(8.63, 3.4) * mm});
            skLineSegment(sketch, "E2635.833", {"start": v(-1.1, 9.76) * mm, "end": v(-1, 9.79) * mm});
            skLineSegment(sketch, "E2635.836", {"start": v(7.05, 5.5) * mm, "end": v(7.14, 5.4) * mm});
            skLineSegment(sketch, "E2635.838", {"start": v(-4.7, 7.72) * mm, "end": v(-4.6, 7.8) * mm});
            skLineSegment(sketch, "E2635.839", {"start": v(-0.7, -9.88) * mm, "end": v(-0.8, -9.85) * mm});
            skLineSegment(sketch, "E2635.840", {"start": v(1.1, 9.76) * mm, "end": v(1.2, 9.72) * mm});
            skLineSegment(sketch, "E2635.847", {"start": v(-7.72, -4.7) * mm, "end": v(-7.8, -4.6) * mm});
            skLineSegment(sketch, "E2635.848", {"start": v(-1.4, 9.65) * mm, "end": v(-1.3, 9.69) * mm});
            skLineSegment(sketch, "E2635.849", {"start": v(-4.6, 7.8) * mm, "end": v(-4.5, 7.87) * mm});
            skLineSegment(sketch, "E2635.852", {"start": v(-8.5, -3.6) * mm, "end": v(-8.57, -3.5) * mm});
            skLineSegment(sketch, "E2635.855", {"start": v(9.35, 2.1) * mm, "end": v(9.4, 2) * mm});
            skLineSegment(sketch, "E2635.857", {"start": v(-0.3, -9.97) * mm, "end": v(-0.4, -9.95) * mm});
            skLineSegment(sketch, "E2635.858", {"start": v(-9.76, 1.1) * mm, "end": v(-9.72, 1.2) * mm});
            skLineSegment(sketch, "E2635.859", {"start": v(-0.1, -10) * mm, "end": v(-0.2, -9.98) * mm});
            skLineSegment(sketch, "E2635.860", {"start": v(-5.8, 6.78) * mm, "end": v(-5.7, 6.87) * mm});
            skLineSegment(sketch, "E2635.862", {"start": v(-0.9, -9.82) * mm, "end": v(-1, -9.79) * mm});
            skLineSegment(sketch, "E2635.865", {"start": v(8.02, -4.3) * mm, "end": v(7.94, -4.4) * mm});
            skLineSegment(sketch, "E2635.867", {"start": v(1, 9.79) * mm, "end": v(1.1, 9.76) * mm});
            skLineSegment(sketch, "E2635.868", {"start": v(-8.02, -4.3) * mm, "end": v(-8.1, -4.2) * mm});
            skLineSegment(sketch, "E2635.872", {"start": v(6.96, 5.6) * mm, "end": v(7.05, 5.5) * mm});
            skLineSegment(sketch, "E2635.875", {"start": v(-6.87, -5.7) * mm, "end": v(-6.96, -5.6) * mm});
            skLineSegment(sketch, "E2635.877", {"start": v(9.69, 1.3) * mm, "end": v(9.72, 1.2) * mm});
            skLineSegment(sketch, "E2635.878", {"start": v(9.9, 0.6) * mm, "end": v(9.93, 0.5) * mm});
            skLineSegment(sketch, "E2635.882", {"start": v(8.16, -4.1) * mm, "end": v(8.1, -4.2) * mm});
            skLineSegment(sketch, "E2635.884", {"start": v(7.14, 5.4) * mm, "end": v(7.23, 5.3) * mm});
            skLineSegment(sketch, "E2635.886", {"start": v(9.79, 1) * mm, "end": v(9.82, 0.9) * mm});
            skLineSegment(sketch, "E2635.887", {"start": v(-7.94, -4.4) * mm, "end": v(-8.02, -4.3) * mm});
            skLineSegment(sketch, "E2635.893", {"start": v(9.25, 2.3) * mm, "end": v(9.3, 2.2) * mm});
            skLineSegment(sketch, "E2635.894", {"start": v(-8.23, -4) * mm, "end": v(-8.3, -3.9) * mm});
            skLineSegment(sketch, "E2635.895", {"start": v(-8.93, -2.9) * mm, "end": v(-8.99, -2.8) * mm});
            skLineSegment(sketch, "E2635.897", {"start": v(-9.82, 0.9) * mm, "end": v(-9.79, 1) * mm});
            skLineSegment(sketch, "E2635.898", {"start": v(-1.6, 9.57) * mm, "end": v(-1.5, 9.6) * mm});
            skLineSegment(sketch, "E2635.899", {"start": v(-9.15, -2.5) * mm, "end": v(-9.2, -2.4) * mm});
            skLineSegment(sketch, "E2635.900", {"start": v(-0.6, -9.9) * mm, "end": v(-0.7, -9.88) * mm});
            skLineSegment(sketch, "E2635.901", {"start": v(9.95, 0.4) * mm, "end": v(9.97, 0.3) * mm});
            skLineSegment(sketch, "E2635.902", {"start": v(-6.69, -5.9) * mm, "end": v(-6.78, -5.8) * mm});
            skLineSegment(sketch, "E2635.904", {"start": v(-9.69, 1.3) * mm, "end": v(-9.65, 1.4) * mm});
            skLineSegment(sketch, "E2635.906", {"start": v(-9.04, -2.7) * mm, "end": v(-9.1, -2.6) * mm});
            skLineSegment(sketch, "E2635.907", {"start": v(-8.37, -3.8) * mm, "end": v(-8.44, -3.7) * mm});
            skLineSegment(sketch, "E2635.908", {"start": v(-4.8, 7.64) * mm, "end": v(-4.7, 7.72) * mm});
            skLineSegment(sketch, "E2635.909", {"start": v(9.04, 2.7) * mm, "end": v(9.1, 2.6) * mm});
            skLineSegment(sketch, "E2635.911", {"start": v(-5.6, 6.96) * mm, "end": v(-5.5, 7.05) * mm});
            skLineSegment(sketch, "E2635.914", {"start": v(-2, 9.4) * mm, "end": v(-1.9, 9.44) * mm});
            skLineSegment(sketch, "E2635.916", {"start": v(-9.25, -2.3) * mm, "end": v(-9.3, -2.2) * mm});
            skLineSegment(sketch, "E2635.917", {"start": v(9.53, 1.7) * mm, "end": v(9.57, 1.6) * mm});
            skLineSegment(sketch, "E2635.918", {"start": v(-1.8, 9.48) * mm, "end": v(-1.7, 9.53) * mm});
            skLineSegment(sketch, "E2635.919", {"start": v(-8.63, -3.4) * mm, "end": v(-8.7, -3.3) * mm});
            skLineSegment(sketch, "E2635.923", {"start": v(1.3, 9.69) * mm, "end": v(1.4, 9.65) * mm});
            skLineSegment(sketch, "E2635.931", {"start": v(8.5, 3.6) * mm, "end": v(8.57, 3.5) * mm});
            skLineSegment(sketch, "E2635.932", {"start": v(4.8, -7.64) * mm, "end": v(4.7, -7.72) * mm});
            skLineSegment(sketch, "E2635.933", {"start": v(3.2, -8.75) * mm, "end": v(3.1, -8.81) * mm});
            skLineSegment(sketch, "E2635.934", {"start": v(-4.4, 7.94) * mm, "end": v(-4.3, 8.02) * mm});
            skLineSegment(sketch, "E2635.935", {"start": v(-3, 8.87) * mm, "end": v(-2.9, 8.93) * mm});
            skLineSegment(sketch, "E2635.936", {"start": v(8.3, 3.9) * mm, "end": v(8.37, 3.8) * mm});
            skLineSegment(sketch, "E2635.940", {"start": v(4.5, -7.87) * mm, "end": v(4.4, -7.94) * mm});
            skLineSegment(sketch, "E2635.941", {"start": v(8.16, 4.1) * mm, "end": v(8.23, 4) * mm});
            skLineSegment(sketch, "E2635.947", {"start": v(8.44, 3.7) * mm, "end": v(8.5, 3.6) * mm});
            skLineSegment(sketch, "E2635.951", {"start": v(3.3, -8.7) * mm, "end": v(3.2, -8.75) * mm});
            skLineSegment(sketch, "E2635.955", {"start": v(2.5, -9.15) * mm, "end": v(2.4, -9.2) * mm});
            skLineSegment(sketch, "E2635.956", {"start": v(-4, 8.23) * mm, "end": v(-3.9, 8.3) * mm});
            skLineSegment(sketch, "E2635.958", {"start": v(2.4, -9.2) * mm, "end": v(2.3, -9.25) * mm});
            skLineSegment(sketch, "E2635.959", {"start": v(3.8, -8.37) * mm, "end": v(3.7, -8.44) * mm});
            skLineSegment(sketch, "E2635.961", {"start": v(4.2, -8.1) * mm, "end": v(4.1, -8.16) * mm});
            skLineSegment(sketch, "E2635.962", {"start": v(-4.2, 8.1) * mm, "end": v(-4.1, 8.16) * mm});
            skLineSegment(sketch, "E2635.964", {"start": v(2.7, -9.04) * mm, "end": v(2.6, -9.1) * mm});
            skLineSegment(sketch, "E2635.965", {"start": v(9.76, 1.1) * mm, "end": v(9.79, 1) * mm});
            skLineSegment(sketch, "E2635.966", {"start": v(-3.8, 8.37) * mm, "end": v(-3.7, 8.44) * mm});
            skLineSegment(sketch, "E2635.967", {"start": v(4, -8.23) * mm, "end": v(3.9, -8.3) * mm});
            skLineSegment(sketch, "E2635.968", {"start": v(3.4, -8.63) * mm, "end": v(3.3, -8.7) * mm});
            skLineSegment(sketch, "E2635.969", {"start": v(-7.87, -4.5) * mm, "end": v(-7.94, -4.4) * mm});
            skLineSegment(sketch, "E2635.970", {"start": v(4.4, -7.94) * mm, "end": v(4.3, -8.02) * mm});
            skLineSegment(sketch, "E2635.971", {"start": v(2.9, -8.93) * mm, "end": v(2.8, -8.99) * mm});
            skLineSegment(sketch, "E2635.972", {"start": v(3.6, -8.5) * mm, "end": v(3.5, -8.57) * mm});
            skLineSegment(sketch, "E2635.973", {"start": v(-9.85, 0.8) * mm, "end": v(-9.82, 0.9) * mm});
            skLineSegment(sketch, "E2635.975", {"start": v(8.23, 4) * mm, "end": v(8.3, 3.9) * mm});
            skLineSegment(sketch, "E2635.976", {"start": v(4.7, -7.72) * mm, "end": v(4.6, -7.8) * mm});
            skLineSegment(sketch, "E2635.977", {"start": v(-3.1, 8.81) * mm, "end": v(-3, 8.87) * mm});
            skLineSegment(sketch, "E2635.978", {"start": v(-4.3, 8.02) * mm, "end": v(-4.2, 8.1) * mm});
            skLineSegment(sketch, "E2635.979", {"start": v(3.7, -8.44) * mm, "end": v(3.6, -8.5) * mm});
            skLineSegment(sketch, "E2635.980", {"start": v(8.37, 3.8) * mm, "end": v(8.44, 3.7) * mm});
            skLineSegment(sketch, "E2635.981", {"start": v(4.1, -8.16) * mm, "end": v(4, -8.23) * mm});
            skLineSegment(sketch, "E2635.982", {"start": v(3, -8.87) * mm, "end": v(2.9, -8.93) * mm});
            skLineSegment(sketch, "E2635.983", {"start": v(8.1, 4.2) * mm, "end": v(8.16, 4.1) * mm});
            skLineSegment(sketch, "E2635.984", {"start": v(2.8, -8.99) * mm, "end": v(2.7, -9.04) * mm});
            skLineSegment(sketch, "E2635.988", {"start": v(4.3, -8.02) * mm, "end": v(4.2, -8.1) * mm});
            skLineSegment(sketch, "E2635.989", {"start": v(4.6, -7.8) * mm, "end": v(4.5, -7.87) * mm});
            skLineSegment(sketch, "E2635.990", {"start": v(-4.1, 8.16) * mm, "end": v(-4, 8.23) * mm});
            skLineSegment(sketch, "E2635.991", {"start": v(2.6, -9.1) * mm, "end": v(2.5, -9.15) * mm});
            skLineSegment(sketch, "E2635.992", {"start": v(-3.9, 8.3) * mm, "end": v(-3.8, 8.37) * mm});
            skLineSegment(sketch, "E2635.994", {"start": v(3.9, -8.3) * mm, "end": v(3.8, -8.37) * mm});
            skLineSegment(sketch, "E2635.995", {"start": v(3.1, -8.81) * mm, "end": v(3, -8.87) * mm});
            skLineSegment(sketch, "E2635.998", {"start": v(3.5, -8.57) * mm, "end": v(3.4, -8.63) * mm});
            skLineSegment(sketch, "E2635.1000", {"start": v(-3.4, 8.63) * mm, "end": v(-3.3, 8.7) * mm});
            skLineSegment(sketch, "E2635.1001", {"start": v(-3.2, 8.75) * mm, "end": v(-3.1, 8.81) * mm});
            skLineSegment(sketch, "E2635.1003", {"start": v(-3.6, 8.5) * mm, "end": v(-3.5, 8.57) * mm});
            skLineSegment(sketch, "E2635.1005", {"start": v(-3.5, 8.57) * mm, "end": v(-3.4, 8.63) * mm});
            skLineSegment(sketch, "E2635.1006", {"start": v(-3.7, 8.44) * mm, "end": v(-3.6, 8.5) * mm});
            skLineSegment(sketch, "E2635.1007", {"start": v(-3.3, 8.7) * mm, "end": v(-3.2, 8.75) * mm});
            skPoint(sketch, "E2636.0", {"position": v(0, 0) * mm});
            skLineSegment(sketch, "E2637.0", {"start": v(3.23, -9.03) * mm, "end": v(3.13, -9.09) * mm});
            skLineSegment(sketch, "E2637.1", {"start": v(3.33, -8.97) * mm, "end": v(3.23, -9.03) * mm});
            skLineSegment(sketch, "E2637.2", {"start": v(3.43, -8.9) * mm, "end": v(3.33, -8.97) * mm});
            skLineSegment(sketch, "E2637.3", {"start": v(3.53, -8.84) * mm, "end": v(3.43, -8.9) * mm});
            skLineSegment(sketch, "E2637.4", {"start": v(3.63, -8.78) * mm, "end": v(3.53, -8.84) * mm});
            skLineSegment(sketch, "E2637.5", {"start": v(3.74, -8.71) * mm, "end": v(3.63, -8.78) * mm});
            skLineSegment(sketch, "E2637.6", {"start": v(3.84, -8.65) * mm, "end": v(3.74, -8.71) * mm});
            skLineSegment(sketch, "E2637.7", {"start": v(3.94, -8.58) * mm, "end": v(3.84, -8.65) * mm});
            skLineSegment(sketch, "E2637.8", {"start": v(4.04, -8.5) * mm, "end": v(3.94, -8.58) * mm});
            skLineSegment(sketch, "E2637.9", {"start": v(4.14, -8.44) * mm, "end": v(4.04, -8.5) * mm});
            skLineSegment(sketch, "E2637.10", {"start": v(4.24, -8.37) * mm, "end": v(4.14, -8.44) * mm});
            skLineSegment(sketch, "E2637.11", {"start": v(4.35, -8.3) * mm, "end": v(4.24, -8.37) * mm});
            skLineSegment(sketch, "E2637.12", {"start": v(4.45, -8.22) * mm, "end": v(4.35, -8.3) * mm});
            skLineSegment(sketch, "E2637.13", {"start": v(4.55, -8.15) * mm, "end": v(4.45, -8.22) * mm});
            skLineSegment(sketch, "E2637.14", {"start": v(4.65, -8.07) * mm, "end": v(4.55, -8.15) * mm});
            skLineSegment(sketch, "E2637.15", {"start": v(4.75, -8) * mm, "end": v(4.65, -8.07) * mm});
            skLineSegment(sketch, "E2637.16", {"start": v(4.85, -7.91) * mm, "end": v(4.75, -8) * mm});
            skLineSegment(sketch, "E2637.17", {"start": v(4.96, -7.83) * mm, "end": v(4.85, -7.91) * mm});
            skLineSegment(sketch, "E2637.18", {"start": v(5.06, -7.75) * mm, "end": v(4.96, -7.83) * mm});
            skLineSegment(sketch, "E2637.19", {"start": v(5.16, -7.67) * mm, "end": v(5.06, -7.75) * mm});
            skLineSegment(sketch, "E2637.20", {"start": v(5.26, -7.59) * mm, "end": v(5.16, -7.67) * mm});
            skLineSegment(sketch, "E2637.21", {"start": v(5.36, -7.5) * mm, "end": v(5.26, -7.59) * mm});
            skLineSegment(sketch, "E2637.22", {"start": v(5.46, -7.42) * mm, "end": v(5.36, -7.5) * mm});
            skLineSegment(sketch, "E2637.23", {"start": v(5.56, -7.33) * mm, "end": v(5.46, -7.42) * mm});
            skLineSegment(sketch, "E2637.24", {"start": v(5.67, -7.24) * mm, "end": v(5.56, -7.33) * mm});
            skLineSegment(sketch, "E2637.25", {"start": v(5.77, -7.15) * mm, "end": v(5.67, -7.24) * mm});
            skLineSegment(sketch, "E2637.26", {"start": v(5.87, -7.06) * mm, "end": v(5.77, -7.15) * mm});
            skLineSegment(sketch, "E2637.27", {"start": v(5.97, -6.96) * mm, "end": v(5.87, -7.06) * mm});
            skLineSegment(sketch, "E2637.28", {"start": v(6.07, -6.87) * mm, "end": v(5.97, -6.96) * mm});
            skLineSegment(sketch, "E2637.29", {"start": v(6.17, -6.77) * mm, "end": v(6.07, -6.87) * mm});
            skLineSegment(sketch, "E2637.30", {"start": v(6.27, -6.68) * mm, "end": v(6.17, -6.77) * mm});
            skLineSegment(sketch, "E2637.31", {"start": v(6.38, -6.58) * mm, "end": v(6.27, -6.68) * mm});
            skLineSegment(sketch, "E2637.32", {"start": v(6.48, -6.48) * mm, "end": v(6.38, -6.58) * mm});
            skLineSegment(sketch, "E2637.33", {"start": v(6.58, -6.38) * mm, "end": v(6.48, -6.48) * mm});
            skLineSegment(sketch, "E2637.34", {"start": v(6.68, -6.27) * mm, "end": v(6.58, -6.38) * mm});
            skLineSegment(sketch, "E2637.35", {"start": v(6.77, -6.17) * mm, "end": v(6.68, -6.27) * mm});
            skLineSegment(sketch, "E2637.36", {"start": v(6.87, -6.07) * mm, "end": v(6.77, -6.17) * mm});
            skLineSegment(sketch, "E2637.37", {"start": v(6.96, -5.97) * mm, "end": v(6.87, -6.07) * mm});
            skLineSegment(sketch, "E2637.38", {"start": v(7.06, -5.87) * mm, "end": v(6.96, -5.97) * mm});
            skLineSegment(sketch, "E2637.39", {"start": v(7.15, -5.77) * mm, "end": v(7.06, -5.87) * mm});
            skLineSegment(sketch, "E2637.40", {"start": v(7.24, -5.67) * mm, "end": v(7.15, -5.77) * mm});
            skLineSegment(sketch, "E2637.41", {"start": v(7.33, -5.56) * mm, "end": v(7.24, -5.67) * mm});
            skLineSegment(sketch, "E2637.42", {"start": v(7.42, -5.46) * mm, "end": v(7.33, -5.56) * mm});
            skLineSegment(sketch, "E2637.43", {"start": v(7.5, -5.36) * mm, "end": v(7.42, -5.46) * mm});
            skLineSegment(sketch, "E2637.44", {"start": v(7.59, -5.26) * mm, "end": v(7.5, -5.36) * mm});
            skLineSegment(sketch, "E2637.45", {"start": v(7.67, -5.16) * mm, "end": v(7.59, -5.26) * mm});
            skLineSegment(sketch, "E2637.46", {"start": v(7.75, -5.06) * mm, "end": v(7.67, -5.16) * mm});
            skLineSegment(sketch, "E2637.47", {"start": v(7.83, -4.96) * mm, "end": v(7.75, -5.06) * mm});
            skLineSegment(sketch, "E2637.48", {"start": v(7.91, -4.85) * mm, "end": v(7.83, -4.96) * mm});
            skLineSegment(sketch, "E2637.49", {"start": v(8, -4.75) * mm, "end": v(7.91, -4.85) * mm});
            skLineSegment(sketch, "E2637.50", {"start": v(8.07, -4.65) * mm, "end": v(8, -4.75) * mm});
            skLineSegment(sketch, "E2637.51", {"start": v(8.15, -4.55) * mm, "end": v(8.07, -4.65) * mm});
            skLineSegment(sketch, "E2637.52", {"start": v(8.22, -4.45) * mm, "end": v(8.15, -4.55) * mm});
            skLineSegment(sketch, "E2637.53", {"start": v(8.3, -4.35) * mm, "end": v(8.22, -4.45) * mm});
            skLineSegment(sketch, "E2637.54", {"start": v(8.37, -4.24) * mm, "end": v(8.3, -4.35) * mm});
            skLineSegment(sketch, "E2637.55", {"start": v(8.44, -4.14) * mm, "end": v(8.37, -4.24) * mm});
            skLineSegment(sketch, "E2637.56", {"start": v(8.5, -4.04) * mm, "end": v(8.44, -4.14) * mm});
            skLineSegment(sketch, "E2637.57", {"start": v(8.58, -3.94) * mm, "end": v(8.5, -4.04) * mm});
            skLineSegment(sketch, "E2637.58", {"start": v(8.65, -3.84) * mm, "end": v(8.58, -3.94) * mm});
            skLineSegment(sketch, "E2637.59", {"start": v(8.71, -3.74) * mm, "end": v(8.65, -3.84) * mm});
            skLineSegment(sketch, "E2637.60", {"start": v(8.78, -3.63) * mm, "end": v(8.71, -3.74) * mm});
            skLineSegment(sketch, "E2637.61", {"start": v(8.84, -3.53) * mm, "end": v(8.78, -3.63) * mm});
            skLineSegment(sketch, "E2637.62", {"start": v(8.9, -3.43) * mm, "end": v(8.84, -3.53) * mm});
            skLineSegment(sketch, "E2637.63", {"start": v(8.97, -3.33) * mm, "end": v(8.9, -3.43) * mm});
            skLineSegment(sketch, "E2637.64", {"start": v(9.03, -3.23) * mm, "end": v(8.97, -3.33) * mm});
            skLineSegment(sketch, "E2637.65", {"start": v(9.09, -3.13) * mm, "end": v(9.03, -3.23) * mm});
            skLineSegment(sketch, "E2637.66", {"start": v(9.15, -3.02) * mm, "end": v(9.09, -3.13) * mm});
            skLineSegment(sketch, "E2637.67", {"start": v(9.2, -2.92) * mm, "end": v(9.15, -3.02) * mm});
            skLineSegment(sketch, "E2637.68", {"start": v(9.26, -2.82) * mm, "end": v(9.2, -2.92) * mm});
            skLineSegment(sketch, "E2637.69", {"start": v(9.32, -2.72) * mm, "end": v(9.26, -2.82) * mm});
            skLineSegment(sketch, "E2637.70", {"start": v(9.37, -2.62) * mm, "end": v(9.32, -2.72) * mm});
            skLineSegment(sketch, "E2637.71", {"start": v(9.42, -2.51) * mm, "end": v(9.37, -2.62) * mm});
            skLineSegment(sketch, "E2637.72", {"start": v(9.47, -2.41) * mm, "end": v(9.42, -2.51) * mm});
            skLineSegment(sketch, "E2637.73", {"start": v(9.52, -2.3) * mm, "end": v(9.47, -2.41) * mm});
            skLineSegment(sketch, "E2637.74", {"start": v(9.57, -2.2) * mm, "end": v(9.52, -2.3) * mm});
            skLineSegment(sketch, "E2637.75", {"start": v(9.62, -2.1) * mm, "end": v(9.57, -2.2) * mm});
            skLineSegment(sketch, "E2637.76", {"start": v(9.67, -2) * mm, "end": v(9.62, -2.1) * mm});
            skLineSegment(sketch, "E2637.77", {"start": v(9.71, -1.9) * mm, "end": v(9.67, -2) * mm});
            skLineSegment(sketch, "E2637.78", {"start": v(9.76, -1.8) * mm, "end": v(9.71, -1.9) * mm});
            skLineSegment(sketch, "E2637.79", {"start": v(9.8, -1.7) * mm, "end": v(9.76, -1.8) * mm});
            skLineSegment(sketch, "E2637.80", {"start": v(9.84, -1.6) * mm, "end": v(9.8, -1.7) * mm});
            skLineSegment(sketch, "E2637.81", {"start": v(9.88, -1.49) * mm, "end": v(9.84, -1.6) * mm});
            skLineSegment(sketch, "E2637.82", {"start": v(9.92, -1.39) * mm, "end": v(9.88, -1.49) * mm});
            skLineSegment(sketch, "E2637.83", {"start": v(9.96, -1.28) * mm, "end": v(9.92, -1.39) * mm});
            skLineSegment(sketch, "E2637.84", {"start": v(10, -1.18) * mm, "end": v(9.96, -1.28) * mm});
            skLineSegment(sketch, "E2637.85", {"start": v(10.03, -1.08) * mm, "end": v(10, -1.18) * mm});
            skLineSegment(sketch, "E2637.86", {"start": v(10.06, -0.97) * mm, "end": v(10.03, -1.08) * mm});
            skLineSegment(sketch, "E2637.87", {"start": v(10.09, -0.87) * mm, "end": v(10.06, -0.97) * mm});
            skLineSegment(sketch, "E2637.88", {"start": v(10.12, -0.76) * mm, "end": v(10.09, -0.87) * mm});
            skLineSegment(sketch, "E2637.89", {"start": v(10.14, -0.66) * mm, "end": v(10.12, -0.76) * mm});
            skLineSegment(sketch, "E2637.90", {"start": v(10.17, -0.55) * mm, "end": v(10.14, -0.66) * mm});
            skLineSegment(sketch, "E2637.91", {"start": v(10.2, -0.45) * mm, "end": v(10.17, -0.55) * mm});
            skLineSegment(sketch, "E2637.92", {"start": v(10.21, -0.34) * mm, "end": v(10.2, -0.45) * mm});
            skLineSegment(sketch, "E2637.93", {"start": v(10.23, -0.23) * mm, "end": v(10.21, -0.34) * mm});
            skLineSegment(sketch, "E2637.94", {"start": v(10.24, -0.12) * mm, "end": v(10.23, -0.23) * mm});
            skLineSegment(sketch, "E2637.95", {"start": v(-8.3, 4.35) * mm, "end": v(-8.22, 4.45) * mm});
            skLineSegment(sketch, "E2637.96", {"start": v(-8.37, 4.24) * mm, "end": v(-8.3, 4.35) * mm});
            skLineSegment(sketch, "E2637.97", {"start": v(-8.44, 4.14) * mm, "end": v(-8.37, 4.24) * mm});
            skLineSegment(sketch, "E2637.98", {"start": v(-8.5, 4.04) * mm, "end": v(-8.44, 4.14) * mm});
            skLineSegment(sketch, "E2637.99", {"start": v(-8.58, 3.94) * mm, "end": v(-8.5, 4.04) * mm});
            skLineSegment(sketch, "E2637.100", {"start": v(-8.65, 3.84) * mm, "end": v(-8.58, 3.94) * mm});
            skLineSegment(sketch, "E2637.101", {"start": v(-8.71, 3.74) * mm, "end": v(-8.65, 3.84) * mm});
            skLineSegment(sketch, "E2637.102", {"start": v(-8.78, 3.63) * mm, "end": v(-8.71, 3.74) * mm});
            skLineSegment(sketch, "E2637.103", {"start": v(-8.84, 3.53) * mm, "end": v(-8.78, 3.63) * mm});
            skLineSegment(sketch, "E2637.104", {"start": v(-8.9, 3.43) * mm, "end": v(-8.84, 3.53) * mm});
            skLineSegment(sketch, "E2637.105", {"start": v(-8.97, 3.33) * mm, "end": v(-8.9, 3.43) * mm});
            skLineSegment(sketch, "E2637.106", {"start": v(-9.03, 3.23) * mm, "end": v(-8.97, 3.33) * mm});
            skLineSegment(sketch, "E2637.107", {"start": v(-9.09, 3.13) * mm, "end": v(-9.03, 3.23) * mm});
            skLineSegment(sketch, "E2637.108", {"start": v(-9.15, 3.02) * mm, "end": v(-9.09, 3.13) * mm});
            skLineSegment(sketch, "E2637.109", {"start": v(-9.2, 2.92) * mm, "end": v(-9.15, 3.02) * mm});
            skLineSegment(sketch, "E2637.110", {"start": v(-9.26, 2.82) * mm, "end": v(-9.2, 2.92) * mm});
            skLineSegment(sketch, "E2637.111", {"start": v(-9.32, 2.72) * mm, "end": v(-9.26, 2.82) * mm});
            skLineSegment(sketch, "E2637.112", {"start": v(-9.37, 2.62) * mm, "end": v(-9.32, 2.72) * mm});
            skLineSegment(sketch, "E2637.113", {"start": v(-9.42, 2.51) * mm, "end": v(-9.37, 2.62) * mm});
            skLineSegment(sketch, "E2637.114", {"start": v(-9.47, 2.41) * mm, "end": v(-9.42, 2.51) * mm});
            skLineSegment(sketch, "E2637.115", {"start": v(-9.52, 2.3) * mm, "end": v(-9.47, 2.41) * mm});
            skLineSegment(sketch, "E2637.116", {"start": v(-9.57, 2.2) * mm, "end": v(-9.52, 2.3) * mm});
            skLineSegment(sketch, "E2637.117", {"start": v(-9.62, 2.1) * mm, "end": v(-9.57, 2.2) * mm});
            skLineSegment(sketch, "E2637.118", {"start": v(-9.67, 2) * mm, "end": v(-9.62, 2.1) * mm});
            skLineSegment(sketch, "E2637.119", {"start": v(-9.71, 1.9) * mm, "end": v(-9.67, 2) * mm});
            skLineSegment(sketch, "E2637.120", {"start": v(-9.76, 1.8) * mm, "end": v(-9.71, 1.9) * mm});
            skLineSegment(sketch, "E2637.121", {"start": v(-9.8, 1.7) * mm, "end": v(-9.76, 1.8) * mm});
            skLineSegment(sketch, "E2637.122", {"start": v(-9.84, 1.6) * mm, "end": v(-9.8, 1.7) * mm});
            skLineSegment(sketch, "E2637.123", {"start": v(-9.88, 1.49) * mm, "end": v(-9.84, 1.6) * mm});
            skLineSegment(sketch, "E2637.124", {"start": v(-9.92, 1.39) * mm, "end": v(-9.88, 1.49) * mm});
            skLineSegment(sketch, "E2637.125", {"start": v(-9.96, 1.28) * mm, "end": v(-9.92, 1.39) * mm});
            skLineSegment(sketch, "E2637.126", {"start": v(-10, 1.18) * mm, "end": v(-9.96, 1.28) * mm});
            skLineSegment(sketch, "E2637.127", {"start": v(-10.03, 1.08) * mm, "end": v(-10, 1.18) * mm});
            skLineSegment(sketch, "E2637.128", {"start": v(-10.06, 0.97) * mm, "end": v(-10.03, 1.08) * mm});
            skLineSegment(sketch, "E2637.129", {"start": v(-10.09, 0.87) * mm, "end": v(-10.06, 0.97) * mm});
            skLineSegment(sketch, "E2637.130", {"start": v(-10.12, 0.76) * mm, "end": v(-10.09, 0.87) * mm});
            skLineSegment(sketch, "E2637.131", {"start": v(-10.14, 0.66) * mm, "end": v(-10.12, 0.76) * mm});
            skLineSegment(sketch, "E2637.132", {"start": v(-10.17, 0.55) * mm, "end": v(-10.14, 0.66) * mm});
            skLineSegment(sketch, "E2637.133", {"start": v(-10.2, 0.45) * mm, "end": v(-10.17, 0.55) * mm});
            skLineSegment(sketch, "E2637.134", {"start": v(-10.21, 0.34) * mm, "end": v(-10.2, 0.45) * mm});
            skLineSegment(sketch, "E2637.135", {"start": v(-10.23, 0.23) * mm, "end": v(-10.21, 0.34) * mm});
            skLineSegment(sketch, "E2637.136", {"start": v(-10.24, 0.12) * mm, "end": v(-10.23, 0.23) * mm});
            skLineSegment(sketch, "E2637.137", {"start": v(-10.25, 0) * mm, "end": v(-10.24, 0.12) * mm});
            skLineSegment(sketch, "E2637.138", {"start": v(-10.24, -0.12) * mm, "end": v(-10.25, 0) * mm});
            skLineSegment(sketch, "E2637.139", {"start": v(-10.23, -0.23) * mm, "end": v(-10.24, -0.12) * mm});
            skLineSegment(sketch, "E2637.140", {"start": v(-10.21, -0.34) * mm, "end": v(-10.23, -0.23) * mm});
            skLineSegment(sketch, "E2637.141", {"start": v(-10.2, -0.45) * mm, "end": v(-10.21, -0.34) * mm});
            skLineSegment(sketch, "E2637.142", {"start": v(-10.17, -0.55) * mm, "end": v(-10.2, -0.45) * mm});
            skLineSegment(sketch, "E2637.143", {"start": v(-10.14, -0.66) * mm, "end": v(-10.17, -0.55) * mm});
            skLineSegment(sketch, "E2637.144", {"start": v(-10.12, -0.76) * mm, "end": v(-10.14, -0.66) * mm});
            skLineSegment(sketch, "E2637.145", {"start": v(-10.09, -0.87) * mm, "end": v(-10.12, -0.76) * mm});
            skLineSegment(sketch, "E2637.146", {"start": v(-10.06, -0.97) * mm, "end": v(-10.09, -0.87) * mm});
            skLineSegment(sketch, "E2637.147", {"start": v(-10.03, -1.08) * mm, "end": v(-10.06, -0.97) * mm});
            skLineSegment(sketch, "E2637.148", {"start": v(-10, -1.18) * mm, "end": v(-10.03, -1.08) * mm});
            skLineSegment(sketch, "E2637.149", {"start": v(-9.96, -1.28) * mm, "end": v(-10, -1.18) * mm});
            skLineSegment(sketch, "E2637.150", {"start": v(-9.92, -1.39) * mm, "end": v(-9.96, -1.28) * mm});
            skLineSegment(sketch, "E2637.151", {"start": v(-9.88, -1.49) * mm, "end": v(-9.92, -1.39) * mm});
            skLineSegment(sketch, "E2637.152", {"start": v(-9.84, -1.6) * mm, "end": v(-9.88, -1.49) * mm});
            skLineSegment(sketch, "E2637.153", {"start": v(-9.8, -1.7) * mm, "end": v(-9.84, -1.6) * mm});
            skLineSegment(sketch, "E2637.154", {"start": v(-9.76, -1.8) * mm, "end": v(-9.8, -1.7) * mm});
            skLineSegment(sketch, "E2637.155", {"start": v(-9.71, -1.9) * mm, "end": v(-9.76, -1.8) * mm});
            skLineSegment(sketch, "E2637.156", {"start": v(-9.67, -2) * mm, "end": v(-9.71, -1.9) * mm});
            skLineSegment(sketch, "E2637.157", {"start": v(-9.62, -2.1) * mm, "end": v(-9.67, -2) * mm});
            skLineSegment(sketch, "E2637.158", {"start": v(-9.57, -2.2) * mm, "end": v(-9.62, -2.1) * mm});
            skLineSegment(sketch, "E2637.159", {"start": v(-9.52, -2.3) * mm, "end": v(-9.57, -2.2) * mm});
            skLineSegment(sketch, "E2637.160", {"start": v(-9.47, -2.41) * mm, "end": v(-9.52, -2.3) * mm});
            skLineSegment(sketch, "E2637.161", {"start": v(-9.42, -2.51) * mm, "end": v(-9.47, -2.41) * mm});
            skLineSegment(sketch, "E2637.162", {"start": v(-9.37, -2.62) * mm, "end": v(-9.42, -2.51) * mm});
            skLineSegment(sketch, "E2637.163", {"start": v(-9.32, -2.72) * mm, "end": v(-9.37, -2.62) * mm});
            skLineSegment(sketch, "E2637.164", {"start": v(-9.26, -2.82) * mm, "end": v(-9.32, -2.72) * mm});
            skLineSegment(sketch, "E2637.165", {"start": v(-9.2, -2.92) * mm, "end": v(-9.26, -2.82) * mm});
            skLineSegment(sketch, "E2637.166", {"start": v(-9.15, -3.02) * mm, "end": v(-9.2, -2.92) * mm});
            skLineSegment(sketch, "E2637.167", {"start": v(-9.09, -3.13) * mm, "end": v(-9.15, -3.02) * mm});
            skLineSegment(sketch, "E2637.168", {"start": v(-9.03, -3.23) * mm, "end": v(-9.09, -3.13) * mm});
            skLineSegment(sketch, "E2637.169", {"start": v(-8.97, -3.33) * mm, "end": v(-9.03, -3.23) * mm});
            skLineSegment(sketch, "E2637.170", {"start": v(-8.9, -3.43) * mm, "end": v(-8.97, -3.33) * mm});
            skLineSegment(sketch, "E2637.171", {"start": v(-8.84, -3.53) * mm, "end": v(-8.9, -3.43) * mm});
            skLineSegment(sketch, "E2637.172", {"start": v(-8.78, -3.63) * mm, "end": v(-8.84, -3.53) * mm});
            skLineSegment(sketch, "E2637.173", {"start": v(-8.71, -3.74) * mm, "end": v(-8.78, -3.63) * mm});
            skLineSegment(sketch, "E2637.174", {"start": v(-8.65, -3.84) * mm, "end": v(-8.71, -3.74) * mm});
            skLineSegment(sketch, "E2637.175", {"start": v(-8.58, -3.94) * mm, "end": v(-8.65, -3.84) * mm});
            skLineSegment(sketch, "E2637.176", {"start": v(-8.5, -4.04) * mm, "end": v(-8.58, -3.94) * mm});
            skLineSegment(sketch, "E2637.177", {"start": v(-8.44, -4.14) * mm, "end": v(-8.5, -4.04) * mm});
            skLineSegment(sketch, "E2637.178", {"start": v(-8.37, -4.24) * mm, "end": v(-8.44, -4.14) * mm});
            skLineSegment(sketch, "E2637.179", {"start": v(-8.3, -4.35) * mm, "end": v(-8.37, -4.24) * mm});
            skLineSegment(sketch, "E2637.180", {"start": v(-8.22, -4.45) * mm, "end": v(-8.3, -4.35) * mm});
            skLineSegment(sketch, "E2637.181", {"start": v(-8.15, -4.55) * mm, "end": v(-8.22, -4.45) * mm});
            skLineSegment(sketch, "E2637.182", {"start": v(-8.07, -4.65) * mm, "end": v(-8.15, -4.55) * mm});
            skLineSegment(sketch, "E2637.183", {"start": v(-8, -4.75) * mm, "end": v(-8.07, -4.65) * mm});
            skLineSegment(sketch, "E2637.184", {"start": v(-7.91, -4.85) * mm, "end": v(-8, -4.75) * mm});
            skLineSegment(sketch, "E2637.185", {"start": v(-7.83, -4.96) * mm, "end": v(-7.91, -4.85) * mm});
            skLineSegment(sketch, "E2637.186", {"start": v(-7.75, -5.06) * mm, "end": v(-7.83, -4.96) * mm});
            skLineSegment(sketch, "E2637.187", {"start": v(-7.67, -5.16) * mm, "end": v(-7.75, -5.06) * mm});
            skLineSegment(sketch, "E2637.188", {"start": v(-7.59, -5.26) * mm, "end": v(-7.67, -5.16) * mm});
            skLineSegment(sketch, "E2637.189", {"start": v(-7.5, -5.36) * mm, "end": v(-7.59, -5.26) * mm});
            skLineSegment(sketch, "E2637.190", {"start": v(-7.42, -5.46) * mm, "end": v(-7.5, -5.36) * mm});
            skLineSegment(sketch, "E2637.191", {"start": v(-7.33, -5.56) * mm, "end": v(-7.42, -5.46) * mm});
            skLineSegment(sketch, "E2637.192", {"start": v(-7.24, -5.67) * mm, "end": v(-7.33, -5.56) * mm});
            skLineSegment(sketch, "E2637.193", {"start": v(-7.15, -5.77) * mm, "end": v(-7.24, -5.67) * mm});
            skLineSegment(sketch, "E2637.194", {"start": v(-7.06, -5.87) * mm, "end": v(-7.15, -5.77) * mm});
            skLineSegment(sketch, "E2637.195", {"start": v(-6.96, -5.97) * mm, "end": v(-7.06, -5.87) * mm});
            skLineSegment(sketch, "E2637.196", {"start": v(-6.87, -6.07) * mm, "end": v(-6.96, -5.97) * mm});
            skLineSegment(sketch, "E2637.197", {"start": v(-1.7, -9.8) * mm, "end": v(-1.8, -9.76) * mm});
            skLineSegment(sketch, "E2637.198", {"start": v(-1.6, -9.84) * mm, "end": v(-1.7, -9.8) * mm});
            skLineSegment(sketch, "E2637.199", {"start": v(-1.49, -9.88) * mm, "end": v(-1.6, -9.84) * mm});
            skLineSegment(sketch, "E2637.200", {"start": v(-1.39, -9.92) * mm, "end": v(-1.49, -9.88) * mm});
            skLineSegment(sketch, "E2637.201", {"start": v(-1.28, -9.96) * mm, "end": v(-1.39, -9.92) * mm});
            skLineSegment(sketch, "E2637.202", {"start": v(-1.18, -10) * mm, "end": v(-1.28, -9.96) * mm});
            skLineSegment(sketch, "E2637.203", {"start": v(-1.08, -10.03) * mm, "end": v(-1.18, -10) * mm});
            skLineSegment(sketch, "E2637.204", {"start": v(-0.97, -10.06) * mm, "end": v(-1.08, -10.03) * mm});
            skLineSegment(sketch, "E2637.205", {"start": v(-0.87, -10.09) * mm, "end": v(-0.97, -10.06) * mm});
            skLineSegment(sketch, "E2637.206", {"start": v(-0.76, -10.12) * mm, "end": v(-0.87, -10.09) * mm});
            skLineSegment(sketch, "E2637.207", {"start": v(-0.66, -10.14) * mm, "end": v(-0.76, -10.12) * mm});
            skLineSegment(sketch, "E2637.208", {"start": v(-0.55, -10.17) * mm, "end": v(-0.66, -10.14) * mm});
            skLineSegment(sketch, "E2637.209", {"start": v(-0.45, -10.2) * mm, "end": v(-0.55, -10.17) * mm});
            skLineSegment(sketch, "E2637.210", {"start": v(-0.34, -10.21) * mm, "end": v(-0.45, -10.2) * mm});
            skLineSegment(sketch, "E2637.211", {"start": v(-0.23, -10.23) * mm, "end": v(-0.34, -10.21) * mm});
            skLineSegment(sketch, "E2637.212", {"start": v(-0.12, -10.24) * mm, "end": v(-0.23, -10.23) * mm});
            skLineSegment(sketch, "E2637.213", {"start": v(0, -10.25) * mm, "end": v(-0.12, -10.24) * mm});
            skLineSegment(sketch, "E2637.214", {"start": v(0.12, -10.24) * mm, "end": v(0, -10.25) * mm});
            skLineSegment(sketch, "E2637.215", {"start": v(0.23, -10.23) * mm, "end": v(0.12, -10.24) * mm});
            skLineSegment(sketch, "E2637.216", {"start": v(0.34, -10.21) * mm, "end": v(0.23, -10.23) * mm});
            skLineSegment(sketch, "E2637.217", {"start": v(0.45, -10.2) * mm, "end": v(0.34, -10.21) * mm});
            skLineSegment(sketch, "E2637.218", {"start": v(0.55, -10.17) * mm, "end": v(0.45, -10.2) * mm});
            skLineSegment(sketch, "E2637.219", {"start": v(0.66, -10.14) * mm, "end": v(0.55, -10.17) * mm});
            skLineSegment(sketch, "E2637.220", {"start": v(0.76, -10.12) * mm, "end": v(0.66, -10.14) * mm});
            skLineSegment(sketch, "E2637.221", {"start": v(2.1, -9.62) * mm, "end": v(2, -9.67) * mm});
            skLineSegment(sketch, "E2637.222", {"start": v(2.2, -9.57) * mm, "end": v(2.1, -9.62) * mm});
            skLineSegment(sketch, "E2637.223", {"start": v(2.3, -9.52) * mm, "end": v(2.2, -9.57) * mm});
            skLineSegment(sketch, "E2637.224", {"start": v(2.41, -9.47) * mm, "end": v(2.3, -9.52) * mm});
            skLineSegment(sketch, "E2637.225", {"start": v(2.51, -9.42) * mm, "end": v(2.41, -9.47) * mm});
            skLineSegment(sketch, "E2637.226", {"start": v(2.62, -9.37) * mm, "end": v(2.51, -9.42) * mm});
            skLineSegment(sketch, "E2637.227", {"start": v(3.02, -9.15) * mm, "end": v(2.92, -9.2) * mm});
            skLineSegment(sketch, "E2637.228", {"start": v(2.92, -9.2) * mm, "end": v(2.82, -9.26) * mm});
            skLineSegment(sketch, "E2637.229", {"start": v(2.82, -9.26) * mm, "end": v(2.72, -9.32) * mm});
            skLineSegment(sketch, "E2637.230", {"start": v(2.72, -9.32) * mm, "end": v(2.62, -9.37) * mm});
            skLineSegment(sketch, "E2637.231", {"start": v(2, -9.67) * mm, "end": v(1.9, -9.71) * mm});
            skLineSegment(sketch, "E2637.232", {"start": v(1.9, -9.71) * mm, "end": v(1.8, -9.76) * mm});
            skLineSegment(sketch, "E2637.233", {"start": v(1.8, -9.76) * mm, "end": v(1.7, -9.8) * mm});
            skLineSegment(sketch, "E2637.234", {"start": v(1.7, -9.8) * mm, "end": v(1.6, -9.84) * mm});
            skLineSegment(sketch, "E2637.235", {"start": v(1.6, -9.84) * mm, "end": v(1.49, -9.88) * mm});
            skLineSegment(sketch, "E2637.236", {"start": v(1.49, -9.88) * mm, "end": v(1.39, -9.92) * mm});
            skLineSegment(sketch, "E2637.237", {"start": v(1.39, -9.92) * mm, "end": v(1.28, -9.96) * mm});
            skLineSegment(sketch, "E2637.238", {"start": v(1.28, -9.96) * mm, "end": v(1.18, -10) * mm});
            skLineSegment(sketch, "E2637.239", {"start": v(1.18, -10) * mm, "end": v(1.08, -10.03) * mm});
            skLineSegment(sketch, "E2637.240", {"start": v(1.08, -10.03) * mm, "end": v(0.97, -10.06) * mm});
            skLineSegment(sketch, "E2637.241", {"start": v(0.97, -10.06) * mm, "end": v(0.87, -10.09) * mm});
            skLineSegment(sketch, "E2637.242", {"start": v(0.87, -10.09) * mm, "end": v(0.76, -10.12) * mm});
            skLineSegment(sketch, "E2637.243", {"start": v(-1.8, -9.76) * mm, "end": v(-1.9, -9.71) * mm});
            skLineSegment(sketch, "E2637.244", {"start": v(-1.9, -9.71) * mm, "end": v(-2, -9.67) * mm});
            skLineSegment(sketch, "E2637.245", {"start": v(-2, -9.67) * mm, "end": v(-2.1, -9.62) * mm});
            skLineSegment(sketch, "E2637.246", {"start": v(-2.1, -9.62) * mm, "end": v(-2.2, -9.57) * mm});
            skLineSegment(sketch, "E2637.247", {"start": v(-2.2, -9.57) * mm, "end": v(-2.3, -9.52) * mm});
            skLineSegment(sketch, "E2637.248", {"start": v(-2.3, -9.52) * mm, "end": v(-2.41, -9.47) * mm});
            skLineSegment(sketch, "E2637.249", {"start": v(-2.41, -9.47) * mm, "end": v(-2.51, -9.42) * mm});
            skLineSegment(sketch, "E2637.250", {"start": v(-2.51, -9.42) * mm, "end": v(-2.62, -9.37) * mm});
            skLineSegment(sketch, "E2637.251", {"start": v(-2.62, -9.37) * mm, "end": v(-2.72, -9.32) * mm});
            skLineSegment(sketch, "E2637.252", {"start": v(-2.72, -9.32) * mm, "end": v(-2.82, -9.26) * mm});
            skLineSegment(sketch, "E2637.253", {"start": v(-2.82, -9.26) * mm, "end": v(-2.92, -9.2) * mm});
            skLineSegment(sketch, "E2637.254", {"start": v(-2.92, -9.2) * mm, "end": v(-3.02, -9.15) * mm});
            skLineSegment(sketch, "E2637.255", {"start": v(-3.02, -9.15) * mm, "end": v(-3.13, -9.09) * mm});
            skLineSegment(sketch, "E2637.256", {"start": v(-3.13, -9.09) * mm, "end": v(-3.23, -9.03) * mm});
            skLineSegment(sketch, "E2637.257", {"start": v(-3.23, -9.03) * mm, "end": v(-3.33, -8.97) * mm});
            skLineSegment(sketch, "E2637.258", {"start": v(-3.33, -8.97) * mm, "end": v(-3.43, -8.9) * mm});
            skLineSegment(sketch, "E2637.259", {"start": v(-3.43, -8.9) * mm, "end": v(-3.53, -8.84) * mm});
            skLineSegment(sketch, "E2637.260", {"start": v(-3.53, -8.84) * mm, "end": v(-3.63, -8.78) * mm});
            skLineSegment(sketch, "E2637.261", {"start": v(-3.63, -8.78) * mm, "end": v(-3.74, -8.71) * mm});
            skLineSegment(sketch, "E2637.262", {"start": v(-3.74, -8.71) * mm, "end": v(-3.84, -8.65) * mm});
            skLineSegment(sketch, "E2637.263", {"start": v(-3.84, -8.65) * mm, "end": v(-3.94, -8.58) * mm});
            skLineSegment(sketch, "E2637.264", {"start": v(-3.94, -8.58) * mm, "end": v(-4.04, -8.5) * mm});
            skLineSegment(sketch, "E2637.265", {"start": v(-4.04, -8.5) * mm, "end": v(-4.14, -8.44) * mm});
            skLineSegment(sketch, "E2637.266", {"start": v(-4.14, -8.44) * mm, "end": v(-4.24, -8.37) * mm});
            skLineSegment(sketch, "E2637.267", {"start": v(-4.24, -8.37) * mm, "end": v(-4.35, -8.3) * mm});
            skLineSegment(sketch, "E2637.268", {"start": v(-4.35, -8.3) * mm, "end": v(-4.45, -8.22) * mm});
            skLineSegment(sketch, "E2637.269", {"start": v(-4.45, -8.22) * mm, "end": v(-4.55, -8.15) * mm});
            skLineSegment(sketch, "E2637.270", {"start": v(-4.55, -8.15) * mm, "end": v(-4.65, -8.07) * mm});
            skLineSegment(sketch, "E2637.271", {"start": v(-4.65, -8.07) * mm, "end": v(-4.75, -8) * mm});
            skLineSegment(sketch, "E2637.272", {"start": v(-4.75, -8) * mm, "end": v(-4.85, -7.91) * mm});
            skLineSegment(sketch, "E2637.273", {"start": v(-4.85, -7.91) * mm, "end": v(-4.96, -7.83) * mm});
            skLineSegment(sketch, "E2637.274", {"start": v(-4.96, -7.83) * mm, "end": v(-5.06, -7.75) * mm});
            skLineSegment(sketch, "E2637.275", {"start": v(-5.06, -7.75) * mm, "end": v(-5.16, -7.67) * mm});
            skLineSegment(sketch, "E2637.276", {"start": v(-5.16, -7.67) * mm, "end": v(-5.26, -7.59) * mm});
            skLineSegment(sketch, "E2637.277", {"start": v(-5.26, -7.59) * mm, "end": v(-5.36, -7.5) * mm});
            skLineSegment(sketch, "E2637.278", {"start": v(-5.36, -7.5) * mm, "end": v(-5.46, -7.42) * mm});
            skLineSegment(sketch, "E2637.279", {"start": v(-5.46, -7.42) * mm, "end": v(-5.56, -7.33) * mm});
            skLineSegment(sketch, "E2637.280", {"start": v(-5.56, -7.33) * mm, "end": v(-5.67, -7.24) * mm});
            skLineSegment(sketch, "E2637.281", {"start": v(-5.67, -7.24) * mm, "end": v(-5.77, -7.15) * mm});
            skLineSegment(sketch, "E2637.282", {"start": v(-5.77, -7.15) * mm, "end": v(-5.87, -7.06) * mm});
            skLineSegment(sketch, "E2637.283", {"start": v(-5.87, -7.06) * mm, "end": v(-5.97, -6.96) * mm});
            skLineSegment(sketch, "E2637.284", {"start": v(-5.97, -6.96) * mm, "end": v(-6.07, -6.87) * mm});
            skLineSegment(sketch, "E2637.285", {"start": v(-6.07, -6.87) * mm, "end": v(-6.17, -6.77) * mm});
            skLineSegment(sketch, "E2637.286", {"start": v(-6.17, -6.77) * mm, "end": v(-6.27, -6.68) * mm});
            skLineSegment(sketch, "E2637.287", {"start": v(-6.27, -6.68) * mm, "end": v(-6.38, -6.58) * mm});
            skLineSegment(sketch, "E2637.288", {"start": v(-6.38, -6.58) * mm, "end": v(-6.48, -6.48) * mm});
            skLineSegment(sketch, "E2637.289", {"start": v(-6.48, -6.48) * mm, "end": v(-6.58, -6.38) * mm});
            skLineSegment(sketch, "E2637.290", {"start": v(-6.58, -6.38) * mm, "end": v(-6.68, -6.27) * mm});
            skLineSegment(sketch, "E2637.291", {"start": v(-6.68, -6.27) * mm, "end": v(-6.77, -6.17) * mm});
            skLineSegment(sketch, "E2637.292", {"start": v(-6.77, -6.17) * mm, "end": v(-6.87, -6.07) * mm});
            skLineSegment(sketch, "E2637.293", {"start": v(-8.22, 4.45) * mm, "end": v(-8.15, 4.55) * mm});
            skLineSegment(sketch, "E2637.294", {"start": v(-8.15, 4.55) * mm, "end": v(-8.07, 4.65) * mm});
            skLineSegment(sketch, "E2637.295", {"start": v(-8.07, 4.65) * mm, "end": v(-8, 4.75) * mm});
            skLineSegment(sketch, "E2637.296", {"start": v(-8, 4.75) * mm, "end": v(-7.91, 4.85) * mm});
            skLineSegment(sketch, "E2637.297", {"start": v(-7.91, 4.85) * mm, "end": v(-7.83, 4.96) * mm});
            skLineSegment(sketch, "E2637.298", {"start": v(-7.83, 4.96) * mm, "end": v(-7.75, 5.06) * mm});
            skLineSegment(sketch, "E2637.299", {"start": v(-7.75, 5.06) * mm, "end": v(-7.67, 5.16) * mm});
            skLineSegment(sketch, "E2637.300", {"start": v(-7.67, 5.16) * mm, "end": v(-7.59, 5.26) * mm});
            skLineSegment(sketch, "E2637.301", {"start": v(-7.59, 5.26) * mm, "end": v(-7.5, 5.36) * mm});
            skLineSegment(sketch, "E2637.302", {"start": v(-7.5, 5.36) * mm, "end": v(-7.42, 5.46) * mm});
            skLineSegment(sketch, "E2637.303", {"start": v(-7.42, 5.46) * mm, "end": v(-7.33, 5.56) * mm});
            skLineSegment(sketch, "E2637.304", {"start": v(-7.33, 5.56) * mm, "end": v(-7.24, 5.67) * mm});
            skLineSegment(sketch, "E2637.305", {"start": v(-7.24, 5.67) * mm, "end": v(-7.15, 5.77) * mm});
            skLineSegment(sketch, "E2637.306", {"start": v(-7.15, 5.77) * mm, "end": v(-7.06, 5.87) * mm});
            skLineSegment(sketch, "E2637.307", {"start": v(-7.06, 5.87) * mm, "end": v(-6.96, 5.97) * mm});
            skLineSegment(sketch, "E2637.308", {"start": v(-6.96, 5.97) * mm, "end": v(-6.87, 6.07) * mm});
            skLineSegment(sketch, "E2637.309", {"start": v(-6.87, 6.07) * mm, "end": v(-6.77, 6.17) * mm});
            skLineSegment(sketch, "E2637.310", {"start": v(-6.77, 6.17) * mm, "end": v(-6.68, 6.27) * mm});
            skLineSegment(sketch, "E2637.311", {"start": v(-6.68, 6.27) * mm, "end": v(-6.58, 6.38) * mm});
            skLineSegment(sketch, "E2637.312", {"start": v(-6.58, 6.38) * mm, "end": v(-6.48, 6.48) * mm});
            skLineSegment(sketch, "E2637.313", {"start": v(-6.48, 6.48) * mm, "end": v(-6.38, 6.58) * mm});
            skLineSegment(sketch, "E2637.314", {"start": v(-6.38, 6.58) * mm, "end": v(-6.27, 6.68) * mm});
            skLineSegment(sketch, "E2637.315", {"start": v(-6.27, 6.68) * mm, "end": v(-6.17, 6.77) * mm});
            skLineSegment(sketch, "E2637.316", {"start": v(-6.17, 6.77) * mm, "end": v(-6.07, 6.87) * mm});
            skLineSegment(sketch, "E2637.317", {"start": v(-6.07, 6.87) * mm, "end": v(-5.97, 6.96) * mm});
            skLineSegment(sketch, "E2637.318", {"start": v(-5.97, 6.96) * mm, "end": v(-5.87, 7.06) * mm});
            skLineSegment(sketch, "E2637.319", {"start": v(-5.87, 7.06) * mm, "end": v(-5.77, 7.15) * mm});
            skLineSegment(sketch, "E2637.320", {"start": v(-5.77, 7.15) * mm, "end": v(-5.67, 7.24) * mm});
            skLineSegment(sketch, "E2637.321", {"start": v(-5.67, 7.24) * mm, "end": v(-5.56, 7.33) * mm});
            skLineSegment(sketch, "E2637.322", {"start": v(-5.56, 7.33) * mm, "end": v(-5.46, 7.42) * mm});
            skLineSegment(sketch, "E2637.323", {"start": v(-5.46, 7.42) * mm, "end": v(-5.36, 7.5) * mm});
            skLineSegment(sketch, "E2637.324", {"start": v(-5.36, 7.5) * mm, "end": v(-5.26, 7.59) * mm});
            skLineSegment(sketch, "E2637.325", {"start": v(-5.26, 7.59) * mm, "end": v(-5.16, 7.67) * mm});
            skLineSegment(sketch, "E2637.326", {"start": v(-5.16, 7.67) * mm, "end": v(-5.06, 7.75) * mm});
            skLineSegment(sketch, "E2637.327", {"start": v(-5.06, 7.75) * mm, "end": v(-4.96, 7.83) * mm});
            skLineSegment(sketch, "E2637.328", {"start": v(-4.96, 7.83) * mm, "end": v(-4.85, 7.91) * mm});
            skLineSegment(sketch, "E2637.329", {"start": v(-4.85, 7.91) * mm, "end": v(-4.75, 8) * mm});
            skLineSegment(sketch, "E2637.330", {"start": v(-4.75, 8) * mm, "end": v(-4.65, 8.07) * mm});
            skLineSegment(sketch, "E2637.331", {"start": v(-4.65, 8.07) * mm, "end": v(-4.55, 8.15) * mm});
            skLineSegment(sketch, "E2637.332", {"start": v(-4.55, 8.15) * mm, "end": v(-4.45, 8.22) * mm});
            skLineSegment(sketch, "E2637.333", {"start": v(-4.45, 8.22) * mm, "end": v(-4.35, 8.3) * mm});
            skLineSegment(sketch, "E2637.334", {"start": v(-4.35, 8.3) * mm, "end": v(-4.24, 8.37) * mm});
            skLineSegment(sketch, "E2637.335", {"start": v(-4.24, 8.37) * mm, "end": v(-4.14, 8.44) * mm});
            skLineSegment(sketch, "E2637.336", {"start": v(-4.14, 8.44) * mm, "end": v(-4.04, 8.5) * mm});
            skLineSegment(sketch, "E2637.337", {"start": v(-4.04, 8.5) * mm, "end": v(-3.94, 8.58) * mm});
            skLineSegment(sketch, "E2637.338", {"start": v(-3.94, 8.58) * mm, "end": v(-3.84, 8.65) * mm});
            skLineSegment(sketch, "E2637.339", {"start": v(-3.84, 8.65) * mm, "end": v(-3.74, 8.71) * mm});
            skLineSegment(sketch, "E2637.340", {"start": v(-3.74, 8.71) * mm, "end": v(-3.63, 8.78) * mm});
            skLineSegment(sketch, "E2637.341", {"start": v(-3.63, 8.78) * mm, "end": v(-3.53, 8.84) * mm});
            skLineSegment(sketch, "E2637.342", {"start": v(-3.53, 8.84) * mm, "end": v(-3.43, 8.9) * mm});
            skLineSegment(sketch, "E2637.343", {"start": v(-3.43, 8.9) * mm, "end": v(-3.33, 8.97) * mm});
            skLineSegment(sketch, "E2637.344", {"start": v(-3.33, 8.97) * mm, "end": v(-3.23, 9.03) * mm});
            skLineSegment(sketch, "E2637.345", {"start": v(-3.23, 9.03) * mm, "end": v(-3.13, 9.09) * mm});
            skLineSegment(sketch, "E2637.346", {"start": v(-3.13, 9.09) * mm, "end": v(-3.02, 9.15) * mm});
            skLineSegment(sketch, "E2637.347", {"start": v(-3.02, 9.15) * mm, "end": v(-2.92, 9.2) * mm});
            skLineSegment(sketch, "E2637.348", {"start": v(-2.92, 9.2) * mm, "end": v(-2.82, 9.26) * mm});
            skLineSegment(sketch, "E2637.349", {"start": v(-2.82, 9.26) * mm, "end": v(-2.72, 9.32) * mm});
            skLineSegment(sketch, "E2637.350", {"start": v(-2.72, 9.32) * mm, "end": v(-2.62, 9.37) * mm});
            skLineSegment(sketch, "E2637.351", {"start": v(-2.62, 9.37) * mm, "end": v(-2.51, 9.42) * mm});
            skLineSegment(sketch, "E2637.352", {"start": v(-2.51, 9.42) * mm, "end": v(-2.41, 9.47) * mm});
            skLineSegment(sketch, "E2637.353", {"start": v(-2.41, 9.47) * mm, "end": v(-2.3, 9.52) * mm});
            skLineSegment(sketch, "E2637.354", {"start": v(-2.3, 9.52) * mm, "end": v(-2.2, 9.57) * mm});
            skLineSegment(sketch, "E2637.355", {"start": v(-2.2, 9.57) * mm, "end": v(-2.1, 9.62) * mm});
            skLineSegment(sketch, "E2637.356", {"start": v(-2.1, 9.62) * mm, "end": v(-2, 9.67) * mm});
            skLineSegment(sketch, "E2637.357", {"start": v(-2, 9.67) * mm, "end": v(-1.9, 9.71) * mm});
            skLineSegment(sketch, "E2637.358", {"start": v(-1.9, 9.71) * mm, "end": v(-1.8, 9.76) * mm});
            skLineSegment(sketch, "E2637.359", {"start": v(-1.8, 9.76) * mm, "end": v(-1.7, 9.8) * mm});
            skLineSegment(sketch, "E2637.360", {"start": v(-1.7, 9.8) * mm, "end": v(-1.6, 9.84) * mm});
            skLineSegment(sketch, "E2637.361", {"start": v(-1.6, 9.84) * mm, "end": v(-1.49, 9.88) * mm});
            skLineSegment(sketch, "E2637.362", {"start": v(-1.49, 9.88) * mm, "end": v(-1.39, 9.92) * mm});
            skLineSegment(sketch, "E2637.363", {"start": v(-1.39, 9.92) * mm, "end": v(-1.28, 9.96) * mm});
            skLineSegment(sketch, "E2637.364", {"start": v(-1.28, 9.96) * mm, "end": v(-1.18, 10) * mm});
            skLineSegment(sketch, "E2637.365", {"start": v(-1.18, 10) * mm, "end": v(-1.08, 10.03) * mm});
            skLineSegment(sketch, "E2637.366", {"start": v(-1.08, 10.03) * mm, "end": v(-0.97, 10.06) * mm});
            skLineSegment(sketch, "E2637.367", {"start": v(-0.97, 10.06) * mm, "end": v(-0.87, 10.09) * mm});
            skLineSegment(sketch, "E2637.368", {"start": v(-0.87, 10.09) * mm, "end": v(-0.76, 10.12) * mm});
            skLineSegment(sketch, "E2637.369", {"start": v(-0.76, 10.12) * mm, "end": v(-0.66, 10.14) * mm});
            skLineSegment(sketch, "E2637.370", {"start": v(-0.66, 10.14) * mm, "end": v(-0.55, 10.17) * mm});
            skLineSegment(sketch, "E2637.371", {"start": v(-0.55, 10.17) * mm, "end": v(-0.45, 10.2) * mm});
            skLineSegment(sketch, "E2637.372", {"start": v(-0.45, 10.2) * mm, "end": v(-0.34, 10.21) * mm});
            skLineSegment(sketch, "E2637.373", {"start": v(-0.34, 10.21) * mm, "end": v(-0.23, 10.23) * mm});
            skLineSegment(sketch, "E2637.374", {"start": v(-0.23, 10.23) * mm, "end": v(-0.12, 10.24) * mm});
            skLineSegment(sketch, "E2637.375", {"start": v(-0.12, 10.24) * mm, "end": v(0, 10.25) * mm});
            skLineSegment(sketch, "E2637.376", {"start": v(0, 10.25) * mm, "end": v(0.12, 10.24) * mm});
            skLineSegment(sketch, "E2637.377", {"start": v(0.12, 10.24) * mm, "end": v(0.23, 10.23) * mm});
            skLineSegment(sketch, "E2637.378", {"start": v(0.23, 10.23) * mm, "end": v(0.34, 10.21) * mm});
            skLineSegment(sketch, "E2637.379", {"start": v(0.34, 10.21) * mm, "end": v(0.45, 10.2) * mm});
            skLineSegment(sketch, "E2637.380", {"start": v(0.45, 10.2) * mm, "end": v(0.55, 10.17) * mm});
            skLineSegment(sketch, "E2637.381", {"start": v(0.55, 10.17) * mm, "end": v(0.66, 10.14) * mm});
            skLineSegment(sketch, "E2637.382", {"start": v(0.66, 10.14) * mm, "end": v(0.76, 10.12) * mm});
            skLineSegment(sketch, "E2637.383", {"start": v(0.76, 10.12) * mm, "end": v(0.87, 10.09) * mm});
            skLineSegment(sketch, "E2637.384", {"start": v(0.87, 10.09) * mm, "end": v(0.97, 10.06) * mm});
            skLineSegment(sketch, "E2637.385", {"start": v(0.97, 10.06) * mm, "end": v(1.08, 10.03) * mm});
            skLineSegment(sketch, "E2637.386", {"start": v(1.08, 10.03) * mm, "end": v(1.18, 10) * mm});
            skLineSegment(sketch, "E2637.387", {"start": v(1.18, 10) * mm, "end": v(1.28, 9.96) * mm});
            skLineSegment(sketch, "E2637.388", {"start": v(1.28, 9.96) * mm, "end": v(1.39, 9.92) * mm});
            skLineSegment(sketch, "E2637.389", {"start": v(1.39, 9.92) * mm, "end": v(1.49, 9.88) * mm});
            skLineSegment(sketch, "E2637.390", {"start": v(1.49, 9.88) * mm, "end": v(1.6, 9.84) * mm});
            skLineSegment(sketch, "E2637.391", {"start": v(1.6, 9.84) * mm, "end": v(1.7, 9.8) * mm});
            skLineSegment(sketch, "E2637.392", {"start": v(3.13, -9.09) * mm, "end": v(3.02, -9.15) * mm});
            skLineSegment(sketch, "E2637.393", {"start": v(1.7, 9.8) * mm, "end": v(1.8, 9.76) * mm});
            skLineSegment(sketch, "E2637.394", {"start": v(1.8, 9.76) * mm, "end": v(1.9, 9.71) * mm});
            skLineSegment(sketch, "E2637.395", {"start": v(1.9, 9.71) * mm, "end": v(2, 9.67) * mm});
            skLineSegment(sketch, "E2637.396", {"start": v(2, 9.67) * mm, "end": v(2.1, 9.62) * mm});
            skLineSegment(sketch, "E2637.397", {"start": v(2.1, 9.62) * mm, "end": v(2.2, 9.57) * mm});
            skLineSegment(sketch, "E2637.398", {"start": v(2.2, 9.57) * mm, "end": v(2.3, 9.52) * mm});
            skLineSegment(sketch, "E2637.399", {"start": v(2.3, 9.52) * mm, "end": v(2.41, 9.47) * mm});
            skLineSegment(sketch, "E2637.400", {"start": v(2.41, 9.47) * mm, "end": v(2.51, 9.42) * mm});
            skLineSegment(sketch, "E2637.401", {"start": v(2.51, 9.42) * mm, "end": v(2.62, 9.37) * mm});
            skLineSegment(sketch, "E2637.402", {"start": v(2.62, 9.37) * mm, "end": v(2.72, 9.32) * mm});
            skLineSegment(sketch, "E2637.403", {"start": v(2.72, 9.32) * mm, "end": v(2.82, 9.26) * mm});
            skLineSegment(sketch, "E2637.404", {"start": v(2.82, 9.26) * mm, "end": v(2.92, 9.2) * mm});
            skLineSegment(sketch, "E2637.405", {"start": v(2.92, 9.2) * mm, "end": v(3.02, 9.15) * mm});
            skLineSegment(sketch, "E2637.406", {"start": v(3.02, 9.15) * mm, "end": v(3.13, 9.09) * mm});
            skLineSegment(sketch, "E2637.407", {"start": v(3.13, 9.09) * mm, "end": v(3.23, 9.03) * mm});
            skLineSegment(sketch, "E2637.408", {"start": v(3.23, 9.03) * mm, "end": v(3.33, 8.97) * mm});
            skLineSegment(sketch, "E2637.409", {"start": v(3.33, 8.97) * mm, "end": v(3.43, 8.9) * mm});
            skLineSegment(sketch, "E2637.410", {"start": v(3.43, 8.9) * mm, "end": v(3.53, 8.84) * mm});
            skLineSegment(sketch, "E2637.411", {"start": v(3.53, 8.84) * mm, "end": v(3.63, 8.78) * mm});
            skLineSegment(sketch, "E2637.412", {"start": v(3.63, 8.78) * mm, "end": v(3.74, 8.71) * mm});
            skLineSegment(sketch, "E2637.413", {"start": v(3.74, 8.71) * mm, "end": v(3.84, 8.65) * mm});
            skLineSegment(sketch, "E2637.414", {"start": v(3.84, 8.65) * mm, "end": v(3.94, 8.58) * mm});
            skLineSegment(sketch, "E2637.415", {"start": v(3.94, 8.58) * mm, "end": v(4.04, 8.5) * mm});
            skLineSegment(sketch, "E2637.416", {"start": v(4.04, 8.5) * mm, "end": v(4.14, 8.44) * mm});
            skLineSegment(sketch, "E2637.417", {"start": v(4.14, 8.44) * mm, "end": v(4.24, 8.37) * mm});
            skLineSegment(sketch, "E2637.418", {"start": v(4.24, 8.37) * mm, "end": v(4.35, 8.3) * mm});
            skLineSegment(sketch, "E2637.419", {"start": v(4.35, 8.3) * mm, "end": v(4.45, 8.22) * mm});
            skLineSegment(sketch, "E2637.420", {"start": v(4.45, 8.22) * mm, "end": v(4.55, 8.15) * mm});
            skLineSegment(sketch, "E2637.421", {"start": v(4.55, 8.15) * mm, "end": v(4.65, 8.07) * mm});
            skLineSegment(sketch, "E2637.422", {"start": v(4.65, 8.07) * mm, "end": v(4.75, 8) * mm});
            skLineSegment(sketch, "E2637.423", {"start": v(4.75, 8) * mm, "end": v(4.85, 7.91) * mm});
            skLineSegment(sketch, "E2637.424", {"start": v(4.85, 7.91) * mm, "end": v(4.96, 7.83) * mm});
            skLineSegment(sketch, "E2637.425", {"start": v(4.96, 7.83) * mm, "end": v(5.06, 7.75) * mm});
            skLineSegment(sketch, "E2637.426", {"start": v(5.06, 7.75) * mm, "end": v(5.16, 7.67) * mm});
            skLineSegment(sketch, "E2637.427", {"start": v(5.16, 7.67) * mm, "end": v(5.26, 7.59) * mm});
            skLineSegment(sketch, "E2637.428", {"start": v(5.26, 7.59) * mm, "end": v(5.36, 7.5) * mm});
            skLineSegment(sketch, "E2637.429", {"start": v(5.36, 7.5) * mm, "end": v(5.46, 7.42) * mm});
            skLineSegment(sketch, "E2637.430", {"start": v(5.46, 7.42) * mm, "end": v(5.56, 7.33) * mm});
            skLineSegment(sketch, "E2637.431", {"start": v(5.56, 7.33) * mm, "end": v(5.67, 7.24) * mm});
            skLineSegment(sketch, "E2637.432", {"start": v(5.67, 7.24) * mm, "end": v(5.77, 7.15) * mm});
            skLineSegment(sketch, "E2637.433", {"start": v(5.77, 7.15) * mm, "end": v(5.87, 7.06) * mm});
            skLineSegment(sketch, "E2637.434", {"start": v(5.87, 7.06) * mm, "end": v(5.97, 6.96) * mm});
            skLineSegment(sketch, "E2637.435", {"start": v(5.97, 6.96) * mm, "end": v(6.07, 6.87) * mm});
            skLineSegment(sketch, "E2637.436", {"start": v(6.07, 6.87) * mm, "end": v(6.17, 6.77) * mm});
            skLineSegment(sketch, "E2637.437", {"start": v(6.17, 6.77) * mm, "end": v(6.27, 6.68) * mm});
            skLineSegment(sketch, "E2637.438", {"start": v(6.27, 6.68) * mm, "end": v(6.38, 6.58) * mm});
            skLineSegment(sketch, "E2637.439", {"start": v(6.38, 6.58) * mm, "end": v(6.48, 6.48) * mm});
            skLineSegment(sketch, "E2637.440", {"start": v(6.48, 6.48) * mm, "end": v(6.58, 6.38) * mm});
            skLineSegment(sketch, "E2637.441", {"start": v(6.58, 6.38) * mm, "end": v(6.68, 6.27) * mm});
            skLineSegment(sketch, "E2637.442", {"start": v(6.68, 6.27) * mm, "end": v(6.77, 6.17) * mm});
            skLineSegment(sketch, "E2637.443", {"start": v(6.77, 6.17) * mm, "end": v(6.87, 6.07) * mm});
            skLineSegment(sketch, "E2637.444", {"start": v(6.87, 6.07) * mm, "end": v(6.96, 5.97) * mm});
            skLineSegment(sketch, "E2637.445", {"start": v(6.96, 5.97) * mm, "end": v(7.06, 5.87) * mm});
            skLineSegment(sketch, "E2637.446", {"start": v(7.06, 5.87) * mm, "end": v(7.15, 5.77) * mm});
            skLineSegment(sketch, "E2637.447", {"start": v(7.15, 5.77) * mm, "end": v(7.24, 5.67) * mm});
            skLineSegment(sketch, "E2637.448", {"start": v(7.24, 5.67) * mm, "end": v(7.33, 5.56) * mm});
            skLineSegment(sketch, "E2637.449", {"start": v(7.33, 5.56) * mm, "end": v(7.42, 5.46) * mm});
            skLineSegment(sketch, "E2637.450", {"start": v(7.42, 5.46) * mm, "end": v(7.5, 5.36) * mm});
            skLineSegment(sketch, "E2637.451", {"start": v(7.5, 5.36) * mm, "end": v(7.59, 5.26) * mm});
            skLineSegment(sketch, "E2637.452", {"start": v(7.59, 5.26) * mm, "end": v(7.67, 5.16) * mm});
            skLineSegment(sketch, "E2637.453", {"start": v(7.67, 5.16) * mm, "end": v(7.75, 5.06) * mm});
            skLineSegment(sketch, "E2637.454", {"start": v(7.75, 5.06) * mm, "end": v(7.83, 4.96) * mm});
            skLineSegment(sketch, "E2637.455", {"start": v(7.83, 4.96) * mm, "end": v(7.91, 4.85) * mm});
            skLineSegment(sketch, "E2637.456", {"start": v(7.91, 4.85) * mm, "end": v(8, 4.75) * mm});
            skLineSegment(sketch, "E2637.457", {"start": v(8, 4.75) * mm, "end": v(8.07, 4.65) * mm});
            skLineSegment(sketch, "E2637.458", {"start": v(8.07, 4.65) * mm, "end": v(8.15, 4.55) * mm});
            skLineSegment(sketch, "E2637.459", {"start": v(8.15, 4.55) * mm, "end": v(8.22, 4.45) * mm});
            skLineSegment(sketch, "E2637.460", {"start": v(8.22, 4.45) * mm, "end": v(8.3, 4.35) * mm});
            skLineSegment(sketch, "E2637.461", {"start": v(8.3, 4.35) * mm, "end": v(8.37, 4.24) * mm});
            skLineSegment(sketch, "E2637.462", {"start": v(8.37, 4.24) * mm, "end": v(8.44, 4.14) * mm});
            skLineSegment(sketch, "E2637.463", {"start": v(8.44, 4.14) * mm, "end": v(8.5, 4.04) * mm});
            skLineSegment(sketch, "E2637.464", {"start": v(8.5, 4.04) * mm, "end": v(8.58, 3.94) * mm});
            skLineSegment(sketch, "E2637.465", {"start": v(8.58, 3.94) * mm, "end": v(8.65, 3.84) * mm});
            skLineSegment(sketch, "E2637.466", {"start": v(8.65, 3.84) * mm, "end": v(8.71, 3.74) * mm});
            skLineSegment(sketch, "E2637.467", {"start": v(8.71, 3.74) * mm, "end": v(8.78, 3.63) * mm});
            skLineSegment(sketch, "E2637.468", {"start": v(8.78, 3.63) * mm, "end": v(8.84, 3.53) * mm});
            skLineSegment(sketch, "E2637.469", {"start": v(8.84, 3.53) * mm, "end": v(8.9, 3.43) * mm});
            skLineSegment(sketch, "E2637.470", {"start": v(8.9, 3.43) * mm, "end": v(8.97, 3.33) * mm});
            skLineSegment(sketch, "E2637.471", {"start": v(8.97, 3.33) * mm, "end": v(9.03, 3.23) * mm});
            skLineSegment(sketch, "E2637.472", {"start": v(9.03, 3.23) * mm, "end": v(9.09, 3.13) * mm});
            skLineSegment(sketch, "E2637.473", {"start": v(9.09, 3.13) * mm, "end": v(9.15, 3.02) * mm});
            skLineSegment(sketch, "E2637.474", {"start": v(9.15, 3.02) * mm, "end": v(9.2, 2.92) * mm});
            skLineSegment(sketch, "E2637.475", {"start": v(9.2, 2.92) * mm, "end": v(9.26, 2.82) * mm});
            skLineSegment(sketch, "E2637.476", {"start": v(9.26, 2.82) * mm, "end": v(9.32, 2.72) * mm});
            skLineSegment(sketch, "E2637.477", {"start": v(9.32, 2.72) * mm, "end": v(9.37, 2.62) * mm});
            skLineSegment(sketch, "E2637.478", {"start": v(9.37, 2.62) * mm, "end": v(9.42, 2.51) * mm});
            skLineSegment(sketch, "E2637.479", {"start": v(9.42, 2.51) * mm, "end": v(9.47, 2.41) * mm});
            skLineSegment(sketch, "E2637.480", {"start": v(9.47, 2.41) * mm, "end": v(9.52, 2.3) * mm});
            skLineSegment(sketch, "E2637.481", {"start": v(9.52, 2.3) * mm, "end": v(9.57, 2.2) * mm});
            skLineSegment(sketch, "E2637.482", {"start": v(9.57, 2.2) * mm, "end": v(9.62, 2.1) * mm});
            skLineSegment(sketch, "E2637.483", {"start": v(9.62, 2.1) * mm, "end": v(9.67, 2) * mm});
            skLineSegment(sketch, "E2637.484", {"start": v(9.67, 2) * mm, "end": v(9.71, 1.9) * mm});
            skLineSegment(sketch, "E2637.485", {"start": v(9.71, 1.9) * mm, "end": v(9.76, 1.8) * mm});
            skLineSegment(sketch, "E2637.486", {"start": v(9.76, 1.8) * mm, "end": v(9.8, 1.7) * mm});
            skLineSegment(sketch, "E2637.487", {"start": v(9.8, 1.7) * mm, "end": v(9.84, 1.6) * mm});
            skLineSegment(sketch, "E2637.488", {"start": v(9.84, 1.6) * mm, "end": v(9.88, 1.49) * mm});
            skLineSegment(sketch, "E2637.489", {"start": v(9.88, 1.49) * mm, "end": v(9.92, 1.39) * mm});
            skLineSegment(sketch, "E2637.490", {"start": v(9.92, 1.39) * mm, "end": v(9.96, 1.28) * mm});
            skLineSegment(sketch, "E2637.491", {"start": v(9.96, 1.28) * mm, "end": v(10, 1.18) * mm});
            skLineSegment(sketch, "E2637.492", {"start": v(10, 1.18) * mm, "end": v(10.03, 1.08) * mm});
            skLineSegment(sketch, "E2637.493", {"start": v(10.03, 1.08) * mm, "end": v(10.06, 0.97) * mm});
            skLineSegment(sketch, "E2637.494", {"start": v(10.06, 0.97) * mm, "end": v(10.09, 0.87) * mm});
            skLineSegment(sketch, "E2637.495", {"start": v(10.09, 0.87) * mm, "end": v(10.12, 0.76) * mm});
            skLineSegment(sketch, "E2637.496", {"start": v(10.12, 0.76) * mm, "end": v(10.14, 0.66) * mm});
            skLineSegment(sketch, "E2637.497", {"start": v(10.14, 0.66) * mm, "end": v(10.17, 0.55) * mm});
            skLineSegment(sketch, "E2637.498", {"start": v(10.17, 0.55) * mm, "end": v(10.2, 0.45) * mm});
            skLineSegment(sketch, "E2637.499", {"start": v(10.2, 0.45) * mm, "end": v(10.21, 0.34) * mm});
            skLineSegment(sketch, "E2637.500", {"start": v(10.21, 0.34) * mm, "end": v(10.23, 0.23) * mm});
            skLineSegment(sketch, "E2637.501", {"start": v(10.23, 0.23) * mm, "end": v(10.24, 0.12) * mm});
            skLineSegment(sketch, "E2637.502", {"start": v(10.24, 0.12) * mm, "end": v(10.25, 0) * mm});
            skLineSegment(sketch, "E2637.503", {"start": v(10.25, 0) * mm, "end": v(10.24, -0.12) * mm});
            skSolve(sketch);
        }
        {
            var Q0;
            Q0=makeQuery(id+"F14.imprint","IMPRINT",FACE,{"disambiguationData":[TD([[makeQuery(id+"F14.imprint","IMPRINT",EDGE,{"derivedFrom":sQuery(id+"F14.wireOp",EDGE,"E2635.4")}),1.0]])]});
            extrude(context, id + "F15", {"entities" : qUnion([Q0]), "operationType" : NewBodyOperationType.REMOVE, "oppositeDirection" : true, "depth" : .5 * mm});
        }
    });
